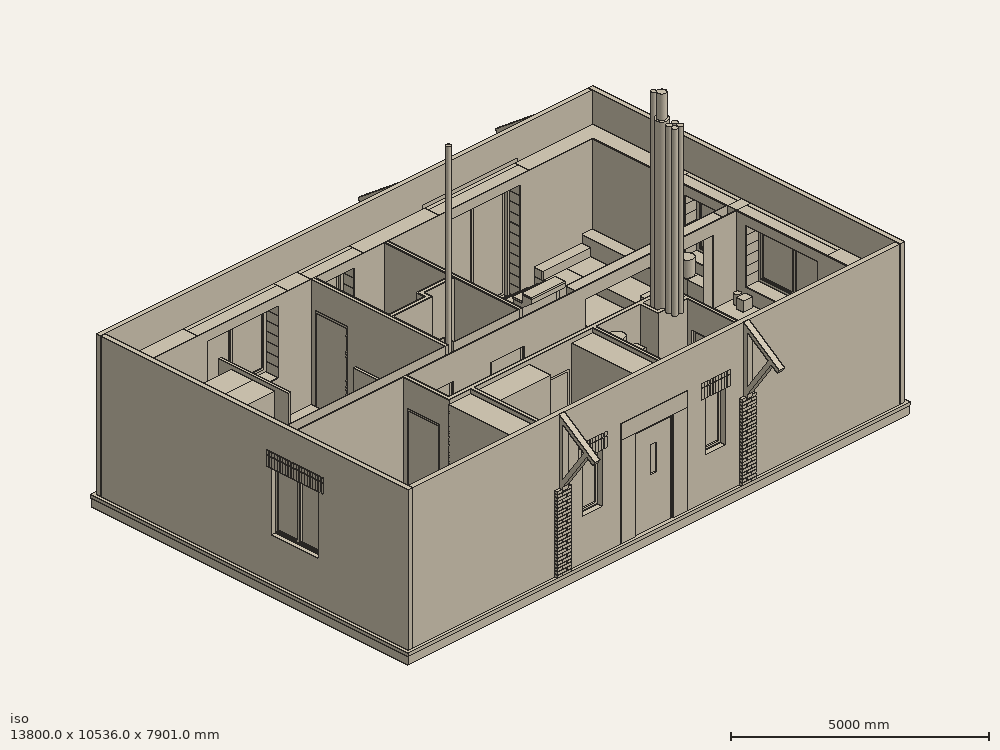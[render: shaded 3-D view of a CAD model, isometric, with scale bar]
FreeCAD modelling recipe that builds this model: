
FCSTD DOCUMENT  (FreeCAD 0.19R)
Label: 2bedr_dev_221121_BIM_mod
License: All rights reserved
LicenseURL: http://en.wikipedia.org/wiki/All_rights_reserved
objects: Part::Part2DObjectPython×664, Part::FeaturePython×646, App::FeaturePython×168, App::GeometryPython×80, App::DocumentObjectGroupPython×73, Sketcher::SketchObject×64, Part::MultiCommon×53, Part::Box×38, Part::Extrusion×36, Part::Cut×35, TechDraw::DrawViewAnnotation×32, Part::MultiFuse×26, App::MaterialObjectPython×21, TechDraw::DrawLeaderLine×17, Part::Feature×16, App::DocumentObjectGroup×11, TechDraw::DrawSVGTemplate×7, TechDraw::DrawPage×7, TechDraw::DrawViewImage×6, Part::Cylinder×5, +8 more types
note: 1669 computed .brp shape members not serialized (recipe doc carries the construction recipe); baked Part::Feature solids carry a one-line shape summary decoded from their .brp

FEATURE [Part::Part2DObjectPython] Rectangle2169  label="Д-105-254-001"  # Draft 2D object (typed FeaturePython)
  ChamferSize = 0
  Columns = 1
  FilletRadius = 0
  Height = 410
  Length = 1050
  MakeFace = true
  Placement = pos=(5670,-435,0) rot=(0,0,1;0rad)
  Rows = 1
FEATURE [Part::Part2DObjectPython] Rectangle2231  label="ОК-66-001"  # Draft 2D object (typed FeaturePython)
  ChamferSize = 0
  Columns = 1
  FilletRadius = 0
  Height = 410
  Length = 660
  MakeFace = true
  Placement = pos=(7555,-435,0) rot=(0,0,1;0rad)
  Rows = 1
FEATURE [Part::Part2DObjectPython] Rectangle2230  label="ОК-66-002"  # Draft 2D object (typed FeaturePython)
  ChamferSize = 0
  Columns = 1
  FilletRadius = 0
  Height = 410
  Length = 660
  MakeFace = true
  Placement = pos=(4175,-435,0) rot=(0,0,1;0rad)
  Rows = 1
FEATURE [App::FeaturePython] Dimension001  # Draft dimension (typed FeaturePython)
  Diameter = false
  Dimline = (13900,-300,0)
  Direction = (0,0,0)
  Distance = 7510
  End = (12550,7485,0)
  Normal = (0,0,1)
  Start = (12550,-25,0)
FEATURE [App::FeaturePython] Dimension  # Draft dimension (typed FeaturePython)
  Diameter = false
  Dimline = (13600,-1100,0)
  Direction = (0,0,0)
  Distance = 12580
  End = (12550,-10,0)
  Normal = (0,0,1)
  Start = (-30,-10,0)
FEATURE [Part::Part2DObjectPython] Rectangle2234  # Draft 2D object (typed FeaturePython)
  ChamferSize = 0
  Columns = 1
  FilletRadius = 0
  Height = 1500
  Length = 3000
  MakeFace = false
  Placement = pos=(5125,-1770,0) rot=(0,0,1;0rad)
  Rows = 1
FEATURE [Part::FeaturePython] Structure016  label="Проём-ОК-66-002"  # Arch/BIM 52 (typed FeaturePython)
  Base = -> Rectangle2230
  FaceMaker = 0
  Height = 1386
  HorizontalArea = 270600
  IfcData = complex_attributes={"OwnerHistory": {}, "IsNestedBy": {}, "IsDecomposedBy": {}, "IsDefinedBy": {}, "ObjectPlacement": {}, "Representation":... (+4 chars omitted)
  IfcType = 52
  Length = 0
  MoveBase = false
  MoveWithHost = false
  Nodes = (2) [(4618,-185,0),(4618,-185,1386)]
  NodesOffset = 0
  Normal = (0,0,0)
  PerimeterLength = 2140
  Placement = pos=(0,0,955) rot=(0,0,1;0rad)
  VerticalArea = 2966040
  Width = 100
FEATURE [Part::FeaturePython] Structure017  label="Проём-ОК-66-001"  # Arch/BIM 52 (typed FeaturePython)
  Base = -> Rectangle2231
  FaceMaker = 0
  Height = 1386
  HorizontalArea = 270600
  IfcData = complex_attributes={"OwnerHistory": {}, "IsNestedBy": {}, "IsDecomposedBy": {}, "IsDefinedBy": {}, "ObjectPlacement": {}, "Representation":... (+4 chars omitted)
  IfcType = 52
  Length = 0
  MoveBase = false
  MoveWithHost = false
  Nodes = (2) [(7885,-230,0),(7885,-230,1386)]
  NodesOffset = 0
  Normal = (0,0,0)
  PerimeterLength = 2140
  Placement = pos=(0,0,955) rot=(0,0,1;0rad)
  VerticalArea = 2966040
  Width = 100
FEATURE [Part::FeaturePython] Structure019  label="Проём-Д-105-254-001"  # Arch/BIM 52 (typed FeaturePython)
  Base = -> Rectangle2169
  FaceMaker = 0
  Height = 2541
  HorizontalArea = 430500
  IfcData = complex_attributes={"OwnerHistory": {}, "IsNestedBy": {}, "IsDecomposedBy": {}, "IsDefinedBy": {}, "ObjectPlacement": {}, "Representation":... (+4 chars omitted)
  IfcType = 52
  Length = 0
  MoveBase = false
  MoveWithHost = false
  Nodes = (2) [(6195,-230,0),(6195,-230,2541)]
  NodesOffset = 0
  Normal = (0,0,0)
  PerimeterLength = 2920
  Placement = pos=(0,0,-200) rot=(0,0,1;0rad)
  VerticalArea = 7419720
  Width = 100
FEATURE [Part::Part2DObjectPython] Line1049  # Draft 2D object (typed FeaturePython)
  ChamferSize = 0
  Closed = true
  End = (-50,3680,0)
  FilletRadius = 0
  Length = 12620
  MakeFace = false
  Placement = pos=(4290,10400,0) rot=(0,0,1;1.5708rad)
  Points = (2) [(-6720,-8280,0),(-6720,4340,0)]
  Start = (12570,3680,0)
  Subdivisions = 0
FEATURE [Part::Part2DObjectPython] Line1054  # Draft 2D object (typed FeaturePython)
  ChamferSize = 0
  Closed = true
  End = (4870,7505,0)
  FilletRadius = 0
  Length = 3700
  MakeFace = false
  Placement = pos=(9650,5690,0) rot=(0,0,1;0rad)
  Points = (2) [(-4780,-1885,0),(-4780,1815,0)]
  Start = (4870,3805,0)
  Subdivisions = 0
FEATURE [Sketcher::SketchObject] Sketch231  label="Профиль ПНО 120-8"
  FullyConstrained = false
  Placement = pos=(0,0,0) rot=(1,0,0;1.5708rad)
  sketch-geometry (19):
    g0: LineSegment StartX=0 StartY=0 StartZ=0 EndX=1190 EndY=0 EndZ=0
    g1: LineSegment StartX=1190 StartY=0 StartZ=0 EndX=1190 EndY=160 EndZ=0
    g2: LineSegment StartX=1190 StartY=160 StartZ=0 EndX=0 EndY=160 EndZ=0
    g3: LineSegment StartX=0 StartY=160 StartZ=0 EndX=0 EndY=0 EndZ=0
    g4: Circle CenterX=100 CenterY=80 CenterZ=0 NormalX=0 NormalY=0 NormalZ=1 AngleXU=0 Radius=50
    g5: Circle CenterX=240 CenterY=80 CenterZ=0 NormalX=0 NormalY=0 NormalZ=1 AngleXU=0 Radius=50
    g6: LineSegment StartX=100 StartY=80 StartZ=0 EndX=240 EndY=80 EndZ=0
    g7: Circle CenterX=380 CenterY=80 CenterZ=0 NormalX=0 NormalY=0 NormalZ=1 AngleXU=0 Radius=50
    g8: LineSegment StartX=240 StartY=80 StartZ=0 EndX=380 EndY=80 EndZ=0
    g9: Circle CenterX=520 CenterY=80 CenterZ=0 NormalX=0 NormalY=0 NormalZ=1 AngleXU=0 Radius=50
    g10: LineSegment StartX=380 StartY=80 StartZ=0 EndX=520 EndY=80 EndZ=0
    g11: Circle CenterX=660 CenterY=80 CenterZ=0 NormalX=0 NormalY=0 NormalZ=1 AngleXU=0 Radius=50
    g12: LineSegment StartX=520 StartY=80 StartZ=0 EndX=660 EndY=80 EndZ=0
    g13: Circle CenterX=800 CenterY=80 CenterZ=0 NormalX=0 NormalY=0 NormalZ=1 AngleXU=0 Radius=50
    g14: LineSegment StartX=660 StartY=80 StartZ=0 EndX=800 EndY=80 EndZ=0
    g15: Circle CenterX=940 CenterY=80 CenterZ=0 NormalX=0 NormalY=0 NormalZ=1 AngleXU=0 Radius=50
    g16: LineSegment StartX=800 StartY=80 StartZ=0 EndX=940 EndY=80 EndZ=0
    g17: Circle CenterX=1080 CenterY=80 CenterZ=0 NormalX=0 NormalY=0 NormalZ=1 AngleXU=0 Radius=50
    g18: LineSegment StartX=940 StartY=80 StartZ=0 EndX=1080 EndY=80 EndZ=0
  constraints (49):
    c: Coincident(g0,g1)
    c: Coincident(g1,g2)
    c: Coincident(g2,g3)
    c: Coincident(g3,g0)
    c: Horizontal(g0)
    c: Horizontal(g2)
    c: Vertical(g1)
    c: Vertical(g3)
    c: Coincident(g0,g-1)
    c: DistanceY(g3,g3) = 160
    c: DistanceX(g2,g2) = 1190
    c: Diameter(g4) = 100
    c: DistanceY(g4,g2) = 80
    c: Diameter(g5) = 100
    c: Coincident(g4,g6)
    c: Coincident(g5,g6)
    c: Distance(g6) = 140
    c: Angle(g6) = 0
    c: Diameter(g7) = 100
    c: Coincident(g5,g8)
    c: Coincident(g7,g8)
    c: Equal(g6,g8)
    c: Parallel(g8,g6)
    c: Diameter(g9) = 100
    c: Coincident(g7,g10)
    c: Coincident(g9,g10)
    c: Equal(g6,g10)
    c: Parallel(g10,g6)
    c: Diameter(g11) = 100
    c: Coincident(g9,g12)
    c: Coincident(g11,g12)
    c: Equal(g6,g12)
    c: Parallel(g12,g6)
    c: Diameter(g13) = 100
    c: Coincident(g11,g14)
    c: Coincident(g13,g14)
    c: Equal(g6,g14)
    c: Parallel(g14,g6)
    c: Diameter(g15) = 100
    c: Coincident(g13,g16)
    c: Coincident(g15,g16)
    c: Equal(g6,g16)
    c: Parallel(g16,g6)
    c: Diameter(g17) = 100
    c: Coincident(g15,g18)
    c: Coincident(g17,g18)
    c: Equal(g6,g18)
    c: Parallel(g18,g6)
    c: DistanceX(g2,g4) = 100
FEATURE [Part::Part2DObjectPython] Line1074  label="ось фундамента внутр.стены"  # Draft 2D object (typed FeaturePython)
  ChamferSize = 0
  Closed = true
  End = (3855,9350,0)
  FilletRadius = 0
  Length = 5200
  MakeFace = false
  Placement = pos=(2155,2900,0) rot=(0,0,1;1.5708rad)
  Points = (2) [(1250,-1700,0),(6450,-1700,0)]
  Start = (3855,4150,0)
  Subdivisions = 0
FEATURE [Part::FeaturePython] Wall037  label="фундамент внутр.стена01"  # Arch/BIM 166 (typed FeaturePython)
  Align = 2
  Area = 2.6e+06
  Base = -> Line1074
  BlockHeight = 0
  BlockLength = 0
  CountBroken = 0
  CountEntire = 0
  Face = 0
  Height = 500
  HorizontalArea = 1.3e+06
  IfcType = 166
  Joint = 0
  Length = 5200
  MakeBlocks = false
  MoveBase = false
  MoveWithHost = false
  Normal = (0,0,-1)
  OffsetFirst = 0
  OffsetSecond = 0
  PerimeterLength = 10900
  Placement = pos=(0,0,-180) rot=(0,0,1;0rad)
  PredefinedType = 0
  VerticalArea = 5.45e+06
  Width = 250
FEATURE [Part::FeaturePython] Wall046  label="утепл фунд. внешней.стены 002"  # Arch/BIM 166 (typed FeaturePython)
  Align = 1
  Area = 28488000
  BlockHeight = 600
  BlockLength = 600
  CountBroken = 1
  CountEntire = 0
  Face = 0
  Height = 600
  HorizontalArea = 3798400
  IfcType = 166
  Joint = 1
  Length = 47480
  MakeBlocks = true
  MoveBase = false
  MoveWithHost = false
  Normal = (0,0,-1)
  OffsetFirst = 0
  OffsetSecond = 0
  PerimeterLength = 95120
  Placement = pos=(0,0,-380) rot=(0,0,1;0rad)
  PredefinedType = 0
  VerticalArea = 57072000
  Width = 80
FEATURE [Part::FeaturePython] Wall047  label="утепл отмостки 001"  # Arch/BIM 166 (typed FeaturePython)
  Align = 1
  Area = 2374000
  BlockHeight = 600
  BlockLength = 1200
  CountBroken = 1
  CountEntire = 0
  Face = 0
  Height = 50
  HorizontalArea = 28488000
  IfcType = 166
  Joint = 1
  Length = 47480
  MakeBlocks = true
  MoveBase = false
  MoveWithHost = false
  Normal = (0,0,-1)
  Offset = 80
  OffsetFirst = 0
  OffsetSecond = 0
  PerimeterLength = 96160
  Placement = pos=(0,0,-930) rot=(0,0,1;0rad)
  PredefinedType = 0
  VerticalArea = 4808000
  Width = 600
FEATURE [Part::Part2DObjectPython] Circle071  # Draft 2D object (typed FeaturePython)
  FirstAngle = 0
  LastAngle = 0
  MakeFace = false
  Placement = pos=(8500,900,0) rot=(0,0,1;0rad)
  Radius = 580
FEATURE [Part::Part2DObjectPython] Circle072  # Draft 2D object (typed FeaturePython)
  FirstAngle = 0
  LastAngle = 0
  MakeFace = false
  Placement = pos=(8500,900,0) rot=(0,0,1;0rad)
  Radius = 500
FEATURE [Part::Part2DObjectPython] Circle073  label="люк_контур 001"  # Draft 2D object (typed FeaturePython)
  FirstAngle = 0
  LastAngle = 0
  MakeFace = false
  Placement = pos=(8500,1000,0) rot=(0,0,1;0rad)
  Radius = 350
FEATURE [Part::FeaturePython] Structure041  label="кольцо с днищем ДК-10.9 внутр."  # Arch/BIM 52 (typed FeaturePython)
  Base = -> Circle072
  FaceMaker = 0
  Height = 800
  HorizontalArea = 785398
  IfcData = complex_attributes={"OwnerHistory": {}, "IsNestedBy": {}, "IsDecomposedBy": {}, "IsDefinedBy": {}, "ObjectPlacement": {}, "Representation":... (+4 chars omitted)
  IfcType = 52
  Length = 0
  MoveBase = false
  MoveWithHost = false
  Nodes = (2) [(8500,900,0),(8500,900,-800)]
  NodesOffset = 0
  Normal = (0,0,-1)
  PerimeterLength = 3141.59
  Placement = pos=(0,0,-300) rot=(0,0,1;0rad)
  VerticalArea = 2.51327e+06
  Width = 100
FEATURE [Part::FeaturePython] Structure040  label="кольцо с днищем ДК-10.9 габарит"  # Arch/BIM 52 (typed FeaturePython)
  Base = -> Circle071
  FaceMaker = 0
  Height = 900
  HorizontalArea = 1.05683e+06
  IfcData = complex_attributes={"OwnerHistory": {}, "IsNestedBy": {}, "IsDecomposedBy": {}, "IsDefinedBy": {}, "ObjectPlacement": {}, "Representation":... (+4 chars omitted)
  IfcType = 52
  Length = 0
  MoveBase = false
  MoveWithHost = false
  Nodes = (2) [(8500,900,0),(8500,900,-900)]
  NodesOffset = 0
  Normal = (0,0,-1)
  PerimeterLength = 3644.25
  Placement = pos=(0,0,-300) rot=(0,0,1;0rad)
  Subtractions = -> [Structure041]
  VerticalArea = 5.7931e+06
  Width = 100
FEATURE [Part::FeaturePython] Structure044  label="люк контур Д700"  # Arch/BIM 52 (typed FeaturePython)
  Base = -> Circle073
  FaceMaker = 0
  Height = 300
  HorizontalArea = 384845
  IfcData = complex_attributes={"OwnerHistory": {}, "IsNestedBy": {}, "IsDecomposedBy": {}, "IsDefinedBy": {}, "ObjectPlacement": {}, "Representation":... (+4 chars omitted)
  IfcType = 52
  Length = 0
  MoveBase = false
  MoveWithHost = false
  Nodes = (2) [(8500,1000,0),(8500,1000,-300)]
  NodesOffset = 0
  Normal = (0,0,-1)
  PerimeterLength = 2199.11
  VerticalArea = 659734
  Width = 100
FEATURE [Part::FeaturePython] Structure043  label="крышка ПП10"  # Arch/BIM 52 (typed FeaturePython)
  Base = -> Circle071
  FaceMaker = 0
  Height = 100
  HorizontalArea = 671987
  IfcData = complex_attributes={"OwnerHistory": {}, "IsNestedBy": {}, "IsDecomposedBy": {}, "IsDefinedBy": {}, "ObjectPlacement": {}, "Representation":... (+4 chars omitted)
  IfcType = 52
  Length = 0
  MoveBase = false
  MoveWithHost = false
  Nodes = (2) [(8500,900,0),(8500,900,-100)]
  NodesOffset = 0
  Normal = (0,0,-1)
  PerimeterLength = 3644.25
  Placement = pos=(0,0,-200) rot=(0,0,1;0rad)
  Subtractions = -> [Structure044]
  VerticalArea = 584336
  Width = 100
FEATURE [App::GeometryPython] BuildingPart015  label="Колодец d1000 (ввод воды и канализации)"  # Arch/BIM 52 (typed FeaturePython)
  Area = 0
  Group = -> [Structure040,Structure043]
  Height = 0
  HeightPropagate = true
  IfcData = complex_attributes={"OwnerHistory": {}, "IsNestedBy": {}, "IsDecomposedBy": {}, "IsDefinedBy": {}, "ObjectPlacement": {}, "Representation":... (+4 chars omitted)
  IfcType = 52
  LevelOffset = 0
FEATURE [Part::Part2DObjectPython] Line1077  # Draft 2D object (typed FeaturePython)
  ChamferSize = 0
  Closed = true
  End = (-50,-45,0)
  FilletRadius = 0
  Length = 12620
  MakeFace = false
  Placement = pos=(12060,265,0) rot=(0,0,1;0rad)
  Points = (2) [(510,-310,0),(-12110,-310,0)]
  Start = (12570,-45,0)
  Subdivisions = 0
FEATURE [Part::Part2DObjectPython] Rectangle2286  # Draft 2D object (typed FeaturePython)
  ChamferSize = 0
  Columns = 1
  FilletRadius = 0
  Height = 5190
  Length = 9350
  MakeFace = false
  Placement = pos=(1950,2210,0) rot=(0,0,1;0rad)
  Rows = 1
FEATURE [Part::FeaturePython] Structure049  label="вычитаемый объём 002"  # Arch/BIM 52 (typed FeaturePython)
  FaceMaker = 0
  Height = 4000
  HorizontalArea = 3.20922e+07
  IfcData = complex_attributes={"OwnerHistory": {}, "IsNestedBy": {}, "IsDecomposedBy": {}, "IsDefinedBy": {}, "ObjectPlacement": {}, "Representation":... (+4 chars omitted)
  IfcType = 52
  Length = 0
  MoveBase = false
  MoveWithHost = false
  Nodes = (2) [(506.667,3830,0),(506.667,3830,4000)]
  NodesOffset = 0
  Normal = (0,0,1)
  PerimeterLength = 27353
  Placement = pos=(0,0,3160) rot=(0,0,1;0rad)
  VerticalArea = 1.09412e+08
  Width = 100
FEATURE [Part::FeaturePython] Structure050  label="вычитаемый объём 004"  # Arch/BIM 52 (typed FeaturePython)
  FaceMaker = 0
  Height = 4000
  HorizontalArea = 5.56586e+07
  IfcData = complex_attributes={"OwnerHistory": {}, "IsNestedBy": {}, "IsDecomposedBy": {}, "IsDefinedBy": {}, "ObjectPlacement": {}, "Representation":... (+4 chars omitted)
  IfcType = 52
  Length = 0
  MoveBase = false
  MoveWithHost = false
  Nodes = (2) [(6040,886.738,0),(6040,886.738,4000)]
  NodesOffset = 0
  Normal = (0,0,1)
  PerimeterLength = 35673
  Placement = pos=(0,0,3160) rot=(0,0,1;0rad)
  VerticalArea = 1.42692e+08
  Width = 100
FEATURE [Part::FeaturePython] Structure051  label="вычитаемый объём 003"  # Arch/BIM 52 (typed FeaturePython)
  FaceMaker = 0
  Height = 4000
  HorizontalArea = 32092225
  IfcData = complex_attributes={"OwnerHistory": {}, "IsNestedBy": {}, "IsDecomposedBy": {}, "IsDefinedBy": {}, "ObjectPlacement": {}, "Representation":... (+4 chars omitted)
  IfcType = 52
  Length = 0
  MoveBase = false
  MoveWithHost = false
  Nodes = (2) [(12481.7,4805,0),(12481.7,4805,4000)]
  NodesOffset = 0
  Normal = (0,0,1)
  PerimeterLength = 27353
  Placement = pos=(0,0,3160) rot=(0,0,1;0rad)
  VerticalArea = 1.09412e+08
  Width = 100
FEATURE [App::FeaturePython] Dimension003  # Draft dimension (typed FeaturePython)
  Diameter = false
  Dimline = (14100,-1000,0)
  Direction = (0,0,0)
  Distance = 8570
  End = (13080,8015,0)
  Normal = (0,0,1)
  Start = (13080,-555,0)
FEATURE [Sketcher::SketchObject] Sketch248
  FullyConstrained = true
  Placement = pos=(3860,3535,0) rot=(1,0,0;1.5708rad)
  sketch-geometry (8):
    g0: LineSegment StartX=0 StartY=0 StartZ=0 EndX=900 EndY=0 EndZ=0
    g1: LineSegment StartX=900 StartY=0 StartZ=0 EndX=900 EndY=2150 EndZ=0
    g2: LineSegment StartX=900 StartY=2150 StartZ=0 EndX=0 EndY=2150 EndZ=0
    g3: LineSegment StartX=0 StartY=2150 StartZ=0 EndX=0 EndY=0 EndZ=0
    g4: LineSegment StartX=50 StartY=0 StartZ=0 EndX=850 EndY=0 EndZ=0
    g5: LineSegment StartX=850 StartY=0 StartZ=0 EndX=850 EndY=2100 EndZ=0
    g6: LineSegment StartX=850 StartY=2100 StartZ=0 EndX=50 EndY=2100 EndZ=0
    g7: LineSegment StartX=50 StartY=2100 StartZ=0 EndX=50 EndY=0 EndZ=0
  constraints (23):
    c: Coincident(g0,g1)
    c: Coincident(g1,g2)
    c: Coincident(g2,g3)
    c: Coincident(g3,g0)
    c: Horizontal(g0)
    c: Horizontal(g2)
    c: Vertical(g1)
    c: Vertical(g3)
    c: Coincident(g4,g5)
    c: Coincident(g5,g6)
    c: Coincident(g6,g7)
    c: Coincident(g7,g4)
    c: Horizontal(g4)
    c: Horizontal(g6)
    c: Vertical(g5)
    c: Vertical(g7)
    c: DistanceY(g1) = 2150  'Height'
    c: DistanceX(g0) = 900  'Width'
    c: DistanceY(g6,g2) = 50  'Frame1'
    c: DistanceX(g2,g6) = 50  'Frame2'
    c: DistanceX(g4,g0) = 50  'Frame3'
    c: DistanceY(g0,g4) = 0
    c: Coincident(g0,g-1)
FEATURE [Sketcher::SketchObject] Sketch249  label="Профиль ПНО 100-6"
  FullyConstrained = false
  Placement = pos=(0,0,0) rot=(1,0,0;1.5708rad)
  sketch-geometry (15):
    g0: LineSegment StartX=0 StartY=0 StartZ=0 EndX=990 EndY=0 EndZ=0
    g1: LineSegment StartX=990 StartY=0 StartZ=0 EndX=990 EndY=160 EndZ=0
    g2: LineSegment StartX=990 StartY=160 StartZ=0 EndX=0 EndY=160 EndZ=0
    g3: LineSegment StartX=0 StartY=160 StartZ=0 EndX=0 EndY=0 EndZ=0
    g4: Circle CenterX=145 CenterY=80 CenterZ=0 NormalX=0 NormalY=0 NormalZ=1 AngleXU=0 Radius=50
    g5: Circle CenterX=285 CenterY=80 CenterZ=0 NormalX=0 NormalY=0 NormalZ=1 AngleXU=0 Radius=50
    g6: LineSegment StartX=145 StartY=80 StartZ=0 EndX=285 EndY=80 EndZ=0
    g7: Circle CenterX=425 CenterY=80 CenterZ=0 NormalX=0 NormalY=0 NormalZ=1 AngleXU=0 Radius=50
    g8: LineSegment StartX=285 StartY=80 StartZ=0 EndX=425 EndY=80 EndZ=0
    g9: Circle CenterX=565 CenterY=80 CenterZ=0 NormalX=0 NormalY=0 NormalZ=1 AngleXU=0 Radius=50
    g10: LineSegment StartX=425 StartY=80 StartZ=0 EndX=565 EndY=80 EndZ=0
    g11: Circle CenterX=705 CenterY=80 CenterZ=0 NormalX=0 NormalY=0 NormalZ=1 AngleXU=0 Radius=50
    g12: LineSegment StartX=565 StartY=80 StartZ=0 EndX=705 EndY=80 EndZ=0
    g13: Circle CenterX=845 CenterY=80 CenterZ=0 NormalX=0 NormalY=0 NormalZ=1 AngleXU=0 Radius=50
    g14: LineSegment StartX=705 StartY=80 StartZ=0 EndX=845 EndY=80 EndZ=0
  constraints (39):
    c: Coincident(g0,g1)
    c: Coincident(g1,g2)
    c: Coincident(g2,g3)
    c: Coincident(g3,g0)
    c: Horizontal(g0)
    c: Horizontal(g2)
    c: Vertical(g1)
    c: Vertical(g3)
    c: Coincident(g0,g-1)
    c: DistanceY(g3,g3) = 160
    c: DistanceX(g2,g2) = 990
    c: Diameter(g4) = 100
    c: DistanceY(g4,g2) = 80
    c: Diameter(g5) = 100
    c: Coincident(g4,g6)
    c: Coincident(g5,g6)
    c: Distance(g6) = 140
    c: Angle(g6) = 0
    c: Diameter(g7) = 100
    c: Coincident(g5,g8)
    c: Coincident(g7,g8)
    c: Equal(g6,g8)
    c: Parallel(g8,g6)
    c: Diameter(g9) = 100
    c: Coincident(g7,g10)
    c: Coincident(g9,g10)
    c: Equal(g6,g10)
    c: Parallel(g10,g6)
    c: Diameter(g11) = 100
    c: Coincident(g9,g12)
    c: Coincident(g11,g12)
    c: Equal(g6,g12)
    c: Parallel(g12,g6)
    c: Diameter(g13) = 100
    c: Coincident(g11,g14)
    c: Coincident(g13,g14)
    c: Equal(g6,g14)
    c: Parallel(g14,g6)
    c: DistanceX(g2,g4) = 145
FEATURE [Part::Part2DObjectPython] Wire460  label="границы участка"  # Draft 2D object (typed FeaturePython)
  ChamferSize = 0
  Closed = true
  End = (26167.8,29983.2,0)
  FilletRadius = 0
  Length = 156987
  MakeFace = false
  Placement = pos=(24404.1,-9481.8,0) rot=(0,0,1;0.025758rad)
  Points = (7) [(0,0,0),(-3118.22,176.296,0),(-9989.98,2199.83,0),(-22349.9,2518.26,0),(-33551.4,825.818,0),(-40981.4,39865.2,0),(2779.54,39406.5,0)]
  Start = (24404.1,-9481.8,0)
  Subdivisions = 0
FEATURE [Part::Part2DObjectPython] Rectangle2365  label="зона парковки-навес"  # Draft 2D object (typed FeaturePython)
  ChamferSize = 0
  Columns = 1
  FilletRadius = 0
  Height = 7000
  Length = 7000
  MakeFace = false
  Placement = pos=(17916.6,-6918.81,0) rot=(0,0,-1;0.068796rad)
  Rows = 1
FEATURE [Part::Part2DObjectPython] Wire463  label="граница по ограждению"  # Draft 2D object (typed FeaturePython)
  ChamferSize = 0
  Closed = true
  End = (5754.6,-6612.02,0)
  FilletRadius = 0
  Length = 153279
  MakeFace = false
  Placement = pos=(24847.4,-8209.78,0) rot=(0,0,1;0rad)
  Points = (6) [(14.0233,-1.17368,0),(2632.1,37116.3,0),(-41128.8,37575,0),(-34003,133.748,0),(-24492.8,1579.34,0),(-19092.8,1597.76,0)]
  Start = (24861.5,-8210.95,0)
  Subdivisions = 0
FEATURE [Part::FeaturePython] Structure133  label="грунт в границах участка"  # Arch/BIM 52 (typed FeaturePython)
  Base = -> Wire460
  FaceMaker = 0
  Height = 1000
  HorizontalArea = 1.47224e+09
  IfcData = complex_attributes={"OwnerHistory": {}, "IsNestedBy": {}, "IsDecomposedBy": {}, "IsDefinedBy": {}, "ObjectPlacement": {}, "Representation":... (+4 chars omitted)
  IfcType = 52
  Length = 0
  MoveBase = false
  MoveWithHost = false
  Nodes = (2) [(5892.5,11504.2,0),(5892.5,11504.2,-1000)]
  NodesOffset = 0
  Normal = (0,0,-1)
  PerimeterLength = 156987
  Placement = pos=(0,0,-320) rot=(0,0,1;0rad)
  VerticalArea = 1.56987e+08
  Width = 100
FEATURE [Part::Part2DObjectPython] Wire464  label="мауэрлат003"  # Draft 2D object (typed FeaturePython)
  ChamferSize = 0
  Closed = true
  End = (14568.5,-7412.72,0)
  FilletRadius = 0
  Length = 30000
  MakeFace = false
  Placement = pos=(20304,-1451.15,0) rot=(0,0,-1;0.229406rad)
  Points = (4) [(3770.46,-7109.62,0),(3770.46,-109.624,0),(-4229.54,-109.624,0),(-4229.54,-7109.62,0)]
  Start = (22359,-9231.91,0)
  Subdivisions = 0
FEATURE [Part::Part2DObjectPython] Rectangle2375  # Draft 2D object (typed FeaturePython)
  ChamferSize = 0
  Columns = 1
  FilletRadius = 0
  Height = 150
  Length = 800
  MakeFace = true
  Placement = pos=(-1461.06,-5083.09,0) rot=(0,0,-1;1.39508rad)
  Rows = 1
FEATURE [Part::Part2DObjectPython] Rectangle2376  # Draft 2D object (typed FeaturePython)
  ChamferSize = 0
  Columns = 1
  FilletRadius = 0
  Height = 150
  Length = 500
  MakeFace = true
  Placement = pos=(-6959.67,-6719.51,0) rot=(0,0,1;1.74651rad)
  Rows = 1
FEATURE [Part::Part2DObjectPython] Rectangle2377  # Draft 2D object (typed FeaturePython)
  ChamferSize = 0
  Columns = 1
  FilletRadius = 0
  Height = 2300
  Length = 6000
  MakeFace = false
  Placement = pos=(-1444.48,-4318.42,0) rot=(0,0,1;3.31731rad)
  Rows = 1
FEATURE [Part::FeaturePython] Roof011  label="Навес над парковкой"  # Arch/BIM 113 (typed FeaturePython)
  Angles = [90,10,90,10]
  Base = -> Wire464
  BorderLength = 0
  Face = 0
  Flip = false
  Heights = [0,617.144,0,617.144]
  HorizontalArea = 5.6e+07
  IdRel = [0,0,0,0]
  IfcType = 113
  MoveBase = false
  MoveWithHost = false
  Overhang = [0,0,0,0]
  PerimeterLength = 30000
  Placement = pos=(0,0,2500) rot=(0,0,1;0rad)
  PredefinedType = 0
  RidgeLength = 0
  Runs = [0,3500,0,3500]
  Thickness = [150,150,150,150]
  VerticalArea = 7.00644e+06
FEATURE [Part::FeaturePython] Structure135  label="Structure134"  # Arch/BIM 52 (typed FeaturePython)
  Base = -> Rectangle2375
  FaceMaker = 0
  Height = 1800
  HorizontalArea = 120000
  IfcData = complex_attributes={"OwnerHistory": {}, "IsNestedBy": {}, "IsDecomposedBy": {}, "IsDefinedBy": {}, "ObjectPlacement": {}, "Representation":... (+4 chars omitted)
  IfcType = 52
  Length = 0
  MoveBase = false
  MoveWithHost = false
  Nodes = (2) [(-35.6948,-25773.1,0),(-35.6948,-25773.1,1800)]
  NodesOffset = 0
  Normal = (0,0,0)
  PerimeterLength = 1900
  VerticalArea = 3.42e+06
  Width = 100
FEATURE [Part::FeaturePython] Structure136  label="Structure135"  # Arch/BIM 52 (typed FeaturePython)
  Base = -> Rectangle2376
  FaceMaker = 0
  Height = 600
  HorizontalArea = 75000
  IfcData = complex_attributes={"OwnerHistory": {}, "IsNestedBy": {}, "IsDecomposedBy": {}, "IsDefinedBy": {}, "ObjectPlacement": {}, "Representation":... (+4 chars omitted)
  IfcType = 52
  Length = 0
  MoveBase = false
  MoveWithHost = false
  Nodes = (2) [(1351.07,-25965.1,0),(1351.07,-25965.1,600)]
  NodesOffset = 0
  Normal = (0,0,0)
  PerimeterLength = 1300
  Placement = pos=(0,-4e-15,1240) rot=(0,0,1;0rad)
  VerticalArea = 780000
  Width = 100
FEATURE [Part::FeaturePython] Wall097  label="Wall007"  # Arch/BIM 166 (typed FeaturePython)
  Align = 1
  Area = 4.067e+07
  Base = -> Rectangle2377
  BlockHeight = 0
  BlockLength = 0
  CountBroken = 0
  CountEntire = 0
  Face = 0
  Height = 2450
  HorizontalArea = 2.595e+06
  IfcType = 166
  Joint = 0
  Length = 16600
  MakeBlocks = false
  MoveBase = false
  MoveWithHost = false
  Normal = (0,0,0)
  OffsetFirst = 0
  OffsetSecond = 0
  PerimeterLength = 12600
  Placement = pos=(0,0,-150) rot=(0,0,1;0rad)
  PredefinedType = 0
  Subtractions = -> [Structure136,Structure135]
  VerticalArea = 7.564e+07
  Width = 150
FEATURE [Sketcher::SketchObject] Sketch250  label="Габарит человека"
  FullyConstrained = false
  Placement = pos=(0,0,0) rot=(1,0,0;1.5708rad)
  sketch-geometry (21):
    g0: LineSegment StartX=-250 StartY=0 StartZ=0 EndX=250 EndY=0 EndZ=0
    g1: LineSegment StartX=250 StartY=0 StartZ=0 EndX=250 EndY=1750 EndZ=0
    g2: LineSegment StartX=250 StartY=1750 StartZ=0 EndX=-250 EndY=1750 EndZ=0
    g3: LineSegment StartX=-250 StartY=1750 StartZ=0 EndX=-250 EndY=0 EndZ=0
    g4: LineSegment StartX=85 StartY=1500 StartZ=0 EndX=85 EndY=1750 EndZ=0
    g5: LineSegment StartX=85 StartY=1750 StartZ=0 EndX=-85 EndY=1750 EndZ=0
    g6: LineSegment StartX=-85 StartY=1750 StartZ=0 EndX=-85 EndY=1500 EndZ=0
    g7: LineSegment StartX=250 StartY=750 StartZ=0 EndX=250 EndY=1500 EndZ=0
    g8: LineSegment StartX=-250 StartY=1500 StartZ=0 EndX=-250 EndY=750 EndZ=0
    g9: LineSegment StartX=-110 StartY=0 StartZ=0 EndX=110 EndY=0 EndZ=0
    g10: LineSegment StartX=110 StartY=0 StartZ=0 EndX=175 EndY=750 EndZ=0
    g11: LineSegment StartX=-175 StartY=750 StartZ=0 EndX=-110 EndY=0 EndZ=0
    g12: GeomPoint X=0 Y=750 Z=0
    g13: GeomPoint X=-110 Y=0 Z=0
    g14: GeomPoint X=110 Y=0 Z=0
    g15: GeomPoint X=175 Y=750 Z=0
    g16: GeomPoint X=-175 Y=750 Z=0
    g17: LineSegment StartX=-250 StartY=1500 StartZ=0 EndX=-85 EndY=1500 EndZ=0
    g18: LineSegment StartX=85 StartY=1500 StartZ=0 EndX=250 EndY=1500 EndZ=0
    g19: LineSegment StartX=-250 StartY=750 StartZ=0 EndX=-175 EndY=750 EndZ=0
    g20: LineSegment StartX=175 StartY=750 StartZ=0 EndX=250 EndY=750 EndZ=0
  constraints (50):
    c: Coincident(g0,g1)
    c: Coincident(g1,g2)
    c: Coincident(g2,g3)
    c: Coincident(g3,g0)
    c: Horizontal(g0)
    c: Horizontal(g2)
    c: Vertical(g1)
    c: Vertical(g3)
    c: Symmetric(g0,g0,g-1)
    c: DistanceX(g2,g2) = 500
    c: DistanceY(g1,g1) = 1750
    c: Coincident(g4,g5)
    c: Coincident(g5,g6)
    c: Horizontal(g5)
    c: Vertical(g4)
    c: Vertical(g6)
    c: Vertical(g7)
    c: Vertical(g8)
    c: Coincident(g9,g10)
    c: DistanceX(g5,g5) = 170
    c: DistanceY(g4,g4) = 250
    c: PointOnObject(g4,g2)
    c: Symmetric(g6,g4,g-2)
    c: PointOnObject(g8,g3)
    c: PointOnObject(g7,g1)
    c: Coincident(g9,g11)
    c: DistanceX(g9,g9) = 220
    c: DistanceY(g0,g7) = 750
    c: PointOnObject(g12,g-2)
    c: Coincident(g13,g9)
    c: Coincident(g14,g9)
    c: Symmetric(g13,g14,g-2)
    c: PointOnObject(g14,g0)
    c: Coincident(g15,g10)
    c: Symmetric(g15,g16,g-2)
    c: DistanceX(g16,g15) = 350
    c: Coincident(g17,g8)
    c: Coincident(g17,g6)
    c: Horizontal(g17)
    c: Coincident(g18,g4)
    c: Coincident(g18,g7)
    c: Horizontal(g18)
    c: Coincident(g19,g8)
    c: Coincident(g19,g11)
    c: Horizontal(g19)
    c: Coincident(g20,g10)
    c: Coincident(g20,g7)
    c: Horizontal(g20)
    c: Equal(g19,g20)
    c: Equal(g11,g10)
FEATURE [Part::Extrusion] Extrude007  label="Габарит человека 001"
  Base = -> Sketch250
  Dir = (0,-1,2e-16)
  DirMode = 2
  FaceMakerClass = Part::FaceMakerBullseye
  LengthFwd = 290
  LengthRev = 0
  Placement = pos=(7375,4690,0) rot=(0,0,1;0rad)
  Solid = true
  Symmetric = false
FEATURE [Part::Extrusion] Extrude008  label="Габарит человека 002"
  Base = -> Sketch250
  Dir = (0,-1,2e-16)
  DirMode = 2
  FaceMakerClass = Part::FaceMakerBullseye
  LengthFwd = 290
  LengthRev = 0
  Placement = pos=(6300,5845,0) rot=(0,0,1;0rad)
  Solid = true
  Symmetric = false
FEATURE [Part::Part2DObjectPython] Rectangle2381  # Draft 2D object (typed FeaturePython)
  ChamferSize = 0
  Columns = 1
  FilletRadius = 0
  Height = 1250
  Length = 2500
  MakeFace = false
  Placement = pos=(5375,-1520,0) rot=(0,0,1;0rad)
  Rows = 1
FEATURE [Part::FeaturePython] Structure140  label="габарит крыльца001"  # Arch/BIM 52 (typed FeaturePython)
  Base = -> Rectangle2381
  FaceMaker = 0
  Height = 180
  HorizontalArea = 3125000
  IfcData = complex_attributes={"OwnerHistory": {}, "IsNestedBy": {}, "IsDecomposedBy": {}, "IsDefinedBy": {}, "ObjectPlacement": {}, "Representation":... (+4 chars omitted)
  IfcType = 52
  Length = 0
  MoveBase = false
  MoveWithHost = false
  Nodes = (2) [(5975,-1250,0),(5975,-1250,-350)]
  NodesOffset = 0
  Normal = (0,0,-1)
  PerimeterLength = 7500
  Placement = pos=(0,0,-40) rot=(0,0,1;0rad)
  VerticalArea = 1350000
  Width = 100
FEATURE [Part::FeaturePython] Structure029  label="габарит крыльца"  # Arch/BIM 52 (typed FeaturePython)
  Additions = -> [Structure140]
  Base = -> Rectangle2234
  FaceMaker = 0
  Height = 180
  HorizontalArea = 4500000
  IfcData = complex_attributes={"OwnerHistory": {}, "IsNestedBy": {}, "IsDecomposedBy": {}, "IsDefinedBy": {}, "ObjectPlacement": {}, "Representation":... (+4 chars omitted)
  IfcType = 52
  Length = 0
  MoveBase = false
  MoveWithHost = false
  Nodes = (2) [(5975,-1250,0),(5975,-1250,-350)]
  NodesOffset = 0
  Normal = (0,0,-1)
  PerimeterLength = 9000
  Placement = pos=(0,0,-220) rot=(0,0,1;0rad)
  VerticalArea = 2970000
  Width = 100
FEATURE [Part::Part2DObjectPython] Rectangle2382  label="террасса"  # Draft 2D object (typed FeaturePython)
  ChamferSize = 0
  Columns = 1
  FilletRadius = 0
  Height = 2400
  Length = 10500
  MakeFace = false
  Placement = pos=(1255,9880,0) rot=(0,0,1;0rad)
  Rows = 1
FEATURE [Part::FeaturePython] Structure028  label="габарит терассы"  # Arch/BIM 52 (typed FeaturePython)
  Base = -> Rectangle2382
  FaceMaker = 0
  Height = 400
  HorizontalArea = 25200000
  IfcData = complex_attributes={"OwnerHistory": {}, "IsNestedBy": {}, "IsDecomposedBy": {}, "IsDefinedBy": {}, "ObjectPlacement": {}, "Representation":... (+4 chars omitted)
  IfcType = 52
  Length = 0
  MoveBase = false
  MoveWithHost = false
  Nodes = (2) [(6755,9400,0),(6755,9400,-400)]
  NodesOffset = 0
  Normal = (0,0,-1)
  PerimeterLength = 25800
  Placement = pos=(0,0,-40) rot=(0,0,1;0rad)
  VerticalArea = 10320000
  Width = 100
FEATURE [App::GeometryPython] BuildingPart035  label="Внешние элементы"  # Arch/BIM 52 (typed FeaturePython)
  Area = 0
  Group = -> [Structure028,Structure029]
  Height = 0
  HeightPropagate = true
  IfcData = complex_attributes={"OwnerHistory": {}, "IsNestedBy": {}, "IsDecomposedBy": {}, "IsDefinedBy": {}, "ObjectPlacement": {}, "Representation":... (+4 chars omitted)
  IfcType = 52
  LevelOffset = 0
FEATURE [Image::ImagePlane] ImagePlane  label="План участка"
  Placement = pos=(1568.88,19724.2,-450) rot=(0,0,1;3.16731rad)
  XSize = 103541
  YSize = 98696.8
FEATURE [Sketcher::SketchObject] Sketch251
  FullyConstrained = true
  Placement = pos=(3400,2535,0) rot=(0.57735,0.57735,0.57735;2.0944rad)
  sketch-geometry (8):
    g0: LineSegment StartX=0 StartY=0 StartZ=0 EndX=900 EndY=0 EndZ=0
    g1: LineSegment StartX=900 StartY=0 StartZ=0 EndX=900 EndY=2150 EndZ=0
    g2: LineSegment StartX=900 StartY=2150 StartZ=0 EndX=0 EndY=2150 EndZ=0
    g3: LineSegment StartX=0 StartY=2150 StartZ=0 EndX=0 EndY=0 EndZ=0
    g4: LineSegment StartX=50 StartY=0 StartZ=0 EndX=850 EndY=0 EndZ=0
    g5: LineSegment StartX=850 StartY=0 StartZ=0 EndX=850 EndY=2100 EndZ=0
    g6: LineSegment StartX=850 StartY=2100 StartZ=0 EndX=50 EndY=2100 EndZ=0
    g7: LineSegment StartX=50 StartY=2100 StartZ=0 EndX=50 EndY=0 EndZ=0
  constraints (23):
    c: Coincident(g0,g1)
    c: Coincident(g1,g2)
    c: Coincident(g2,g3)
    c: Coincident(g3,g0)
    c: Horizontal(g0)
    c: Horizontal(g2)
    c: Vertical(g1)
    c: Vertical(g3)
    c: Coincident(g4,g5)
    c: Coincident(g5,g6)
    c: Coincident(g6,g7)
    c: Coincident(g7,g4)
    c: Horizontal(g4)
    c: Horizontal(g6)
    c: Vertical(g5)
    c: Vertical(g7)
    c: DistanceY(g1) = 2150  'Height'
    c: DistanceX(g0) = 900  'Width'
    c: DistanceY(g6,g2) = 50  'Frame1'
    c: DistanceX(g2,g6) = 50  'Frame2'
    c: DistanceX(g4,g0) = 50  'Frame3'
    c: DistanceY(g0,g4) = 0
    c: Coincident(g0,g-1)
FEATURE [App::FeaturePython] Dimension004  # Draft dimension (typed FeaturePython)
  Diameter = false
  Dimline = (-1600,-1000,0)
  Direction = (0,0,0)
  Distance = 3915
  End = (-1836.7,3680,0)
  Normal = (0,0,1)
  Start = (-1836.7,-235,0)
FEATURE [App::FeaturePython] Dimension006  # Draft dimension (typed FeaturePython)
  Diameter = false
  Dimline = (-1600,3680,0)
  Direction = (0,0,0)
  Distance = 4015
  End = (-1836.7,7695,0)
  Normal = (0,0,1)
  Start = (-1836.7,3680,0)
FEATURE [App::FeaturePython] Dimension007  # Draft dimension (typed FeaturePython)
  Diameter = false
  Dimline = (-600,9000,0)
  Direction = (0,0,0)
  Distance = 5110
  End = (4870,9506.46,0)
  Normal = (0,0,1)
  Start = (-240,9506.46,0)
FEATURE [App::FeaturePython] Dimension009  # Draft dimension (typed FeaturePython)
  Diameter = false
  Dimline = (7910,9000,0)
  Direction = (0,0,0)
  Distance = 1020
  End = (7910,9506.46,0)
  Normal = (0,0,1)
  Start = (6890,9506.46,0)
FEATURE [Part::Part2DObjectPython] Rectangle2392  # Draft 2D object (typed FeaturePython)
  ChamferSize = 0
  Columns = 1
  FilletRadius = 50
  Height = 400
  Length = 400
  MakeFace = false
  Placement = pos=(12050,2061,0) rot=(0,0,1;0rad)
  Rows = 1
FEATURE [Part::Part2DObjectPython] Rectangle2573  label="четверть_530-001"  # Draft 2D object (typed FeaturePython)
  ChamferSize = 0
  Columns = 1
  FilletRadius = 0
  Height = 120
  Length = 530
  MakeFace = true
  Placement = pos=(4240,-555,0) rot=(0,0,1;0rad)
  Rows = 1
FEATURE [Part::Part2DObjectPython] Rectangle2571  label="четверть_105-001"  # Draft 2D object (typed FeaturePython)
  ChamferSize = 0
  Columns = 1
  FilletRadius = 0
  Height = 120
  Length = 1050
  MakeFace = true
  Placement = pos=(5670,-555,0) rot=(0,0,1;0rad)
  Rows = 1
FEATURE [Part::FeaturePython] Structure148  label="Проём_четв._031"  # Arch/BIM 52 (typed FeaturePython)
  Base = -> Rectangle2571
  FaceMaker = 0
  Height = 2315
  HorizontalArea = 126000
  IfcData = complex_attributes={"OwnerHistory": {}, "IsNestedBy": {}, "IsDecomposedBy": {}, "IsDefinedBy": {}, "ObjectPlacement": {}, "Representation":... (+4 chars omitted)
  IfcType = 52
  Length = 0
  MoveBase = false
  MoveWithHost = false
  Nodes = (2) [(5775,-395,0),(5775,-395,2335)]
  NodesOffset = 0
  Normal = (0,0,0)
  PerimeterLength = 2340
  Placement = pos=(0,0,-40) rot=(0,0,1;0rad)
  VerticalArea = 5417100
  Width = 100
FEATURE [Part::Part2DObjectPython] Rectangle2579  label="четверть_183-001"  # Draft 2D object (typed FeaturePython)
  ChamferSize = 0
  Columns = 1
  FilletRadius = 0
  Height = 120
  Length = 1830
  MakeFace = true
  Placement = pos=(12960,3215,0) rot=(0,0,-1;1.5708rad)
  Rows = 1
FEATURE [Part::Part2DObjectPython] Rectangle2577  label="четверть_790-001"  # Draft 2D object (typed FeaturePython)
  ChamferSize = 0
  Columns = 1
  FilletRadius = 0
  Height = 120
  Length = 790
  MakeFace = true
  Placement = pos=(12960,4905,0) rot=(0,0,-1;1.5708rad)
  Rows = 1
FEATURE [Part::Part2DObjectPython] Line1184  label="Line1179"  # Draft 2D object (typed FeaturePython)
  ChamferSize = 0
  Closed = false
  End = (8280,-555,0)
  FilletRadius = 0
  Length = 790
  MakeFace = true
  Placement = pos=(7490,-555,0) rot=(0,0,-1;0rad)
  Points = (2) [(0,0,0),(790,3.41061e-13,0)]
  Start = (7490,-555,0)
  Subdivisions = 0
FEATURE [Part::Part2DObjectPython] Line1186  # Draft 2D object (typed FeaturePython)
  ChamferSize = 0
  Closed = true
  End = (6070,8015,0)
  FilletRadius = 0
  Length = 4170
  MakeFace = true
  Placement = pos=(1900,8015,0) rot=(0,0,1;0rad)
  Points = (2) [(0,0,0),(4170,0,0)]
  Start = (1900,8015,0)
  Subdivisions = 0
FEATURE [Part::Part2DObjectPython] Line1187  # Draft 2D object (typed FeaturePython)
  ChamferSize = 0
  Closed = true
  End = (13080,5035,0)
  FilletRadius = 0
  Length = 3780
  MakeFace = true
  Placement = pos=(13080,1255,0) rot=(0,0,1;1.5708rad)
  Points = (2) [(0,0,0),(3780,9.09495e-12,0)]
  Start = (13080,1255,0)
  Subdivisions = 0
FEATURE [Part::Part2DObjectPython] Rectangle2580  label="четверть_530-002"  # Draft 2D object (typed FeaturePython)
  ChamferSize = 0
  Columns = 1
  FilletRadius = 0
  Height = 120
  Length = 530
  MakeFace = true
  Placement = pos=(7620,-555,0) rot=(0,0,1;0rad)
  Rows = 1
FEATURE [Part::Part2DObjectPython] Line1191  label="Line1184"  # Draft 2D object (typed FeaturePython)
  ChamferSize = 0
  Closed = false
  End = (4900,-555,0)
  FilletRadius = 0
  Length = 790
  MakeFace = true
  Placement = pos=(4110,-585,0) rot=(0,0,-1;0rad)
  Points = (2) [(0,30,0),(790,30,0)]
  Start = (4110,-555,0)
  Subdivisions = 0
FEATURE [Sketcher::SketchObject] Sketch260
  FullyConstrained = true
  Placement = pos=(5810,2285,-180) rot=(1,0,0;1.5708rad)
  sketch-geometry (8):
    g0: LineSegment StartX=0 StartY=0 StartZ=0 EndX=900 EndY=0 EndZ=0
    g1: LineSegment StartX=900 StartY=0 StartZ=0 EndX=900 EndY=2150 EndZ=0
    g2: LineSegment StartX=900 StartY=2150 StartZ=0 EndX=0 EndY=2150 EndZ=0
    g3: LineSegment StartX=0 StartY=2150 StartZ=0 EndX=0 EndY=0 EndZ=0
    g4: LineSegment StartX=50 StartY=0 StartZ=0 EndX=850 EndY=0 EndZ=0
    g5: LineSegment StartX=850 StartY=0 StartZ=0 EndX=850 EndY=2100 EndZ=0
    g6: LineSegment StartX=850 StartY=2100 StartZ=0 EndX=50 EndY=2100 EndZ=0
    g7: LineSegment StartX=50 StartY=2100 StartZ=0 EndX=50 EndY=0 EndZ=0
  constraints (23):
    c: Coincident(g0,g1)
    c: Coincident(g1,g2)
    c: Coincident(g2,g3)
    c: Coincident(g3,g0)
    c: Horizontal(g0)
    c: Horizontal(g2)
    c: Vertical(g1)
    c: Vertical(g3)
    c: Coincident(g4,g5)
    c: Coincident(g5,g6)
    c: Coincident(g6,g7)
    c: Coincident(g7,g4)
    c: Horizontal(g4)
    c: Horizontal(g6)
    c: Vertical(g5)
    c: Vertical(g7)
    c: DistanceY(g1) = 2150  'Height'
    c: DistanceX(g0) = 900  'Width'
    c: DistanceY(g6,g2) = 50  'Frame1'
    c: DistanceX(g2,g6) = 50  'Frame2'
    c: DistanceX(g4,g0) = 50  'Frame3'
    c: DistanceY(g0,g4) = 0
    c: Coincident(g0,g-1)
FEATURE [Part::Part2DObjectPython] Line1200  label="Line1202"  # Draft 2D object (typed FeaturePython)
  ChamferSize = 0
  Closed = true
  End = (7910,6475,0)
  FilletRadius = 0
  Length = 2670
  MakeFace = false
  Placement = pos=(5440,5450,0) rot=(0,0,-1;1.5708rad)
  Points = (2) [(1645,2470,0),(-1025,2470,0)]
  Start = (7910,3805,0)
  Subdivisions = 0
FEATURE [Part::Part2DObjectPython] Line1201  label="ось фундамента внутр.стены001"  # Draft 2D object (typed FeaturePython)
  ChamferSize = 0
  Closed = true
  End = (9525,9350,0)
  FilletRadius = 0
  Length = 9090
  MakeFace = false
  Placement = pos=(7825,2900,0) rot=(0,0,1;1.5708rad)
  Points = (2) [(-2640,-1700,0),(6450,-1700,0)]
  Start = (9525,260,0)
  Subdivisions = 0
FEATURE [Part::FeaturePython] Wall129  label="фундамент внутр.стена002"  # Arch/BIM 166 (typed FeaturePython)
  Align = 2
  Area = 4545000
  Base = -> Line1201
  BlockHeight = 0
  BlockLength = 0
  CountBroken = 0
  CountEntire = 0
  Face = 0
  Height = 500
  HorizontalArea = 2.2725e+06
  IfcType = 166
  Joint = 0
  Length = 9090
  MakeBlocks = false
  MoveBase = false
  MoveWithHost = false
  Normal = (0,0,-1)
  OffsetFirst = 0
  OffsetSecond = 0
  PerimeterLength = 18680
  Placement = pos=(0,0,-180) rot=(0,0,1;0rad)
  PredefinedType = 0
  VerticalArea = 9340000
  Width = 250
FEATURE [Part::Extrusion] Extrude012  label="Габарит человека 003"
  Base = -> Sketch250
  Dir = (0,-1,2e-16)
  DirMode = 2
  FaceMakerClass = Part::FaceMakerBullseye
  LengthFwd = 290
  LengthRev = 0
  Placement = pos=(4469.4,8795.6,0) rot=(0,0,1;0rad)
  Solid = true
  Symmetric = false
FEATURE [Part::Part2DObjectPython] Rectangle2589  label="проём в перекрытии 005"  # Draft 2D object (typed FeaturePython)
  ChamferSize = 0
  Columns = 1
  FilletRadius = 0
  Height = 1550
  Length = 380
  MakeFace = false
  Placement = pos=(-3580,8320,0) rot=(0,0,1;0rad)
  Rows = 1
FEATURE [Part::Part2DObjectPython] Rectangle2597  label="проём вентшахты"  # Draft 2D object (typed FeaturePython)
  ChamferSize = 0
  Columns = 1
  FilletRadius = 0
  Height = 800
  Length = 320
  MakeFace = false
  Placement = pos=(8785,1470,0) rot=(0,0,1;0rad)
  Rows = 1
FEATURE [Part::FeaturePython] Structure158  label="Вентстояк вычитаемы объём 002"  # Arch/BIM 52 (typed FeaturePython)
  Base = -> Rectangle2597
  FaceMaker = 0
  GlobalId = 2VgUxAGbH6UvSFD9GbSn_n
  Height = 4000
  HorizontalArea = 256000
  IfcData = IfcUID=2VgUxAGbH6UvSFD9GbSn_n,attributes={"GlobalId": {"value": "2VgUxAGbH6UvSFD9GbSn_n"}},+1 more (map truncated)
  IfcType = 52
  Length = 0
  MoveBase = false
  MoveWithHost = false
  Nodes = (2) [(8945,1870,0),(8945,1870,4000)]
  NodesOffset = 0
  Normal = (0,0,0)
  PerimeterLength = 2240
  Placement = pos=(0,0,2800) rot=(0,0,1;0rad)
  VerticalArea = 8960000
  Width = 100
FEATURE [Part::Extrusion] Extrude022  label="Габарит человека 004"
  Base = -> Sketch250
  Dir = (0,-1,2e-16)
  DirMode = 2
  FaceMakerClass = Part::FaceMakerBullseye
  LengthFwd = 290
  LengthRev = 0
  Placement = pos=(11840.4,4373.49,3130) rot=(0,0,1;1.5708rad)
  Solid = true
  Symmetric = false
FEATURE [App::GeometryPython] BuildingPart036  label="Эргономика"  # Arch/BIM 52 (typed FeaturePython)
  Area = 0
  GlobalId = 1U0bveIaj1buNClxqFBVzz
  Group = -> [Extrude007,Extrude008,Extrude012,Extrude022]
  Height = 0
  HeightPropagate = true
  IfcData = IfcUID=1U0bveIaj1buNClxqFBVzz,attributes={"GlobalId": {"value": "1U0bveIaj1buNClxqFBVzz"}},+1 more (map truncated)
  IfcType = 52
  LevelOffset = 0
FEATURE [Part::FeaturePython] Wall145  label="табуретка"  # Arch/BIM 166 (typed FeaturePython)
  Align = 2
  Area = 1992000
  BlockHeight = 0
  BlockLength = 0
  CountBroken = 0
  CountEntire = 0
  Face = 0
  Height = 150
  HorizontalArea = 1.328e+06
  IfcType = 166
  Joint = 0
  Length = 13280
  MakeBlocks = false
  MoveBase = false
  MoveWithHost = false
  Normal = (0,0,0)
  OffsetFirst = 0
  OffsetSecond = 0
  PerimeterLength = 26760
  Placement = pos=(0,0,5260) rot=(0,0,1;0rad)
  PredefinedType = 0
  VerticalArea = 4.014e+06
  Width = 100
FEATURE [Part::FeaturePython] Wall146  label="Wall010"  # Arch/BIM 166 (typed FeaturePython)
  Align = 2
  Area = 420000
  BlockHeight = 0
  BlockLength = 0
  CountBroken = 0
  CountEntire = 0
  Face = 0
  Height = 150
  HorizontalArea = 280000
  IfcType = 166
  Joint = 0
  Length = 2800
  MakeBlocks = false
  MoveBase = false
  MoveWithHost = true
  Normal = (0,0,0)
  OffsetFirst = 0
  OffsetSecond = 0
  PerimeterLength = 5800
  Placement = pos=(0,0,3210) rot=(0,0,1;0rad)
  PredefinedType = 0
  VerticalArea = 870000
  Width = 100
FEATURE [Part::Part2DObjectPython] Line1228  label="Line1229"  # Draft 2D object (typed FeaturePython)
  ChamferSize = 0
  Closed = false
  End = (903.033,1056.97,0)
  FilletRadius = 0
  Length = 150
  MakeFace = false
  Placement = pos=(796.967,1163.03,0) rot=(0,0,1;0rad)
  Points = (2) [(0,0,0),(106.066,-106.066,0)]
  Start = (796.967,1163.03,0)
  Subdivisions = 0
FEATURE [Part::Part2DObjectPython] Line1229  label="Line1230"  # Draft 2D object (typed FeaturePython)
  ChamferSize = 0
  Closed = false
  End = (12453,8446.97,0)
  FilletRadius = 0
  Length = 150
  MakeFace = false
  Placement = pos=(12347,8553.03,0) rot=(0,0,1;0rad)
  Points = (2) [(0,0,0),(106.066,-106.066,0)]
  Start = (12347,8553.03,0)
  Subdivisions = 0
FEATURE [Part::Part2DObjectPython] Line1230  label="Line1231"  # Draft 2D object (typed FeaturePython)
  ChamferSize = 0
  Closed = false
  End = (13389.9,7510.05,0)
  FilletRadius = 0
  Length = 2800
  MakeFace = false
  Placement = pos=(11410.1,9489.95,0) rot=(0,0,1;0rad)
  Points = (2) [(0,0,0),(1979.9,-1979.9,0)]
  Start = (11410.1,9489.95,0)
  Subdivisions = 0
FEATURE [Part::FeaturePython] Wall149  label="Wall012"  # Arch/BIM 166 (typed FeaturePython)
  Align = 2
  Area = 420000
  Base = -> Line1230
  BlockHeight = 0
  BlockLength = 0
  CountBroken = 0
  CountEntire = 0
  Face = 0
  Height = 150
  HorizontalArea = 280000
  IfcType = 166
  Joint = 0
  Length = 2800
  MakeBlocks = false
  MoveBase = false
  MoveWithHost = true
  Normal = (0,0,0)
  OffsetFirst = 0
  OffsetSecond = 0
  PerimeterLength = 5800
  Placement = pos=(0,0,3210) rot=(0,0,1;0rad)
  PredefinedType = 0
  VerticalArea = 870000
  Width = 100
FEATURE [Part::Part2DObjectPython] Line1231  label="Line1232"  # Draft 2D object (typed FeaturePython)
  ChamferSize = 0
  Closed = false
  End = (903.033,8553.03,0)
  FilletRadius = 0
  Length = 150
  MakeFace = false
  Placement = pos=(796.967,8446.97,0) rot=(0,0,1;1.5708rad)
  Points = (2) [(0,0,0),(106.066,-106.066,0)]
  Start = (796.967,8446.97,0)
  Subdivisions = 0
FEATURE [Part::Part2DObjectPython] Line1232  label="Line1233"  # Draft 2D object (typed FeaturePython)
  ChamferSize = 0
  Closed = false
  End = (1839.95,9489.95,0)
  FilletRadius = 0
  Length = 2800
  MakeFace = false
  Placement = pos=(-139.949,7510.05,0) rot=(0,0,1;1.5708rad)
  Points = (2) [(0,0,0),(1979.9,-1979.9,0)]
  Start = (-139.949,7510.05,0)
  Subdivisions = 0
FEATURE [Part::FeaturePython] Wall152  label="Wall014"  # Arch/BIM 166 (typed FeaturePython)
  Align = 2
  Area = 420000
  Base = -> Line1232
  BlockHeight = 0
  BlockLength = 0
  CountBroken = 0
  CountEntire = 0
  Face = 0
  Height = 150
  HorizontalArea = 280000
  IfcType = 166
  Joint = 0
  Length = 2800
  MakeBlocks = false
  MoveBase = false
  MoveWithHost = true
  Normal = (0,0,0)
  OffsetFirst = 0
  OffsetSecond = 0
  PerimeterLength = 5800
  Placement = pos=(0,0,3210) rot=(0,0,1;0rad)
  PredefinedType = 0
  VerticalArea = 870000
  Width = 100
FEATURE [Part::Part2DObjectPython] Line1233  label="Line1234"  # Draft 2D object (typed FeaturePython)
  ChamferSize = 0
  Closed = false
  End = (12453,1163.03,0)
  FilletRadius = 0
  Length = 150
  MakeFace = false
  Placement = pos=(12347,1056.97,0) rot=(0,0,1;1.5708rad)
  Points = (2) [(0,0,0),(106.066,-106.066,0)]
  Start = (12347,1056.97,0)
  Subdivisions = 0
FEATURE [Part::Part2DObjectPython] Line1234  label="Line1235"  # Draft 2D object (typed FeaturePython)
  ChamferSize = 0
  Closed = false
  End = (13389.9,2099.95,0)
  FilletRadius = 0
  Length = 2800
  MakeFace = false
  Placement = pos=(11410.1,120.051,0) rot=(0,0,1;1.5708rad)
  Points = (2) [(0,0,0),(1979.9,-1979.9,0)]
  Start = (11410.1,120.051,0)
  Subdivisions = 0
FEATURE [Part::FeaturePython] Wall155  label="Wall016"  # Arch/BIM 166 (typed FeaturePython)
  Align = 2
  Area = 420000
  Base = -> Line1234
  BlockHeight = 0
  BlockLength = 0
  CountBroken = 0
  CountEntire = 0
  Face = 0
  Height = 150
  HorizontalArea = 280000
  IfcType = 166
  Joint = 0
  Length = 2800
  MakeBlocks = false
  MoveBase = false
  MoveWithHost = true
  Normal = (0,0,0)
  OffsetFirst = 0
  OffsetSecond = 0
  PerimeterLength = 5800
  Placement = pos=(0,0,3210) rot=(0,0,1;0rad)
  PredefinedType = 0
  VerticalArea = 870000
  Width = 100
FEATURE [Part::Part2DObjectPython] Rectangle2651  label="уширение фундамента 001"  # Draft 2D object (typed FeaturePython)
  ChamferSize = 0
  Columns = 1
  FilletRadius = 0
  Height = 1030
  Length = 130
  MakeFace = false
  Placement = pos=(3600,5330,0) rot=(0,0,1;0rad)
  Rows = 1
FEATURE [Part::FeaturePython] Structure172  label="уширение фундамента001"  # Arch/BIM 52 (typed FeaturePython)
  Base = -> Rectangle2651
  FaceMaker = 0
  Height = 500
  HorizontalArea = 133900
  IfcData = complex_attributes={"OwnerHistory": {}, "IsNestedBy": {}, "IsDecomposedBy": {}, "IsDefinedBy": {}, "ObjectPlacement": {}, "Representation":... (+4 chars omitted)
  IfcType = 52
  Length = 0
  MoveBase = false
  MoveWithHost = false
  Nodes = (2) [(3665,5845,0),(3665,5845,-500)]
  NodesOffset = 0
  Normal = (0,0,-1)
  PerimeterLength = 2320
  Placement = pos=(0,0,-180) rot=(0,0,1;0rad)
  VerticalArea = 1160000
  Width = 100
FEATURE [Part::FeaturePython] Wall038  label="фундамент внутр. стена 001"  # Arch/BIM 166 (typed FeaturePython)
  Additions = -> [Wall037,Structure172]
  Align = 2
  Area = 1.56e+06
  Base = -> Line1074
  BlockHeight = 0
  BlockLength = 0
  CountBroken = 0
  CountEntire = 0
  Face = 0
  Height = 300
  HorizontalArea = 2.6e+06
  IfcType = 166
  Joint = 0
  Length = 5200
  MakeBlocks = false
  MoveBase = false
  MoveWithHost = false
  Normal = (0,0,-1)
  OffsetFirst = 0
  OffsetSecond = 0
  PerimeterLength = 28620
  Placement = pos=(-25,0,-680) rot=(0,0,1;0rad)
  PredefinedType = 0
  VerticalArea = 9e+06
  Width = 500
FEATURE [Part::Part2DObjectPython] Rectangle556  label="вытяжка осн мал"  # Draft 2D object (typed FeaturePython)
  ChamferSize = 0
  Columns = 1
  FilletRadius = 0
  Height = 400
  Length = 400
  MakeFace = false
  Placement = pos=(11300,375,1600) rot=(0,0,-1;1.5708rad)
  Rows = 1
FEATURE [Part::Box] Box3145  label="ТВ"
  AttacherType = Attacher::AttachEngine3D
  Height = 750
  Length = 1400
  Placement = pos=(8090,6200,620) rot=(0,0,-1;1.5708rad)
  Width = 100
FEATURE [Part::Box] Box3143  label="шкаф книжн. "
  AttacherType = Attacher::AttachEngine3D
  Height = 2700
  Length = 900
  Placement = pos=(320,-25,0) rot=(0,0,1;1.5708rad)
  Width = 350
FEATURE [Part::Part2DObjectPython] Rectangle555  label="вытяжка осн бол"  # Draft 2D object (typed FeaturePython)
  ChamferSize = 0
  Columns = 1
  FilletRadius = 0
  Height = 600
  Length = 500
  MakeFace = false
  Placement = pos=(11200,475,1550) rot=(0,0,-1;1.5708rad)
  Rows = 1
FEATURE [Part::Loft] Loft001  label="вытяжка"
  Closed = false
  MaxDegree = 5
  Ruled = false
  Sections = -> [Rectangle555,Rectangle556]
  Solid = true
FEATURE [Part::Feature] Fillet001  label="стол обеденный"
  Placement = pos=(10350,2890,0) rot=(0,0,1;0rad)
  shape: bbox 1500 x 750 x 750 mm, 30 faces (baked)
FEATURE [Part::Feature] Fusion013  label="стул005"
  Placement = pos=(10350,2890,0) rot=(0,0,1;0rad)
  shape: bbox 480 x 520 x 910 mm, 35 faces (baked)
FEATURE [Part::Feature] Fusion014  label="стул006"
  Placement = pos=(10350,2890,0) rot=(0,0,1;0rad)
  shape: bbox 480 x 520 x 910 mm, 35 faces (baked)
FEATURE [Part::Feature] Fusion015  label="стул007"
  Placement = pos=(10350,2890,0) rot=(0,0,1;0rad)
  shape: bbox 480 x 520 x 910 mm, 35 faces (baked)
FEATURE [Part::Feature] Fusion016  label="стул008"
  Placement = pos=(10350,2890,0) rot=(0,0,1;0rad)
  shape: bbox 480 x 520 x 910 mm, 35 faces (baked)
FEATURE [Part::Box] Box3154  label="шкаф 58 одежда 001"
  AttacherType = Attacher::AttachEngine3D
  Height = 2700
  Length = 2310
  Placement = pos=(7350,-25,0) rot=(0,0,1;1.5708rad)
  Width = 580
FEATURE [Part::Box] Box3155  label="шкаф 60 одежда 002"
  AttacherType = Attacher::AttachEngine3D
  Height = 2700
  Length = 1500
  Placement = pos=(4100,1685,0) rot=(0,0,1;0rad)
  Width = 600
FEATURE [Part::Box] Box3156  label="шкаф 60 одежда 003"
  AttacherType = Attacher::AttachEngine3D
  Height = 2700
  Length = 2310
  Placement = pos=(4000,-25,0) rot=(0,0,1;1.5708rad)
  Width = 600
FEATURE [Part::Box] Box3157  label="шкаф 60 одежда 004"
  AttacherType = Attacher::AttachEngine3D
  Height = 2700
  Length = 1400
  Placement = pos=(-30,5025,0) rot=(0,0,1;0rad)
  Width = 600
FEATURE [Part::Box] Box3159  label="ТВ001"
  AttacherType = Attacher::AttachEngine3D
  Height = 750
  Length = 1200
  Placement = pos=(4720,6225,620) rot=(0,0,-1;1.5708rad)
  Width = 75
FEATURE [Part::Box] Box3163  label="обувница"
  AttacherType = Attacher::AttachEngine3D
  Height = 500
  Length = 1500
  Placement = pos=(4100,-25,0) rot=(0,0,1;0rad)
  Width = 400
FEATURE [Part::Feature] Fusion019  label="кровать 2 спальная 210х170 002"
  Placement = pos=(6970,7925,0) rot=(0,0,-1;1.5708rad)
  shape: bbox 2100 x 1700 x 800 mm, 53 faces (baked)
FEATURE [Part::Feature] Fusion027  label="Диван кабинет"
  Placement = pos=(3475,2970,0) rot=(0,0,1;3.14159rad)
  shape: bbox 1950 x 950 x 800 mm, 23 faces (baked)
FEATURE [Part::Box] Box3175  label="Холодильник"
  AttacherType = Attacher::AttachEngine3D
  Height = 1600
  Length = 600
  Placement = pos=(10150,-10,0) rot=(0,0,1;1.5708rad)
  Width = 600
FEATURE [Part::Box] Box3178  label="шкаф 45 кухонный 002"
  AttacherType = Attacher::AttachEngine3D
  Height = 700
  Length = 1800
  Placement = pos=(10750,-10,1600) rot=(0,0,1;0rad)
  Width = 450
FEATURE [Part::Box] Box3179  label="шкаф 60 кухонный 003"
  AttacherType = Attacher::AttachEngine3D
  Height = 700
  Length = 600
  Placement = pos=(9550,-10,1600) rot=(0,0,1;0rad)
  Width = 600
FEATURE [Part::Feature] Fillet003  label="Столик журнальный"
  Placement = pos=(13600,-900,0) rot=(0,0,1;0rad)
  shape: bbox 1000 x 1000 x 530 mm, 34 faces, 5 solids (baked)
FEATURE [Part::Box] Box3183  label="морозильник 60 см"
  AttacherType = Attacher::AttachEngine3D
  Height = 1800
  Length = 600
  Placement = pos=(8250,-25,0) rot=(0,0,1;0rad)
  Width = 600
FEATURE [Part::Box] Box3184  label="СМ"
  AttacherType = Attacher::AttachEngine3D
  Height = 800
  Length = 600
  Placement = pos=(8850,-25,0) rot=(0,0,1;0rad)
  Width = 600
FEATURE [Part::Feature] Fusion041  label="унитаз с инсталляцией 002"
  Placement = pos=(10970,-6405,0) rot=(0,0,1;1.5708rad)
  shape: bbox 400 x 700 x 1150 mm, 15 faces (baked)
FEATURE [Part::Box] Box3191  label="кулер"
  AttacherType = Attacher::AttachEngine3D
  Height = 950
  Length = 310
  Placement = pos=(12240,4575,0) rot=(0,0,1;0rad)
  Width = 310
FEATURE [Part::Cylinder] Cylinder  label="бутыль воды"
  Angle = 360
  AttacherType = Attacher::AttachEngine3D
  Height = 400
  Placement = pos=(12395,4730,950) rot=(0,0,1;0rad)
  Radius = 150
FEATURE [Part::Box] Box3192  label="кофеварка"
  AttacherType = Attacher::AttachEngine3D
  Height = 250
  Length = 200
  Placement = pos=(12494,3045.99,850) rot=(0,0,1;1.5708rad)
  Width = 250
FEATURE [Part::Cylinder] Cylinder001  label="чайник"
  Angle = 360
  AttacherType = Attacher::AttachEngine3D
  Height = 250
  Placement = pos=(12393.3,3359.1,850) rot=(0,0,1;1.5708rad)
  Radius = 75
FEATURE [Part::Box] Box3195  label="шкаф 45 кухонный 003"
  AttacherType = Attacher::AttachEngine3D
  Height = 400
  Length = 3000
  Placement = pos=(9550,-10,2300) rot=(0,0,1;0rad)
  Width = 600
FEATURE [Part::Part2DObjectPython] Rectangle2663  label="уширение фундамента 002"  # Draft 2D object (typed FeaturePython)
  ChamferSize = 0
  Columns = 1
  FilletRadius = 0
  Height = 1030
  Length = 130
  MakeFace = false
  Placement = pos=(9650,4310,0) rot=(0,0,1;0rad)
  Rows = 1
FEATURE [Part::FeaturePython] Structure175  label="уширение фундамента002"  # Arch/BIM 52 (typed FeaturePython)
  Base = -> Rectangle2663
  FaceMaker = 0
  Height = 500
  HorizontalArea = 133900
  IfcData = complex_attributes={"OwnerHistory": {}, "IsNestedBy": {}, "IsDecomposedBy": {}, "IsDefinedBy": {}, "ObjectPlacement": {}, "Representation":... (+4 chars omitted)
  IfcType = 52
  Length = 0
  MoveBase = false
  MoveWithHost = false
  Nodes = (2) [(9715,4825,0),(9715,4825,-500)]
  NodesOffset = 0
  Normal = (0,0,-1)
  PerimeterLength = 2320
  Placement = pos=(0,0,-180) rot=(0,0,1;0rad)
  VerticalArea = 1160000
  Width = 100
FEATURE [Part::FeaturePython] Wall130  label="фундамент внутр. стена 002"  # Arch/BIM 166 (typed FeaturePython)
  Additions = -> [Wall129,Structure175]
  Align = 2
  Area = 2727000
  Base = -> Line1201
  BlockHeight = 0
  BlockLength = 0
  CountBroken = 0
  CountEntire = 0
  Face = 0
  Height = 300
  HorizontalArea = 4.55015e+06
  IfcType = 166
  Joint = 0
  Length = 9090
  MakeBlocks = false
  MoveBase = false
  MoveWithHost = false
  Normal = (0,0,-1)
  OffsetFirst = 0
  OffsetSecond = 0
  PerimeterLength = 28620
  Placement = pos=(0,0,-680) rot=(0,0,1;0rad)
  PredefinedType = 0
  VerticalArea = 15224000
  Width = 500
FEATURE [Part::Part2DObjectPython] Rectangle2695  label="Д90-007"  # Draft 2D object (typed FeaturePython)
  ChamferSize = 0
  Columns = 1
  FilletRadius = 0
  Height = 100
  Length = 900
  MakeFace = true
  Placement = pos=(9550,770,0) rot=(0,0,1;1.5708rad)
  Rows = 1
FEATURE [Part::FeaturePython] Structure026  label="Проём-Д90-020"  # Arch/BIM 52 (typed FeaturePython)
  Base = -> Rectangle2695
  FaceMaker = 0
  Height = 2170
  HorizontalArea = 90000
  IfcData = complex_attributes={"OwnerHistory": {}, "IsNestedBy": {}, "IsDecomposedBy": {}, "IsDefinedBy": {}, "ObjectPlacement": {}, "Representation":... (+4 chars omitted)
  IfcType = 52
  Length = 0
  MoveBase = false
  MoveWithHost = false
  Nodes = (2) [(13000,6050,0),(13000,6050,2180)]
  NodesOffset = 0
  Normal = (0,0,0)
  PerimeterLength = 2000
  Placement = pos=(0,0,-20) rot=(0,0,1;0rad)
  VerticalArea = 4340000
  Width = 100
FEATURE [Part::Part2DObjectPython] Rectangle2630  label="Rectangle2624"  # Draft 2D object (typed FeaturePython)
  ChamferSize = 0
  Columns = 1
  FilletRadius = 0
  Height = 1500
  Length = 2100
  MakeFace = false
  Placement = pos=(1150,2125,0) rot=(0,0,-1;1.5708rad)
  Rows = 1
FEATURE [Part::Part2DObjectPython] Rectangle2684  label="Rectangle2703"  # Draft 2D object (typed FeaturePython)
  ChamferSize = 0
  Columns = 1
  FilletRadius = 0
  Height = 1800
  Length = 900
  MakeFace = true
  Placement = pos=(1000,925,0) rot=(0,0,-1;1.5708rad)
  Rows = 1
FEATURE [Part::Part2DObjectPython] Rectangle2712  label="TV 54" 002"  # Draft 2D object (typed FeaturePython)
  ChamferSize = 0
  Columns = 1
  FilletRadius = 0
  Height = 1200
  Length = 75
  MakeFace = false
  Placement = pos=(4795,6225,0) rot=(0,0,1;3.14159rad)
  Rows = 1
FEATURE [Part::Part2DObjectPython] Rectangle2717  label="Д90-006"  # Draft 2D object (typed FeaturePython)
  ChamferSize = 0
  Columns = 1
  FilletRadius = 0
  Height = 100
  Length = 900
  MakeFace = true
  Placement = pos=(5810,2285,0) rot=(0,0,1;0rad)
  Rows = 1
FEATURE [Part::FeaturePython] Structure024  label="Проём-Д90-019"  # Arch/BIM 52 (typed FeaturePython)
  Base = -> Rectangle2717
  FaceMaker = 0
  Height = 2170
  HorizontalArea = 90000
  IfcData = complex_attributes={"OwnerHistory": {}, "IsNestedBy": {}, "IsDecomposedBy": {}, "IsDefinedBy": {}, "ObjectPlacement": {}, "Representation":... (+4 chars omitted)
  IfcType = 52
  Length = 0
  MoveBase = false
  MoveWithHost = false
  Nodes = (2) [(5000,3050,0),(5000,3050,2180)]
  NodesOffset = 0
  Normal = (0,0,0)
  PerimeterLength = 2000
  Placement = pos=(0,0,-20) rot=(0,0,1;0rad)
  VerticalArea = 4340000
  Width = 100
FEATURE [Part::Part2DObjectPython] Rectangle2730  label="Д70-004"  # Draft 2D object (typed FeaturePython)
  ChamferSize = 0
  Columns = 1
  FilletRadius = 0
  Height = 110
  Length = 900
  MakeFace = true
  Placement = pos=(4930,6485,0) rot=(0,0,1;1.5708rad)
  Rows = 1
FEATURE [Part::FeaturePython] Structure141  label="Проём-Д90-001"  # Arch/BIM 52 (typed FeaturePython)
  Base = -> Rectangle2730
  FaceMaker = 0
  Height = 2170
  HorizontalArea = 99000
  IfcData = complex_attributes={"OwnerHistory": {}, "IsNestedBy": {}, "IsDecomposedBy": {}, "IsDefinedBy": {}, "ObjectPlacement": {}, "Representation":... (+4 chars omitted)
  IfcType = 52
  Length = 0
  MoveBase = false
  MoveWithHost = false
  Nodes = (2) [(10750,4050,0),(10750,4050,2180)]
  NodesOffset = 0
  Normal = (0,0,0)
  PerimeterLength = 2020
  Placement = pos=(0,0,-20) rot=(0,0,1;0rad)
  VerticalArea = 4.3834e+06
  Width = 100
FEATURE [Part::Part2DObjectPython] Rectangle2788  label="вн_контур"  # Draft 2D object (typed FeaturePython)
  ChamferSize = 0
  Columns = 1
  FilletRadius = 0
  Height = 7510
  Length = 12580
  MakeFace = false
  Placement = pos=(-30,-25,0) rot=(0,0,1;0rad)
  Rows = 1
FEATURE [Part::Part2DObjectPython] Rectangle2792  # Draft 2D object (typed FeaturePython)
  ChamferSize = 0
  Columns = 1
  FilletRadius = 0
  Height = 600
  Length = 600
  MakeFace = false
  Placement = pos=(10150,-25,0) rot=(0,0,1;0rad)
  Rows = 1
FEATURE [Part::Part2DObjectPython] Rectangle2795  label="Д90-002"  # Draft 2D object (typed FeaturePython)
  ChamferSize = 0
  Columns = 1
  FilletRadius = 0
  Height = 290
  Length = 920
  MakeFace = true
  Placement = pos=(3850,3535,0) rot=(0,0,1;0rad)
  Rows = 1
FEATURE [Part::FeaturePython] Structure023  label="Проём-Д90-018"  # Arch/BIM 52 (typed FeaturePython)
  Base = -> Rectangle2795
  FaceMaker = 0
  Height = 2350
  HorizontalArea = 266800
  IfcData = complex_attributes={"OwnerHistory": {}, "IsNestedBy": {}, "IsDecomposedBy": {}, "IsDefinedBy": {}, "ObjectPlacement": {}, "Representation":... (+4 chars omitted)
  IfcType = 52
  Length = 0
  MoveBase = false
  MoveWithHost = false
  Nodes = (2) [(8900,5350,0),(8900,5350,2180)]
  NodesOffset = 0
  Normal = (0,0,0)
  PerimeterLength = 2420
  Placement = pos=(0,0,-200) rot=(0,0,1;0rad)
  VerticalArea = 5687000
  Width = 100
FEATURE [Part::Part2DObjectPython] Rectangle2798  label="Д90-005"  # Draft 2D object (typed FeaturePython)
  ChamferSize = 0
  Columns = 1
  FilletRadius = 0
  Height = 100
  Length = 900
  MakeFace = true
  Placement = pos=(3500,2535,0) rot=(0,0,1;1.5708rad)
  Rows = 1
FEATURE [Part::FeaturePython] Structure021  label="Проём-Д90-017"  # Arch/BIM 52 (typed FeaturePython)
  Base = -> Rectangle2798
  FaceMaker = 0
  Height = 2170
  HorizontalArea = 90000
  IfcData = complex_attributes={"OwnerHistory": {}, "IsNestedBy": {}, "IsDecomposedBy": {}, "IsDefinedBy": {}, "ObjectPlacement": {}, "Representation":... (+4 chars omitted)
  IfcType = 52
  Length = 0
  MoveBase = false
  MoveWithHost = false
  Nodes = (2) [(7500,3050,0),(7500,3050,2180)]
  NodesOffset = 0
  Normal = (0,0,0)
  PerimeterLength = 2000
  Placement = pos=(0,0,-20) rot=(0,0,1;0rad)
  VerticalArea = 4340000
  Width = 100
FEATURE [Part::Part2DObjectPython] Rectangle2807  label="Д90-001"  # Draft 2D object (typed FeaturePython)
  ChamferSize = 0
  Columns = 1
  FilletRadius = 0
  Height = 290
  Length = 920
  MakeFace = true
  Placement = pos=(6720,3825,0) rot=(0,0,1;3.14159rad)
  Rows = 1
FEATURE [Part::FeaturePython] Structure020  label="Проём-Д90-016"  # Arch/BIM 52 (typed FeaturePython)
  Base = -> Rectangle2807
  FaceMaker = 0
  Height = 2350
  HorizontalArea = 266800
  IfcData = complex_attributes={"OwnerHistory": {}, "IsNestedBy": {}, "IsDecomposedBy": {}, "IsDefinedBy": {}, "ObjectPlacement": {}, "Representation":... (+4 chars omitted)
  IfcType = 52
  Length = 0
  MoveBase = false
  MoveWithHost = false
  Nodes = (2) [(650,-4000,0),(650,-4000,2250)]
  NodesOffset = 0
  Normal = (0,0,0)
  PerimeterLength = 2420
  Placement = pos=(0,0,-200) rot=(0,0,1;0rad)
  VerticalArea = 5687000
  Width = 100
FEATURE [Part::Part2DObjectPython] Rectangle2808  # Draft 2D object (typed FeaturePython)
  ChamferSize = 0
  Columns = 1
  FilletRadius = 0
  Height = 600
  Length = 600
  MakeFace = true
  Placement = pos=(8850,-25,0) rot=(0,0,1;0rad)
  Rows = 1
FEATURE [Part::Part2DObjectPython] Rectangle  label="контур по облицовке"  # Draft 2D object (typed FeaturePython)
  ChamferSize = 0
  Columns = 1
  FilletRadius = 0
  Height = 8570
  Length = 13640
  MakeFace = false
  Placement = pos=(-560,-555,0) rot=(0,0,1;0rad)
  Rows = 1
FEATURE [Part::Extrusion] Extrude061  label="ПНО 40-10-6-003"
  Base = -> Sketch249
  Dir = (0,3980,0)
  DirMode = 0
  FaceMakerClass = Part::FaceMakerBullseye
  LengthFwd = 3980
  LengthRev = 0
  Placement = pos=(10,3685,2800) rot=(0,0,1;0rad)
  Solid = true
  Symmetric = false
FEATURE [Part::Extrusion] Extrude062  label="ПНО 40-12-8-003"
  Base = -> Sketch231
  Dir = (0,3980,0)
  DirMode = 0
  FaceMakerClass = Part::FaceMakerBullseye
  LengthFwd = 3980
  LengthRev = 0
  Placement = pos=(10,3685,2800) rot=(0,0,1;0rad)
  Solid = true
  Symmetric = false
FEATURE [Part::FeaturePython] Array038  label="ПНО-40-12 3шт."  # Draft array (typed FeaturePython)
  Angle = 360
  ArrayType = 0
  Axis = (0,0,1)
  Base = -> Extrude062
  Center = (0,0,0)
  Fuse = false
  IntervalAxis = (0,0,0)
  IntervalX = (1215,0,0)
  IntervalY = (0,0,0)
  IntervalZ = (0,0,1)
  NumberPolar = 1
  NumberX = 3
  NumberY = 1
  NumberZ = 1
  Placement = pos=(7920,9.09e-13,0) rot=(0,0,1;0rad)
FEATURE [Part::Part2DObjectPython] Rectangle544  # Draft 2D object (typed FeaturePython)
  ChamferSize = 0
  Columns = 1
  FilletRadius = 25
  Height = 300
  Length = 2500
  MakeFace = false
  Placement = pos=(12525,4960,0) rot=(0,0,1;1.5708rad)
  Rows = 1
FEATURE [Part::Part2DObjectPython] Rectangle545  # Draft 2D object (typed FeaturePython)
  ChamferSize = 0
  Columns = 1
  FilletRadius = 25
  Height = 950
  Length = 2500
  MakeFace = true
  Placement = pos=(12525,4960,0) rot=(0,0,1;1.5708rad)
  Rows = 1
  Support = -> [Rectangle544]
FEATURE [Part::Part2DObjectPython] Rectangle546  # Draft 2D object (typed FeaturePython)
  ChamferSize = 0
  Columns = 1
  FilletRadius = 25
  Height = 1620
  Length = 250
  MakeFace = false
  Placement = pos=(12525,7210,0) rot=(0,0,1;1.5708rad)
  Rows = 1
FEATURE [Part::Part2DObjectPython] Rectangle547  # Draft 2D object (typed FeaturePython)
  ChamferSize = 0
  Columns = 1
  FilletRadius = 25
  Height = 950
  Length = 250
  MakeFace = false
  Placement = pos=(12525,4960,0) rot=(0,0,1;1.5708rad)
  Rows = 1
FEATURE [Part::Part2DObjectPython] Rectangle2837  # Draft 2D object (typed FeaturePython)
  ChamferSize = 0
  Columns = 1
  FilletRadius = 25
  Height = 670
  Length = 900
  MakeFace = true
  Placement = pos=(11575,6560,0) rot=(0,0,1;1.5708rad)
  Rows = 1
FEATURE [Part::Part2DObjectPython] Rectangle2857  label="ОК-144-001"  # Draft 2D object (typed FeaturePython)
  ChamferSize = 0
  Columns = 1
  FilletRadius = 0
  Height = 410
  Length = 1440
  MakeFace = true
  Placement = pos=(-30,1840,0) rot=(0,0,1;1.5708rad)
  Rows = 1
FEATURE [Part::FeaturePython] Structure285  label="Проём-ОК-144-001"  # Arch/BIM 52 (typed FeaturePython)
  Base = -> Rectangle2857
  FaceMaker = 0
  Height = 1617
  HorizontalArea = 590400
  IfcData = complex_attributes={"OwnerHistory": {}, "IsNestedBy": {}, "IsDecomposedBy": {}, "IsDefinedBy": {}, "ObjectPlacement": {}, "Representation":... (+4 chars omitted)
  IfcType = 52
  Length = 0
  MoveBase = false
  MoveWithHost = false
  Nodes = (2) [(-8120,-170,0),(-8120,-170,1500)]
  NodesOffset = 0
  Normal = (0,0,0)
  PerimeterLength = 3700
  Placement = pos=(0,0,955) rot=(0,0,1;0rad)
  VerticalArea = 5982900
  Width = 100
FEATURE [Part::Part2DObjectPython] Rectangle2858  label="четверть_131-001"  # Draft 2D object (typed FeaturePython)
  ChamferSize = 0
  Columns = 1
  FilletRadius = 0
  Height = 120
  Length = 1310
  MakeFace = true
  Placement = pos=(-560,3215,0) rot=(0,0,-1;1.5708rad)
  Rows = 1
FEATURE [Part::Part2DObjectPython] Line1266  label="Line1267"  # Draft 2D object (typed FeaturePython)
  ChamferSize = 0
  Closed = false
  End = (-560,1775,0)
  FilletRadius = 0
  Length = 1570
  MakeFace = true
  Placement = pos=(-560,3345,0) rot=(0,0,-1;1.5708rad)
  Points = (2) [(0,0,0),(1570,-3.41061e-13,0)]
  Start = (-560,3345,0)
  Subdivisions = 0
FEATURE [Part::Part2DObjectPython] Line1271  label="Line1272"  # Draft 2D object (typed FeaturePython)
  ChamferSize = 0
  Closed = true
  End = (8660,1835,0)
  FilletRadius = 0
  Length = 800
  MakeFace = false
  Placement = pos=(11240,5185,0) rot=(0,0,-1;1.5708rad)
  Points = (2) [(3350,-1780,0),(3350,-2580,0)]
  Start = (9460,1835,0)
  Subdivisions = 0
FEATURE [Part::FeaturePython] Wall162  label="перегородка 042"  # Arch/BIM 166 (typed FeaturePython)
  Align = 2
  Area = 2.24e+06
  Base = -> Line1271
  BlockHeight = 250
  BlockLength = 0
  CountBroken = 0
  CountEntire = 0
  Face = 0
  Height = 2800
  HorizontalArea = 64000
  IfcType = 166
  Joint = 0
  Length = 800
  MakeBlocks = false
  MoveBase = false
  MoveWithHost = false
  Normal = (0,0,0)
  OffsetFirst = 0
  OffsetSecond = 300
  PerimeterLength = 1760
  PredefinedType = 0
  VerticalArea = 4.928e+06
  Width = 80
FEATURE [Part::Box] Box3203  label="шкаф подвесной"
  AttacherType = Attacher::AttachEngine3D
  Height = 1000
  Length = 600
  Placement = pos=(8850,-25,800) rot=(0,0,1;0rad)
  Width = 600
FEATURE [Part::Box] Box3204  label="шкаф 001"
  AttacherType = Attacher::AttachEngine3D
  Height = 2700
  Length = 1215
  Placement = pos=(370,3810,0) rot=(0,0,1;1.5708rad)
  Width = 400
FEATURE [Part::Box] Box3205  label="шкаф 60 кухонный 011"
  AttacherType = Attacher::AttachEngine3D
  Height = 850
  Length = 1800
  Placement = pos=(10750,-10,0) rot=(0,0,1;0rad)
  Width = 600
FEATURE [Part::FeaturePython] Wall163  label="отделка цоколя"  # Arch/BIM 166 (typed FeaturePython)
  Align = 1
  Area = 11870000
  BlockHeight = 600
  BlockLength = 600
  CountBroken = 1
  CountEntire = 0
  Face = 0
  Height = 250
  HorizontalArea = 474800
  IfcType = 166
  Joint = 1
  Length = 47480
  MakeBlocks = true
  MoveBase = false
  MoveWithHost = false
  Normal = (0,0,-1)
  Offset = 80
  OffsetFirst = 0
  OffsetSecond = 0
  PerimeterLength = 94980
  Placement = pos=(0,0,-380) rot=(0,0,1;0rad)
  PredefinedType = 0
  VerticalArea = 23745000
  Width = 10
FEATURE [Part::Part2DObjectPython] Rectangle2939  # Draft 2D object (typed FeaturePython)
  ChamferSize = 0
  Columns = 1
  FilletRadius = 100
  Height = 800
  Length = 1500
  MakeFace = true
  Placement = pos=(10350,3265,0) rot=(0,0,1;0rad)
  Rows = 1
FEATURE [Part::Part2DObjectPython] Rectangle2941  # Draft 2D object (typed FeaturePython)
  ChamferSize = 0
  Columns = 1
  FilletRadius = 0
  Height = 300
  Length = 500
  MakeFace = true
  Placement = pos=(10490,4065,0) rot=(0,0,1;0rad)
  Rows = 1
FEATURE [Part::Part2DObjectPython] Rectangle2944  # Draft 2D object (typed FeaturePython)
  ChamferSize = 0
  Columns = 1
  FilletRadius = 0
  Height = 300
  Length = 500
  MakeFace = true
  Placement = pos=(10490,2965,0) rot=(0,0,1;0rad)
  Rows = 1
FEATURE [Part::FeaturePython] Structure155  label="Вентстояк вычитаемы объём 001"  # Arch/BIM 52 (typed FeaturePython)
  Base = -> Rectangle2589
  FaceMaker = 0
  Height = 6000
  HorizontalArea = 589000
  IfcData = complex_attributes={"OwnerHistory": {}, "IsNestedBy": {}, "IsDecomposedBy": {}, "IsDefinedBy": {}, "ObjectPlacement": {}, "Representation":... (+4 chars omitted)
  IfcType = 52
  Length = 0
  MoveBase = false
  MoveWithHost = false
  Nodes = (2) [(-3390,9095,0),(-3390,9095,6000)]
  NodesOffset = 0
  Normal = (0,0,0)
  PerimeterLength = 3860
  Placement = pos=(0,0,-180) rot=(0,0,1;0rad)
  VerticalArea = 2.316e+07
  Width = 100
FEATURE [Part::Part2DObjectPython] ShapeString131  # Draft 2D object (typed FeaturePython)
  FontFile = <path>
  Placement = pos=(9798.37,89.5753,0) rot=(0,0,1;0rad)
  Size = 300
  String = *
  Tracking = 0
FEATURE [Part::Part2DObjectPython] ShapeString133  # Draft 2D object (typed FeaturePython)
  FontFile = <path>
  Placement = pos=(8956.86,201.345,0) rot=(0,0,1;0rad)
  Size = 200
  String = СМ
  Tracking = 0
FEATURE [Part::Part2DObjectPython] ShapeString135  # Draft 2D object (typed FeaturePython)
  FontFile = <path>
  Placement = pos=(12278.3,1358.24,0) rot=(0,0,1;1.5708rad)
  Size = 200
  String = ПМ
  Tracking = 0
FEATURE [Part::Part2DObjectPython] Rectangle2972  label="Камин"  # Draft 2D object (typed FeaturePython)
  Area = 400000
  ChamferSize = 0
  Columns = 1
  FilletRadius = 0
  Height = 500
  Length = 800
  MakeFace = true
  Placement = pos=(8750,1885,0) rot=(0,0,1;0rad)
  Rows = 1
FEATURE [Spreadsheet::Sheet] Spreadsheet
  cells = C1=N/N; D1=Помещение; E1=Площадь; C2=1); D2==<<Прихожая>>.Label; E2==<<Прихожая>>.Shape.Area; C3=2); D3==<<Тех.помещение>>.Label; E3==<<Тех.помещение>>.Shape.Area; C4=3); D4==<<Кабинет>>.Label; E4==<<Кабинет>>.Shape.Area; C5=4); D5==<<Коридор>>.Label; E5==<<Коридор>>.Shape.Area; C6=5); D6==<<СУ#1>>.Label; E6==<<СУ#1>>.Shape.Area; C7=6); D7==<<Ванная>>.Label; E7==<<Ванная>>.Shape.Area; C8=7); D8==<<Душ>>.Label; E8==<<Душ>>.Shape.Area; C9=8); D9==<<Спальня 1 этаж>>.Label; E9==<<Спальня 1 этаж>>.Shape.Area; C10=9); D10==<<Кухня-столовая>>.Label; E10==<<Кухня-столовая>>.Shape.Area; D11=Итого:; E11==sum(E2:E10); D12=Тёплый контур (Площадь этажа):; E12==<<Тёплый контур>>.Shape.Area; B29=Мансарда (к учёту по СП54.13330); D29==<<h2,5м площадь (к=1.0) 001>>.Label; E29==<<h2,5м площадь (к=1.0) 001>>.Shape.Area * 1; D30==<<h1,6м площадь (к=0.7) 001>>.Label; E30==<<h1,6м площадь (к=0.7) 001>>.Shape.Area * 0.7; D31==<<h1,6м площадь (к=0.7) 002>>.Label; E31==<<h1,6м площадь (к=0.7) 002>>.Shape.Area * 0.7; D32==<<Вычитаемая площадь проёма>>.Label; E32==<<Вычитаемая площадь проёма>>.Shape.Area; D33=Итого:; E33==sum(E29:E31) - E32; D35=Тёплый контур+Мансарда:; E35==E12 + E33; B37=Мансарда фактически (от h=1.2m); D37==<<мансарда h1.2m>>.Label; E37==<<мансарда h1.2m>>.Shape.Area; D38==<<проём в перекрытии 007>>.Label; E38==<<проём в перекрытии 007>>.Shape.Area; E39==E37 - E38; B44=Объёмы материалов (этап коробки под крышу с облицовкой, на готовый фундамент):; B45=Блок ЛСР "Тёплый" 10.7нф; D45==<<Внешняя стена ЛСР 380мм>>.Label; E45==<<Внешняя стена ЛСР 380мм>>.Shape.Volume; D46==<<Стена ЛСР 380мм ряд перекрытия 001>>.Label; E46==<<Стена ЛСР 380мм ряд перекрытия 001>>.Shape.Volume; D47==<<Стена ЛСР 380мм ряд перекрытия 002>>.Label; E47==<<Стена ЛСР 380мм ряд перекрытия 002>>.Shape.Volume; D48==<<Стена ЛСР 380мм под мауэрлат>>.Label; E48==<<Стена ЛСР 380мм под мауэрлат>>.Shape.Volume; D49=Итого:; E49==sum(E45:E48); B51=Кирпич рядовой 1нф и 2.1нф, в соотн. 1:2; D51==<<Стена 250mm 2.1нф+1нф>>.Label; E51==<<Стена 250mm 2.1нф+1нф>>.Shape.Volume; D52==<<Ряд 1нф по плитам ПНО 001>>.Label; E52==<<Ряд 1нф по плитам ПНО 001>>.Shape.Volume; D53==<<Ряд 1нф по плитам ПНО 002>>.Label; E53==<<Ряд 1нф по плитам ПНО 002>>.Shape.Volume; D54==<<Стена 3 ряда 1NF в уровне перекрытия 001>>.Label; E54==<<Стена 3 ряда 1NF в уровне перекрытия 001>>.Shape.Volume; D55==<<Стена 3 ряда 1NF в уровне перекрытия 002>>.Label; E55==<<Стена 3 ряда 1NF в уровне перекрытия 002>>.Shape.Volume; D56==<<ряд  2.1нф в уровне армпояса>>.Label; E56==<<ряд  2.1нф в уровне армпояса>>.Shape.Volume; D57=Итого:; E57==sum(E51:E56); B58=Бетон (без учёта армирования):; D59==<<Перемычки монолитные>>.Label; E59==<<Перемычки монолитные>>.Shape.Volume; D60==<<Армпояс001>>.Label; E60==<<Армпояс001>>.Shape.Volume; D61==<<Армпояс002>>.Label; E61==<<Армпояс002>>.Shape.Volume; D62==<<Армпояс003>>.Label; E62==<<Армпояс003>>.Shape.Volume; D63==<<Армпояс004>>.Label; E63==<<Армпояс004>>.Shape.Volume; D64=Итого:; E64==sum(E59:E59); B65=Утеплитель XPS 80mm и 100mm; D66==<<Утепление перемычек XPS 100mm>>.Label; E66==<<Утепление перемычек XPS 100mm>>.Shape.Volume; D67==<<Утепление торца плит XPS 80mm 001>>.Label; E67==<<Утепление торца плит XPS 80mm 001>>.Shape.Volume; D68==<<Утепление торца плит XPS 80mm 002>>.Label; E68==<<Утепление торца плит XPS 80mm 002>>.Shape.Volume; D69==<<XPS 80mm в уровне армпояса>>.Label; E69==<<XPS 80mm в уровне армпояса>>.Shape.Volume; D70=Итого:; E70==sum(E66:E69); D72=Перегородки 80mm; E72==<<Перегородки>>.Shape.Volume; D73=Утепление перемычек XPS 100mm; E73==<<Утепление перемычек XPS 100mm>>.Shape.Volume; D75=бетон Армпояс+Пол по грунту стяжка; D79=бетон (фундамент МЗЛФ); E79==<<фундамент МЗЛФ>>.Shape.Volume; D80=Утеплитель ЭППС (МЗЛФ); E80==<<утепл фунд. внешней.стены 002>>.Shape.Volume + <<утепл отмостки 001>>.Shape.Volume + <<Утеплитель полки облицовки>>.Shape.Volume; D82=Утепление перекрытия ПСБ25; E82==<<Утепление перекрытия XPS 100mm>>.Shape.Volume; D83=Пояс перекрытия+монолит.уч.; D84=стяжка перекрытия; E84==<<Стяжка пола 50мм>>.Shape.Volume; D85=опорный ряд  под мауэрлат; E85==<<Стена ЛСР 380мм под мауэрлат>>.Shape.Volume; D87=грунт в границах участка, h=1м; E87==<<грунт в границах участка>>.Shape.Volume
FEATURE [Part::Part2DObjectPython] Rectangle2973  label="Шкаф 60 014"  # Draft 2D object (typed FeaturePython)
  Area = 630000
  ChamferSize = 0
  Columns = 1
  FilletRadius = 0
  Height = 1800
  Length = 350
  MakeFace = true
  Placement = pos=(-30,-25,0) rot=(0,0,1;0rad)
  Rows = 1
FEATURE [Part::Part2DObjectPython] ShapeString138  # Draft 2D object (typed FeaturePython)
  FontFile = <path>
  Placement = pos=(5506.65,999.608,0) rot=(0,0,1;0rad)
  Size = 250
  String = 1
  Tracking = 0
FEATURE [Part::Part2DObjectPython] Circle088  # Draft 2D object (typed FeaturePython)
  Area = 0
  FirstAngle = 0
  LastAngle = 0
  MakeFace = false
  Placement = pos=(5600,1100,0) rot=(0,0,1;0rad)
  Radius = 200
FEATURE [Part::Part2DObjectPython] Circle089  label="Circle090"  # Draft 2D object (typed FeaturePython)
  Area = 0
  FirstAngle = 0
  LastAngle = 0
  MakeFace = false
  Placement = pos=(8400,1200,0) rot=(0,0,1;0rad)
  Radius = 200
FEATURE [Part::Part2DObjectPython] ShapeString139  # Draft 2D object (typed FeaturePython)
  FontFile = <path>
  Placement = pos=(8306.65,1099.61,0) rot=(0,0,1;0rad)
  Size = 250
  String = 2
  Tracking = 0
FEATURE [Part::Part2DObjectPython] Circle090  label="Circle091"  # Draft 2D object (typed FeaturePython)
  Area = 0
  FirstAngle = 0
  LastAngle = 0
  MakeFace = false
  Placement = pos=(2300,1700,0) rot=(0,0,1;0rad)
  Radius = 200
FEATURE [Part::Part2DObjectPython] ShapeString140  # Draft 2D object (typed FeaturePython)
  FontFile = <path>
  Placement = pos=(2206.65,1599.61,0) rot=(0,0,1;0rad)
  Size = 250
  String = 3
  Tracking = 0
FEATURE [Part::Part2DObjectPython] Circle091  label="Circle092"  # Draft 2D object (typed FeaturePython)
  Area = 0
  FirstAngle = 0
  LastAngle = 0
  MakeFace = false
  Placement = pos=(5400,6800,0) rot=(0,0,1;0rad)
  Radius = 200
FEATURE [Part::Part2DObjectPython] ShapeString141  # Draft 2D object (typed FeaturePython)
  FontFile = <path>
  Placement = pos=(5306.65,6699.61,0) rot=(0,0,1;0rad)
  Size = 250
  String = 6
  Tracking = 0
FEATURE [Part::Part2DObjectPython] Circle092  label="Circle093"  # Draft 2D object (typed FeaturePython)
  Area = 0
  FirstAngle = 0
  LastAngle = 0
  MakeFace = false
  Placement = pos=(5478.23,2960.97,0) rot=(0,0,1;0rad)
  Radius = 200
FEATURE [Part::Part2DObjectPython] ShapeString142  # Draft 2D object (typed FeaturePython)
  FontFile = <path>
  Placement = pos=(5384.88,2860.58,0) rot=(0,0,1;0rad)
  Size = 250
  String = 4
  Tracking = 0
FEATURE [Part::Part2DObjectPython] Circle093  label="Circle094"  # Draft 2D object (typed FeaturePython)
  Area = 0
  FirstAngle = 0
  LastAngle = 0
  MakeFace = false
  Placement = pos=(6024.68,4588.68,0) rot=(0,0,1;0rad)
  Radius = 200
FEATURE [Part::Part2DObjectPython] ShapeString143  # Draft 2D object (typed FeaturePython)
  FontFile = <path>
  Placement = pos=(5931.33,4488.29,0) rot=(0,0,1;0rad)
  Size = 250
  String = 5
  Tracking = 0
FEATURE [Part::Part2DObjectPython] Circle094  label="Circle095"  # Draft 2D object (typed FeaturePython)
  Area = 0
  FirstAngle = 0
  LastAngle = 0
  MakeFace = false
  Placement = pos=(4100,5600,0) rot=(0,0,1;0rad)
  Radius = 200
FEATURE [Part::Part2DObjectPython] ShapeString144  # Draft 2D object (typed FeaturePython)
  FontFile = <path>
  Placement = pos=(4006.65,5499.61,0) rot=(0,0,1;0rad)
  Size = 250
  String = 8
  Tracking = 0
FEATURE [Part::Part2DObjectPython] Circle095  label="Circle096"  # Draft 2D object (typed FeaturePython)
  Area = 0
  FirstAngle = 0
  LastAngle = 0
  MakeFace = false
  Placement = pos=(7423.01,4962.99,0) rot=(0,0,1;0rad)
  Radius = 200
FEATURE [Part::Part2DObjectPython] ShapeString145  # Draft 2D object (typed FeaturePython)
  FontFile = <path>
  Placement = pos=(7329.66,4862.6,0) rot=(0,0,1;0rad)
  Size = 250
  String = 7
  Tracking = 0
FEATURE [Part::Part2DObjectPython] Circle097  label="Circle098"  # Draft 2D object (typed FeaturePython)
  Area = 0
  FirstAngle = 0
  LastAngle = 0
  MakeFace = false
  Placement = pos=(9400,5300,0) rot=(0,0,1;0rad)
  Radius = 200
FEATURE [Part::Part2DObjectPython] ShapeString147  # Draft 2D object (typed FeaturePython)
  FontFile = <path>
  Placement = pos=(9306.65,5199.61,0) rot=(0,0,1;0rad)
  Size = 250
  String = 9
  Tracking = 0
FEATURE [Part::Part2DObjectPython] Wire691  label="кровля_контур_001"  # Draft 2D object (typed FeaturePython)
  Area = 0
  ChamferSize = 0
  Closed = true
  End = (-1215,8670,0)
  FilletRadius = 0
  Length = 49660
  MakeFace = false
  Placement = pos=(19000,-1120,0) rot=(0,0,1;0rad)
  Points = (4) [(-20215,-90,0),(-5265,-90,0),(-5265,9790,0),(-20215,9790,0)]
  Start = (-1215,-1210,0)
  Subdivisions = 0
FEATURE [Part::FeaturePython] Roof013  label="Крыша объём стропильной системы"  # Arch/BIM 113 (typed FeaturePython)
  Angles = [30,30,30,30]
  Base = -> Wire691
  BorderLength = 49660
  Face = 0
  Flip = false
  Heights = [2852.11,3345.74,2852.11,3345.74]
  HorizontalArea = 1.47706e+08
  IdRel = [-1,-1,-1,-1]
  IfcData = attributes={"GlobalId": {"name": "GlobalId", "type": "IfcGloballyUniqueId", "is_enum": false, "enum_values": []}, "Description": {"... (+613 chars omitted),+1 more (map truncated)
  IfcType = 113
  MoveBase = false
  MoveWithHost = false
  Overhang = [0,0,0,0]
  PerimeterLength = 0
  Placement = pos=(0,0,3180) rot=(0,0,1;0rad)
  PredefinedType = 0
  RidgeLength = 35253.9
  Runs = [5795,5795,5795,5795]
  Thickness = [190,190,190,190]
  VerticalArea = 1.08951e+07
FEATURE [Part::MultiCommon] Common022
  Shapes = -> [Roof013,Structure050]
FEATURE [Part::MultiCommon] Common024
  Shapes = -> [Roof013,Structure051]
FEATURE [Part::MultiCommon] Common026
  Shapes = -> [Roof013,Structure049]
FEATURE [Part::Part2DObjectPython] Line1297  label="Line1298"  # Draft 2D object (typed FeaturePython)
  Area = 0
  ChamferSize = 0
  Closed = true
  End = (4545,4805,0)
  FilletRadius = 0
  Length = 6957.93
  MakeFace = false
  Placement = pos=(-200,-200,0) rot=(0,0,1;0rad)
  Points = (2) [(-175,85,0),(4745,5005,0)]
  Start = (-375,-115,0)
  Subdivisions = 0
FEATURE [Part::Part2DObjectPython] Line1298  label="Line1299"  # Draft 2D object (typed FeaturePython)
  Area = 0
  ChamferSize = 0
  Closed = true
  End = (4545,4805,0)
  FilletRadius = 0
  Length = 6957.93
  MakeFace = false
  Placement = pos=(-200,9550,0) rot=(0,0,1;0rad)
  Points = (2) [(-175,175,0),(4745,-4745,0)]
  Start = (-375,9725,0)
  Subdivisions = 0
FEATURE [Part::Part2DObjectPython] Line1299  label="Line1300"  # Draft 2D object (typed FeaturePython)
  Area = 0
  ChamferSize = 0
  Closed = true
  End = (8705,4805,0)
  FilletRadius = 0
  Length = 6957.93
  MakeFace = false
  Placement = pos=(13450,9550,0) rot=(0,0,1;0rad)
  Points = (2) [(175,175,0),(-4745,-4745,0)]
  Start = (13625,9725,0)
  Subdivisions = 0
FEATURE [Part::Part2DObjectPython] Line1300  label="Line1301"  # Draft 2D object (typed FeaturePython)
  Area = 0
  ChamferSize = 0
  Closed = true
  End = (8705,4805,0)
  FilletRadius = 0
  Length = 6957.93
  MakeFace = false
  Placement = pos=(13450,-200,0) rot=(0,0,1;0rad)
  Points = (2) [(175,85,0),(-4745,5005,0)]
  Start = (13625,-115,0)
  Subdivisions = 0
FEATURE [Part::Part2DObjectPython] Line1301  label="Line1302"  # Draft 2D object (typed FeaturePython)
  Area = 0
  ChamferSize = 0
  Closed = true
  End = (8705,4805,0)
  FilletRadius = 0
  Length = 4160
  MakeFace = false
  Placement = pos=(4675,4675,0) rot=(0,0,1;0rad)
  Points = (2) [(-130,130,0),(4030,130,0)]
  Start = (4545,4805,0)
  Subdivisions = 0
FEATURE [Part::FeaturePython] Wall169  label="Стена"  # Arch/BIM 166 (typed FeaturePython)
  Align = 2
  Area = 2.43528e+07
  Base = -> Line1297
  BlockHeight = 0
  BlockLength = 0
  CountBroken = 0
  CountEntire = 0
  Face = 0
  Height = 3500
  HorizontalArea = 1.04369e+06
  IfcData = attributes={"GlobalId": {"name": "GlobalId", "type": "IfcGloballyUniqueId", "is_enum": false, "enum_values": []}, "Description": {"... (+533 chars omitted),+1 more (map truncated)
  IfcType = 166
  Joint = 0
  Length = 6957.93
  MakeBlocks = false
  MoveBase = false
  MoveWithHost = false
  Normal = (0,0,0)
  OffsetFirst = 0
  OffsetSecond = 0
  PerimeterLength = 14215.9
  Placement = pos=(0,0,3160) rot=(0,0,1;0rad)
  PredefinedType = 0
  VerticalArea = 4.97555e+07
  Width = 150
FEATURE [Part::FeaturePython] Wall170  label="Стена001"  # Arch/BIM 166 (typed FeaturePython)
  Align = 2
  Area = 2.43528e+07
  Base = -> Line1298
  BlockHeight = 0
  BlockLength = 0
  CountBroken = 0
  CountEntire = 0
  Face = 0
  Height = 3500
  HorizontalArea = 1.04369e+06
  IfcData = attributes={"GlobalId": {"name": "GlobalId", "type": "IfcGloballyUniqueId", "is_enum": false, "enum_values": []}, "Description": {"... (+533 chars omitted),+1 more (map truncated)
  IfcType = 166
  Joint = 0
  Length = 6957.93
  MakeBlocks = false
  MoveBase = false
  MoveWithHost = false
  Normal = (0,0,0)
  OffsetFirst = 0
  OffsetSecond = 0
  PerimeterLength = 14215.9
  Placement = pos=(0,0,3160) rot=(0,0,1;0rad)
  PredefinedType = 0
  VerticalArea = 4.97555e+07
  Width = 150
FEATURE [Part::FeaturePython] Wall171  label="Стена002"  # Arch/BIM 166 (typed FeaturePython)
  Align = 2
  Area = 2.43528e+07
  Base = -> Line1299
  BlockHeight = 0
  BlockLength = 0
  CountBroken = 0
  CountEntire = 0
  Face = 0
  Height = 3500
  HorizontalArea = 1.04369e+06
  IfcData = attributes={"GlobalId": {"name": "GlobalId", "type": "IfcGloballyUniqueId", "is_enum": false, "enum_values": []}, "Description": {"... (+533 chars omitted),+1 more (map truncated)
  IfcType = 166
  Joint = 0
  Length = 6957.93
  MakeBlocks = false
  MoveBase = false
  MoveWithHost = false
  Normal = (0,0,0)
  OffsetFirst = 0
  OffsetSecond = 0
  PerimeterLength = 14215.9
  Placement = pos=(0,0,3160) rot=(0,0,1;0rad)
  PredefinedType = 0
  VerticalArea = 4.97555e+07
  Width = 150
FEATURE [Part::FeaturePython] Wall172  label="Стена003"  # Arch/BIM 166 (typed FeaturePython)
  Align = 2
  Area = 2.43528e+07
  Base = -> Line1300
  BlockHeight = 0
  BlockLength = 0
  CountBroken = 0
  CountEntire = 0
  Face = 0
  Height = 3500
  HorizontalArea = 1.04369e+06
  IfcData = attributes={"GlobalId": {"name": "GlobalId", "type": "IfcGloballyUniqueId", "is_enum": false, "enum_values": []}, "Description": {"... (+533 chars omitted),+1 more (map truncated)
  IfcType = 166
  Joint = 0
  Length = 6957.93
  MakeBlocks = false
  MoveBase = false
  MoveWithHost = false
  Normal = (0,0,0)
  OffsetFirst = 0
  OffsetSecond = 0
  PerimeterLength = 14215.9
  Placement = pos=(0,0,3160) rot=(0,0,1;0rad)
  PredefinedType = 0
  VerticalArea = 4.97555e+07
  Width = 150
FEATURE [Part::FeaturePython] Wall173  label="Стена004"  # Arch/BIM 166 (typed FeaturePython)
  Align = 2
  Area = 14560000
  Base = -> Line1301
  BlockHeight = 0
  BlockLength = 0
  CountBroken = 0
  CountEntire = 0
  Face = 0
  Height = 3500
  HorizontalArea = 208000
  IfcData = attributes={"GlobalId": {"name": "GlobalId", "type": "IfcGloballyUniqueId", "is_enum": false, "enum_values": []}, "Description": {"... (+533 chars omitted),+1 more (map truncated)
  IfcType = 166
  Joint = 0
  Length = 4160
  MakeBlocks = false
  MoveBase = false
  MoveWithHost = false
  Normal = (0,0,0)
  OffsetFirst = 0
  OffsetSecond = 0
  PerimeterLength = 8420
  Placement = pos=(0,0,3160) rot=(0,0,1;0rad)
  PredefinedType = 0
  VerticalArea = 2.947e+07
  Width = 50
FEATURE [Part::MultiFuse] Fusion
  Shapes = -> [Wall169,Wall170,Wall171,Wall172,Wall173]
FEATURE [Part::MultiCommon] Common028  label="Диагональные стропила"
  Shapes = -> [Fusion,Roof013]
FEATURE [Part::Part2DObjectPython] Line1302  label="ось фундамента внутр.стены002"  # Draft 2D object (typed FeaturePython)
  ChamferSize = 0
  Closed = true
  End = (9400,4025,0)
  FilletRadius = 0
  Length = 9400
  MakeFace = false
  Placement = pos=(7825,3025,0) rot=(0,0,1;1.5708rad)
  Points = (2) [(1000,7825,0),(1000,-1575,0)]
  Start = (0,4025,0)
  Subdivisions = 0
FEATURE [Part::FeaturePython] Wall174  label="фундамент внутр.стена003"  # Arch/BIM 166 (typed FeaturePython)
  Align = 2
  Area = 4.7e+06
  Base = -> Line1302
  BlockHeight = 0
  BlockLength = 0
  CountBroken = 0
  CountEntire = 0
  Face = 0
  Height = 500
  HorizontalArea = 2.35e+06
  IfcType = 166
  Joint = 0
  Length = 9400
  MakeBlocks = false
  MoveBase = false
  MoveWithHost = false
  Normal = (0,0,-1)
  OffsetFirst = 0
  OffsetSecond = 0
  PerimeterLength = 19300
  Placement = pos=(0,0,-180) rot=(0,0,1;0rad)
  PredefinedType = 0
  VerticalArea = 9.65e+06
  Width = 250
FEATURE [Part::FeaturePython] Wall175  label="фундамент внутр. стена 003"  # Arch/BIM 166 (typed FeaturePython)
  Additions = -> [Wall174]
  Align = 2
  Area = 2.82e+06
  Base = -> Line1302
  BlockHeight = 0
  BlockLength = 0
  CountBroken = 0
  CountEntire = 0
  Face = 0
  Height = 300
  HorizontalArea = 4.7e+06
  IfcType = 166
  Joint = 0
  Length = 9400
  MakeBlocks = false
  MoveBase = false
  MoveWithHost = false
  Normal = (0,0,-1)
  OffsetFirst = 0
  OffsetSecond = 0
  PerimeterLength = 28620
  Placement = pos=(0,0,-680) rot=(0,0,1;0rad)
  PredefinedType = 0
  VerticalArea = 1.559e+07
  Width = 500
FEATURE [Part::FeaturePython] Roof014  label="Крыша объём кобылок"  # Arch/BIM 113 (typed FeaturePython)
  Angles = [28,28,28,28]
  Base = -> Wire691
  BorderLength = 92920
  Face = 0
  Flip = false
  Heights = [425.368,425.368,425.368,425.368]
  HorizontalArea = 37168000
  IdRel = [-1,-1,-1,-1]
  IfcData = attributes={"GlobalId": {"name": "GlobalId", "type": "IfcGloballyUniqueId", "is_enum": false, "enum_values": []}, "Description": {"... (+613 chars omitted),+1 more (map truncated)
  IfcType = 113
  MoveBase = false
  MoveWithHost = false
  Overhang = [0,0,0,0]
  PerimeterLength = 0
  Placement = pos=(0,0,2820) rot=(0,0,1;0rad)
  PredefinedType = 0
  RidgeLength = 4834.77
  Runs = [800,800,800,800]
  Thickness = [100,100,100,100]
  VerticalArea = 1.05238e+07
FEATURE [Part::Part2DObjectPython] Circle098  label="Circle099"  # Draft 2D object (typed FeaturePython)
  Area = 0
  FirstAngle = 0
  LastAngle = 0
  MakeFace = false
  Placement = pos=(11626.7,117.473,0) rot=(0,0,1;0rad)
  Radius = 75
FEATURE [Part::FeaturePython] Array019  # Draft array (typed FeaturePython)
  Angle = 360
  ArrayType = 0
  Axis = (0,0,1)
  Base = -> Circle098
  Center = (0,0,0)
  Fuse = false
  IntervalAxis = (0,0,0)
  IntervalX = (250,0,0)
  IntervalY = (0,250,0)
  IntervalZ = (0,0,1)
  NumberPolar = 1
  NumberX = 2
  NumberY = 2
  NumberZ = 1
  Placement = pos=(-250,0,0) rot=(0,0,1;0rad)
FEATURE [Part::Extrusion] Extrude058  label="Панель индукционная"
  Base = -> Array019
  Dir = (0,0,1)
  DirMode = 2
  FaceMakerClass = Part::FaceMakerBullseye
  LengthFwd = 50
  LengthRev = 0
  Placement = pos=(0,0,800) rot=(0,0,1;0rad)
  Solid = true
  Symmetric = false
FEATURE [Part::MultiFuse] Fusion044  label="Шкаф с плитой 001"
  Shapes = -> [Box3205,Extrude058]
FEATURE [Part::Box] Box3207  label="ПММ_45_002"
  AttacherType = Attacher::AttachEngine3D
  Height = 700
  Length = 450
  Placement = pos=(12440,1345,100) rot=(0,0,1;1.5708rad)
  Width = 500
FEATURE [Part::Box] Box3209  label="ДШ_001"
  AttacherType = Attacher::AttachEngine3D
  Height = 500
  Length = 500
  Placement = pos=(10740,90,450) rot=(0,0,1;1.5708rad)
  Width = 580
FEATURE [Part::Box] Box3211  label="камин топка 700"
  AttacherType = Attacher::AttachEngine3D
  Height = 500
  Length = 800
  Placement = pos=(8750,1885,800) rot=(0,0,1;0rad)
  Width = 500
FEATURE [Part::Box] Box3215  label="Душ 100*80"
  AttacherType = Attacher::AttachEngine3D
  Height = 5
  Length = 900
  Placement = pos=(6950,3825,0) rot=(0,0,1;0rad)
  Width = 1500
FEATURE [Part::Part2DObjectPython] Rectangle3000  # Draft 2D object (typed FeaturePython)
  Area = 0
  ChamferSize = 0
  Columns = 1
  FilletRadius = 0
  Height = 1500
  Length = 900
  MakeFace = false
  Placement = pos=(6950,3825,0) rot=(0,0,1;0rad)
  Rows = 1
FEATURE [Part::Part2DObjectPython] Rectangle3004  # Draft 2D object (typed FeaturePython)
  ChamferSize = 0
  Columns = 1
  FilletRadius = 0
  Height = 600
  Length = 600
  MakeFace = true
  Placement = pos=(8250,-25,0) rot=(0,0,1;0rad)
  Rows = 1
FEATURE [Part::Part2DObjectPython] ShapeString185  # Draft 2D object (typed FeaturePython)
  FontFile = <path>
  Placement = pos=(8472.79,91.4359,0) rot=(0,0,1;0rad)
  Size = 300
  String = *
  Tracking = 0
FEATURE [Part::Part2DObjectPython] ShapeString186  # Draft 2D object (typed FeaturePython)
  FontFile = <path>
  Placement = pos=(10206,195.637,0) rot=(0,0,1;0rad)
  Size = 200
  String = ДШ
  Tracking = 0
FEATURE [Part::FeaturePython] Wall184  label="МЗЛФ нижняя часть"  # Arch/BIM 166 (typed FeaturePython)
  Align = 0
  Area = 24108000
  Base = -> Rectangle2788
  BlockHeight = 0
  BlockLength = 0
  CountBroken = 0
  CountEntire = 0
  Face = 0
  Height = 600
  HorizontalArea = 1.4553e+07
  IfcData = attributes={"GlobalId": {"name": "GlobalId", "type": "IfcGloballyUniqueId", "is_enum": false, "enum_values": []}, "Description": {"... (+533 chars omitted),+1 more (map truncated)
  IfcType = 166
  Joint = 0
  Length = 40180
  MakeBlocks = false
  MoveBase = false
  MoveWithHost = false
  Normal = (0,0,0)
  OffsetFirst = 0
  OffsetSecond = 0
  PerimeterLength = 42980
  Placement = pos=(0,0,-980) rot=(0,0,1;0rad)
  PredefinedType = 0
  VerticalArea = 49896000
  Width = 350
FEATURE [Part::Part2DObjectPython] Rectangle3023  # Draft 2D object (typed FeaturePython)
  ChamferSize = 0
  Columns = 1
  FilletRadius = 0
  Height = 300
  Length = 500
  MakeFace = true
  Placement = pos=(11190,4065,0) rot=(0,0,1;0rad)
  Rows = 1
FEATURE [Part::Part2DObjectPython] Rectangle3024  # Draft 2D object (typed FeaturePython)
  ChamferSize = 0
  Columns = 1
  FilletRadius = 0
  Height = 300
  Length = 500
  MakeFace = true
  Placement = pos=(11190,2965,0) rot=(0,0,1;0rad)
  Rows = 1
FEATURE [Part::Part2DObjectPython] Rectangle3026  # Draft 2D object (typed FeaturePython)
  Area = 0
  ChamferSize = 0
  Columns = 1
  FilletRadius = 0
  Height = 490
  Length = 450
  MakeFace = false
  Placement = pos=(12440,1330,0) rot=(0,0,1;1.5708rad)
  Rows = 1
FEATURE [Part::Part2DObjectPython] Line1316  # Draft 2D object (typed FeaturePython)
  ChamferSize = 0
  Closed = true
  End = (3490,2335,0)
  FilletRadius = 0
  Length = 5970
  MakeFace = false
  Placement = pos=(4400,5635,0) rot=(0,0,-1;1.5708rad)
  Points = (2) [(3300,5060,0),(3300,-910,0)]
  Start = (9460,2335,0)
  Subdivisions = 0
FEATURE [Part::Part2DObjectPython] Rectangle3032  # Draft 2D object (typed FeaturePython)
  ChamferSize = 0
  Columns = 1
  FilletRadius = 75
  Height = 1000
  Length = 500
  MakeFace = true
  Placement = pos=(10350,5100,0) rot=(0,0,1;0rad)
  Rows = 1
FEATURE [Part::Part2DObjectPython] Line1317  # Draft 2D object (typed FeaturePython)
  Area = 0
  ChamferSize = 0
  Closed = false
  End = (10128.9,732.87,0)
  FilletRadius = 0
  Length = 600
  MakeFace = true
  Placement = pos=(9550,575,0) rot=(0,0,1;0rad)
  Points = (2) [(0,0,0),(578.858,157.87,0)]
  Start = (9550,575,0)
  Subdivisions = 0
FEATURE [Part::Part2DObjectPython] Rectangle3046  label="Шкаф 60 015"  # Draft 2D object (typed FeaturePython)
  Area = 498000
  ChamferSize = 0
  Columns = 1
  FilletRadius = 0
  Height = 1245
  Length = 400
  MakeFace = true
  Placement = pos=(-30,6240,0) rot=(0,0,1;0rad)
  Rows = 1
FEATURE [Part::Part2DObjectPython] Line1323  # Draft 2D object (typed FeaturePython)
  ChamferSize = 0
  Closed = true
  End = (8700,1875,0)
  FilletRadius = 0
  Length = 420
  MakeFace = false
  Placement = pos=(10280,1880,0) rot=(0,0,1;0rad)
  Points = (2) [(-1580,415,0),(-1580,-5,0)]
  Start = (8700,2295,0)
  Subdivisions = 0
FEATURE [Part::FeaturePython] Wall187  label="перегородка 044"  # Arch/BIM 166 (typed FeaturePython)
  Align = 2
  Area = 1176000
  Base = -> Line1323
  BlockHeight = 250
  BlockLength = 0
  CountBroken = 0
  CountEntire = 0
  Face = 0
  Height = 2800
  HorizontalArea = 33600
  IfcType = 166
  Joint = 0
  Length = 420
  MakeBlocks = false
  MoveBase = false
  MoveWithHost = false
  Normal = (0,0,0)
  OffsetFirst = 0
  OffsetSecond = 300
  PerimeterLength = 1000
  PredefinedType = 0
  VerticalArea = 2800000
  Width = 80
FEATURE [Part::Part2DObjectPython] Line1324  # Draft 2D object (typed FeaturePython)
  ChamferSize = 0
  Closed = true
  End = (7400,-45,0)
  FilletRadius = 0
  Length = 2340
  MakeFace = false
  Placement = pos=(9485,1900,0) rot=(0,0,1;0rad)
  Points = (2) [(-2085,395,0),(-2085,-1945,0)]
  Start = (7400,2295,0)
  Subdivisions = 0
FEATURE [Part::FeaturePython] Wall188  label="перегородка 045"  # Arch/BIM 166 (typed FeaturePython)
  Align = 2
  Area = 6552000
  Base = -> Line1324
  BlockHeight = 250
  BlockLength = 0
  CountBroken = 0
  CountEntire = 0
  Face = 0
  Height = 2800
  HorizontalArea = 187200
  IfcType = 166
  Joint = 0
  Length = 2340
  MakeBlocks = false
  MoveBase = false
  MoveWithHost = false
  Normal = (0,0,0)
  OffsetFirst = 0
  OffsetSecond = 300
  PerimeterLength = 4840
  PredefinedType = 0
  VerticalArea = 13552000
  Width = 80
FEATURE [Part::Part2DObjectPython] Line1326  # Draft 2D object (typed FeaturePython)
  Area = 0
  ChamferSize = 0
  Closed = true
  End = (14600,5100,0)
  FilletRadius = 0
  Length = 1100
  MakeFace = true
  Placement = pos=(14600,6200,0) rot=(0,0,1;0rad)
  Points = (2) [(0,0,0),(0,-1100,0)]
  Start = (14600,6200,0)
  Subdivisions = 0
FEATURE [Part::Part2DObjectPython] Line1327  # Draft 2D object (typed FeaturePython)
  Area = 0
  ChamferSize = 0
  Closed = false
  End = (14600,6200,0)
  FilletRadius = 0
  Length = 282.843
  MakeFace = true
  Placement = pos=(14400,6400,0) rot=(0,0,1;0rad)
  Points = (2) [(0,0,0),(200,-200,0)]
  Start = (14400,6400,0)
  Subdivisions = 0
FEATURE [Part::Part2DObjectPython] Line1328  # Draft 2D object (typed FeaturePython)
  Area = 0
  ChamferSize = 0
  Closed = false
  End = (14800,6400,0)
  FilletRadius = 0
  Length = 282.843
  MakeFace = true
  Placement = pos=(14600,6200,0) rot=(0,0,1;0rad)
  Points = (2) [(0,0,0),(200,200,0)]
  Start = (14600,6200,0)
  Subdivisions = 0
FEATURE [Part::Part2DObjectPython] Line1329  # Draft 2D object (typed FeaturePython)
  Area = 0
  ChamferSize = 0
  Closed = false
  End = (14400,5500,0)
  FilletRadius = 0
  Length = 447.214
  MakeFace = true
  Placement = pos=(14600,5100,0) rot=(0,0,1;0rad)
  Points = (2) [(0,0,0),(-200,400,0)]
  Start = (14600,5100,0)
  Subdivisions = 0
FEATURE [Part::Part2DObjectPython] Line1330  # Draft 2D object (typed FeaturePython)
  Area = 0
  ChamferSize = 0
  Closed = false
  End = (14800,5500,0)
  FilletRadius = 0
  Length = 447.214
  MakeFace = true
  Placement = pos=(14600,5100,0) rot=(0,0,1;0rad)
  Points = (2) [(0,0,0),(200,400,0)]
  Start = (14600,5100,0)
  Subdivisions = 0
FEATURE [Part::Part2DObjectPython] ShapeString189  # Draft 2D object (typed FeaturePython)
  FontFile = <path>
  Placement = pos=(14506.7,4699.61,0) rot=(0,0,1;0rad)
  Size = 250
  String = С
  Tracking = 0
FEATURE [Part::Part2DObjectPython] ShapeString191  # Draft 2D object (typed FeaturePython)
  FontFile = <path>
  Placement = pos=(14406.7,6499.61,0) rot=(0,0,1;0rad)
  Size = 250
  String = Юг
  Tracking = 0
FEATURE [App::FeaturePython] Dimension010  # Draft dimension (typed FeaturePython)
  Diameter = false
  Dimline = (4870,9000,0)
  Direction = (0,0,0)
  Distance = 2020
  End = (6890,9506.46,0)
  Normal = (0,0,1)
  Start = (4870,9506.46,0)
FEATURE [Part::Part2DObjectPython] Line1340  # Draft 2D object (typed FeaturePython)
  Area = 0
  ChamferSize = 0
  Closed = true
  End = (12570,-425,0)
  FilletRadius = 0
  Length = 13000
  MakeFace = false
  Placement = pos=(-400,-520,0) rot=(0,0,1;0rad)
  Points = (2) [(-30,95,0),(12970,95,0)]
  Start = (-430,-425,0)
  Subdivisions = 0
FEATURE [Part::Part2DObjectPython] Rectangle3074  label="Тёплый контур"  # Draft 2D object (typed FeaturePython)
  Area = 9.44758e+07
  ChamferSize = 0
  Columns = 1
  FilletRadius = 0
  Height = 7510
  Length = 12580
  MakeFace = true
  Placement = pos=(-30,-25,0) rot=(0,0,1;0rad)
  Rows = 1
FEATURE [Part::Part2DObjectPython] Rectangle005  label="Прихожая"  # Draft 2D object (typed FeaturePython)
  Area = 7507500
  ChamferSize = 0
  Columns = 1
  FilletRadius = 0
  Height = 2310
  Length = 3250
  MakeFace = true
  Placement = pos=(4100,-25,0) rot=(0,0,1;0rad)
  Rows = 1
FEATURE [Part::Part2DObjectPython] Rectangle006  label="Душ"  # Draft 2D object (typed FeaturePython)
  Area = 1.35e+06
  ChamferSize = 0
  Columns = 1
  FilletRadius = 0
  Height = 1500
  Length = 900
  MakeFace = true
  Placement = pos=(6950,3825,0) rot=(0,0,1;0rad)
  Rows = 1
FEATURE [Part::Part2DObjectPython] Rectangle008  label="Спальня 1 этаж"  # Draft 2D object (typed FeaturePython)
  Area = 1.7751e+07
  ChamferSize = 0
  Columns = 1
  FilletRadius = 0
  Height = 3660
  Length = 4850
  MakeFace = true
  Placement = pos=(-30,3825,0) rot=(0,0,1;0rad)
  Rows = 1
FEATURE [Part::Part2DObjectPython] Rectangle011  label="Коридор"  # Draft 2D object (typed FeaturePython)
  Area = 5.658e+06
  ChamferSize = 0
  Columns = 1
  FilletRadius = 0
  Height = 1150
  Length = 4920
  MakeFace = true
  Placement = pos=(3500,2385,0) rot=(0,0,1;0rad)
  Rows = 1
FEATURE [Part::Part2DObjectPython] Line1341  # Draft 2D object (typed FeaturePython)
  Area = 0
  ChamferSize = 0
  Closed = true
  End = (-430,-45,0)
  FilletRadius = 0
  Length = 7930
  MakeFace = false
  Placement = pos=(-345,-365,0) rot=(0,0,1;0rad)
  Points = (2) [(-85,8250,0),(-85,320,0)]
  Start = (-430,7885,0)
  Subdivisions = 0
FEATURE [Part::Part2DObjectPython] Line1342  # Draft 2D object (typed FeaturePython)
  Area = 0
  ChamferSize = 0
  Closed = true
  End = (12950,7505,0)
  FilletRadius = 0
  Length = 7930
  MakeFace = false
  Placement = pos=(-4425,-450,0) rot=(0,0,1;0rad)
  Points = (2) [(17375,25,0),(17375,7955,0)]
  Start = (12950,-425,0)
  Subdivisions = 0
FEATURE [Part::Part2DObjectPython] Line1343  # Draft 2D object (typed FeaturePython)
  Area = 0
  ChamferSize = 0
  Closed = true
  End = (12950,-45,0)
  FilletRadius = 0
  Length = 7930
  MakeFace = false
  Placement = pos=(-4425,-745,0) rot=(0,0,1;0rad)
  Points = (2) [(17375,8630,0),(17375,700,0)]
  Start = (12950,7885,0)
  Subdivisions = 0
FEATURE [Part::Part2DObjectPython] Line1347  # Draft 2D object (typed FeaturePython)
  Area = 0
  ChamferSize = 0
  Closed = true
  End = (-430,7505,0)
  FilletRadius = 0
  Length = 7930
  MakeFace = false
  Placement = pos=(-345,-875,0) rot=(0,0,1;0rad)
  Points = (2) [(-85,450,0),(-85,8380,0)]
  Start = (-430,-425,0)
  Subdivisions = 0
FEATURE [Part::Part2DObjectPython] Line1349  # Draft 2D object (typed FeaturePython)
  Area = 0
  ChamferSize = 0
  Closed = true
  End = (-50,7885,0)
  FilletRadius = 0
  Length = 13000
  MakeFace = false
  Placement = pos=(-4925,-305,0) rot=(0,0,1;0rad)
  Points = (2) [(17875,8190,0),(4875,8190,0)]
  Start = (12950,7885,0)
  Subdivisions = 0
FEATURE [Part::Part2DObjectPython] Line1350  # Draft 2D object (typed FeaturePython)
  Area = 0
  ChamferSize = 0
  Closed = true
  End = (12570,7885,0)
  FilletRadius = 0
  Length = 13000
  MakeFace = false
  Placement = pos=(-345,-305,0) rot=(0,0,1;0rad)
  Points = (2) [(-85,8190,0),(12915,8190,0)]
  Start = (-430,7885,0)
  Subdivisions = 0
FEATURE [Part::Part2DObjectPython] Line1351  # Draft 2D object (typed FeaturePython)
  Area = 0
  ChamferSize = 0
  Closed = true
  End = (-50,-425,0)
  FilletRadius = 0
  Length = 13000
  MakeFace = false
  Placement = pos=(-4925,-465,0) rot=(0,0,1;0rad)
  Points = (2) [(17875,40,0),(4875,40,0)]
  Start = (12950,-425,0)
  Subdivisions = 0
FEATURE [Part::Part2DObjectPython] Rectangle016  label="Контур_по_блоку_ЛСР_38_шаг255"  # Draft 2D object (typed FeaturePython)
  Area = 0
  ChamferSize = 0
  Columns = 1
  FilletRadius = 0
  Height = 7550
  Length = 12620
  MakeFace = false
  Placement = pos=(-50,-45,0) rot=(0,0,1;0rad)
  Rows = 1
FEATURE [Part::Part2DObjectPython] Rectangle3075  label="ОК-196-002"  # Draft 2D object (typed FeaturePython)
  ChamferSize = 0
  Columns = 1
  FilletRadius = 0
  Height = 410
  Length = 1960
  MakeFace = true
  Placement = pos=(12550,3280,0) rot=(0,0,-1;1.5708rad)
  Rows = 1
FEATURE [Part::FeaturePython] Structure304  label="Проём-ОК-196-002"  # Arch/BIM 52 (typed FeaturePython)
  Base = -> Rectangle3075
  FaceMaker = 0
  Height = 1386
  HorizontalArea = 803600
  IfcData = complex_attributes={"OwnerHistory": {}, "IsNestedBy": {}, "IsDecomposedBy": {}, "IsDefinedBy": {}, "ObjectPlacement": {}, "Representation":... (+4 chars omitted)
  IfcType = 52
  Length = 0
  MoveBase = false
  MoveWithHost = false
  Nodes = (2) [(4745,-225,0),(4745,-225,1350)]
  NodesOffset = 0
  Normal = (0,0,0)
  PerimeterLength = 4740
  Placement = pos=(0,0,1186) rot=(0,0,1;0rad)
  VerticalArea = 6569640
  Width = 100
FEATURE [Part::Part2DObjectPython] Rectangle3077  label="ОК-92-001"  # Draft 2D object (typed FeaturePython)
  ChamferSize = 0
  Columns = 1
  FilletRadius = 0
  Height = 410
  Length = 920
  MakeFace = true
  Placement = pos=(12550,4970,0) rot=(0,0,-1;1.5708rad)
  Rows = 1
FEATURE [Part::FeaturePython] Structure306  label="Проём-ОК-92-001"  # Arch/BIM 52 (typed FeaturePython)
  Base = -> Rectangle3077
  FaceMaker = 0
  Height = 1386
  HorizontalArea = 377200
  IfcData = complex_attributes={"OwnerHistory": {}, "IsNestedBy": {}, "IsDecomposedBy": {}, "IsDefinedBy": {}, "ObjectPlacement": {}, "Representation":... (+4 chars omitted)
  IfcType = 52
  Length = 0
  MoveBase = false
  MoveWithHost = false
  Nodes = (2) [(1035,250,0),(1035,250,600)]
  NodesOffset = 0
  Normal = (0,0,0)
  PerimeterLength = 2660
  Placement = pos=(0,0,1186) rot=(0,0,1;0rad)
  VerticalArea = 3.68676e+06
  Width = 100
FEATURE [Part::Part2DObjectPython] Rectangle3079  label="ОК-196-001"  # Draft 2D object (typed FeaturePython)
  ChamferSize = 0
  Columns = 1
  FilletRadius = 0
  Height = 410
  Length = 1960
  MakeFace = true
  Placement = pos=(8595,7485,0) rot=(0,0,1;0rad)
  Rows = 1
FEATURE [Part::FeaturePython] Structure308  label="Проём-ОК-196-001"  # Arch/BIM 52 (typed FeaturePython)
  Base = -> Rectangle3079
  FaceMaker = 0
  Height = 2772
  HorizontalArea = 803600
  IfcData = complex_attributes={"OwnerHistory": {}, "IsNestedBy": {}, "IsDecomposedBy": {}, "IsDefinedBy": {}, "ObjectPlacement": {}, "Representation":... (+4 chars omitted)
  IfcType = 52
  Length = 0
  MoveBase = false
  MoveWithHost = false
  Nodes = (2) [(1035,250,0),(1035,250,600)]
  NodesOffset = 0
  Normal = (0,0,0)
  PerimeterLength = 4740
  Placement = pos=(0,0,-200) rot=(0,0,1;0rad)
  VerticalArea = 13139280
  Width = 100
FEATURE [Part::Part2DObjectPython] Rectangle3084  label="ОК-92-002"  # Draft 2D object (typed FeaturePython)
  ChamferSize = 0
  Columns = 1
  FilletRadius = 0
  Height = 410
  Length = 920
  MakeFace = true
  Placement = pos=(5085,7485,0) rot=(0,0,1;0rad)
  Rows = 1
FEATURE [Part::FeaturePython] Structure313  label="Проём-ОК-92-002"  # Arch/BIM 52 (typed FeaturePython)
  Base = -> Rectangle3084
  FaceMaker = 0
  Height = 1617
  HorizontalArea = 377200
  IfcData = complex_attributes={"OwnerHistory": {}, "IsNestedBy": {}, "IsDecomposedBy": {}, "IsDefinedBy": {}, "ObjectPlacement": {}, "Representation":... (+4 chars omitted)
  IfcType = 52
  Length = 0
  MoveBase = false
  MoveWithHost = false
  Nodes = (2) [(1035,250,0),(1035,250,600)]
  NodesOffset = 0
  Normal = (0,0,0)
  PerimeterLength = 2660
  Placement = pos=(0,0,955) rot=(0,0,1;0rad)
  VerticalArea = 4301220
  Width = 100
FEATURE [Part::Part2DObjectPython] Rectangle3086  label="ОК-196-003"  # Draft 2D object (typed FeaturePython)
  ChamferSize = 0
  Columns = 1
  FilletRadius = 0
  Height = 410
  Length = 1960
  MakeFace = true
  Placement = pos=(1965,7485,0) rot=(0,0,1;0rad)
  Rows = 1
FEATURE [Part::FeaturePython] Structure315  label="Проём-ОК-196-003"  # Arch/BIM 52 (typed FeaturePython)
  Base = -> Rectangle3086
  FaceMaker = 0
  Height = 1617
  HorizontalArea = 803600
  IfcData = complex_attributes={"OwnerHistory": {}, "IsNestedBy": {}, "IsDecomposedBy": {}, "IsDefinedBy": {}, "ObjectPlacement": {}, "Representation":... (+4 chars omitted)
  IfcType = 52
  Length = 0
  MoveBase = false
  MoveWithHost = false
  Nodes = (2) [(1035,250,0),(1035,250,600)]
  NodesOffset = 0
  Normal = (0,0,0)
  PerimeterLength = 4740
  Placement = pos=(0,0,955) rot=(0,0,1;0rad)
  VerticalArea = 7664580
  Width = 100
FEATURE [Part::Part2DObjectPython] Rectangle3095  label="ПР352-001"  # Draft 2D object (typed FeaturePython)
  ChamferSize = 0
  Columns = 1
  FilletRadius = 0
  Height = 3520
  Length = 290
  MakeFace = true
  Placement = pos=(11920,3535,0) rot=(0,0,1;1.5708rad)
  Rows = 1
FEATURE [Part::FeaturePython] Structure317  label="Проём-ПР352"  # Arch/BIM 52 (typed FeaturePython)
  Base = -> Rectangle3095
  FaceMaker = 0
  Height = 2700
  HorizontalArea = 1.0208e+06
  IfcData = complex_attributes={"OwnerHistory": {}, "IsNestedBy": {}, "IsDecomposedBy": {}, "IsDefinedBy": {}, "ObjectPlacement": {}, "Representation":... (+4 chars omitted)
  IfcType = 52
  Length = 0
  MoveBase = false
  MoveWithHost = false
  Nodes = (2) [(8200,3800,0),(8200,3800,2250)]
  NodesOffset = 0
  Normal = (0,0,0)
  PerimeterLength = 7620
  Placement = pos=(0,0,-200) rot=(0,0,1;0rad)
  VerticalArea = 20574000
  Width = 100
FEATURE [Part::Part2DObjectPython] Rectangle3104  # Draft 2D object (typed FeaturePython)
  ChamferSize = 0
  Columns = 1
  FilletRadius = 0
  Height = 1060
  Length = 310
  MakeFace = true
  Placement = pos=(12240,3825,0) rot=(0,0,1;0rad)
  Rows = 1
FEATURE [App::FeaturePython] Dimension002  # Draft dimension (typed FeaturePython)
  Diameter = false
  Dimline = (6500,-1800,0)
  Direction = (0,0,0)
  Distance = 13640
  End = (13080,-555,0)
  Normal = (0,0,1)
  Start = (-560,-555,0)
FEATURE [App::FeaturePython] Dimension011  # Draft dimension (typed FeaturePython)
  Diameter = false
  Dimline = (4150,-1500,0)
  Direction = (0,0,0)
  Distance = 3350
  End = (7400,-2107.94,0)
  Normal = (0,0,1)
  Start = (4050,-2107.94,0)
FEATURE [App::FeaturePython] Dimension012  # Draft dimension (typed FeaturePython)
  Diameter = false
  Dimline = (9500,-1500,0)
  Direction = (0,0,0)
  Distance = 2100
  End = (9500,-2107.94,0)
  Normal = (0,0,1)
  Start = (7400,-2107.94,0)
FEATURE [App::FeaturePython] Dimension013  # Draft dimension (typed FeaturePython)
  Diameter = false
  Dimline = (1700,-1500,0)
  Direction = (0,0,0)
  Distance = 4290
  End = (4050,-2107.94,0)
  Normal = (0,0,1)
  Start = (-240,-2107.94,0)
FEATURE [App::FeaturePython] Dimension014  # Draft dimension (typed FeaturePython)
  Diameter = false
  Dimline = (7910,9000,0)
  Direction = (0,0,0)
  Distance = 4850
  End = (12760,9506.46,0)
  Normal = (0,0,1)
  Start = (7910,9506.46,0)
FEATURE [App::FeaturePython] Dimension015  # Draft dimension (typed FeaturePython)
  Diameter = false
  Dimline = (-1200,2335,0)
  Direction = (0,0,0)
  Distance = 2570
  End = (-1836.7,2335,0)
  Normal = (0,0,1)
  Start = (-1836.7,-235,0)
FEATURE [App::FeaturePython] Dimension016  # Draft dimension (typed FeaturePython)
  Diameter = false
  Dimline = (3550,-1350,0)
  Direction = (0,0,0)
  Distance = 600
  End = (4050,-2107.94,0)
  Normal = (0,0,1)
  Start = (3450,-2107.94,0)
FEATURE [App::FeaturePython] Dimension018  # Draft dimension (typed FeaturePython)
  Diameter = false
  Dimline = (8700,4200,0)
  Direction = (0,0,0)
  Distance = 290
  End = (8420,3825,0)
  Normal = (0,0,1)
  Start = (8420,3535,0)
FEATURE [Sketcher::SketchObject] Sketch301  label="Профиль ПНО 150-001"
  FullyConstrained = true
  Placement = pos=(0,0,0) rot=(1,0,0;1.5708rad)
  sketch-geometry (23):
    g0: LineSegment StartX=0 StartY=0 StartZ=0 EndX=1490 EndY=0 EndZ=0
    g1: LineSegment StartX=1490 StartY=0 StartZ=0 EndX=1490 EndY=160 EndZ=0
    g2: LineSegment StartX=1490 StartY=160 StartZ=0 EndX=0 EndY=160 EndZ=0
    g3: LineSegment StartX=0 StartY=160 StartZ=0 EndX=0 EndY=0 EndZ=0
    g4: Circle CenterX=115 CenterY=80 CenterZ=0 NormalX=0 NormalY=0 NormalZ=1 AngleXU=0 Radius=50
    g5: Circle CenterX=255 CenterY=80 CenterZ=0 NormalX=0 NormalY=0 NormalZ=1 AngleXU=0 Radius=50
    g6: LineSegment StartX=115 StartY=80 StartZ=0 EndX=255 EndY=80 EndZ=0
    g7: Circle CenterX=395 CenterY=80 CenterZ=0 NormalX=0 NormalY=0 NormalZ=1 AngleXU=0 Radius=50
    g8: LineSegment StartX=255 StartY=80 StartZ=0 EndX=395 EndY=80 EndZ=0
    g9: Circle CenterX=535 CenterY=80 CenterZ=0 NormalX=0 NormalY=0 NormalZ=1 AngleXU=0 Radius=50
    g10: LineSegment StartX=395 StartY=80 StartZ=0 EndX=535 EndY=80 EndZ=0
    g11: Circle CenterX=675 CenterY=80 CenterZ=0 NormalX=0 NormalY=0 NormalZ=1 AngleXU=0 Radius=50
    g12: LineSegment StartX=535 StartY=80 StartZ=0 EndX=675 EndY=80 EndZ=0
    g13: Circle CenterX=815 CenterY=80 CenterZ=0 NormalX=0 NormalY=0 NormalZ=1 AngleXU=0 Radius=50
    g14: LineSegment StartX=675 StartY=80 StartZ=0 EndX=815 EndY=80 EndZ=0
    g15: Circle CenterX=955 CenterY=80 CenterZ=0 NormalX=0 NormalY=0 NormalZ=1 AngleXU=0 Radius=50
    g16: Circle CenterX=1095 CenterY=80 CenterZ=0 NormalX=0 NormalY=0 NormalZ=1 AngleXU=0 Radius=50
    g17: Circle CenterX=1235 CenterY=80 CenterZ=0 NormalX=0 NormalY=0 NormalZ=1 AngleXU=0 Radius=50
    g18: Circle CenterX=1375 CenterY=80 CenterZ=0 NormalX=0 NormalY=0 NormalZ=1 AngleXU=0 Radius=50
    g19: LineSegment StartX=1235 StartY=80 StartZ=0 EndX=1375 EndY=80 EndZ=0
    g20: LineSegment StartX=1095 StartY=80 StartZ=0 EndX=1235 EndY=80 EndZ=0
    g21: LineSegment StartX=955 StartY=80 StartZ=0 EndX=1095 EndY=80 EndZ=0
    g22: LineSegment StartX=815 StartY=80 StartZ=0 EndX=955 EndY=80 EndZ=0
  constraints (59):
    c: Coincident(g0,g1)
    c: Coincident(g1,g2)
    c: Coincident(g2,g3)
    c: Coincident(g3,g0)
    c: Horizontal(g0)
    c: Horizontal(g2)
    c: Vertical(g1)
    c: Vertical(g3)
    c: Coincident(g0,g-1)
    c: DistanceY(g3,g3) = 160
    c: DistanceX(g2,g2) = 1490
    c: Diameter(g4) = 100
    c: DistanceY(g4,g2) = 80
    c: Diameter(g5) = 100
    c: Coincident(g4,g6)
    c: Coincident(g5,g6)
    c: Distance(g6) = 140
    c: Angle(g6) = 0
    c: Diameter(g7) = 100
    c: Coincident(g5,g8)
    c: Coincident(g7,g8)
    c: Equal(g6,g8)
    c: Parallel(g8,g6)
    c: Diameter(g9) = 100
    c: Coincident(g7,g10)
    c: Coincident(g9,g10)
    c: Equal(g6,g10)
    c: Parallel(g10,g6)
    c: Diameter(g11) = 100
    c: Coincident(g9,g12)
    c: Coincident(g11,g12)
    c: Equal(g6,g12)
    c: Parallel(g12,g6)
    c: Diameter(g13) = 100
    c: Coincident(g11,g14)
    c: Coincident(g13,g14)
    c: Equal(g6,g14)
    c: Parallel(g14,g6)
    c: Diameter(g15) = 100
    c: Coincident(g15,g22)
    c: Diameter(g16) = 100
    c: Coincident(g15,g21)
    c: Coincident(g16,g21)
    c: Diameter(g17) = 100
    c: Coincident(g16,g20)
    c: Coincident(g17,g20)
    c: Diameter(g18) = 100
    c: Coincident(g17,g19)
    c: Coincident(g18,g19)
    c: Coincident(g22,g13)
    c: Equal(g14,g22)
    c: Equal(g22,g21)
    c: Equal(g21,g20)
    c: Equal(g20,g19)
    c: Horizontal(g22)
    c: Horizontal(g21)
    c: Horizontal(g20)
    c: Horizontal(g19)
    c: DistanceX(g18,g1) = 115
FEATURE [Part::Part2DObjectPython] Wire760  label="Кабинет"  # Draft 2D object (typed FeaturePython)
  Area = 1.35968e+07
  ChamferSize = 0
  Closed = true
  End = (-30,-25,0)
  FilletRadius = 0
  Length = 15180
  MakeFace = true
  Placement = pos=(-1.819e-13,2985,0) rot=(0,0,1;0rad)
  Points = (6) [(-30,550,0),(3400,550,0),(3400,-700,0),(4000,-700,0),(4000,-3010,0),(-30,-3010,0)]
  Start = (-30,3535,0)
  Subdivisions = 0
FEATURE [Part::Extrusion] Extrude084  label="ПНО 40-15-002"
  Base = -> Sketch301
  Dir = (0,3980,0)
  DirMode = 0
  FaceMakerClass = Part::FaceMakerBullseye
  LengthFwd = 3980
  LengthRev = 0
  Placement = pos=(10,3685,2800) rot=(0,0,1;0rad)
  Solid = true
  Symmetric = false
FEATURE [Part::FeaturePython] Array054  label="ПНО-40-15 3шт."  # Draft array (typed FeaturePython)
  Angle = 360
  ArrayType = 0
  Axis = (0,0,1)
  Base = -> Extrude084
  Center = (0,0,0)
  Fuse = false
  IntervalAxis = (0,0,0)
  IntervalX = (1510,0,0)
  IntervalY = (0,0,0)
  IntervalZ = (0,0,1)
  NumberPolar = 1
  NumberX = 3
  NumberY = 1
  NumberZ = 1
  Placement = pos=(-50,-9.09e-13,0) rot=(0,0,1;0rad)
FEATURE [Part::Part2DObjectPython] Rectangle3121  label="проём в перекрытии 007"  # Draft 2D object (typed FeaturePython)
  Area = 3860700
  ChamferSize = 0
  Columns = 1
  FilletRadius = 0
  Height = 3785
  Length = 1020
  MakeFace = true
  Placement = pos=(6900,3720,0) rot=(0,0,1;0rad)
  Rows = 1
FEATURE [Part::FeaturePython] Structure037  label="проём в перекрытии 004"  # Arch/BIM 52 (typed FeaturePython)
  Base = -> Rectangle3121
  FaceMaker = 0
  Height = 4500
  HorizontalArea = 3860700
  IfcData = complex_attributes={"OwnerHistory": {}, "IsNestedBy": {}, "IsDecomposedBy": {}, "IsDefinedBy": {}, "ObjectPlacement": {}, "Representation":... (+4 chars omitted)
  IfcType = 52
  Length = 0
  MoveBase = false
  MoveWithHost = false
  Nodes = (2) [(4500,6910,0),(4500,6910,4500)]
  NodesOffset = 0
  Normal = (0,0,0)
  PerimeterLength = 9610
  VerticalArea = 43245000
  Width = 100
FEATURE [Part::FeaturePython] Wall063  label="Объем стоек стропильной системы"  # Arch/BIM 166 (typed FeaturePython)
  Align = 0
  Area = 34896000
  Base = -> Rectangle2286
  BlockHeight = 0
  BlockLength = 0
  CountBroken = 0
  CountEntire = 0
  Face = 0
  Height = 1200
  HorizontalArea = 5.5625e+06
  IfcType = 166
  Joint = 0
  Length = 29080
  MakeBlocks = false
  MoveBase = false
  MoveWithHost = false
  Normal = (0,0,0)
  OffsetFirst = 0
  OffsetSecond = 0
  PerimeterLength = 30600
  Placement = pos=(0,0,3210) rot=(0,0,1;0rad)
  PredefinedType = 0
  Subtractions = -> [Structure037]
  VerticalArea = 71868000
  Width = 190
FEATURE [Part::FeaturePython] Wall064  label="опорная доска стоек стропильной системы"  # Arch/BIM 166 (typed FeaturePython)
  Align = 0
  Area = 1454000
  Base = -> Rectangle2286
  BlockHeight = 0
  BlockLength = 0
  CountBroken = 0
  CountEntire = 0
  Face = 0
  Height = 50
  HorizontalArea = 5.5625e+06
  IfcType = 166
  Joint = 0
  Length = 29080
  MakeBlocks = false
  MoveBase = false
  MoveWithHost = false
  Normal = (0,0,0)
  OffsetFirst = 0
  OffsetSecond = 0
  PerimeterLength = 30600
  Placement = pos=(0,0,3160) rot=(0,0,1;0rad)
  PredefinedType = 0
  Subtractions = -> [Structure037]
  VerticalArea = 2994500
  Width = 190
FEATURE [Part::Cut] Cut  label="Объем стоек стропильной системы_01"
  Base = -> Wall063
  Tool = -> Roof013
FEATURE [Part::Part2DObjectPython] Line1357  # Draft 2D object (typed FeaturePython)
  ChamferSize = 0
  Closed = true
  End = (4050,-45,0)
  FilletRadius = 0
  Length = 2340
  MakeFace = false
  Placement = pos=(5330,5450,0) rot=(0,0,-1;1.5708rad)
  Points = (2) [(3155,-1280,0),(5495,-1280,0)]
  Start = (4050,2295,0)
  Subdivisions = 0
FEATURE [Part::FeaturePython] Wall222  label="перегородка 048"  # Arch/BIM 166 (typed FeaturePython)
  Align = 2
  Area = 6.552e+06
  Base = -> Line1357
  BlockHeight = 250
  BlockLength = 0
  CountBroken = 0
  CountEntire = 0
  Face = 0
  Height = 2800
  HorizontalArea = 187200
  IfcType = 166
  Joint = 0
  Length = 2340
  MakeBlocks = false
  MoveBase = false
  MoveWithHost = false
  Normal = (0,0,0)
  OffsetFirst = 300
  OffsetSecond = 50
  PerimeterLength = 4840
  PredefinedType = 0
  VerticalArea = 1.3552e+07
  Width = 80
FEATURE [Part::Part2DObjectPython] Line1358  # Draft 2D object (typed FeaturePython)
  ChamferSize = 0
  Closed = true
  End = (6890,3805,0)
  FilletRadius = 0
  Length = 3700
  MakeFace = false
  Placement = pos=(5520,5450,0) rot=(0,0,-1;1.5708rad)
  Points = (2) [(-2055,1370,0),(1645,1370,0)]
  Start = (6890,7505,0)
  Subdivisions = 0
FEATURE [Part::Part2DObjectPython] Line1359  # Draft 2D object (typed FeaturePython)
  ChamferSize = 0
  Closed = true
  End = (3450,2295,0)
  FilletRadius = 0
  Length = 1260
  MakeFace = false
  Placement = pos=(5230,5435,0) rot=(0,0,-1;1.5708rad)
  Points = (2) [(1880,-1780,0),(3140,-1780,0)]
  Start = (3450,3555,0)
  Subdivisions = 0
FEATURE [Part::FeaturePython] Wall224  label="перегородка 050"  # Arch/BIM 166 (typed FeaturePython)
  Align = 2
  Area = 3.528e+06
  Base = -> Line1359
  BlockHeight = 250
  BlockLength = 0
  CountBroken = 0
  CountEntire = 0
  Face = 0
  Height = 2800
  HorizontalArea = 100800
  IfcType = 166
  Joint = 0
  Length = 1260
  MakeBlocks = false
  MoveBase = false
  MoveWithHost = false
  Normal = (0,0,0)
  OffsetFirst = 300
  OffsetSecond = 50
  PerimeterLength = 2680
  PredefinedType = 0
  VerticalArea = 7.504e+06
  Width = 80
FEATURE [Part::Part2DObjectPython] Line1360  # Draft 2D object (typed FeaturePython)
  ChamferSize = 0
  Closed = true
  End = (9500,2375,0)
  FilletRadius = 0
  Length = 2420
  MakeFace = false
  Placement = pos=(10380,1920,0) rot=(0,0,1;0rad)
  Points = (2) [(-880,-1965,0),(-880,455,0)]
  Start = (9500,-45,0)
  Subdivisions = 0
FEATURE [Part::FeaturePython] Wall225  label="перегородка 052"  # Arch/BIM 166 (typed FeaturePython)
  Align = 2
  Area = 6776000
  Base = -> Line1360
  BlockHeight = 250
  BlockLength = 0
  CountBroken = 0
  CountEntire = 0
  Face = 0
  Height = 2800
  HorizontalArea = 193600
  IfcType = 166
  Joint = 0
  Length = 2420
  MakeBlocks = false
  MoveBase = false
  MoveWithHost = false
  Normal = (0,0,0)
  OffsetFirst = 0
  OffsetSecond = 300
  PerimeterLength = 5000
  PredefinedType = 0
  VerticalArea = 1.4e+07
  Width = 80
FEATURE [Part::Part2DObjectPython] Rectangle3159  # Draft 2D object (typed FeaturePython)
  Area = 0
  ChamferSize = 0
  Columns = 1
  FilletRadius = 0
  Height = 250
  Length = 920
  MakeFace = false
  Placement = pos=(6940,5803.61,0) rot=(0,0,1;0rad)
  Rows = 1
FEATURE [Image::ImagePlane] ImagePlane001  label="Эскиз планировки"
  Placement = pos=(7057.85,2583.46,-10) rot=(0,0,1;0rad)
  XSize = 15451.2
  YSize = 11577
FEATURE [Part::FeaturePython] Array056  label="ПНО-40-10 1шт. (2)"  # Draft array (typed FeaturePython)
  Angle = 360
  ArrayType = 0
  Axis = (0,0,1)
  Base = -> Extrude061
  Center = (0,0,0)
  Fuse = false
  IntervalAxis = (0,0,0)
  IntervalX = (-1010,0,0)
  IntervalY = (0,0,0)
  IntervalZ = (0,0,1)
  NumberPolar = 1
  NumberX = 1
  NumberY = 1
  NumberZ = 1
  Placement = pos=(11560,9.09e-13,0) rot=(0,0,1;0rad)
FEATURE [Part::FeaturePython] Array057  label="ПНО-40-12 1шт."  # Draft array (typed FeaturePython)
  Angle = 360
  ArrayType = 0
  Axis = (0,0,1)
  Base = -> Extrude062
  Center = (0,0,0)
  Fuse = false
  IntervalAxis = (0,0,0)
  IntervalX = (1210,0,0)
  IntervalY = (0,0,0)
  IntervalZ = (0,0,1)
  NumberPolar = 1
  NumberX = 2
  NumberY = 1
  NumberZ = 1
  Placement = pos=(4480,9.09e-13,0) rot=(0,0,1;0rad)
FEATURE [Part::Extrusion] Extrude087  label="ПНО 39-10-6-005"
  Base = -> Sketch249
  Dir = (0,3880,0)
  DirMode = 0
  FaceMakerClass = Part::FaceMakerBullseye
  LengthFwd = 3880
  LengthRev = 0
  Placement = pos=(10,-205,2800) rot=(0,0,1;0rad)
  Solid = true
  Symmetric = false
FEATURE [Part::FeaturePython] Array058  label="ПНО-39-10 1шт. (1)"  # Draft array (typed FeaturePython)
  Angle = 360
  ArrayType = 0
  Axis = (0,0,1)
  Base = -> Extrude087
  Center = (0,0,0)
  Fuse = false
  IntervalAxis = (0,0,0)
  IntervalX = (-1010,0,0)
  IntervalY = (0,0,0)
  IntervalZ = (0,0,1)
  NumberPolar = 1
  NumberX = 1
  NumberY = 1
  NumberZ = 1
  Placement = pos=(-50,0,0) rot=(0,0,1;0rad)
FEATURE [Part::Extrusion] Extrude088  label="ПНО 39-12-8-005"
  Base = -> Sketch231
  Dir = (0,3880,0)
  DirMode = 0
  FaceMakerClass = Part::FaceMakerBullseye
  LengthFwd = 3880
  LengthRev = 0
  Placement = pos=(10,-205,2800) rot=(0,0,1;0rad)
  Solid = true
  Symmetric = false
FEATURE [Part::FeaturePython] Array059  label="ПНО-39-12 2шт."  # Draft array (typed FeaturePython)
  Angle = 360
  ArrayType = 0
  Axis = (0,0,1)
  Base = -> Extrude088
  Center = (0,0,0)
  Fuse = false
  IntervalAxis = (0,0,0)
  IntervalX = (1210,0,0)
  IntervalY = (0,0,0)
  IntervalZ = (0,0,1)
  NumberPolar = 1
  NumberX = 2
  NumberY = 1
  NumberZ = 1
  Placement = pos=(10150,1.364e-12,0) rot=(0,0,1;0rad)
FEATURE [Part::Extrusion] Extrude089  label="ПНО 39-15-003"
  Base = -> Sketch301
  Dir = (0,3880,0)
  DirMode = 0
  FaceMakerClass = Part::FaceMakerBullseye
  LengthFwd = 3880
  LengthRev = 0
  Placement = pos=(10,-205,2800) rot=(0,0,1;0rad)
  Solid = true
  Symmetric = false
FEATURE [Part::FeaturePython] Array060  label="ПНО-39-15 2шт."  # Draft array (typed FeaturePython)
  Angle = 360
  ArrayType = 0
  Axis = (0,0,1)
  Base = -> Extrude089
  Center = (0,0,0)
  Fuse = false
  IntervalAxis = (0,0,0)
  IntervalX = (1510,0,0)
  IntervalY = (0,0,0)
  IntervalZ = (0,0,1)
  NumberPolar = 1
  NumberX = 2
  NumberY = 1
  NumberZ = 1
  Placement = pos=(960,0,0) rot=(0,0,1;0rad)
FEATURE [Part::FeaturePython] Array061  label="ПНО-39-10 1шт. (2)"  # Draft array (typed FeaturePython)
  Angle = 360
  ArrayType = 0
  Axis = (0,0,1)
  Base = -> Extrude087
  Center = (0,0,0)
  Fuse = false
  IntervalAxis = (0,0,0)
  IntervalX = (-1010,0,0)
  IntervalY = (0,0,0)
  IntervalZ = (0,0,1)
  NumberPolar = 1
  NumberX = 1
  NumberY = 1
  NumberZ = 1
  Placement = pos=(6710,4.54e-13,0) rot=(0,0,1;0rad)
FEATURE [Part::Part2DObjectPython] Rectangle3166  label="Д90-017"  # Draft 2D object (typed FeaturePython)
  ChamferSize = 0
  Columns = 1
  FilletRadius = 0
  Height = 120
  Length = 900
  MakeFace = true
  Placement = pos=(6950,3825,0) rot=(0,0,1;1.5708rad)
  Rows = 1
FEATURE [Part::FeaturePython] Structure333  label="Проём-Д90-003"  # Arch/BIM 52 (typed FeaturePython)
  Base = -> Rectangle3166
  FaceMaker = 0
  Height = 2000
  HorizontalArea = 108000
  IfcData = complex_attributes={"OwnerHistory": {}, "IsNestedBy": {}, "IsDecomposedBy": {}, "IsDefinedBy": {}, "ObjectPlacement": {}, "Representation":... (+4 chars omitted)
  IfcType = 52
  Length = 0
  MoveBase = false
  MoveWithHost = false
  Nodes = (2) [(10750,4050,0),(10750,4050,2180)]
  NodesOffset = 0
  Normal = (0,0,0)
  PerimeterLength = 2040
  VerticalArea = 4.08e+06
  Width = 100
FEATURE [Part::Part2DObjectPython] Rectangle3168  label="трап"  # Draft 2D object (typed FeaturePython)
  Area = 0
  ChamferSize = 0
  Columns = 1
  FilletRadius = 0
  Height = 900
  Length = 70
  MakeFace = false
  Placement = pos=(6950,3825,0) rot=(0,0,1;0rad)
  Rows = 1
FEATURE [Part::Box] Box3216  label="шкаф книжн. 001"
  AttacherType = Attacher::AttachEngine3D
  Height = 2700
  Length = 900
  Placement = pos=(320,875,0) rot=(0,0,1;1.5708rad)
  Width = 350
FEATURE [Part::Box] Box3217  label="шкаф 60 одежда 005"
  AttacherType = Attacher::AttachEngine3D
  Height = 2700
  Length = 1400
  Placement = pos=(-30,5625,0) rot=(0,0,1;0rad)
  Width = 600
FEATURE [Part::Box] Box3218  label="шкаф 003"
  AttacherType = Attacher::AttachEngine3D
  Height = 2700
  Length = 1245
  Placement = pos=(370,6225,0) rot=(0,0,1;1.5708rad)
  Width = 400
FEATURE [Part::Part2DObjectPython] Line1383  # Draft 2D object (typed FeaturePython)
  ChamferSize = 0
  Closed = true
  End = (1370,6575,0)
  FilletRadius = 0
  Length = 1900
  MakeFace = false
  Placement = pos=(-1100,7435,0) rot=(0,0,-1;1.5708rad)
  Points = (2) [(2760,2470,0),(860,2470,0)]
  Start = (1370,4675,0)
  Subdivisions = 0
FEATURE [Part::Feature] Fillet004  label="стол письменный"
  Placement = pos=(1140,1890,0) rot=(0,0,1;1.5708rad)
  shape: bbox 750 x 1500 x 750 mm, 30 faces (baked)
FEATURE [Part::Feature] Fusion045  label="стул009"
  Placement = pos=(-462.225,3197.19,0) rot=(0,0,-1;1.5708rad)
  shape: bbox 520 x 480 x 910 mm, 35 faces (baked)
FEATURE [Part::Part2DObjectPython] Wire784  # Draft 2D object (typed FeaturePython)
  Area = 1.11339e+06
  ChamferSize = 0
  Closed = true
  End = (8360,3825,0)
  FilletRadius = 0
  Length = 6499.55
  MakeFace = true
  Placement = pos=(7960,3835,0) rot=(0,0,1;0rad)
  Points = (10) [(1.36424e-11,-10,0),(1.36424e-11,2650,0),(-100,2650,0),(-99.9902,2715.1,0),(-65.0942,2750,0),(1.36424e-11,2750,0),(250,2750.02,0),(350,2750,0),+2 more]
  Start = (7960,3825,0)
  Subdivisions = 0
FEATURE [Part::Cylinder] Cylinder002  label="БКН 120л"
  Angle = 360
  AttacherType = Attacher::AttachEngine3D
  Height = 1010
  Placement = pos=(7730,1990,1000) rot=(0,0,1;0rad)
  Radius = 250
FEATURE [Part::Part2DObjectPython] Arc113  label="Arc114"  # Draft 2D object (typed FeaturePython)
  Area = 0
  FirstAngle = 90
  LastAngle = 180
  MakeFace = false
  Placement = pos=(6660,3635,0) rot=(0,0,1;0rad)
  Radius = 800
FEATURE [Part::Box] Box3220  label="Котёл 24кВт одноконтурн. закртытая камера"
  AttacherType = Attacher::AttachEngine3D
  Height = 700
  Length = 400
  Placement = pos=(8130,2000,1300) rot=(0,0,1;0rad)
  Width = 250
FEATURE [Part::Cylinder] Cylinder003  label="бак расширительный"
  Angle = 360
  AttacherType = Attacher::AttachEngine3D
  Height = 400
  Placement = pos=(7730,1990,2200) rot=(0,0,1;0rad)
  Radius = 175
FEATURE [Part::Box] Box3222  label="грёбенка и насосы"
  AttacherType = Attacher::AttachEngine3D
  Height = 900
  Length = 150
  Placement = pos=(7450,-10,0) rot=(0,0,1;0rad)
  Width = 1700
FEATURE [Part::Extrusion] Extrude090  label="ПНО 39-12-8-006"
  Base = -> Sketch231
  Dir = (0,3880,0)
  DirMode = 0
  FaceMakerClass = Part::FaceMakerBullseye
  LengthFwd = 3880
  LengthRev = 0
  Placement = pos=(7740,-205,2800) rot=(0,0,1;0rad)
  Solid = true
  Symmetric = false
FEATURE [Part::Extrusion] Extrude091  label="ПНО 39-12-8-007"
  Base = -> Sketch231
  Dir = (0,3880,0)
  DirMode = 0
  FaceMakerClass = Part::FaceMakerBullseye
  LengthFwd = 3880
  LengthRev = 0
  Placement = pos=(8950,-205,2800) rot=(0,0,1;0rad)
  Solid = true
  Symmetric = false
FEATURE [Part::Cut] Cut040  label="ПНО-39-12 1шт. рез. (1)"
  Base = -> Extrude090
  Tool = -> Structure158
FEATURE [Part::Cut] Cut041  label="ПНО-39-12 1шт. рез. (2)"
  Base = -> Extrude091
  Tool = -> Structure158
FEATURE [Part::Cylinder] Cylinder004  label="Гидроакк. 100л"
  Angle = 360
  AttacherType = Attacher::AttachEngine3D
  Height = 700
  Placement = pos=(8350,2020,140) rot=(0,0,1;0rad)
  Radius = 220
FEATURE [Part::Box] Box3223  label="Котёл электр. (резерв)"
  AttacherType = Attacher::AttachEngine3D
  Height = 700
  Length = 200
  Placement = pos=(7600,1490,1300) rot=(0,0,1;1.5708rad)
  Width = 150
FEATURE [Part::Extrusion] Extrude057  label="мойка_вырез"
  Base = -> Rectangle2392
  Dir = (0,0,1)
  DirMode = 0
  FaceMakerClass = Part::FaceMakerBullseye
  LengthFwd = 150
  LengthRev = 0
  Placement = pos=(0,0,700) rot=(0,0,1;0rad)
  Solid = true
  Symmetric = false
FEATURE [Part::Box] Box3224  label="шкаф 60 кухонный 012"
  AttacherType = Attacher::AttachEngine3D
  Height = 850
  Length = 2960
  Placement = pos=(12550,575,0) rot=(0,0,1;1.5708rad)
  Width = 600
FEATURE [Part::Cut] Cut043  label="Шкаф с мойкой"
  Base = -> Box3224
  Tool = -> Extrude057
FEATURE [Part::Part2DObjectPython] Wire787  label="Тех.помещение"  # Draft 2D object (typed FeaturePython)
  Area = 4.22e+06
  ChamferSize = 0
  Closed = true
  End = (9450,-25,0)
  FilletRadius = 0
  Length = 8620
  MakeFace = true
  Placement = pos=(7380,35,0) rot=(0,0,1;0rad)
  Points = (6) [(70,-60,0),(70,2250,0),(1270,2250,0),(1270,1750,0),(2070,1750,0),(2070,-60,0)]
  Start = (7450,-25,0)
  Subdivisions = 0
FEATURE [Part::Box] Box3227  label="комод"
  AttacherType = Attacher::AttachEngine3D
  Height = 950
  Length = 310
  Placement = pos=(12240,3825,0) rot=(0,0,1;0rad)
  Width = 750
FEATURE [Part::Part2DObjectPython] Line1390  # Draft 2D object (typed FeaturePython)
  ChamferSize = 0
  Closed = true
  End = (6000,5625,0)
  FilletRadius = 0
  Length = 850
  MakeFace = false
  Placement = pos=(8345,9135,0) rot=(0,0,-1;1.5708rad)
  Points = (2) [(3510,-1495,0),(3510,-2345,0)]
  Start = (6850,5625,0)
  Subdivisions = 0
FEATURE [Part::FeaturePython] Array063  # Draft array (typed FeaturePython)
  Angle = 360
  ArrayType = 0
  Axis = (0,0,1)
  Base = -> Rectangle3159
  Center = (0,0,0)
  Count = 10
  ExpandArray = false
  Fuse = false
  IntervalAxis = (0,0,0)
  IntervalX = (100,0,0)
  IntervalY = (0,-250,0)
  IntervalZ = (0,0,100)
  NumberCircles = 3
  NumberPolar = 5
  NumberX = 1
  NumberY = 10
  NumberZ = 1
  PlacementList = 10 placements: arithmetic series from (6940,5803.61,0) step (0,-250,0) to (6940,3553.61,0)
  RadialDistance = 50
  ScaleList = (10) [(1,1,1),(1,1,1),(1,1,1),(1,1,1),(1,1,1),(1,1,1),(1,1,1),(1,1,1),(1,1,1),(1,1,1)]
  Symmetry = 1
  TangentialDistance = 25
FEATURE [Part::Part2DObjectPython] Line1391  # Draft 2D object (typed FeaturePython)
  ChamferSize = 0
  Closed = true
  End = (6930,5385,0)
  FilletRadius = 0
  Length = 940
  MakeFace = false
  Placement = pos=(10350,5380,0) rot=(0,0,-1;1.5708rad)
  Points = (2) [(-5,-2480,0),(-5,-3420,0)]
  Start = (7870,5385,0)
  Subdivisions = 0
FEATURE [Part::Part2DObjectPython] Line1392  # Draft 2D object (typed FeaturePython)
  Area = 0
  ChamferSize = 0
  Closed = true
  End = (7350,-25,0)
  FilletRadius = 0
  Length = 3250
  MakeFace = true
  Placement = pos=(4210,-10,0) rot=(0,0,1;0rad)
  Points = (2) [(-110,-15,0),(3140,-15,0)]
  Start = (4100,-25,0)
  Subdivisions = 0
FEATURE [Part::Part2DObjectPython] Line1393  # Draft 2D object (typed FeaturePython)
  Area = 0
  ChamferSize = 0
  Closed = true
  End = (9450,-25,0)
  FilletRadius = 0
  Length = 2000
  MakeFace = true
  Placement = pos=(7400,-10,0) rot=(0,0,1;0rad)
  Points = (2) [(50,-15,0),(2050,-15,0)]
  Start = (7450,-25,0)
  Subdivisions = 0
FEATURE [Part::Part2DObjectPython] Wire795  # Draft 2D object (typed FeaturePython)
  Area = 0
  ChamferSize = 0
  Closed = false
  End = (3500,3535,0)
  FilletRadius = 0
  Length = 15610
  MakeFace = true
  Placement = pos=(9500,20,0) rot=(0,0,1;0rad)
  Points = (4) [(50,-45,0),(3050,-45,0),(3050,3515,0),(-6000,3515,0)]
  Start = (9550,-25,0)
  Subdivisions = 0
FEATURE [Part::Part2DObjectPython] Wire796  # Draft 2D object (typed FeaturePython)
  Area = 0
  ChamferSize = 0
  Closed = false
  End = (6940,7485,0)
  FilletRadius = 0
  Length = 13860
  MakeFace = true
  Placement = pos=(7940,3810,0) rot=(0,0,1;0rad)
  Points = (4) [(20,15,0),(4610,15,0),(4610,3675,0),(-1000,3675,0)]
  Start = (7960,3825,0)
  Subdivisions = 0
FEATURE [Part::Part2DObjectPython] Wire797  # Draft 2D object (typed FeaturePython)
  Area = 0
  ChamferSize = 0
  Closed = false
  End = (4820,3825,0)
  FilletRadius = 0
  Length = 13360
  MakeFace = true
  Placement = pos=(4820,7440,0) rot=(0,0,1;0rad)
  Points = (4) [(-9.09495e-13,45,0),(-4850,45,0),(-4850,-3615,0),(-9.09495e-13,-3615,0)]
  Start = (4820,7485,0)
  Subdivisions = 0
FEATURE [Part::Part2DObjectPython] Arc114  label="Arc115"  # Draft 2D object (typed FeaturePython)
  Area = 0
  FirstAngle = 90
  LastAngle = 180
  MakeFace = true
  Placement = pos=(4710,3635,0) rot=(0,0,1;0rad)
  Radius = 800
FEATURE [Part::Part2DObjectPython] Line1394  # Draft 2D object (typed FeaturePython)
  Area = 0
  ChamferSize = 0
  Closed = false
  End = (4710,3635,0)
  FilletRadius = 0
  Length = 800
  MakeFace = true
  Placement = pos=(4710,4435,0) rot=(0,0,1;0rad)
  Points = (2) [(0,0,0),(0,-800,0)]
  Start = (4710,4435,0)
  Subdivisions = 0
FEATURE [Part::Part2DObjectPython] Arc115  label="Arc116"  # Draft 2D object (typed FeaturePython)
  Area = 0
  FirstAngle = -180
  LastAngle = -90
  MakeFace = true
  Placement = pos=(3400,3385,0) rot=(0,0,1;0rad)
  Radius = 800
FEATURE [Part::Part2DObjectPython] Arc116  label="Arc117"  # Draft 2D object (typed FeaturePython)
  Area = 0
  FirstAngle = 180
  LastAngle = 270
  MakeFace = true
  Placement = pos=(6660,2285,0) rot=(0,0,1;0rad)
  Radius = 800
FEATURE [Part::Part2DObjectPython] Line1396  # Draft 2D object (typed FeaturePython)
  Area = 0
  ChamferSize = 0
  Closed = false
  End = (6660,2285,0)
  FilletRadius = 0
  Length = 800
  MakeFace = true
  Placement = pos=(6660,1485,0) rot=(0,0,1;0rad)
  Points = (2) [(0,0,0),(0,800,0)]
  Start = (6660,1485,0)
  Subdivisions = 0
FEATURE [Sketcher::SketchObject] Sketch305
  FullyConstrained = true
  Placement = pos=(4820,6485,0) rot=(0.57735,0.57735,0.57735;2.0944rad)
  sketch-geometry (8):
    g0: LineSegment StartX=0 StartY=0 StartZ=0 EndX=900 EndY=0 EndZ=0
    g1: LineSegment StartX=900 StartY=0 StartZ=0 EndX=900 EndY=2150 EndZ=0
    g2: LineSegment StartX=900 StartY=2150 StartZ=0 EndX=0 EndY=2150 EndZ=0
    g3: LineSegment StartX=0 StartY=2150 StartZ=0 EndX=0 EndY=0 EndZ=0
    g4: LineSegment StartX=50 StartY=0 StartZ=0 EndX=850 EndY=0 EndZ=0
    g5: LineSegment StartX=850 StartY=0 StartZ=0 EndX=850 EndY=2100 EndZ=0
    g6: LineSegment StartX=850 StartY=2100 StartZ=0 EndX=50 EndY=2100 EndZ=0
    g7: LineSegment StartX=50 StartY=2100 StartZ=0 EndX=50 EndY=0 EndZ=0
  constraints (23):
    c: Coincident(g0,g1)
    c: Coincident(g1,g2)
    c: Coincident(g2,g3)
    c: Coincident(g3,g0)
    c: Horizontal(g0)
    c: Horizontal(g2)
    c: Vertical(g1)
    c: Vertical(g3)
    c: Coincident(g4,g5)
    c: Coincident(g5,g6)
    c: Coincident(g6,g7)
    c: Coincident(g7,g4)
    c: Horizontal(g4)
    c: Horizontal(g6)
    c: Vertical(g5)
    c: Vertical(g7)
    c: DistanceY(g1) = 2150  'Height'
    c: DistanceX(g0) = 900  'Width'
    c: DistanceY(g6,g2) = 50  'Frame1'
    c: DistanceX(g2,g6) = 50  'Frame2'
    c: DistanceX(g4,g0) = 50  'Frame3'
    c: DistanceY(g0,g4) = 0
    c: Coincident(g0,g-1)
FEATURE [Sketcher::SketchObject] Sketch309
  FullyConstrained = true
  Placement = pos=(9550,770,0) rot=(0.57735,0.57735,0.57735;2.0944rad)
  sketch-geometry (8):
    g0: LineSegment StartX=0 StartY=0 StartZ=0 EndX=900 EndY=0 EndZ=0
    g1: LineSegment StartX=900 StartY=0 StartZ=0 EndX=900 EndY=2150 EndZ=0
    g2: LineSegment StartX=900 StartY=2150 StartZ=0 EndX=0 EndY=2150 EndZ=0
    g3: LineSegment StartX=0 StartY=2150 StartZ=0 EndX=0 EndY=0 EndZ=0
    g4: LineSegment StartX=50 StartY=0 StartZ=0 EndX=850 EndY=0 EndZ=0
    g5: LineSegment StartX=850 StartY=0 StartZ=0 EndX=850 EndY=2100 EndZ=0
    g6: LineSegment StartX=850 StartY=2100 StartZ=0 EndX=50 EndY=2100 EndZ=0
    g7: LineSegment StartX=50 StartY=2100 StartZ=0 EndX=50 EndY=0 EndZ=0
  constraints (23):
    c: Coincident(g0,g1)
    c: Coincident(g1,g2)
    c: Coincident(g2,g3)
    c: Coincident(g3,g0)
    c: Horizontal(g0)
    c: Horizontal(g2)
    c: Vertical(g1)
    c: Vertical(g3)
    c: Coincident(g4,g5)
    c: Coincident(g5,g6)
    c: Coincident(g6,g7)
    c: Coincident(g7,g4)
    c: Horizontal(g4)
    c: Horizontal(g6)
    c: Vertical(g5)
    c: Vertical(g7)
    c: DistanceY(g1) = 2150  'Height'
    c: DistanceX(g0) = 900  'Width'
    c: DistanceY(g6,g2) = 50  'Frame1'
    c: DistanceX(g2,g6) = 50  'Frame2'
    c: DistanceX(g4,g0) = 50  'Frame3'
    c: DistanceY(g0,g4) = 0
    c: Coincident(g0,g-1)
FEATURE [Part::Part2DObjectPython] Arc118  label="Arc119"  # Draft 2D object (typed FeaturePython)
  Area = 0
  FirstAngle = 0
  LastAngle = 90
  MakeFace = true
  Placement = pos=(9550,820,0) rot=(0,0,1;0rad)
  Radius = 800
FEATURE [Part::Part2DObjectPython] Line1398  # Draft 2D object (typed FeaturePython)
  Area = 0
  ChamferSize = 0
  Closed = false
  End = (9550,820,0)
  FilletRadius = 0
  Length = 800
  MakeFace = true
  Placement = pos=(10350,820,0) rot=(0,0,1;0rad)
  Points = (2) [(0,0,0),(-800,5.68434e-13,0)]
  Start = (10350,820,0)
  Subdivisions = 0
FEATURE [Part::Part2DObjectPython] Line1400  # Draft 2D object (typed FeaturePython)
  Area = 0
  ChamferSize = 0
  Closed = false
  End = (6660,3635,0)
  FilletRadius = 0
  Length = 800
  MakeFace = true
  Placement = pos=(6660,4580,0) rot=(0,0,1;0rad)
  Points = (2) [(0,-145,0),(0,-945,0)]
  Start = (6660,4435,0)
  Subdivisions = 0
FEATURE [Part::Part2DObjectPython] Rectangle3176  label="Контур по блоку ЛСР38 внешний"  # Draft 2D object (typed FeaturePython)
  Area = 0
  ChamferSize = 0
  Columns = 1
  FilletRadius = 0
  Height = 8310
  Length = 13380
  MakeFace = false
  Placement = pos=(-430,-425,0) rot=(0,0,1;0rad)
  Rows = 1
FEATURE [Part::Part2DObjectPython] Wire808  # Draft 2D object (typed FeaturePython)
  Area = 0
  ChamferSize = 0
  Closed = true
  End = (6830,5685,0)
  FilletRadius = 0
  Length = 5460
  MakeFace = false
  Placement = pos=(6160,4810,0) rot=(0,0,1;0rad)
  Points = (4) [(-260,875,0),(-260,2675,0),(670,2675,0),(670,875,0)]
  Start = (5900,5685,0)
  Subdivisions = 0
FEATURE [Part::Part2DObjectPython] Wire809  # Draft 2D object (typed FeaturePython)
  Area = 0
  ChamferSize = 0
  Closed = true
  End = (6675,5785,0)
  FilletRadius = 0
  Length = 4500
  MakeFace = false
  Placement = pos=(6235,4855,0) rot=(0,0,1;0rad)
  Points = (4) [(-210,930,0),(-210,2530,0),(440,2530,0),(440,930,0)]
  Start = (6025,5785,0)
  Subdivisions = 0
FEATURE [Part::FeaturePython] Structure342  label="Структура006"  # Arch/BIM 52 (typed FeaturePython)
  Base = -> Wire809
  FaceMaker = 0
  Height = 450
  HorizontalArea = 1040000
  IfcData = attributes={"GlobalId": {"name": "GlobalId", "type": "IfcGloballyUniqueId", "is_enum": false, "enum_values": []}, "Description": {"... (+484 chars omitted),+1 more (map truncated)
  IfcType = 52
  Length = 0
  MoveBase = false
  MoveWithHost = false
  Nodes = (2) [(6409.93,5722.83,0),(6409.93,5722.83,450)]
  NodesOffset = 0
  Normal = (0,0,1)
  PerimeterLength = 4500
  Placement = pos=(0,0,150) rot=(0,0,1;0rad)
  VerticalArea = 2025000
  Width = 100
FEATURE [Part::Part2DObjectPython] Circle109  label="Circle110"  # Draft 2D object (typed FeaturePython)
  Area = 0
  FirstAngle = 0
  LastAngle = 0
  MakeFace = false
  Placement = pos=(7390,4155,0) rot=(0,0,-1;1.5708rad)
  Radius = 100
FEATURE [Part::Part2DObjectPython] Line1409  # Draft 2D object (typed FeaturePython)
  Area = 0
  ChamferSize = 0
  Closed = false
  End = (7390,3825,0)
  FilletRadius = 0
  Length = 330
  MakeFace = false
  Placement = pos=(7420,4155,0) rot=(0,0,-1;1.5708rad)
  Points = (2) [(0,-30,0),(330,-30,0)]
  Start = (7390,4155,0)
  Subdivisions = 0
FEATURE [Part::Part2DObjectPython] Rectangle3193  # Draft 2D object (typed FeaturePython)
  Area = 0
  ChamferSize = 0
  Columns = 1
  FilletRadius = 75
  Height = 720
  Length = 235
  MakeFace = false
  Placement = pos=(6065,5455,0) rot=(0,0,-1;1.5708rad)
  Rows = 1
FEATURE [Part::Part2DObjectPython] Wire812  # Draft 2D object (typed FeaturePython)
  Area = 0
  ChamferSize = 0
  Closed = true
  End = (6020,5565,0)
  FilletRadius = 0
  Length = 2372.43
  MakeFace = false
  Placement = pos=(6875,5565,0) rot=(0,0,-1;1.5708rad)
  Points = (10) [(6.36646e-12,-45,0),(360,-45,0),(360,-184.29,0),(393.033,-216.967,0),(410,-275,0),(410,-625,0),(393.033,-683.033,0),(360,-715.711,0),(360,-855,0),+1 more]
  Start = (6830,5565,0)
  Subdivisions = 0
FEATURE [Part::FeaturePython] Structure346  label="Структура007"  # Arch/BIM 52 (typed FeaturePython)
  Base = -> Rectangle3193
  FaceMaker = 0
  Height = 100
  HorizontalArea = 164371
  IfcData = attributes={"GlobalId": {"name": "GlobalId", "type": "IfcGloballyUniqueId", "is_enum": false, "enum_values": []}, "Description": {"... (+484 chars omitted),+1 more (map truncated)
  IfcType = 52
  Length = 0
  MoveBase = false
  MoveWithHost = false
  Nodes = (2) [(6380,5325,0),(6380,5325,100)]
  NodesOffset = 0
  Normal = (0,0,1)
  PerimeterLength = 1781.24
  Placement = pos=(0,0,900) rot=(0,0,1;0rad)
  VerticalArea = 178124
  Width = 100
FEATURE [Part::Box] Box3228  label="Ниша-дровник"
  AttacherType = Attacher::AttachEngine3D
  Height = 400
  Length = 500
  Placement = pos=(8800,1885,200) rot=(0,0,1;0rad)
  Width = 500
FEATURE [Part::Box] Box3229  label="шкаф 60 кухонный 013"
  AttacherType = Attacher::AttachEngine3D
  Height = 700
  Length = 600
  Placement = pos=(10150,-10,1600) rot=(0,0,1;0rad)
  Width = 600
FEATURE [Part::Box] Box3230  label="шкаф 60 кухонный 001"
  AttacherType = Attacher::AttachEngine3D
  Height = 1600
  Length = 600
  Placement = pos=(10750,-10,0) rot=(0,0,1;1.5708rad)
  Width = 600
FEATURE [Part::Box] Box3231  label="МВ_001"
  AttacherType = Attacher::AttachEngine3D
  Height = 350
  Length = 500
  Placement = pos=(10740,90,1000) rot=(0,0,1;1.5708rad)
  Width = 580
FEATURE [Part::Cut] Cut044
  Base = -> Box3230
  Tool = -> Box3231
FEATURE [Part::Cut] Cut045
  Base = -> Cut044
  Tool = -> Box3209
FEATURE [Part::Box] Box3232  label="МВ_002"
  AttacherType = Attacher::AttachEngine3D
  Height = 350
  Length = 500
  Placement = pos=(10740,90,1000) rot=(0,0,1;1.5708rad)
  Width = 580
FEATURE [Part::Box] Box3233  label="ДШ_002"
  AttacherType = Attacher::AttachEngine3D
  Height = 500
  Length = 500
  Placement = pos=(10740,90,450) rot=(0,0,1;1.5708rad)
  Width = 580
FEATURE [Part::Part2DObjectPython] Rectangle3200  label="четверть_183-003"  # Draft 2D object (typed FeaturePython)
  ChamferSize = 0
  Columns = 1
  FilletRadius = 0
  Height = 120
  Length = 1830
  MakeFace = true
  Placement = pos=(2030,7895,0) rot=(0,0,1;0rad)
  Rows = 1
FEATURE [Part::Part2DObjectPython] Rectangle3201  label="четверть_790-002"  # Draft 2D object (typed FeaturePython)
  ChamferSize = 0
  Columns = 1
  FilletRadius = 0
  Height = 120
  Length = 790
  MakeFace = true
  Placement = pos=(5150,7895,0) rot=(0,0,1;0rad)
  Rows = 1
FEATURE [Part::Part2DObjectPython] Rectangle3202  label="четверть_183-002"  # Draft 2D object (typed FeaturePython)
  ChamferSize = 0
  Columns = 1
  FilletRadius = 0
  Height = 120
  Length = 1830
  MakeFace = true
  Placement = pos=(8660,7895,0) rot=(0,0,1;0rad)
  Rows = 1
FEATURE [Part::FeaturePython] Structure350  label="Проём_четв._044"  # Arch/BIM 52 (typed FeaturePython)
  Base = -> Rectangle3202
  FaceMaker = 0
  Height = 2552
  HorizontalArea = 219600
  IfcData = complex_attributes={"OwnerHistory": {}, "IsNestedBy": {}, "IsDecomposedBy": {}, "IsDefinedBy": {}, "ObjectPlacement": {}, "Representation":... (+4 chars omitted)
  IfcType = 52
  Length = 0
  MoveBase = false
  MoveWithHost = false
  Nodes = (2) [(5775,-395,0),(5775,-395,2335)]
  NodesOffset = 0
  Normal = (0,0,0)
  PerimeterLength = 3900
  Placement = pos=(0,0,-40) rot=(0,0,1;0rad)
  VerticalArea = 9.9528e+06
  Width = 100
FEATURE [Part::Part2DObjectPython] Line1426  # Draft 2D object (typed FeaturePython)
  Area = 0
  ChamferSize = 0
  Closed = true
  End = (-430,7885,0)
  FilletRadius = 0
  Length = 8310
  MakeFace = false
  Placement = pos=(-380,-318,0) rot=(0,0,1;0rad)
  Points = (2) [(-50,-107,0),(-50,8203,0)]
  Start = (-430,-425,0)
  Subdivisions = 0
FEATURE [Part::Part2DObjectPython] Line1427  # Draft 2D object (typed FeaturePython)
  Area = 0
  ChamferSize = 0
  Closed = true
  End = (12950,7885,0)
  FilletRadius = 0
  Length = 8310
  MakeFace = false
  Placement = pos=(12900,-318,0) rot=(0,0,1;0rad)
  Points = (2) [(50,-107,0),(50,8203,0)]
  Start = (12950,-425,0)
  Subdivisions = 0
FEATURE [Part::Part2DObjectPython] Line1430  # Draft 2D object (typed FeaturePython)
  Area = 0
  ChamferSize = 0
  Closed = true
  End = (-50,-425,0)
  FilletRadius = 0
  Length = 12620
  MakeFace = false
  Placement = pos=(-380,-425,0) rot=(0,0,1;0rad)
  Points = (2) [(12950,0,0),(330,0,0)]
  Start = (12570,-425,0)
  Subdivisions = 0
FEATURE [Part::Part2DObjectPython] Line1431  # Draft 2D object (typed FeaturePython)
  Area = 0
  ChamferSize = 0
  Closed = true
  End = (12570,7885,0)
  FilletRadius = 0
  Length = 12620
  MakeFace = false
  Placement = pos=(-380,-303,0) rot=(0,0,1;0rad)
  Points = (2) [(330,8188,0),(12950,8188,0)]
  Start = (-50,7885,0)
  Subdivisions = 0
FEATURE [Part::Part2DObjectPython] Wire817  label="кровля_контур_обрезки"  # Draft 2D object (typed FeaturePython)
  Area = 0
  ChamferSize = 0
  Closed = true
  End = (3195,-1155,0)
  FilletRadius = 0
  Length = 52320
  MakeFace = false
  Placement = pos=(-1210,-1210,0) rot=(0,0,1;0rad)
  Points = (12) [(50,55,0),(50,9825,0),(8285,9825,0),(8285,10600,0),(13285,10600,0),(13285,9825,0),(14890,9825,0),(14890,55,0),(10405,55,0),(10405,-720,0),+2 more]
  Start = (-1160,-1155,0)
  Subdivisions = 0
FEATURE [Part::Extrusion] Extrude
  Base = -> Wire817
  Dir = (0,0,1)
  DirMode = 2
  FaceMakerClass = Part::FaceMakerBullseye
  LengthFwd = 5000
  LengthRev = 0
  Placement = pos=(0,0,2720) rot=(0,0,1;0rad)
  Solid = true
  Symmetric = false
FEATURE [Part::Part2DObjectPython] Rectangle3216  # Draft 2D object (typed FeaturePython)
  Area = 0
  ChamferSize = 0
  Columns = 1
  FilletRadius = 0
  Height = 8540
  Length = 20900
  MakeFace = false
  Placement = pos=(-4200,-540,0) rot=(0,0,1;0rad)
  Rows = 1
FEATURE [Part::Part2DObjectPython] Wire  # Draft 2D object (typed FeaturePython)
  Area = 6.01874e+06
  ChamferSize = 0
  Closed = true
  End = (13030,6661.83,3999.83)
  FilletRadius = 0
  Length = 13021.9
  MakeFace = true
  Placement = pos=(13030,798.165,3999.83) rot=(0.57735,0.57735,0.57735;2.0944rad)
  Points = (3) [(0,0,0),(2931.83,2052.89,0),(5863.67,-9.09495e-13,0)]
  Start = (13030,798.165,3999.83)
  Subdivisions = 0
FEATURE [Part::Extrusion] Extrude092
  Base = -> Wire
  Dir = (1,0,0)
  DirMode = 2
  FaceMakerClass = Part::FaceMakerBullseye
  LengthFwd = 15000
  LengthRev = 0
  Placement = pos=(-14250,0,0) rot=(0,0,1;0rad)
  Solid = false
  Symmetric = false
FEATURE [Sketcher::SketchObject] Sketch316
  FullyConstrained = true
  Placement = pos=(-185,3635,4170) rot=(0.57735,0.57735,0.57735;2.0944rad)
  sketch-geometry (20):
    g0: LineSegment StartX=-1900 StartY=0 StartZ=0 EndX=0 EndY=0 EndZ=0
    g1: LineSegment StartX=0 StartY=0 StartZ=0 EndX=0 EndY=1200 EndZ=0
    g2: LineSegment StartX=0 StartY=1200 StartZ=0 EndX=-611.028 EndY=1200 EndZ=0
    g3: LineSegment StartX=-1900 StartY=297.452 StartZ=0 EndX=-1900 EndY=0 EndZ=0
    g4: LineSegment StartX=-1850 StartY=50 StartZ=0 EndX=-50 EndY=50 EndZ=0
    g5: LineSegment StartX=-50 StartY=50 StartZ=0 EndX=-50 EndY=1150 EndZ=0
    g6: LineSegment StartX=-50 StartY=1150 StartZ=0 EndX=-595.263 EndY=1150 EndZ=0
    g7: LineSegment StartX=-1850 StartY=271.423 StartZ=0 EndX=-1850 EndY=50 EndZ=0
    g8: LineSegment StartX=-1845 StartY=55 StartZ=0 EndX=-55 EndY=55 EndZ=0
    g9: LineSegment StartX=-55 StartY=55 StartZ=0 EndX=-55 EndY=1145 EndZ=0
    g10: LineSegment StartX=-55 StartY=1145 StartZ=0 EndX=-611.121 EndY=1145 EndZ=0
    g11: LineSegment StartX=-1845 StartY=281.028 StartZ=0 EndX=-1845 EndY=55 EndZ=0
    g12: LineSegment StartX=-1795 StartY=105 StartZ=0 EndX=-105 EndY=105 EndZ=0
    g13: LineSegment StartX=-105 StartY=105 StartZ=0 EndX=-105 EndY=1095 EndZ=0
    g14: LineSegment StartX=-105 StartY=1095 StartZ=0 EndX=-595.356 EndY=1095 EndZ=0
    g15: LineSegment StartX=-1795 StartY=255 StartZ=0 EndX=-1795 EndY=105 EndZ=0
    g16: LineSegment StartX=-1900 StartY=297.452 StartZ=0 EndX=-611.028 EndY=1200 EndZ=0
    g17: LineSegment StartX=-1850 StartY=271.423 StartZ=0 EndX=-595.263 EndY=1150 EndZ=0
    g18: LineSegment StartX=-1845 StartY=281.028 StartZ=0 EndX=-611.121 EndY=1145 EndZ=0
    g19: LineSegment StartX=-1795 StartY=255 StartZ=0 EndX=-595.356 EndY=1095 EndZ=0
  constraints (59):
    c: Coincident(g1,g2)
    c: Horizontal(g0)
    c: Horizontal(g2)
    c: Vertical(g1)
    c: Vertical(g3)
    c: Coincident(g4,g5)
    c: Coincident(g5,g6)
    c: Coincident(g7,g4)
    c: Horizontal(g4)
    c: Horizontal(g6)
    c: Vertical(g5)
    c: Vertical(g7)
    c: DistanceX(g4,g0) = 50  'Frame3'
    c: DistanceY(g0,g4) = 50  'Frame4'
    c: Coincident(g8,g9)
    c: Coincident(g9,g10)
    c: Coincident(g11,g8)
    c: Horizontal(g8)
    c: Horizontal(g10)
    c: Vertical(g9)
    c: Vertical(g11)
    c: Coincident(g12,g13)
    c: Coincident(g13,g14)
    c: Coincident(g15,g12)
    c: Horizontal(g12)
    c: Horizontal(g14)
    c: Vertical(g13)
    c: Vertical(g15)
    c: DistanceX(g8,g12) = 50  'Frame5'
    c: DistanceY(g8,g12) = 50  'Frame6'
    c: DistanceX(g14,g10) = 50  'Frame8'
    c: DistanceY(g14,g10) = 50  'Frame7'
    c: DistanceX(g4,g8) = 5
    c: DistanceY(g4,g8) = 5
    c: DistanceX(g10,g6) = 5
    c: DistanceY(g10,g6) = 5
    c: Coincident(g16,g3)
    c: Coincident(g16,g2)
    c: Coincident(g17,g7)
    c: Coincident(g17,g6)
    c: Coincident(g18,g11)
    c: Coincident(g18,g10)
    c: Coincident(g19,g15)
    c: Coincident(g19,g14)
    c: Distance(g11,g17) = 5
    c: Distance(g15,g18) = 50
    c: Distance(g7,g16) = 50
    c: DistanceY(g5,g1) = 50
    c: Parallel(g18,g17)
    c: Parallel(g16,g17)
    c: Parallel(g18,g19)
    c: DistanceX(g0,g4) = 50
    c: DistanceY(g15,g15) = 150
    c: Angle(g19) = 0.610865  'угол наклона'
    c: Coincident(g3,g0)
    c: Coincident(g0,g1)
    c: Coincident(g0,g-1)
    c: DistanceX(g0,g0) = 1900
    c: DistanceY(g1,g1) = 1200
FEATURE [Sketcher::SketchObject] Sketch318
  FullyConstrained = true
  Placement = pos=(-185,3825,4170) rot=(0.57735,-0.57735,-0.57735;2.0944rad)
  sketch-geometry (20):
    g0: LineSegment StartX=-1900 StartY=0 StartZ=0 EndX=0 EndY=0 EndZ=0
    g1: LineSegment StartX=0 StartY=0 StartZ=0 EndX=0 EndY=1200 EndZ=0
    g2: LineSegment StartX=0 StartY=1200 StartZ=0 EndX=-611.028 EndY=1200 EndZ=0
    g3: LineSegment StartX=-1900 StartY=297.452 StartZ=0 EndX=-1900 EndY=0 EndZ=0
    g4: LineSegment StartX=-1850 StartY=50 StartZ=0 EndX=-50 EndY=50 EndZ=0
    g5: LineSegment StartX=-50 StartY=50 StartZ=0 EndX=-50 EndY=1150 EndZ=0
    g6: LineSegment StartX=-50 StartY=1150 StartZ=0 EndX=-595.263 EndY=1150 EndZ=0
    g7: LineSegment StartX=-1850 StartY=271.423 StartZ=0 EndX=-1850 EndY=50 EndZ=0
    g8: LineSegment StartX=-1845 StartY=55 StartZ=0 EndX=-55 EndY=55 EndZ=0
    g9: LineSegment StartX=-55 StartY=55 StartZ=0 EndX=-55 EndY=1145 EndZ=0
    g10: LineSegment StartX=-55 StartY=1145 StartZ=0 EndX=-611.121 EndY=1145 EndZ=0
    g11: LineSegment StartX=-1845 StartY=281.028 StartZ=0 EndX=-1845 EndY=55 EndZ=0
    g12: LineSegment StartX=-1795 StartY=105 StartZ=0 EndX=-105 EndY=105 EndZ=0
    g13: LineSegment StartX=-105 StartY=105 StartZ=0 EndX=-105 EndY=1095 EndZ=0
    g14: LineSegment StartX=-105 StartY=1095 StartZ=0 EndX=-595.356 EndY=1095 EndZ=0
    g15: LineSegment StartX=-1795 StartY=255 StartZ=0 EndX=-1795 EndY=105 EndZ=0
    g16: LineSegment StartX=-1900 StartY=297.452 StartZ=0 EndX=-611.028 EndY=1200 EndZ=0
    g17: LineSegment StartX=-1850 StartY=271.423 StartZ=0 EndX=-595.263 EndY=1150 EndZ=0
    g18: LineSegment StartX=-1845 StartY=281.028 StartZ=0 EndX=-611.121 EndY=1145 EndZ=0
    g19: LineSegment StartX=-1795 StartY=255 StartZ=0 EndX=-595.356 EndY=1095 EndZ=0
  constraints (59):
    c: Coincident(g1,g2)
    c: Horizontal(g0)
    c: Horizontal(g2)
    c: Vertical(g1)
    c: Vertical(g3)
    c: Coincident(g4,g5)
    c: Coincident(g5,g6)
    c: Coincident(g7,g4)
    c: Horizontal(g4)
    c: Horizontal(g6)
    c: Vertical(g5)
    c: Vertical(g7)
    c: DistanceY(g1) = 1200  'Height'
    c: DistanceX(g4,g0) = 50  'Frame3'
    c: DistanceY(g0,g4) = 50  'Frame4'
    c: Coincident(g8,g9)
    c: Coincident(g9,g10)
    c: Coincident(g11,g8)
    c: Horizontal(g8)
    c: Horizontal(g10)
    c: Vertical(g9)
    c: Vertical(g11)
    c: Coincident(g12,g13)
    c: Coincident(g13,g14)
    c: Coincident(g15,g12)
    c: Horizontal(g12)
    c: Horizontal(g14)
    c: Vertical(g13)
    c: Vertical(g15)
    c: DistanceX(g8,g12) = 50  'Frame5'
    c: DistanceY(g8,g12) = 50  'Frame6'
    c: DistanceX(g14,g10) = 50  'Frame8'
    c: DistanceY(g14,g10) = 50  'Frame7'
    c: DistanceX(g4,g8) = 5
    c: DistanceY(g4,g8) = 5
    c: DistanceX(g10,g6) = 5
    c: DistanceY(g10,g6) = 5
    c: Coincident(g16,g3)
    c: Coincident(g16,g2)
    c: Coincident(g17,g7)
    c: Coincident(g17,g6)
    c: Coincident(g18,g11)
    c: Coincident(g18,g10)
    c: Coincident(g19,g15)
    c: Coincident(g19,g14)
    c: Distance(g11,g17) = 5
    c: Distance(g15,g18) = 50
    c: Distance(g7,g16) = 50
    c: DistanceY(g5,g1) = 50
    c: Parallel(g18,g17)
    c: Parallel(g16,g17)
    c: Parallel(g18,g19)
    c: DistanceX(g0,g4) = 50
    c: DistanceY(g15,g15) = 150
    c: Angle(g19) = 0.610865  'угол наклона'
    c: Coincident(g3,g0)
    c: Coincident(g0,g1)
    c: Coincident(g0,g-1)
    c: DistanceX(g0,g0) = 1900
FEATURE [Part::Part2DObjectPython] Rectangle3217  # Draft 2D object (typed FeaturePython)
  Area = 142500
  ChamferSize = 0
  Columns = 1
  FilletRadius = 0
  Height = 1900
  Length = 75
  MakeFace = true
  Placement = pos=(1370,4675,0) rot=(0,0,1;0rad)
  Rows = 1
FEATURE [Part::Part2DObjectPython] Wire819  label="мансарда h1.2m"  # Draft 2D object (typed FeaturePython)
  Area = 7.84576e+07
  ChamferSize = 0
  Closed = true
  End = (540,6330,0)
  FilletRadius = 0
  Length = 37840
  MakeFace = true
  Placement = pos=(20,5942.03,0) rot=(0,0,1;0rad)
  Points = (12) [(-50,387.97,0),(-50,-4812.03,0),(520,-4812.03,0),(520,-5382.03,0),(11960,-5382.03,0),(11960,-4812.03,0),(12530,-4812.03,0),(12530,387.97,0),+4 more]
  Start = (-30,6330,0)
  Subdivisions = 0
FEATURE [Part::Part2DObjectPython] Rectangle3220  # Draft 2D object (typed FeaturePython)
  Area = 0
  ChamferSize = 0
  Columns = 1
  FilletRadius = 0
  Height = 8240
  Length = 13300
  MakeFace = false
  Placement = pos=(-390,-390,0) rot=(0,0,1;0rad)
  Rows = 1
FEATURE [Part::Part2DObjectPython] Line1442  # Draft 2D object (typed FeaturePython)
  Area = 0
  ChamferSize = 0
  Closed = false
  End = (13500,3730,0)
  FilletRadius = 0
  Length = 14500
  MakeFace = false
  Placement = pos=(-390,3730,0) rot=(0,0,1;0rad)
  Points = (2) [(-610,4.54747e-13,0),(13890,0,0)]
  Start = (-1000,3730,0)
  Subdivisions = 0
FEATURE [Part::Part2DObjectPython] Rectangle3222  label="Проём ФР 001"  # Draft 2D object (typed FeaturePython)
  Area = 723419
  ChamferSize = 0
  Columns = 1
  FilletRadius = 0
  Height = 2009.5
  Length = 360
  MakeFace = true
  Placement = pos=(-390,3830,0) rot=(0,0,1;0rad)
  Rows = 1
FEATURE [Part::Part2DObjectPython] Rectangle3223  label="Проём ФР 010"  # Draft 2D object (typed FeaturePython)
  Area = 723419
  ChamferSize = 0
  Columns = 1
  FilletRadius = 0
  Height = 2009.5
  Length = 360
  MakeFace = true
  Placement = pos=(-390,1620.5,0) rot=(0,0,1;0rad)
  Rows = 1
FEATURE [Part::Part2DObjectPython] Rectangle3224  label="Проём ФР 011"  # Draft 2D object (typed FeaturePython)
  Area = 723419
  ChamferSize = 0
  Columns = 1
  FilletRadius = 0
  Height = 2009.5
  Length = 360
  MakeFace = true
  Placement = pos=(12550,3830,0) rot=(0,0,1;0rad)
  Rows = 1
FEATURE [Part::Part2DObjectPython] Rectangle3225  label="Проём ФР 012"  # Draft 2D object (typed FeaturePython)
  Area = 723419
  ChamferSize = 0
  Columns = 1
  FilletRadius = 0
  Height = 2009.5
  Length = 360
  MakeFace = true
  Placement = pos=(12550,1620.5,0) rot=(0,0,1;0rad)
  Rows = 1
FEATURE [Part::Extrusion] Extrude093  label="ПНО 39-15-004"
  Base = -> Sketch301
  Dir = (0,3880,0)
  DirMode = 0
  FaceMakerClass = Part::FaceMakerBullseye
  LengthFwd = 3880
  LengthRev = 0
  Placement = pos=(3990,-205,2800) rot=(0,0,1;0rad)
  Solid = true
  Symmetric = false
FEATURE [Part::Extrusion] Extrude094  label="ПНО 39-12-8-008"
  Base = -> Sketch231
  Dir = (0,3880,0)
  DirMode = 0
  FaceMakerClass = Part::FaceMakerBullseye
  LengthFwd = 3880
  LengthRev = 0
  Placement = pos=(5510,-205,2800) rot=(0,0,1;0rad)
  Solid = true
  Symmetric = false
FEATURE [Part::Part2DObjectPython] Rectangle3227  # Draft 2D object (typed FeaturePython)
  Area = 22500
  ChamferSize = 0
  Columns = 1
  FilletRadius = 0
  Height = 150
  Length = 150
  MakeFace = true
  Placement = pos=(3320,3655,0) rot=(0,0,1;0rad)
  Rows = 1
FEATURE [Part::Part2DObjectPython] Rectangle3228  # Draft 2D object (typed FeaturePython)
  Area = 22500
  ChamferSize = 0
  Columns = 1
  FilletRadius = 0
  Height = 150
  Length = 150
  MakeFace = true
  Placement = pos=(9050,3655,0) rot=(0,0,1;0rad)
  Rows = 1
FEATURE [Part::Part2DObjectPython] Rectangle3229  # Draft 2D object (typed FeaturePython)
  Area = 22500
  ChamferSize = 0
  Columns = 1
  FilletRadius = 0
  Height = 150
  Length = 150
  MakeFace = true
  Placement = pos=(5290,3655,0) rot=(0,0,1;0rad)
  Rows = 1
FEATURE [Part::Part2DObjectPython] Rectangle3232  # Draft 2D object (typed FeaturePython)
  Area = 169500
  ChamferSize = 0
  Columns = 1
  FilletRadius = 0
  Height = 150
  Length = 1130
  MakeFace = true
  Placement = pos=(7920,3655,0) rot=(0,0,1;0rad)
  Rows = 1
FEATURE [Part::Part2DObjectPython] Rectangle3233  # Draft 2D object (typed FeaturePython)
  Area = 464907
  ChamferSize = 0
  Columns = 1
  FilletRadius = 0
  Height = 3099.38
  Length = 150
  MakeFace = true
  Placement = pos=(7932.5,3805,0) rot=(0,0,1;0rad)
  Rows = 1
FEATURE [Part::Part2DObjectPython] Rectangle3236  # Draft 2D object (typed FeaturePython)
  Area = 464907
  ChamferSize = 0
  Columns = 1
  FilletRadius = 0
  Height = 3099.38
  Length = 150
  MakeFace = true
  Placement = pos=(6737.5,3805,0) rot=(0,0,1;0rad)
  Rows = 1
FEATURE [Part::Part2DObjectPython] Rectangle3239  # Draft 2D object (typed FeaturePython)
  Area = 0
  ChamferSize = 0
  Columns = 1
  FilletRadius = 0
  Height = 1200
  Length = 1200
  MakeFace = false
  Placement = pos=(4240,2881.47,0) rot=(0,0,1;0.785398rad)
  Rows = 1
FEATURE [Part::Part2DObjectPython] Rectangle3240  # Draft 2D object (typed FeaturePython)
  Area = 22500
  ChamferSize = 0
  Columns = 1
  FilletRadius = 0
  Height = 150
  Length = 150
  MakeFace = true
  Placement = pos=(6550,3655,0) rot=(0,0,1;0rad)
  Rows = 1
FEATURE [Part::Part2DObjectPython] Rectangle3247  # Draft 2D object (typed FeaturePython)
  Area = 0
  ChamferSize = 0
  Columns = 1
  FilletRadius = 0
  Height = 1300
  Length = 100
  MakeFace = false
  Placement = pos=(3285.41,3765.36,0) rot=(0,0,-1;0.785398rad)
  Rows = 1
FEATURE [Part::Part2DObjectPython] Rectangle3250  # Draft 2D object (typed FeaturePython)
  Area = 355835
  ChamferSize = 0
  Columns = 1
  FilletRadius = 0
  Height = 2372.23
  Length = 150
  MakeFace = true
  Placement = pos=(4190.76,4527.77,0) rot=(0,0,1;0rad)
  Rows = 1
FEATURE [Part::Part2DObjectPython] Rectangle3252  # Draft 2D object (typed FeaturePython)
  Area = 79500
  ChamferSize = 0
  Columns = 1
  FilletRadius = 0
  Height = 795
  Length = 100
  MakeFace = true
  Placement = pos=(9100,560,0) rot=(0,0,1;0rad)
  Rows = 1
FEATURE [Part::Part2DObjectPython] Rectangle3253  label="Д90-мансарда-012"  # Draft 2D object (typed FeaturePython)
  Area = 112500
  ChamferSize = 0
  Columns = 1
  FilletRadius = 0
  Height = 900
  Length = 125
  MakeFace = true
  Placement = pos=(9087.5,2500,0) rot=(0,0,1;0rad)
  Rows = 1
FEATURE [Part::Part2DObjectPython] Arc119  label="Arc120"  # Draft 2D object (typed FeaturePython)
  Area = 0
  FirstAngle = 0
  LastAngle = 90
  MakeFace = false
  Placement = pos=(9100,2550,0) rot=(0,0,1;1.5708rad)
  Radius = 800
FEATURE [Part::Part2DObjectPython] Rectangle3255  label="Д90-мансарда-011"  # Draft 2D object (typed FeaturePython)
  Area = 90000
  ChamferSize = 0
  Columns = 1
  FilletRadius = 0
  Height = 900
  Length = 100
  MakeFace = true
  Placement = pos=(4062.46,2916.83,0) rot=(0,0,1;0.785398rad)
  Rows = 1
FEATURE [Part::Part2DObjectPython] Rectangle3257  label="Д90-мансарда-010"  # Draft 2D object (typed FeaturePython)
  Area = 90000
  ChamferSize = 0
  Columns = 1
  FilletRadius = 0
  Height = 900
  Length = 100
  MakeFace = true
  Placement = pos=(4133.17,4472.46,0) rot=(0,0,1;2.35619rad)
  Rows = 1
FEATURE [Part::Part2DObjectPython] Rectangle3258  # Draft 2D object (typed FeaturePython)
  Area = 0
  ChamferSize = 0
  Columns = 1
  FilletRadius = 0
  Height = 1250
  Length = 150
  MakeFace = false
  Placement = pos=(5088.53,3730,0) rot=(0,0,1;0.785398rad)
  Rows = 1
FEATURE [Part::Part2DObjectPython] Rectangle3259  # Draft 2D object (typed FeaturePython)
  Area = 15000
  ChamferSize = 0
  Columns = 1
  FilletRadius = 0
  Height = 100
  Length = 150
  MakeFace = true
  Placement = pos=(4165.76,4527.77,0) rot=(0,0,1;0rad)
  Rows = 1
FEATURE [Part::Part2DObjectPython] Rectangle3261  # Draft 2D object (typed FeaturePython)
  Area = 330000
  ChamferSize = 0
  Columns = 1
  FilletRadius = 0
  Height = 100
  Length = 3300
  MakeFace = true
  Placement = pos=(20,3680,0) rot=(0,0,1;0rad)
  Rows = 1
FEATURE [Part::Part2DObjectPython] Rectangle3262  # Draft 2D object (typed FeaturePython)
  Area = 249000
  ChamferSize = 0
  Columns = 1
  FilletRadius = 0
  Height = 150
  Length = 1660
  MakeFace = true
  Placement = pos=(5240,3655,0) rot=(0,0,1;0rad)
  Rows = 1
FEATURE [Part::Part2DObjectPython] Line1447  # Draft 2D object (typed FeaturePython)
  Area = 0
  ChamferSize = 0
  Closed = false
  End = (4027.87,4507.82,0)
  FilletRadius = 0
  Length = 800
  MakeFace = false
  Placement = pos=(3462.18,5073.5,0) rot=(0,0,1;0rad)
  Points = (2) [(0,0,0),(565.685,-565.685,0)]
  Start = (3462.18,5073.5,0)
  Subdivisions = 0
FEATURE [Part::Part2DObjectPython] Line1448  # Draft 2D object (typed FeaturePython)
  Area = 0
  ChamferSize = 0
  Closed = false
  End = (4027.87,2952.18,0)
  FilletRadius = 0
  Length = 800
  MakeFace = false
  Placement = pos=(3462.18,2386.5,0) rot=(0,0,1;0rad)
  Points = (2) [(0,0,0),(565.685,565.685,0)]
  Start = (3462.18,2386.5,0)
  Subdivisions = 0
FEATURE [Part::Part2DObjectPython] Line1449  # Draft 2D object (typed FeaturePython)
  Area = 0
  ChamferSize = 0
  Closed = false
  End = (9100,2550,0)
  FilletRadius = 0
  Length = 800
  MakeFace = false
  Placement = pos=(8300,2550,0) rot=(0,0,1;0rad)
  Points = (2) [(0,0,0),(800,0,0)]
  Start = (8300,2550,0)
  Subdivisions = 0
FEATURE [Part::Part2DObjectPython] Rectangle3264  # Draft 2D object (typed FeaturePython)
  Area = 0
  ChamferSize = 0
  Columns = 1
  FilletRadius = 0
  Height = 600
  Length = 2525
  MakeFace = false
  Placement = pos=(570,3792.5,0) rot=(0,0,1;1.5708rad)
  Rows = 1
FEATURE [Part::Part2DObjectPython] Rectangle3265  # Draft 2D object (typed FeaturePython)
  Area = 0
  ChamferSize = 0
  Columns = 1
  FilletRadius = 0
  Height = 600
  Length = 2525
  MakeFace = false
  Placement = pos=(570,1142.5,0) rot=(0,0,1;1.5708rad)
  Rows = 1
FEATURE [Part::Part2DObjectPython] Rectangle3266  # Draft 2D object (typed FeaturePython)
  Area = 0
  ChamferSize = 0
  Columns = 1
  FilletRadius = 0
  Height = 1400
  Length = 2000
  MakeFace = false
  Placement = pos=(575.636,592.87,0) rot=(0,0,1;0rad)
  Rows = 1
FEATURE [Part::Part2DObjectPython] Rectangle3267  # Draft 2D object (typed FeaturePython)
  Area = 0
  ChamferSize = 0
  Columns = 1
  FilletRadius = 0
  Height = 1000
  Length = 400
  MakeFace = false
  Placement = pos=(2075.64,692.87,0) rot=(0,0,1;0rad)
  Rows = 1
FEATURE [Part::Part2DObjectPython] Rectangle3271  # Draft 2D object (typed FeaturePython)
  Area = 0
  ChamferSize = 0
  Columns = 1
  FilletRadius = 0
  Height = 50
  Length = 1100
  MakeFace = false
  Placement = pos=(6860,3582.5,0) rot=(0,0,1;0rad)
  Rows = 1
FEATURE [Part::Part2DObjectPython] Rectangle3272  # Draft 2D object (typed FeaturePython)
  Area = 0
  ChamferSize = 0
  Columns = 1
  FilletRadius = 0
  Height = 50
  Length = 1100
  MakeFace = false
  Placement = pos=(7920,3582.5,0) rot=(0,0,1;0rad)
  Rows = 1
FEATURE [Part::Part2DObjectPython] Rectangle3273  # Draft 2D object (typed FeaturePython)
  Area = 0
  ChamferSize = 0
  Columns = 1
  FilletRadius = 0
  Height = 2100
  Length = 1800
  MakeFace = false
  Placement = pos=(9190.68,4767.73,0) rot=(0,0,1;0rad)
  Rows = 1
FEATURE [Part::Part2DObjectPython] Rectangle3274  # Draft 2D object (typed FeaturePython)
  Area = 0
  ChamferSize = 0
  Columns = 1
  FilletRadius = 0
  Height = 400
  Length = 800
  MakeFace = false
  Placement = pos=(9290.68,6367.73,0) rot=(0,0,1;0rad)
  Rows = 1
FEATURE [Part::Part2DObjectPython] Rectangle3275  # Draft 2D object (typed FeaturePython)
  Area = 0
  ChamferSize = 0
  Columns = 1
  FilletRadius = 0
  Height = 400
  Length = 700
  MakeFace = false
  Placement = pos=(10190.7,6367.73,0) rot=(0,0,1;0rad)
  Rows = 1
FEATURE [Part::Part2DObjectPython] Arc123  label="Arc124"  # Draft 2D object (typed FeaturePython)
  Area = 0
  FirstAngle = -225
  LastAngle = -135
  MakeFace = false
  Placement = pos=(4027.87,4507.82,0) rot=(0,0,1;0rad)
  Radius = 800
FEATURE [Part::Part2DObjectPython] Line1452  # Draft 2D object (typed FeaturePython)
  Area = 0
  ChamferSize = 0
  Closed = false
  End = (3300.05,3680,0)
  FilletRadius = 0
  Length = 1300
  MakeFace = false
  Placement = pos=(4219.29,2760.76,0) rot=(0,0,1;0rad)
  Points = (2) [(0,0,0),(-919.239,919.239,0)]
  Start = (4219.29,2760.76,0)
  Subdivisions = 0
FEATURE [Part::Part2DObjectPython] Arc124  label="Arc125"  # Draft 2D object (typed FeaturePython)
  Area = 0
  FirstAngle = -225
  LastAngle = -135
  MakeFace = false
  Placement = pos=(4027.87,2952.18,0) rot=(0,0,1;0rad)
  Radius = 800
FEATURE [Part::Part2DObjectPython] Rectangle3277  # Draft 2D object (typed FeaturePython)
  Area = 0
  ChamferSize = 0
  Columns = 1
  FilletRadius = 0
  Height = 1400
  Length = 2000
  MakeFace = false
  Placement = pos=(570.894,5470.31,0) rot=(0,0,1;0rad)
  Rows = 1
FEATURE [Part::Part2DObjectPython] Rectangle3278  # Draft 2D object (typed FeaturePython)
  Area = 0
  ChamferSize = 0
  Columns = 1
  FilletRadius = 0
  Height = 1000
  Length = 400
  MakeFace = false
  Placement = pos=(2070.89,5723.96,0) rot=(0,0,1;0rad)
  Rows = 1
FEATURE [Part::Part2DObjectPython] Line1456  # Draft 2D object (typed FeaturePython)
  Area = 0
  ChamferSize = 0
  Closed = false
  End = (4820,7335,0)
  FilletRadius = 0
  Length = 800
  MakeFace = true
  Placement = pos=(4020,7335,0) rot=(0,0,1;0rad)
  Points = (2) [(0,0,0),(800,0,0)]
  Start = (4020,7335,0)
  Subdivisions = 0
FEATURE [Part::Part2DObjectPython] Arc125  label="Arc126"  # Draft 2D object (typed FeaturePython)
  Area = 0
  FirstAngle = -180
  LastAngle = -90
  MakeFace = true
  Placement = pos=(4820,7335,0) rot=(0,0,1;0rad)
  Radius = 800
FEATURE [Part::Part2DObjectPython] Wire822  # Draft 2D object (typed FeaturePython)
  Area = 3.74321e+07
  ChamferSize = 0
  Closed = true
  End = (3500,2385,0)
  FilletRadius = 0
  Length = 39480
  MakeFace = true
  Placement = pos=(3600,3535,0) rot=(0,0,1;1.5708rad)
  Points = (18) [(0,100,0),(0,-4820,0),(290,-4820,0),(290,-4360,0),(2950,-4360,0),(2950,-4260,0),(1900,-4260,0),(1900,-3340,0),(3950,-3340,0),(3950,-8950,0),+8 more]
  Start = (3500,3535,0)
  Subdivisions = 0
FEATURE [Sketcher::SketchObject] Sketch
  FullyConstrained = true
  Placement = pos=(5355,993.568,5040.23) rot=(1,0,0;0.610865rad)
  sketch-geometry (16):
    g0: LineSegment StartX=0 StartY=0 StartZ=0 EndX=550 EndY=0 EndZ=0
    g1: LineSegment StartX=550 StartY=0 StartZ=0 EndX=550 EndY=980 EndZ=0
    g2: LineSegment StartX=550 StartY=980 StartZ=0 EndX=0 EndY=980 EndZ=0
    g3: LineSegment StartX=0 StartY=980 StartZ=0 EndX=0 EndY=0 EndZ=0
    g4: LineSegment StartX=50 StartY=50 StartZ=0 EndX=500 EndY=50 EndZ=0
    g5: LineSegment StartX=500 StartY=50 StartZ=0 EndX=500 EndY=930 EndZ=0
    g6: LineSegment StartX=500 StartY=930 StartZ=0 EndX=50 EndY=930 EndZ=0
    g7: LineSegment StartX=50 StartY=930 StartZ=0 EndX=50 EndY=50 EndZ=0
    g8: LineSegment StartX=55 StartY=55 StartZ=0 EndX=495 EndY=55 EndZ=0
    g9: LineSegment StartX=495 StartY=55 StartZ=0 EndX=495 EndY=925 EndZ=0
    g10: LineSegment StartX=495 StartY=925 StartZ=0 EndX=55 EndY=925 EndZ=0
    g11: LineSegment StartX=55 StartY=925 StartZ=0 EndX=55 EndY=55 EndZ=0
    g12: LineSegment StartX=105 StartY=105 StartZ=0 EndX=445 EndY=105 EndZ=0
    g13: LineSegment StartX=445 StartY=105 StartZ=0 EndX=445 EndY=875 EndZ=0
    g14: LineSegment StartX=445 StartY=875 StartZ=0 EndX=105 EndY=875 EndZ=0
    g15: LineSegment StartX=105 StartY=875 StartZ=0 EndX=105 EndY=105 EndZ=0
  constraints (47):
    c: Coincident(g0,g1)
    c: Coincident(g1,g2)
    c: Coincident(g2,g3)
    c: Coincident(g3,g0)
    c: Horizontal(g0)
    c: Horizontal(g2)
    c: Vertical(g1)
    c: Vertical(g3)
    c: Coincident(g4,g5)
    c: Coincident(g5,g6)
    c: Coincident(g6,g7)
    c: Coincident(g7,g4)
    c: Horizontal(g4)
    c: Horizontal(g6)
    c: Vertical(g5)
    c: Vertical(g7)
    c: DistanceY(g1) = 980  'Height'
    c: DistanceX(g0) = 550  'Width'
    c: DistanceY(g6,g2) = 50  'Frame1'
    c: DistanceX(g2,g6) = 50  'Frame2'
    c: DistanceX(g4,g0) = 50  'Frame3'
    c: DistanceY(g0,g4) = 50  'Frame4'
    c: Coincident(g0,g-1)
    c: Coincident(g8,g9)
    c: Coincident(g9,g10)
    c: Coincident(g10,g11)
    c: Coincident(g11,g8)
    c: Horizontal(g8)
    c: Horizontal(g10)
    c: Vertical(g9)
    c: Vertical(g11)
    c: Coincident(g12,g13)
    c: Coincident(g13,g14)
    c: Coincident(g14,g15)
    c: Coincident(g15,g12)
    c: Horizontal(g12)
    c: Horizontal(g14)
    c: Vertical(g13)
    c: Vertical(g15)
    c: DistanceX(g8,g12) = 50  'Frame5'
    c: DistanceY(g8,g12) = 50  'Frame6'
    c: DistanceX(g14,g10) = 50  'Frame8'
    c: DistanceY(g14,g10) = 50  'Frame7'
    c: DistanceX(g4,g8) = 5
    c: DistanceY(g4,g8) = 5
    c: DistanceX(g10,g6) = 5
    c: DistanceY(g10,g6) = 5
FEATURE [Sketcher::SketchObject] Sketch321
  FullyConstrained = true
  Placement = pos=(6615,991.948,5039.09) rot=(1,0,0;0.610865rad)
  sketch-geometry (16):
    g0: LineSegment StartX=0 StartY=0 StartZ=0 EndX=550 EndY=0 EndZ=0
    g1: LineSegment StartX=550 StartY=0 StartZ=0 EndX=550 EndY=980 EndZ=0
    g2: LineSegment StartX=550 StartY=980 StartZ=0 EndX=0 EndY=980 EndZ=0
    g3: LineSegment StartX=0 StartY=980 StartZ=0 EndX=0 EndY=0 EndZ=0
    g4: LineSegment StartX=50 StartY=50 StartZ=0 EndX=500 EndY=50 EndZ=0
    g5: LineSegment StartX=500 StartY=50 StartZ=0 EndX=500 EndY=930 EndZ=0
    g6: LineSegment StartX=500 StartY=930 StartZ=0 EndX=50 EndY=930 EndZ=0
    g7: LineSegment StartX=50 StartY=930 StartZ=0 EndX=50 EndY=50 EndZ=0
    g8: LineSegment StartX=55 StartY=55 StartZ=0 EndX=495 EndY=55 EndZ=0
    g9: LineSegment StartX=495 StartY=55 StartZ=0 EndX=495 EndY=925 EndZ=0
    g10: LineSegment StartX=495 StartY=925 StartZ=0 EndX=55 EndY=925 EndZ=0
    g11: LineSegment StartX=55 StartY=925 StartZ=0 EndX=55 EndY=55 EndZ=0
    g12: LineSegment StartX=105 StartY=105 StartZ=0 EndX=445 EndY=105 EndZ=0
    g13: LineSegment StartX=445 StartY=105 StartZ=0 EndX=445 EndY=875 EndZ=0
    g14: LineSegment StartX=445 StartY=875 StartZ=0 EndX=105 EndY=875 EndZ=0
    g15: LineSegment StartX=105 StartY=875 StartZ=0 EndX=105 EndY=105 EndZ=0
  constraints (47):
    c: Coincident(g0,g1)
    c: Coincident(g1,g2)
    c: Coincident(g2,g3)
    c: Coincident(g3,g0)
    c: Horizontal(g0)
    c: Horizontal(g2)
    c: Vertical(g1)
    c: Vertical(g3)
    c: Coincident(g4,g5)
    c: Coincident(g5,g6)
    c: Coincident(g6,g7)
    c: Coincident(g7,g4)
    c: Horizontal(g4)
    c: Horizontal(g6)
    c: Vertical(g5)
    c: Vertical(g7)
    c: DistanceY(g1) = 980  'Height'
    c: DistanceX(g0) = 550  'Width'
    c: DistanceY(g6,g2) = 50  'Frame1'
    c: DistanceX(g2,g6) = 50  'Frame2'
    c: DistanceX(g4,g0) = 50  'Frame3'
    c: DistanceY(g0,g4) = 50  'Frame4'
    c: Coincident(g0,g-1)
    c: Coincident(g8,g9)
    c: Coincident(g9,g10)
    c: Coincident(g10,g11)
    c: Coincident(g11,g8)
    c: Horizontal(g8)
    c: Horizontal(g10)
    c: Vertical(g9)
    c: Vertical(g11)
    c: Coincident(g12,g13)
    c: Coincident(g13,g14)
    c: Coincident(g14,g15)
    c: Coincident(g15,g12)
    c: Horizontal(g12)
    c: Horizontal(g14)
    c: Vertical(g13)
    c: Vertical(g15)
    c: DistanceX(g8,g12) = 50  'Frame5'
    c: DistanceY(g8,g12) = 50  'Frame6'
    c: DistanceX(g14,g10) = 50  'Frame8'
    c: DistanceY(g14,g10) = 50  'Frame7'
    c: DistanceX(g4,g8) = 5
    c: DistanceY(g4,g8) = 5
    c: DistanceX(g10,g6) = 5
    c: DistanceY(g10,g6) = 5
FEATURE [Sketcher::SketchObject] Sketch322
  FullyConstrained = true
  Placement = pos=(4725,5626.01,5628.7) rot=(-1,0,0;0.610865rad)
  sketch-geometry (16):
    g0: LineSegment StartX=0 StartY=0 StartZ=0 EndX=550 EndY=0 EndZ=0
    g1: LineSegment StartX=550 StartY=0 StartZ=0 EndX=550 EndY=980 EndZ=0
    g2: LineSegment StartX=550 StartY=980 StartZ=0 EndX=0 EndY=980 EndZ=0
    g3: LineSegment StartX=0 StartY=980 StartZ=0 EndX=0 EndY=0 EndZ=0
    g4: LineSegment StartX=50 StartY=50 StartZ=0 EndX=500 EndY=50 EndZ=0
    g5: LineSegment StartX=500 StartY=50 StartZ=0 EndX=500 EndY=930 EndZ=0
    g6: LineSegment StartX=500 StartY=930 StartZ=0 EndX=50 EndY=930 EndZ=0
    g7: LineSegment StartX=50 StartY=930 StartZ=0 EndX=50 EndY=50 EndZ=0
    g8: LineSegment StartX=55 StartY=55 StartZ=0 EndX=495 EndY=55 EndZ=0
    g9: LineSegment StartX=495 StartY=55 StartZ=0 EndX=495 EndY=925 EndZ=0
    g10: LineSegment StartX=495 StartY=925 StartZ=0 EndX=55 EndY=925 EndZ=0
    g11: LineSegment StartX=55 StartY=925 StartZ=0 EndX=55 EndY=55 EndZ=0
    g12: LineSegment StartX=105 StartY=105 StartZ=0 EndX=445 EndY=105 EndZ=0
    g13: LineSegment StartX=445 StartY=105 StartZ=0 EndX=445 EndY=875 EndZ=0
    g14: LineSegment StartX=445 StartY=875 StartZ=0 EndX=105 EndY=875 EndZ=0
    g15: LineSegment StartX=105 StartY=875 StartZ=0 EndX=105 EndY=105 EndZ=0
  constraints (47):
    c: Coincident(g0,g1)
    c: Coincident(g1,g2)
    c: Coincident(g2,g3)
    c: Coincident(g3,g0)
    c: Horizontal(g0)
    c: Horizontal(g2)
    c: Vertical(g1)
    c: Vertical(g3)
    c: Coincident(g4,g5)
    c: Coincident(g5,g6)
    c: Coincident(g6,g7)
    c: Coincident(g7,g4)
    c: Horizontal(g4)
    c: Horizontal(g6)
    c: Vertical(g5)
    c: Vertical(g7)
    c: DistanceY(g1) = 980  'Height'
    c: DistanceX(g0) = 550  'Width'
    c: DistanceY(g6,g2) = 50  'Frame1'
    c: DistanceX(g2,g6) = 50  'Frame2'
    c: DistanceX(g4,g0) = 50  'Frame3'
    c: DistanceY(g0,g4) = 50  'Frame4'
    c: Coincident(g0,g-1)
    c: Coincident(g8,g9)
    c: Coincident(g9,g10)
    c: Coincident(g10,g11)
    c: Coincident(g11,g8)
    c: Horizontal(g8)
    c: Horizontal(g10)
    c: Vertical(g9)
    c: Vertical(g11)
    c: Coincident(g12,g13)
    c: Coincident(g13,g14)
    c: Coincident(g14,g15)
    c: Coincident(g15,g12)
    c: Horizontal(g12)
    c: Horizontal(g14)
    c: Vertical(g13)
    c: Vertical(g15)
    c: DistanceX(g8,g12) = 50  'Frame5'
    c: DistanceY(g8,g12) = 50  'Frame6'
    c: DistanceX(g14,g10) = 50  'Frame8'
    c: DistanceY(g14,g10) = 50  'Frame7'
    c: DistanceX(g4,g8) = 5
    c: DistanceY(g4,g8) = 5
    c: DistanceX(g10,g6) = 5
    c: DistanceY(g10,g6) = 5
FEATURE [Part::Part2DObjectPython] Line1465  # Draft 2D object (typed FeaturePython)
  Area = 0
  ChamferSize = 0
  Closed = true
  End = (5000,3900,7200)
  FilletRadius = 0
  Length = 7200
  MakeFace = true
  Placement = pos=(4655,3900,0) rot=(0,0,1;0rad)
  Points = (2) [(345,1.81899e-12,0),(345,9.09495e-13,7200)]
  Start = (5000,3900,0)
  Subdivisions = 0
FEATURE [Part::Part2DObjectPython] Rectangle3284  # Draft 2D object (typed FeaturePython)
  Area = 0
  ChamferSize = 0
  Columns = 1
  FilletRadius = 0
  Height = 8240
  Length = 14000
  MakeFace = false
  Placement = pos=(-740,-390,0) rot=(0,0,1;0rad)
  Rows = 1
FEATURE [Part::Extrusion] Extrude108
  Base = -> Rectangle3284
  Dir = (0,0,1)
  DirMode = 2
  FaceMakerClass = Part::FaceMakerBullseye
  LengthFwd = 5000
  LengthRev = 0
  Placement = pos=(0,0,2000) rot=(0,0,1;0rad)
  Solid = true
  Symmetric = false
FEATURE [Part::Part2DObjectPython] Wire825  # Draft 2D object (typed FeaturePython)
  Area = 0
  ChamferSize = 0
  Closed = true
  End = (9225,2390,0)
  FilletRadius = 0
  Length = 3200
  MakeFace = false
  Placement = pos=(8665,2390,0) rot=(0,0,1;0rad)
  Points = (4) [(0,0,0),(0,-1040,0),(560,-1040,0),(560,0,0)]
  Start = (8665,2390,0)
  Subdivisions = 0
FEATURE [Part::Part2DObjectPython] Line1468  label="облицовка ВШ_линия_005"  # Draft 2D object (typed FeaturePython)
  ChamferSize = 0
  Closed = true
  End = (8690,1355,0)
  FilletRadius = 0
  Length = 380
  MakeFace = false
  Placement = pos=(8900,1355,0) rot=(0,0,1;0rad)
  Points = (2) [(170,-9.09495e-13,0),(-210,9.09495e-13,0)]
  Start = (9070,1355,0)
  Subdivisions = 0
FEATURE [Part::Part2DObjectPython] Line1469  label="облицовка ВШ_линия_006"  # Draft 2D object (typed FeaturePython)
  ChamferSize = 0
  Closed = true
  End = (9200,2385,0)
  FilletRadius = 0
  Length = 380
  MakeFace = false
  Placement = pos=(8990,2385,0) rot=(0,0,1;3.14159rad)
  Points = (2) [(170,-9.09495e-13,0),(-210,9.09495e-13,0)]
  Start = (8820,2385,0)
  Subdivisions = 0
FEATURE [Part::Part2DObjectPython] Line1470  label="облицовка ВШ_линия_007"  # Draft 2D object (typed FeaturePython)
  ChamferSize = 0
  Closed = true
  End = (8690,2385,0)
  FilletRadius = 0
  Length = 900
  MakeFace = false
  Placement = pos=(8990,2385,0) rot=(0,0,1;3.14159rad)
  Points = (2) [(300,900,0),(300,2.72848e-12,0)]
  Start = (8690,1485,0)
  Subdivisions = 0
FEATURE [Part::Part2DObjectPython] Line1471  label="облицовка ВШ_линия_008"  # Draft 2D object (typed FeaturePython)
  ChamferSize = 0
  Closed = true
  End = (9200,1355,0)
  FilletRadius = 0
  Length = 900
  MakeFace = false
  Placement = pos=(8900,1355,0) rot=(0,0,1;0rad)
  Points = (2) [(300,900,0),(300,2.72848e-12,0)]
  Start = (9200,2255,0)
  Subdivisions = 0
FEATURE [Part::Part2DObjectPython] Rectangle3286  # Draft 2D object (typed FeaturePython)
  Area = 0
  ChamferSize = 0
  Columns = 1
  FilletRadius = 0
  Height = 1003.52
  Length = 550
  MakeFace = false
  Placement = pos=(5355,993.568,0) rot=(0,0,1;0rad)
  Rows = 1
FEATURE [Part::Part2DObjectPython] Rectangle3287  # Draft 2D object (typed FeaturePython)
  Area = 0
  ChamferSize = 0
  Columns = 1
  FilletRadius = 0
  Height = 1003.52
  Length = 550
  MakeFace = false
  Placement = pos=(6615,991.948,0) rot=(0,0,1;0rad)
  Rows = 1
FEATURE [Part::Part2DObjectPython] Rectangle3288  # Draft 2D object (typed FeaturePython)
  Area = 0
  ChamferSize = 0
  Columns = 1
  FilletRadius = 0
  Height = 1003.52
  Length = 550
  MakeFace = false
  Placement = pos=(4725,5425.25,0) rot=(0,0,1;0rad)
  Rows = 1
FEATURE [Part::Part2DObjectPython] Circle111  label="Circle112"  # Draft 2D object (typed FeaturePython)
  Area = 0
  FirstAngle = 0
  LastAngle = 0
  MakeFace = false
  Placement = pos=(8945,1979.8,0) rot=(0,0,1;0rad)
  Radius = 100
FEATURE [Part::Part2DObjectPython] Circle112  label="Circle113"  # Draft 2D object (typed FeaturePython)
  Area = 0
  FirstAngle = 0
  LastAngle = 0
  MakeFace = false
  Placement = pos=(8945,1979.8,0) rot=(0,0,1;0rad)
  Radius = 150
FEATURE [Part::Part2DObjectPython] Circle115  label="Circle116"  # Draft 2D object (typed FeaturePython)
  Area = 0
  FirstAngle = 0
  LastAngle = 0
  MakeFace = false
  Placement = pos=(8867.89,1548.23,0) rot=(0,0,1;0rad)
  Radius = 55
FEATURE [Part::Part2DObjectPython] Circle116  label="Circle117"  # Draft 2D object (typed FeaturePython)
  Area = 0
  FirstAngle = 0
  LastAngle = 0
  MakeFace = false
  Placement = pos=(8945,2200.27,0) rot=(0,0,1;0rad)
  Radius = 30
FEATURE [Part::FeaturePython] Array064  # Draft array (typed FeaturePython)
  Angle = 360
  ArrayType = 0
  Axis = (0,0,1)
  Base = -> Circle115
  Center = (0,0,0)
  Count = 4
  ExpandArray = false
  Fuse = false
  IntervalAxis = (0,0,0)
  IntervalX = (150,0,0)
  IntervalY = (0,150,0)
  IntervalZ = (0,0,100)
  NumberCircles = 3
  NumberPolar = 5
  NumberX = 2
  NumberY = 2
  NumberZ = 1
  PlacementList = 4 placements: [(8867.89,1548.23,0),(8867.89,1698.23,0),(9017.89,1548.23,0),(9017.89,1698.23,0)]
  RadialDistance = 50
  ScaleList = (4) [(1,1,1),(1,1,1),(1,1,1),(1,1,1)]
  Symmetry = 1
  TangentialDistance = 25
FEATURE [Part::Part2DObjectPython] Circle117  label="Circle118"  # Draft 2D object (typed FeaturePython)
  Area = 0
  FirstAngle = 0
  LastAngle = 0
  MakeFace = false
  Placement = pos=(8945,2200.27,0) rot=(0,0,1;0rad)
  Radius = 55
FEATURE [Part::Part2DObjectPython] Line1478  # Draft 2D object (typed FeaturePython)
  Area = 0
  ChamferSize = 0
  Closed = true
  End = (8915,2029.8,6981)
  FilletRadius = 0
  Length = 0
  MakeFace = false
  Placement = pos=(8915,2029.8,6981) rot=(0,0,1;0rad)
  Points = (2) [(0,0,0),(0,0,0)]
  Start = (8915,2029.8,6981)
  Subdivisions = 0
FEATURE [Part::Part2DObjectPython] Line1479  # Draft 2D object (typed FeaturePython)
  Area = 0
  ChamferSize = 0
  Closed = true
  End = (8945,1979.8,7581)
  FilletRadius = 0
  Length = 5600
  MakeFace = false
  Placement = pos=(8945,1979.8,6981) rot=(0,0,1;0rad)
  Points = (2) [(0,2.50111e-12,-5000),(0,0,600)]
  Start = (8945,1979.8,1981)
  Subdivisions = 0
FEATURE [Part::Part2DObjectPython] Wire828  # Draft 2D object (typed FeaturePython)
  Area = 0
  ChamferSize = 0
  Closed = false
  End = (8945,1979.8,6981)
  FilletRadius = 0
  Length = 5777.48
  MakeFace = false
  Placement = pos=(9130,2120,1300) rot=(0,0,1;0rad)
  Points = (4) [(0,0,0),(0,0,500),(-185,-140.202,731),(-185,-140.202,5681)]
  Start = (9130,2120,1300)
  Subdivisions = 0
FEATURE [Part::Part2DObjectPython] Line1480  # Draft 2D object (typed FeaturePython)
  Area = 0
  ChamferSize = 0
  Closed = false
  End = (8867.89,1698.23,6980)
  FilletRadius = 0
  Length = 4200
  MakeFace = false
  Placement = pos=(8867.89,1698.23,2780) rot=(0,0,1;0rad)
  Points = (2) [(0,0,0),(0,0,4200)]
  Start = (8867.89,1698.23,2780)
  Subdivisions = 0
FEATURE [Part::Part2DObjectPython] Line1481  # Draft 2D object (typed FeaturePython)
  Area = 0
  ChamferSize = 0
  Closed = false
  End = (8948,-1570,3275.2)
  FilletRadius = 0
  Length = 5500
  MakeFace = false
  Placement = pos=(3448,-1570,3275.2) rot=(1,0,0;0.610865rad)
  Points = (2) [(0,0,0),(5500,2.27374e-13,9.09495e-13)]
  Start = (3448,-1570,3275.2)
  Subdivisions = 0
FEATURE [Part::Part2DObjectPython] Line1482  # Draft 2D object (typed FeaturePython)
  Area = 0
  ChamferSize = 0
  Closed = false
  End = (8948,-1447.13,3361.23)
  FilletRadius = 0
  Length = 5500
  MakeFace = false
  Placement = pos=(3448,-1447.13,3361.23) rot=(1,0,0;0.610865rad)
  Points = (2) [(0,0,0),(5500,2.27374e-13,-9.09495e-13)]
  Start = (3448,-1447.13,3361.23)
  Subdivisions = 0
FEATURE [Part::Part2DObjectPython] Line1483  # Draft 2D object (typed FeaturePython)
  Area = 0
  ChamferSize = 0
  Closed = false
  End = (8948,-1447.13,3461.23)
  FilletRadius = 0
  Length = 5500
  MakeFace = false
  Placement = pos=(3448,-1447.13,3461.23) rot=(1,0,0;0.610865rad)
  Points = (2) [(0,0,0),(5500,2.27374e-13,-9.09495e-13)]
  Start = (3448,-1447.13,3461.23)
  Subdivisions = 0
FEATURE [Part::Part2DObjectPython] Line1484  # Draft 2D object (typed FeaturePython)
  Area = 0
  ChamferSize = 0
  Closed = false
  End = (8948,-1570,3375.2)
  FilletRadius = 0
  Length = 5500
  MakeFace = false
  Placement = pos=(3448,-1570,3375.2) rot=(1,0,0;0.610865rad)
  Points = (2) [(0,0,0),(5500,0,0)]
  Start = (3448,-1570,3375.2)
  Subdivisions = 0
FEATURE [Part::FeaturePython] Pipe014  label="Снегозадержатели 010"  # Arch/BIM 98 (typed FeaturePython)
  Base = -> Line1481
  Diameter = 25
  GlobalId = 3FGB4W65b7$RelxxBEC_I3
  HorizontalArea = 0
  IfcData = IfcUID=3FGB4W65b7$RelxxBEC_I3,+2 more (map truncated)
  IfcType = 98
  Length = 5500
  MoveBase = false
  MoveWithHost = false
  OffsetEnd = 0
  OffsetStart = 0
  PerimeterLength = 0
  Placement = pos=(0,0,50) rot=(0,0,1;0rad)
  PredefinedType = 0
  VerticalArea = 0
  WallThickness = 0
FEATURE [Part::FeaturePython] Pipe015  label="Снегозадержатели 011"  # Arch/BIM 98 (typed FeaturePython)
  Base = -> Line1482
  Diameter = 25
  GlobalId = 0m162zSxL9MvR8JxGsHhMh
  HorizontalArea = 0
  IfcData = IfcUID=0m162zSxL9MvR8JxGsHhMh,+2 more (map truncated)
  IfcType = 98
  Length = 5500
  MoveBase = false
  MoveWithHost = false
  OffsetEnd = 0
  OffsetStart = 0
  PerimeterLength = 0
  Placement = pos=(0,0,50) rot=(0,0,1;0rad)
  PredefinedType = 0
  VerticalArea = 0
  WallThickness = 0
FEATURE [Part::FeaturePython] Pipe016  label="Снегозадержатели 012"  # Arch/BIM 98 (typed FeaturePython)
  Base = -> Line1483
  Diameter = 25
  GlobalId = 1BHvc1NuD0qQo1xGtb2qrX
  HorizontalArea = 0
  IfcData = IfcUID=1BHvc1NuD0qQo1xGtb2qrX,+2 more (map truncated)
  IfcType = 98
  Length = 5500
  MoveBase = false
  MoveWithHost = false
  OffsetEnd = 0
  OffsetStart = 0
  PerimeterLength = 0
  Placement = pos=(0,0,50) rot=(0,0,1;0rad)
  PredefinedType = 0
  VerticalArea = 0
  WallThickness = 0
FEATURE [Part::FeaturePython] Pipe017  label="Снегозадержатели 001"  # Arch/BIM 98 (typed FeaturePython)
  Base = -> Line1484
  Diameter = 25
  GlobalId = 3Gvi8SLif8WfTz7jjSrXL2
  HorizontalArea = 0
  IfcData = IfcUID=3Gvi8SLif8WfTz7jjSrXL2,+2 more (map truncated)
  IfcType = 98
  Length = 5500
  MoveBase = false
  MoveWithHost = false
  OffsetEnd = 0
  OffsetStart = 0
  PerimeterLength = 0
  Placement = pos=(0,0,50) rot=(0,0,1;0rad)
  PredefinedType = 0
  VerticalArea = 0
  WallThickness = 0
FEATURE [Part::Part2DObjectPython] Line1486  # Draft 2D object (typed FeaturePython)
  Area = 0
  ChamferSize = 0
  Closed = true
  End = (7257,9030,3275.2)
  FilletRadius = 0
  Length = 4460
  MakeFace = false
  Placement = pos=(11717,9030,3275.2) rot=(0,0.300706,0.953717;3.14159rad)
  Points = (2) [(0,0,0),(4460,-5.92209e-05,-8.45762e-05)]
  Start = (11717,9030,3275.2)
  Subdivisions = 0
FEATURE [Part::Part2DObjectPython] Line1487  # Draft 2D object (typed FeaturePython)
  Area = 0
  ChamferSize = 0
  Closed = false
  End = (7257,8907.13,3361.23)
  FilletRadius = 0
  Length = 4460
  MakeFace = false
  Placement = pos=(11717,8907.13,3361.23) rot=(0,0.300706,0.953717;3.14159rad)
  Points = (2) [(0,0,0),(4460,-9.09495e-13,-1.81899e-12)]
  Start = (11717,8907.13,3361.23)
  Subdivisions = 0
FEATURE [Part::Part2DObjectPython] Line1488  # Draft 2D object (typed FeaturePython)
  Area = 0
  ChamferSize = 0
  Closed = false
  End = (7345,8907.13,3461.23)
  FilletRadius = 0
  Length = 4460
  MakeFace = false
  Placement = pos=(11805,8907.13,3461.23) rot=(0,0.300706,0.953717;3.14159rad)
  Points = (2) [(0,0,0),(4460,0,-9.09495e-13)]
  Start = (11805,8907.13,3461.23)
  Subdivisions = 0
FEATURE [Part::Part2DObjectPython] Line1489  # Draft 2D object (typed FeaturePython)
  Area = 0
  ChamferSize = 0
  Closed = false
  End = (7345,9030,3375.2)
  FilletRadius = 0
  Length = 4460
  MakeFace = false
  Placement = pos=(11805,9030,3375.2) rot=(0,0.300706,0.953717;3.14159rad)
  Points = (2) [(0,0,0),(4460,0,0)]
  Start = (11805,9030,3375.2)
  Subdivisions = 0
FEATURE [Part::FeaturePython] Pipe018  label="Снегозадержатели 013"  # Arch/BIM 98 (typed FeaturePython)
  Base = -> Line1486
  Diameter = 25
  GlobalId = 0psA13S1r3kfjsLgw5ftBB
  HorizontalArea = 0
  IfcData = IfcUID=0psA13S1r3kfjsLgw5ftBB,+2 more (map truncated)
  IfcType = 98
  Length = 4460
  MoveBase = false
  MoveWithHost = false
  OffsetEnd = 0
  OffsetStart = 0
  PerimeterLength = 0
  Placement = pos=(0,0,50) rot=(0,0,1;0rad)
  PredefinedType = 0
  VerticalArea = 0
  WallThickness = 0
FEATURE [Part::FeaturePython] Pipe019  label="Снегозадержатели 014"  # Arch/BIM 98 (typed FeaturePython)
  Base = -> Line1487
  Diameter = 25
  GlobalId = 1ajV3GjIH90PewpSEaAIL9
  HorizontalArea = 0
  IfcData = IfcUID=1ajV3GjIH90PewpSEaAIL9,+2 more (map truncated)
  IfcType = 98
  Length = 4460
  MoveBase = false
  MoveWithHost = false
  OffsetEnd = 0
  OffsetStart = 0
  PerimeterLength = 0
  Placement = pos=(0,0,50) rot=(0,0,1;0rad)
  PredefinedType = 0
  VerticalArea = 0
  WallThickness = 0
FEATURE [Part::FeaturePython] Pipe020  label="Снегозадержатели 015"  # Arch/BIM 98 (typed FeaturePython)
  Base = -> Line1488
  Diameter = 25
  GlobalId = 3F76V0rxL2cvmgn6TVRcv1
  HorizontalArea = 0
  IfcData = IfcUID=3F76V0rxL2cvmgn6TVRcv1,+2 more (map truncated)
  IfcType = 98
  Length = 4460
  MoveBase = false
  MoveWithHost = false
  OffsetEnd = 0
  OffsetStart = 0
  PerimeterLength = 0
  Placement = pos=(0,0,50) rot=(0,0,1;0rad)
  PredefinedType = 0
  VerticalArea = 0
  WallThickness = 0
FEATURE [Part::FeaturePython] Pipe021  label="Снегозадержатели 016"  # Arch/BIM 98 (typed FeaturePython)
  Base = -> Line1489
  Diameter = 25
  GlobalId = 2T$R0KaZDBcBfa4GgFt7Wm
  HorizontalArea = 0
  IfcData = IfcUID=2T$R0KaZDBcBfa4GgFt7Wm,+2 more (map truncated)
  IfcType = 98
  Length = 4460
  MoveBase = false
  MoveWithHost = false
  OffsetEnd = 0
  OffsetStart = 0
  PerimeterLength = 0
  Placement = pos=(0,0,50) rot=(0,0,1;0rad)
  PredefinedType = 0
  VerticalArea = 0
  WallThickness = 0
FEATURE [Part::Part2DObjectPython] Wire829  # Draft 2D object (typed FeaturePython)
  Area = 0
  ChamferSize = 0
  Closed = false
  End = (4000,-25,0)
  FilletRadius = 0
  Length = 11020
  MakeFace = false
  Placement = pos=(3510,3520,0) rot=(0,0,1;0rad)
  Points = (4) [(-110,15,0),(-3540,15,0),(-3540,-3545,0),(490,-3545,0)]
  Start = (3400,3535,0)
  Subdivisions = 0
FEATURE [Part::Part2DObjectPython] Wire830  # Draft 2D object (typed FeaturePython)
  Area = 0
  ChamferSize = 0
  Closed = false
  End = (8945,2200.27,7500)
  FilletRadius = 0
  Length = 6119.59
  MakeFace = false
  Placement = pos=(8330,2125,2000) rot=(0,0,1;0rad)
  Points = (4) [(0,0,0),(0,0,200),(615,75.27,200),(615,75.27,5500)]
  Start = (8330,2125,2000)
  Subdivisions = 0
FEATURE [Part::Part2DObjectPython] Rectangle3296  # Draft 2D object (typed FeaturePython)
  Area = 0
  ChamferSize = 0
  Columns = 1
  FilletRadius = 0
  Height = 1030
  Length = 510
  MakeFace = false
  Placement = pos=(8690,1355,0) rot=(0,0,1;0rad)
  Rows = 1
FEATURE [Part::Part2DObjectPython] Rectangle3297  label="проём вентшахты001"  # Draft 2D object (typed FeaturePython)
  ChamferSize = 0
  Columns = 1
  FilletRadius = 0
  Height = 800
  Length = 320
  MakeFace = false
  Placement = pos=(8785,1470,0) rot=(0,0,1;0rad)
  Rows = 1
FEATURE [Part::Part2DObjectPython] Line1497  # Draft 2D object (typed FeaturePython)
  Area = 0
  ChamferSize = 0
  Closed = true
  End = (3725,3730,0)
  FilletRadius = 0
  Length = 6908.43
  MakeFace = true
  Placement = pos=(-1230,8670,0) rot=(0,0,1;0rad)
  Points = (2) [(70,-55,0),(4955,-4940,0)]
  Start = (-1160,8615,0)
  Subdivisions = 0
FEATURE [Part::Part2DObjectPython] Line1498  # Draft 2D object (typed FeaturePython)
  Area = 0
  ChamferSize = 0
  Closed = true
  End = (-1160,-1155,0)
  FilletRadius = 0
  Length = 6908.43
  MakeFace = true
  Placement = pos=(3710,3730,0) rot=(0,0,1;0rad)
  Points = (2) [(15,0,0),(-4870,-4885,0)]
  Start = (3725,3730,0)
  Subdivisions = 0
FEATURE [Part::Part2DObjectPython] Line1499  # Draft 2D object (typed FeaturePython)
  Area = 0
  ChamferSize = 0
  Closed = true
  End = (8795,3730,0)
  FilletRadius = 0
  Length = 5070
  MakeFace = true
  Placement = pos=(3710,3730,0) rot=(0,0,1;0rad)
  Points = (2) [(15,0,0),(5085,0,0)]
  Start = (3725,3730,0)
  Subdivisions = 0
FEATURE [Part::Part2DObjectPython] Line1500  # Draft 2D object (typed FeaturePython)
  Area = 0
  ChamferSize = 0
  Closed = true
  End = (13680,8615,0)
  FilletRadius = 0
  Length = 6908.43
  MakeFace = true
  Placement = pos=(8810,3730,0) rot=(0,0,1;0rad)
  Points = (2) [(-15,-4.54747e-13,0),(4870,4885,0)]
  Start = (8795,3730,0)
  Subdivisions = 0
FEATURE [Part::Part2DObjectPython] Line1501  # Draft 2D object (typed FeaturePython)
  Area = 0
  ChamferSize = 0
  Closed = true
  End = (13680,-1155,0)
  FilletRadius = 0
  Length = 6908.43
  MakeFace = true
  Placement = pos=(8810,3730,0) rot=(0,0,1;0rad)
  Points = (2) [(-15,-4.54747e-13,0),(4870,-4885,0)]
  Start = (8795,3730,0)
  Subdivisions = 0
FEATURE [Part::Part2DObjectPython] Line1502  # Draft 2D object (typed FeaturePython)
  Area = 0
  ChamferSize = 0
  Closed = true
  End = (13260,7465.93,0)
  FilletRadius = 0
  Length = 5283.4
  MakeFace = true
  Placement = pos=(9480,3730,0) rot=(0,0,1;0rad)
  Points = (2) [(44.0742,-4.54747e-13,0),(3780,3735.93,0)]
  Start = (9524.07,3730,0)
  Subdivisions = 0
FEATURE [Part::Part2DObjectPython] Line1503  # Draft 2D object (typed FeaturePython)
  Area = 0
  ChamferSize = 0
  Closed = true
  End = (13260,-5.92599,0)
  FilletRadius = 0
  Length = 5283.4
  MakeFace = true
  Placement = pos=(9480,3730,0) rot=(0,0,1;0rad)
  Points = (2) [(44.0742,-4.54747e-13,0),(3780,-3735.93,0)]
  Start = (9524.07,3730,0)
  Subdivisions = 0
FEATURE [Part::Part2DObjectPython] Line1504  # Draft 2D object (typed FeaturePython)
  Area = 0
  ChamferSize = 0
  Closed = true
  End = (13260,-5.92599,0)
  FilletRadius = 0
  Length = 7471.85
  MakeFace = true
  Placement = pos=(13310,7560,0) rot=(0,0,1;0rad)
  Points = (2) [(-50,-94.0742,0),(-50,-7565.93,0)]
  Start = (13260,7465.93,0)
  Subdivisions = 0
FEATURE [Part::Part2DObjectPython] Line1505  # Draft 2D object (typed FeaturePython)
  Area = 0
  ChamferSize = 0
  Closed = true
  End = (-740,-5.926,0)
  FilletRadius = 0
  Length = 7471.85
  MakeFace = true
  Placement = pos=(-810,7580,0) rot=(0,0,1;0rad)
  Points = (2) [(70,-114.074,0),(70,-7585.93,0)]
  Start = (-740,7465.93,0)
  Subdivisions = 0
FEATURE [Part::Part2DObjectPython] Line1506  # Draft 2D object (typed FeaturePython)
  Area = 0
  ChamferSize = 0
  Closed = true
  End = (2995.93,3730,0)
  FilletRadius = 0
  Length = 5283.4
  MakeFace = true
  Placement = pos=(-810,-120,0) rot=(0,0,1;0rad)
  Points = (2) [(70,114.074,0),(3805.93,3850,0)]
  Start = (-740,-5.926,0)
  Subdivisions = 0
FEATURE [Part::Part2DObjectPython] Line1507  # Draft 2D object (typed FeaturePython)
  Area = 0
  ChamferSize = 0
  Closed = true
  End = (-740,7465.93,0)
  FilletRadius = 0
  Length = 5283.4
  MakeFace = true
  Placement = pos=(3040,3730,0) rot=(0,0,1;0rad)
  Points = (2) [(-44.074,0,0),(-3780,3735.93,0)]
  Start = (2995.93,3730,0)
  Subdivisions = 0
FEATURE [Part::Part2DObjectPython] Wire831  # Draft 2D object (typed FeaturePython)
  Area = 3.576e+06
  ChamferSize = 0
  Closed = true
  End = (11950,575,0)
  FilletRadius = 0
  Length = 13120
  MakeFace = true
  Placement = pos=(9550,575,0) rot=(0,0,1;0rad)
  Points = (6) [(0,0,0),(0,-600,0),(3000,-600,0),(3000,2960,0),(2400,2960,0),(2400,4.54747e-13,0)]
  Start = (9550,575,0)
  Subdivisions = 0
FEATURE [Part::Part2DObjectPython] Rectangle3298  label="Шкаф 60 017"  # Draft 2D object (typed FeaturePython)
  Area = 486000
  ChamferSize = 0
  Columns = 1
  FilletRadius = 0
  Height = 1215
  Length = 400
  MakeFace = true
  Placement = pos=(-30,3825,0) rot=(0,0,1;0rad)
  Rows = 1
FEATURE [Part::Part2DObjectPython] Rectangle3299  label="Шкаф 60 018"  # Draft 2D object (typed FeaturePython)
  Area = 840000
  ChamferSize = 0
  Columns = 1
  FilletRadius = 0
  Height = 600
  Length = 1400
  MakeFace = true
  Placement = pos=(-30,5040,0) rot=(0,0,1;0rad)
  Rows = 1
FEATURE [Part::Part2DObjectPython] Rectangle3300  label="Шкаф 60 019"  # Draft 2D object (typed FeaturePython)
  Area = 840000
  ChamferSize = 0
  Columns = 1
  FilletRadius = 0
  Height = 600
  Length = 1400
  MakeFace = true
  Placement = pos=(-30,5640,0) rot=(0,0,1;0rad)
  Rows = 1
FEATURE [Part::Part2DObjectPython] Rectangle3302  # Draft 2D object (typed FeaturePython)
  ChamferSize = 0
  Columns = 1
  FilletRadius = 100
  Height = 1500
  Length = 750
  MakeFace = true
  Placement = pos=(-10,1890,0) rot=(0,0,1;0rad)
  Rows = 1
FEATURE [Sketcher::SketchObject] Sketch323  label="кресло 45'014"
  FullyConstrained = false
  Placement = pos=(850,2620,0) rot=(0,0,-1;1.5708rad)
  sketch-geometry (11):
    g0: LineSegment StartX=-280 StartY=-350 StartZ=0 EndX=280 EndY=-350 EndZ=0
    g1: LineSegment StartX=330 StartY=-300 StartZ=0 EndX=330 EndY=300 EndZ=0
    g2: LineSegment StartX=280 StartY=350 StartZ=0 EndX=-280 EndY=350 EndZ=0
    g3: LineSegment StartX=-330 StartY=300 StartZ=0 EndX=-330 EndY=-300 EndZ=0
    g4: ArcOfCircle CenterX=-280 CenterY=300 CenterZ=0 NormalX=0 NormalY=0 NormalZ=1 AngleXU=0 Radius=50 StartAngle=1.5708 EndAngle=3.14159
    g5: ArcOfCircle CenterX=280 CenterY=300 CenterZ=0 NormalX=0 NormalY=0 NormalZ=1 AngleXU=0 Radius=50 StartAngle=-9e-16 EndAngle=1.5708
    g6: ArcOfCircle CenterX=280 CenterY=-300 CenterZ=0 NormalX=0 NormalY=0 NormalZ=1 AngleXU=0 Radius=50 StartAngle=4.71239 EndAngle=6.28319
    g7: ArcOfCircle CenterX=-280 CenterY=-300 CenterZ=0 NormalX=0 NormalY=0 NormalZ=1 AngleXU=0 Radius=50 StartAngle=3.14159 EndAngle=4.71239
    g8: LineSegment StartX=-330 StartY=200 StartZ=0 EndX=330 EndY=200 EndZ=0
    g9: LineSegment StartX=-230 StartY=200 StartZ=0 EndX=-230 EndY=-350 EndZ=0
    g10: LineSegment StartX=230 StartY=200 StartZ=0 EndX=230 EndY=-350 EndZ=0
  constraints (29):
    c: Horizontal(g0)
    c: Vertical(g1)
    c: Vertical(g3)
    c: Tangent(g2,g4) = -1.5708
    c: Tangent(g3,g4) = -1.5708
    c: Tangent(g2,g5) = -1.5708
    c: Tangent(g1,g5) = -1.5708
    c: Tangent(g0,g6) = -1.5708
    c: Tangent(g1,g6) = -1.5708
    c: Tangent(g3,g7) = -1.5708
    c: Tangent(g0,g7) = -1.5708
    c: DistanceY(g0,g2) = 700
    c: DistanceX(g3,g1) = 660
    c: Equal(g4,g5)
    c: Equal(g7,g6)
    c: Radius(g5) = 50
    c: Symmetric(g2,g2,g-2)
    c: Symmetric(g2,g0,g-1)
    c: PointOnObject(g8,g3)
    c: PointOnObject(g8,g1)
    c: Horizontal(g8)
    c: DistanceY(g8,g2) = 150
    c: PointOnObject(g9,g8)
    c: PointOnObject(g9,g0)
    c: Vertical(g9)
    c: PointOnObject(g10,g0)
    c: Vertical(g10)
    c: DistanceX(g10,g8) = 100
    c: Symmetric(g10,g9,g-2)
FEATURE [Part::Part2DObjectPython] Rectangle3303  label="Шкаф 60 020"  # Draft 2D object (typed FeaturePython)
  Area = 1386000
  ChamferSize = 0
  Columns = 1
  FilletRadius = 0
  Height = 2310
  Length = 600
  MakeFace = true
  Placement = pos=(3400,-25,0) rot=(0,0,1;0rad)
  Rows = 1
FEATURE [Part::Part2DObjectPython] Rectangle3304  # Draft 2D object (typed FeaturePython)
  ChamferSize = 0
  Columns = 1
  FilletRadius = 0
  Height = 1800
  Length = 2100
  MakeFace = true
  Placement = pos=(3570,6525,0) rot=(0,0,1;3.14159rad)
  Rows = 1
FEATURE [Part::Part2DObjectPython] Rectangle3305  # Draft 2D object (typed FeaturePython)
  Area = 0
  ChamferSize = 0
  Columns = 1
  FilletRadius = 0
  Height = 600
  Length = 350
  MakeFace = false
  Placement = pos=(1570,5725,0) rot=(0,0,1;0rad)
  Rows = 1
FEATURE [Part::Part2DObjectPython] Rectangle3306  # Draft 2D object (typed FeaturePython)
  Area = 0
  ChamferSize = 0
  Columns = 1
  FilletRadius = 0
  Height = 600
  Length = 350
  MakeFace = false
  Placement = pos=(1570,4945,0) rot=(0,0,1;0rad)
  Rows = 1
FEATURE [Part::Part2DObjectPython] Rectangle3307  label="Шкаф 60 021"  # Draft 2D object (typed FeaturePython)
  Area = 600000
  ChamferSize = 0
  Columns = 1
  FilletRadius = 0
  Height = 400
  Length = 1500
  MakeFace = true
  Placement = pos=(4100,-25,0) rot=(0,0,1;0rad)
  Rows = 1
FEATURE [Part::Part2DObjectPython] Rectangle3308  label="Шкаф 60 022"  # Draft 2D object (typed FeaturePython)
  Area = 900000
  ChamferSize = 0
  Columns = 1
  FilletRadius = 0
  Height = 600
  Length = 1500
  MakeFace = true
  Placement = pos=(4100,1685,0) rot=(0,0,1;0rad)
  Rows = 1
FEATURE [Part::Part2DObjectPython] Rectangle3309  label="Шкаф 60 023"  # Draft 2D object (typed FeaturePython)
  Area = 1.3398e+06
  ChamferSize = 0
  Columns = 1
  FilletRadius = 0
  Height = 2310
  Length = 580
  MakeFace = true
  Placement = pos=(6770,-25,0) rot=(0,0,1;0rad)
  Rows = 1
FEATURE [Part::Part2DObjectPython] Rectangle3310  label="TV 54" 001"  # Draft 2D object (typed FeaturePython)
  ChamferSize = 0
  Columns = 1
  FilletRadius = 0
  Height = 1200
  Length = 75
  MakeFace = false
  Placement = pos=(8190,6215,0) rot=(0,0,1;3.14159rad)
  Rows = 1
FEATURE [Part::Part2DObjectPython] Circle119  label="Circle120"  # Draft 2D object (typed FeaturePython)
  Area = 196350
  FirstAngle = 0
  LastAngle = 0
  MakeFace = true
  Placement = pos=(7730,1990,0) rot=(0,0,1;0rad)
  Radius = 250
FEATURE [Part::Part2DObjectPython] Circle120  label="Circle121"  # Draft 2D object (typed FeaturePython)
  Area = 0
  FirstAngle = 0
  LastAngle = 0
  MakeFace = false
  Placement = pos=(7730,1990,0) rot=(0,0,1;0rad)
  Radius = 175
FEATURE [Part::Part2DObjectPython] Rectangle3311  # Draft 2D object (typed FeaturePython)
  Area = 259500
  ChamferSize = 0
  Columns = 1
  FilletRadius = 0
  Height = 1730
  Length = 150
  MakeFace = true
  Placement = pos=(7450,-25,0) rot=(0,0,1;0rad)
  Rows = 1
FEATURE [Part::Part2DObjectPython] Rectangle3312  # Draft 2D object (typed FeaturePython)
  Area = 100000
  ChamferSize = 0
  Columns = 1
  FilletRadius = 0
  Height = 250
  Length = 400
  MakeFace = true
  Placement = pos=(8130,2000,0) rot=(0,0,1;0rad)
  Rows = 1
FEATURE [Part::Part2DObjectPython] Wire833  # Draft 2D object (typed FeaturePython)
  Area = 0
  ChamferSize = 0
  Closed = false
  End = (7390,5600,0)
  FilletRadius = 0
  Length = 2341.58
  MakeFace = true
  Placement = pos=(8310,7021.58,0) rot=(0,0,1;0rad)
  Points = (3) [(0,0,0),(-920,0,0),(-920,-1421.58,0)]
  Start = (8310,7021.58,0)
  Subdivisions = 0
FEATURE [Part::Part2DObjectPython] Wire835  # Draft 2D object (typed FeaturePython)
  Area = 0
  ChamferSize = 0
  Closed = true
  End = (7490,5800,0)
  FilletRadius = 0
  Length = 647.214
  MakeFace = false
  Placement = pos=(7390,5600,0) rot=(0,0,1;0rad)
  Points = (3) [(0,0,0),(-100,200,0),(100,200,0)]
  Start = (7390,5600,0)
  Subdivisions = 0
FEATURE [Part::Part2DObjectPython] Rectangle3316  label="проём в перекрытии под фан.стояк002"  # Draft 2D object (typed FeaturePython)
  ChamferSize = 0
  Columns = 1
  FilletRadius = 0
  Height = 250
  Length = 150
  MakeFace = false
  Placement = pos=(4910,3805,0) rot=(0,0,1;0rad)
  Rows = 1
FEATURE [Part::FeaturePython] Structure360  label="Вентстояк вычитаемы объём 003"  # Arch/BIM 52 (typed FeaturePython)
  Base = -> Rectangle3316
  FaceMaker = 0
  GlobalId = 0eTNl8duH9Xv7LHx2JWCfz
  Height = 6000
  HorizontalArea = 37500
  IfcData = IfcUID=0eTNl8duH9Xv7LHx2JWCfz,attributes={"GlobalId": {"value": "0eTNl8duH9Xv7LHx2JWCfz"}},+1 more (map truncated)
  IfcType = 52
  Length = 0
  MoveBase = false
  MoveWithHost = false
  Nodes = (2) [(4985,3930,0),(4985,3930,6000)]
  NodesOffset = 0
  Normal = (0,0,0)
  PerimeterLength = 800
  Placement = pos=(0,0,-200) rot=(0,0,1;0rad)
  VerticalArea = 4800000
  Width = 100
FEATURE [Part::Cut] Cut048  label="ПНО-39-15 1шт. рез. (1)"
  Base = -> Extrude093
  Tool = -> Structure360
FEATURE [Part::Cut] Cut049  label="ПНО-39-12 1шт. рез. (3)"
  Base = -> Extrude094
  Tool = -> Structure360
FEATURE [App::FeaturePython] Dimension024  # Draft dimension (typed FeaturePython)
  Diameter = false
  Dimline = (9500,-1500,0)
  Direction = (0,0,0)
  Distance = 3260
  End = (12760,-2107.94,0)
  Normal = (0,0,1)
  Start = (9500,-2107.94,0)
FEATURE [Part::Part2DObjectPython] Circle121  label="Circle122"  # Draft 2D object (typed FeaturePython)
  Area = 0
  FirstAngle = 0
  LastAngle = 0
  MakeFace = false
  Placement = pos=(4985,3900,0) rot=(0,0,1;0rad)
  Radius = 55
FEATURE [TechDraw::DrawSVGTemplate] Template001
  EditableTexts = Лист=6; Номер=ИЖС-2021.0001
  Height = 297
  Orientation = 1
  Width = 420
FEATURE [App::MaterialObjectPython] Material  label="Wood"  # material (typed FeaturePython)
  Description = A standard construction wood
  Material = AuthorAndLicense=Wood-Generic,CardName=Wood-Generic,Color=(1.0, 0.8196078431372549, 0.0, 1.0),Density=700 kg/m^3,+10 more (map truncated)
  ProductURL = https://en.wikipedia.org/wiki/Wood
  Transparency = 0
FEATURE [Part::FeaturePython] Wall057  label="мауэрлат"  # Arch/BIM 166 (typed FeaturePython)
  Align = 0
  Area = 6027000
  Base = -> Rectangle2788
  BlockHeight = 0
  BlockLength = 0
  CountBroken = 0
  CountEntire = 0
  Face = 0
  GlobalId = 1B71KP0Y9AOfuyJlUXW0eC
  Height = 150
  HorizontalArea = 6.303e+06
  IfcData = IfcUID=1B71KP0Y9AOfuyJlUXW0eC; attributes={"GlobalId": {"value": "1B71KP0Y9AOfuyJlUXW0eC"}}
  IfcType = 166
  Joint = 0
  Length = 40180
  MakeBlocks = false
  Material = -> Material
  MoveBase = false
  MoveWithHost = false
  Normal = (0,0,0)
  Offset = 155
  OffsetFirst = 0
  OffsetSecond = 0
  PerimeterLength = 42620
  Placement = pos=(0,0,3633) rot=(0,0,1;0rad)
  PredefinedType = 0
  VerticalArea = 12606000
  Width = 150
FEATURE [Part::FeaturePython] Wall147  label="шпренгель 001"  # Arch/BIM 166 (typed FeaturePython)
  Additions = -> [Wall146]
  Align = 2
  Area = 75000
  Base = -> Line1228
  BlockHeight = 0
  BlockLength = 0
  CountBroken = 0
  CountEntire = 0
  Face = 0
  Height = 500
  HorizontalArea = 295000
  IfcType = 166
  Joint = 0
  Length = 150
  MakeBlocks = false
  MoveBase = false
  MoveWithHost = false
  Normal = (0,0,0)
  OffsetFirst = 0
  OffsetSecond = 0
  PerimeterLength = 500
  Placement = pos=(0,0,3260) rot=(0,0,1;0rad)
  PredefinedType = 0
  Subtractions = -> [Wall057]
  VerticalArea = 1120000
  Width = 100
FEATURE [Part::FeaturePython] Wall150  label="шпренгель 010"  # Arch/BIM 166 (typed FeaturePython)
  Additions = -> [Wall149]
  Align = 2
  Area = 75000
  Base = -> Line1229
  BlockHeight = 0
  BlockLength = 0
  CountBroken = 0
  CountEntire = 0
  Face = 0
  Height = 500
  HorizontalArea = 280000
  IfcType = 166
  Joint = 0
  Length = 150
  MakeBlocks = false
  MoveBase = false
  MoveWithHost = false
  Normal = (0,0,0)
  OffsetFirst = 0
  OffsetSecond = 0
  PerimeterLength = 500
  Placement = pos=(0,0,3260) rot=(0,0,1;0rad)
  PredefinedType = 0
  Subtractions = -> [Wall057]
  VerticalArea = 1.07e+06
  Width = 100
FEATURE [Part::FeaturePython] Wall153  label="шпренгель 011"  # Arch/BIM 166 (typed FeaturePython)
  Additions = -> [Wall152]
  Align = 2
  Area = 75000
  Base = -> Line1231
  BlockHeight = 0
  BlockLength = 0
  CountBroken = 0
  CountEntire = 0
  Face = 0
  Height = 500
  HorizontalArea = 280000
  IfcType = 166
  Joint = 0
  Length = 150
  MakeBlocks = false
  MoveBase = false
  MoveWithHost = false
  Normal = (0,0,0)
  OffsetFirst = 0
  OffsetSecond = 0
  PerimeterLength = 500
  Placement = pos=(0,0,3260) rot=(0,0,1;0rad)
  PredefinedType = 0
  Subtractions = -> [Wall057]
  VerticalArea = 1070000
  Width = 100
FEATURE [Part::FeaturePython] Wall156  label="шпренгель 012"  # Arch/BIM 166 (typed FeaturePython)
  Additions = -> [Wall155]
  Align = 2
  Area = 75000
  Base = -> Line1233
  BlockHeight = 0
  BlockLength = 0
  CountBroken = 0
  CountEntire = 0
  Face = 0
  Height = 500
  HorizontalArea = 280000
  IfcType = 166
  Joint = 0
  Length = 150
  MakeBlocks = false
  MoveBase = false
  MoveWithHost = false
  Normal = (0,0,0)
  OffsetFirst = 0
  OffsetSecond = 0
  PerimeterLength = 500
  Placement = pos=(0,0,3260) rot=(0,0,1;0rad)
  PredefinedType = 0
  Subtractions = -> [Wall057]
  VerticalArea = 1.07e+06
  Width = 100
FEATURE [App::GeometryPython] BuildingPart044  label="Шпренгельные стойки"  # Arch/BIM 52 (typed FeaturePython)
  Area = 300000
  Group = -> [Wall147,Wall153,Wall156,Wall150]
  Height = 0
  HeightPropagate = true
  IfcData = complex_attributes={"OwnerHistory": {}, "IsNestedBy": {}, "IsDecomposedBy": {}, "IsDefinedBy": {}, "ObjectPlacement": {}, "Representation":... (+4 chars omitted)
  IfcType = 52
  LevelOffset = 0
FEATURE [App::MaterialObjectPython] Material001  label="Concrete"  # material (typed FeaturePython)
  Description = A standard C-25 construction concrete
  Material = AuthorAndLicense=Concrete-Generic,CardName=Concrete-Generic,Color=(0.47058823529411764, 0.4627450980392157, 0.4627450980392157, 1.0),+13 more (map truncated)
  ProductURL = https://en.wikipedia.org/wiki/Concrete
  StandardCode = Masterformat 03 33 13
  Transparency = 50
FEATURE [Part::FeaturePython] Structure030  label="блок утеплителя 60*10*20 001"  # Arch/BIM 7 (typed FeaturePython)
  FaceMaker = 0
  Height = 200
  HorizontalArea = 60000
  IfcType = 7
  Length = 600
  Material = -> Material001
  MoveBase = false
  MoveWithHost = false
  Nodes = (2) [(0,0,-3.88578e-16),(0,0,600)]
  NodesOffset = 0
  Normal = (0,0,0)
  PerimeterLength = 1400
  Placement = pos=(-175,9700,-280) rot=(0,0,1;0rad)
  PredefinedType = 0
  VerticalArea = 280000
  Width = 100
FEATURE [Part::FeaturePython] Array  label="массив утепления 001"  # Draft array (typed FeaturePython)
  Angle = 360
  ArrayType = 0
  Axis = (0,0,1)
  Base = -> Structure030
  Center = (0,0,0)
  Fuse = false
  IntervalAxis = (0,0,0)
  IntervalX = (765,0,0)
  IntervalY = (0,1,0)
  IntervalZ = (0,0,1)
  NumberPolar = 1
  NumberX = 18
  NumberY = 1
  NumberZ = 1
FEATURE [Part::FeaturePython] Structure031  label="блок утеплителя 60*10*20 002"  # Arch/BIM 7 (typed FeaturePython)
  FaceMaker = 0
  Height = 200
  HorizontalArea = 60000
  IfcType = 7
  Length = 600
  Material = -> Material001
  MoveBase = false
  MoveWithHost = false
  Nodes = (2) [(0,0,-3.88578e-16),(0,0,600)]
  NodesOffset = 0
  Normal = (0,0,0)
  PerimeterLength = 1400
  Placement = pos=(-180,-90,-280) rot=(0,0,1;0rad)
  PredefinedType = 0
  VerticalArea = 280000
  Width = 100
FEATURE [Part::FeaturePython] Array010  label="массив утепления 010"  # Draft array (typed FeaturePython)
  Angle = 360
  ArrayType = 0
  Axis = (0,0,1)
  Base = -> Structure031
  Center = (0,0,0)
  Fuse = false
  IntervalAxis = (0,0,0)
  IntervalX = (765,0,0)
  IntervalY = (0,1,0)
  IntervalZ = (0,0,1)
  NumberPolar = 1
  NumberX = 18
  NumberY = 1
  NumberZ = 1
FEATURE [Part::FeaturePython] Structure032  label="блок утеплителя 60*10*20 003"  # Arch/BIM 7 (typed FeaturePython)
  FaceMaker = 0
  Height = 200
  HorizontalArea = 60000
  IfcType = 7
  Length = 100
  Material = -> Material001
  MoveBase = false
  MoveWithHost = false
  Nodes = (2) [(-1.94289e-16,5.68434e-15,0),(-1.94289e-16,5.68434e-15,200)]
  NodesOffset = 0
  Normal = (0,0,0)
  PerimeterLength = 1400
  Placement = pos=(-350,375,-380) rot=(0,0,1;0rad)
  PredefinedType = 0
  VerticalArea = 280000
  Width = 600
FEATURE [Part::FeaturePython] Array011  label="массив утепления 011"  # Draft array (typed FeaturePython)
  Angle = 360
  ArrayType = 0
  Axis = (0,0,1)
  Base = -> Structure032
  Center = (0,0,0)
  Fuse = false
  IntervalAxis = (0,0,0)
  IntervalX = (0,0,0)
  IntervalY = (0,740,0)
  IntervalZ = (0,0,1)
  NumberPolar = 1
  NumberX = 1
  NumberY = 13
  NumberZ = 1
FEATURE [Part::FeaturePython] Structure033  label="блок утеплителя 60*10*20 004"  # Arch/BIM 7 (typed FeaturePython)
  FaceMaker = 0
  Height = 200
  HorizontalArea = 60000
  IfcType = 7
  Length = 100
  Material = -> Material001
  MoveBase = false
  MoveWithHost = false
  Nodes = (2) [(-1.94289e-16,5.68434e-15,0),(-1.94289e-16,5.68434e-15,200)]
  NodesOffset = 0
  Normal = (0,0,0)
  PerimeterLength = 1400
  Placement = pos=(13600,375,-380) rot=(0,0,1;0rad)
  PredefinedType = 0
  VerticalArea = 280000
  Width = 600
FEATURE [Part::FeaturePython] Array012  label="массив утепления 012"  # Draft array (typed FeaturePython)
  Angle = 360
  ArrayType = 0
  Axis = (0,0,1)
  Base = -> Structure033
  Center = (0,0,0)
  Fuse = false
  IntervalAxis = (0,0,0)
  IntervalX = (0,0,0)
  IntervalY = (0,740,0)
  IntervalZ = (0,0,1)
  NumberPolar = 1
  NumberX = 1
  NumberY = 13
  NumberZ = 1
FEATURE [App::GeometryPython] BuildingPart013  label="Утеплитель полки облицовки"  # Arch/BIM 52 (typed FeaturePython)
  Area = 0
  Group = -> [Array,Array010,Array011,Array012]
  Height = 0
  HeightPropagate = true
  IfcData = complex_attributes={"OwnerHistory": {}, "IsNestedBy": {}, "IsDecomposedBy": {}, "IsDefinedBy": {}, "ObjectPlacement": {}, "Representation":... (+4 chars omitted)
  IfcType = 52
  LevelOffset = 0
FEATURE [Part::FeaturePython] Structure047  label="Плоскость стропила"  # Arch/BIM 7 (typed FeaturePython)
  FaceMaker = 0
  Height = 5000
  HorizontalArea = 600000
  IfcType = 7
  Length = 12000
  Material = -> Material001
  MoveBase = false
  MoveWithHost = false
  Nodes = (2) [(0,1.81899e-16,-8.88178e-15),(0,1.81899e-16,14000)]
  NodesOffset = 0
  Normal = (0,0,0)
  PerimeterLength = 24100
  Placement = pos=(25,-2493.54,4500) rot=(0,0,1;1.5708rad)
  PredefinedType = 0
  VerticalArea = 120500000
  Width = 50
FEATURE [Part::FeaturePython] Structure052  label="Плоскость стропила001"  # Arch/BIM 7 (typed FeaturePython)
  FaceMaker = 0
  Height = 5000
  HorizontalArea = 850000
  IfcType = 7
  Length = 17000
  Material = -> Material001
  MoveBase = false
  MoveWithHost = false
  Nodes = (2) [(0,1.81899e-16,-8.88178e-15),(0,1.81899e-16,17000)]
  NodesOffset = 0
  Normal = (0,0,0)
  PerimeterLength = 34100
  Placement = pos=(-2000,25,4500) rot=(0,0,1;0rad)
  PredefinedType = 0
  VerticalArea = 170500000
  Width = 50
FEATURE [Part::FeaturePython] Array013  # Draft array (typed FeaturePython)
  Angle = 360
  ArrayType = 0
  Axis = (0,0,1)
  Base = -> Structure047
  Center = (0,0,0)
  Fuse = false
  IntervalAxis = (0,0,0)
  IntervalX = (630,0,0)
  IntervalY = (0,1,0)
  IntervalZ = (0,0,1)
  NumberPolar = 1
  NumberX = 22
  NumberY = 1
  NumberZ = 1
  Placement = pos=(-380,-5.457e-12,0) rot=(0,0,1;0rad)
FEATURE [Part::FeaturePython] Array014  # Draft array (typed FeaturePython)
  Angle = 360
  ArrayType = 0
  Axis = (0,0,1)
  Base = -> Structure052
  Center = (0,0,0)
  Fuse = false
  IntervalAxis = (0,0,0)
  IntervalX = (1,0,0)
  IntervalY = (0,625,0)
  IntervalZ = (0,0,1)
  NumberPolar = 1
  NumberX = 1
  NumberY = 14
  NumberZ = 1
  Placement = pos=(0,-360,0) rot=(0,0,1;0rad)
FEATURE [Part::MultiCommon] Common023  label="Стропилка_002"
  Shapes = -> [Array013,Common022]
FEATURE [Part::MultiCommon] Common025  label="Стропилка_003"
  Shapes = -> [Common024,Array014]
FEATURE [Part::MultiCommon] Common027  label="Стропилка_004"
  Shapes = -> [Common026,Array014]
FEATURE [Part::MultiCommon] Common029  label="Стойки 001"
  Shapes = -> [Cut,Array013]
FEATURE [Part::MultiCommon] Common030  label="Стойки 002"
  Shapes = -> [Cut,Array014]
FEATURE [Part::Cut] Cut024
  Base = -> Common023
  Tool = -> Wall145
FEATURE [Part::Cut] Cut025  label="Стропила 002"
  Base = -> Cut024
  Tool = -> Wall057
FEATURE [Part::Cut] Cut026
  Base = -> Common025
  Tool = -> Wall145
FEATURE [Part::Cut] Cut027  label="Стропила 003"
  Base = -> Cut026
  Tool = -> Wall057
FEATURE [Part::Cut] Cut028
  Base = -> Common027
  Tool = -> Wall145
FEATURE [Part::Cut] Cut029  label="Стропила 004"
  Base = -> Cut028
  Tool = -> Wall057
FEATURE [Part::FeaturePython] Wall176  label="фундамент МЗЛФ"  # Arch/BIM 166 (typed FeaturePython)
  Additions = -> [Wall130,Wall175,Wall038,Wall184]
  Align = 0
  Area = 8884000
  Base = -> Rectangle
  BlockHeight = 0
  BlockLength = 0
  CountBroken = 0
  CountEntire = 0
  Face = 0
  Height = 200
  HorizontalArea = 0
  IfcType = 166
  Joint = 0
  Length = 44420
  MakeBlocks = false
  MoveBase = false
  MoveWithHost = false
  Normal = (0,0,-1)
  OffsetFirst = 0
  OffsetSecond = 0
  PerimeterLength = 0
  Placement = pos=(0,0,-180) rot=(0,0,1;0rad)
  PredefinedType = 0
  Subtractions = -> [Array,Array010,Array011,Array012]
  VerticalArea = 0
  Width = 520
FEATURE [App::GeometryPython] BuildingPart012  label="Фундамент МЗЛФ в сборе"  # Arch/BIM 52 (typed FeaturePython)
  Area = 51616000
  Group = -> [Wall046,Wall047,BuildingPart013,Wall163,Wall176]
  Height = 0
  HeightPropagate = true
  IfcData = complex_attributes={"OwnerHistory": {}, "IsNestedBy": {}, "IsDecomposedBy": {}, "IsDefinedBy": {}, "ObjectPlacement": {}, "Representation":... (+4 chars omitted)
  IfcType = 52
  LevelOffset = 0
FEATURE [App::GeometryPython] BuildingPart010  label="Фундамент и основание"  # Arch/BIM 14 (typed FeaturePython)
  Area = 51616000
  CompositionType = 0
  Elevation = 0
  Group = -> [BuildingPart012]
  Height = 0
  HeightPropagate = true
  IfcData = attributes={"Elevation": {"value": 0.0}}
  IfcType = 14
  LevelOffset = 0
  LongName = Фундамент и основание
  expr: Elevation = .Placement.Base.z
FEATURE [Part::MultiCommon] Common031  label="Кобылки 001"
  Placement = pos=(50,0,0) rot=(0,0,1;0rad)
  Shapes = -> [Roof014,Array013]
FEATURE [Part::MultiCommon] Common032  label="Кобылки 002"
  Placement = pos=(0,50,0) rot=(0,0,1;0rad)
  Shapes = -> [Roof014,Array014]
FEATURE [Part::Cut] Cut035  label="Стропила 003_001"
  Base = -> Cut027
  Tool = -> Structure155
FEATURE [App::GeometryPython] BuildingPart018  label="Стропильная система"  # Arch/BIM 52 (typed FeaturePython)
  Area = 3.746e+06
  Group = -> [BuildingPart044,Common028,Wall064,Common029,Common030,Cut025,Cut029,Wall145,Common031,Common032,Cut035]
  Height = 0
  HeightPropagate = true
  IfcData = complex_attributes={"OwnerHistory": {}, "IsNestedBy": {}, "IsDecomposedBy": {}, "IsDefinedBy": {}, "ObjectPlacement": {}, "Representation":... (+4 chars omitted)
  IfcType = 52
  LevelOffset = 0
FEATURE [Part::FeaturePython] Structure368  label="Стяжка тёплого пола  80 мм 001"  # Arch/BIM 52 (typed FeaturePython)
  Base = -> Rectangle2169
  FaceMaker = 0
  GlobalId = 22FHYXjNfD0ge3TUS_JU1i
  Height = 80
  HorizontalArea = 430500
  IfcData = IfcUID=22FHYXjNfD0ge3TUS_JU1i,attributes={"GlobalId": {"value": "22FHYXjNfD0ge3TUS_JU1i"}},+1 more (map truncated)
  IfcType = 52
  Length = 0
  Material = -> Material001
  MoveBase = false
  MoveWithHost = false
  Nodes = (2) [(6195,-230,0),(6195,-230,80)]
  NodesOffset = 0
  Normal = (0,0,1)
  PerimeterLength = 2920
  Placement = pos=(0,0,-100) rot=(0,0,1;0rad)
  VerticalArea = 233600
  Width = 100
FEATURE [Part::FeaturePython] Structure371  label="Стяжка тёплого пола  80 мм 008"  # Arch/BIM 52 (typed FeaturePython)
  Base = -> Rectangle3079
  FaceMaker = 0
  GlobalId = 1aGZ9vCCD9wP_BshGDICol
  Height = 80
  HorizontalArea = 803600
  IfcData = IfcUID=1aGZ9vCCD9wP_BshGDICol,attributes={"GlobalId": {"value": "1aGZ9vCCD9wP_BshGDICol"}},+1 more (map truncated)
  IfcType = 52
  Length = 0
  Material = -> Material001
  MoveBase = false
  MoveWithHost = false
  Nodes = (2) [(4000,4250,0),(4000,4250,100)]
  NodesOffset = 0
  Normal = (0,0,1)
  PerimeterLength = 4740
  Placement = pos=(0,0,-100) rot=(0,0,1;0rad)
  VerticalArea = 379200
  Width = 100
FEATURE [Part::FeaturePython] Structure374  label="покрытие пола 20мм 001"  # Arch/BIM 52 (typed FeaturePython)
  Base = -> Rectangle2169
  FaceMaker = 0
  GlobalId = 2zjFlxA7P7zeUfdNFV2euI
  Height = 20
  HorizontalArea = 430500
  IfcData = IfcUID=2zjFlxA7P7zeUfdNFV2euI,attributes={"GlobalId": {"value": "2zjFlxA7P7zeUfdNFV2euI"}},+1 more (map truncated)
  IfcType = 52
  Length = 0
  Material = -> Material001
  MoveBase = false
  MoveWithHost = false
  Nodes = (2) [(6195,-230,0),(6195,-230,20)]
  NodesOffset = 0
  Normal = (0,0,1)
  PerimeterLength = 2920
  Placement = pos=(0,0,-20) rot=(0,0,1;0rad)
  VerticalArea = 58400
  Width = 20
FEATURE [Part::FeaturePython] Structure377  label="покрытие пола 20мм 003"  # Arch/BIM 52 (typed FeaturePython)
  Base = -> Rectangle3079
  FaceMaker = 0
  GlobalId = 2T3KnpypPEbv6OyL_zSjC5
  Height = 20
  HorizontalArea = 803600
  IfcData = IfcUID=2T3KnpypPEbv6OyL_zSjC5,attributes={"GlobalId": {"value": "2T3KnpypPEbv6OyL_zSjC5"}},+1 more (map truncated)
  IfcType = 52
  Length = 0
  Material = -> Material001
  MoveBase = false
  MoveWithHost = false
  Nodes = (2) [(4000,4250,0),(4000,4250,100)]
  NodesOffset = 0
  Normal = (0,0,1)
  PerimeterLength = 4740
  Placement = pos=(0,0,-20) rot=(0,0,1;0rad)
  VerticalArea = 94800
  Width = 20
FEATURE [App::MaterialObjectPython] Material002  label="XPS"  # material (typed FeaturePython)
  Description = XPS
  Material = AuthorAndLicense=ABS-Generic,CardName=ABS-Generic,Color=(0.9411764705882353, 0.5450980392156862, 0.5686274509803921, 1.0),Density=1060 kg/m^3,+15 more (map truncated)
  Transparency = 0
FEATURE [Part::FeaturePython] Structure066  label="утепление пола в проёмах XPS 100mm 001"  # Arch/BIM 52 (typed FeaturePython)
  Base = -> Rectangle3079
  FaceMaker = 0
  GlobalId = 3EKnpUeW1ADw6RKJbe9Fmo
  Height = 100
  HorizontalArea = 803600
  IfcData = IfcUID=3EKnpUeW1ADw6RKJbe9Fmo,attributes={"GlobalId": {"value": "3EKnpUeW1ADw6RKJbe9Fmo"}},+1 more (map truncated)
  IfcType = 52
  Length = 0
  Material = -> Material002
  MoveBase = false
  MoveWithHost = false
  Nodes = (2) [(4000,4250,0),(4000,4250,100)]
  NodesOffset = 0
  Normal = (0,0,1)
  PerimeterLength = 4740
  Placement = pos=(0,0,-200) rot=(0,0,1;0rad)
  VerticalArea = 474000
  Width = 100
FEATURE [Part::FeaturePython] Structure069  label="утепление пола в проёмах XPS 100mm 002"  # Arch/BIM 52 (typed FeaturePython)
  Base = -> Rectangle2169
  FaceMaker = 0
  GlobalId = 3Shc3AjDz99AkEi1PjraMs
  Height = 100
  HorizontalArea = 430500
  IfcData = IfcUID=3Shc3AjDz99AkEi1PjraMs,attributes={"GlobalId": {"value": "3Shc3AjDz99AkEi1PjraMs"}},+1 more (map truncated)
  IfcType = 52
  Length = 0
  Material = -> Material002
  MoveBase = false
  MoveWithHost = false
  Nodes = (2) [(6195,-230,0),(6195,-230,100)]
  NodesOffset = 0
  Normal = (0,0,1)
  PerimeterLength = 2920
  Placement = pos=(0,0,-200) rot=(0,0,1;0rad)
  VerticalArea = 292000
  Width = 100
FEATURE [Part::FeaturePython] Wall249  label="XPS 80mm в уровне армпояса"  # Arch/BIM 166 (typed FeaturePython)
  Align = 0
  Area = 5647600
  Base = -> Rectangle016
  BlockHeight = 231
  BlockLength = 1200
  CountBroken = 33
  CountEntire = 0
  Face = 0
  GlobalId = 0S$ta$Atf7kQfUAIRZ7neI
  Height = 140
  HorizontalArea = 0
  IfcData = IfcUID=0S$ta$Atf7kQfUAIRZ7neI; attributes={"GlobalId": {"value": "0S$ta$Atf7kQfUAIRZ7neI"}}
  IfcType = 166
  Joint = 0
  Length = 40340
  MakeBlocks = true
  Material = -> Material002
  MoveBase = false
  MoveWithHost = false
  Normal = (0,0,1)
  Offset = 300
  OffsetFirst = 0
  OffsetSecond = 0
  PerimeterLength = 0
  Placement = pos=(0,0,3493) rot=(0,0,1;0rad)
  PredefinedType = 0
  VerticalArea = 0
  Width = 80
FEATURE [Part::FeaturePython] Wall259  label="Утепление торца плит XPS 80mm 002"  # Arch/BIM 166 (typed FeaturePython)
  Align = 0
  Area = 2915220
  Base = -> Line1430
  BlockHeight = 231
  BlockLength = 1200
  CountBroken = 1
  CountEntire = 10
  Face = 0
  GlobalId = 1ibByTMrr7TuIBXHnohxoK
  Height = 231
  HorizontalArea = 0
  IfcData = IfcUID=1ibByTMrr7TuIBXHnohxoK,+2 more (map truncated)
  IfcType = 166
  Joint = 0
  Length = 12620
  MakeBlocks = true
  Material = -> Material002
  MoveBase = false
  MoveWithHost = false
  Normal = (0,0,0)
  OffsetFirst = 0
  OffsetSecond = 0
  PerimeterLength = 0
  Placement = pos=(5.68e-14,0,2800) rot=(0,0,1;0rad)
  PredefinedType = 0
  VerticalArea = 0
  Width = 80
FEATURE [Part::FeaturePython] Wall260  label="Утепление торца плит XPS 80mm 001"  # Arch/BIM 166 (typed FeaturePython)
  Align = 0
  Area = 2915220
  Base = -> Line1431
  BlockHeight = 231
  BlockLength = 1200
  CountBroken = 1
  CountEntire = 10
  Face = 0
  GlobalId = 1LI82ViEn62R_6CNpLHhhT
  Height = 231
  HorizontalArea = 0
  IfcData = IfcUID=1LI82ViEn62R_6CNpLHhhT,+2 more (map truncated)
  IfcType = 166
  Joint = 0
  Length = 12620
  MakeBlocks = true
  Material = -> Material002
  MoveBase = false
  MoveWithHost = false
  Normal = (0,0,0)
  OffsetFirst = 0
  OffsetSecond = 0
  PerimeterLength = 0
  Placement = pos=(5.68e-14,0,2800) rot=(0,0,1;0rad)
  PredefinedType = 0
  VerticalArea = 0
  Width = 80
FEATURE [App::MaterialObjectPython] Material003  label="Red brick"  # material (typed FeaturePython)
  Description = A standard red brick
  Material = AuthorAndLicense=Concrete-Generic,CardName=Concrete-Generic,Color=(0.788235294117647, 0.2980392156862745, 0.18823529411764706, 1.0),+11 more (map truncated)
  Transparency = 0
FEATURE [Part::FeaturePython] Wall120  label="Перемычка облицовки 014"  # Arch/BIM 166 (typed FeaturePython)
  Align = 2
  Area = 1379700
  Base = -> Line1187
  BlockHeight = 250
  BlockLength = 64.2
  CountBroken = 53
  CountEntire = 49
  Face = 0
  GlobalId = 2CDkG$u1H6yg879o_wXiaT
  Height = 365
  HorizontalArea = 0
  IfcData = IfcUID=2CDkG$u1H6yg879o_wXiaT; attributes={"GlobalId": {"value": "2CDkG$u1H6yg879o_wXiaT"}}
  IfcType = 166
  Joint = 10
  Length = 3780
  MakeBlocks = true
  Material = -> Material003
  MoveBase = false
  MoveWithHost = false
  Normal = (0,0,1)
  OffsetFirst = 0
  OffsetSecond = 0
  PerimeterLength = 0
  Placement = pos=(0,0,2510) rot=(0,0,1;0rad)
  PredefinedType = 0
  VerticalArea = 0
  Width = 10
FEATURE [Part::FeaturePython] Wall121  label="Перемычка облицовки 015"  # Arch/BIM 166 (typed FeaturePython)
  Align = 2
  Area = 1522050
  Base = -> Line1186
  BlockHeight = 250
  BlockLength = 65.8
  CountBroken = 57
  CountEntire = 53
  Face = 0
  GlobalId = 3Y7MnwAmX628ZvBXKl4dyB
  Height = 365
  HorizontalArea = 0
  IfcData = IfcUID=3Y7MnwAmX628ZvBXKl4dyB; attributes={"GlobalId": {"value": "3Y7MnwAmX628ZvBXKl4dyB"}}
  IfcType = 166
  Joint = 10
  Length = 4170
  MakeBlocks = true
  Material = -> Material003
  MoveBase = false
  MoveWithHost = false
  Normal = (0,0,1)
  OffsetFirst = 0
  OffsetSecond = 0
  PerimeterLength = 0
  Placement = pos=(0,0,2510) rot=(0,0,1;0rad)
  PredefinedType = 0
  VerticalArea = 0
  Width = 10
FEATURE [Part::FeaturePython] Wall123  label="Перемычка облицовки 017"  # Arch/BIM 166 (typed FeaturePython)
  Align = 2
  Area = 288350
  Base = -> Line1184
  BlockHeight = 250
  BlockLength = 68
  CountBroken = 12
  CountEntire = 8
  Face = 0
  GlobalId = 3lCsDqyJL5KvboFIYAEUQo
  Height = 365
  HorizontalArea = 0
  IfcData = IfcUID=3lCsDqyJL5KvboFIYAEUQo; attributes={"GlobalId": {"value": "3lCsDqyJL5KvboFIYAEUQo"}}
  IfcType = 166
  Joint = 10
  Length = 790
  MakeBlocks = true
  Material = -> Material003
  MoveBase = false
  MoveWithHost = false
  Normal = (0,0,1)
  OffsetFirst = 0
  OffsetSecond = 0
  PerimeterLength = 0
  Placement = pos=(0,0,2285) rot=(0,0,1;0rad)
  PredefinedType = 0
  VerticalArea = 0
  Width = 10
FEATURE [Part::FeaturePython] Wall124  label="Перемычка облицовки 018"  # Arch/BIM 166 (typed FeaturePython)
  Align = 2
  Area = 288350
  Base = -> Line1191
  BlockHeight = 250
  BlockLength = 68
  CountBroken = 12
  CountEntire = 8
  Face = 0
  GlobalId = 07ToIk0b17KwOPIvB7CAEx
  Height = 365
  HorizontalArea = 0
  IfcData = IfcUID=07ToIk0b17KwOPIvB7CAEx; attributes={"GlobalId": {"value": "07ToIk0b17KwOPIvB7CAEx"}}
  IfcType = 166
  Joint = 10
  Length = 790
  MakeBlocks = true
  Material = -> Material003
  MoveBase = false
  MoveWithHost = false
  Normal = (0,0,1)
  OffsetFirst = 0
  OffsetSecond = 0
  PerimeterLength = 0
  Placement = pos=(0,0,2285) rot=(0,0,1;0rad)
  PredefinedType = 0
  VerticalArea = 0
  Width = 10
FEATURE [Part::FeaturePython] Wall159  label="Перемычка облицовки 019"  # Arch/BIM 166 (typed FeaturePython)
  Align = 2
  Area = 573050
  Base = -> Line1266
  BlockHeight = 250
  BlockLength = 65
  CountBroken = 23
  CountEntire = 19
  Face = 0
  GlobalId = 0T7dyAI05B38PZhXyjg8rR
  Height = 365
  HorizontalArea = 0
  IfcData = IfcUID=0T7dyAI05B38PZhXyjg8rR; attributes={"GlobalId": {"value": "0T7dyAI05B38PZhXyjg8rR"}}
  IfcType = 166
  Joint = 10
  Length = 1570
  MakeBlocks = true
  Material = -> Material003
  MoveBase = false
  MoveWithHost = false
  Normal = (0,0,1)
  OffsetFirst = 0
  OffsetSecond = 0
  PerimeterLength = 0
  Placement = pos=(0,0,2510) rot=(0,0,1;0rad)
  PredefinedType = 0
  VerticalArea = 0
  Width = 10
FEATURE [App::GeometryPython] BuildingPart038  label="Перемычки облицовки 1nf"  # Arch/BIM 52 (typed FeaturePython)
  Area = 4.0515e+06
  GlobalId = 0KtQz4WtXFJO7H9uDU_qkV
  Group = -> [Wall120,Wall121,Wall123,Wall124,Wall159]
  Height = 0
  HeightPropagate = true
  IfcData = IfcUID=0KtQz4WtXFJO7H9uDU_qkV,attributes={"GlobalId": {"value": "0KtQz4WtXFJO7H9uDU_qkV"}},+1 more (map truncated)
  IfcType = 52
  LevelOffset = 0
FEATURE [Part::FeaturePython] Wall215  label="Ряд 1нф по плитам ПНО 001"  # Arch/BIM 166 (typed FeaturePython)
  Align = 0
  Area = 820300
  Base = -> Line1430
  BlockHeight = 65
  BlockLength = 260
  CountBroken = 2
  CountEntire = 48
  Face = 0
  GlobalId = 0Kxc8b9mX0hhA4A11jgaug
  Height = 65
  HorizontalArea = 0
  IfcData = IfcUID=0Kxc8b9mX0hhA4A11jgaug,+2 more (map truncated)
  IfcType = 166
  Joint = 0
  Length = 12620
  MakeBlocks = true
  Material = -> Material003
  MoveBase = false
  MoveWithHost = false
  Normal = (0,0,0)
  Offset = 210
  OffsetFirst = 120
  OffsetSecond = 0
  PerimeterLength = 0
  Placement = pos=(0,0,2963) rot=(0,0,1;0rad)
  PredefinedType = 0
  VerticalArea = 0
  Width = 170
FEATURE [Part::FeaturePython] Wall245  label="Стена 3 ряда 1NF в уровне перекрытия 001"  # Arch/BIM 166 (typed FeaturePython)
  Align = 0
  Area = 2915220
  Base = -> Line1430
  BlockHeight = 65
  BlockLength = 250
  CountBroken = 6
  CountEntire = 141
  Face = 0
  GlobalId = 3KlxKDIJjA7Q82FRbrh_9n
  Height = 231
  HorizontalArea = 0
  IfcData = IfcUID=3KlxKDIJjA7Q82FRbrh_9n,+2 more (map truncated)
  IfcType = 166
  Joint = 12
  Length = 12620
  MakeBlocks = true
  Material = -> Material003
  MoveBase = false
  MoveWithHost = false
  Normal = (0,0,0)
  Offset = 85
  OffsetFirst = 65
  OffsetSecond = 200
  PerimeterLength = 0
  Placement = pos=(5.68e-14,0,2805) rot=(0,0,1;0rad)
  PredefinedType = 0
  VerticalArea = 0
  Width = 120
FEATURE [Part::FeaturePython] Wall246  label="Стена 3 ряда 1NF в уровне перекрытия 002"  # Arch/BIM 166 (typed FeaturePython)
  Align = 0
  Area = 2915220
  Base = -> Line1431
  BlockHeight = 65
  BlockLength = 250
  CountBroken = 6
  CountEntire = 141
  Face = 0
  GlobalId = 2jFZMiwejFCvBCF1MAHti2
  Height = 231
  HorizontalArea = 0
  IfcData = IfcUID=2jFZMiwejFCvBCF1MAHti2,+2 more (map truncated)
  IfcType = 166
  Joint = 12
  Length = 12620
  MakeBlocks = true
  Material = -> Material003
  MoveBase = false
  MoveWithHost = false
  Normal = (0,0,0)
  Offset = 85
  OffsetFirst = 65
  OffsetSecond = 200
  PerimeterLength = 0
  Placement = pos=(5.68e-14,0,2805) rot=(0,0,1;0rad)
  PredefinedType = 0
  VerticalArea = 0
  Width = 120
FEATURE [Part::FeaturePython] Wall247  label="Ряд 1нф по плитам ПНО 002"  # Arch/BIM 166 (typed FeaturePython)
  Align = 0
  Area = 820300
  Base = -> Line1431
  BlockHeight = 65
  BlockLength = 260
  CountBroken = 2
  CountEntire = 48
  Face = 0
  GlobalId = 33o6NID0r8NOJAPg0rbzr4
  Height = 65
  HorizontalArea = 0
  IfcData = IfcUID=33o6NID0r8NOJAPg0rbzr4,+2 more (map truncated)
  IfcType = 166
  Joint = 0
  Length = 12620
  MakeBlocks = true
  Material = -> Material003
  MoveBase = false
  MoveWithHost = false
  Normal = (0,0,0)
  Offset = 210
  OffsetFirst = 120
  OffsetSecond = 0
  PerimeterLength = 0
  Placement = pos=(0,0,2963) rot=(0,0,1;0rad)
  PredefinedType = 0
  VerticalArea = 0
  Width = 170
FEATURE [Part::FeaturePython] Wall248  label="ряд  2.1нф в уровне армпояса"  # Arch/BIM 166 (typed FeaturePython)
  Align = 0
  Area = 5647600
  Base = -> Rectangle016
  BlockHeight = 140
  BlockLength = 260
  CountBroken = 4
  CountEntire = 149
  Face = 0
  GlobalId = 3OBRES97PB8f6_bWU2_YT7
  Height = 140
  HorizontalArea = 4898400
  IfcData = IfcUID=3OBRES97PB8f6_bWU2_YT7; attributes={"GlobalId": {"value": "3OBRES97PB8f6_bWU2_YT7"}}
  IfcType = 166
  Joint = 0
  Length = 40340
  MakeBlocks = false
  Material = -> Material003
  MoveBase = false
  MoveWithHost = false
  Normal = (0,0,1)
  OffsetFirst = 0
  OffsetSecond = 0
  PerimeterLength = 41300
  Placement = pos=(0,0,3493) rot=(0,0,1;0rad)
  PredefinedType = 0
  VerticalArea = 11429600
  Width = 120
FEATURE [Part::FeaturePython] Wall255  label="облицовка ВШ  001"  # Arch/BIM 166 (typed FeaturePython)
  Align = 0
  Area = 1520000
  Base = -> Line1468
  BlockHeight = 65
  BlockLength = 250
  CountBroken = 55
  CountEntire = 53
  Face = 0
  GlobalId = 0NV5Z8QsLE8RP4h00TMdTp
  Height = 4000
  HorizontalArea = 45600
  IfcData = IfcUID=0NV5Z8QsLE8RP4h00TMdTp; attributes={"GlobalId": {"value": "0NV5Z8QsLE8RP4h00TMdTp"}}
  IfcType = 166
  Joint = 10
  Length = 380
  MakeBlocks = false
  Material = -> Material003
  MoveBase = false
  MoveWithHost = false
  Normal = (0,0,0)
  OffsetFirst = 120
  OffsetSecond = 250
  PerimeterLength = 1000
  Placement = pos=(0,0,2960) rot=(0,0,1;0rad)
  PredefinedType = 0
  VerticalArea = 4000000
  Width = 120
FEATURE [Part::FeaturePython] Wall256  label="облицовка ВШ  002"  # Arch/BIM 166 (typed FeaturePython)
  Align = 0
  Area = 1520000
  Base = -> Line1469
  BlockHeight = 65
  BlockLength = 250
  CountBroken = 55
  CountEntire = 53
  Face = 0
  GlobalId = 2TkovYGMD8r9zraP45mHkR
  Height = 4000
  HorizontalArea = 45600
  IfcData = IfcUID=2TkovYGMD8r9zraP45mHkR; attributes={"GlobalId": {"value": "2TkovYGMD8r9zraP45mHkR"}}
  IfcType = 166
  Joint = 10
  Length = 380
  MakeBlocks = false
  Material = -> Material003
  MoveBase = false
  MoveWithHost = false
  Normal = (0,0,0)
  OffsetFirst = 120
  OffsetSecond = 250
  PerimeterLength = 1000
  Placement = pos=(0,0,2960) rot=(0,0,1;0rad)
  PredefinedType = 0
  VerticalArea = 4000000
  Width = 120
FEATURE [Part::FeaturePython] Wall257  label="облицовка ВШ  003"  # Arch/BIM 166 (typed FeaturePython)
  Align = 0
  Area = 3600000
  Base = -> Line1470
  BlockHeight = 65
  BlockLength = 250
  CountBroken = 57
  CountEntire = 159
  Face = 0
  GlobalId = 0woF2TLZD1r929WxYa3eSK
  Height = 4000
  HorizontalArea = 108000
  IfcData = IfcUID=0woF2TLZD1r929WxYa3eSK; attributes={"GlobalId": {"value": "0woF2TLZD1r929WxYa3eSK"}}
  IfcType = 166
  Joint = 10
  Length = 900
  MakeBlocks = false
  Material = -> Material003
  MoveBase = false
  MoveWithHost = false
  Normal = (0,0,0)
  OffsetFirst = 250
  OffsetSecond = 120
  PerimeterLength = 2040
  Placement = pos=(0,0,2960) rot=(0,0,1;0rad)
  PredefinedType = 0
  VerticalArea = 8.16e+06
  Width = 120
FEATURE [Part::FeaturePython] Wall258  label="облицовка ВШ  004"  # Arch/BIM 166 (typed FeaturePython)
  Align = 0
  Area = 3600000
  Base = -> Line1471
  BlockHeight = 65
  BlockLength = 250
  CountBroken = 57
  CountEntire = 159
  Face = 0
  GlobalId = 0uV1Y0I5TBPurrni9deYxv
  Height = 4000
  HorizontalArea = 108000
  IfcData = IfcUID=0uV1Y0I5TBPurrni9deYxv; attributes={"GlobalId": {"value": "0uV1Y0I5TBPurrni9deYxv"}}
  IfcType = 166
  Joint = 10
  Length = 900
  MakeBlocks = false
  Material = -> Material003
  MoveBase = false
  MoveWithHost = false
  Normal = (0,0,0)
  OffsetFirst = 250
  OffsetSecond = 120
  PerimeterLength = 2040
  Placement = pos=(0,0,2960) rot=(0,0,1;0rad)
  PredefinedType = 0
  VerticalArea = 8.16e+06
  Width = 120
FEATURE [App::MaterialObjectPython] Material004  label="Ceramic block"  # material (typed FeaturePython)
  Description = A standard Ceramic block LSR TK380
  Material = AuthorAndLicense=Concrete-Generic,CardName=Concrete-Generic,Color=(0.8627450980392157, 0.5803921568627451, 0.13725490196078433, 1.0),+11 more (map truncated)
  Transparency = 0
FEATURE [Part::FeaturePython] Wall164  label="Стена ЛСР 380мм под мауэрлат"  # Arch/BIM 166 (typed FeaturePython)
  Align = 0
  Area = 18637080
  Base = -> Rectangle016
  BlockHeight = 231
  BlockLength = 0
  CountBroken = 0
  CountEntire = 0
  Face = 0
  GlobalId = 3z2ptnFFLDUOlhnj0g0DYP
  Height = 462
  HorizontalArea = 31813600
  IfcData = IfcUID=3z2ptnFFLDUOlhnj0g0DYP; attributes={"GlobalId": {"value": "3z2ptnFFLDUOlhnj0g0DYP"}}
  IfcType = 166
  Joint = 0
  Length = 40340
  MakeBlocks = true
  Material = -> Material004
  MoveBase = false
  MoveWithHost = false
  Normal = (0,0,1)
  OffsetFirst = 0
  OffsetSecond = 0
  PerimeterLength = 0
  Placement = pos=(0,0,3031) rot=(0,0,1;0rad)
  PredefinedType = 0
  VerticalArea = 38678640
  Width = 380
FEATURE [Part::FeaturePython] Wall206  label="Стена021"  # Arch/BIM 166 (typed FeaturePython)
  Align = 0
  Area = 1831830
  Base = -> Line1343
  BlockHeight = 231
  BlockLength = 256
  CountBroken = 1
  CountEntire = 30
  Face = 0
  Height = 231
  HorizontalArea = 0
  IfcData = attributes={"GlobalId": {"name": "GlobalId", "type": "IfcGloballyUniqueId", "is_enum": false, "enum_values": []}, "Description": {"... (+533 chars omitted),+1 more (map truncated)
  IfcType = 166
  Joint = 0
  Length = 7930
  MakeBlocks = true
  Material = -> Material004
  MoveBase = false
  MoveWithHost = false
  Normal = (0,0,0)
  OffsetFirst = 0
  OffsetSecond = 0
  PerimeterLength = 0
  Placement = pos=(0,0,31) rot=(0,0,1;0rad)
  PredefinedType = 0
  VerticalArea = 0
  Width = 380
FEATURE [Part::FeaturePython] Wall207  label="Стена022"  # Arch/BIM 166 (typed FeaturePython)
  Align = 1
  Area = 1831830
  Base = -> Line1342
  BlockHeight = 231
  BlockLength = 256
  CountBroken = 1
  CountEntire = 30
  Face = 0
  Height = 231
  HorizontalArea = 0
  IfcData = attributes={"GlobalId": {"name": "GlobalId", "type": "IfcGloballyUniqueId", "is_enum": false, "enum_values": []}, "Description": {"... (+533 chars omitted),+1 more (map truncated)
  IfcType = 166
  Joint = 0
  Length = 7930
  MakeBlocks = true
  Material = -> Material004
  MoveBase = false
  MoveWithHost = false
  Normal = (0,0,0)
  OffsetFirst = 0
  OffsetSecond = 0
  PerimeterLength = 0
  Placement = pos=(0,0,-200) rot=(0,0,1;0rad)
  PredefinedType = 0
  VerticalArea = 0
  Width = 380
FEATURE [Part::FeaturePython] Wall208  label="Стена023"  # Arch/BIM 166 (typed FeaturePython)
  Align = 1
  Area = 3003000
  Base = -> Line1349
  BlockHeight = 231
  BlockLength = 255
  CountBroken = 3
  CountEntire = 41
  Face = 0
  Height = 231
  HorizontalArea = 0
  IfcData = attributes={"GlobalId": {"name": "GlobalId", "type": "IfcGloballyUniqueId", "is_enum": false, "enum_values": []}, "Description": {"... (+533 chars omitted),+1 more (map truncated)
  IfcType = 166
  Joint = 0
  Length = 13000
  MakeBlocks = true
  Material = -> Material004
  MoveBase = false
  MoveWithHost = false
  Normal = (0,0,0)
  OffsetFirst = 0
  OffsetSecond = 0
  PerimeterLength = 0
  Placement = pos=(0,0,-200) rot=(0,0,1;0rad)
  PredefinedType = 0
  Subtractions = -> [Structure308]
  VerticalArea = 0
  Width = 380
FEATURE [Part::FeaturePython] Wall209  label="Стена024"  # Arch/BIM 166 (typed FeaturePython)
  Align = 1
  Area = 3003000
  Base = -> Line1340
  BlockHeight = 231
  BlockLength = 255
  CountBroken = 3
  CountEntire = 44
  Face = 0
  Height = 231
  HorizontalArea = 0
  IfcData = attributes={"GlobalId": {"name": "GlobalId", "type": "IfcGloballyUniqueId", "is_enum": false, "enum_values": []}, "Description": {"... (+533 chars omitted),+1 more (map truncated)
  IfcType = 166
  Joint = 0
  Length = 13000
  MakeBlocks = true
  Material = -> Material004
  MoveBase = false
  MoveWithHost = false
  Normal = (0,0,0)
  OffsetFirst = 0
  OffsetSecond = 0
  PerimeterLength = 0
  Placement = pos=(0,0,-200) rot=(0,0,1;0rad)
  PredefinedType = 0
  Subtractions = -> [Structure019]
  VerticalArea = 0
  Width = 380
FEATURE [Part::FeaturePython] Wall210  label="Стена025"  # Arch/BIM 166 (typed FeaturePython)
  Align = 0
  Area = 3003000
  Base = -> Line1350
  BlockHeight = 231
  BlockLength = 255
  CountBroken = 3
  CountEntire = 41
  Face = 0
  Height = 231
  HorizontalArea = 0
  IfcData = attributes={"GlobalId": {"name": "GlobalId", "type": "IfcGloballyUniqueId", "is_enum": false, "enum_values": []}, "Description": {"... (+533 chars omitted),+1 more (map truncated)
  IfcType = 166
  Joint = 0
  Length = 13000
  MakeBlocks = true
  Material = -> Material004
  MoveBase = false
  MoveWithHost = false
  Normal = (0,0,0)
  OffsetFirst = 0
  OffsetSecond = 0
  PerimeterLength = 0
  Placement = pos=(0,0,31) rot=(0,0,1;0rad)
  PredefinedType = 0
  Subtractions = -> [Structure308]
  VerticalArea = 0
  Width = 380
FEATURE [Part::FeaturePython] Wall211  label="Стена026"  # Arch/BIM 166 (typed FeaturePython)
  Align = 0
  Area = 1.83183e+06
  Base = -> Line1347
  BlockHeight = 231
  BlockLength = 256
  CountBroken = 1
  CountEntire = 30
  Face = 0
  Height = 231
  HorizontalArea = 0
  IfcData = attributes={"GlobalId": {"name": "GlobalId", "type": "IfcGloballyUniqueId", "is_enum": false, "enum_values": []}, "Description": {"... (+533 chars omitted),+1 more (map truncated)
  IfcType = 166
  Joint = 0
  Length = 7930
  MakeBlocks = true
  Material = -> Material004
  MoveBase = false
  MoveWithHost = false
  Normal = (0,0,0)
  OffsetFirst = 0
  OffsetSecond = 0
  PerimeterLength = 0
  Placement = pos=(0,0,31) rot=(0,0,1;0rad)
  PredefinedType = 0
  VerticalArea = 0
  Width = 380
FEATURE [Part::FeaturePython] Wall212  label="Стена027"  # Arch/BIM 166 (typed FeaturePython)
  Align = 0
  Area = 3003000
  Base = -> Line1351
  BlockHeight = 231
  BlockLength = 255
  CountBroken = 3
  CountEntire = 45
  Face = 0
  Height = 231
  HorizontalArea = 0
  IfcData = attributes={"GlobalId": {"name": "GlobalId", "type": "IfcGloballyUniqueId", "is_enum": false, "enum_values": []}, "Description": {"... (+533 chars omitted),+1 more (map truncated)
  IfcType = 166
  Joint = 0
  Length = 13000
  MakeBlocks = true
  Material = -> Material004
  MoveBase = false
  MoveWithHost = false
  Normal = (0,0,0)
  OffsetFirst = 0
  OffsetSecond = 0
  PerimeterLength = 0
  Placement = pos=(0,0,31) rot=(0,0,1;0rad)
  PredefinedType = 0
  Subtractions = -> [Structure019]
  VerticalArea = 0
  Width = 380
FEATURE [App::GeometryPython] BuildingPart072  label="ряд 2"  # Arch/BIM 52 (typed FeaturePython)
  Area = 9669660
  Group = -> [Wall212,Wall210,Wall211,Wall206]
  Height = 0
  HeightPropagate = true
  IfcData = attributes={"GlobalId": {"name": "GlobalId", "type": "IfcGloballyUniqueId", "is_enum": false, "enum_values": []}, "Description": {"... (+484 chars omitted),+1 more (map truncated)
  IfcType = 52
  LevelOffset = 0
FEATURE [Part::FeaturePython] Wall213  label="Стена028"  # Arch/BIM 166 (typed FeaturePython)
  Align = 1
  Area = 1831830
  Base = -> Line1341
  BlockHeight = 231
  BlockLength = 256
  CountBroken = 1
  CountEntire = 30
  Face = 0
  Height = 231
  HorizontalArea = 0
  IfcData = attributes={"GlobalId": {"name": "GlobalId", "type": "IfcGloballyUniqueId", "is_enum": false, "enum_values": []}, "Description": {"... (+533 chars omitted),+1 more (map truncated)
  IfcType = 166
  Joint = 0
  Length = 7930
  MakeBlocks = true
  Material = -> Material004
  MoveBase = false
  MoveWithHost = false
  Normal = (0,0,0)
  OffsetFirst = 0
  OffsetSecond = 0
  PerimeterLength = 0
  Placement = pos=(0,0,-200) rot=(0,0,1;0rad)
  PredefinedType = 0
  VerticalArea = 0
  Width = 380
FEATURE [App::GeometryPython] BuildingPart077  label="ряд 1"  # Arch/BIM 52 (typed FeaturePython)
  Area = 9669660
  Group = -> [Wall209,Wall208,Wall213,Wall207]
  Height = 0
  HeightPropagate = true
  IfcData = attributes={"GlobalId": {"name": "GlobalId", "type": "IfcGloballyUniqueId", "is_enum": false, "enum_values": []}, "Description": {"... (+484 chars omitted),+1 more (map truncated)
  IfcType = 52
  LevelOffset = 0
FEATURE [Part::FeaturePython] Wall242  label="Стена ЛСР 380мм ряд перекрытия 001"  # Arch/BIM 166 (typed FeaturePython)
  Align = 0
  Area = 1919610
  Base = -> Line1426
  BlockHeight = 231
  BlockLength = 255
  CountBroken = 1
  CountEntire = 32
  Face = 0
  GlobalId = 0JF6Mj3WnAXwUaXoCorPV_
  Height = 231
  HorizontalArea = 3157800
  IfcData = IfcUID=0JF6Mj3WnAXwUaXoCorPV_,+2 more (map truncated)
  IfcType = 166
  Joint = 0
  Length = 8310
  MakeBlocks = false
  Material = -> Material004
  MoveBase = false
  MoveWithHost = false
  Normal = (0,0,0)
  OffsetFirst = 0
  OffsetSecond = 0
  PerimeterLength = 17380
  Placement = pos=(5.68e-14,0,2800) rot=(0,0,1;0rad)
  PredefinedType = 0
  VerticalArea = 4014780
  Width = 380
FEATURE [Part::FeaturePython] Wall243  label="Стена ЛСР 380мм ряд перекрытия 002"  # Arch/BIM 166 (typed FeaturePython)
  Align = 1
  Area = 1919610
  Base = -> Line1427
  BlockHeight = 231
  BlockLength = 255
  CountBroken = 1
  CountEntire = 32
  Face = 0
  GlobalId = 25wehzmoL6BRnSZJd_gcHH
  Height = 231
  HorizontalArea = 3157800
  IfcData = IfcUID=25wehzmoL6BRnSZJd_gcHH,+2 more (map truncated)
  IfcType = 166
  Joint = 0
  Length = 8310
  MakeBlocks = false
  Material = -> Material004
  MoveBase = false
  MoveWithHost = false
  Normal = (0,0,0)
  OffsetFirst = 120
  OffsetSecond = 0
  PerimeterLength = 17380
  Placement = pos=(5.68e-14,0,2800) rot=(0,0,1;0rad)
  PredefinedType = 0
  VerticalArea = 4014780
  Width = 380
FEATURE [App::GeometryPython] BuildingPart082  label="Кладка в уровне перекрытия"  # Arch/BIM 52 (typed FeaturePython)
  Area = 17140700
  GlobalId = 1YWPLHYQvChhSjPeXmlyje
  Group = -> [Wall247,Wall242,Wall243,Wall245,Wall246,Wall215,Wall259,Wall260]
  Height = 0
  HeightPropagate = true
  IfcData = IfcUID=1YWPLHYQvChhSjPeXmlyje,+2 more (map truncated)
  IfcType = 52
  LevelOffset = 0
FEATURE [App::MaterialObjectPython] Material005  label="Wall ceramic plates"  # material (typed FeaturePython)
  Description = Wall ceramic plates
  Material = AuthorAndLicense=Concrete-Generic,CardName=Concrete-Generic,Color=(0.1450980392156863, 0.4745098039215686, 0.6980392156862745, 1.0),+11 more (map truncated)
  Transparency = 0
FEATURE [Part::FeaturePython] Wall240  label="Облицовка ванны плиткой 30мм"  # Arch/BIM 166 (typed FeaturePython)
  Align = 0
  Area = 3112200
  Base = -> Wire808
  BlockHeight = 0
  BlockLength = 0
  CountBroken = 0
  CountEntire = 0
  Face = 0
  GlobalId = 36KkLHJl1D_AUwy3AkMKZ7
  Height = 570
  HorizontalArea = 263000
  IfcData = IfcUID=36KkLHJl1D_AUwy3AkMKZ7,+2 more (map truncated)
  IfcType = 166
  Joint = 0
  Length = 5460
  MakeBlocks = false
  Material = -> Material005
  MoveBase = false
  MoveWithHost = false
  Normal = (0,0,0)
  OffsetFirst = 0
  OffsetSecond = 0
  PerimeterLength = 5460
  PredefinedType = 0
  VerticalArea = 5.9964e+06
  Width = 50
FEATURE [App::MaterialObjectPython] Material006  label="Glass mate"  # material (typed FeaturePython)
  Description = Generic soda-lime glass
  Material = AuthorAndLicense=Glass-Generic,CardName=Glass-Generic,Color=(0.8, 0.8, 0.8, 1.0),Density=2520 kg/m^3,Description=Generic soda-lime glass,+12 more (map truncated)
  ProductURL = https://en.wikipedia.org/wiki/Soda-lime_glass
  Transparency = 80
FEATURE [App::MaterialObjectPython] Material007  label="Stone wild"  # material (typed FeaturePython)
  Description = Stone wild
  Material = AuthorAndLicense=Concrete-Generic,CardName=Concrete-Generic,Color=(0.49019607843137253, 0.49019607843137253, 0.49019607843137253, 1.0),+11 more (map truncated)
  Transparency = 0
FEATURE [Part::FeaturePython] Roof012  label="roof_4_side"  # Arch/BIM 113 (typed FeaturePython)
  Angles = [35,35,35,35]
  Base = -> Wire691
  BorderLength = 68940
  Face = 0
  Flip = false
  Heights = [3459.03,3851.14,3459.03,3851.14]
  HorizontalArea = 0
  IdRel = [-1,-1,-1,-1]
  IfcData = attributes={"GlobalId": {"name": "GlobalId", "type": "IfcGloballyUniqueId", "is_enum": false, "enum_values": []}, "Description": {"... (+613 chars omitted),+1 more (map truncated)
  IfcType = 113
  Material = -> Material007
  MoveBase = false
  MoveWithHost = false
  Overhang = [1000,1000,1000,1000]
  PerimeterLength = 0
  Placement = pos=(0,0,3093.7) rot=(0,0,1;0rad)
  PredefinedType = 0
  RidgeLength = 44214.8
  Runs = [5500,5500,5500,5500]
  Thickness = [350,350,350,350]
  VerticalArea = 0
FEATURE [Part::MultiCommon] Common033  label="Кровля с выступами"
  Shapes = -> [Extrude,Roof012]
FEATURE [Part::FeaturePython] Roof  label="Кровля 2скатн001"  # Arch/BIM 113 (typed FeaturePython)
  Angles = [35,35,35,35]
  Base = -> Rectangle3216
  BorderLength = 58880
  Face = 0
  Flip = false
  Heights = [2989.89,3150.93,2989.89,3150.93]
  HorizontalArea = 1.78486e+08
  IdRel = [-1,-1,-1,-1]
  IfcData = attributes={"GlobalId": {"name": "GlobalId", "type": "IfcGloballyUniqueId", "is_enum": false, "enum_values": []}, "Description": {"... (+613 chars omitted),+1 more (map truncated)
  IfcType = 113
  Material = -> Material007
  MoveBase = false
  MoveWithHost = false
  Overhang = [0,0,0,0]
  PerimeterLength = 0
  Placement = pos=(0,4.55e-13,3062.84) rot=(0,0,1;0rad)
  PredefinedType = 0
  RidgeLength = 39313.4
  Runs = [4500,4500,4500,4500]
  Thickness = [350,350,350,350]
  VerticalArea = 2.51577e+07
FEATURE [Part::Cut] Cut046
  Base = -> Common033
  Tool = -> Extrude092
FEATURE [Part::FeaturePython] Roof015  label="Кровля 4скатн.001"  # Arch/BIM 113 (typed FeaturePython)
  Angles = [35,35,35,35]
  Base = -> Wire691
  BorderLength = 49660
  Face = 0
  Flip = false
  Heights = [3459.03,3851.14,3459.03,3851.14]
  HorizontalArea = 147706000
  IdRel = [-1,-1,-1,-1]
  IfcData = attributes={"GlobalId": {"name": "GlobalId", "type": "IfcGloballyUniqueId", "is_enum": false, "enum_values": []}, "Description": {"... (+613 chars omitted),+1 more (map truncated)
  IfcType = 113
  Material = -> Material007
  MoveBase = false
  MoveWithHost = false
  Overhang = [0,0,0,0]
  PerimeterLength = 0
  Placement = pos=(0,0,-324.469) rot=(0,0,1;0rad)
  PredefinedType = 0
  RidgeLength = 36252.6
  Runs = [5500,5500,5500,5500]
  Thickness = [2800,2800,2800,2800]
  VerticalArea = 1.69746e+08
FEATURE [Part::MultiCommon] Common034
  Shapes = -> [Roof,Extrude108]
FEATURE [Part::MultiFuse] Fusion046
  Shapes = -> [Common034,Cut046]
FEATURE [Part::Cut] Cut050  label="Roof001"
  Base = -> Fusion046
  Tool = -> Roof015
FEATURE [Part::FeaturePython] Roof017  label="Крышка вентшахты"  # Arch/BIM 113 (typed FeaturePython)
  Angles = [35,35,35,35]
  Base = -> Wire825
  BorderLength = 3840
  Face = 0
  Flip = false
  GlobalId = 36hdyCWSLF5w0SQ7_aWhlx
  Heights = [196.058,210.062,196.058,210.062]
  HorizontalArea = 864000
  IdRel = [-1,-1,-1,-1]
  IfcData = IfcUID=36hdyCWSLF5w0SQ7_aWhlx,+2 more (map truncated)
  IfcType = 113
  Material = -> Material007
  MoveBase = false
  MoveWithHost = false
  Overhang = [80,80,80,80]
  PerimeterLength = 0
  Placement = pos=(0,0,7150) rot=(0,0,1;0rad)
  PredefinedType = 0
  RidgeLength = 2752.41
  Runs = [300,300,300,300]
  Thickness = [10,10,10,10]
  VerticalArea = 46877.7
FEATURE [App::GeometryPython] BuildingPart040  label="Вентстояки верх.часть"  # Arch/BIM 52 (typed FeaturePython)
  Area = 10240000
  GlobalId = 0S7MvrNQ9E$RFzm_BzyI1l
  Group = -> [Wall256,Wall257,Wall258,Wall255,Roof017]
  Height = 0
  HeightPropagate = true
  IfcData = IfcUID=0S7MvrNQ9E$RFzm_BzyI1l,attributes={"GlobalId": {"value": "0S7MvrNQ9E$RFzm_BzyI1l"}},+1 more (map truncated)
  IfcType = 52
  LevelOffset = 0
FEATURE [App::MaterialObjectPython] Material008  label="Wall cement"  # material (typed FeaturePython)
  Description = Wall cement
  Material = AuthorAndLicense=Concrete-Generic,CardName=Concrete-Generic,Color=(0.8, 0.8, 0.8, 1.0),CompressiveStrength=25 MPa,Density=2400 kg/m^3,+9 more (map truncated)
  Transparency = 0
FEATURE [Part::FeaturePython] Wall229  label="перегородка ГП 75мм"  # Arch/BIM 166 (typed FeaturePython)
  Align = 0
  Area = 5.32e+06
  Base = -> Line1383
  BlockHeight = 250
  BlockLength = 625
  CountBroken = 22
  CountEntire = 16
  Face = 0
  GlobalId = 2WVLl1wd99i9KCUxxwLupd
  Height = 2800
  HorizontalArea = 142500
  IfcData = IfcUID=2WVLl1wd99i9KCUxxwLupd; attributes={"GlobalId": {"value": "2WVLl1wd99i9KCUxxwLupd"}}
  IfcType = 166
  Joint = 0
  Length = 1900
  MakeBlocks = false
  Material = -> Material008
  MoveBase = false
  MoveWithHost = false
  Normal = (0,0,0)
  OffsetFirst = 300
  OffsetSecond = 50
  PerimeterLength = 3950
  PredefinedType = 0
  VerticalArea = 1.106e+07
  Width = 75
FEATURE [Part::FeaturePython] Wall233  label="Штукатурка 20мм 001"  # Arch/BIM 166 (typed FeaturePython)
  Align = 0
  Area = 30856000
  Base = -> Wire829
  BlockHeight = 0
  BlockLength = 0
  CountBroken = 0
  CountEntire = 0
  Face = 0
  GlobalId = 1_tpg5Ww11ef5dsryiIvTa
  Height = 2800
  HorizontalArea = 250000
  IfcData = IfcUID=1_tpg5Ww11ef5dsryiIvTa,+2 more (map truncated)
  IfcType = 166
  Joint = 0
  Length = 11020
  MakeBlocks = false
  Material = -> Material008
  MoveBase = false
  MoveWithHost = false
  Normal = (0,0,0)
  OffsetFirst = 0
  OffsetSecond = 0
  PerimeterLength = 14792.2
  PredefinedType = 0
  Subtractions = -> [Structure285]
  VerticalArea = 57455720
  Width = 20
FEATURE [Part::FeaturePython] Wall234  label="Штукатурка 20мм 002"  # Arch/BIM 166 (typed FeaturePython)
  Align = 0
  Area = 9100000
  Base = -> Line1392
  BlockHeight = 0
  BlockLength = 0
  CountBroken = 0
  CountEntire = 0
  Face = 0
  GlobalId = 3UxVpvSNzClhJFqsCgM8Mc
  Height = 2800
  HorizontalArea = 78200
  IfcData = IfcUID=3UxVpvSNzClhJFqsCgM8Mc,+2 more (map truncated)
  IfcType = 166
  Joint = 0
  Length = 3250
  MakeBlocks = false
  Material = -> Material008
  MoveBase = false
  MoveWithHost = false
  Normal = (0,0,0)
  OffsetFirst = 0
  OffsetSecond = 0
  PerimeterLength = 6280
  PredefinedType = 0
  Subtractions = -> [Structure019,Structure016]
  VerticalArea = 1.17155e+07
  Width = 20
FEATURE [Part::FeaturePython] Wall235  label="Штукатурка 20мм 003"  # Arch/BIM 166 (typed FeaturePython)
  Align = 0
  Area = 5600000
  Base = -> Line1393
  BlockHeight = 0
  BlockLength = 0
  CountBroken = 0
  CountEntire = 0
  Face = 0
  GlobalId = 0Elsg4vQ59AghdVdDj5fjs
  Height = 2800
  HorizontalArea = 53200
  IfcData = IfcUID=0Elsg4vQ59AghdVdDj5fjs,+2 more (map truncated)
  IfcType = 166
  Joint = 0
  Length = 2000
  MakeBlocks = false
  Material = -> Material008
  MoveBase = false
  MoveWithHost = false
  Normal = (0,0,0)
  OffsetFirst = 0
  OffsetSecond = 0
  PerimeterLength = 4080
  PredefinedType = 0
  Subtractions = -> [Structure017]
  VerticalArea = 9.53792e+06
  Width = 20
FEATURE [Part::FeaturePython] Wall236  label="Штукатурка 20мм 004"  # Arch/BIM 166 (typed FeaturePython)
  Align = 0
  Area = 43708000
  Base = -> Wire795
  BlockHeight = 0
  BlockLength = 0
  CountBroken = 0
  CountEntire = 0
  Face = 0
  GlobalId = 1rvNhjPI97_QqIjlSx0NrH
  Height = 2800
  HorizontalArea = 0
  IfcData = IfcUID=1rvNhjPI97_QqIjlSx0NrH,+2 more (map truncated)
  IfcType = 166
  Joint = 0
  Length = 15610
  MakeBlocks = false
  Material = -> Material008
  MoveBase = false
  MoveWithHost = false
  Normal = (0,0,0)
  OffsetFirst = 0
  OffsetSecond = 0
  PerimeterLength = 0
  PredefinedType = 0
  Subtractions = -> [Structure304,Structure317,Structure020,Structure023]
  VerticalArea = 0
  Width = 20
FEATURE [Part::FeaturePython] Wall237  label="Штукатурка 20мм 005"  # Arch/BIM 166 (typed FeaturePython)
  Align = 0
  Area = 38808000
  Base = -> Wire796
  BlockHeight = 0
  BlockLength = 0
  CountBroken = 0
  CountEntire = 0
  Face = 0
  GlobalId = 0ZsALDo$1EKg5Etd528_ZF
  Height = 2800
  HorizontalArea = 0
  IfcData = IfcUID=0ZsALDo$1EKg5Etd528_ZF,+2 more (map truncated)
  IfcType = 166
  Joint = 0
  Length = 13860
  MakeBlocks = false
  Material = -> Material008
  MoveBase = false
  MoveWithHost = false
  Normal = (0,0,0)
  OffsetFirst = 0
  OffsetSecond = 0
  PerimeterLength = 0
  PredefinedType = 0
  Subtractions = -> [Structure308,Structure317,Structure306]
  VerticalArea = 0
  Width = 20
FEATURE [Part::FeaturePython] Wall238  label="Штукатурка 20мм 006"  # Arch/BIM 166 (typed FeaturePython)
  Align = 0
  Area = 37408000
  Base = -> Wire797
  BlockHeight = 0
  BlockLength = 0
  CountBroken = 0
  CountEntire = 0
  Face = 0
  GlobalId = 2HzDQoGZ5FsODk6SDIgE_Y
  Height = 2800
  HorizontalArea = 307200
  IfcData = IfcUID=2HzDQoGZ5FsODk6SDIgE_Y,+2 more (map truncated)
  IfcType = 166
  Joint = 0
  Length = 13360
  MakeBlocks = false
  Material = -> Material008
  MoveBase = false
  MoveWithHost = false
  Normal = (0,0,0)
  OffsetFirst = 0
  OffsetSecond = 0
  PerimeterLength = 26620
  PredefinedType = 0
  Subtractions = -> [Structure315,Structure023]
  VerticalArea = 6.5008e+07
  Width = 20
FEATURE [App::MaterialObjectPython] Material009  label="Silicate blocks"  # material (typed FeaturePython)
  Description = Silicate blocks
  Material = AuthorAndLicense=Concrete-Generic,CardName=Concrete-Generic,Color=(0.8313725490196079, 0.7647058823529411, 0.7647058823529411, 1.0),+11 more (map truncated)
  Transparency = 0
FEATURE [Part::FeaturePython] Wall015  label="перегородка (сил.блок 500х250х80) 001"  # Arch/BIM 166 (typed FeaturePython)
  Align = 2
  Area = 10360000
  Base = -> Line1054
  BlockHeight = 250
  BlockLength = 0
  CountBroken = 0
  CountEntire = 0
  Face = 0
  GlobalId = 0Pb3kWXLL62hdiT4yMFPnD
  Height = 2800
  HorizontalArea = 296000
  IfcData = IfcUID=0Pb3kWXLL62hdiT4yMFPnD; attributes={"GlobalId": {"value": "0Pb3kWXLL62hdiT4yMFPnD"}}
  IfcType = 166
  Joint = 0
  Length = 3700
  MakeBlocks = false
  Material = -> Material009
  MoveBase = false
  MoveWithHost = false
  Normal = (0,0,0)
  OffsetFirst = 0
  OffsetSecond = 300
  PerimeterLength = 7560
  PredefinedType = 0
  Subtractions = -> [Structure141]
  VerticalArea = 1.7642e+07
  Width = 80
FEATURE [Part::FeaturePython] Wall186  label="перегородка (сил.блок 500х250х80) 002"  # Arch/BIM 166 (typed FeaturePython)
  Additions = -> [Wall162,Wall187,Wall225,Wall188,Wall224,Wall222]
  Align = 2
  Area = 16716000
  Base = -> Line1316
  BlockHeight = 250
  BlockLength = 0
  CountBroken = 0
  CountEntire = 0
  Face = 0
  GlobalId = 1Rj7XWwfD1TACQSKytQJ$J
  Height = 2800
  HorizontalArea = 0
  IfcData = IfcUID=1Rj7XWwfD1TACQSKytQJ$J; attributes={"GlobalId": {"value": "1Rj7XWwfD1TACQSKytQJ$J"}}
  IfcType = 166
  Joint = 0
  Length = 5970
  MakeBlocks = false
  Material = -> Material009
  MoveBase = false
  MoveWithHost = false
  Normal = (0,0,0)
  OffsetFirst = 300
  OffsetSecond = 0
  PerimeterLength = 0
  PredefinedType = 0
  Subtractions = -> [Structure024,Structure026,Structure021,Box3211,Box3228]
  VerticalArea = 0
  Width = 80
FEATURE [Part::FeaturePython] Wall223  label="перегородка (сил.блок 500х250х80) 004"  # Arch/BIM 166 (typed FeaturePython)
  Align = 2
  Area = 1.036e+07
  Base = -> Line1358
  BlockHeight = 250
  BlockLength = 0
  CountBroken = 0
  CountEntire = 0
  Face = 0
  GlobalId = 1OB118XG9DJPL5jtZdDHzR
  Height = 2800
  HorizontalArea = 296000
  IfcData = IfcUID=1OB118XG9DJPL5jtZdDHzR; attributes={"GlobalId": {"value": "1OB118XG9DJPL5jtZdDHzR"}}
  IfcType = 166
  Joint = 0
  Length = 3700
  MakeBlocks = false
  Material = -> Material009
  MoveBase = false
  MoveWithHost = false
  Normal = (0,0,0)
  OffsetFirst = 300
  OffsetSecond = 50
  PerimeterLength = 7560
  PredefinedType = 0
  Subtractions = -> [Structure333]
  VerticalArea = 1.7888e+07
  Width = 80
FEATURE [App::MaterialObjectPython] Material010  label="Steel-Generic"  # material (typed FeaturePython)
  Description = This is a blend Steel material card. The values are at the low end of the spectrum. If you need a more precise material definition use the more specialised steel cards.
  Material = AuthorAndLicense=Steel-Generic,CardName=Steel-Generic,Color=(0.3803921568627451, 0.3803921568627451, 0.3803921568627451, 1.0),Density=7900 kg/m^3,+13 more (map truncated)
  ProductURL = https://en.wikipedia.org/wiki/Steel
  Transparency = 0
FEATURE [Part::FeaturePython] Pipe004  label="коакс. дымоход 120"  # Arch/BIM 98 (typed FeaturePython)
  Base = -> Wire830
  Diameter = 120
  GlobalId = 3_rhopNO93fB54w5AHh6mI
  HorizontalArea = 0
  IfcData = IfcUID=3_rhopNO93fB54w5AHh6mI,+2 more (map truncated)
  IfcType = 98
  Length = 6119.59
  Material = -> Material010
  MoveBase = false
  MoveWithHost = false
  OffsetEnd = 0
  OffsetStart = 0
  PerimeterLength = 0
  PredefinedType = 0
  VerticalArea = 0
  WallThickness = 0
FEATURE [Part::FeaturePython] Pipe007  label="Дымоход 200/300"  # Arch/BIM 98 (typed FeaturePython)
  Base = -> Wire828
  Diameter = 300
  GlobalId = 2NNTD1t9nFeu6xjn5rmLg2
  HorizontalArea = 0
  IfcData = IfcUID=2NNTD1t9nFeu6xjn5rmLg2,+2 more (map truncated)
  IfcType = 98
  Length = 5777.48
  Material = -> Material010
  MoveBase = false
  MoveWithHost = false
  OffsetEnd = 0
  OffsetStart = 0
  PerimeterLength = 0
  PredefinedType = 0
  VerticalArea = 0
  WallThickness = 0
FEATURE [Part::FeaturePython] Pipe008  label="Дымоход 200"  # Arch/BIM 98 (typed FeaturePython)
  Base = -> Line1479
  Diameter = 200
  GlobalId = 11JHR0lR55LRzzbgV05jpw
  HorizontalArea = 0
  IfcData = IfcUID=11JHR0lR55LRzzbgV05jpw,+2 more (map truncated)
  IfcType = 98
  Length = 5600
  Material = -> Material010
  MoveBase = false
  MoveWithHost = false
  OffsetEnd = 0
  OffsetStart = 0
  PerimeterLength = 0
  PredefinedType = 0
  VerticalArea = 0
  WallThickness = 0
FEATURE [Part::FeaturePython] Pipe009  label="Вентканал 140мм 001"  # Arch/BIM 98 (typed FeaturePython)
  Base = -> Line1480
  Diameter = 140
  GlobalId = 3HmMp4Xfr8TAmJ5ODVlau7
  HorizontalArea = 0
  IfcData = IfcUID=3HmMp4Xfr8TAmJ5ODVlau7,+2 more (map truncated)
  IfcType = 98
  Length = 4200
  Material = -> Material010
  MoveBase = false
  MoveWithHost = false
  OffsetEnd = 0
  OffsetStart = 0
  PerimeterLength = 0
  PredefinedType = 0
  VerticalArea = 0
  WallThickness = 0
FEATURE [Part::FeaturePython] Pipe010  label="Вентканал 140мм 002"  # Arch/BIM 98 (typed FeaturePython)
  Base = -> Line1480
  Diameter = 140
  GlobalId = 3OBLLStZzDnRK0fH7jX7AD
  HorizontalArea = 0
  IfcData = IfcUID=3OBLLStZzDnRK0fH7jX7AD,+2 more (map truncated)
  IfcType = 98
  Length = 4200
  Material = -> Material010
  MoveBase = false
  MoveWithHost = false
  OffsetEnd = 0
  OffsetStart = 0
  PerimeterLength = 0
  Placement = pos=(150,-150,0) rot=(0,0,1;0rad)
  PredefinedType = 0
  VerticalArea = 0
  WallThickness = 0
FEATURE [Part::FeaturePython] Pipe011  label="Вентканал 140мм 003"  # Arch/BIM 98 (typed FeaturePython)
  Base = -> Line1480
  Diameter = 140
  GlobalId = 2bpWL1Qcr8UxhAynMgY7T5
  HorizontalArea = 0
  IfcData = IfcUID=2bpWL1Qcr8UxhAynMgY7T5,+2 more (map truncated)
  IfcType = 98
  Length = 4200
  Material = -> Material010
  MoveBase = false
  MoveWithHost = false
  OffsetEnd = 0
  OffsetStart = 0
  PerimeterLength = 0
  Placement = pos=(0,-150,0) rot=(0,0,1;0rad)
  PredefinedType = 0
  VerticalArea = 0
  WallThickness = 0
FEATURE [Part::FeaturePython] Pipe013  label="Вентканал 140мм 004"  # Arch/BIM 98 (typed FeaturePython)
  Base = -> Line1480
  Diameter = 140
  GlobalId = 22CnrufE59UfX6ZQo80id_
  HorizontalArea = 0
  IfcData = IfcUID=22CnrufE59UfX6ZQo80id_,+2 more (map truncated)
  IfcType = 98
  Length = 4200
  Material = -> Material010
  MoveBase = false
  MoveWithHost = false
  OffsetEnd = 0
  OffsetStart = 0
  PerimeterLength = 0
  Placement = pos=(150,0,0) rot=(0,0,1;0rad)
  PredefinedType = 0
  VerticalArea = 0
  WallThickness = 0
FEATURE [App::MaterialObjectPython] Material011  label="Polypropylene"  # material (typed FeaturePython)
  Material = AuthorAndLicense=PP-Generic,CardName=PP-Generic,Color=(0.38823529411764707, 0.38823529411764707, 0.38823529411764707, 1.0),CompressiveStrength=10 MPa,+15 more (map truncated)
  ProductURL = https://en.wikipedia.org/wiki/Polypropylene
  Transparency = 0
FEATURE [Part::FeaturePython] Window020  label="Д-90-004"  # Arch/BIM 41 (typed FeaturePython)
  Area = 1935000
  Base = -> Sketch248
  Frame = 50
  GlobalId = 00iW5F1Zz0_RepVZ61wedb
  Height = 2150
  HoleDepth = 0
  HoleWire = 0
  HorizontalArea = 0
  IfcData = IfcUID=00iW5F1Zz0_RepVZ61wedb; attributes={"OverallHeight": {"value": 2150.0}, "OverallWidth": {"value": 900.0}, "GlobalId": {"value": "00iW5F1Zz0_RepVZ61wedb"}}
  IfcType = 41
  LouvreSpacing = 0
  LouvreWidth = 0
  Material = -> Material011
  MoveBase = false
  MoveWithHost = true
  Normal = (0,1,0)
  Opening = 0
  OperationType = 0
  OverallHeight = 2150
  OverallWidth = 900
  PerimeterLength = 0
  Placement = pos=(0,50,0) rot=(0,0,1;0rad)
  PredefinedType = 0
  Preset = 6
  SymbolElevation = false
  SymbolPlan = false
  VerticalArea = 0
  Width = 900
  WindowParts = OuterFrame | Frame | Wire0,Wire1 | 0.0+V | 0.00+V | Door | Solid panel | Wire1 | 50.0 | 0.0+V
  expr: OverallWidth = .Width.Value
  expr: OverallHeight = .Height.Value
FEATURE [Part::FeaturePython] Window021  label="Д-90-003"  # Arch/BIM 41 (typed FeaturePython)
  Area = 1935000
  Base = -> Sketch251
  Frame = 50
  GlobalId = 29QgZPyov5qAVey2RViV7P
  Height = 2150
  HoleDepth = 0
  HoleWire = 0
  HorizontalArea = 0
  IfcData = IfcUID=29QgZPyov5qAVey2RViV7P; attributes={"OverallHeight": {"value": 2150.0}, "OverallWidth": {"value": 900.0}, "GlobalId": {"value": "29QgZPyov5qAVey2RViV7P"}}
  IfcType = 41
  LouvreSpacing = 0
  LouvreWidth = 0
  Material = -> Material011
  MoveBase = false
  MoveWithHost = true
  Normal = (1,0,0)
  Opening = 0
  OperationType = 0
  OverallHeight = 2150
  OverallWidth = 900
  PerimeterLength = 0
  PredefinedType = 0
  Preset = 6
  SymbolElevation = false
  SymbolPlan = false
  VerticalArea = 0
  Width = 900
  WindowParts = OuterFrame | Frame | Wire0,Wire1 | 0.0+V | 0.00+V | Door | Solid panel | Wire1 | 50.0 | 0.0+V
  expr: OverallWidth = .Width.Value
  expr: OverallHeight = .Height.Value
FEATURE [Part::FeaturePython] Window026  label="Д-90-002"  # Arch/BIM 41 (typed FeaturePython)
  Area = 1935000
  Base = -> Sketch260
  Frame = 50
  GlobalId = 3IW9J8Pfn69QiBWvx91KEB
  Height = 2150
  HoleDepth = 0
  HoleWire = 0
  HorizontalArea = 0
  IfcData = IfcUID=3IW9J8Pfn69QiBWvx91KEB; attributes={"OverallHeight": {"value": 2150.0}, "OverallWidth": {"value": 900.0}, "GlobalId": {"value": "3IW9J8Pfn69QiBWvx91KEB"}}
  IfcType = 41
  LouvreSpacing = 0
  LouvreWidth = 0
  Material = -> Material011
  MoveBase = false
  MoveWithHost = true
  Normal = (0,1,0)
  Opening = 0
  OperationType = 0
  OverallHeight = 2150
  OverallWidth = 900
  PerimeterLength = 0
  Placement = pos=(0,0,180) rot=(0,0,1;0rad)
  PredefinedType = 0
  Preset = 6
  SymbolElevation = false
  SymbolPlan = false
  VerticalArea = 0
  Width = 900
  WindowParts = OuterFrame | Frame | Wire0,Wire1 | 0.0+V | 0.00+V | Door | Solid panel | Wire1 | 50.0 | 0.0+V
  expr: OverallWidth = .Width.Value
  expr: OverallHeight = .Height.Value
FEATURE [Part::FeaturePython] Window048  label="Д-90-001"  # Arch/BIM 41 (typed FeaturePython)
  Area = 1935000
  Base = -> Sketch305
  Frame = 50
  GlobalId = 3YJH8Y7brE3BZDEOWbTYIP
  Height = 2150
  HoleDepth = 0
  HoleWire = 0
  HorizontalArea = 0
  IfcData = IfcUID=3YJH8Y7brE3BZDEOWbTYIP; attributes={"OverallHeight": {"value": 2150.0}, "OverallWidth": {"value": 900.0}, "GlobalId": {"value": "3YJH8Y7brE3BZDEOWbTYIP"}}
  IfcType = 41
  LouvreSpacing = 0
  LouvreWidth = 0
  Material = -> Material011
  MoveBase = false
  MoveWithHost = true
  Normal = (1,0,0)
  Opening = 0
  OperationType = 0
  OverallHeight = 2150
  OverallWidth = 900
  PerimeterLength = 0
  PredefinedType = 0
  Preset = 6
  SymbolElevation = false
  SymbolPlan = false
  VerticalArea = 0
  Width = 900
  WindowParts = OuterFrame | Frame | Wire0,Wire1 | 0.0+V | 0.00+V | Door | Solid panel | Wire1 | 50.0 | 0.0+V
  expr: OverallHeight = .Height.Value
  expr: OverallWidth = .Width.Value
FEATURE [Part::FeaturePython] Window052  label="Д-90-005"  # Arch/BIM 41 (typed FeaturePython)
  Area = 1935000
  Base = -> Sketch309
  Frame = 50
  GlobalId = 1cijn4gZv3rAlY7HDrqfh6
  Height = 2150
  HoleDepth = 0
  HoleWire = 0
  HorizontalArea = 0
  IfcData = IfcUID=1cijn4gZv3rAlY7HDrqfh6; attributes={"OverallHeight": {"value": 2150.0}, "OverallWidth": {"value": 900.0}, "GlobalId": {"value": "1cijn4gZv3rAlY7HDrqfh6"}}
  IfcType = 41
  LouvreSpacing = 0
  LouvreWidth = 0
  Material = -> Material011
  MoveBase = false
  MoveWithHost = true
  Normal = (-1,0,0)
  Opening = 0
  OperationType = 0
  OverallHeight = 2150
  OverallWidth = 900
  PerimeterLength = 0
  PredefinedType = 0
  Preset = 6
  SymbolElevation = false
  SymbolPlan = false
  VerticalArea = 0
  Width = 900
  WindowParts = OuterFrame | Frame | Wire0,Wire1 | 0.0+V | 0.00+V | Door | Solid panel | Wire1 | 50.0 | 0.0+V
  expr: OverallHeight = .Height.Value
  expr: OverallWidth = .Width.Value
FEATURE [Part::FeaturePython] Window061  label="Окно Velox 55x98 001"  # Arch/BIM 170 (typed FeaturePython)
  Area = 539000
  Base = -> Sketch
  Frame = 50
  GlobalId = 0OgXawITjBROe3cBxnSt2i
  Height = 980
  HoleDepth = 0
  HoleWire = 0
  HorizontalArea = 0
  Hosts = -> [Roof012]
  IfcData = IfcUID=0OgXawITjBROe3cBxnSt2i,+2 more (map truncated)
  IfcType = 170
  LouvreSpacing = 0
  LouvreWidth = 0
  Material = -> Material011
  MoveBase = false
  MoveWithHost = true
  Normal = (0,0.573576,-0.819152)
  Opening = 0
  OverallHeight = 980
  OverallWidth = 550
  PartitioningType = 0
  PerimeterLength = 0
  Placement = pos=(0,0,23.7) rot=(0,0,1;0rad)
  PredefinedType = 0
  Preset = 2
  SymbolElevation = false
  SymbolPlan = false
  VerticalArea = 0
  Width = 550
  WindowParts = OuterFrame | Frame | Wire0,Wire1 | 300.0+V | 0.00+V | InnerFrame | Frame | Wire2,Wire3,Edge8,Mode1 | 50.0 | 50.0+V | InnerGlass | Glass panel | Wire3 | 5.0 | 75.0+V
  expr: OverallHeight = .Height.Value
  expr: OverallWidth = .Width.Value
FEATURE [Part::FeaturePython] Window062  label="Окно Velox 55x98 002"  # Arch/BIM 170 (typed FeaturePython)
  Area = 539000
  Base = -> Sketch321
  Frame = 50
  GlobalId = 1t8PRcMxPE3hYzY8q_2YfV
  Height = 980
  HoleDepth = 0
  HoleWire = 0
  HorizontalArea = 0
  Hosts = -> [Roof012]
  IfcData = IfcUID=1t8PRcMxPE3hYzY8q_2YfV,+2 more (map truncated)
  IfcType = 170
  LouvreSpacing = 0
  LouvreWidth = 0
  Material = -> Material011
  MoveBase = false
  MoveWithHost = true
  Normal = (0,0.573576,-0.819152)
  Opening = 0
  OverallHeight = 980
  OverallWidth = 550
  PartitioningType = 0
  PerimeterLength = 0
  Placement = pos=(0,0,23.7) rot=(0,0,1;0rad)
  PredefinedType = 0
  Preset = 2
  SymbolElevation = false
  SymbolPlan = false
  VerticalArea = 0
  Width = 550
  WindowParts = OuterFrame | Frame | Wire0,Wire1 | 300.0+V | 0.00+V | InnerFrame | Frame | Wire2,Wire3,Edge8,Mode1 | 50.0 | 50.0+V | InnerGlass | Glass panel | Wire3 | 5.0 | 75.0+V
  expr: OverallHeight = .Height.Value
  expr: OverallWidth = .Width.Value
FEATURE [Part::FeaturePython] Window063  label="Окно Velox 55x98 003"  # Arch/BIM 170 (typed FeaturePython)
  Area = 539000
  Base = -> Sketch322
  Frame = 50
  GlobalId = 1OK8u$9hHB99HRKu0QW2Gw
  Height = 980
  HoleDepth = 0
  HoleWire = 0
  HorizontalArea = 0
  Hosts = -> [Roof012]
  IfcData = IfcUID=1OK8u$9hHB99HRKu0QW2Gw,+2 more (map truncated)
  IfcType = 170
  LouvreSpacing = 0
  LouvreWidth = 0
  Material = -> Material011
  MoveBase = false
  MoveWithHost = true
  Normal = (0,-0.573576,-0.819152)
  Opening = 0
  OverallHeight = 980
  OverallWidth = 550
  PartitioningType = 0
  PerimeterLength = 0
  Placement = pos=(0,0,23.7) rot=(0,0,1;0rad)
  PredefinedType = 0
  Preset = 2
  SymbolElevation = false
  SymbolPlan = false
  VerticalArea = 0
  Width = 550
  WindowParts = OuterFrame | Frame | Wire0,Wire1 | 300.0+V | 0.00+V | InnerFrame | Frame | Wire2,Wire3,Edge8,Mode1 | 50.0 | 50.0+V | InnerGlass | Glass panel | Wire3 | 5.0 | 75.0+V
  expr: OverallHeight = .Height.Value
  expr: OverallWidth = .Width.Value
FEATURE [Part::FeaturePython] Pipe006  label="Фановый стояк 001"  # Arch/BIM 98 (typed FeaturePython)
  Base = -> Line1465
  Diameter = 110
  GlobalId = 0tHcO5Qt903xGrElAHG3sm
  HorizontalArea = 0
  IfcData = IfcUID=0tHcO5Qt903xGrElAHG3sm,+2 more (map truncated)
  IfcType = 98
  Length = 7200
  Material = -> Material011
  MoveBase = false
  MoveWithHost = false
  OffsetEnd = 0
  OffsetStart = 0
  PerimeterLength = 0
  PredefinedType = 0
  VerticalArea = 0
  WallThickness = 0
FEATURE [Part::Cut] Cut051  label="Roof002"
  Base = -> Cut050
  Tool = -> Wall057
FEATURE [Part::Part2DObjectPython] Wire836  # Draft 2D object (typed FeaturePython)
  Area = 0
  ChamferSize = 0
  Closed = true
  End = (0,7042.91,3733)
  FilletRadius = 0
  Length = 14626.9
  MakeFace = false
  Placement = pos=(0,436.862,3746.85) rot=(0.57735,0.57735,0.57735;2.0944rad)
  Points = (4) [(-19.7731,-13.8453,0),(3094.8,2167,0),(3491.48,2167,0),(6606.05,-13.8453,0)]
  Start = (0,417.089,3733)
  Subdivisions = 0
FEATURE [Part::FeaturePython] Structure357  label="Фронтон каркасн. 001"  # Arch/BIM 52 (typed FeaturePython)
  Base = -> Wire836
  FaceMaker = 0
  GlobalId = 3jxAwhryLARBy7FrCZDeex
  Height = 400
  HorizontalArea = 0
  IfcData = IfcUID=3jxAwhryLARBy7FrCZDeex,+2 more (map truncated)
  IfcType = 52
  Length = 0
  Material = -> Material003
  MoveBase = false
  MoveWithHost = false
  Nodes = (2) [(0,3730,4501.01),(-380,3730,4501.01)]
  NodesOffset = 0
  Normal = (0,0,0)
  PerimeterLength = 14935.2
  Placement = pos=(12950,3.637e-12,0) rot=(0,0,1;0rad)
  VerticalArea = 9.71968e+06
  Width = 100
FEATURE [Part::FeaturePython] Window057  label="ОК-Фронтон-1-1"  # Arch/BIM 170 (typed FeaturePython)
  Area = 1500000
  Base = -> Sketch316
  Frame = 50
  GlobalId = 0$_XcsZN1ByAmbTwc2WkwE
  Height = 1500
  HoleDepth = 0
  HoleWire = 0
  HorizontalArea = 0
  Hosts = -> [Structure357]
  IfcData = IfcUID=0$_XcsZN1ByAmbTwc2WkwE; attributes={"OverallHeight": {"value": 1500.0}, "OverallWidth": {"value": 1000.0}, "GlobalId": {"value": "0$_XcsZN1ByAmbTwc2WkwE"}}
  IfcType = 170
  LouvreSpacing = 0
  LouvreWidth = 0
  Material = -> Material011
  MoveBase = false
  MoveWithHost = true
  Normal = (-1,0,0)
  Opening = 0
  OverallHeight = 1500
  OverallWidth = 1000
  PartitioningType = 0
  PerimeterLength = 0
  Placement = pos=(12990,4.546e-12,0) rot=(0,0,1;0rad)
  PredefinedType = 0
  Preset = 2
  SymbolElevation = false
  SymbolPlan = false
  VerticalArea = 0
  Width = 1000
  WindowParts = OuterFrame | Frame | Wire0,Wire1 | 0.0+V | 0.00+V | InnerFrame | Frame | Wire2,Wire3 | 0.00+V | 0.0+V | InnerGlass | Glass panel | Wire3 | 10.0 | 50.0+V
  expr: OverallHeight = .Height.Value
  expr: OverallWidth = .Width.Value
FEATURE [Part::FeaturePython] Window059  label="ОК-Фронтон-1-2"  # Arch/BIM 170 (typed FeaturePython)
  Area = 1500000
  Base = -> Sketch318
  Frame = 50
  GlobalId = 0nJFhS2Ib74ffg7zBAHN8z
  Height = 1500
  HoleDepth = 0
  HoleWire = 0
  HorizontalArea = 0
  Hosts = -> [Structure357]
  IfcData = IfcUID=0nJFhS2Ib74ffg7zBAHN8z; attributes={"OverallHeight": {"value": 1500.0}, "OverallWidth": {"value": 1000.0}, "GlobalId": {"value": "0nJFhS2Ib74ffg7zBAHN8z"}}
  IfcType = 170
  LouvreSpacing = 0
  LouvreWidth = 0
  Material = -> Material011
  MoveBase = false
  MoveWithHost = true
  Normal = (-1,0,0)
  Opening = 0
  OverallHeight = 1500
  OverallWidth = 1000
  PartitioningType = 0
  PerimeterLength = 0
  Placement = pos=(12990,4.546e-12,0) rot=(0,0,1;0rad)
  PredefinedType = 0
  Preset = 2
  SymbolElevation = false
  SymbolPlan = false
  VerticalArea = 0
  Width = 1000
  WindowParts = OuterFrame | Frame | Wire0,Wire1 | 0.0+V | 0.00+V | InnerFrame | Frame | Wire2,Wire3 | 0.00+V | 0.0+V | InnerGlass | Glass panel | Wire3 | 10.0 | 50.0+V
  expr: OverallHeight = .Height.Value
  expr: OverallWidth = .Width.Value
FEATURE [Part::FeaturePython] Structure367  label="Фронтон каркасн. 002"  # Arch/BIM 52 (typed FeaturePython)
  Base = -> Wire836
  FaceMaker = 0
  GlobalId = 2MSSJcqfT2sha54GOqmBwm
  Height = 400
  HorizontalArea = 0
  IfcData = IfcUID=2MSSJcqfT2sha54GOqmBwm,+2 more (map truncated)
  IfcType = 52
  Length = 0
  Material = -> Material003
  MoveBase = false
  MoveWithHost = false
  Nodes = (2) [(0,3730,4501.01),(-380,3730,4501.01)]
  NodesOffset = 0
  Normal = (0,0,0)
  PerimeterLength = 0
  Placement = pos=(-30,0,0) rot=(0,0,1;0rad)
  VerticalArea = 9.71968e+06
  Width = 100
FEATURE [App::GeometryPython] BuildingPart083  label="Фронтоны"  # Arch/BIM 52 (typed FeaturePython)
  Area = 0
  GlobalId = 0vaHPODnn9yvkLUa9L_ZFm
  Group = -> [Structure357,Structure367]
  Height = 0
  HeightPropagate = true
  IfcData = IfcUID=0vaHPODnn9yvkLUa9L_ZFm,+2 more (map truncated)
  IfcType = 52
  LevelOffset = 0
FEATURE [Part::FeaturePython] Window066  label="ОК-Фронтон-1-005"  # Arch/BIM 170 (typed FeaturePython)
  Area = 1500000
  Base = -> Sketch316
  Frame = 50
  GlobalId = 2UO6SkOn1FXAzPeAHbjv7O
  Height = 1500
  HoleDepth = 0
  HoleWire = 0
  HorizontalArea = 0
  Hosts = -> [Structure367]
  IfcData = IfcUID=2UO6SkOn1FXAzPeAHbjv7O; attributes={"OverallHeight": {"value": 1500.0}, "OverallWidth": {"value": 1000.0}, "GlobalId": {"value": "2UO6SkOn1FXAzPeAHbjv7O"}}
  IfcType = 170
  LouvreSpacing = 0
  LouvreWidth = 0
  Material = -> Material011
  MoveBase = false
  MoveWithHost = true
  Normal = (1,0,0)
  Opening = 0
  OverallHeight = 1500
  OverallWidth = 1000
  PartitioningType = 0
  PerimeterLength = 0
  Placement = pos=(-80,0,0) rot=(0,0,1;0rad)
  PredefinedType = 0
  Preset = 2
  SymbolElevation = false
  SymbolPlan = false
  VerticalArea = 0
  Width = 1000
  WindowParts = OuterFrame | Frame | Wire0,Wire1 | 0.0+V | 0.00+V | InnerFrame | Frame | Wire2,Wire3 | 0.00+V | 0.0+V | InnerGlass | Glass panel | Wire3 | 10.0 | 50.0+V
  expr: OverallWidth = .Width.Value
  expr: OverallHeight = .Height.Value
FEATURE [Part::FeaturePython] Window067  label="ОК-Фронтон-1-006"  # Arch/BIM 170 (typed FeaturePython)
  Area = 1500000
  Base = -> Sketch318
  Frame = 50
  GlobalId = 1cBa_Vux91PRzEq6I7BfM7
  Height = 1500
  HoleDepth = 0
  HoleWire = 0
  HorizontalArea = 0
  Hosts = -> [Structure367]
  IfcData = IfcUID=1cBa_Vux91PRzEq6I7BfM7; attributes={"OverallHeight": {"value": 1500.0}, "OverallWidth": {"value": 1000.0}, "GlobalId": {"value": "1cBa_Vux91PRzEq6I7BfM7"}}
  IfcType = 170
  LouvreSpacing = 0
  LouvreWidth = 0
  Material = -> Material011
  MoveBase = false
  MoveWithHost = true
  Normal = (1,0,0)
  Opening = 0
  OverallHeight = 1500
  OverallWidth = 1000
  PartitioningType = 0
  PerimeterLength = 0
  Placement = pos=(-80,0,0) rot=(0,0,1;0rad)
  PredefinedType = 0
  Preset = 2
  SymbolElevation = false
  SymbolPlan = false
  VerticalArea = 0
  Width = 1000
  WindowParts = OuterFrame | Frame | Wire0,Wire1 | 0.0+V | 0.00+V | InnerFrame | Frame | Wire2,Wire3 | 0.00+V | 0.0+V | InnerGlass | Glass panel | Wire3 | 10.0 | 50.0+V
  expr: OverallWidth = .Width.Value
  expr: OverallHeight = .Height.Value
FEATURE [Part::Part2DObjectPython] Wire837  # Draft 2D object (typed FeaturePython)
  Area = 0
  ChamferSize = 0
  Closed = false
  End = (3400,3555,0)
  FilletRadius = 0
  Length = 4200
  MakeFace = false
  Placement = pos=(4110,-10,0) rot=(0,0,1;0rad)
  Points = (4) [(-110,-35,0),(-110,2295,0),(-710,2295,0),(-710,3565,0)]
  Start = (4000,-45,0)
  Subdivisions = 0
FEATURE [Part::Part2DObjectPython] Wire838  # Draft 2D object (typed FeaturePython)
  Area = 0
  ChamferSize = 0
  Closed = false
  End = (3500,3555,0)
  FilletRadius = 0
  Length = 9650
  MakeFace = false
  Placement = pos=(9540,-10,0) rot=(0,0,1;0rad)
  Points = (4) [(10,-35,0),(10,2395,0),(-6040,2395,0),(-6040,3565,0)]
  Start = (9550,-45,0)
  Subdivisions = 0
FEATURE [Part::Part2DObjectPython] Wire839  # Draft 2D object (typed FeaturePython)
  Area = 0
  ChamferSize = 0
  Closed = false
  End = (7450,-45,0)
  FilletRadius = 0
  Length = 6660
  MakeFace = false
  Placement = pos=(9460,-10,0) rot=(0,0,1;0rad)
  Points = (6) [(-10,-35,0),(-10,1795,0),(-810,1795,0),(-810,2295,0),(-2010,2295,0),(-2010,-35,0)]
  Start = (9450,-45,0)
  Subdivisions = 0
FEATURE [Part::Part2DObjectPython] Wire840  # Draft 2D object (typed FeaturePython)
  Area = 0
  ChamferSize = 0
  Closed = false
  End = (4100,-45,0)
  FilletRadius = 0
  Length = 7910
  MakeFace = false
  Placement = pos=(7310,-10,0) rot=(0,0,1;0rad)
  Points = (4) [(40,-35,0),(40,2295,0),(-3210,2295,0),(-3210,-35,0)]
  Start = (7350,-45,0)
  Subdivisions = 0
FEATURE [Part::FeaturePython] Wall  label="Штукатурка 10мм 001"  # Arch/BIM 166 (typed FeaturePython)
  Align = 0
  Area = 11760000
  Base = -> Wire837
  BlockHeight = 0
  BlockLength = 0
  CountBroken = 0
  CountEntire = 0
  Face = 0
  GlobalId = 0h0Qmcrjb7bRq5SNTtGOK3
  Height = 2800
  HorizontalArea = 42000
  IfcData = IfcUID=0h0Qmcrjb7bRq5SNTtGOK3,+2 more (map truncated)
  IfcType = 166
  Joint = 0
  Length = 4200
  MakeBlocks = false
  Material = -> Material008
  MoveBase = false
  MoveWithHost = false
  Normal = (0,0,0)
  OffsetFirst = 0
  OffsetSecond = 0
  PerimeterLength = 8420
  PredefinedType = 0
  Subtractions = -> [Structure021]
  VerticalArea = 19749000
  Width = 10
FEATURE [Part::FeaturePython] Wall267  label="Штукатурка 10мм 002"  # Arch/BIM 166 (typed FeaturePython)
  Align = 1
  Area = 27020000
  Base = -> Wire838
  BlockHeight = 0
  BlockLength = 0
  CountBroken = 0
  CountEntire = 0
  Face = 0
  GlobalId = 2wC2Vrh6fADPaqtRoWs2md
  Height = 2800
  HorizontalArea = 0
  IfcData = IfcUID=2wC2Vrh6fADPaqtRoWs2md,+2 more (map truncated)
  IfcType = 166
  Joint = 0
  Length = 9650
  MakeBlocks = false
  Material = -> Material008
  MoveBase = false
  MoveWithHost = false
  Normal = (0,0,0)
  OffsetFirst = 0
  OffsetSecond = 0
  PerimeterLength = 0
  PredefinedType = 0
  Subtractions = -> [Structure024,Structure026,Structure021,Box3211,Box3228]
  VerticalArea = 0
  Width = 10
FEATURE [Part::FeaturePython] Wall268  label="Штукатурка 10мм 003"  # Arch/BIM 166 (typed FeaturePython)
  Align = 0
  Area = 18648000
  Base = -> Wire839
  BlockHeight = 0
  BlockLength = 0
  CountBroken = 0
  CountEntire = 0
  Face = 0
  GlobalId = 34dKQn9vP2GQ3oJZbW7CwE
  Height = 2800
  HorizontalArea = 66800
  IfcData = IfcUID=34dKQn9vP2GQ3oJZbW7CwE,+2 more (map truncated)
  IfcType = 166
  Joint = 0
  Length = 6660
  MakeBlocks = false
  Material = -> Material008
  MoveBase = false
  MoveWithHost = false
  Normal = (0,0,0)
  OffsetFirst = 0
  OffsetSecond = 0
  PerimeterLength = 13380
  PredefinedType = 0
  Subtractions = -> [Structure026]
  VerticalArea = 33637000
  Width = 10
FEATURE [Part::FeaturePython] Wall269  label="Штукатурка 10мм 004"  # Arch/BIM 166 (typed FeaturePython)
  Align = 0
  Area = 22148000
  Base = -> Wire840
  BlockHeight = 0
  BlockLength = 0
  CountBroken = 0
  CountEntire = 0
  Face = 0
  GlobalId = 0L504R8CfBD9vh$vQbgFy9
  Height = 2800
  HorizontalArea = 79300
  IfcData = IfcUID=0L504R8CfBD9vh$vQbgFy9,+2 more (map truncated)
  IfcType = 166
  Joint = 0
  Length = 7910
  MakeBlocks = false
  Material = -> Material008
  MoveBase = false
  MoveWithHost = false
  Normal = (0,0,0)
  OffsetFirst = 0
  OffsetSecond = 0
  PerimeterLength = 15880
  PredefinedType = 0
  Subtractions = -> [Structure024]
  VerticalArea = 4.0637e+07
  Width = 10
FEATURE [Part::Part2DObjectPython] Rectangle3317  label="проём вентшахты внешний 001"  # Draft 2D object (typed FeaturePython)
  ChamferSize = 0
  Columns = 1
  FilletRadius = 0
  Height = 1030
  Length = 510
  MakeFace = false
  Placement = pos=(8690,1355,0) rot=(0,0,1;0rad)
  Rows = 1
FEATURE [Part::FeaturePython] Structure384  label="Вентстояк вычитаемы объём 007"  # Arch/BIM 52 (typed FeaturePython)
  Base = -> Rectangle3317
  FaceMaker = 0
  Height = 4000
  HorizontalArea = 525300
  IfcData = complex_attributes={"OwnerHistory": {}, "IsNestedBy": {}, "IsDecomposedBy": {}, "IsDefinedBy": {}, "ObjectPlacement": {}, "Representation":... (+4 chars omitted)
  IfcType = 52
  Length = 0
  MoveBase = false
  MoveWithHost = false
  Nodes = (2) [(8945,1870,0),(8945,1870,4000)]
  NodesOffset = 0
  Normal = (0,0,0)
  PerimeterLength = 3080
  Placement = pos=(0,0,2800) rot=(0,0,1;0rad)
  VerticalArea = 12320000
  Width = 100
FEATURE [Part::Cut] Cut052  label="Кровля габарит_001"
  Base = -> Cut051
  Tool = -> Structure384
FEATURE [Part::Part2DObjectPython] Line1523  label="Перемычки_034"  # Draft 2D object (typed FeaturePython)
  Area = 0
  ChamferSize = 0
  Closed = true
  End = (4185,7505,0)
  FilletRadius = 0
  Length = 2480
  MakeFace = true
  Placement = pos=(1622,7505,0) rot=(0,0,1;0rad)
  Points = (2) [(83,0,0),(2563,0,0)]
  Start = (1705,7505,0)
  Subdivisions = 0
FEATURE [Part::Part2DObjectPython] Line1524  label="Перемычки_035"  # Draft 2D object (typed FeaturePython)
  Area = 0
  ChamferSize = 0
  Closed = true
  End = (6265,7505,0)
  FilletRadius = 0
  Length = 1440
  MakeFace = true
  Placement = pos=(4174,7505,0) rot=(0,0,1;0rad)
  Points = (2) [(651,0,0),(2091,0,0)]
  Start = (4825,7505,0)
  Subdivisions = 0
FEATURE [Part::Part2DObjectPython] Line1526  label="Перемычки_037"  # Draft 2D object (typed FeaturePython)
  Area = 0
  ChamferSize = 0
  Closed = true
  End = (6980,-45,0)
  FilletRadius = 0
  Length = 1570
  MakeFace = true
  Placement = pos=(4825,-45,0) rot=(0,0,1;0rad)
  Points = (2) [(585,0,0),(2155,0,0)]
  Start = (5410,-45,0)
  Subdivisions = 0
FEATURE [Part::Part2DObjectPython] Line1527  label="Перемычки_038"  # Draft 2D object (typed FeaturePython)
  Area = 0
  ChamferSize = 0
  Closed = true
  End = (8475,-45,0)
  FilletRadius = 0
  Length = 1180
  MakeFace = true
  Placement = pos=(6515,-45,0) rot=(0,0,1;0rad)
  Points = (2) [(780,1.13687e-12,0),(1960,1.13687e-12,0)]
  Start = (7295,-45,0)
  Subdivisions = 0
FEATURE [Part::Part2DObjectPython] Line1529  label="Перемычки_039"  # Draft 2D object (typed FeaturePython)
  Area = 0
  ChamferSize = 0
  Closed = true
  End = (12570,1060,0)
  FilletRadius = 0
  Length = 2480
  MakeFace = true
  Placement = pos=(9260,845,0) rot=(0,0,1;0rad)
  Points = (2) [(3310,2695,0),(3310,215,0)]
  Start = (12570,3540,0)
  Subdivisions = 0
FEATURE [Part::Part2DObjectPython] Line1530  label="Перемычки_040"  # Draft 2D object (typed FeaturePython)
  Area = 0
  ChamferSize = 0
  Closed = true
  End = (-50,1580,0)
  FilletRadius = 0
  Length = 1960
  MakeFace = true
  Placement = pos=(-3360,1090,0) rot=(0,0,1;0rad)
  Points = (2) [(3310,2450,0),(3310,490,0)]
  Start = (-50,3540,0)
  Subdivisions = 0
FEATURE [Part::Part2DObjectPython] Line1531  label="Перемычки_041"  # Draft 2D object (typed FeaturePython)
  Area = 0
  ChamferSize = 0
  Closed = true
  End = (12570,3790,0)
  FilletRadius = 0
  Length = 1440
  MakeFace = true
  Placement = pos=(9260,3089,0) rot=(0,0,1;0rad)
  Points = (2) [(3310,2141,0),(3310,701,0)]
  Start = (12570,5230,0)
  Subdivisions = 0
FEATURE [Part::Part2DObjectPython] Line1532  label="Перемычки_042"  # Draft 2D object (typed FeaturePython)
  Area = 0
  ChamferSize = 0
  Closed = true
  End = (5030,3680,0)
  FilletRadius = 0
  Length = 1440
  MakeFace = true
  Placement = pos=(2939,3680,0) rot=(0,0,1;0rad)
  Points = (2) [(651,0,0),(2091,0,0)]
  Start = (3590,3680,0)
  Subdivisions = 0
FEATURE [Part::Part2DObjectPython] Line1533  label="Перемычки_043"  # Draft 2D object (typed FeaturePython)
  Area = 0
  ChamferSize = 0
  Closed = true
  End = (6980,3680,0)
  FilletRadius = 0
  Length = 1440
  MakeFace = true
  Placement = pos=(4889,3680,0) rot=(0,0,1;0rad)
  Points = (2) [(651,0,0),(2091,0,0)]
  Start = (5540,3680,0)
  Subdivisions = 0
FEATURE [Part::Part2DObjectPython] Line1537  label="Перемычки_045"  # Draft 2D object (typed FeaturePython)
  Area = 0
  ChamferSize = 0
  Closed = true
  End = (5095,-45,0)
  FilletRadius = 0
  Length = 1180
  MakeFace = true
  Placement = pos=(3135,-45,0) rot=(0,0,1;0rad)
  Points = (2) [(780,1.13687e-12,0),(1960,1.13687e-12,0)]
  Start = (3915,-45,0)
  Subdivisions = 0
FEATURE [Part::Part2DObjectPython] Line1538  label="Перемычки_046"  # Draft 2D object (typed FeaturePython)
  Area = 0
  ChamferSize = 0
  Closed = true
  End = (10815,7505,0)
  FilletRadius = 0
  Length = 2480
  MakeFace = true
  Placement = pos=(8252,7505,0) rot=(0,0,1;0rad)
  Points = (2) [(83,0,0),(2563,0,0)]
  Start = (8335,7505,0)
  Subdivisions = 0
FEATURE [Part::Part2DObjectPython] Line1540  label="Перемычки_048"  # Draft 2D object (typed FeaturePython)
  Area = 0
  ChamferSize = 0
  Closed = true
  End = (12180,3680,0)
  FilletRadius = 0
  Length = 4040
  MakeFace = true
  Placement = pos=(8057,3680,0) rot=(0,0,1;0rad)
  Points = (2) [(83,0,0),(4123,0,0)]
  Start = (8140,3680,0)
  Subdivisions = 0
FEATURE [Part::FeaturePython] Wall270  label="Перемычка монолитн. 001"  # Arch/BIM 166 (typed FeaturePython)
  Align = 1
  Area = 565440
  Base = -> Line1523
  BlockHeight = 0
  BlockLength = 0
  CountBroken = 0
  CountEntire = 0
  Face = 0
  GlobalId = 2_OOPfC1L9nOo2BwNBJ59E
  Height = 228
  HorizontalArea = 694400
  IfcData = IfcUID=2_OOPfC1L9nOo2BwNBJ59E,+2 more (map truncated)
  IfcType = 166
  Joint = 0
  Length = 2480
  MakeBlocks = false
  Material = -> Material001
  MoveBase = false
  MoveWithHost = false
  Normal = (0,0,0)
  OffsetFirst = 0
  OffsetSecond = 0
  PerimeterLength = 5520
  Placement = pos=(0,0,2572) rot=(0,0,1;0rad)
  PredefinedType = 0
  VerticalArea = 1.25856e+06
  Width = 280
FEATURE [Part::FeaturePython] Wall271  label="Перемычка монолитн. 002"  # Arch/BIM 166 (typed FeaturePython)
  Align = 1
  Area = 328320
  Base = -> Line1524
  BlockHeight = 0
  BlockLength = 0
  CountBroken = 0
  CountEntire = 0
  Face = 0
  GlobalId = 02zZ5o_1DBJf0p5Hr4GWva
  Height = 228
  HorizontalArea = 403200
  IfcData = IfcUID=02zZ5o_1DBJf0p5Hr4GWva,+2 more (map truncated)
  IfcType = 166
  Joint = 0
  Length = 1440
  MakeBlocks = false
  Material = -> Material001
  MoveBase = false
  MoveWithHost = false
  Normal = (0,0,0)
  OffsetFirst = 0
  OffsetSecond = 0
  PerimeterLength = 3440
  Placement = pos=(0,0,2572) rot=(0,0,1;0rad)
  PredefinedType = 0
  VerticalArea = 784320
  Width = 280
FEATURE [Part::FeaturePython] Wall272  label="Перемычка монолитн. 003"  # Arch/BIM 166 (typed FeaturePython)
  Align = 0
  Area = 362670
  Base = -> Line1526
  BlockHeight = 0
  BlockLength = 0
  CountBroken = 0
  CountEntire = 0
  Face = 0
  GlobalId = 2Km2nGMYj6_hkYj1EJr8Pd
  Height = 231
  HorizontalArea = 439600
  IfcData = IfcUID=2Km2nGMYj6_hkYj1EJr8Pd,+2 more (map truncated)
  IfcType = 166
  Joint = 0
  Length = 1570
  MakeBlocks = false
  Material = -> Material001
  MoveBase = false
  MoveWithHost = false
  Normal = (0,0,0)
  OffsetFirst = 0
  OffsetSecond = 0
  PerimeterLength = 3700
  Placement = pos=(0,0,2341) rot=(0,0,1;0rad)
  PredefinedType = 0
  VerticalArea = 854700
  Width = 280
FEATURE [Part::FeaturePython] Wall273  label="Перемычка монолитн. 004"  # Arch/BIM 166 (typed FeaturePython)
  Align = 0
  Area = 272580
  Base = -> Line1527
  BlockHeight = 0
  BlockLength = 0
  CountBroken = 0
  CountEntire = 0
  Face = 0
  GlobalId = 16$DxRw$TB6BfQSNqz60Qz
  Height = 231
  HorizontalArea = 330400
  IfcData = IfcUID=16$DxRw$TB6BfQSNqz60Qz,+2 more (map truncated)
  IfcType = 166
  Joint = 0
  Length = 1180
  MakeBlocks = false
  Material = -> Material001
  MoveBase = false
  MoveWithHost = false
  Normal = (0,0,0)
  OffsetFirst = 0
  OffsetSecond = 0
  PerimeterLength = 2920
  Placement = pos=(0,0,2341) rot=(0,0,1;0rad)
  PredefinedType = 0
  VerticalArea = 674520
  Width = 280
FEATURE [Part::FeaturePython] Wall274  label="Перемычка монолитн. 005"  # Arch/BIM 166 (typed FeaturePython)
  Align = 1
  Area = 565440
  Base = -> Line1529
  BlockHeight = 0
  BlockLength = 0
  CountBroken = 0
  CountEntire = 0
  Face = 0
  GlobalId = 0AqGC86W9B8PvMAPbhOTte
  Height = 228
  HorizontalArea = 694400
  IfcData = IfcUID=0AqGC86W9B8PvMAPbhOTte,+2 more (map truncated)
  IfcType = 166
  Joint = 0
  Length = 2480
  MakeBlocks = false
  Material = -> Material001
  MoveBase = false
  MoveWithHost = false
  Normal = (0,0,0)
  OffsetFirst = 0
  OffsetSecond = 0
  PerimeterLength = 5520
  Placement = pos=(0,0,2572) rot=(0,0,1;0rad)
  PredefinedType = 0
  VerticalArea = 1258560
  Width = 280
FEATURE [Part::FeaturePython] Wall275  label="Перемычка монолитн. 006"  # Arch/BIM 166 (typed FeaturePython)
  Align = 0
  Area = 446880
  Base = -> Line1530
  BlockHeight = 0
  BlockLength = 0
  CountBroken = 0
  CountEntire = 0
  Face = 0
  GlobalId = 23sFNS3FX7B9N2mOSbHlu1
  Height = 228
  HorizontalArea = 548800
  IfcData = IfcUID=23sFNS3FX7B9N2mOSbHlu1,+2 more (map truncated)
  IfcType = 166
  Joint = 0
  Length = 1960
  MakeBlocks = false
  Material = -> Material001
  MoveBase = false
  MoveWithHost = false
  Normal = (0,0,0)
  OffsetFirst = 0
  OffsetSecond = 0
  PerimeterLength = 4480
  Placement = pos=(0,0,2572) rot=(0,0,1;0rad)
  PredefinedType = 0
  VerticalArea = 1021440
  Width = 280
FEATURE [Part::FeaturePython] Wall276  label="Перемычка монолитн. 007"  # Arch/BIM 166 (typed FeaturePython)
  Align = 1
  Area = 328320
  Base = -> Line1531
  BlockHeight = 0
  BlockLength = 0
  CountBroken = 0
  CountEntire = 0
  Face = 0
  GlobalId = 2TdxzIhfb2oA4zfHjvmbo2
  Height = 228
  HorizontalArea = 403200
  IfcData = IfcUID=2TdxzIhfb2oA4zfHjvmbo2,+2 more (map truncated)
  IfcType = 166
  Joint = 0
  Length = 1440
  MakeBlocks = false
  Material = -> Material001
  MoveBase = false
  MoveWithHost = false
  Normal = (0,0,0)
  OffsetFirst = 0
  OffsetSecond = 0
  PerimeterLength = 3440
  Placement = pos=(0,0,2572) rot=(0,0,1;0rad)
  PredefinedType = 0
  VerticalArea = 784320
  Width = 280
FEATURE [Part::FeaturePython] Wall277  label="Перемычка монолитн. 008"  # Arch/BIM 166 (typed FeaturePython)
  Align = 2
  Area = 275040
  Base = -> Line1532
  BlockHeight = 0
  BlockLength = 0
  CountBroken = 0
  CountEntire = 0
  Face = 0
  GlobalId = 0sYYehG3D7NAgPHO$7$lOP
  Height = 191
  HorizontalArea = 360000
  IfcData = IfcUID=0sYYehG3D7NAgPHO$7$lOP,+2 more (map truncated)
  IfcType = 166
  Joint = 0
  Length = 1440
  MakeBlocks = false
  Material = -> Material001
  MoveBase = false
  MoveWithHost = false
  Normal = (0,0,0)
  OffsetFirst = 0
  OffsetSecond = 0
  PerimeterLength = 3380
  Placement = pos=(0,-1.819e-12,2150) rot=(0,0,1;0rad)
  PredefinedType = 0
  VerticalArea = 645580
  Width = 250
FEATURE [Part::FeaturePython] Wall278  label="Перемычка монолитн. 009"  # Arch/BIM 166 (typed FeaturePython)
  Align = 2
  Area = 275040
  Base = -> Line1533
  BlockHeight = 0
  BlockLength = 0
  CountBroken = 0
  CountEntire = 0
  Face = 0
  GlobalId = 0U$bER0DTA2wM7MkZ_5muC
  Height = 191
  HorizontalArea = 360000
  IfcData = IfcUID=0U$bER0DTA2wM7MkZ_5muC,+2 more (map truncated)
  IfcType = 166
  Joint = 0
  Length = 1440
  MakeBlocks = false
  Material = -> Material001
  MoveBase = false
  MoveWithHost = false
  Normal = (0,0,0)
  OffsetFirst = 0
  OffsetSecond = 0
  PerimeterLength = 3380
  Placement = pos=(0,-1.819e-12,2150) rot=(0,0,1;0rad)
  PredefinedType = 0
  VerticalArea = 645580
  Width = 250
FEATURE [Part::FeaturePython] Wall279  label="Перемычка монолитн. 010"  # Arch/BIM 166 (typed FeaturePython)
  Align = 0
  Area = 272580
  Base = -> Line1537
  BlockHeight = 0
  BlockLength = 0
  CountBroken = 0
  CountEntire = 0
  Face = 0
  GlobalId = 2dIW8Z8qb1VQVoHMf0gHj5
  Height = 231
  HorizontalArea = 330400
  IfcData = IfcUID=2dIW8Z8qb1VQVoHMf0gHj5,+2 more (map truncated)
  IfcType = 166
  Joint = 0
  Length = 1180
  MakeBlocks = false
  Material = -> Material001
  MoveBase = false
  MoveWithHost = false
  Normal = (0,0,0)
  OffsetFirst = 0
  OffsetSecond = 0
  PerimeterLength = 2920
  Placement = pos=(0,0,2341) rot=(0,0,1;0rad)
  PredefinedType = 0
  VerticalArea = 674520
  Width = 280
FEATURE [Part::FeaturePython] Wall280  label="Перемычка монолитн. 011"  # Arch/BIM 166 (typed FeaturePython)
  Align = 1
  Area = 565440
  Base = -> Line1538
  BlockHeight = 0
  BlockLength = 0
  CountBroken = 0
  CountEntire = 0
  Face = 0
  GlobalId = 3keULZXVT8QA_IAgUQCOo2
  Height = 228
  HorizontalArea = 694400
  IfcData = IfcUID=3keULZXVT8QA_IAgUQCOo2,+2 more (map truncated)
  IfcType = 166
  Joint = 0
  Length = 2480
  MakeBlocks = false
  Material = -> Material001
  MoveBase = false
  MoveWithHost = false
  Normal = (0,0,0)
  OffsetFirst = 0
  OffsetSecond = 0
  PerimeterLength = 5520
  Placement = pos=(0,-9.09e-13,2572) rot=(0,0,1;0rad)
  PredefinedType = 0
  VerticalArea = 1258560
  Width = 280
FEATURE [Part::FeaturePython] Wall281  label="Перемычка монолитн. 012"  # Arch/BIM 166 (typed FeaturePython)
  Align = 2
  Area = 1212000
  Base = -> Line1540
  BlockHeight = 0
  BlockLength = 0
  CountBroken = 0
  CountEntire = 0
  Face = 0
  GlobalId = 0GYkMrihr4SvLL6ceY8F$x
  Height = 300
  HorizontalArea = 1010000
  IfcData = IfcUID=0GYkMrihr4SvLL6ceY8F$x,+2 more (map truncated)
  IfcType = 166
  Joint = 0
  Length = 4040
  MakeBlocks = false
  Material = -> Material001
  MoveBase = false
  MoveWithHost = false
  Normal = (0,0,0)
  OffsetFirst = 0
  OffsetSecond = 0
  PerimeterLength = 8580
  Placement = pos=(0,-1.819e-12,2500) rot=(0,0,1;0rad)
  PredefinedType = 0
  VerticalArea = 2574000
  Width = 250
FEATURE [Part::FeaturePython] Wall004  label="Стена 250mm 2.1нф+1нф"  # Arch/BIM 166 (typed FeaturePython)
  Align = 2
  Area = 3.786e+07
  Base = -> Line1049
  BlockHeight = 231
  BlockLength = 0
  CountBroken = 0
  CountEntire = 0
  Face = 0
  GlobalId = 1uw9ZyZ5vAkuN6nr$sWkBP
  Height = 3000
  HorizontalArea = 0
  IfcData = IfcUID=1uw9ZyZ5vAkuN6nr$sWkBP; attributes={"GlobalId": {"value": "1uw9ZyZ5vAkuN6nr$sWkBP"}}
  IfcType = 166
  Joint = 0
  Length = 12620
  MakeBlocks = true
  Material = -> Material003
  MoveBase = false
  MoveWithHost = false
  Normal = (0,0,0)
  OffsetFirst = 0
  OffsetSecond = 500
  PerimeterLength = 0
  Placement = pos=(0,0,-200) rot=(0,0,1;0rad)
  PredefinedType = 0
  Subtractions = -> [Structure317,Structure023,Structure020,Wall278,Wall281,Wall277]
  VerticalArea = 0
  Width = 250
FEATURE [App::GeometryPython] BuildingPart088  label="Перемычки монолитные"  # Arch/BIM 52 (typed FeaturePython)
  Area = 5469750
  GlobalId = 3$YVGVb81DNfcCDGoK7nvQ
  Group = -> [Wall270,Wall271,Wall272,Wall273,Wall274,Wall275,Wall276,Wall277,Wall278,Wall279,Wall280,Wall281]
  Height = 0
  HeightPropagate = true
  IfcData = IfcUID=3$YVGVb81DNfcCDGoK7nvQ,+2 more (map truncated)
  IfcType = 52
  LevelOffset = 0
FEATURE [Part::FeaturePython] Wall282  label="Утепление перемычки XPS 100mm 001"  # Arch/BIM 166 (typed FeaturePython)
  Align = 1
  Area = 565440
  Base = -> Line1523
  BlockHeight = 0
  BlockLength = 0
  CountBroken = 0
  CountEntire = 0
  Face = 0
  Height = 228
  HorizontalArea = 248000
  IfcData = attributes={"GlobalId": {"name": "GlobalId", "type": "IfcGloballyUniqueId", "is_enum": false, "enum_values": []}, "Description": {"... (+533 chars omitted),+1 more (map truncated)
  IfcType = 166
  Joint = 0
  Length = 2480
  MakeBlocks = false
  Material = -> Material002
  MoveBase = false
  MoveWithHost = false
  Normal = (0,0,0)
  Offset = 280
  OffsetFirst = 0
  OffsetSecond = 0
  PerimeterLength = 5160
  Placement = pos=(0,0,2572) rot=(0,0,1;0rad)
  PredefinedType = 0
  VerticalArea = 1.17648e+06
  Width = 100
FEATURE [Part::FeaturePython] Wall283  label="Утепление перемычки XPS 100mm 025"  # Arch/BIM 166 (typed FeaturePython)
  Align = 0
  Area = 269040
  Base = -> Line1537
  BlockHeight = 0
  BlockLength = 0
  CountBroken = 0
  CountEntire = 0
  Face = 0
  Height = 228
  HorizontalArea = 118000
  IfcData = attributes={"GlobalId": {"name": "GlobalId", "type": "IfcGloballyUniqueId", "is_enum": false, "enum_values": []}, "Description": {"... (+533 chars omitted),+1 more (map truncated)
  IfcType = 166
  Joint = 0
  Length = 1180
  MakeBlocks = false
  Material = -> Material002
  MoveBase = false
  MoveWithHost = false
  Normal = (0,0,0)
  Offset = 280
  OffsetFirst = 0
  OffsetSecond = 0
  PerimeterLength = 2560
  Placement = pos=(0,0,2341) rot=(0,0,1;0rad)
  PredefinedType = 0
  VerticalArea = 583680
  Width = 100
FEATURE [Part::FeaturePython] Wall284  label="Утепление перемычки XPS 100mm 026"  # Arch/BIM 166 (typed FeaturePython)
  Align = 1
  Area = 328320
  Base = -> Line1524
  BlockHeight = 0
  BlockLength = 0
  CountBroken = 0
  CountEntire = 0
  Face = 0
  Height = 228
  HorizontalArea = 144000
  IfcData = attributes={"GlobalId": {"name": "GlobalId", "type": "IfcGloballyUniqueId", "is_enum": false, "enum_values": []}, "Description": {"... (+533 chars omitted),+1 more (map truncated)
  IfcType = 166
  Joint = 0
  Length = 1440
  MakeBlocks = false
  Material = -> Material002
  MoveBase = false
  MoveWithHost = false
  Normal = (0,0,0)
  Offset = 280
  OffsetFirst = 0
  OffsetSecond = 0
  PerimeterLength = 3080
  Placement = pos=(0,0,2572) rot=(0,0,1;0rad)
  PredefinedType = 0
  VerticalArea = 702240
  Width = 100
FEATURE [Part::FeaturePython] Wall285  label="Утепление перемычки XPS 100mm 027"  # Arch/BIM 166 (typed FeaturePython)
  Align = 0
  Area = 446880
  Base = -> Line1530
  BlockHeight = 0
  BlockLength = 0
  CountBroken = 0
  CountEntire = 0
  Face = 0
  Height = 228
  HorizontalArea = 196000
  IfcData = attributes={"GlobalId": {"name": "GlobalId", "type": "IfcGloballyUniqueId", "is_enum": false, "enum_values": []}, "Description": {"... (+533 chars omitted),+1 more (map truncated)
  IfcType = 166
  Joint = 0
  Length = 1960
  MakeBlocks = false
  Material = -> Material002
  MoveBase = false
  MoveWithHost = false
  Normal = (0,0,0)
  Offset = 280
  OffsetFirst = 0
  OffsetSecond = 0
  PerimeterLength = 4120
  Placement = pos=(0,0,2572) rot=(0,0,1;0rad)
  PredefinedType = 0
  VerticalArea = 939360
  Width = 100
FEATURE [Part::FeaturePython] Wall286  label="Утепление перемычки XPS 100mm 028"  # Arch/BIM 166 (typed FeaturePython)
  Align = 0
  Area = 269040
  Base = -> Line1527
  BlockHeight = 0
  BlockLength = 0
  CountBroken = 0
  CountEntire = 0
  Face = 0
  Height = 228
  HorizontalArea = 118000
  IfcData = attributes={"GlobalId": {"name": "GlobalId", "type": "IfcGloballyUniqueId", "is_enum": false, "enum_values": []}, "Description": {"... (+533 chars omitted),+1 more (map truncated)
  IfcType = 166
  Joint = 0
  Length = 1180
  MakeBlocks = false
  Material = -> Material002
  MoveBase = false
  MoveWithHost = false
  Normal = (0,0,0)
  Offset = 280
  OffsetFirst = 0
  OffsetSecond = 0
  PerimeterLength = 2560
  Placement = pos=(0,0,2341) rot=(0,0,1;0rad)
  PredefinedType = 0
  VerticalArea = 583680
  Width = 100
FEATURE [Part::FeaturePython] Wall287  label="Утепление перемычки XPS 100mm 029"  # Arch/BIM 166 (typed FeaturePython)
  Align = 1
  Area = 565440
  Base = -> Line1538
  BlockHeight = 0
  BlockLength = 0
  CountBroken = 0
  CountEntire = 0
  Face = 0
  Height = 228
  HorizontalArea = 248000
  IfcData = attributes={"GlobalId": {"name": "GlobalId", "type": "IfcGloballyUniqueId", "is_enum": false, "enum_values": []}, "Description": {"... (+533 chars omitted),+1 more (map truncated)
  IfcType = 166
  Joint = 0
  Length = 2480
  MakeBlocks = false
  Material = -> Material002
  MoveBase = false
  MoveWithHost = false
  Normal = (0,0,0)
  Offset = 280
  OffsetFirst = 0
  OffsetSecond = 0
  PerimeterLength = 5160
  Placement = pos=(0,-9.09e-13,2572) rot=(0,0,1;0rad)
  PredefinedType = 0
  VerticalArea = 1176480
  Width = 100
FEATURE [Part::FeaturePython] Wall288  label="Утепление перемычки XPS 100mm 030"  # Arch/BIM 166 (typed FeaturePython)
  Align = 0
  Area = 357960
  Base = -> Line1526
  BlockHeight = 0
  BlockLength = 0
  CountBroken = 0
  CountEntire = 0
  Face = 0
  Height = 228
  HorizontalArea = 157000
  IfcData = attributes={"GlobalId": {"name": "GlobalId", "type": "IfcGloballyUniqueId", "is_enum": false, "enum_values": []}, "Description": {"... (+533 chars omitted),+1 more (map truncated)
  IfcType = 166
  Joint = 0
  Length = 1570
  MakeBlocks = false
  Material = -> Material002
  MoveBase = false
  MoveWithHost = false
  Normal = (0,0,0)
  Offset = 280
  OffsetFirst = 0
  OffsetSecond = 0
  PerimeterLength = 3340
  Placement = pos=(0,0,2341) rot=(0,0,1;0rad)
  PredefinedType = 0
  VerticalArea = 761520
  Width = 100
FEATURE [Part::FeaturePython] Wall289  label="Утепление перемычки XPS 100mm 031"  # Arch/BIM 166 (typed FeaturePython)
  Align = 1
  Area = 565440
  Base = -> Line1529
  BlockHeight = 0
  BlockLength = 0
  CountBroken = 0
  CountEntire = 0
  Face = 0
  Height = 228
  HorizontalArea = 248000
  IfcData = attributes={"GlobalId": {"name": "GlobalId", "type": "IfcGloballyUniqueId", "is_enum": false, "enum_values": []}, "Description": {"... (+533 chars omitted),+1 more (map truncated)
  IfcType = 166
  Joint = 0
  Length = 2480
  MakeBlocks = false
  Material = -> Material002
  MoveBase = false
  MoveWithHost = false
  Normal = (0,0,0)
  Offset = 280
  OffsetFirst = 0
  OffsetSecond = 0
  PerimeterLength = 5160
  Placement = pos=(0,0,2572) rot=(0,0,1;0rad)
  PredefinedType = 0
  VerticalArea = 1176480
  Width = 100
FEATURE [Part::FeaturePython] Wall290  label="Утепление перемычки XPS 100mm 032"  # Arch/BIM 166 (typed FeaturePython)
  Align = 1
  Area = 328320
  Base = -> Line1531
  BlockHeight = 0
  BlockLength = 0
  CountBroken = 0
  CountEntire = 0
  Face = 0
  Height = 228
  HorizontalArea = 144000
  IfcData = attributes={"GlobalId": {"name": "GlobalId", "type": "IfcGloballyUniqueId", "is_enum": false, "enum_values": []}, "Description": {"... (+533 chars omitted),+1 more (map truncated)
  IfcType = 166
  Joint = 0
  Length = 1440
  MakeBlocks = false
  Material = -> Material002
  MoveBase = false
  MoveWithHost = false
  Normal = (0,0,0)
  Offset = 280
  OffsetFirst = 0
  OffsetSecond = 0
  PerimeterLength = 3080
  Placement = pos=(0,0,2572) rot=(0,0,1;0rad)
  PredefinedType = 0
  VerticalArea = 702240
  Width = 100
FEATURE [App::GeometryPython] BuildingPart089  label="Утепление перемычек XPS 100mm"  # Arch/BIM 52 (typed FeaturePython)
  Area = 3695880
  GlobalId = 1IqJZ7MUv7eQPyUTFsu7$l
  Group = -> [Wall282,Wall283,Wall284,Wall285,Wall286,Wall287,Wall288,Wall289,Wall290]
  Height = 0
  HeightPropagate = true
  IfcData = IfcUID=1IqJZ7MUv7eQPyUTFsu7$l,+2 more (map truncated)
  IfcType = 52
  LevelOffset = 0
FEATURE [TechDraw::DrawSVGTemplate] Template002
  EditableTexts = Лист=4; Номер=ИЖС-2021.0001
  Height = 297
  Orientation = 1
  Width = 420
FEATURE [App::FeaturePython] Dimension026  # Draft dimension (typed FeaturePython)
  Diameter = false
  Dimline = (5200,6300,0)
  Direction = (0,0,0)
  Distance = 110
  End = (4930,7485,0)
  Normal = (0,0,1)
  Start = (4820,7485,0)
FEATURE [App::FeaturePython] Dimension027  # Draft dimension (typed FeaturePython)
  Diameter = false
  Dimline = (8300,3000,0)
  Direction = (0,0,0)
  Distance = 1150
  End = (7910,3535,0)
  Normal = (0,0,1)
  Start = (7910,2385,0)
FEATURE [Part::Part2DObjectPython] Rectangle3323  # Draft 2D object (typed FeaturePython)
  Area = 0
  ChamferSize = 0
  Columns = 1
  FilletRadius = 0
  Height = 250
  Length = 920
  MakeFace = false
  Placement = pos=(6940,6068.61,0) rot=(0,0,1;0rad)
  Rows = 1
FEATURE [Part::Part2DObjectPython] Rectangle3324  # Draft 2D object (typed FeaturePython)
  Area = 0
  ChamferSize = 0
  Columns = 1
  FilletRadius = 0
  Height = 250
  Length = 920
  MakeFace = false
  Placement = pos=(6940,5818.61,0) rot=(0,0,1;0rad)
  Rows = 1
FEATURE [Part::Part2DObjectPython] Rectangle3325  # Draft 2D object (typed FeaturePython)
  Area = 0
  ChamferSize = 0
  Columns = 1
  FilletRadius = 0
  Height = 250
  Length = 920
  MakeFace = false
  Placement = pos=(6940,5568.61,0) rot=(0,0,1;0rad)
  Rows = 1
FEATURE [Part::FeaturePython] Stairs003  # Arch/BIM 128 (typed FeaturePython)
  AbsTop = (0,0,2208)
  Align = 0
  BlondelRatio = 0
  Flight = 0
  GlobalId = 3uneSe57LCqfWUoFMYeGFv
  Height = 3000
  HorizontalArea = 0
  IfcData = IfcUID=3uneSe57LCqfWUoFMYeGFv,+2 more (map truncated)
  IfcType = 128
  LandingDepth = 0
  Landings = 0
  Length = 4500
  Material = -> Material001
  MoveBase = false
  MoveWithHost = false
  Nosing = 20
  NumberOfSteps = 12
  OutlineLeft = (2) [(0,-60,1044),(2750,-60,3068)]
  OutlineLeftAll = (2) [(0,-60,1044),(2750,-60,3068)]
  OutlineRight = (2) [(2750,-860,3068),(0,-860,1044)]
  OutlineRightAll = (2) [(2750,-860,3068),(0,-860,1044)]
  PerimeterLength = 0
  Placement = pos=(7860,6298.61,1104) rot=(0,0,-1;1.5708rad)
  PredefinedType = 0
  RailingHeightLeft = 900
  RailingHeightRight = 900
  RailingLeft = Rail
  RailingOffsetLeft = 60
  RailingOffsetRight = 60
  RailingRight = Rail001
  RiserHeight = 184
  RiserHeightEnforce = 184
  RiserThickness = 0
  StringerOverlap = 0
  StringerWidth = 100
  Structure = 1
  StructureOffset = 0
  StructureThickness = 80
  TreadDepth = 250
  TreadDepthEnforce = 250
  TreadThickness = 40
  VerticalArea = 0
  Width = 920
  Winders = 0
FEATURE [Part::Part2DObjectPython] Line1552  # Draft 2D object (typed FeaturePython)
  Area = 0
  ChamferSize = 0
  Closed = true
  End = (7390,7020,0)
  FilletRadius = 0
  Length = 1010
  MakeFace = false
  Placement = pos=(8400,7020,0) rot=(1,0,0;3.14159rad)
  Points = (2) [(0,0,0),(-1010,0,0)]
  Start = (8400,7020,0)
  Subdivisions = 0
FEATURE [Part::Part2DObjectPython] Line1553  # Draft 2D object (typed FeaturePython)
  Area = 0
  ChamferSize = 0
  Closed = false
  End = (7390,7020,0)
  FilletRadius = 0
  Length = 3210
  MakeFace = false
  Placement = pos=(7390,3810,0) rot=(0,0,1;0rad)
  Points = (2) [(0,0,0),(0,3210,0)]
  Start = (7390,3810,0)
  Subdivisions = 0
FEATURE [Part::Part2DObjectPython] Arc  # Draft 2D object (typed FeaturePython)
  Area = 0
  FirstAngle = 90
  LastAngle = 180
  MakeFace = false
  Placement = pos=(7840,6570,0) rot=(0,0,1;0rad)
  Radius = 450
FEATURE [Part::Part2DObjectPython] Rectangle3331  # Draft 2D object (typed FeaturePython)
  Area = 0
  ChamferSize = 0
  Columns = 1
  FilletRadius = 0
  Height = 50
  Length = 50
  MakeFace = false
  Placement = pos=(7840,6520,0) rot=(0,0,1;0rad)
  Rows = 1
FEATURE [Part::Part2DObjectPython] Line1554  # Draft 2D object (typed FeaturePython)
  Area = 0
  ChamferSize = 0
  Closed = false
  End = (6940,7470,0)
  FilletRadius = 0
  Length = 1272.79
  MakeFace = false
  Placement = pos=(7840,6570,0) rot=(0,0,1;0rad)
  Points = (2) [(0,0,0),(-900,900,0)]
  Start = (7840,6570,0)
  Subdivisions = 0
FEATURE [Part::Part2DObjectPython] Circle  # Draft 2D object (typed FeaturePython)
  Area = 0
  FirstAngle = 0
  LastAngle = 0
  MakeFace = false
  Placement = pos=(7521.8,6888.2,0) rot=(0,0,1;0rad)
  Radius = 125
FEATURE [Part::Part2DObjectPython] Line1556  # Draft 2D object (typed FeaturePython)
  Area = 0
  ChamferSize = 0
  Closed = false
  End = (7610.19,6976.59,0)
  FilletRadius = 0
  Length = 250
  MakeFace = false
  Placement = pos=(7433.41,6799.81,0) rot=(0,0,1;0rad)
  Points = (2) [(0,0,0),(176.777,176.777,0)]
  Start = (7433.41,6799.81,0)
  Subdivisions = 0
FEATURE [Part::Part2DObjectPython] Arc126  label="Arc127"  # Draft 2D object (typed FeaturePython)
  Area = 0
  FirstAngle = -1.84921
  LastAngle = 26.749
  MakeFace = false
  Placement = pos=(7610.19,6976.59,0) rot=(0,0,1;0rad)
  Radius = 250
FEATURE [Part::Part2DObjectPython] Line1557  # Draft 2D object (typed FeaturePython)
  Area = 0
  ChamferSize = 0
  Closed = false
  End = (7856.39,7020,0)
  FilletRadius = 0
  Length = 250
  MakeFace = false
  Placement = pos=(7610.19,6976.59,0) rot=(0,0,1;0rad)
  Points = (2) [(0,0,0),(246.202,43.4136,0)]
  Start = (7610.19,6976.59,0)
  Subdivisions = 0
FEATURE [Part::Part2DObjectPython] Arc127  label="Arc128"  # Draft 2D object (typed FeaturePython)
  Area = 0
  FirstAngle = -123.355
  LastAngle = -87.0616
  MakeFace = false
  Placement = pos=(7433.41,6799.81,0) rot=(0,0,1;0rad)
  Radius = 250
FEATURE [Part::Part2DObjectPython] Line1558  # Draft 2D object (typed FeaturePython)
  Area = 0
  ChamferSize = 0
  Closed = false
  End = (7433.41,6799.81,0)
  FilletRadius = 0
  Length = 250
  MakeFace = false
  Placement = pos=(7390,6553.61,0) rot=(0,0,1;0rad)
  Points = (2) [(0,0,0),(43.4136,246.202,0)]
  Start = (7390,6553.61,0)
  Subdivisions = 0
FEATURE [Part::Part2DObjectPython] Rectangle3332  # Draft 2D object (typed FeaturePython)
  Area = 0
  ChamferSize = 0
  Columns = 1
  FilletRadius = 0
  Height = 100
  Length = 100
  MakeFace = false
  Placement = pos=(7840,6470,0) rot=(0,0,1;0rad)
  Rows = 1
FEATURE [Part::Part2DObjectPython] Line1564  # Draft 2D object (typed FeaturePython)
  Area = 0
  ChamferSize = 0
  Closed = false
  End = (7714.57,7952.96,0)
  FilletRadius = 0
  Length = 1500
  MakeFace = false
  Placement = pos=(7940,6470,0) rot=(0,0,1;0rad)
  Points = (2) [(0,0,0),(-225.432,1482.96,0)]
  Start = (7940,6470,0)
  Subdivisions = 0
FEATURE [Part::Part2DObjectPython] Line1565  # Draft 2D object (typed FeaturePython)
  Area = 0
  ChamferSize = 0
  Closed = false
  End = (7121.6,7727.07,0)
  FilletRadius = 0
  Length = 1500
  MakeFace = false
  Placement = pos=(7940,6470,0) rot=(0,0,1;0rad)
  Points = (2) [(0,0,0),(-818.404,1257.07,0)]
  Start = (7940,6470,0)
  Subdivisions = 0
FEATURE [Part::Part2DObjectPython] Line1566  # Draft 2D object (typed FeaturePython)
  Area = 0
  ChamferSize = 0
  Closed = false
  End = (6682.93,7288.4,0)
  FilletRadius = 0
  Length = 1500
  MakeFace = false
  Placement = pos=(7940,6470,0) rot=(0,0,1;0rad)
  Points = (2) [(0,0,0),(-1257.07,818.404,0)]
  Start = (7940,6470,0)
  Subdivisions = 0
FEATURE [Part::Part2DObjectPython] Line1567  # Draft 2D object (typed FeaturePython)
  Area = 0
  ChamferSize = 0
  Closed = false
  End = (6457.04,6695.43,0)
  FilletRadius = 0
  Length = 1500
  MakeFace = false
  Placement = pos=(7940,6470,0) rot=(0,0,1;0rad)
  Points = (2) [(0,0,0),(-1482.96,225.432,0)]
  Start = (7940,6470,0)
  Subdivisions = 0
FEATURE [Part::Part2DObjectPython] Rectangle3333  # Draft 2D object (typed FeaturePython)
  Area = 0
  ChamferSize = 0
  Columns = 1
  FilletRadius = 0
  Height = 900
  Length = 250
  MakeFace = false
  Placement = pos=(7856.39,6570,0) rot=(0,0,1;0rad)
  Rows = 1
FEATURE [Part::Part2DObjectPython] Rectangle3334  # Draft 2D object (typed FeaturePython)
  Area = 0
  ChamferSize = 0
  Columns = 1
  FilletRadius = 0
  Height = 250
  Length = 900
  MakeFace = false
  Placement = pos=(6940,6303.61,0) rot=(0,0,1;0rad)
  Rows = 1
FEATURE [Part::Part2DObjectPython] Rectangle3335  # Draft 2D object (typed FeaturePython)
  Area = 0
  ChamferSize = 0
  Columns = 1
  FilletRadius = 0
  Height = 900
  Length = 250
  MakeFace = false
  Placement = pos=(8106.39,6570,0) rot=(0,0,1;0rad)
  Rows = 1
FEATURE [Part::Part2DObjectPython] Rectangle3336  # Draft 2D object (typed FeaturePython)
  Area = 0
  ChamferSize = 0
  Columns = 1
  FilletRadius = 0
  Height = 250
  Length = 900
  MakeFace = false
  Placement = pos=(6940,6053.61,0) rot=(0,0,1;0rad)
  Rows = 1
FEATURE [Part::Part2DObjectPython] Line1568  # Draft 2D object (typed FeaturePython)
  Area = 0
  ChamferSize = 0
  Closed = false
  End = (6940,7470,0)
  FilletRadius = 0
  Length = 1416.39
  MakeFace = false
  Placement = pos=(8356.39,7470,0) rot=(0,0,1;0rad)
  Points = (2) [(0,0,0),(-1416.39,0,0)]
  Start = (8356.39,7470,0)
  Subdivisions = 0
FEATURE [Part::Part2DObjectPython] Line1569  # Draft 2D object (typed FeaturePython)
  Area = 0
  ChamferSize = 0
  Closed = false
  End = (6940,7470,0)
  FilletRadius = 0
  Length = 1416.39
  MakeFace = false
  Placement = pos=(6940,6053.61,0) rot=(0,0,1;0rad)
  Points = (2) [(0,0,0),(0,1416.39,0)]
  Start = (6940,6053.61,0)
  Subdivisions = 0
FEATURE [Part::Part2DObjectPython] Line1570  # Draft 2D object (typed FeaturePython)
  Area = 0
  ChamferSize = 0
  Closed = false
  End = (7874.9,6570,0)
  FilletRadius = 0
  Length = 49.3499
  MakeFace = false
  Placement = pos=(7840,6535.1,0) rot=(0,0,1;0rad)
  Points = (2) [(0,0,0),(34.8957,34.8957,0)]
  Start = (7840,6535.1,0)
  Subdivisions = 0
FEATURE [Part::Part2DObjectPython] Wire856  # Draft 2D object (typed FeaturePython)
  Area = 0
  ChamferSize = 0
  Closed = false
  End = (7840,6303.61,0)
  FilletRadius = 0
  Length = 1410.34
  MakeFace = false
  Placement = pos=(6940,6303.61,0) rot=(0,0,1;0rad)
  Points = (4) [(0,0,0),(0,318.407,0),(900,181.593,0),(900,0,0)]
  Start = (6940,6303.61,0)
  Subdivisions = 0
FEATURE [Part::Part2DObjectPython] Rectangle3337  # Draft 2D object (typed FeaturePython)
  Area = 0
  ChamferSize = 0
  Columns = 1
  FilletRadius = 0
  Height = 20
  Length = 899.99
  MakeFace = false
  Placement = pos=(6940,6283.61,0) rot=(0,0,1;0rad)
  Rows = 1
FEATURE [Part::Part2DObjectPython] Rectangle3338  # Draft 2D object (typed FeaturePython)
  Area = 0
  ChamferSize = 0
  Columns = 1
  FilletRadius = 0
  Height = 900
  Length = 250
  MakeFace = false
  Placement = pos=(8106.4,6585,0) rot=(0,0,1;0rad)
  Rows = 1
FEATURE [Part::Part2DObjectPython] Rectangle3339  # Draft 2D object (typed FeaturePython)
  Area = 0
  ChamferSize = 0
  Columns = 1
  FilletRadius = 0
  Height = 900
  Length = 20
  MakeFace = false
  Placement = pos=(8086.39,6570,0) rot=(0,0,1;0rad)
  Rows = 1
FEATURE [Part::Part2DObjectPython] Line1571  # Draft 2D object (typed FeaturePython)
  Area = 0
  ChamferSize = 0
  Closed = false
  End = (7824.35,7230.77,0)
  FilletRadius = 0
  Length = 20
  MakeFace = false
  Placement = pos=(7804.58,7227.77,0) rot=(0,0,1;0rad)
  Points = (2) [(0,0,0),(19.7728,3.00576,0)]
  Start = (7804.58,7227.77,0)
  Subdivisions = 0
FEATURE [Part::Part2DObjectPython] Line1572  # Draft 2D object (typed FeaturePython)
  Area = 0
  ChamferSize = 0
  Closed = false
  End = (7469.57,7192.58,0)
  FilletRadius = 0
  Length = 20
  MakeFace = false
  Placement = pos=(7452.81,7181.67,0) rot=(0,0,1;0rad)
  Points = (2) [(0,0,0),(16.7609,10.9121,0)]
  Start = (7452.81,7181.67,0)
  Subdivisions = 0
FEATURE [Part::Part2DObjectPython] Line1573  # Draft 2D object (typed FeaturePython)
  Area = 0
  ChamferSize = 0
  Closed = false
  End = (7191.99,6956.99,0)
  FilletRadius = 0
  Length = 20
  MakeFace = false
  Placement = pos=(7181.07,6940.23,0) rot=(0,0,1;0rad)
  Points = (2) [(0,0,0),(10.9121,16.7609,0)]
  Start = (7181.07,6940.23,0)
  Subdivisions = 0
FEATURE [Part::Part2DObjectPython] Line1574  # Draft 2D object (typed FeaturePython)
  Area = 0
  ChamferSize = 0
  Closed = false
  End = (7110.88,6596.04,0)
  FilletRadius = 0
  Length = 20
  MakeFace = false
  Placement = pos=(7107.87,6576.27,0) rot=(0,0,1;0rad)
  Points = (2) [(0,0,0),(3.00576,19.7728,0)]
  Start = (7107.87,6576.27,0)
  Subdivisions = 0
FEATURE [Part::Part2DObjectPython] Line1575  # Draft 2D object (typed FeaturePython)
  Area = 0
  ChamferSize = 0
  Closed = false
  End = (6454.03,6675.66,0)
  FilletRadius = 0
  Length = 1500
  MakeFace = false
  Placement = pos=(7936.99,6450.23,0) rot=(0,0,1;0rad)
  Points = (2) [(0,0,0),(-1482.96,225.432,0)]
  Start = (7936.99,6450.23,0)
  Subdivisions = 0
FEATURE [Part::Part2DObjectPython] Line1576  # Draft 2D object (typed FeaturePython)
  Area = 0
  ChamferSize = 0
  Closed = false
  End = (6672.02,7271.64,0)
  FilletRadius = 0
  Length = 1500
  MakeFace = false
  Placement = pos=(7929.09,6453.24,0) rot=(0,0,1;0rad)
  Points = (2) [(0,0,0),(-1257.07,818.404,0)]
  Start = (7929.09,6453.24,0)
  Subdivisions = 0
FEATURE [Part::Part2DObjectPython] Line1577  # Draft 2D object (typed FeaturePython)
  Area = 0
  ChamferSize = 0
  Closed = false
  End = (7104.83,7716.15,0)
  FilletRadius = 0
  Length = 1500
  MakeFace = false
  Placement = pos=(7923.24,6459.09,0) rot=(0,0,1;0rad)
  Points = (2) [(0,0,0),(-818.404,1257.07,0)]
  Start = (7923.24,6459.09,0)
  Subdivisions = 0
FEATURE [Part::Part2DObjectPython] Line1578  # Draft 2D object (typed FeaturePython)
  Area = 0
  ChamferSize = 0
  Closed = false
  End = (7694.8,7949.96,0)
  FilletRadius = 0
  Length = 1500
  MakeFace = false
  Placement = pos=(7920.23,6466.99,0) rot=(0,0,1;0rad)
  Points = (2) [(0,0,0),(-225.432,1482.96,0)]
  Start = (7920.23,6466.99,0)
  Subdivisions = 0
FEATURE [App::DocumentObjectGroup] Group  label="Лестница построение"
  Group = -> [Line1578,Line1577,Line1576,Line1575,Rectangle3339,Rectangle3335,Rectangle3336,Line1566,Line1569,Line1554,Line1568,Line1565,Line1564,Rectangle3333,Rectangle3334,Rectangle3337,Line1553,Line1552,Circle,Arc127,Line1574,Line1573,Line1572,Line1571,Arc,Arc126,Line1557,Line1556,Line1558,Rectangle3332,Line1567,Rectangle3331,Line1570,Rectangle3338,Wire856]
FEATURE [Part::Part2DObjectPython] Wire857  # Draft 2D object (typed FeaturePython)
  Area = 231189
  ChamferSize = 0
  Closed = true
  End = (7860,6298.61,0)
  FilletRadius = 0
  Length = 2353.16
  MakeFace = true
  Placement = pos=(6960.01,6298.61,0) rot=(0,0,1;0rad)
  Points = (4) [(-20.01,-0.000129917,0),(-20.01,321.217,0),(900,181.364,0),(899.99,0,0)]
  Start = (6940,6298.61,0)
  Subdivisions = 0
FEATURE [Part::Part2DObjectPython] Wire858  # Draft 2D object (typed FeaturePython)
  Area = 253761
  ChamferSize = 0
  Closed = true
  End = (7860.01,6479.97,0)
  FilletRadius = 0
  Length = 2580.03
  MakeFace = true
  Placement = pos=(6960.01,6616.78,0) rot=(0,0,1;0rad)
  Points = (4) [(-20.01,3.04034,0),(-20.01,508.421,0),(900,-90.5456,0),(900,-136.813,0)]
  Start = (6940,6619.83,0)
  Subdivisions = 0
FEATURE [Part::Part2DObjectPython] Wire859  # Draft 2D object (typed FeaturePython)
  Area = 353236
  ChamferSize = 0
  Closed = true
  End = (7860.01,6550.1,0)
  FilletRadius = 0
  Length = 2946.66
  MakeFace = true
  Placement = pos=(7860.01,6526.24,0) rot=(0,0,1;0rad)
  Points = (6) [(0,0,0),(-920.01,598.96,0),(-920.01,958.761,0),(-574.908,958.761,0),(20.4411,44.3062,0),(0,23.8651,0)]
  Start = (7860.01,6526.24,0)
  Subdivisions = 0
FEATURE [Part::Part2DObjectPython] Wire860  # Draft 2D object (typed FeaturePython)
  Area = 250464
  ChamferSize = 0
  Closed = true
  End = (7894.91,6585,0)
  FilletRadius = 0
  Length = 2554.3
  MakeFace = true
  Placement = pos=(7880.45,6570.55,0) rot=(0,0,1;0rad)
  Points = (5) [(0,0,0),(-595.35,914.455,0),(-92.6855,914.455,0),(44.1277,14.4546,0),(14.4546,14.4546,0)]
  Start = (7880.45,6570.55,0)
  Subdivisions = 0
FEATURE [Part::Part2DObjectPython] Wire861  # Draft 2D object (typed FeaturePython)
  Area = 225207
  ChamferSize = 0
  Closed = true
  End = (8106.4,6585,0)
  FilletRadius = 0
  Length = 2310.8
  MakeFace = true
  Placement = pos=(7924.58,6585,0) rot=(0,0,1;0rad)
  Points = (4) [(0,0,0),(-136.813,900,0),(181.823,900,0),(181.823,0,0)]
  Start = (7924.58,6585,0)
  Subdivisions = 0
FEATURE [Part::Part2DObjectPython] Wire862  # Draft 2D object (typed FeaturePython)
  Area = 0
  ChamferSize = 0
  Closed = true
  End = (7859.99,6298.61,0)
  FilletRadius = 0
  Length = 2393.6
  MakeFace = false
  Placement = pos=(6960,6298.61,0) rot=(0,0,1;0rad)
  Points = (4) [(-20,-0.000129917,0),(-20,341.447,0),(900,201.593,0),(899.99,0,0)]
  Start = (6940,6298.61,0)
  Subdivisions = 0
FEATURE [Part::Part2DObjectPython] Wire863  # Draft 2D object (typed FeaturePython)
  Area = 0
  ChamferSize = 0
  Closed = true
  End = (7860,6479.97,0)
  FilletRadius = 0
  Length = 2627.74
  MakeFace = false
  Placement = pos=(6960,6616.78,0) rot=(0,0,1;0rad)
  Points = (4) [(-20,3.04034,0),(-20,532.28,0),(900,-66.6805,0),(900,-136.813,0)]
  Start = (6940,6619.83,0)
  Subdivisions = 0
FEATURE [Part::Part2DObjectPython] Wire864  # Draft 2D object (typed FeaturePython)
  Area = 0
  ChamferSize = 0
  Closed = true
  End = (7860,6526.24,0)
  FilletRadius = 0
  Length = 2973.7
  MakeFace = false
  Placement = pos=(6960,7112.18,0) rot=(0,0,1;0rad)
  Points = (6) [(-20,13.021,0),(-20,372.822,0),(348.957,372.822,0),(934.896,-527.178,0),(900,-562.074,0),(900,-585.939,0)]
  Start = (6940,7125.2,0)
  Subdivisions = 0
FEATURE [Part::Part2DObjectPython] Wire865  # Draft 2D object (typed FeaturePython)
  Area = 0
  ChamferSize = 0
  Closed = true
  End = (7880.44,6570.55,0)
  FilletRadius = 0
  Length = 2594.76
  MakeFace = false
  Placement = pos=(7285.09,7485,0) rot=(0,0,1;0rad)
  Points = (5) [(0,0,0),(522.894,0,0),(659.707,-900,0),(609.804,-900,0),(595.35,-914.455,0)]
  Start = (7285.09,7485,0)
  Subdivisions = 0
FEATURE [Part::Part2DObjectPython] Wire866  # Draft 2D object (typed FeaturePython)
  Area = 0
  ChamferSize = 0
  Closed = true
  End = (7924.57,6585,0)
  FilletRadius = 0
  Length = 2350.8
  MakeFace = false
  Placement = pos=(7787.76,7485,0) rot=(0,0,1;0rad)
  Points = (4) [(0,0,0),(338.636,0,0),(338.636,-900,0),(136.813,-900,0)]
  Start = (7787.76,7485,0)
  Subdivisions = 0
FEATURE [Part::Part2DObjectPython] Rectangle3340  # Draft 2D object (typed FeaturePython)
  Area = 0
  ChamferSize = 0
  Columns = 1
  FilletRadius = 0
  Height = 900
  Length = 270
  MakeFace = false
  Placement = pos=(8106.39,6585,0) rot=(0,0,1;0rad)
  Rows = 1
FEATURE [Part::Part2DObjectPython] Rectangle3341  # Draft 2D object (typed FeaturePython)
  Area = 0
  ChamferSize = 0
  Columns = 1
  FilletRadius = 0
  Height = 189.696
  Length = 920
  MakeFace = false
  Placement = pos=(6940,6108.91,0) rot=(0,0,1;0rad)
  Rows = 1
FEATURE [Part::Part2DObjectPython] Wire869  # Draft 2D object (typed FeaturePython)
  Area = 0
  ChamferSize = 0
  Closed = false
  End = (12159,3610.73,2729.47)
  FilletRadius = 0
  Length = 1079.31
  MakeFace = true
  Placement = pos=(0,20,0) rot=(0,0,1;0rad)
  Points = (7) [(12172.2,3610.53,2749.27),(12170,3564,2795.8),(12167.8,3564,2524),(12165.6,3766,2524),(12163.4,3766,2776),(12161.2,3544.2,2776),+1 more]
  Start = (12172.2,3630.53,2749.27)
  Subdivisions = 0
  Support = -> [Wall281]
FEATURE [Part::FeaturePython] Rebar  label="Stirrup"  # Arch/BIM 110 (typed FeaturePython)
  Amount = 15
  AmountCheck = false
  Base = -> Wire869
  BentAngle = 135
  BentFactor = 4
  BottomCover = 20
  Diameter = 8
  Direction = (-1,0,0)
  Distance = 0
  FrontCover = 100
  HorizontalArea = 0
  Host = -> Wall281
  IfcData = IfcUID=0N2vvO0MT7Dvpb7EyTCBhJ
  IfcType = 110
  LeftCover = 20
  Length = 1079.31
  Mark = Stirrup
  Material = -> Material010
  MoveBase = false
  MoveWithHost = false
  OffsetEnd = 104
  OffsetStart = 104
  PerimeterLength = 0
  PlacementList = 15 placements: arithmetic series from (-104,0,0) step (-273.143,0,0) to (-3928,0,0)
  RebarShape = 3
  RightCover = 20
  Rounding = 1.75
  Spacing = 273.143
  TopCover = 20
  TotalLength = 16189.7
  TrueSpacing = 300
  VerticalArea = 0
FEATURE [App::DocumentObjectGroupPython] Stirrups  # scripted group (container) (typed FeaturePython)
  Group = -> [Rebar]
  Stirrups = -> [Rebar]
  StirrupsConfiguration = Two Legged Stirrups
FEATURE [Sketcher::SketchObject] Sketch326
  FullyConstrained = false
  MapMode = 5
  Placement = pos=(0,3555,2500) rot=(1,0,0;1.5708rad)
  Support = -> [Wall281]
  sketch-geometry (1):
    g0: LineSegment StartX=8230 StartY=263 StartZ=0 EndX=12110 EndY=263 EndZ=0
FEATURE [Part::FeaturePython] Rebar001  label="StraightRebar"  # Arch/BIM 110 (typed FeaturePython)
  Amount = 3
  AmountCheck = true
  Base = -> Sketch326
  Cover = 28
  CoverAlong = Top Side
  Diameter = 18
  Direction = (0,0,0)
  Distance = 0
  FrontCover = 28
  HorizontalArea = 0
  Host = -> Wall281
  IfcData = IfcUID=1dcUT_FHHF_B5oInSCm5hB
  IfcType = 110
  LeftBottomCover = 60
  Length = 3880
  Mark = StraightRebar
  Material = -> Material010
  MoveBase = false
  MoveWithHost = false
  OffsetEnd = 37
  OffsetStart = 37
  Orientation = Horizontal
  PerimeterLength = 0
  PlacementList = 3 placements: arithmetic series from (0,37,-8.21565e-15) step (0,88,-1.95399e-14) to (0,213,-4.72955e-14)
  RebarShape = 0
  RightTopCover = 60
  Rounding = 0
  Spacing = 88
  TotalLength = 11640
  TrueSpacing = 3
  VerticalArea = 0
FEATURE [App::DocumentObjectGroupPython] TopReinforcement  # scripted group (container) (typed FeaturePython)
  Group = -> [Rebar001]
  LayerSpacing = [30]
  NumberDiameterOffset = 3#18.0@60.0
  TopRebars = -> [Rebar001]
FEATURE [Sketcher::SketchObject] Sketch327
  FullyConstrained = false
  MapMode = 5
  Placement = pos=(0,3555,2500) rot=(1,0,0;1.5708rad)
  Support = -> [Wall281]
  sketch-geometry (1):
    g0: LineSegment StartX=8230 StartY=38 StartZ=0 EndX=12110 EndY=38 EndZ=0
FEATURE [Part::FeaturePython] Rebar002  label="StraightRebar001"  # Arch/BIM 110 (typed FeaturePython)
  Amount = 4
  AmountCheck = true
  Base = -> Sketch327
  Cover = 28
  CoverAlong = Bottom Side
  Diameter = 20
  Direction = (0,0,0)
  Distance = 0
  FrontCover = 28
  HorizontalArea = 0
  Host = -> Wall281
  IfcData = IfcUID=1EQ$82SIHAhRdy_3AtFEgy
  IfcType = 110
  LeftBottomCover = 60
  Length = 3880
  Mark = StraightRebar001
  Material = -> Material010
  MoveBase = false
  MoveWithHost = false
  OffsetEnd = 38
  OffsetStart = 38
  Orientation = Horizontal
  PerimeterLength = 0
  PlacementList = 4 placements: arithmetic series from (0,38,-8.43769e-15) step (0,58,-1.28786e-14) to (0,212,-4.70735e-14)
  RebarShape = 0
  RightTopCover = 60
  Rounding = 0
  Spacing = 58
  TotalLength = 15520
  TrueSpacing = 4
  VerticalArea = 0
FEATURE [App::DocumentObjectGroupPython] BottomReinforcement  # scripted group (container) (typed FeaturePython)
  BottomRebars = -> [Rebar002]
  Group = -> [Rebar002]
  LayerSpacing = [30]
  NumberDiameterOffset = 4#20.0@60.0
FEATURE [App::DocumentObjectGroupPython] BeamReinforcement  label="BeamReinforcement012"  # scripted group (container) (typed FeaturePython)
  Group = -> [Stirrups,TopReinforcement,BottomReinforcement]
  ReinforcementGroups = -> [Stirrups,TopReinforcement,BottomReinforcement]
FEATURE [Part::Part2DObjectPython] Wire871  # Draft 2D object (typed FeaturePython)
  Area = 0
  ChamferSize = 0
  Closed = false
  End = (10787.3,7564.85,2727.59)
  FilletRadius = 0
  Length = 898.352
  MakeFace = true
  Placement = pos=(0,15,0) rot=(0,0,1;0rad)
  Points = (7) [(10800.1,7565.41,2743.15),(10798,7524,2784.56),(10795.9,7524,2606),(10793.7,7736,2606),(10791.6,7736,2769),(10789.4,7508.44,2769),+1 more]
  Start = (10800.1,7580.41,2743.15)
  Subdivisions = 0
  Support = -> [Wall280]
FEATURE [Part::FeaturePython] Rebar003  label="Stirrup001"  # Arch/BIM 110 (typed FeaturePython)
  Amount = 10
  AmountCheck = false
  Base = -> Wire871
  BentAngle = 135
  BentFactor = 4
  BottomCover = 30
  Diameter = 8
  Direction = (-1,0,0)
  Distance = 0
  FrontCover = 100
  HorizontalArea = 0
  Host = -> Wall280
  IfcData = IfcUID=03$MgHS6j9GAjpO8e5wY8i
  IfcType = 110
  LeftCover = 30
  Length = 898.352
  Mark = Stirrup001
  Material = -> Material010
  MoveBase = false
  MoveWithHost = false
  OffsetEnd = 104
  OffsetStart = 104
  PerimeterLength = 0
  PlacementList = 10 placements: arithmetic series from (-104,0,0) step (-251.556,0,0) to (-2368,0,0)
  RebarShape = 3
  RightCover = 30
  Rounding = 1.375
  Spacing = 251.556
  TopCover = 30
  TotalLength = 8983.52
  TrueSpacing = 300
  VerticalArea = 0
FEATURE [App::DocumentObjectGroupPython] Stirrups001  # scripted group (container) (typed FeaturePython)
  Group = -> [Rebar003]
  Stirrups = -> [Rebar003]
  StirrupsConfiguration = Two Legged Stirrups
FEATURE [Sketcher::SketchObject] Sketch328
  FullyConstrained = false
  MapMode = 5
  Placement = pos=(0,7505,2572) rot=(1,0,0;1.5708rad)
  Support = -> [Wall280]
  sketch-geometry (1):
    g0: LineSegment StartX=8308 StartY=187 StartZ=0 EndX=10738 EndY=187 EndZ=0
FEATURE [Part::FeaturePython] Rebar004  label="StraightRebar002"  # Arch/BIM 110 (typed FeaturePython)
  Amount = 2
  AmountCheck = true
  Base = -> Sketch328
  Cover = 38
  CoverAlong = Top Side
  Diameter = 12
  Direction = (0,0,0)
  Distance = 0
  FrontCover = 38
  HorizontalArea = 0
  Host = -> Wall280
  IfcData = IfcUID=3CS4Ce6bv4LRFzsmwW8q2U
  IfcType = 110
  LeftBottomCover = 60
  Length = 2430
  Mark = StraightRebar002
  Material = -> Material010
  MoveBase = false
  MoveWithHost = false
  OffsetEnd = 44
  OffsetStart = 44
  Orientation = Horizontal
  PerimeterLength = 0
  Placement = pos=(57,0,0) rot=(0,0,1;0rad)
  PlacementList = 2 placements: [(0,44,-9.76996e-15),(0,236,-5.24025e-14)]
  RebarShape = 0
  RightTopCover = 60
  Rounding = 0
  Spacing = 192
  TotalLength = 4860
  TrueSpacing = 2
  VerticalArea = 0
FEATURE [App::DocumentObjectGroupPython] TopReinforcement001  # scripted group (container) (typed FeaturePython)
  Group = -> [Rebar004]
  LayerSpacing = [30]
  NumberDiameterOffset = 2#12.0@60.0
  TopRebars = -> [Rebar004]
FEATURE [Sketcher::SketchObject] Sketch329
  FullyConstrained = false
  MapMode = 5
  Placement = pos=(0,7505,2572) rot=(1,0,0;1.5708rad)
  Support = -> [Wall280]
  sketch-geometry (1):
    g0: LineSegment StartX=8308 StartY=45 StartZ=0 EndX=10738 EndY=45 EndZ=0
FEATURE [Part::FeaturePython] Rebar005  label="StraightRebar003"  # Arch/BIM 110 (typed FeaturePython)
  Amount = 2
  AmountCheck = true
  Base = -> Sketch329
  Cover = 38
  CoverAlong = Bottom Side
  Diameter = 14
  Direction = (0,0,0)
  Distance = 0
  FrontCover = 38
  HorizontalArea = 0
  Host = -> Wall280
  IfcData = IfcUID=12Y1T$1uv20RkT81nP3$Z0
  IfcType = 110
  LeftBottomCover = 60
  Length = 2430
  Mark = StraightRebar003
  Material = -> Material010
  MoveBase = false
  MoveWithHost = false
  OffsetEnd = 45
  OffsetStart = 45
  Orientation = Horizontal
  PerimeterLength = 0
  Placement = pos=(57,0,0) rot=(0,0,1;0rad)
  PlacementList = 2 placements: [(0,45,-9.99201e-15),(0,235,-5.21805e-14)]
  RebarShape = 0
  RightTopCover = 60
  Rounding = 0
  Spacing = 190
  TotalLength = 4860
  TrueSpacing = 2
  VerticalArea = 0
FEATURE [App::DocumentObjectGroupPython] BottomReinforcement001  # scripted group (container) (typed FeaturePython)
  BottomRebars = -> [Rebar005]
  Group = -> [Rebar005]
  LayerSpacing = [30]
  NumberDiameterOffset = 2#14.0@60.0
FEATURE [App::DocumentObjectGroupPython] BeamReinforcement001  # scripted group (container) (typed FeaturePython)
  Group = -> [Stirrups001,TopReinforcement001,BottomReinforcement001]
  ReinforcementGroups = -> [Stirrups001,TopReinforcement001,BottomReinforcement001]
FEATURE [Part::Part2DObjectPython] Wire872  # Draft 2D object (typed FeaturePython)
  Area = 0
  ChamferSize = 0
  Closed = false
  End = (6264.33,7564.56,2729.3)
  FilletRadius = 0
  Length = 890.697
  MakeFace = true
  Placement = pos=(75,15,0) rot=(0,0,1;0rad)
  Points = (7) [(6202.13,7563.7,2743.44),(6200,7524,2783.14),(6197.87,7524,2606),(6195.73,7736,2606),(6193.6,7736,2769),(6191.47,7509.86,2769),+1 more]
  Start = (6277.13,7578.7,2743.44)
  Subdivisions = 0
  Support = -> [Wall271]
FEATURE [Part::FeaturePython] Rebar006  label="Stirrup002"  # Arch/BIM 110 (typed FeaturePython)
  Amount = 6
  AmountCheck = false
  Base = -> Wire872
  BentAngle = 135
  BentFactor = 4
  BottomCover = 30
  Diameter = 8
  Direction = (-1,0,0)
  Distance = 0
  FrontCover = 100
  HorizontalArea = 0
  Host = -> Wall271
  IfcData = IfcUID=0wbSWuBvbEnPgC0wfqdX_b
  IfcType = 110
  LeftCover = 30
  Length = 890.697
  Mark = Stirrup002
  Material = -> Material010
  MoveBase = false
  MoveWithHost = false
  OffsetEnd = 104
  OffsetStart = 104
  PerimeterLength = 0
  PlacementList = 6 placements: arithmetic series from (-104,0,0) step (-244.8,0,0) to (-1328,0,0)
  RebarShape = 3
  RightCover = 30
  Rounding = 1.25
  Spacing = 244.8
  TopCover = 30
  TotalLength = 5344.18
  TrueSpacing = 300
  VerticalArea = 0
FEATURE [App::DocumentObjectGroupPython] Stirrups002  # scripted group (container) (typed FeaturePython)
  Group = -> [Rebar006]
  Stirrups = -> [Rebar006]
  StirrupsConfiguration = Two Legged Stirrups
FEATURE [Sketcher::SketchObject] Sketch330
  FullyConstrained = false
  MapMode = 5
  Placement = pos=(0,7505,2572) rot=(1,0,0;1.5708rad)
  Support = -> [Wall271]
  sketch-geometry (1):
    g0: LineSegment StartX=4850 StartY=187 StartZ=0 EndX=6140 EndY=187 EndZ=0
FEATURE [Part::FeaturePython] Rebar007  label="StraightRebar004"  # Arch/BIM 110 (typed FeaturePython)
  Amount = 2
  AmountCheck = true
  Base = -> Sketch330
  Cover = 38
  CoverAlong = Top Side
  Diameter = 12
  Direction = (0,0,0)
  Distance = 0
  FrontCover = 38
  HorizontalArea = 0
  Host = -> Wall271
  IfcData = IfcUID=02n1lHqdL8NwZlQltGu_h7
  IfcType = 110
  LeftBottomCover = 60
  Length = 1290
  Mark = StraightRebar004
  Material = -> Material010
  MoveBase = false
  MoveWithHost = false
  OffsetEnd = 44
  OffsetStart = 44
  Orientation = Horizontal
  PerimeterLength = 0
  Placement = pos=(60,0,0) rot=(0,0,1;0rad)
  PlacementList = 2 placements: [(0,44,-9.76996e-15),(0,236,-5.24025e-14)]
  RebarShape = 0
  RightTopCover = 60
  Rounding = 0
  Spacing = 192
  TotalLength = 2580
  TrueSpacing = 2
  VerticalArea = 0
FEATURE [App::DocumentObjectGroupPython] TopReinforcement002  # scripted group (container) (typed FeaturePython)
  Group = -> [Rebar007]
  LayerSpacing = [30]
  NumberDiameterOffset = 2#12.0@60.0
  TopRebars = -> [Rebar007]
FEATURE [Sketcher::SketchObject] Sketch331
  FullyConstrained = false
  MapMode = 5
  Placement = pos=(0,7505,2572) rot=(1,0,0;1.5708rad)
  Support = -> [Wall271]
  sketch-geometry (1):
    g0: LineSegment StartX=4850 StartY=44 StartZ=0 EndX=6140 EndY=44 EndZ=0
FEATURE [Part::FeaturePython] Rebar008  label="StraightRebar005"  # Arch/BIM 110 (typed FeaturePython)
  Amount = 2
  AmountCheck = true
  Base = -> Sketch331
  Cover = 38
  CoverAlong = Bottom Side
  Diameter = 12
  Direction = (0,0,0)
  Distance = 0
  FrontCover = 38
  HorizontalArea = 0
  Host = -> Wall271
  IfcData = IfcUID=10xIFfkxLCGw0mpryRN3cI
  IfcType = 110
  LeftBottomCover = 60
  Length = 1290
  Mark = StraightRebar005
  Material = -> Material010
  MoveBase = false
  MoveWithHost = false
  OffsetEnd = 44
  OffsetStart = 44
  Orientation = Horizontal
  PerimeterLength = 0
  Placement = pos=(60,0,0) rot=(0,0,1;0rad)
  PlacementList = 2 placements: [(0,44,-9.76996e-15),(0,236,-5.24025e-14)]
  RebarShape = 0
  RightTopCover = 60
  Rounding = 0
  Spacing = 192
  TotalLength = 2580
  TrueSpacing = 2
  VerticalArea = 0
FEATURE [App::DocumentObjectGroupPython] BottomReinforcement002  # scripted group (container) (typed FeaturePython)
  BottomRebars = -> [Rebar008]
  Group = -> [Rebar008]
  LayerSpacing = [30]
  NumberDiameterOffset = 2#12.0@60.0
FEATURE [App::DocumentObjectGroupPython] BeamReinforcement002  # scripted group (container) (typed FeaturePython)
  Group = -> [Stirrups002,TopReinforcement002,BottomReinforcement002]
  ReinforcementGroups = -> [Stirrups002,TopReinforcement002,BottomReinforcement002]
FEATURE [Part::Part2DObjectPython] Wire873  # Draft 2D object (typed FeaturePython)
  Area = 0
  ChamferSize = 0
  Closed = false
  End = (12629.6,5219.33,2729.3)
  FilletRadius = 0
  Length = 890.697
  MakeFace = true
  Placement = pos=(0,30,0) rot=(0,0,1;0rad)
  Points = (7) [(12643.7,5202.13,2743.44),(12604,5200,2783.14),(12604,5197.87,2606),(12816,5195.73,2606),(12816,5193.6,2769),(12589.9,5191.47,2769),+1 more]
  Start = (12643.7,5232.13,2743.44)
  Subdivisions = 0
  Support = -> [Wall276]
FEATURE [Part::FeaturePython] Rebar009  label="Stirrup003"  # Arch/BIM 110 (typed FeaturePython)
  Amount = 6
  AmountCheck = false
  Base = -> Wire873
  BentAngle = 135
  BentFactor = 4
  BottomCover = 30
  Diameter = 8
  Direction = (0,-1,0)
  Distance = 0
  FrontCover = 100
  HorizontalArea = 0
  Host = -> Wall276
  IfcData = IfcUID=0yypPYtsPCuBCevCtN2Olt
  IfcType = 110
  LeftCover = 30
  Length = 890.697
  Mark = Stirrup003
  Material = -> Material010
  MoveBase = false
  MoveWithHost = false
  OffsetEnd = 104
  OffsetStart = 104
  PerimeterLength = 0
  PlacementList = 6 placements: arithmetic series from (0,-104,0) step (0,-244.8,0) to (0,-1328,0)
  RebarShape = 3
  RightCover = 30
  Rounding = 1.25
  Spacing = 244.8
  TopCover = 30
  TotalLength = 5344.18
  TrueSpacing = 300
  VerticalArea = 0
FEATURE [App::DocumentObjectGroupPython] Stirrups003  # scripted group (container) (typed FeaturePython)
  Group = -> [Rebar009]
  Stirrups = -> [Rebar009]
  StirrupsConfiguration = Two Legged Stirrups
FEATURE [Sketcher::SketchObject] Sketch332
  FullyConstrained = false
  MapMode = 5
  Placement = pos=(12850,0,2572) rot=(0.57735,0.57735,0.57735;2.0944rad)
  Support = -> [Wall276]
  sketch-geometry (1):
    g0: LineSegment StartX=3850 StartY=187 StartZ=0 EndX=5140 EndY=187 EndZ=0
FEATURE [Part::FeaturePython] Rebar010  label="StraightRebar006"  # Arch/BIM 110 (typed FeaturePython)
  Amount = 2
  AmountCheck = true
  Base = -> Sketch332
  Cover = 38
  CoverAlong = Top Side
  Diameter = 12
  Direction = (0,0,0)
  Distance = 0
  FrontCover = 38
  HorizontalArea = 0
  Host = -> Wall276
  IfcData = IfcUID=3sX30Bu914T9jBbQKNrnT9
  IfcType = 110
  LeftBottomCover = 60
  Length = 1290
  Mark = StraightRebar006
  Material = -> Material010
  MoveBase = false
  MoveWithHost = false
  OffsetEnd = 44
  OffsetStart = 44
  Orientation = Horizontal
  PerimeterLength = 0
  Placement = pos=(0,30,0) rot=(0,0,1;0rad)
  PlacementList = 2 placements: [(-44,0,0),(-236,0,0)]
  RebarShape = 0
  RightTopCover = 60
  Rounding = 0
  Spacing = 192
  TotalLength = 2580
  TrueSpacing = 2
  VerticalArea = 0
FEATURE [App::DocumentObjectGroupPython] TopReinforcement003  # scripted group (container) (typed FeaturePython)
  Group = -> [Rebar010]
  LayerSpacing = [30]
  NumberDiameterOffset = 2#12.0@60.0
  TopRebars = -> [Rebar010]
FEATURE [Sketcher::SketchObject] Sketch333
  FullyConstrained = false
  MapMode = 5
  Placement = pos=(12850,0,2572) rot=(0.57735,0.57735,0.57735;2.0944rad)
  Support = -> [Wall276]
  sketch-geometry (1):
    g0: LineSegment StartX=3850 StartY=44 StartZ=0 EndX=5140 EndY=44 EndZ=0
FEATURE [Part::FeaturePython] Rebar011  label="StraightRebar007"  # Arch/BIM 110 (typed FeaturePython)
  Amount = 2
  AmountCheck = true
  Base = -> Sketch333
  Cover = 38
  CoverAlong = Bottom Side
  Diameter = 12
  Direction = (0,0,0)
  Distance = 0
  FrontCover = 38
  HorizontalArea = 0
  Host = -> Wall276
  IfcData = IfcUID=0U2drE4$P7kvGv3bbH5Yg2
  IfcType = 110
  LeftBottomCover = 60
  Length = 1290
  Mark = StraightRebar007
  Material = -> Material010
  MoveBase = false
  MoveWithHost = false
  OffsetEnd = 44
  OffsetStart = 44
  Orientation = Horizontal
  PerimeterLength = 0
  Placement = pos=(0,30,0) rot=(0,0,1;0rad)
  PlacementList = 2 placements: [(-44,0,0),(-236,0,0)]
  RebarShape = 0
  RightTopCover = 60
  Rounding = 0
  Spacing = 192
  TotalLength = 2580
  TrueSpacing = 2
  VerticalArea = 0
FEATURE [App::DocumentObjectGroupPython] BottomReinforcement003  # scripted group (container) (typed FeaturePython)
  BottomRebars = -> [Rebar011]
  Group = -> [Rebar011]
  LayerSpacing = [30]
  NumberDiameterOffset = 2#12.0@60.0
FEATURE [App::DocumentObjectGroupPython] BeamReinforcement003  # scripted group (container) (typed FeaturePython)
  Group = -> [Stirrups003,TopReinforcement003,BottomReinforcement003]
  ReinforcementGroups = -> [Stirrups003,TopReinforcement003,BottomReinforcement003]
FEATURE [Part::Part2DObjectPython] Wire874  # Draft 2D object (typed FeaturePython)
  Area = 0
  ChamferSize = 0
  Closed = false
  End = (12629.8,1049.27,2727.59)
  FilletRadius = 0
  Length = 898.352
  MakeFace = true
  Placement = pos=(0,75,0) rot=(0,0,1;0rad)
  Points = (7) [(12645.4,987.147,2743.15),(12604,985,2784.56),(12604,982.853,2606),(12816,980.706,2606),(12816,978.56,2769),(12588.4,976.413,2769),+1 more]
  Start = (12645.4,1062.15,2743.15)
  Subdivisions = 0
  Support = -> [Wall274]
FEATURE [Part::FeaturePython] Rebar012  label="Stirrup004"  # Arch/BIM 110 (typed FeaturePython)
  Amount = 10
  AmountCheck = false
  Base = -> Wire874
  BentAngle = 135
  BentFactor = 4
  BottomCover = 30
  Diameter = 8
  Direction = (0,1,0)
  Distance = 0
  FrontCover = 100
  HorizontalArea = 0
  Host = -> Wall274
  IfcData = IfcUID=3XbnhF0cz6mArcGNZbmhw$
  IfcType = 110
  LeftCover = 30
  Length = 898.352
  Mark = Stirrup004
  Material = -> Material010
  MoveBase = false
  MoveWithHost = false
  OffsetEnd = 104
  OffsetStart = 104
  PerimeterLength = 0
  PlacementList = 10 placements: arithmetic series from (0,104,0) step (0,251.556,0) to (0,2368,0)
  RebarShape = 3
  RightCover = 30
  Rounding = 1.375
  Spacing = 251.556
  TopCover = 30
  TotalLength = 8983.52
  TrueSpacing = 300
  VerticalArea = 0
FEATURE [App::DocumentObjectGroupPython] Stirrups004  # scripted group (container) (typed FeaturePython)
  Group = -> [Rebar012]
  Stirrups = -> [Rebar012]
  StirrupsConfiguration = Two Legged Stirrups
FEATURE [Sketcher::SketchObject] Sketch334
  FullyConstrained = false
  MapMode = 5
  Placement = pos=(12570,0,2572) rot=(0.57735,-0.57735,-0.57735;2.0944rad)
  Support = -> [Wall274]
  sketch-geometry (1):
    g0: LineSegment StartX=-3475 StartY=187 StartZ=0 EndX=-1045 EndY=187 EndZ=0
FEATURE [Part::FeaturePython] Rebar013  label="StraightRebar008"  # Arch/BIM 110 (typed FeaturePython)
  Amount = 2
  AmountCheck = true
  Base = -> Sketch334
  Cover = 38
  CoverAlong = Top Side
  Diameter = 12
  Direction = (0,0,0)
  Distance = 0
  FrontCover = 38
  HorizontalArea = 0
  Host = -> Wall274
  IfcData = IfcUID=0IhfJ24H12sPMtpoimhsX_
  IfcType = 110
  LeftBottomCover = 60
  Length = 2430
  Mark = StraightRebar008
  Material = -> Material010
  MoveBase = false
  MoveWithHost = false
  OffsetEnd = 44
  OffsetStart = 44
  Orientation = Horizontal
  PerimeterLength = 0
  Placement = pos=(0,35,0) rot=(0,0,1;0rad)
  PlacementList = 2 placements: [(44,0,0),(236,0,0)]
  RebarShape = 0
  RightTopCover = 60
  Rounding = 0
  Spacing = 192
  TotalLength = 4860
  TrueSpacing = 2
  VerticalArea = 0
FEATURE [App::DocumentObjectGroupPython] TopReinforcement004  # scripted group (container) (typed FeaturePython)
  Group = -> [Rebar013]
  LayerSpacing = [30]
  NumberDiameterOffset = 2#12.0@60.0
  TopRebars = -> [Rebar013]
FEATURE [Sketcher::SketchObject] Sketch335
  FullyConstrained = false
  MapMode = 5
  Placement = pos=(12570,0,2572) rot=(0.57735,-0.57735,-0.57735;2.0944rad)
  Support = -> [Wall274]
  sketch-geometry (1):
    g0: LineSegment StartX=-3475 StartY=45 StartZ=0 EndX=-1045 EndY=45 EndZ=0
FEATURE [Part::FeaturePython] Rebar014  label="StraightRebar009"  # Arch/BIM 110 (typed FeaturePython)
  Amount = 2
  AmountCheck = true
  Base = -> Sketch335
  Cover = 38
  CoverAlong = Bottom Side
  Diameter = 14
  Direction = (0,0,0)
  Distance = 0
  FrontCover = 38
  HorizontalArea = 0
  Host = -> Wall274
  IfcData = IfcUID=38s843Wp98lgFtcANgZxJN
  IfcType = 110
  LeftBottomCover = 60
  Length = 2430
  Mark = StraightRebar009
  Material = -> Material010
  MoveBase = false
  MoveWithHost = false
  OffsetEnd = 45
  OffsetStart = 45
  Orientation = Horizontal
  PerimeterLength = 0
  Placement = pos=(0,35,0) rot=(0,0,1;0rad)
  PlacementList = 2 placements: [(45,0,0),(235,0,0)]
  RebarShape = 0
  RightTopCover = 60
  Rounding = 0
  Spacing = 190
  TotalLength = 4860
  TrueSpacing = 2
  VerticalArea = 0
FEATURE [App::DocumentObjectGroupPython] BottomReinforcement004  # scripted group (container) (typed FeaturePython)
  BottomRebars = -> [Rebar014]
  Group = -> [Rebar014]
  LayerSpacing = [30]
  NumberDiameterOffset = 2#14.0@60.0
FEATURE [App::DocumentObjectGroupPython] BeamReinforcement004  # scripted group (container) (typed FeaturePython)
  Group = -> [Stirrups004,TopReinforcement004,BottomReinforcement004]
  ReinforcementGroups = -> [Stirrups004,TopReinforcement004,BottomReinforcement004]
FEATURE [Part::Part2DObjectPython] Wire875  # Draft 2D object (typed FeaturePython)
  Area = 0
  ChamferSize = 0
  Closed = false
  End = (4194.27,7564.85,2727.59)
  FilletRadius = 0
  Length = 898.352
  MakeFace = true
  Placement = pos=(-75,15,0) rot=(0,0,1;0rad)
  Points = (7) [(4282.15,7565.41,2743.15),(4280,7524,2784.56),(4277.85,7524,2606),(4275.71,7736,2606),(4273.56,7736,2769),(4271.41,7508.44,2769),+1 more]
  Start = (4207.15,7580.41,2743.15)
  Subdivisions = 0
  Support = -> [Wall270]
FEATURE [Part::FeaturePython] Rebar015  label="Stirrup005"  # Arch/BIM 110 (typed FeaturePython)
  Amount = 10
  AmountCheck = false
  Base = -> Wire875
  BentAngle = 135
  BentFactor = 4
  BottomCover = 30
  Diameter = 8
  Direction = (-1,0,0)
  Distance = 0
  FrontCover = 100
  HorizontalArea = 0
  Host = -> Wall270
  IfcData = IfcUID=2RF9jp$wz08A9VdwpHTXzZ
  IfcType = 110
  LeftCover = 30
  Length = 898.352
  Mark = Stirrup005
  Material = -> Material010
  MoveBase = false
  MoveWithHost = false
  OffsetEnd = 104
  OffsetStart = 104
  PerimeterLength = 0
  PlacementList = 10 placements: arithmetic series from (-104,0,0) step (-251.556,0,0) to (-2368,0,0)
  RebarShape = 3
  RightCover = 30
  Rounding = 1.375
  Spacing = 251.556
  TopCover = 30
  TotalLength = 8983.52
  TrueSpacing = 300
  VerticalArea = 0
FEATURE [App::DocumentObjectGroupPython] Stirrups005  # scripted group (container) (typed FeaturePython)
  Group = -> [Rebar015]
  Stirrups = -> [Rebar015]
  StirrupsConfiguration = Two Legged Stirrups
FEATURE [Sketcher::SketchObject] Sketch336
  FullyConstrained = false
  MapMode = 5
  Placement = pos=(0,7505,2572) rot=(1,0,0;1.5708rad)
  Support = -> [Wall270]
  sketch-geometry (1):
    g0: LineSegment StartX=1790 StartY=187 StartZ=0 EndX=4220 EndY=187 EndZ=0
FEATURE [Part::FeaturePython] Rebar016  label="StraightRebar010"  # Arch/BIM 110 (typed FeaturePython)
  Amount = 2
  AmountCheck = true
  Base = -> Sketch336
  Cover = 38
  CoverAlong = Top Side
  Diameter = 12
  Direction = (0,0,0)
  Distance = 0
  FrontCover = 38
  HorizontalArea = 0
  Host = -> Wall270
  IfcData = IfcUID=1nXP$0rpbACR1K2SbosHQt
  IfcType = 110
  LeftBottomCover = 60
  Length = 2430
  Mark = StraightRebar010
  Material = -> Material010
  MoveBase = false
  MoveWithHost = false
  OffsetEnd = 44
  OffsetStart = 44
  Orientation = Horizontal
  PerimeterLength = 0
  Placement = pos=(-50,0,0) rot=(0,0,1;0rad)
  PlacementList = 2 placements: [(0,44,-9.76996e-15),(0,236,-5.24025e-14)]
  RebarShape = 0
  RightTopCover = 60
  Rounding = 0
  Spacing = 192
  TotalLength = 4860
  TrueSpacing = 2
  VerticalArea = 0
FEATURE [App::DocumentObjectGroupPython] TopReinforcement005  # scripted group (container) (typed FeaturePython)
  Group = -> [Rebar016]
  LayerSpacing = [30]
  NumberDiameterOffset = 2#12.0@60.0
  TopRebars = -> [Rebar016]
FEATURE [Sketcher::SketchObject] Sketch337
  FullyConstrained = false
  MapMode = 5
  Placement = pos=(0,7505,2572) rot=(1,0,0;1.5708rad)
  Support = -> [Wall270]
  sketch-geometry (1):
    g0: LineSegment StartX=1790 StartY=45 StartZ=0 EndX=4220 EndY=45 EndZ=0
FEATURE [Part::FeaturePython] Rebar017  label="StraightRebar011"  # Arch/BIM 110 (typed FeaturePython)
  Amount = 2
  AmountCheck = true
  Base = -> Sketch337
  Cover = 38
  CoverAlong = Bottom Side
  Diameter = 14
  Direction = (0,0,0)
  Distance = 0
  FrontCover = 38
  HorizontalArea = 0
  Host = -> Wall270
  IfcData = IfcUID=3zK0LNm4n3mO5pKUyneaxe
  IfcType = 110
  LeftBottomCover = 60
  Length = 2430
  Mark = StraightRebar011
  Material = -> Material010
  MoveBase = false
  MoveWithHost = false
  OffsetEnd = 45
  OffsetStart = 45
  Orientation = Horizontal
  PerimeterLength = 0
  Placement = pos=(-50,0,0) rot=(0,0,1;0rad)
  PlacementList = 2 placements: [(0,45,-9.99201e-15),(0,235,-5.21805e-14)]
  RebarShape = 0
  RightTopCover = 60
  Rounding = 0
  Spacing = 190
  TotalLength = 4860
  TrueSpacing = 2
  VerticalArea = 0
FEATURE [App::DocumentObjectGroupPython] BottomReinforcement005  # scripted group (container) (typed FeaturePython)
  BottomRebars = -> [Rebar017]
  Group = -> [Rebar017]
  LayerSpacing = [30]
  NumberDiameterOffset = 2#14.0@60.0
FEATURE [App::DocumentObjectGroupPython] BeamReinforcement005  # scripted group (container) (typed FeaturePython)
  Group = -> [Stirrups005,TopReinforcement005,BottomReinforcement005]
  ReinforcementGroups = -> [Stirrups005,TopReinforcement005,BottomReinforcement005]
FEATURE [Part::Part2DObjectPython] Wire876  # Draft 2D object (typed FeaturePython)
  Area = 0
  ChamferSize = 0
  Closed = false
  End = (-270.444,3559.33,2729.3)
  FilletRadius = 0
  Length = 890.697
  MakeFace = true
  Placement = pos=(0,-100,0) rot=(0,0,1;0rad)
  Points = (7) [(-256.302,3672.13,2743.44),(-296,3670,2783.14),(-296,3667.87,2606),(-84,3665.73,2606),(-84,3663.6,2769),(-310.142,3661.47,2769),+1 more]
  Start = (-256.302,3572.13,2743.44)
  Subdivisions = 0
  Support = -> [Wall275]
FEATURE [Part::FeaturePython] Rebar018  label="Stirrup006"  # Arch/BIM 110 (typed FeaturePython)
  Amount = 8
  AmountCheck = false
  Base = -> Wire876
  BentAngle = 135
  BentFactor = 4
  BottomCover = 30
  Diameter = 8
  Direction = (0,-1,0)
  Distance = 0
  FrontCover = 100
  HorizontalArea = 0
  Host = -> Wall275
  IfcData = IfcUID=0GO4wNkB97lOlqTACpJZwt
  IfcType = 110
  LeftCover = 30
  Length = 890.697
  Mark = Stirrup006
  Material = -> Material010
  MoveBase = false
  MoveWithHost = false
  OffsetEnd = 104
  OffsetStart = 104
  PerimeterLength = 0
  PlacementList = 8 placements: arithmetic series from (0,-104,0) step (0,-249.143,0) to (0,-1848,0)
  RebarShape = 3
  RightCover = 30
  Rounding = 1.25
  Spacing = 249.143
  TopCover = 30
  TotalLength = 7125.58
  TrueSpacing = 300
  VerticalArea = 0
FEATURE [App::DocumentObjectGroupPython] Stirrups006  # scripted group (container) (typed FeaturePython)
  Group = -> [Rebar018]
  Stirrups = -> [Rebar018]
  StirrupsConfiguration = Two Legged Stirrups
FEATURE [Sketcher::SketchObject] Sketch338
  FullyConstrained = false
  MapMode = 5
  Placement = pos=(-50,0,2572) rot=(0.57735,0.57735,0.57735;2.0944rad)
  Support = -> [Wall275]
  sketch-geometry (1):
    g0: LineSegment StartX=1690 StartY=187 StartZ=0 EndX=3610 EndY=187 EndZ=0
FEATURE [Part::FeaturePython] Rebar019  label="StraightRebar012"  # Arch/BIM 110 (typed FeaturePython)
  Amount = 2
  AmountCheck = true
  Base = -> Sketch338
  Cover = 38
  CoverAlong = Top Side
  Diameter = 12
  Direction = (0,0,0)
  Distance = 0
  FrontCover = 38
  HorizontalArea = 0
  Host = -> Wall275
  IfcData = IfcUID=3m1D0xJN5Ey8da60xgpDpj
  IfcType = 110
  LeftBottomCover = 60
  Length = 1920
  Mark = StraightRebar012
  Material = -> Material010
  MoveBase = false
  MoveWithHost = false
  OffsetEnd = 44
  OffsetStart = 44
  Orientation = Horizontal
  PerimeterLength = 0
  Placement = pos=(0,-80,0) rot=(0,0,1;0rad)
  PlacementList = 2 placements: [(-44,0,0),(-236,0,0)]
  RebarShape = 0
  RightTopCover = 60
  Rounding = 0
  Spacing = 192
  TotalLength = 3840
  TrueSpacing = 2
  VerticalArea = 0
FEATURE [App::DocumentObjectGroupPython] TopReinforcement006  # scripted group (container) (typed FeaturePython)
  Group = -> [Rebar019]
  LayerSpacing = [30]
  NumberDiameterOffset = 2#12.0@60.0
  TopRebars = -> [Rebar019]
FEATURE [Sketcher::SketchObject] Sketch339
  FullyConstrained = false
  MapMode = 5
  Placement = pos=(-50,0,2572) rot=(0.57735,0.57735,0.57735;2.0944rad)
  Support = -> [Wall275]
  sketch-geometry (1):
    g0: LineSegment StartX=1690 StartY=44 StartZ=0 EndX=3610 EndY=44 EndZ=0
FEATURE [Part::FeaturePython] Rebar020  label="StraightRebar013"  # Arch/BIM 110 (typed FeaturePython)
  Amount = 2
  AmountCheck = true
  Base = -> Sketch339
  Cover = 38
  CoverAlong = Bottom Side
  Diameter = 12
  Direction = (0,0,0)
  Distance = 0
  FrontCover = 38
  HorizontalArea = 0
  Host = -> Wall275
  IfcData = IfcUID=1s9A5d1rn8SeYaByjManJ6
  IfcType = 110
  LeftBottomCover = 60
  Length = 1920
  Mark = StraightRebar013
  Material = -> Material010
  MoveBase = false
  MoveWithHost = false
  OffsetEnd = 44
  OffsetStart = 44
  Orientation = Horizontal
  PerimeterLength = 0
  Placement = pos=(0,-80,0) rot=(0,0,1;0rad)
  PlacementList = 2 placements: [(-44,0,0),(-236,0,0)]
  RebarShape = 0
  RightTopCover = 60
  Rounding = 0
  Spacing = 192
  TotalLength = 3840
  TrueSpacing = 2
  VerticalArea = 0
FEATURE [App::DocumentObjectGroupPython] BottomReinforcement006  # scripted group (container) (typed FeaturePython)
  BottomRebars = -> [Rebar020]
  Group = -> [Rebar020]
  LayerSpacing = [30]
  NumberDiameterOffset = 2#12.0@60.0
FEATURE [App::DocumentObjectGroupPython] BeamReinforcement006  # scripted group (container) (typed FeaturePython)
  Group = -> [Stirrups006,TopReinforcement006,BottomReinforcement006]
  ReinforcementGroups = -> [Stirrups006,TopReinforcement006,BottomReinforcement006]
FEATURE [Part::Part2DObjectPython] Wire877  # Draft 2D object (typed FeaturePython)
  Area = 0
  ChamferSize = 0
  Closed = false
  End = (8454.33,-265.444,2498.3)
  FilletRadius = 0
  Length = 890.697
  MakeFace = true
  Placement = pos=(105,-15,0) rot=(0,0,1;0rad)
  Points = (7) [(8362.13,-236.302,2512.44),(8360,-276,2552.14),(8357.87,-276,2375),(8355.73,-64,2375),(8353.6,-64,2538),(8351.47,-290.142,2538),+1 more]
  Start = (8467.13,-251.302,2512.44)
  Subdivisions = 0
  Support = -> [Wall273]
FEATURE [Part::FeaturePython] Rebar021  label="Stirrup007"  # Arch/BIM 110 (typed FeaturePython)
  Amount = 5
  AmountCheck = false
  Base = -> Wire877
  BentAngle = 135
  BentFactor = 4
  BottomCover = 30
  Diameter = 8
  Direction = (-1,0,0)
  Distance = 0
  FrontCover = 100
  HorizontalArea = 0
  Host = -> Wall273
  IfcData = IfcUID=2sOpwtOeP6d93qeK3TWBYN
  IfcType = 110
  LeftCover = 30
  Length = 890.697
  Mark = Stirrup007
  Material = -> Material010
  MoveBase = false
  MoveWithHost = false
  OffsetEnd = 104
  OffsetStart = 104
  PerimeterLength = 0
  PlacementList = 5 placements: arithmetic series from (-104,0,0) step (-241,0,0) to (-1068,0,0)
  RebarShape = 3
  RightCover = 30
  Rounding = 1.25
  Spacing = 241
  TopCover = 30
  TotalLength = 4453.49
  TrueSpacing = 300
  VerticalArea = 0
FEATURE [App::DocumentObjectGroupPython] Stirrups007  # scripted group (container) (typed FeaturePython)
  Group = -> [Rebar021]
  Stirrups = -> [Rebar021]
  StirrupsConfiguration = Two Legged Stirrups
FEATURE [Sketcher::SketchObject] Sketch340
  FullyConstrained = false
  MapMode = 5
  Placement = pos=(0,-325,2341) rot=(1,0,0;1.5708rad)
  Support = -> [Wall273]
  sketch-geometry (1):
    g0: LineSegment StartX=7280 StartY=187 StartZ=0 EndX=8300 EndY=187 EndZ=0
FEATURE [Part::FeaturePython] Rebar022  label="StraightRebar014"  # Arch/BIM 110 (typed FeaturePython)
  Amount = 2
  AmountCheck = true
  Base = -> Sketch340
  Cover = 38
  CoverAlong = Top Side
  Diameter = 12
  Direction = (0,0,0)
  Distance = 0
  FrontCover = 38
  HorizontalArea = 0
  Host = -> Wall273
  IfcData = IfcUID=1vMcNoj0HEmRp1d9MJzP$J
  IfcType = 110
  LeftBottomCover = 60
  Length = 1020
  Mark = StraightRebar014
  Material = -> Material010
  MoveBase = false
  MoveWithHost = false
  OffsetEnd = 44
  OffsetStart = 44
  Orientation = Horizontal
  PerimeterLength = 0
  Placement = pos=(75,7.1e-15,0) rot=(0,0,1;0rad)
  PlacementList = 2 placements: [(0,44,-9.76996e-15),(0,236,-5.24025e-14)]
  RebarShape = 0
  RightTopCover = 60
  Rounding = 0
  Spacing = 192
  TotalLength = 2040
  TrueSpacing = 2
  VerticalArea = 0
FEATURE [App::DocumentObjectGroupPython] TopReinforcement007  # scripted group (container) (typed FeaturePython)
  Group = -> [Rebar022]
  LayerSpacing = [30]
  NumberDiameterOffset = 2#12.0@60.0
  TopRebars = -> [Rebar022]
FEATURE [Sketcher::SketchObject] Sketch341
  FullyConstrained = false
  MapMode = 5
  Placement = pos=(0,-325,2341) rot=(1,0,0;1.5708rad)
  Support = -> [Wall273]
  sketch-geometry (1):
    g0: LineSegment StartX=7280 StartY=44 StartZ=0 EndX=8300 EndY=44 EndZ=0
FEATURE [Part::FeaturePython] Rebar023  label="StraightRebar015"  # Arch/BIM 110 (typed FeaturePython)
  Amount = 2
  AmountCheck = true
  Base = -> Sketch341
  Cover = 38
  CoverAlong = Bottom Side
  Diameter = 12
  Direction = (0,0,0)
  Distance = 0
  FrontCover = 38
  HorizontalArea = 0
  Host = -> Wall273
  IfcData = IfcUID=3uc1wwna11_hIpa5m3v9lF
  IfcType = 110
  LeftBottomCover = 60
  Length = 1020
  Mark = StraightRebar015
  Material = -> Material010
  MoveBase = false
  MoveWithHost = false
  OffsetEnd = 44
  OffsetStart = 44
  Orientation = Horizontal
  PerimeterLength = 0
  Placement = pos=(75,7.1e-15,0) rot=(0,0,1;0rad)
  PlacementList = 2 placements: [(0,44,-9.76996e-15),(0,236,-5.24025e-14)]
  RebarShape = 0
  RightTopCover = 60
  Rounding = 0
  Spacing = 192
  TotalLength = 2040
  TrueSpacing = 2
  VerticalArea = 0
FEATURE [App::DocumentObjectGroupPython] BottomReinforcement007  # scripted group (container) (typed FeaturePython)
  BottomRebars = -> [Rebar023]
  Group = -> [Rebar023]
  LayerSpacing = [30]
  NumberDiameterOffset = 2#12.0@60.0
FEATURE [App::DocumentObjectGroupPython] BeamReinforcement007  # scripted group (container) (typed FeaturePython)
  Group = -> [Stirrups007,TopReinforcement007,BottomReinforcement007]
  ReinforcementGroups = -> [Stirrups007,TopReinforcement007,BottomReinforcement007]
FEATURE [Part::Part2DObjectPython] Wire878  # Draft 2D object (typed FeaturePython)
  Area = 0
  ChamferSize = 0
  Closed = false
  End = (6969.33,-265.444,2498.3)
  FilletRadius = 0
  Length = 890.697
  MakeFace = true
  Placement = pos=(15,-15,0) rot=(0,0,1;0rad)
  Points = (7) [(6967.13,-236.302,2512.44),(6965,-276,2552.14),(6962.87,-276,2375),(6960.73,-64,2375),(6958.6,-64,2538),(6956.47,-290.142,2538),+1 more]
  Start = (6982.13,-251.302,2512.44)
  Subdivisions = 0
  Support = -> [Wall272]
FEATURE [Part::FeaturePython] Rebar024  label="Stirrup008"  # Arch/BIM 110 (typed FeaturePython)
  Amount = 7
  AmountCheck = false
  Base = -> Wire878
  BentAngle = 135
  BentFactor = 4
  BottomCover = 30
  Diameter = 8
  Direction = (-1,0,0)
  Distance = 0
  FrontCover = 100
  HorizontalArea = 0
  Host = -> Wall272
  IfcData = IfcUID=0LnHNELLX3fuNNWSVyCMGl
  IfcType = 110
  LeftCover = 30
  Length = 890.697
  Mark = Stirrup008
  Material = -> Material010
  MoveBase = false
  MoveWithHost = false
  OffsetEnd = 104
  OffsetStart = 104
  PerimeterLength = 0
  PlacementList = 7 placements: arithmetic series from (-104,0,0) step (-225.667,0,0) to (-1458,0,0)
  RebarShape = 3
  RightCover = 30
  Rounding = 1.25
  Spacing = 225.667
  TopCover = 30
  TotalLength = 6234.88
  TrueSpacing = 300
  VerticalArea = 0
FEATURE [App::DocumentObjectGroupPython] Stirrups008  # scripted group (container) (typed FeaturePython)
  Group = -> [Rebar024]
  Stirrups = -> [Rebar024]
  StirrupsConfiguration = Two Legged Stirrups
FEATURE [Sketcher::SketchObject] Sketch342
  FullyConstrained = false
  MapMode = 5
  Placement = pos=(0,-325,2341) rot=(1,0,0;1.5708rad)
  Support = -> [Wall272]
  sketch-geometry (1):
    g0: LineSegment StartX=5495 StartY=187 StartZ=0 EndX=6905 EndY=187 EndZ=0
FEATURE [Part::FeaturePython] Rebar025  label="StraightRebar016"  # Arch/BIM 110 (typed FeaturePython)
  Amount = 2
  AmountCheck = true
  Base = -> Sketch342
  Cover = 38
  CoverAlong = Top Side
  Diameter = 12
  Direction = (0,0,0)
  Distance = 0
  FrontCover = 38
  HorizontalArea = 0
  Host = -> Wall272
  IfcData = IfcUID=1KTuHzywvETe2xYfKlmI5q
  IfcType = 110
  LeftBottomCover = 60
  Length = 1410
  Mark = StraightRebar016
  Material = -> Material010
  MoveBase = false
  MoveWithHost = false
  OffsetEnd = 44
  OffsetStart = 44
  Orientation = Horizontal
  PerimeterLength = 0
  Placement = pos=(-5,0,0) rot=(0,0,1;0rad)
  PlacementList = 2 placements: [(0,44,-9.76996e-15),(0,236,-5.24025e-14)]
  RebarShape = 0
  RightTopCover = 60
  Rounding = 0
  Spacing = 192
  TotalLength = 2820
  TrueSpacing = 2
  VerticalArea = 0
FEATURE [App::DocumentObjectGroupPython] TopReinforcement008  # scripted group (container) (typed FeaturePython)
  Group = -> [Rebar025]
  LayerSpacing = [30]
  NumberDiameterOffset = 2#12.0@60.0
  TopRebars = -> [Rebar025]
FEATURE [Sketcher::SketchObject] Sketch343
  FullyConstrained = false
  MapMode = 5
  Placement = pos=(0,-325,2341) rot=(1,0,0;1.5708rad)
  Support = -> [Wall272]
  sketch-geometry (1):
    g0: LineSegment StartX=5495 StartY=44 StartZ=0 EndX=6905 EndY=44 EndZ=0
FEATURE [Part::FeaturePython] Rebar026  label="StraightRebar017"  # Arch/BIM 110 (typed FeaturePython)
  Amount = 2
  AmountCheck = true
  Base = -> Sketch343
  Cover = 38
  CoverAlong = Bottom Side
  Diameter = 12
  Direction = (0,0,0)
  Distance = 0
  FrontCover = 38
  HorizontalArea = 0
  Host = -> Wall272
  IfcData = IfcUID=12i$N8lpL6MOoc$XX$mBTR
  IfcType = 110
  LeftBottomCover = 60
  Length = 1410
  Mark = StraightRebar017
  Material = -> Material010
  MoveBase = false
  MoveWithHost = false
  OffsetEnd = 44
  OffsetStart = 44
  Orientation = Horizontal
  PerimeterLength = 0
  Placement = pos=(-5,0,0) rot=(0,0,1;0rad)
  PlacementList = 2 placements: [(0,44,-9.76996e-15),(0,236,-5.24025e-14)]
  RebarShape = 0
  RightTopCover = 60
  Rounding = 0
  Spacing = 192
  TotalLength = 2820
  TrueSpacing = 2
  VerticalArea = 0
FEATURE [App::DocumentObjectGroupPython] BottomReinforcement008  # scripted group (container) (typed FeaturePython)
  BottomRebars = -> [Rebar026]
  Group = -> [Rebar026]
  LayerSpacing = [30]
  NumberDiameterOffset = 2#12.0@60.0
FEATURE [App::DocumentObjectGroupPython] BeamReinforcement008  # scripted group (container) (typed FeaturePython)
  Group = -> [Stirrups008,TopReinforcement008,BottomReinforcement008]
  ReinforcementGroups = -> [Stirrups008,TopReinforcement008,BottomReinforcement008]
FEATURE [Part::Part2DObjectPython] Wire879  # Draft 2D object (typed FeaturePython)
  Area = 0
  ChamferSize = 0
  Closed = false
  End = (5069.33,-265.444,2498.3)
  FilletRadius = 0
  Length = 890.697
  MakeFace = true
  Placement = pos=(-100,-15,0) rot=(0,0,1;0rad)
  Points = (7) [(5182.13,-236.302,2512.44),(5180,-276,2552.14),(5177.87,-276,2375),(5175.73,-64,2375),(5173.6,-64,2538),(5171.47,-290.142,2538),+1 more]
  Start = (5082.13,-251.302,2512.44)
  Subdivisions = 0
  Support = -> [Wall279]
FEATURE [Part::FeaturePython] Rebar027  label="Stirrup009"  # Arch/BIM 110 (typed FeaturePython)
  Amount = 5
  AmountCheck = false
  Base = -> Wire879
  BentAngle = 135
  BentFactor = 4
  BottomCover = 30
  Diameter = 8
  Direction = (-1,0,0)
  Distance = 0
  FrontCover = 100
  HorizontalArea = 0
  Host = -> Wall279
  IfcData = IfcUID=31rsnq52n3DxwBSiGvx1jF
  IfcType = 110
  LeftCover = 30
  Length = 890.697
  Mark = Stirrup009
  Material = -> Material010
  MoveBase = false
  MoveWithHost = false
  OffsetEnd = 104
  OffsetStart = 104
  PerimeterLength = 0
  PlacementList = 5 placements: arithmetic series from (-104,0,0) step (-241,0,0) to (-1068,0,0)
  RebarShape = 3
  RightCover = 30
  Rounding = 1.25
  Spacing = 241
  TopCover = 30
  TotalLength = 4453.49
  TrueSpacing = 300
  VerticalArea = 0
FEATURE [App::DocumentObjectGroupPython] Stirrups009  # scripted group (container) (typed FeaturePython)
  Group = -> [Rebar027]
  Stirrups = -> [Rebar027]
  StirrupsConfiguration = Two Legged Stirrups
FEATURE [Sketcher::SketchObject] Sketch344
  FullyConstrained = false
  MapMode = 5
  Placement = pos=(0,-325,2341) rot=(1,0,0;1.5708rad)
  Support = -> [Wall279]
  sketch-geometry (1):
    g0: LineSegment StartX=4100 StartY=187 StartZ=0 EndX=5120 EndY=187 EndZ=0
FEATURE [Part::FeaturePython] Rebar028  label="StraightRebar018"  # Arch/BIM 110 (typed FeaturePython)
  Amount = 2
  AmountCheck = true
  Base = -> Sketch344
  Cover = 38
  CoverAlong = Top Side
  Diameter = 12
  Direction = (0,0,0)
  Distance = 0
  FrontCover = 38
  HorizontalArea = 0
  Host = -> Wall279
  IfcData = IfcUID=3AflJxepXCVOa0re2f_fXP
  IfcType = 110
  LeftBottomCover = 60
  Length = 1020
  Mark = StraightRebar018
  Material = -> Material010
  MoveBase = false
  MoveWithHost = false
  OffsetEnd = 44
  OffsetStart = 44
  Orientation = Horizontal
  PerimeterLength = 0
  Placement = pos=(-125,-7.1e-15,0) rot=(0,0,1;0rad)
  PlacementList = 2 placements: [(0,44,-9.76996e-15),(0,236,-5.24025e-14)]
  RebarShape = 0
  RightTopCover = 60
  Rounding = 0
  Spacing = 192
  TotalLength = 2040
  TrueSpacing = 2
  VerticalArea = 0
FEATURE [App::DocumentObjectGroupPython] TopReinforcement009  # scripted group (container) (typed FeaturePython)
  Group = -> [Rebar028]
  LayerSpacing = [30]
  NumberDiameterOffset = 2#12.0@60.0
  TopRebars = -> [Rebar028]
FEATURE [Sketcher::SketchObject] Sketch345
  FullyConstrained = false
  MapMode = 5
  Placement = pos=(0,-325,2341) rot=(1,0,0;1.5708rad)
  Support = -> [Wall279]
  sketch-geometry (1):
    g0: LineSegment StartX=4100 StartY=44 StartZ=0 EndX=5120 EndY=44 EndZ=0
FEATURE [Part::FeaturePython] Rebar029  label="StraightRebar019"  # Arch/BIM 110 (typed FeaturePython)
  Amount = 2
  AmountCheck = true
  Base = -> Sketch345
  Cover = 38
  CoverAlong = Bottom Side
  Diameter = 12
  Direction = (0,0,0)
  Distance = 0
  FrontCover = 38
  HorizontalArea = 0
  Host = -> Wall279
  IfcData = IfcUID=2gFM5ezKfE0viRuku9MTTs
  IfcType = 110
  LeftBottomCover = 60
  Length = 1020
  Mark = StraightRebar019
  Material = -> Material010
  MoveBase = false
  MoveWithHost = false
  OffsetEnd = 44
  OffsetStart = 44
  Orientation = Horizontal
  PerimeterLength = 0
  Placement = pos=(-125,-7.1e-15,0) rot=(0,0,1;0rad)
  PlacementList = 2 placements: [(0,44,-9.76996e-15),(0,236,-5.24025e-14)]
  RebarShape = 0
  RightTopCover = 60
  Rounding = 0
  Spacing = 192
  TotalLength = 2040
  TrueSpacing = 2
  VerticalArea = 0
FEATURE [App::DocumentObjectGroupPython] BottomReinforcement009  # scripted group (container) (typed FeaturePython)
  BottomRebars = -> [Rebar029]
  Group = -> [Rebar029]
  LayerSpacing = [30]
  NumberDiameterOffset = 2#12.0@60.0
FEATURE [App::DocumentObjectGroupPython] BeamReinforcement009  # scripted group (container) (typed FeaturePython)
  Group = -> [Stirrups009,TopReinforcement009,BottomReinforcement009]
  ReinforcementGroups = -> [Stirrups009,TopReinforcement009,BottomReinforcement009]
FEATURE [App::DocumentObjectGroupPython] Stirrups010  # scripted group (container) (typed FeaturePython)
  StirrupsConfiguration = Two Legged Stirrups
FEATURE [App::DocumentObjectGroupPython] TopReinforcement010  # scripted group (container) (typed FeaturePython)
  LayerSpacing = [30]
  NumberDiameterOffset = 2#12.0@100.0
FEATURE [App::DocumentObjectGroupPython] BottomReinforcement010  # scripted group (container) (typed FeaturePython)
  LayerSpacing = [30]
  NumberDiameterOffset = 2#12.0@100.0
FEATURE [App::DocumentObjectGroupPython] BeamReinforcement010  # scripted group (container) (typed FeaturePython)
  Group = -> [Stirrups010,TopReinforcement010,BottomReinforcement010]
  ReinforcementGroups = -> [Stirrups010,TopReinforcement010,BottomReinforcement010]
FEATURE [App::DocumentObjectGroupPython] Stirrups011  # scripted group (container) (typed FeaturePython)
  StirrupsConfiguration = Two Legged Stirrups
FEATURE [App::DocumentObjectGroupPython] TopReinforcement011  # scripted group (container) (typed FeaturePython)
  LayerSpacing = [30]
  NumberDiameterOffset = 2#12.0@60.0
FEATURE [App::DocumentObjectGroupPython] BottomReinforcement011  # scripted group (container) (typed FeaturePython)
  LayerSpacing = [30]
  NumberDiameterOffset = 2#12.0@60.0
FEATURE [App::DocumentObjectGroupPython] BeamReinforcement011  # scripted group (container) (typed FeaturePython)
  Group = -> [Stirrups011,TopReinforcement011,BottomReinforcement011]
  ReinforcementGroups = -> [Stirrups011,TopReinforcement011,BottomReinforcement011]
FEATURE [Part::Part2DObjectPython] Line1579  # Draft 2D object (typed FeaturePython)
  Area = 0
  ChamferSize = 0
  Closed = false
  End = (12870,-345,0)
  FilletRadius = 0
  Length = 13220
  MakeFace = true
  Placement = pos=(-350,-345,0) rot=(0,0,1;0rad)
  Points = (2) [(0,0,0),(13220,3.97904e-13,0)]
  Start = (-350,-345,0)
  Subdivisions = 0
FEATURE [Part::FeaturePython] Wall291  label="Армпояс001"  # Arch/BIM 166 (typed FeaturePython)
  Align = 1
  Area = 1850800
  Base = -> Line1579
  BlockHeight = 0
  BlockLength = 0
  CountBroken = 0
  CountEntire = 0
  Face = 0
  GlobalId = 16TJfFXcP3X9E$rkeb5rWP
  Height = 140
  HorizontalArea = 2.3796e+06
  IfcData = IfcUID=16TJfFXcP3X9E$rkeb5rWP,+2 more (map truncated)
  IfcType = 166
  Joint = 0
  Length = 13220
  MakeBlocks = false
  Material = -> Material001
  MoveBase = false
  MoveWithHost = false
  Normal = (0,0,0)
  OffsetFirst = 0
  OffsetSecond = 0
  PerimeterLength = 26800
  Placement = pos=(0,0,3493) rot=(0,0,1;0rad)
  PredefinedType = 0
  VerticalArea = 3.752e+06
  Width = 180
FEATURE [Part::Part2DObjectPython] Line1580  # Draft 2D object (typed FeaturePython)
  Area = 0
  ChamferSize = 0
  Closed = true
  End = (-350,7805,0)
  FilletRadius = 0
  Length = 13220
  MakeFace = true
  Placement = pos=(-350,-315,0) rot=(0,0,1;0rad)
  Points = (2) [(13220,8120,0),(0,8120,0)]
  Start = (12870,7805,0)
  Subdivisions = 0
FEATURE [Part::FeaturePython] Wall292  label="Армпояс002"  # Arch/BIM 166 (typed FeaturePython)
  Align = 1
  Area = 1850800
  Base = -> Line1580
  BlockHeight = 0
  BlockLength = 0
  CountBroken = 0
  CountEntire = 0
  Face = 0
  GlobalId = 0QynjLo$PD1uHQZI1aWnKI
  Height = 140
  HorizontalArea = 2.3796e+06
  IfcData = IfcUID=0QynjLo$PD1uHQZI1aWnKI,+2 more (map truncated)
  IfcType = 166
  Joint = 0
  Length = 13220
  MakeBlocks = false
  Material = -> Material001
  MoveBase = false
  MoveWithHost = false
  Normal = (0,0,0)
  OffsetFirst = 0
  OffsetSecond = 0
  PerimeterLength = 26800
  Placement = pos=(0,0,3493) rot=(0,0,1;0rad)
  PredefinedType = 0
  VerticalArea = 3.752e+06
  Width = 180
FEATURE [Part::Part2DObjectPython] Line1581  # Draft 2D object (typed FeaturePython)
  Area = 0
  ChamferSize = 0
  Closed = true
  End = (-350,-165,0)
  FilletRadius = 0
  Length = 7790
  MakeFace = true
  Placement = pos=(-350,-330,0) rot=(0,0,1;0rad)
  Points = (2) [(0,7955,0),(0,165,0)]
  Start = (-350,7625,0)
  Subdivisions = 0
FEATURE [Part::FeaturePython] Wall293  label="Армпояс003"  # Arch/BIM 166 (typed FeaturePython)
  Align = 1
  Area = 1090600
  Base = -> Line1581
  BlockHeight = 0
  BlockLength = 0
  CountBroken = 0
  CountEntire = 0
  Face = 0
  GlobalId = 3eSRug_un8VgtGtFI5hYOD
  Height = 140
  HorizontalArea = 1402200
  IfcData = IfcUID=3eSRug_un8VgtGtFI5hYOD,+2 more (map truncated)
  IfcType = 166
  Joint = 0
  Length = 7790
  MakeBlocks = false
  Material = -> Material001
  MoveBase = false
  MoveWithHost = false
  Normal = (0,0,0)
  OffsetFirst = 0
  OffsetSecond = 0
  PerimeterLength = 15940
  Placement = pos=(0,0,3493) rot=(0,0,1;0rad)
  PredefinedType = 0
  VerticalArea = 2231600
  Width = 180
FEATURE [Part::Part2DObjectPython] Line1582  # Draft 2D object (typed FeaturePython)
  Area = 0
  ChamferSize = 0
  Closed = true
  End = (12870,7625,0)
  FilletRadius = 0
  Length = 7790
  MakeFace = true
  Placement = pos=(-350,-330,0) rot=(0,0,1;0rad)
  Points = (2) [(13220,165,0),(13220,7955,0)]
  Start = (12870,-165,0)
  Subdivisions = 0
FEATURE [Part::FeaturePython] Wall294  label="Армпояс004"  # Arch/BIM 166 (typed FeaturePython)
  Align = 1
  Area = 1090600
  Base = -> Line1582
  BlockHeight = 0
  BlockLength = 0
  CountBroken = 0
  CountEntire = 0
  Face = 0
  GlobalId = 1hI4wR2SfDawL0z1dNH$cq
  Height = 140
  HorizontalArea = 1402200
  IfcData = IfcUID=1hI4wR2SfDawL0z1dNH$cq,+2 more (map truncated)
  IfcType = 166
  Joint = 0
  Length = 7790
  MakeBlocks = false
  Material = -> Material001
  MoveBase = false
  MoveWithHost = false
  Normal = (0,0,0)
  OffsetFirst = 0
  OffsetSecond = 0
  PerimeterLength = 15940
  Placement = pos=(0,0,3493) rot=(0,0,1;0rad)
  PredefinedType = 0
  VerticalArea = 2231600
  Width = 180
FEATURE [Part::Part2DObjectPython] Wire883  # Draft 2D object (typed FeaturePython)
  Area = 0
  ChamferSize = 0
  Closed = false
  End = (12859.1,7673.97,3572.72)
  FilletRadius = 0
  Length = 573.429
  MakeFace = true
  Placement = pos=(0,15,0) rot=(0,0,1;0rad)
  Points = (7) [(12872.2,7670.28,3584.03),(12870,7634,3620.31),(12867.8,7634,3517),(12865.7,7766,3517),(12863.5,7766,3609),(12861.3,7622.69,3609),+1 more]
  Start = (12872.2,7685.28,3584.03)
  Subdivisions = 0
  Support = -> [Wall292]
FEATURE [Part::FeaturePython] Rebar036  label="Stirrup012"  # Arch/BIM 110 (typed FeaturePython)
  Amount = 28
  AmountCheck = false
  Base = -> Wire883
  BentAngle = 135
  BentFactor = 4
  BottomCover = 20
  Diameter = 8
  Direction = (-1,0,0)
  Distance = 0
  FrontCover = 100
  HorizontalArea = 0
  Host = -> Wall292
  IfcData = IfcUID=3K6Qvq_$X52hEgXW4rU6QA
  IfcType = 110
  LeftCover = 20
  Length = 573.429
  Mark = Stirrup012
  Material = -> Material010
  MoveBase = false
  MoveWithHost = false
  OffsetEnd = 104
  OffsetStart = 104
  PerimeterLength = 0
  PlacementList = 28 placements: arithmetic series from (-104,0,0) step (-481.63,0,0) to (-13108,0,0)
  RebarShape = 3
  RightCover = 20
  Rounding = 1
  Spacing = 481.63
  TopCover = 20
  TotalLength = 16056
  TrueSpacing = 500
  VerticalArea = 0
FEATURE [App::DocumentObjectGroupPython] Stirrups012  # scripted group (container) (typed FeaturePython)
  Group = -> [Rebar036]
  Stirrups = -> [Rebar036]
  StirrupsConfiguration = Two Legged Stirrups
FEATURE [Sketcher::SketchObject] Sketch350
  FullyConstrained = false
  MapMode = 5
  Placement = pos=(0,7625,3493) rot=(1,0,0;1.5708rad)
  Support = -> [Wall292]
  sketch-geometry (1):
    g0: LineSegment StartX=-290 StartY=108 StartZ=0 EndX=12810 EndY=108 EndZ=0
FEATURE [Part::FeaturePython] Rebar037  label="StraightRebar024"  # Arch/BIM 110 (typed FeaturePython)
  Amount = 2
  AmountCheck = true
  Base = -> Sketch350
  Cover = 28
  CoverAlong = Top Side
  Diameter = 8
  Direction = (0,0,0)
  Distance = 0
  FrontCover = 28
  HorizontalArea = 0
  Host = -> Wall292
  IfcData = IfcUID=140U$9PZ1AHwJYsE$SOkWK
  IfcType = 110
  LeftBottomCover = 60
  Length = 13100
  Mark = StraightRebar024
  Material = -> Material010
  MoveBase = false
  MoveWithHost = false
  OffsetEnd = 32
  OffsetStart = 32
  Orientation = Horizontal
  PerimeterLength = 0
  PlacementList = 2 placements: [(0,32,-7.10543e-15),(0,148,-3.28626e-14)]
  RebarShape = 0
  RightTopCover = 60
  Rounding = 0
  Spacing = 116
  TotalLength = 26200
  TrueSpacing = 2
  VerticalArea = 0
FEATURE [App::DocumentObjectGroupPython] TopReinforcement012  # scripted group (container) (typed FeaturePython)
  Group = -> [Rebar037]
  LayerSpacing = [30]
  NumberDiameterOffset = 2#8.0@60.0
  TopRebars = -> [Rebar037]
FEATURE [Sketcher::SketchObject] Sketch351
  FullyConstrained = false
  MapMode = 5
  Placement = pos=(0,7625,3493) rot=(1,0,0;1.5708rad)
  Support = -> [Wall292]
  sketch-geometry (1):
    g0: LineSegment StartX=-290 StartY=32 StartZ=0 EndX=12810 EndY=32 EndZ=0
FEATURE [Part::FeaturePython] Rebar038  label="StraightRebar025"  # Arch/BIM 110 (typed FeaturePython)
  Amount = 2
  AmountCheck = true
  Base = -> Sketch351
  Cover = 28
  CoverAlong = Bottom Side
  Diameter = 8
  Direction = (0,0,0)
  Distance = 0
  FrontCover = 28
  HorizontalArea = 0
  Host = -> Wall292
  IfcData = IfcUID=2fxrXb7T52vBDIZ$F2twXk
  IfcType = 110
  LeftBottomCover = 60
  Length = 13100
  Mark = StraightRebar025
  Material = -> Material010
  MoveBase = false
  MoveWithHost = false
  OffsetEnd = 32
  OffsetStart = 32
  Orientation = Horizontal
  PerimeterLength = 0
  PlacementList = 2 placements: [(0,32,-7.10543e-15),(0,148,-3.28626e-14)]
  RebarShape = 0
  RightTopCover = 60
  Rounding = 0
  Spacing = 116
  TotalLength = 26200
  TrueSpacing = 2
  VerticalArea = 0
FEATURE [App::DocumentObjectGroupPython] BottomReinforcement012  # scripted group (container) (typed FeaturePython)
  BottomRebars = -> [Rebar038]
  Group = -> [Rebar038]
  LayerSpacing = [30]
  NumberDiameterOffset = 2#8.0@60.0
FEATURE [App::DocumentObjectGroupPython] BeamReinforcement012  label="BeamReinforcement013"  # scripted group (container) (typed FeaturePython)
  Group = -> [Stirrups012,TopReinforcement012,BottomReinforcement012]
  ReinforcementGroups = -> [Stirrups012,TopReinforcement012,BottomReinforcement012]
FEATURE [Part::Part2DObjectPython] Wire884  # Draft 2D object (typed FeaturePython)
  Area = 0
  ChamferSize = 0
  Closed = false
  End = (12859.1,-296.029,3572.72)
  FilletRadius = 0
  Length = 573.429
  MakeFace = true
  Placement = pos=(0,-15,0) rot=(0,0,1;0rad)
  Points = (7) [(12872.2,-269.716,3584.03),(12870,-306,3620.31),(12867.8,-306,3517),(12865.7,-174,3517),(12863.5,-174,3609),(12861.3,-317.314,3609),+1 more]
  Start = (12872.2,-284.716,3584.03)
  Subdivisions = 0
  Support = -> [Wall291]
FEATURE [Part::FeaturePython] Rebar039  label="Stirrup013"  # Arch/BIM 110 (typed FeaturePython)
  Amount = 28
  AmountCheck = false
  Base = -> Wire884
  BentAngle = 135
  BentFactor = 4
  BottomCover = 20
  Diameter = 8
  Direction = (-1,0,0)
  Distance = 0
  FrontCover = 100
  HorizontalArea = 0
  Host = -> Wall291
  IfcData = IfcUID=3qYUM6LlvEqR380m34$EFs
  IfcType = 110
  LeftCover = 20
  Length = 573.429
  Mark = Stirrup013
  Material = -> Material010
  MoveBase = false
  MoveWithHost = false
  OffsetEnd = 104
  OffsetStart = 104
  PerimeterLength = 0
  PlacementList = 28 placements: arithmetic series from (-104,0,0) step (-481.63,0,0) to (-13108,0,0)
  RebarShape = 3
  RightCover = 20
  Rounding = 1
  Spacing = 481.63
  TopCover = 20
  TotalLength = 16056
  TrueSpacing = 500
  VerticalArea = 0
FEATURE [App::DocumentObjectGroupPython] Stirrups013  # scripted group (container) (typed FeaturePython)
  Group = -> [Rebar039]
  Stirrups = -> [Rebar039]
  StirrupsConfiguration = Two Legged Stirrups
FEATURE [Sketcher::SketchObject] Sketch352
  FullyConstrained = false
  MapMode = 5
  Placement = pos=(1.03e-14,-345,3493) rot=(1,0,0;1.5708rad)
  Support = -> [Wall291]
  sketch-geometry (1):
    g0: LineSegment StartX=-290 StartY=108 StartZ=0 EndX=12810 EndY=108 EndZ=0
FEATURE [Part::FeaturePython] Rebar040  label="StraightRebar026"  # Arch/BIM 110 (typed FeaturePython)
  Amount = 2
  AmountCheck = true
  Base = -> Sketch352
  Cover = 28
  CoverAlong = Top Side
  Diameter = 8
  Direction = (0,0,0)
  Distance = 0
  FrontCover = 28
  HorizontalArea = 0
  Host = -> Wall291
  IfcData = IfcUID=0p007rg9H619hFCHvEy_jd
  IfcType = 110
  LeftBottomCover = 60
  Length = 13100
  Mark = StraightRebar026
  Material = -> Material010
  MoveBase = false
  MoveWithHost = false
  OffsetEnd = 32
  OffsetStart = 32
  Orientation = Horizontal
  PerimeterLength = 0
  PlacementList = 2 placements: [(-9.63156e-16,32,-7.10543e-15),(-4.4546e-15,148,-3.28626e-14)]
  RebarShape = 0
  RightTopCover = 60
  Rounding = 0
  Spacing = 116
  TotalLength = 26200
  TrueSpacing = 2
  VerticalArea = 0
FEATURE [App::DocumentObjectGroupPython] TopReinforcement013  # scripted group (container) (typed FeaturePython)
  Group = -> [Rebar040]
  LayerSpacing = [30]
  NumberDiameterOffset = 2#8.0@60.0
  TopRebars = -> [Rebar040]
FEATURE [Sketcher::SketchObject] Sketch353
  FullyConstrained = false
  MapMode = 5
  Placement = pos=(1.03e-14,-345,3493) rot=(1,0,0;1.5708rad)
  Support = -> [Wall291]
  sketch-geometry (1):
    g0: LineSegment StartX=-290 StartY=32 StartZ=0 EndX=12810 EndY=32 EndZ=0
FEATURE [Part::FeaturePython] Rebar041  label="StraightRebar027"  # Arch/BIM 110 (typed FeaturePython)
  Amount = 2
  AmountCheck = true
  Base = -> Sketch353
  Cover = 28
  CoverAlong = Bottom Side
  Diameter = 8
  Direction = (0,0,0)
  Distance = 0
  FrontCover = 28
  HorizontalArea = 0
  Host = -> Wall291
  IfcData = IfcUID=3WhL2Y$11658LLbofuE694
  IfcType = 110
  LeftBottomCover = 60
  Length = 13100
  Mark = StraightRebar027
  Material = -> Material010
  MoveBase = false
  MoveWithHost = false
  OffsetEnd = 32
  OffsetStart = 32
  Orientation = Horizontal
  PerimeterLength = 0
  PlacementList = 2 placements: [(-9.63156e-16,32,-7.10543e-15),(-4.4546e-15,148,-3.28626e-14)]
  RebarShape = 0
  RightTopCover = 60
  Rounding = 0
  Spacing = 116
  TotalLength = 26200
  TrueSpacing = 2
  VerticalArea = 0
FEATURE [App::DocumentObjectGroupPython] BottomReinforcement013  # scripted group (container) (typed FeaturePython)
  BottomRebars = -> [Rebar041]
  Group = -> [Rebar041]
  LayerSpacing = [30]
  NumberDiameterOffset = 2#8.0@60.0
FEATURE [App::DocumentObjectGroupPython] BeamReinforcement013  label="BeamReinforcement014"  # scripted group (container) (typed FeaturePython)
  Group = -> [Stirrups013,TopReinforcement013,BottomReinforcement013]
  ReinforcementGroups = -> [Stirrups013,TopReinforcement013,BottomReinforcement013]
FEATURE [Part::Part2DObjectPython] Wire886  # Draft 2D object (typed FeaturePython)
  Area = 0
  ChamferSize = 0
  Closed = false
  End = (12739,7599.14,3572.72)
  FilletRadius = 0
  Length = 573.429
  MakeFace = true
  Points = (7) [(12750.3,7612.17,3584.03),(12714,7610,3620.31),(12714,7607.83,3517),(12846,7605.66,3517),(12846,7603.49,3609),(12702.7,7601.31,3609),+1 more]
  Start = (12750.3,7612.17,3584.03)
  Subdivisions = 0
  Support = -> [Wall294]
FEATURE [Part::FeaturePython] Rebar042  label="Stirrup014"  # Arch/BIM 110 (typed FeaturePython)
  Amount = 17
  AmountCheck = false
  Base = -> Wire886
  BentAngle = 135
  BentFactor = 4
  BottomCover = 20
  Diameter = 8
  Direction = (0,-1,0)
  Distance = 0
  FrontCover = 100
  HorizontalArea = 0
  Host = -> Wall294
  IfcData = IfcUID=2hh8STxOfCgxszMIN_Kbtk
  IfcType = 110
  LeftCover = 20
  Length = 573.429
  Mark = Stirrup014
  Material = -> Material010
  MoveBase = false
  MoveWithHost = false
  OffsetEnd = 104
  OffsetStart = 104
  PerimeterLength = 0
  PlacementList = 17 placements: arithmetic series from (0,-104,0) step (0,-473.375,0) to (0,-7678,0)
  RebarShape = 3
  RightCover = 20
  Rounding = 1
  Spacing = 473.375
  TopCover = 20
  TotalLength = 9748.3
  TrueSpacing = 500
  VerticalArea = 0
FEATURE [App::DocumentObjectGroupPython] Stirrups014  # scripted group (container) (typed FeaturePython)
  Group = -> [Rebar042]
  Stirrups = -> [Rebar042]
  StirrupsConfiguration = Two Legged Stirrups
FEATURE [Sketcher::SketchObject] Sketch360
  FullyConstrained = false
  MapMode = 5
  Placement = pos=(12870,0,3493) rot=(0.57735,0.57735,0.57735;2.0944rad)
  Support = -> [Wall294]
  sketch-geometry (1):
    g0: LineSegment StartX=-300 StartY=108 StartZ=0 EndX=7760 EndY=108 EndZ=0
FEATURE [Part::FeaturePython] Rebar045  label="StraightRebar030"  # Arch/BIM 110 (typed FeaturePython)
  Amount = 2
  AmountCheck = true
  Base = -> Sketch360
  Cover = 28
  CoverAlong = Top Side
  Diameter = 8
  Direction = (0,0,0)
  Distance = 0
  FrontCover = 28
  HorizontalArea = 0
  Host = -> Wall294
  IfcData = IfcUID=0$9Ki$QzP9MxF8QuB$I3Ex
  IfcType = 110
  LeftBottomCover = -150
  Length = 8060
  Mark = StraightRebar030
  Material = -> Material010
  MoveBase = false
  MoveWithHost = false
  OffsetEnd = 32
  OffsetStart = 32
  Orientation = Horizontal
  PerimeterLength = 0
  PlacementList = 2 placements: [(-32,0,0),(-148,0,0)]
  RebarShape = 0
  RightTopCover = -150
  Rounding = 0
  Spacing = 116
  TotalLength = 16120
  TrueSpacing = 2
  VerticalArea = 0
FEATURE [App::DocumentObjectGroupPython] TopReinforcement014  # scripted group (container) (typed FeaturePython)
  Group = -> [Rebar045]
  LayerSpacing = [30]
  NumberDiameterOffset = 2#8.0@-150.0
  TopRebars = -> [Rebar045]
FEATURE [Sketcher::SketchObject] Sketch361
  FullyConstrained = false
  MapMode = 5
  Placement = pos=(12870,0,3493) rot=(0.57735,0.57735,0.57735;2.0944rad)
  Support = -> [Wall294]
  sketch-geometry (1):
    g0: LineSegment StartX=-300 StartY=32 StartZ=0 EndX=7760 EndY=32 EndZ=0
FEATURE [Part::FeaturePython] Rebar046  label="StraightRebar031"  # Arch/BIM 110 (typed FeaturePython)
  Amount = 2
  AmountCheck = true
  Base = -> Sketch361
  Cover = 28
  CoverAlong = Bottom Side
  Diameter = 8
  Direction = (0,0,0)
  Distance = 0
  FrontCover = 28
  HorizontalArea = 0
  Host = -> Wall294
  IfcData = IfcUID=3LTvHi1MTDgRMXNthAh_XG
  IfcType = 110
  LeftBottomCover = -150
  Length = 8060
  Mark = StraightRebar031
  Material = -> Material010
  MoveBase = false
  MoveWithHost = false
  OffsetEnd = 32
  OffsetStart = 32
  Orientation = Horizontal
  PerimeterLength = 0
  PlacementList = 2 placements: [(-32,0,0),(-148,0,0)]
  RebarShape = 0
  RightTopCover = -150
  Rounding = 0
  Spacing = 116
  TotalLength = 16120
  TrueSpacing = 2
  VerticalArea = 0
FEATURE [App::DocumentObjectGroupPython] BottomReinforcement014  # scripted group (container) (typed FeaturePython)
  BottomRebars = -> [Rebar046]
  Group = -> [Rebar046]
  LayerSpacing = [30]
  NumberDiameterOffset = 2#8.0@-150.0
FEATURE [App::DocumentObjectGroupPython] BeamReinforcement014  label="BeamReinforcement015"  # scripted group (container) (typed FeaturePython)
  Group = -> [Stirrups014,TopReinforcement014,BottomReinforcement014]
  ReinforcementGroups = -> [Stirrups014,TopReinforcement014,BottomReinforcement014]
FEATURE [Part::Part2DObjectPython] Wire887  # Draft 2D object (typed FeaturePython)
  Area = 0
  ChamferSize = 0
  Closed = false
  End = (-301.029,7599.14,3572.72)
  FilletRadius = 0
  Length = 573.429
  MakeFace = true
  Points = (7) [(-289.716,7612.17,3584.03),(-326,7610,3620.31),(-326,7607.83,3517),(-194,7605.66,3517),(-194,7603.49,3609),(-337.314,7601.31,3609),+1 more]
  Start = (-289.716,7612.17,3584.03)
  Subdivisions = 0
  Support = -> [Wall293]
FEATURE [Part::FeaturePython] Rebar047  label="Stirrup015"  # Arch/BIM 110 (typed FeaturePython)
  Amount = 17
  AmountCheck = false
  Base = -> Wire887
  BentAngle = 135
  BentFactor = 4
  BottomCover = 20
  Diameter = 8
  Direction = (0,-1,0)
  Distance = 0
  FrontCover = 100
  HorizontalArea = 0
  Host = -> Wall293
  IfcData = IfcUID=3cNbPT2cr1VeJ7E6rFKLiC
  IfcType = 110
  LeftCover = 20
  Length = 573.429
  Mark = Stirrup015
  Material = -> Material010
  MoveBase = false
  MoveWithHost = false
  OffsetEnd = 104
  OffsetStart = 104
  PerimeterLength = 0
  PlacementList = 17 placements: arithmetic series from (0,-104,0) step (0,-473.375,0) to (0,-7678,0)
  RebarShape = 3
  RightCover = 20
  Rounding = 1
  Spacing = 473.375
  TopCover = 20
  TotalLength = 9748.3
  TrueSpacing = 500
  VerticalArea = 0
FEATURE [App::DocumentObjectGroupPython] Stirrups015  # scripted group (container) (typed FeaturePython)
  Group = -> [Rebar047]
  Stirrups = -> [Rebar047]
  StirrupsConfiguration = Two Legged Stirrups
FEATURE [Sketcher::SketchObject] Sketch362
  FullyConstrained = false
  MapMode = 5
  Placement = pos=(-170,0,3493) rot=(0.57735,0.57735,0.57735;2.0944rad)
  Support = -> [Wall293]
  sketch-geometry (1):
    g0: LineSegment StartX=-300 StartY=108 StartZ=0 EndX=7760 EndY=108 EndZ=0
FEATURE [Part::FeaturePython] Rebar048  label="StraightRebar032"  # Arch/BIM 110 (typed FeaturePython)
  Amount = 2
  AmountCheck = true
  Base = -> Sketch362
  Cover = 28
  CoverAlong = Top Side
  Diameter = 8
  Direction = (0,0,0)
  Distance = 0
  FrontCover = 28
  HorizontalArea = 0
  Host = -> Wall293
  IfcData = IfcUID=3g7bd8dkj1MPydz_teGZJR
  IfcType = 110
  LeftBottomCover = -150
  Length = 8060
  Mark = StraightRebar032
  Material = -> Material010
  MoveBase = false
  MoveWithHost = false
  OffsetEnd = 32
  OffsetStart = 32
  Orientation = Horizontal
  PerimeterLength = 0
  PlacementList = 2 placements: [(-32,0,0),(-148,0,0)]
  RebarShape = 0
  RightTopCover = -150
  Rounding = 0
  Spacing = 116
  TotalLength = 16120
  TrueSpacing = 2
  VerticalArea = 0
FEATURE [App::DocumentObjectGroupPython] TopReinforcement015  # scripted group (container) (typed FeaturePython)
  Group = -> [Rebar048]
  LayerSpacing = [30]
  NumberDiameterOffset = 2#8.0@-150.0
  TopRebars = -> [Rebar048]
FEATURE [Sketcher::SketchObject] Sketch363
  FullyConstrained = false
  MapMode = 5
  Placement = pos=(-170,0,3493) rot=(0.57735,0.57735,0.57735;2.0944rad)
  Support = -> [Wall293]
  sketch-geometry (1):
    g0: LineSegment StartX=-300 StartY=32 StartZ=0 EndX=7760 EndY=32 EndZ=0
FEATURE [Part::FeaturePython] Rebar049  label="StraightRebar033"  # Arch/BIM 110 (typed FeaturePython)
  Amount = 2
  AmountCheck = true
  Base = -> Sketch363
  Cover = 28
  CoverAlong = Bottom Side
  Diameter = 8
  Direction = (0,0,0)
  Distance = 0
  FrontCover = 28
  HorizontalArea = 0
  Host = -> Wall293
  IfcData = IfcUID=0PUrgqHLj2fuIB$J8Xlgq8
  IfcType = 110
  LeftBottomCover = -150
  Length = 8060
  Mark = StraightRebar033
  Material = -> Material010
  MoveBase = false
  MoveWithHost = false
  OffsetEnd = 32
  OffsetStart = 32
  Orientation = Horizontal
  PerimeterLength = 0
  PlacementList = 2 placements: [(-32,0,0),(-148,0,0)]
  RebarShape = 0
  RightTopCover = -150
  Rounding = 0
  Spacing = 116
  TotalLength = 16120
  TrueSpacing = 2
  VerticalArea = 0
FEATURE [App::DocumentObjectGroupPython] BottomReinforcement015  # scripted group (container) (typed FeaturePython)
  BottomRebars = -> [Rebar049]
  Group = -> [Rebar049]
  LayerSpacing = [30]
  NumberDiameterOffset = 2#8.0@-150.0
FEATURE [App::DocumentObjectGroupPython] BeamReinforcement015  label="BeamReinforcement016"  # scripted group (container) (typed FeaturePython)
  Group = -> [Stirrups015,TopReinforcement015,BottomReinforcement015]
  ReinforcementGroups = -> [Stirrups015,TopReinforcement015,BottomReinforcement015]
FEATURE [App::GeometryPython] BuildingPart098  label="Армирование пояса"  # Arch/BIM 111 (typed FeaturePython)
  Area = 0
  GlobalId = 2PxC9szOX0IvFjy5VtbcaU
  Group = -> [BeamReinforcement012,BeamReinforcement013,BeamReinforcement014,BeamReinforcement015]
  Height = 0
  HeightPropagate = true
  IfcData = IfcUID=2PxC9szOX0IvFjy5VtbcaU,+2 more (map truncated)
  IfcType = 111
  LevelOffset = 0
FEATURE [App::GeometryPython] BuildingPart097  label="Армпояс"  # Arch/BIM 52 (typed FeaturePython)
  Area = 5882800
  GlobalId = 2GdC2J3IrBqAFOXYdeO3oM
  Group = -> [Wall291,Wall292,Wall293,Wall294,BuildingPart098]
  Height = 0
  HeightPropagate = true
  IfcData = IfcUID=2GdC2J3IrBqAFOXYdeO3oM,+2 more (map truncated)
  IfcType = 52
  LevelOffset = 0
FEATURE [App::FeaturePython] Dimension028  # Draft dimension (typed FeaturePython)
  Diameter = false
  Dimline = (-1200,2335,0)
  Direction = (0,0,0)
  Distance = 1345
  End = (-1836.7,3680,0)
  Normal = (0,0,1)
  Start = (-1836.7,2335,0)
FEATURE [Part::Part2DObjectPython] Circle122  label="Circle123"  # Draft 2D object (typed FeaturePython)
  Area = 0
  FirstAngle = 0
  LastAngle = 0
  MakeFace = false
  Placement = pos=(-2036.7,7695,0) rot=(0,0,1;0rad)
  Radius = 200
FEATURE [Part::Part2DObjectPython] ShapeString192  # Draft 2D object (typed FeaturePython)
  FontFile = <path>
  Placement = pos=(-2130.05,7594.61,0) rot=(0,0,1;0rad)
  Size = 200
  String = D
  Tracking = 0
FEATURE [Part::Part2DObjectPython] Circle123  label="Circle124"  # Draft 2D object (typed FeaturePython)
  Area = 0
  FirstAngle = 0
  LastAngle = 0
  MakeFace = false
  Placement = pos=(-2036.7,3680,0) rot=(0,0,1;0rad)
  Radius = 200
FEATURE [Part::Part2DObjectPython] ShapeString193  # Draft 2D object (typed FeaturePython)
  FontFile = <path>
  Placement = pos=(-2133.13,3586.85,0) rot=(0,0,1;0rad)
  Size = 200
  String = C
  Tracking = 0
FEATURE [Part::Part2DObjectPython] Circle124  label="Circle125"  # Draft 2D object (typed FeaturePython)
  Area = 0
  FirstAngle = 0
  LastAngle = 0
  MakeFace = false
  Placement = pos=(-2036.7,2335,0) rot=(0,0,1;0rad)
  Radius = 200
FEATURE [Part::Part2DObjectPython] ShapeString194  # Draft 2D object (typed FeaturePython)
  FontFile = <path>
  Placement = pos=(-2116.38,2246.01,0) rot=(0,0,1;0rad)
  Size = 200
  String = B
  Tracking = 0
FEATURE [Part::Part2DObjectPython] Circle125  label="Circle126"  # Draft 2D object (typed FeaturePython)
  Area = 0
  FirstAngle = 0
  LastAngle = 0
  MakeFace = false
  Placement = pos=(-2036.7,-235,0) rot=(0,0,1;0rad)
  Radius = 200
FEATURE [Part::Part2DObjectPython] ShapeString195  # Draft 2D object (typed FeaturePython)
  FontFile = <path>
  Placement = pos=(-2124.02,-327.945,0) rot=(0,0,1;0rad)
  Size = 200
  String = A
  Tracking = 0
FEATURE [Part::Part2DObjectPython] Circle126  label="Circle127"  # Draft 2D object (typed FeaturePython)
  Area = 0
  FirstAngle = 0
  LastAngle = 0
  MakeFace = false
  Placement = pos=(-240,9706.46,0) rot=(0,0,1;0rad)
  Radius = 200
FEATURE [Part::Part2DObjectPython] ShapeString196  # Draft 2D object (typed FeaturePython)
  FontFile = <path>
  Placement = pos=(-319.076,9614.22,0) rot=(0,0,1;0rad)
  Size = 200
  String = 1
  Tracking = 0
FEATURE [Part::Part2DObjectPython] Circle127  label="Circle128"  # Draft 2D object (typed FeaturePython)
  Area = 0
  FirstAngle = 0
  LastAngle = 0
  MakeFace = false
  Placement = pos=(3450,9706.46,0) rot=(0,0,1;0rad)
  Radius = 200
FEATURE [Part::Part2DObjectPython] ShapeString197  # Draft 2D object (typed FeaturePython)
  FontFile = <path>
  Placement = pos=(3367.38,9622.97,0) rot=(0,0,1;0rad)
  Size = 200
  String = 2
  Tracking = 0
FEATURE [Part::Part2DObjectPython] Circle128  label="Circle129"  # Draft 2D object (typed FeaturePython)
  Area = 0
  FirstAngle = 0
  LastAngle = 0
  MakeFace = false
  Placement = pos=(4050,9706.46,0) rot=(0,0,1;0rad)
  Radius = 200
FEATURE [Part::Part2DObjectPython] ShapeString198  # Draft 2D object (typed FeaturePython)
  FontFile = <path>
  Placement = pos=(3978.07,9610.28,0) rot=(0,0,1;0rad)
  Size = 200
  String = 3
  Tracking = 0
FEATURE [Part::Part2DObjectPython] Circle129  label="Circle130"  # Draft 2D object (typed FeaturePython)
  Area = 0
  FirstAngle = 0
  LastAngle = 0
  MakeFace = false
  Placement = pos=(4870,9706.46,0) rot=(0,0,1;0rad)
  Radius = 200
FEATURE [Part::Part2DObjectPython] ShapeString199  # Draft 2D object (typed FeaturePython)
  FontFile = <path>
  Placement = pos=(4784.17,9612.89,0) rot=(0,0,1;0rad)
  Size = 200
  String = 4
  Tracking = 0
FEATURE [Part::Part2DObjectPython] Circle130  label="Circle131"  # Draft 2D object (typed FeaturePython)
  Area = 0
  FirstAngle = 0
  LastAngle = 0
  MakeFace = false
  Placement = pos=(6890,9706.46,0) rot=(0,0,1;0rad)
  Radius = 200
FEATURE [Part::Part2DObjectPython] ShapeString200  # Draft 2D object (typed FeaturePython)
  FontFile = <path>
  Placement = pos=(6820.3,9606.58,0) rot=(0,0,1;0rad)
  Size = 200
  String = 5
  Tracking = 0
FEATURE [Part::Part2DObjectPython] Circle131  label="Circle132"  # Draft 2D object (typed FeaturePython)
  Area = 0
  FirstAngle = 0
  LastAngle = 0
  MakeFace = false
  Placement = pos=(7400,9706.46,0) rot=(0,0,1;0rad)
  Radius = 200
FEATURE [Part::Part2DObjectPython] ShapeString201  # Draft 2D object (typed FeaturePython)
  FontFile = <path>
  Placement = pos=(7325.5,9616.19,0) rot=(0,0,1;0rad)
  Size = 200
  String = 6
  Tracking = 0
FEATURE [Part::Part2DObjectPython] Circle132  label="Circle133"  # Draft 2D object (typed FeaturePython)
  Area = 0
  FirstAngle = 0
  LastAngle = 0
  MakeFace = false
  Placement = pos=(7910,9706.46,0) rot=(0,0,1;0rad)
  Radius = 200
FEATURE [Part::Part2DObjectPython] ShapeString202  # Draft 2D object (typed FeaturePython)
  FontFile = <path>
  Placement = pos=(7839.18,9604.4,0) rot=(0,0,1;0rad)
  Size = 200
  String = 7
  Tracking = 0
FEATURE [Part::Part2DObjectPython] Circle133  label="Circle134"  # Draft 2D object (typed FeaturePython)
  Area = 0
  FirstAngle = 0
  LastAngle = 0
  MakeFace = false
  Placement = pos=(9500,9706.46,0) rot=(0,0,1;0rad)
  Radius = 200
FEATURE [Part::Part2DObjectPython] ShapeString203  # Draft 2D object (typed FeaturePython)
  FontFile = <path>
  Placement = pos=(9427.59,9608.74,0) rot=(0,0,1;0rad)
  Size = 200
  String = 8
  Tracking = 0
FEATURE [Part::Part2DObjectPython] Circle134  label="Circle135"  # Draft 2D object (typed FeaturePython)
  Area = 0
  FirstAngle = 0
  LastAngle = 0
  MakeFace = false
  Placement = pos=(12760,9706.46,0) rot=(0,0,1;0rad)
  Radius = 200
FEATURE [Part::Part2DObjectPython] ShapeString204  # Draft 2D object (typed FeaturePython)
  FontFile = <path>
  Placement = pos=(12685.6,9616.32,0) rot=(0,0,1;0rad)
  Size = 200
  String = 9
  Tracking = 0
FEATURE [TechDraw::DrawViewAnnotation] Annotation007
  Font = DejaVu Sans
  LineSpace = 80
  LockPosition = false
  MaxWidth = -1
  Rotation = 0
  ScaleType = 0
  Text = \u041f\u043b\u0430\u043d \u043f\u0435\u0440\u0432\u043e\u0433\u043e \u044d\u0442\u0430\u0436\u0430  \u043d\u0430 \u043e\u0442\u043c\u0435\u0442\u043a\u0435 +0.0
  TextSize = 6
  TextStyle = 0
  X = 211.887
  Y = 279.654
FEATURE [TechDraw::DrawViewAnnotation] Annotation008  label="a_085"
  Font = DejaVu Sans
  LineSpace = 80
  LockPosition = true
  MaxWidth = -1
  Rotation = 0
  ScaleType = 0
  Text = \u0420\u0430\u0437\u0440\u0435\u0437 \u043f\u043e \u0410-\u0410
  TextSize = 6
  TextStyle = 0
  X = 203.183
  Y = 279.058
FEATURE [App::FeaturePython] Dimension029  # Draft dimension (typed FeaturePython)
  Diameter = false
  Dimline = (0,5100,-400)
  Direction = (0,0,0)
  Distance = 200
  End = (0,8000,0)
  Normal = (1,0,0)
  Start = (0,8000,-200)
FEATURE [Part::Part2DObjectPython] Wire462  label="мауэрлат002"  # Draft 2D object (typed FeaturePython)
  ChamferSize = 0
  Closed = true
  End = (21584.8,5827.56,0)
  FilletRadius = 0
  Length = 12600
  MakeFace = false
  Placement = pos=(21406.2,1831.55,0) rot=(0,0,-1;1.61546rad)
  Points = (4) [(0,0,0),(0,2300,0),(-4000,2300,0),(-4000,-2.18279e-11,0)]
  Start = (21406.2,1831.55,0)
  Subdivisions = 0
FEATURE [Part::FeaturePython] Roof010  label="Крыша001"  # Arch/BIM 113 (typed FeaturePython)
  Angles = [90,14.6,90,14.6]
  Base = -> Wire462
  BorderLength = 15096.9
  Face = 0
  Flip = false
  Heights = [0,299.553,0,299.553]
  HorizontalArea = 1.26e+07
  IdRel = [0,0,0,0]
  IfcType = 113
  MoveBase = false
  MoveWithHost = false
  Overhang = [250,250,250,250]
  PerimeterLength = 14600
  Placement = pos=(0,0,2200) rot=(0,0,1;0rad)
  PredefinedType = 0
  RidgeLength = 7393.43
  Runs = [250,1150,250,1150]
  Thickness = [150,150,150,150]
  VerticalArea = 2.26308e+06
FEATURE [Part::Part2DObjectPython] Rectangle2373  # Draft 2D object (typed FeaturePython)
  ChamferSize = 0
  Columns = 1
  FilletRadius = 0
  Height = 150
  Length = 800
  MakeFace = true
  Placement = pos=(21464.3,3130.25,0) rot=(0,0,-1;1.61546rad)
  Rows = 1
FEATURE [Part::FeaturePython] Structure131  label="Structure130"  # Arch/BIM 52 (typed FeaturePython)
  Base = -> Rectangle2373
  FaceMaker = 0
  Height = 1800
  HorizontalArea = 120000
  IfcData = complex_attributes={"OwnerHistory": {}, "IsNestedBy": {}, "IsDecomposedBy": {}, "IsDefinedBy": {}, "ObjectPlacement": {}, "Representation":... (+4 chars omitted)
  IfcType = 52
  Length = 0
  MoveBase = false
  MoveWithHost = false
  Nodes = (2) [(-35.6948,-25773.1,0),(-35.6948,-25773.1,1800)]
  NodesOffset = 0
  Normal = (0,0,0)
  PerimeterLength = 1900
  VerticalArea = 3.42e+06
  Width = 100
FEATURE [Part::Part2DObjectPython] Rectangle2370  # Draft 2D object (typed FeaturePython)
  ChamferSize = 0
  Columns = 1
  FilletRadius = 0
  Height = 500
  Length = 150
  MakeFace = true
  Placement = pos=(21862.5,1961.31,0) rot=(0,0,-1;1.61546rad)
  Rows = 1
FEATURE [Part::FeaturePython] Structure130  label="Structure129"  # Arch/BIM 52 (typed FeaturePython)
  Base = -> Rectangle2370
  FaceMaker = 0
  Height = 600
  HorizontalArea = 75000
  IfcData = complex_attributes={"OwnerHistory": {}, "IsNestedBy": {}, "IsDecomposedBy": {}, "IsDefinedBy": {}, "ObjectPlacement": {}, "Representation":... (+4 chars omitted)
  IfcType = 52
  Length = 0
  MoveBase = false
  MoveWithHost = false
  Nodes = (2) [(-938.622,-26279,0),(-938.622,-26279,600)]
  NodesOffset = 0
  Normal = (0,0,0)
  PerimeterLength = 1300
  Placement = pos=(0,-4e-15,1240) rot=(0,0,1;0rad)
  VerticalArea = 780000
  Width = 100
FEATURE [Part::Part2DObjectPython] Rectangle2372  # Draft 2D object (typed FeaturePython)
  ChamferSize = 0
  Columns = 1
  FilletRadius = 0
  Height = 150
  Length = 500
  MakeFace = true
  Placement = pos=(21520.1,4379.01,0) rot=(0,0,-1;1.61546rad)
  Rows = 1
FEATURE [Part::FeaturePython] Structure128  label="Structure"  # Arch/BIM 52 (typed FeaturePython)
  Base = -> Rectangle2372
  FaceMaker = 0
  Height = 600
  HorizontalArea = 75000
  IfcData = complex_attributes={"OwnerHistory": {}, "IsNestedBy": {}, "IsDecomposedBy": {}, "IsDefinedBy": {}, "ObjectPlacement": {}, "Representation":... (+4 chars omitted)
  IfcType = 52
  Length = 0
  MoveBase = false
  MoveWithHost = false
  Nodes = (2) [(1351.07,-25965.1,0),(1351.07,-25965.1,600)]
  NodesOffset = 0
  Normal = (0,0,0)
  PerimeterLength = 1300
  Placement = pos=(0,-4e-15,1240) rot=(0,0,1;0rad)
  VerticalArea = 780000
  Width = 100
FEATURE [Part::Part2DObjectPython] Rectangle2368  # Draft 2D object (typed FeaturePython)
  ChamferSize = 0
  Columns = 1
  FilletRadius = 0
  Height = 2300
  Length = 4000
  MakeFace = false
  Placement = pos=(21584.8,5827.56,0) rot=(0,0,-1;1.61546rad)
  Rows = 1
FEATURE [Part::FeaturePython] Wall094  label="Wall005"  # Arch/BIM 166 (typed FeaturePython)
  Align = 1
  Area = 3.087e+07
  Base = -> Rectangle2368
  BlockHeight = 0
  BlockLength = 0
  CountBroken = 0
  CountEntire = 0
  Face = 0
  Height = 2450
  HorizontalArea = 0
  IfcType = 166
  Joint = 0
  Length = 12600
  MakeBlocks = false
  MoveBase = false
  MoveWithHost = false
  Normal = (0,0,0)
  OffsetFirst = 0
  OffsetSecond = 0
  PerimeterLength = 0
  Placement = pos=(0,0,-150) rot=(0,0,1;0rad)
  PredefinedType = 0
  Subtractions = -> [Structure128,Structure130,Structure131]
  VerticalArea = 0
  Width = 150
FEATURE [Part::FeaturePython] Wall096  label="Wall006"  # Arch/BIM 166 (typed FeaturePython)
  Align = 0
  Area = 6.3e+06
  Base = -> Rectangle2368
  BlockHeight = 0
  BlockLength = 0
  CountBroken = 0
  CountEntire = 0
  Face = 0
  Height = 500
  HorizontalArea = 1.18e+06
  IfcType = 166
  Joint = 0
  Length = 12600
  MakeBlocks = false
  MoveBase = false
  MoveWithHost = false
  Normal = (0,0,-1)
  Offset = 50
  OffsetFirst = 0
  OffsetSecond = 0
  PerimeterLength = 12200
  Placement = pos=(0,0,-150) rot=(0,0,1;0rad)
  PredefinedType = 0
  VerticalArea = 1.18e+07
  Width = 100
FEATURE [App::GeometryPython] BuildingPart032  label="Баня (перевозная)"  # Arch/BIM 10 (typed FeaturePython)
  Area = 3.717e+07
  BuildingType = 0
  CompositionType = 0
  ElevationOfRefHeight = 0
  ElevationOfTerrain = 0
  Group = -> [Wall094,Roof010,Wall096]
  Height = 0
  HeightPropagate = true
  IfcType = 10
  LevelOffset = 0
  LongName = Баня (перевозная)
FEATURE [Part::Part2DObjectPython] Rectangle3343  label="Контур Строения001"  # Draft 2D object (typed FeaturePython)
  Area = 0
  ChamferSize = 0
  Columns = 1
  FilletRadius = 0
  Height = 8540
  Length = 13640
  MakeFace = false
  Placement = pos=(-560,-540,0) rot=(0,0,1;0rad)
  Rows = 1
FEATURE [App::FeaturePython] Text  label="Название Строения"  # WARN: FeaturePython — macro-defined, semantics opaque (R4)
  Placement = pos=(60,-286,0) rot=(0,0,1;0rad)
FEATURE [Part::Feature] Human
  Placement = pos=(2300,-1000,-200) rot=(0,0,1;0rad)
  shape: bbox 490.6 x 1.43e-06 x 1712 mm, 1 faces, 0 solids (baked)
FEATURE [Part::FeaturePython] Axis001006  label="Горизонтальные оси"  # WARN: FeaturePython — macro-defined, semantics opaque (R4)
  Angles = [0,0,0,0]
  Distances = [305,2570,1345,4015]
  Length = 15958.8
  Placement = pos=(14122.1,-540,0) rot=(0,0,1;1.5708rad)
  expr: Length = Rectangle3343.Length * 1.17
  expr: .Placement.Base.x = Rectangle3343.Placement.Base.x + Length * 0.92
  expr: .Placement.Base.y = Rectangle3343.Placement.Base.y
FEATURE [Part::FeaturePython] Axis001007  label="Вертикальные Оси"  # WARN: FeaturePython — macro-defined, semantics opaque (R4)
  Angles = [0,0,0,0,0,0,0,0,0]
  Distances = [320,3690,600,820,2020,510,510,1590,3260]
  Length = 11614.4
  Placement = pos=(-560,-2107.94,0) rot=(0,0,1;0rad)
  expr: Length = Rectangle3343.Height * 1.36
  expr: .Placement.Base.y = Rectangle3343.Placement.Base.y - Length * 0.135
  expr: .Placement.Base.x = Rectangle3343.Placement.Base.x
FEATURE [App::FeaturePython] AxisSystem002  label="Оси 1й этаж"  # WARN: FeaturePython — macro-defined, semantics opaque (R4)
  Axes = -> [Axis001006,Axis001007]
FEATURE [Part::FeaturePython] Axis001008  label="Оси уровня"  # WARN: FeaturePython — macro-defined, semantics opaque (R4)
  Angles = [0,0]
  Distances = [0,3130]
  Labels = 1st floor | mansard
  Length = 15004
  Placement = pos=(13618.8,-540,0) rot=(0.57735,-0.57735,0.57735;2.0944rad)
  expr: Length = Rectangle3343.Length * 1.1
  expr: .Placement.Base.x = Rectangle3343.Placement.Base.x + Length * 0.945
  expr: .Placement.Base.y = Rectangle3343.Placement.Base.y
FEATURE [App::DocumentObjectGroup] App__DocumentObjectGroup  label="Разметка Строения"
  Group = -> [Rectangle3343,Text,AxisSystem002,Axis001008]
FEATURE [App::FeaturePython] WPProxy  # WARN: FeaturePython — macro-defined, semantics opaque (R4)
  Placement = pos=(-560,-540,0) rot=(0,0,1;0rad)
FEATURE [Part::Part2DObjectPython] Rectangle3344  label="Фальшколонна 016"  # Draft 2D object (typed FeaturePython)
  Area = 54600
  ChamferSize = 0
  Columns = 1
  FilletRadius = 0
  Height = 140
  Length = 390
  MakeFace = true
  Placement = pos=(5280,-565,0) rot=(0,0,1;0rad)
  Rows = 1
FEATURE [Part::FeaturePython] Structure413  label="Облицовка камнем 029"  # Arch/BIM 52 (typed FeaturePython)
  Base = -> Rectangle3344
  FaceMaker = 0
  GlobalId = 2ZAbdpbyTAehtFhwD_xQoN
  Height = 2320
  HorizontalArea = 54600
  IfcData = IfcUID=2ZAbdpbyTAehtFhwD_xQoN,+2 more (map truncated)
  IfcType = 52
  Length = 0
  Material = -> Material007
  MoveBase = false
  MoveWithHost = false
  Nodes = (2) [(3798,-460,0),(3798,-460,3600)]
  NodesOffset = 0
  Normal = (0,0,0)
  PerimeterLength = 1060
  Placement = pos=(0,-2.558e-13,-40) rot=(0,0,1;0rad)
  VerticalArea = 2459200
  Width = 100
FEATURE [Part::Part2DObjectPython] Rectangle3345  label="Фальшколонна 017"  # Draft 2D object (typed FeaturePython)
  Area = 256200
  ChamferSize = 0
  Columns = 1
  FilletRadius = 0
  Height = 140
  Length = 1830
  MakeFace = true
  Placement = pos=(5280,-565,0) rot=(0,0,1;0rad)
  Rows = 1
FEATURE [Part::FeaturePython] Structure414  label="Облицовка камнем 030"  # Arch/BIM 52 (typed FeaturePython)
  Base = -> Rectangle3345
  FaceMaker = 0
  GlobalId = 1KN_bE7FH3jPyxIPmeDa18
  Height = 380
  HorizontalArea = 256200
  IfcData = IfcUID=1KN_bE7FH3jPyxIPmeDa18,+2 more (map truncated)
  IfcType = 52
  Length = 0
  Material = -> Material007
  MoveBase = false
  MoveWithHost = false
  Nodes = (2) [(3798,-460,0),(3798,-460,3600)]
  NodesOffset = 0
  Normal = (0,0,0)
  PerimeterLength = 3940
  Placement = pos=(0,1.14e-13,2280) rot=(0,0,1;0rad)
  VerticalArea = 1.4972e+06
  Width = 100
FEATURE [Part::Part2DObjectPython] Rectangle3346  label="Фальшколонна 018"  # Draft 2D object (typed FeaturePython)
  Area = 365400
  ChamferSize = 0
  Columns = 1
  FilletRadius = 0
  Height = 140
  Length = 2610
  MakeFace = true
  Placement = pos=(8270,7895,0) rot=(0,0,1;0rad)
  Rows = 1
FEATURE [Part::FeaturePython] Structure415  label="Облицовка камнем 031"  # Arch/BIM 52 (typed FeaturePython)
  Base = -> Rectangle3346
  FaceMaker = 0
  GlobalId = 0o5mp13GDD3PgfU32fU4jr
  Height = 380
  HorizontalArea = 365400
  IfcData = IfcUID=0o5mp13GDD3PgfU32fU4jr,+2 more (map truncated)
  IfcType = 52
  Length = 0
  Material = -> Material007
  MoveBase = false
  MoveWithHost = false
  Nodes = (2) [(3798,-460,0),(3798,-460,3600)]
  NodesOffset = 0
  Normal = (0,0,0)
  PerimeterLength = 5500
  Placement = pos=(0,1.14e-13,2500) rot=(0,0,1;0rad)
  VerticalArea = 2.09e+06
  Width = 100
FEATURE [Part::Part2DObjectPython] Rectangle3347  label="Фальшколонна 019"  # Draft 2D object (typed FeaturePython)
  Area = 54600
  ChamferSize = 0
  Columns = 1
  FilletRadius = 0
  Height = 140
  Length = 390
  MakeFace = true
  Placement = pos=(8270,7895,0) rot=(0,0,1;0rad)
  Rows = 1
FEATURE [Part::FeaturePython] Structure416  label="Облицовка камнем 032"  # Arch/BIM 52 (typed FeaturePython)
  Base = -> Rectangle3347
  FaceMaker = 0
  GlobalId = 0mLPfwKGf0vhV5LN6Arb3I
  Height = 2540
  HorizontalArea = 54600
  IfcData = IfcUID=0mLPfwKGf0vhV5LN6Arb3I,+2 more (map truncated)
  IfcType = 52
  Length = 0
  Material = -> Material007
  MoveBase = false
  MoveWithHost = false
  Nodes = (2) [(3798,-460,0),(3798,-460,3600)]
  NodesOffset = 0
  Normal = (0,0,0)
  PerimeterLength = 1060
  Placement = pos=(0,4.55e-13,-40) rot=(0,0,1;0rad)
  VerticalArea = 2692400
  Width = 100
FEATURE [Part::Part2DObjectPython] Rectangle3348  label="Фальшколонна 020"  # Draft 2D object (typed FeaturePython)
  Area = 54600
  ChamferSize = 0
  Columns = 1
  FilletRadius = 0
  Height = 140
  Length = 390
  MakeFace = true
  Placement = pos=(6720,-565,0) rot=(0,0,1;0rad)
  Rows = 1
FEATURE [Part::FeaturePython] Structure417  label="Облицовка камнем 033"  # Arch/BIM 52 (typed FeaturePython)
  Base = -> Rectangle3348
  FaceMaker = 0
  GlobalId = 3gi2vzadv7rvN$3wEIiMLm
  Height = 2320
  HorizontalArea = 54600
  IfcData = IfcUID=3gi2vzadv7rvN$3wEIiMLm,+2 more (map truncated)
  IfcType = 52
  Length = 0
  Material = -> Material007
  MoveBase = false
  MoveWithHost = false
  Nodes = (2) [(3798,-460,0),(3798,-460,3600)]
  NodesOffset = 0
  Normal = (0,0,0)
  PerimeterLength = 1060
  Placement = pos=(0,-2.558e-13,-40) rot=(0,0,1;0rad)
  VerticalArea = 2459200
  Width = 100
FEATURE [Part::Part2DObjectPython] Rectangle3349  label="Фальшколонна 021"  # Draft 2D object (typed FeaturePython)
  Area = 54600
  ChamferSize = 0
  Columns = 1
  FilletRadius = 0
  Height = 140
  Length = 390
  MakeFace = true
  Placement = pos=(10490,7895,0) rot=(0,0,1;0rad)
  Rows = 1
FEATURE [Part::FeaturePython] Structure420  label="Облицовка камнем 036"  # Arch/BIM 52 (typed FeaturePython)
  Base = -> Rectangle3349
  FaceMaker = 0
  GlobalId = 0xXC9cy$jFShfp8t3IltaA
  Height = 2540
  HorizontalArea = 54600
  IfcData = IfcUID=0xXC9cy$jFShfp8t3IltaA,+2 more (map truncated)
  IfcType = 52
  Length = 0
  Material = -> Material007
  MoveBase = false
  MoveWithHost = false
  Nodes = (2) [(3798,-460,0),(3798,-460,3600)]
  NodesOffset = 0
  Normal = (0,0,0)
  PerimeterLength = 1060
  Placement = pos=(0,4.55e-13,-40) rot=(0,0,1;0rad)
  VerticalArea = 2692400
  Width = 100
FEATURE [Part::Feature] Extrude098001  label="Подкосы крыльца 015"
  Placement = pos=(19738,7460,0) rot=(0,0,1;3.14159rad)
  shape: bbox 150 x 983 x 1690 mm, 12 faces (baked)
FEATURE [Part::FeaturePython] Component002  label="Подкос011"  # Arch/BIM 52 (typed FeaturePython)
  Base = -> Extrude098001
  GlobalId = 305owz_yPFe8XEoQwHyy9O
  HorizontalArea = 0
  IfcData = IfcUID=305owz_yPFe8XEoQwHyy9O,+2 more (map truncated)
  IfcType = 52
  Material = -> Material
  MoveBase = false
  MoveWithHost = false
  PerimeterLength = 0
  Placement = pos=(19734,7445,0) rot=(0,0,1;3.14159rad)
  VerticalArea = 0
FEATURE [Part::Feature] Extrude095001  label="Подкосы крыльца 013"
  Placement = pos=(476,-7.69351e-07,0) rot=(0,0,1;0rad)
  shape: bbox 150 x 983 x 1690 mm, 12 faces (baked)
FEATURE [Part::FeaturePython] Component  label="Подкос001"  # Arch/BIM 52 (typed FeaturePython)
  Base = -> Extrude095001
  GlobalId = 0BS$y7q7z1ufWzhc1qzE8g
  HorizontalArea = 0
  IfcData = IfcUID=0BS$y7q7z1ufWzhc1qzE8g,+2 more (map truncated)
  IfcType = 52
  Material = -> Material
  MoveBase = false
  MoveWithHost = false
  PerimeterLength = 0
  Placement = pos=(456,15,0) rot=(0,0,1;0rad)
  VerticalArea = 0
FEATURE [Part::Feature] Extrude099001  label="Подкосы крыльца 014"
  Placement = pos=(14668,7460,0) rot=(0,0,1;3.14159rad)
  shape: bbox 150 x 983 x 1690 mm, 12 faces (baked)
FEATURE [Part::FeaturePython] Component001  label="Подкос010"  # Arch/BIM 52 (typed FeaturePython)
  Base = -> Extrude099001
  GlobalId = 3F3uK2ozfBRxSV0PWqxsz5
  HorizontalArea = 0
  IfcData = IfcUID=3F3uK2ozfBRxSV0PWqxsz5,+2 more (map truncated)
  IfcType = 52
  Material = -> Material
  MoveBase = false
  MoveWithHost = false
  PerimeterLength = 0
  Placement = pos=(14664,7445,0) rot=(0,0,1;3.14159rad)
  VerticalArea = 0
FEATURE [Part::Feature] Extrude096001  label="Подкосы крыльца 016"
  Placement = pos=(-3422,-7.69351e-07,0) rot=(0,0,1;0rad)
  shape: bbox 150 x 983 x 1690 mm, 12 faces (baked)
FEATURE [Part::FeaturePython] Component003  label="Подкос012"  # Arch/BIM 52 (typed FeaturePython)
  Base = -> Extrude096001
  GlobalId = 0rQ8hKrWb1kuTVB9ZxaTxQ
  HorizontalArea = 0
  IfcData = IfcUID=0rQ8hKrWb1kuTVB9ZxaTxQ,+2 more (map truncated)
  IfcType = 52
  Material = -> Material
  MoveBase = false
  MoveWithHost = false
  PerimeterLength = 0
  Placement = pos=(-3314,15,0) rot=(0,0,1;0rad)
  VerticalArea = 0
FEATURE [Part::Part2DObjectPython] Line1583  label="облицовка_стены_032"  # Draft 2D object (typed FeaturePython)
  ChamferSize = 0
  Closed = true
  End = (12950,8015,0)
  FilletRadius = 0
  Length = 13510
  MakeFace = false
  Placement = pos=(-450,8535,0) rot=(0,0,1;0rad)
  Points = (2) [(-110,-520,0),(13400,-520,0)]
  Start = (-560,8015,0)
  Subdivisions = 0
FEATURE [Part::FeaturePython] Structure421  label="Проём_четв._045"  # Arch/BIM 52 (typed FeaturePython)
  Base = -> Rectangle3200
  FaceMaker = 0
  Height = 1500
  HorizontalArea = 219600
  IfcData = complex_attributes={"OwnerHistory": {}, "IsNestedBy": {}, "IsDecomposedBy": {}, "IsDefinedBy": {}, "ObjectPlacement": {}, "Representation":... (+4 chars omitted)
  IfcType = 52
  Length = 0
  MoveBase = false
  MoveWithHost = false
  Nodes = (2) [(5775,-395,0),(5775,-395,2335)]
  NodesOffset = 0
  Normal = (0,0,0)
  PerimeterLength = 3900
  Placement = pos=(0,0,1010) rot=(0,0,1;0rad)
  VerticalArea = 5.85e+06
  Width = 100
FEATURE [Part::FeaturePython] Structure422  label="Проём_четв._046"  # Arch/BIM 52 (typed FeaturePython)
  Base = -> Rectangle3201
  FaceMaker = 0
  Height = 1500
  HorizontalArea = 94800
  IfcData = complex_attributes={"OwnerHistory": {}, "IsNestedBy": {}, "IsDecomposedBy": {}, "IsDefinedBy": {}, "ObjectPlacement": {}, "Representation":... (+4 chars omitted)
  IfcType = 52
  Length = 0
  MoveBase = false
  MoveWithHost = false
  Nodes = (2) [(5775,-395,0),(5775,-395,2335)]
  NodesOffset = 0
  Normal = (0,0,0)
  PerimeterLength = 1820
  Placement = pos=(0,0,1010) rot=(0,0,1;0rad)
  VerticalArea = 2.73e+06
  Width = 100
FEATURE [Part::FeaturePython] Structure424  label="Облицовка камнем 037"  # Arch/BIM 52 (typed FeaturePython)
  FaceMaker = 0
  Height = 1500
  HorizontalArea = 154800
  IfcData = attributes={"GlobalId": {"name": "GlobalId", "type": "IfcGloballyUniqueId", "is_enum": false, "enum_values": []}, "Description": {"... (+484 chars omitted),+1 more (map truncated)
  IfcType = 52
  Length = 0
  Material = -> Material007
  MoveBase = false
  MoveWithHost = false
  Nodes = (2) [(4505,7955,0),(4505,7955,1500)]
  NodesOffset = 0
  Normal = (0,0,1)
  PerimeterLength = 2820
  Placement = pos=(0,0,1010) rot=(0,0,1;0rad)
  VerticalArea = 4.23e+06
  Width = 100
FEATURE [Part::FeaturePython] Structure425  label="Облицовка камнем 038"  # Arch/BIM 52 (typed FeaturePython)
  Base = -> Rectangle3346
  FaceMaker = 0
  Height = 2925
  HorizontalArea = 365400
  IfcData = attributes={"GlobalId": {"name": "GlobalId", "type": "IfcGloballyUniqueId", "is_enum": false, "enum_values": []}, "Description": {"... (+484 chars omitted),+1 more (map truncated)
  IfcType = 52
  Length = 0
  Material = -> Material007
  MoveBase = false
  MoveWithHost = false
  Nodes = (2) [(3798,-460,0),(3798,-460,3600)]
  NodesOffset = 0
  Normal = (0,0,0)
  PerimeterLength = 5500
  Placement = pos=(0,1.14e-13,-46) rot=(0,0,1;0rad)
  VerticalArea = 1.60875e+07
  Width = 100
FEATURE [Part::FeaturePython] Wall298  label="облицовка 017"  # Arch/BIM 166 (typed FeaturePython)
  Align = 0
  Area = 48636000
  Base = -> Line1583
  BlockHeight = 65
  BlockLength = 250
  CountBroken = 108
  CountEntire = 1737
  Face = 0
  GlobalId = 2NuME8GJTD0RJft756pcFm
  Height = 3600
  HorizontalArea = 2.0904e+06
  IfcData = IfcUID=2NuME8GJTD0RJft756pcFm; attributes={"GlobalId": {"value": "2NuME8GJTD0RJft756pcFm"}}
  IfcType = 166
  Joint = 10
  Length = 13510
  MakeBlocks = false
  Material = -> Material003
  MoveBase = false
  MoveWithHost = false
  Normal = (0,0,0)
  OffsetFirst = 120
  OffsetSecond = 250
  PerimeterLength = 0
  Placement = pos=(0,0,-40) rot=(0,0,1;0rad)
  PredefinedType = 0
  Subtractions = -> [Structure421,Structure422,Structure424,Structure425]
  VerticalArea = 72229380
  Width = 120
FEATURE [Part::Part2DObjectPython] Line1584  label="облицовка_стены_033"  # Draft 2D object (typed FeaturePython)
  ChamferSize = 0
  Closed = true
  End = (-430,-555,0)
  FilletRadius = 0
  Length = 13380
  MakeFace = false
  Placement = pos=(12780,-555,0) rot=(0,0,1;0rad)
  Points = (2) [(170,2.84217e-12,0),(-13210,2.84217e-12,0)]
  Start = (12950,-555,0)
  Subdivisions = 0
FEATURE [Part::FeaturePython] Structure426  label="Проём_четв._048"  # Arch/BIM 52 (typed FeaturePython)
  Base = -> Rectangle2573
  FaceMaker = 0
  Height = 1275
  HorizontalArea = 63600
  IfcData = complex_attributes={"OwnerHistory": {}, "IsNestedBy": {}, "IsDecomposedBy": {}, "IsDefinedBy": {}, "ObjectPlacement": {}, "Representation":... (+4 chars omitted)
  IfcType = 52
  Length = 0
  MoveBase = false
  MoveWithHost = false
  Nodes = (2) [(4618,-450,0),(4618,-450,1320)]
  NodesOffset = 0
  Normal = (0,0,0)
  PerimeterLength = 1300
  Placement = pos=(0,0,1010) rot=(0,0,1;0rad)
  VerticalArea = 1657500
  Width = 100
FEATURE [Part::FeaturePython] Structure427  label="Проём_четв._049"  # Arch/BIM 52 (typed FeaturePython)
  Base = -> Rectangle2571
  FaceMaker = 0
  Height = 2315
  HorizontalArea = 252000
  IfcData = complex_attributes={"OwnerHistory": {}, "IsNestedBy": {}, "IsDecomposedBy": {}, "IsDefinedBy": {}, "ObjectPlacement": {}, "Representation":... (+4 chars omitted)
  IfcType = 52
  Length = 0
  MoveBase = false
  MoveWithHost = false
  Nodes = (2) [(5775,-395,0),(5775,-395,2335)]
  NodesOffset = 0
  Normal = (0,0,0)
  PerimeterLength = 2340
  Placement = pos=(0,0,-40) rot=(0,0,1;0rad)
  VerticalArea = 503100
  Width = 100
FEATURE [Part::FeaturePython] Structure428  label="Проём_четв._050"  # Arch/BIM 52 (typed FeaturePython)
  Base = -> Rectangle2580
  FaceMaker = 0
  Height = 1275
  HorizontalArea = 63600
  IfcData = complex_attributes={"OwnerHistory": {}, "IsNestedBy": {}, "IsDecomposedBy": {}, "IsDefinedBy": {}, "ObjectPlacement": {}, "Representation":... (+4 chars omitted)
  IfcType = 52
  Length = 0
  MoveBase = false
  MoveWithHost = false
  Nodes = (2) [(5775,-395,0),(5775,-395,2335)]
  NodesOffset = 0
  Normal = (0,0,0)
  PerimeterLength = 1300
  Placement = pos=(0,0,1010) rot=(0,0,1;0rad)
  VerticalArea = 1657500
  Width = 100
FEATURE [Part::FeaturePython] Structure429  label="Облицовка камнем 039"  # Arch/BIM 52 (typed FeaturePython)
  Base = -> Rectangle3345
  FaceMaker = 0
  Height = 2700
  HorizontalArea = 256200
  IfcData = attributes={"GlobalId": {"name": "GlobalId", "type": "IfcGloballyUniqueId", "is_enum": false, "enum_values": []}, "Description": {"... (+484 chars omitted),+1 more (map truncated)
  IfcType = 52
  Length = 0
  Material = -> Material007
  MoveBase = false
  MoveWithHost = false
  Nodes = (2) [(3798,-460,0),(3798,-460,3600)]
  NodesOffset = 0
  Normal = (0,0,0)
  PerimeterLength = 3940
  Placement = pos=(0,1.14e-13,-40) rot=(0,0,1;0rad)
  VerticalArea = 1.0638e+07
  Width = 100
FEATURE [Part::FeaturePython] Wall299  label="облицовка 018"  # Arch/BIM 166 (typed FeaturePython)
  Align = 0
  Area = 48168000
  Base = -> Line1584
  BlockHeight = 65
  BlockLength = 250
  CountBroken = 120
  CountEntire = 2088
  Face = 0
  GlobalId = 3SgCB7ImHBKRjTRpndNtdS
  Height = 3600
  HorizontalArea = 1732800
  IfcData = IfcUID=3SgCB7ImHBKRjTRpndNtdS; attributes={"GlobalId": {"value": "3SgCB7ImHBKRjTRpndNtdS"}}
  IfcType = 166
  Joint = 10
  Length = 13380
  MakeBlocks = false
  Material = -> Material003
  MoveBase = false
  MoveWithHost = false
  Normal = (0,0,0)
  OffsetFirst = 120
  OffsetSecond = 250
  PerimeterLength = 0
  Placement = pos=(0,0,-40) rot=(0,0,1;0rad)
  PredefinedType = 0
  Subtractions = -> [Structure426,Structure427,Structure428,Structure429]
  VerticalArea = 85875000
  Width = 120
FEATURE [Part::Part2DObjectPython] Line1585  label="облицовка_стены_034"  # Draft 2D object (typed FeaturePython)
  ChamferSize = 0
  Closed = true
  End = (-560,-555,0)
  FilletRadius = 0
  Length = 8440
  MakeFace = false
  Placement = pos=(-515,-735,0) rot=(0,0,1;0rad)
  Points = (2) [(-45,8620,0),(-45,180,0)]
  Start = (-560,7885,0)
  Subdivisions = 0
FEATURE [Part::FeaturePython] Structure430  label="Проём_четв._051"  # Arch/BIM 52 (typed FeaturePython)
  Base = -> Rectangle2858
  FaceMaker = 0
  Height = 1500
  HorizontalArea = 157200
  IfcData = complex_attributes={"OwnerHistory": {}, "IsNestedBy": {}, "IsDecomposedBy": {}, "IsDefinedBy": {}, "ObjectPlacement": {}, "Representation":... (+4 chars omitted)
  IfcType = 52
  Length = 0
  MoveBase = false
  MoveWithHost = false
  Nodes = (2) [(1035,460,0),(1035,460,535)]
  NodesOffset = 0
  Normal = (0,0,0)
  PerimeterLength = 2860
  Placement = pos=(0,0,1010) rot=(0,0,1;0rad)
  VerticalArea = 4290000
  Width = 100
FEATURE [Part::FeaturePython] Wall300  label="облицовка 019"  # Arch/BIM 166 (typed FeaturePython)
  Align = 1
  Area = 30384000
  Base = -> Line1585
  BlockHeight = 65
  BlockLength = 250
  CountBroken = 68
  CountEntire = 1421
  Face = 0
  GlobalId = 2BxWlk8bv7HwfTqswZTI_V
  Height = 3600
  HorizontalArea = 1170000
  IfcData = IfcUID=2BxWlk8bv7HwfTqswZTI_V; attributes={"GlobalId": {"value": "2BxWlk8bv7HwfTqswZTI_V"}}
  IfcType = 166
  Joint = 10
  Length = 8440
  MakeBlocks = false
  Material = -> Material003
  MoveBase = false
  MoveWithHost = false
  Normal = (0,0,0)
  OffsetFirst = 120
  OffsetSecond = 250
  PerimeterLength = 0
  Placement = pos=(0,0,-40) rot=(0,0,1;0rad)
  PredefinedType = 0
  Subtractions = -> [Structure430]
  VerticalArea = 58062000
  Width = 120
FEATURE [Part::Part2DObjectPython] Line1586  label="облицовка_стены_035"  # Draft 2D object (typed FeaturePython)
  ChamferSize = 0
  Closed = true
  End = (13080,8015,0)
  FilletRadius = 0
  Length = 8570
  MakeFace = false
  Placement = pos=(14815,4225,0) rot=(0,0,1;0rad)
  Points = (2) [(-1735,-4780,0),(-1735,3790,0)]
  Start = (13080,-555,0)
  Subdivisions = 0
FEATURE [Part::FeaturePython] Structure431  label="Проём_четв._052"  # Arch/BIM 52 (typed FeaturePython)
  Base = -> Rectangle2579
  FaceMaker = 0
  Height = 1275
  HorizontalArea = 219600
  IfcData = complex_attributes={"OwnerHistory": {}, "IsNestedBy": {}, "IsDecomposedBy": {}, "IsDefinedBy": {}, "ObjectPlacement": {}, "Representation":... (+4 chars omitted)
  IfcType = 52
  Length = 0
  MoveBase = false
  MoveWithHost = false
  Nodes = (2) [(1035,460,0),(1035,460,535)]
  NodesOffset = 0
  Normal = (0,0,0)
  PerimeterLength = 3900
  Placement = pos=(0,0,1235) rot=(0,0,1;0rad)
  VerticalArea = 4.9725e+06
  Width = 100
FEATURE [Part::FeaturePython] Structure432  label="Проём_четв._053"  # Arch/BIM 52 (typed FeaturePython)
  Base = -> Rectangle2577
  FaceMaker = 0
  Height = 1275
  HorizontalArea = 94800
  IfcData = complex_attributes={"OwnerHistory": {}, "IsNestedBy": {}, "IsDecomposedBy": {}, "IsDefinedBy": {}, "ObjectPlacement": {}, "Representation":... (+4 chars omitted)
  IfcType = 52
  Length = 0
  MoveBase = false
  MoveWithHost = false
  Nodes = (2) [(1035,460,0),(1035,460,535)]
  NodesOffset = 0
  Normal = (0,0,0)
  PerimeterLength = 1820
  Placement = pos=(0,0,1235) rot=(0,0,1;0rad)
  VerticalArea = 2320500
  Width = 100
FEATURE [Part::FeaturePython] Structure433  label="Облицовка камнем 040"  # Arch/BIM 52 (typed FeaturePython)
  FaceMaker = 0
  Height = 1275
  HorizontalArea = 108000
  IfcData = attributes={"GlobalId": {"name": "GlobalId", "type": "IfcGloballyUniqueId", "is_enum": false, "enum_values": []}, "Description": {"... (+484 chars omitted),+1 more (map truncated)
  IfcType = 52
  Length = 0
  Material = -> Material007
  MoveBase = false
  MoveWithHost = false
  Nodes = (2) [(13020,3665,0),(13020,3665,1275)]
  NodesOffset = 0
  Normal = (0,0,1)
  PerimeterLength = 2040
  Placement = pos=(0,0,1235) rot=(0,0,1;0rad)
  VerticalArea = 2.601e+06
  Width = 100
FEATURE [Part::FeaturePython] Wall305  label="облицовка 020"  # Arch/BIM 166 (typed FeaturePython)
  Align = 1
  Area = 30852000
  Base = -> Line1586
  BlockHeight = 65
  BlockLength = 250
  CountBroken = 66
  CountEntire = 1299
  Face = 0
  GlobalId = 0ylFaZ_Q11vgSu8iyeHdyc
  Height = 3600
  HorizontalArea = 1450800
  IfcData = IfcUID=0ylFaZ_Q11vgSu8iyeHdyc; attributes={"GlobalId": {"value": "0ylFaZ_Q11vgSu8iyeHdyc"}}
  IfcType = 166
  Joint = 10
  Length = 8570
  MakeBlocks = false
  Material = -> Material003
  MoveBase = false
  MoveWithHost = false
  Normal = (0,0,0)
  OffsetFirst = 120
  OffsetSecond = 250
  PerimeterLength = 0
  Placement = pos=(0,0,-40) rot=(0,0,1;0rad)
  PredefinedType = 0
  Subtractions = -> [Structure431,Structure432,Structure433]
  VerticalArea = 53898000
  Width = 120
FEATURE [Part::Part2DObjectPython] Line1587  label="контрфорс_линия_005"  # Draft 2D object (typed FeaturePython)
  ChamferSize = 0
  Closed = true
  End = (3470,-635,0)
  FilletRadius = 0
  Length = 380
  MakeFace = false
  Placement = pos=(3680,-635,0) rot=(0,0,1;0rad)
  Points = (2) [(170,1.02318e-12,0),(-210,9.09495e-13,0)]
  Start = (3850,-635,0)
  Subdivisions = 0
FEATURE [Part::FeaturePython] Wall306  label="Контрфорс 005"  # Arch/BIM 166 (typed FeaturePython)
  Align = 0
  Area = 741000
  Base = -> Line1587
  BlockHeight = 65
  BlockLength = 250
  CountBroken = 26
  CountEntire = 26
  Face = 0
  GlobalId = 342k6QohT2QOnSo3Rt4Yr5
  Height = 1950
  HorizontalArea = 0
  IfcData = IfcUID=342k6QohT2QOnSo3Rt4Yr5; attributes={"GlobalId": {"value": "342k6QohT2QOnSo3Rt4Yr5"}}
  IfcType = 166
  Joint = 10
  Length = 380
  MakeBlocks = true
  Material = -> Material003
  MoveBase = false
  MoveWithHost = false
  Normal = (0,0,0)
  OffsetFirst = 250
  OffsetSecond = 120
  PerimeterLength = 0
  Placement = pos=(0,0,-40) rot=(0,0,1;0rad)
  PredefinedType = 0
  VerticalArea = 0
  Width = 120
FEATURE [Part::Part2DObjectPython] Line1588  label="контрфорс_линия_006"  # Draft 2D object (typed FeaturePython)
  ChamferSize = 0
  Closed = true
  End = (8540,-635,0)
  FilletRadius = 0
  Length = 380
  MakeFace = false
  Placement = pos=(8750,-635,0) rot=(0,0,1;0rad)
  Points = (2) [(170,1.02318e-12,0),(-210,9.09495e-13,0)]
  Start = (8920,-635,0)
  Subdivisions = 0
FEATURE [Part::FeaturePython] Wall307  label="Контрфорс 006"  # Arch/BIM 166 (typed FeaturePython)
  Align = 0
  Area = 741000
  Base = -> Line1588
  BlockHeight = 65
  BlockLength = 250
  CountBroken = 26
  CountEntire = 26
  Face = 0
  GlobalId = 2QQuq56G56SBKvMoDbUykg
  Height = 1950
  HorizontalArea = 0
  IfcData = IfcUID=2QQuq56G56SBKvMoDbUykg; attributes={"GlobalId": {"value": "2QQuq56G56SBKvMoDbUykg"}}
  IfcType = 166
  Joint = 10
  Length = 380
  MakeBlocks = true
  Material = -> Material003
  MoveBase = false
  MoveWithHost = false
  Normal = (0,0,0)
  OffsetFirst = 120
  OffsetSecond = 250
  PerimeterLength = 0
  Placement = pos=(0,0,-40) rot=(0,0,1;0rad)
  PredefinedType = 0
  VerticalArea = 0
  Width = 120
FEATURE [Part::Part2DObjectPython] Line1589  label="контрфорс_линия_007"  # Draft 2D object (typed FeaturePython)
  ChamferSize = 0
  Closed = true
  End = (7500,8095,0)
  FilletRadius = 0
  Length = 380
  MakeFace = false
  Placement = pos=(7710,8095,0) rot=(0,0,1;0rad)
  Points = (2) [(170,9.09495e-13,0),(-210,9.09495e-13,0)]
  Start = (7880,8095,0)
  Subdivisions = 0
FEATURE [Part::FeaturePython] Wall308  label="Контрфорс 007"  # Arch/BIM 166 (typed FeaturePython)
  Align = 1
  Area = 741000
  Base = -> Line1589
  BlockHeight = 65
  BlockLength = 250
  CountBroken = 26
  CountEntire = 26
  Face = 0
  GlobalId = 3waotNP91F$e4vFRfeMs10
  Height = 1950
  HorizontalArea = 0
  IfcData = IfcUID=3waotNP91F$e4vFRfeMs10; attributes={"GlobalId": {"value": "3waotNP91F$e4vFRfeMs10"}}
  IfcType = 166
  Joint = 10
  Length = 380
  MakeBlocks = true
  Material = -> Material003
  MoveBase = false
  MoveWithHost = false
  Normal = (0,0,0)
  OffsetFirst = 120
  OffsetSecond = 250
  PerimeterLength = 0
  Placement = pos=(0,0,-40) rot=(0,0,1;0rad)
  PredefinedType = 0
  VerticalArea = 0
  Width = 120
FEATURE [Part::Part2DObjectPython] Line1590  label="контрфорс_линия_008"  # Draft 2D object (typed FeaturePython)
  ChamferSize = 0
  Closed = true
  End = (11270,8095,0)
  FilletRadius = 0
  Length = 380
  MakeFace = false
  Placement = pos=(11480,8095,0) rot=(0,0,1;0rad)
  Points = (2) [(170,9.09495e-13,0),(-210,9.09495e-13,0)]
  Start = (11650,8095,0)
  Subdivisions = 0
FEATURE [Part::FeaturePython] Wall309  label="Контрфорс 008"  # Arch/BIM 166 (typed FeaturePython)
  Align = 1
  Area = 741000
  Base = -> Line1590
  BlockHeight = 65
  BlockLength = 250
  CountBroken = 26
  CountEntire = 26
  Face = 0
  GlobalId = 0Yg83kwN5EPeGAKGfacmqk
  Height = 1950
  HorizontalArea = 0
  IfcData = IfcUID=0Yg83kwN5EPeGAKGfacmqk; attributes={"GlobalId": {"value": "0Yg83kwN5EPeGAKGfacmqk"}}
  IfcType = 166
  Joint = 10
  Length = 380
  MakeBlocks = true
  Material = -> Material003
  MoveBase = false
  MoveWithHost = false
  Normal = (0,0,0)
  OffsetFirst = 250
  OffsetSecond = 120
  PerimeterLength = 0
  Placement = pos=(0,0,-40) rot=(0,0,1;0rad)
  PredefinedType = 0
  VerticalArea = 0
  Width = 120
FEATURE [App::FeaturePython] WPProxy001  # WARN: FeaturePython — macro-defined, semantics opaque (R4)
  Placement = pos=(-560,-540,3130) rot=(0,0,1;0rad)
FEATURE [Sketcher::SketchObject] Sketch364
  FullyConstrained = false
  MapMode = 5
  Placement = pos=(10929,-710.046,-122.202) rot=(0.57735,0.57735,0.57735;2.0944rad)
  sketch-geometry (10):
    g0: LineSegment StartX=8710.05 StartY=1993.19 StartZ=0 EndX=8710.05 EndY=3683.19 EndZ=0
    g1: LineSegment StartX=8710.05 StartY=3683.19 StartZ=0 EndX=9693.03 EndY=2994.9 EndZ=0
    g2: LineSegment StartX=9693.03 StartY=2994.9 StartZ=0 EndX=9635.67 EndY=2912.98 EndZ=0
    g3: LineSegment StartX=9635.67 StartY=2912.98 StartZ=0 EndX=9471.84 EndY=3027.7 EndZ=0
    g4: LineSegment StartX=9471.84 StartY=3027.7 StartZ=0 EndX=8810.05 EndY=2082.56 EndZ=0
    g5: LineSegment StartX=8810.05 StartY=2082.56 StartZ=0 EndX=8810.05 EndY=1993.19 EndZ=0
    g6: LineSegment StartX=8810.05 StartY=1993.19 StartZ=0 EndX=8710.05 EndY=1993.19 EndZ=0
    g7: LineSegment StartX=8810.05 StartY=2256.9 StartZ=0 EndX=8810.05 EndY=3491.09 EndZ=0
    g8: LineSegment StartX=8810.05 StartY=3491.09 StartZ=0 EndX=9389.93 EndY=3085.06 EndZ=0
    g9: LineSegment StartX=9389.93 StartY=3085.06 StartZ=0 EndX=8810.05 EndY=2256.9 EndZ=0
  constraints (28):
    c: Vertical(g0)
    c: Coincident(g1,g2)
    c: Coincident(g2,g3)
    c: Coincident(g3,g4)
    c: Coincident(g4,g5)
    c: Vertical(g5)
    c: Coincident(g5,g6)
    c: Coincident(g6,g0)
    c: Vertical(g7)
    c: Coincident(g7,g8)
    c: Coincident(g8,g9)
    c: Coincident(g9,g7)
    c: Parallel(g4,g9)
    c: Horizontal(g6)
    c: Parallel(g3,g1)
    c: Parallel(g9,g2)
    c: Parallel(g8,g3)
    c: Distance(g8,g4) = 100
    c: Distance(g8,g1) = 100
    c: Distance(g3,g1) = 100
    c: Distance(g7,g0) = 100
    c: DistanceX(g6,g6) = 100
    c: Angle(g1) = -0.610865
    c: Coincident(g0,g1)
    c: Distance(g1) = 1200
    c: DistanceY(g0,g0) = 1690
    c: Angle(g4,g3) = 1.5708
    c: Distance(g3) = 200
FEATURE [Part::Extrusion] Extrude099002  label="Подкосы крыльца 017"
  Base = -> Sketch364
  Dir = (1,0,0)
  DirMode = 2
  FaceMakerClass = Part::FaceMakerBullseye
  LengthFwd = 150
  LengthRev = 0
  Placement = pos=(19738,7460,0) rot=(0,0,1;3.14159rad)
  Solid = true
  Symmetric = false
FEATURE [Part::Extrusion] Extrude099003  label="Подкосы крыльца 018"
  Base = -> Sketch364
  Dir = (1,0,0)
  DirMode = 2
  FaceMakerClass = Part::FaceMakerBullseye
  LengthFwd = 150
  LengthRev = 0
  Placement = pos=(476,-7.69351e-07,0) rot=(0,0,1;0rad)
  Solid = true
  Symmetric = false
FEATURE [Part::Extrusion] Extrude099004  label="Подкосы крыльца 019"
  Base = -> Sketch364
  Dir = (1,0,0)
  DirMode = 2
  FaceMakerClass = Part::FaceMakerBullseye
  LengthFwd = 150
  LengthRev = 0
  Placement = pos=(-3422,-7.69351e-07,0) rot=(0,0,1;0rad)
  Solid = true
  Symmetric = false
FEATURE [Part::Extrusion] Extrude099005  label="Подкосы крыльца 020"
  Base = -> Sketch364
  Dir = (1,0,0)
  DirMode = 2
  FaceMakerClass = Part::FaceMakerBullseye
  LengthFwd = 150
  LengthRev = 0
  Placement = pos=(14668,7460,0) rot=(0,0,1;3.14159rad)
  Solid = true
  Symmetric = false
FEATURE [App::DocumentObjectGroup] Group128  label="NotSupportedForExport_to_IFC"
  Group = -> [Extrude099002,Extrude099003,Extrude099004,Extrude099005,Pipe004,Pipe007]
FEATURE [Part::FeaturePython] Component004  label="Топка L700"  # Arch/BIM 15 (typed FeaturePython)
  Base = -> Box3211
  GlobalId = 1gtXDcR713zhxl2yKk2Izx
  HorizontalArea = 0
  IfcData = IfcUID=1gtXDcR713zhxl2yKk2Izx,+2 more (map truncated)
  IfcType = 15
  Material = -> Material006
  MoveBase = false
  MoveWithHost = false
  PerimeterLength = 0
  Placement = pos=(8750,1885,800) rot=(0,0,1;0rad)
  PredefinedType = 0
  VerticalArea = 0
FEATURE [Part::FeaturePython] Component005  label="Дымоход 200 001"  # Arch/BIM 52 (typed FeaturePython)
  Base = -> Pipe008
  GlobalId = 1RYiQBgpbBTAR3hS4pyNB_
  HorizontalArea = 0
  IfcData = IfcUID=1RYiQBgpbBTAR3hS4pyNB_,+2 more (map truncated)
  IfcType = 52
  Material = -> Material010
  MoveBase = false
  MoveWithHost = false
  PerimeterLength = 0
  VerticalArea = 0
FEATURE [Part::FeaturePython] Component007  label="Вентканал 140мм 008"  # Arch/BIM 52 (typed FeaturePython)
  Base = -> Pipe009
  GlobalId = 1bznvW3p57su9hI7viqv$n
  HorizontalArea = 0
  IfcData = IfcUID=1bznvW3p57su9hI7viqv$n,+2 more (map truncated)
  IfcType = 52
  Material = -> Material010
  MoveBase = false
  MoveWithHost = false
  PerimeterLength = 0
  VerticalArea = 0
FEATURE [Part::FeaturePython] Component008  label="Вентканал 140мм 007"  # Arch/BIM 52 (typed FeaturePython)
  Base = -> Pipe010
  GlobalId = 30PUGUtgf8w9a6SsQSC606
  HorizontalArea = 0
  IfcData = IfcUID=30PUGUtgf8w9a6SsQSC606,+2 more (map truncated)
  IfcType = 52
  Material = -> Material010
  MoveBase = false
  MoveWithHost = false
  PerimeterLength = 0
  Placement = pos=(150,-150,0) rot=(0,0,1;0rad)
  VerticalArea = 0
FEATURE [Part::FeaturePython] Component009  label="Вентканал 140мм 006"  # Arch/BIM 52 (typed FeaturePython)
  Base = -> Pipe011
  GlobalId = 2DPp5cUajCNBraILIYWVwM
  HorizontalArea = 0
  IfcData = IfcUID=2DPp5cUajCNBraILIYWVwM,+2 more (map truncated)
  IfcType = 52
  Material = -> Material010
  MoveBase = false
  MoveWithHost = false
  PerimeterLength = 0
  Placement = pos=(0,-150,0) rot=(0,0,1;0rad)
  VerticalArea = 0
FEATURE [Part::FeaturePython] Component010  label="Вентканал 140мм 005"  # Arch/BIM 52 (typed FeaturePython)
  Base = -> Pipe013
  GlobalId = 2ewKzaCcr5eA7xHkmfw3LN
  HorizontalArea = 0
  IfcData = IfcUID=2ewKzaCcr5eA7xHkmfw3LN,+2 more (map truncated)
  IfcType = 52
  Material = -> Material010
  MoveBase = false
  MoveWithHost = false
  PerimeterLength = 0
  Placement = pos=(150,0,0) rot=(0,0,1;0rad)
  VerticalArea = 0
FEATURE [Part::FeaturePython] Component011  label="Фановый стояк 002"  # Arch/BIM 52 (typed FeaturePython)
  Base = -> Pipe006
  GlobalId = 0fM_EzyLfDH9wwlzWxKcxT
  HorizontalArea = 0
  IfcData = IfcUID=0fM_EzyLfDH9wwlzWxKcxT,+2 more (map truncated)
  IfcType = 52
  Material = -> Material010
  MoveBase = false
  MoveWithHost = false
  PerimeterLength = 0
  VerticalArea = 0
FEATURE [Part::FeaturePython] Component013  label="бак расширительный001"  # Arch/BIM 52 (typed FeaturePython)
  Base = -> Cylinder003
  GlobalId = 1M0Pc_1oL1dAVej87m7tiQ
  HorizontalArea = 0
  IfcData = IfcUID=1M0Pc_1oL1dAVej87m7tiQ,+2 more (map truncated)
  IfcType = 52
  Material = -> Material010
  MoveBase = false
  MoveWithHost = false
  PerimeterLength = 0
  Placement = pos=(7730,1990,2200) rot=(0,0,1;0rad)
  VerticalArea = 0
FEATURE [Part::FeaturePython] Component014  label="Котёл 24кВт одноконтурн. закртытая камера001"  # Arch/BIM 52 (typed FeaturePython)
  Base = -> Box3220
  GlobalId = 3xYIuffef0591nSqu_zTts
  HorizontalArea = 0
  IfcData = IfcUID=3xYIuffef0591nSqu_zTts,+2 more (map truncated)
  IfcType = 52
  Material = -> Material010
  MoveBase = false
  MoveWithHost = false
  PerimeterLength = 0
  Placement = pos=(8130,2000,1300) rot=(0,0,1;0rad)
  VerticalArea = 0
FEATURE [Part::FeaturePython] Component015  label="БКН 120л001"  # Arch/BIM 52 (typed FeaturePython)
  Base = -> Cylinder002
  GlobalId = 1rGDNCqJr9TfpJcmQRNPPi
  HorizontalArea = 0
  IfcData = IfcUID=1rGDNCqJr9TfpJcmQRNPPi,+2 more (map truncated)
  IfcType = 52
  Material = -> Material010
  MoveBase = false
  MoveWithHost = false
  PerimeterLength = 0
  Placement = pos=(7730,1990,1000) rot=(0,0,1;0rad)
  VerticalArea = 0
FEATURE [Part::FeaturePython] Component016  label="грёбенка и насосы001"  # Arch/BIM 52 (typed FeaturePython)
  Base = -> Box3222
  GlobalId = 2B4UVsrmbF4xKMeEbnOrEi
  HorizontalArea = 0
  IfcData = IfcUID=2B4UVsrmbF4xKMeEbnOrEi,+2 more (map truncated)
  IfcType = 52
  Material = -> Material010
  MoveBase = false
  MoveWithHost = false
  PerimeterLength = 0
  Placement = pos=(7450,-10,0) rot=(0,0,1;0rad)
  VerticalArea = 0
FEATURE [Part::FeaturePython] Component017  label="Гидроакк. 100л001"  # Arch/BIM 52 (typed FeaturePython)
  Base = -> Cylinder004
  GlobalId = 3jeFyR0bH2F9QaToboQra_
  HorizontalArea = 0
  IfcData = IfcUID=3jeFyR0bH2F9QaToboQra_,+2 more (map truncated)
  IfcType = 52
  Material = -> Material010
  MoveBase = false
  MoveWithHost = false
  PerimeterLength = 0
  Placement = pos=(8350,2020,140) rot=(0,0,1;0rad)
  VerticalArea = 0
FEATURE [Part::FeaturePython] Component018  label="Котёл электр. (резерв)001"  # Arch/BIM 52 (typed FeaturePython)
  Base = -> Box3223
  GlobalId = 3fLs6$YNDCqPUF9yh_StuK
  HorizontalArea = 0
  IfcData = IfcUID=3fLs6$YNDCqPUF9yh_StuK,+2 more (map truncated)
  IfcType = 52
  Material = -> Material010
  MoveBase = false
  MoveWithHost = false
  PerimeterLength = 0
  Placement = pos=(7600,1490,1300) rot=(0,0,1;1.5708rad)
  VerticalArea = 0
FEATURE [App::MaterialObjectPython] Material012  label="Wood_mebel"  # material (typed FeaturePython)
  Description = A standard construction wood
  Material = AuthorAndLicense=Wood-Generic,CardName=Wood-Generic,Color=(0.34509803921568627, 0.6627450980392157, 0.5058823529411764, 1.0),Density=700 kg/m^3,+10 more (map truncated)
  ProductURL = https://en.wikipedia.org/wiki/Wood
  Transparency = 0
FEATURE [Part::FeaturePython] Component019  label="Мебель_001"  # Arch/BIM 52 (typed FeaturePython)
  Base = -> Box3143
  GlobalId = 3nI$K5MXnFSf1FSLhknV3E
  HorizontalArea = 0
  IfcData = IfcUID=3nI$K5MXnFSf1FSLhknV3E,+2 more (map truncated)
  IfcType = 52
  Material = -> Material012
  MoveBase = false
  MoveWithHost = false
  PerimeterLength = 0
  Placement = pos=(320,-25,0) rot=(0,0,1;1.5708rad)
  VerticalArea = 0
FEATURE [Part::FeaturePython] Component020  label="Мебель_031"  # Arch/BIM 52 (typed FeaturePython)
  Base = -> Box3216
  GlobalId = 0sMfDnDfXDKQPzl59nSg3w
  HorizontalArea = 0
  IfcData = IfcUID=0sMfDnDfXDKQPzl59nSg3w,+2 more (map truncated)
  IfcType = 52
  Material = -> Material012
  MoveBase = false
  MoveWithHost = false
  PerimeterLength = 0
  Placement = pos=(320,875,0) rot=(0,0,1;1.5708rad)
  VerticalArea = 0
FEATURE [Part::FeaturePython] Component021  label="Мебель_032"  # Arch/BIM 52 (typed FeaturePython)
  Base = -> Box3204
  GlobalId = 3v4KZ3erzAjxwqMZOEXsgs
  HorizontalArea = 0
  IfcData = IfcUID=3v4KZ3erzAjxwqMZOEXsgs,+2 more (map truncated)
  IfcType = 52
  Material = -> Material012
  MoveBase = false
  MoveWithHost = false
  PerimeterLength = 0
  Placement = pos=(370,3825,0) rot=(0,0,1;1.5708rad)
  VerticalArea = 0
FEATURE [Part::FeaturePython] Component022  label="Мебель_033"  # Arch/BIM 52 (typed FeaturePython)
  Base = -> Box3157
  GlobalId = 1irmjboHHBgQGOddX9HYrQ
  HorizontalArea = 0
  IfcData = IfcUID=1irmjboHHBgQGOddX9HYrQ,+2 more (map truncated)
  IfcType = 52
  Material = -> Material012
  MoveBase = false
  MoveWithHost = false
  PerimeterLength = 0
  Placement = pos=(-30,5040,0) rot=(0,0,1;0rad)
  VerticalArea = 0
FEATURE [Part::FeaturePython] Component023  label="Мебель_034"  # Arch/BIM 52 (typed FeaturePython)
  Base = -> Box3217
  GlobalId = 3xnzb49$n4OeOTx2O8OBOQ
  HorizontalArea = 0
  IfcData = IfcUID=3xnzb49$n4OeOTx2O8OBOQ,+2 more (map truncated)
  IfcType = 52
  Material = -> Material012
  MoveBase = false
  MoveWithHost = false
  PerimeterLength = 0
  Placement = pos=(-30,5640,0) rot=(0,0,1;0rad)
  VerticalArea = 0
FEATURE [Part::FeaturePython] Component024  label="Мебель_035"  # Arch/BIM 52 (typed FeaturePython)
  Base = -> Box3218
  GlobalId = 3zlhB5eMrASwK$nF_B$17d
  HorizontalArea = 0
  IfcData = IfcUID=3zlhB5eMrASwK$nF_B$17d,+2 more (map truncated)
  IfcType = 52
  Material = -> Material012
  MoveBase = false
  MoveWithHost = false
  PerimeterLength = 0
  Placement = pos=(370,6240,0) rot=(0,0,1;1.5708rad)
  VerticalArea = 0
FEATURE [Part::FeaturePython] Component025  label="Мебель_036"  # Arch/BIM 52 (typed FeaturePython)
  Base = -> Box3156
  GlobalId = 2LlK29D3D0RBA6mNzylxS_
  HorizontalArea = 0
  IfcData = IfcUID=2LlK29D3D0RBA6mNzylxS_,+2 more (map truncated)
  IfcType = 52
  Material = -> Material012
  MoveBase = false
  MoveWithHost = false
  PerimeterLength = 0
  Placement = pos=(4000,-25,0) rot=(0,0,1;1.5708rad)
  VerticalArea = 0
FEATURE [Part::FeaturePython] Component026  label="Мебель_037"  # Arch/BIM 52 (typed FeaturePython)
  Base = -> Box3155
  GlobalId = 2akPkUu2HEGPHq0U02EI1f
  HorizontalArea = 0
  IfcData = IfcUID=2akPkUu2HEGPHq0U02EI1f,+2 more (map truncated)
  IfcType = 52
  Material = -> Material012
  MoveBase = false
  MoveWithHost = false
  PerimeterLength = 0
  Placement = pos=(4100,1685,0) rot=(0,0,1;0rad)
  VerticalArea = 0
FEATURE [Part::FeaturePython] Component027  label="Мебель_038"  # Arch/BIM 52 (typed FeaturePython)
  Base = -> Box3154
  GlobalId = 01rWHBvXv688jV3_Ss2xzX
  HorizontalArea = 0
  IfcData = IfcUID=01rWHBvXv688jV3_Ss2xzX,+2 more (map truncated)
  IfcType = 52
  Material = -> Material012
  MoveBase = false
  MoveWithHost = false
  PerimeterLength = 0
  Placement = pos=(7350,-25,0) rot=(0,0,1;1.5708rad)
  VerticalArea = 0
FEATURE [Part::FeaturePython] Component028  label="Мебель_039"  # Arch/BIM 52 (typed FeaturePython)
  Base = -> Box3203
  GlobalId = 0TELnS7a95EADyr_UuBryd
  HorizontalArea = 0
  IfcData = IfcUID=0TELnS7a95EADyr_UuBryd,+2 more (map truncated)
  IfcType = 52
  Material = -> Material012
  MoveBase = false
  MoveWithHost = false
  PerimeterLength = 0
  Placement = pos=(8850,-25,800) rot=(0,0,1;0rad)
  VerticalArea = 0
FEATURE [Part::FeaturePython] Component029  label="Мебель_040"  # Arch/BIM 52 (typed FeaturePython)
  Base = -> Box3163
  GlobalId = 3x$ZLcTwH4lOi2HV3kkIS2
  HorizontalArea = 0
  IfcData = IfcUID=3x$ZLcTwH4lOi2HV3kkIS2,+2 more (map truncated)
  IfcType = 52
  Material = -> Material012
  MoveBase = false
  MoveWithHost = false
  PerimeterLength = 0
  Placement = pos=(4100,-25,0) rot=(0,0,1;0rad)
  VerticalArea = 0
FEATURE [App::MaterialObjectPython] Material013  label="ceramic other"  # material (typed FeaturePython)
  Description = ceramic other
  Material = AuthorAndLicense=Concrete-Generic,CardName=Concrete-Generic,Color=(0.8117647058823529, 0.8117647058823529, 0.8117647058823529, 1.0),+11 more (map truncated)
  Transparency = 0
FEATURE [Part::FeaturePython] Structure343  label="Ванна 180х90"  # Arch/BIM 52 (typed FeaturePython)
  Base = -> Wire808
  FaceMaker = 0
  GlobalId = 2VbcwV0QPCqROXcrzT3$_s
  Height = 600
  HorizontalArea = 1.674e+06
  IfcData = IfcUID=2VbcwV0QPCqROXcrzT3$_s,+2 more (map truncated)
  IfcType = 52
  Length = 0
  Material = -> Material013
  MoveBase = false
  MoveWithHost = false
  Nodes = (2) [(-2856.79,7112.64,0),(-2856.79,7112.64,600)]
  NodesOffset = 0
  Normal = (0,0,1)
  PerimeterLength = 4240.95
  Subtractions = -> [Structure342,Wall240]
  VerticalArea = 5073000
  Width = 100
FEATURE [Part::FeaturePython] Structure347  label="Раковина 81х45 Hatria Area"  # Arch/BIM 52 (typed FeaturePython)
  Base = -> Wire812
  FaceMaker = 0
  GlobalId = 2d5W_OQQf2Fxkoe6wMEOb9
  Height = 150
  HorizontalArea = 0
  IfcData = IfcUID=2d5W_OQQf2Fxkoe6wMEOb9,+2 more (map truncated)
  IfcType = 52
  Length = 0
  Material = -> Material013
  MoveBase = false
  MoveWithHost = false
  Nodes = (2) [(-2856.79,7112.64,0),(-2856.79,7112.64,600)]
  NodesOffset = 0
  Normal = (0,0,1)
  PerimeterLength = 0
  Placement = pos=(0,0,850) rot=(0,0,1;0rad)
  Subtractions = -> [Structure346]
  VerticalArea = 0
  Width = 100
FEATURE [Part::FeaturePython] Component030  label="унитаз с инсталляцией 003"  # Arch/BIM 52 (typed FeaturePython)
  Base = -> Fusion041
  GlobalId = 1DHlQrIaXCZ9oXu4naqRMg
  HorizontalArea = 0
  IfcData = IfcUID=1DHlQrIaXCZ9oXu4naqRMg,+2 more (map truncated)
  IfcType = 52
  Material = -> Material013
  MoveBase = false
  MoveWithHost = false
  PerimeterLength = 0
  Placement = pos=(10970,-6405,0) rot=(0,0,1;1.5708rad)
  VerticalArea = 0
FEATURE [Part::FeaturePython] Component031  label="Душ 100*081"  # Arch/BIM 52 (typed FeaturePython)
  Base = -> Box3215
  GlobalId = 2$9kHs27rDI8YZvC992Gc0
  HorizontalArea = 0
  IfcData = IfcUID=2$9kHs27rDI8YZvC992Gc0,+2 more (map truncated)
  IfcType = 52
  Material = -> Material013
  MoveBase = false
  MoveWithHost = false
  PerimeterLength = 0
  Placement = pos=(6950,3825,-10) rot=(0,0,1;0rad)
  VerticalArea = 0
FEATURE [App::MaterialObjectPython] Material014  label="Wood (laminate)"  # material (typed FeaturePython)
  Description = A standard construction wood
  Material = AuthorAndLicense=Wood-Generic,CardName=Wood-Generic,Color=(0.8196078431372549, 0.8196078431372549, 0.8196078431372549, 1.0),Density=700 kg/m^3,+10 more (map truncated)
  ProductURL = https://en.wikipedia.org/wiki/Wood
  Transparency = 0
FEATURE [App::MaterialObjectPython] Material015  label="Other mebel"  # material (typed FeaturePython)
  Description = Other mebel
  Material = AuthorAndLicense=Wood-Generic,CardName=Wood-Generic,Color=(0.6196078431372549, 0.6941176470588235, 0.7568627450980392, 1.0),Density=700 kg/m^3,+9 more (map truncated)
  Transparency = 0
FEATURE [Part::FeaturePython] Structure277  label="Structure020"  # Arch/BIM 52 (typed FeaturePython)
  Base = -> Rectangle546
  FaceMaker = 0
  GlobalId = 2DDa$j80P5hvQ3LPUQNes4
  Height = 200
  HorizontalArea = 404463
  IfcData = IfcUID=2DDa$j80P5hvQ3LPUQNes4,attributes={"GlobalId": {"value": "2DDa$j80P5hvQ3LPUQNes4"}},+1 more (map truncated)
  IfcType = 52
  Length = 0
  Material = -> Material015
  MoveBase = false
  MoveWithHost = false
  Nodes = (2) [(1656.58,7240.7,0),(1656.58,7240.7,200)]
  NodesOffset = 0
  Normal = (0,0,0)
  PerimeterLength = 3697.08
  Placement = pos=(0,0,400) rot=(0,0,1;0rad)
  VerticalArea = 739416
  Width = 100
FEATURE [Part::FeaturePython] Structure278  label="Structure021"  # Arch/BIM 52 (typed FeaturePython)
  Base = -> Rectangle547
  FaceMaker = 0
  GlobalId = 3Z9IWRZuT13weCYbg7_Khd
  Height = 200
  HorizontalArea = 236963
  IfcData = IfcUID=3Z9IWRZuT13weCYbg7_Khd,attributes={"GlobalId": {"value": "3Z9IWRZuT13weCYbg7_Khd"}},+1 more (map truncated)
  IfcType = 52
  Length = 0
  Material = -> Material015
  MoveBase = false
  MoveWithHost = false
  Nodes = (2) [(156.577,7240.7,0),(156.577,7240.7,200)]
  NodesOffset = 0
  Normal = (0,0,0)
  PerimeterLength = 2357.08
  Placement = pos=(0,0,400) rot=(0,0,1;0rad)
  VerticalArea = 471416
  Width = 100
FEATURE [Part::FeaturePython] Structure275  label="Structure018"  # Arch/BIM 52 (typed FeaturePython)
  Base = -> Rectangle544
  FaceMaker = 0
  GlobalId = 1sWNXrsjP3FQ$2jjEvDesy
  Height = 400
  HorizontalArea = 749463
  IfcData = IfcUID=1sWNXrsjP3FQ$2jjEvDesy,attributes={"GlobalId": {"value": "1sWNXrsjP3FQ$2jjEvDesy"}},+1 more (map truncated)
  IfcType = 52
  Length = 0
  Material = -> Material015
  MoveBase = false
  MoveWithHost = false
  Nodes = (2) [(182.895,-1383.89,0),(182.895,-1383.89,400)]
  NodesOffset = 0
  Normal = (0,0,0)
  PerimeterLength = 5557.08
  Placement = pos=(0,0,400) rot=(0,0,1;0rad)
  VerticalArea = 2.22283e+06
  Width = 100
FEATURE [Part::FeaturePython] Structure276  label="Structure019"  # Arch/BIM 52 (typed FeaturePython)
  Base = -> Rectangle545
  FaceMaker = 0
  GlobalId = 3fmvKSc5DEWOPxKz6nUpvm
  Height = 400
  HorizontalArea = 2.37446e+06
  IfcData = IfcUID=3fmvKSc5DEWOPxKz6nUpvm,attributes={"GlobalId": {"value": "3fmvKSc5DEWOPxKz6nUpvm"}},+1 more (map truncated)
  IfcType = 52
  Length = 0
  Material = -> Material015
  MoveBase = false
  MoveWithHost = false
  Nodes = (2) [(906.577,7240.7,0),(906.577,7240.7,400)]
  NodesOffset = 0
  Normal = (0,0,0)
  PerimeterLength = 6857.08
  VerticalArea = 2.74283e+06
  Width = 100
FEATURE [Part::FeaturePython] Structure279  label="Structure143"  # Arch/BIM 52 (typed FeaturePython)
  Base = -> Rectangle2837
  FaceMaker = 0
  GlobalId = 3TZavIZkH49B1D2AaSuAzL
  Height = 400
  HorizontalArea = 602463
  IfcData = IfcUID=3TZavIZkH49B1D2AaSuAzL,attributes={"GlobalId": {"value": "3TZavIZkH49B1D2AaSuAzL"}},+1 more (map truncated)
  IfcType = 52
  Length = 0
  Material = -> Material015
  MoveBase = false
  MoveWithHost = false
  Nodes = (2) [(906.577,7240.7,0),(906.577,7240.7,400)]
  NodesOffset = 0
  Normal = (0,0,0)
  PerimeterLength = 3097.08
  VerticalArea = 1.23883e+06
  Width = 100
FEATURE [App::GeometryPython] BuildingPart065  label="Диван 250x162L"  # Arch/BIM 52 (typed FeaturePython)
  Area = 0
  GlobalId = 1oZyr4jbn08vwhGg8DOzPQ
  Group = -> [Structure275,Structure278,Structure276,Structure277,Structure279]
  Height = 0
  HeightPropagate = true
  IfcData = IfcUID=1oZyr4jbn08vwhGg8DOzPQ,attributes={"GlobalId": {"value": "1oZyr4jbn08vwhGg8DOzPQ"}},+1 more (map truncated)
  IfcType = 52
  LevelOffset = 0
FEATURE [Part::FeaturePython] Structure339  label="Тумба под ТВ"  # Arch/BIM 52 (typed FeaturePython)
  Base = -> Wire784
  FaceMaker = 0
  GlobalId = 02q3nx$AH4fB0PqHacSjsk
  Height = 550
  HorizontalArea = 1.11339e+06
  IfcData = IfcUID=02q3nx$AH4fB0PqHacSjsk,+2 more (map truncated)
  IfcType = 52
  Length = 0
  Material = -> Material015
  MoveBase = false
  MoveWithHost = false
  Nodes = (2) [(8157.91,5216.2,0),(8157.91,5216.2,550)]
  NodesOffset = 0
  Normal = (0,0,1)
  PerimeterLength = 6499.55
  VerticalArea = 3.57475e+06
  Width = 100
FEATURE [Part::FeaturePython] Component032  label="стол обеденный001"  # Arch/BIM 52 (typed FeaturePython)
  Base = -> Fillet001
  GlobalId = 30KhDQuLT9PRlsli0ojqYH
  HorizontalArea = 0
  IfcData = IfcUID=30KhDQuLT9PRlsli0ojqYH,+2 more (map truncated)
  IfcType = 52
  Material = -> Material014
  MoveBase = false
  MoveWithHost = false
  PerimeterLength = 0
  Placement = pos=(10350,2890,0) rot=(0,0,1;0rad)
  VerticalArea = 0
FEATURE [Part::FeaturePython] Component033  label="стул013"  # Arch/BIM 52 (typed FeaturePython)
  Base = -> Fusion015
  GlobalId = 1jDmJlQDDCvfAqy4Wlc4hX
  HorizontalArea = 0
  IfcData = IfcUID=1jDmJlQDDCvfAqy4Wlc4hX,+2 more (map truncated)
  IfcType = 52
  Material = -> Material014
  MoveBase = false
  MoveWithHost = false
  PerimeterLength = 0
  Placement = pos=(10350,2890,0) rot=(0,0,1;0rad)
  VerticalArea = 0
FEATURE [Part::FeaturePython] Component034  label="стул012"  # Arch/BIM 52 (typed FeaturePython)
  Base = -> Fusion014
  GlobalId = 2fjpVYF01FEf1CPxL3Q2Wu
  HorizontalArea = 0
  IfcData = IfcUID=2fjpVYF01FEf1CPxL3Q2Wu,+2 more (map truncated)
  IfcType = 52
  Material = -> Material014
  MoveBase = false
  MoveWithHost = false
  PerimeterLength = 0
  Placement = pos=(10350,2890,0) rot=(0,0,1;0rad)
  VerticalArea = 0
FEATURE [Part::FeaturePython] Component035  label="стул011"  # Arch/BIM 52 (typed FeaturePython)
  Base = -> Fusion016
  GlobalId = 2rbIXYhRj4JgNPKMNl$8l7
  HorizontalArea = 0
  IfcData = IfcUID=2rbIXYhRj4JgNPKMNl$8l7,+2 more (map truncated)
  IfcType = 52
  Material = -> Material014
  MoveBase = false
  MoveWithHost = false
  PerimeterLength = 0
  Placement = pos=(10350,2890,0) rot=(0,0,1;0rad)
  VerticalArea = 0
FEATURE [Part::FeaturePython] Component036  label="стул010"  # Arch/BIM 52 (typed FeaturePython)
  Base = -> Fusion013
  GlobalId = 1ih4cOnfvDqPPYXDMeM0vw
  HorizontalArea = 0
  IfcData = IfcUID=1ih4cOnfvDqPPYXDMeM0vw,+2 more (map truncated)
  IfcType = 52
  Material = -> Material014
  MoveBase = false
  MoveWithHost = false
  PerimeterLength = 0
  Placement = pos=(10350,2890,0) rot=(0,0,1;0rad)
  VerticalArea = 0
FEATURE [Part::FeaturePython] Component037  label="Столик журнальный001"  # Arch/BIM 52 (typed FeaturePython)
  Base = -> Fillet003
  GlobalId = 2_br9eASD3lOnwEF_KCKKD
  HorizontalArea = 0
  IfcData = IfcUID=2_br9eASD3lOnwEF_KCKKD,+2 more (map truncated)
  IfcType = 52
  Material = -> Material014
  MoveBase = false
  MoveWithHost = false
  PerimeterLength = 0
  Placement = pos=(13600,-900,0) rot=(0,0,1;0rad)
  VerticalArea = 0
FEATURE [App::MaterialObjectPython] Material016  label="PVC"  # material (typed FeaturePython)
  Material = AuthorAndLicense=PVC-Generic,CardName=PVC-Generic,Color=(0.10980392156862745, 0.050980392156862744, 0.050980392156862744, 1.0),Density=1380 kg/m^3,+13 more (map truncated)
  ProductURL = https://en.wikipedia.org/wiki/Polyvinyl_chloride
  Transparency = 0
FEATURE [Part::FeaturePython] Component038  label="TV 001"  # Arch/BIM 52 (typed FeaturePython)
  Base = -> Box3145
  GlobalId = 2JRZAdYer2vvHxwrBL$6Tl
  HorizontalArea = 0
  IfcData = IfcUID=2JRZAdYer2vvHxwrBL$6Tl,+2 more (map truncated)
  IfcType = 52
  Material = -> Material016
  MoveBase = false
  MoveWithHost = false
  PerimeterLength = 0
  Placement = pos=(8090,6200,620) rot=(0,0,-1;1.5708rad)
  VerticalArea = 0
FEATURE [Part::FeaturePython] Component039  label="TV 002"  # Arch/BIM 52 (typed FeaturePython)
  Base = -> Box3159
  GlobalId = 1KbL9tWEn0_9owhEd3OMOe
  HorizontalArea = 0
  IfcData = IfcUID=1KbL9tWEn0_9owhEd3OMOe,+2 more (map truncated)
  IfcType = 52
  Material = -> Material016
  MoveBase = false
  MoveWithHost = false
  PerimeterLength = 0
  Placement = pos=(4720,6225,620) rot=(0,0,-1;1.5708rad)
  VerticalArea = 0
FEATURE [Part::FeaturePython] Component040  label="кровать 2 спальная 210х170 003"  # Arch/BIM 52 (typed FeaturePython)
  Base = -> Fusion019
  GlobalId = 178W44cHTAbgFocl2NGJXF
  HorizontalArea = 0
  IfcData = IfcUID=178W44cHTAbgFocl2NGJXF,+2 more (map truncated)
  IfcType = 52
  Material = -> Material015
  MoveBase = false
  MoveWithHost = false
  PerimeterLength = 0
  Placement = pos=(6970,7925,0) rot=(0,0,-1;1.5708rad)
  VerticalArea = 0
FEATURE [Part::FeaturePython] Component041  label="Диван кабинет001"  # Arch/BIM 52 (typed FeaturePython)
  Base = -> Fusion027
  GlobalId = 03vX7Qg392WAqcZgndFghb
  HorizontalArea = 0
  IfcData = IfcUID=03vX7Qg392WAqcZgndFghb,+2 more (map truncated)
  IfcType = 52
  Material = -> Material015
  MoveBase = false
  MoveWithHost = false
  PerimeterLength = 0
  Placement = pos=(3475,2970,0) rot=(0,0,1;3.14159rad)
  VerticalArea = 0
FEATURE [Part::FeaturePython] Component042  label="стол письменный001"  # Arch/BIM 52 (typed FeaturePython)
  Base = -> Fillet004
  GlobalId = 1qvzd8t693bQPX5BZwJPZ7
  HorizontalArea = 0
  IfcData = IfcUID=1qvzd8t693bQPX5BZwJPZ7,+2 more (map truncated)
  IfcType = 52
  Material = -> Material014
  MoveBase = false
  MoveWithHost = false
  PerimeterLength = 0
  Placement = pos=(1140,1890,0) rot=(0,0,1;1.5708rad)
  VerticalArea = 0
FEATURE [Part::FeaturePython] Component043  label="стул014"  # Arch/BIM 52 (typed FeaturePython)
  Base = -> Fusion045
  GlobalId = 1cZkVUkvD10h41bCcuxnEs
  HorizontalArea = 0
  IfcData = IfcUID=1cZkVUkvD10h41bCcuxnEs,+2 more (map truncated)
  IfcType = 52
  Material = -> Material014
  MoveBase = false
  MoveWithHost = false
  PerimeterLength = 0
  Placement = pos=(-462.225,3197.19,0) rot=(0,0,-1;1.5708rad)
  VerticalArea = 0
FEATURE [Part::FeaturePython] Component044  label="бутыль воды001"  # Arch/BIM 52 (typed FeaturePython)
  Base = -> Cylinder
  GlobalId = 0nuTQ1H4vFqAFkLsCfzz$Y
  HorizontalArea = 0
  IfcData = IfcUID=0nuTQ1H4vFqAFkLsCfzz$Y,+2 more (map truncated)
  IfcType = 52
  Material = -> Material006
  MoveBase = false
  MoveWithHost = false
  PerimeterLength = 0
  Placement = pos=(12395,4730,950) rot=(0,0,1;0rad)
  VerticalArea = 0
FEATURE [Part::FeaturePython] Component047  label="кулер001"  # Arch/BIM 52 (typed FeaturePython)
  Base = -> Box3191
  GlobalId = 1NUnbntaH5wfvllth3pArq
  HorizontalArea = 0
  IfcData = IfcUID=1NUnbntaH5wfvllth3pArq,+2 more (map truncated)
  IfcType = 52
  Material = -> Material015
  MoveBase = false
  MoveWithHost = false
  PerimeterLength = 0
  Placement = pos=(12240,4575,0) rot=(0,0,1;0rad)
  VerticalArea = 0
FEATURE [Part::FeaturePython] Component048  label="комод001"  # Arch/BIM 52 (typed FeaturePython)
  Base = -> Box3227
  GlobalId = 3x1u_ovjXEMwAlsSbA8GHf
  HorizontalArea = 0
  IfcData = IfcUID=3x1u_ovjXEMwAlsSbA8GHf,+2 more (map truncated)
  IfcType = 52
  Material = -> Material015
  MoveBase = false
  MoveWithHost = false
  PerimeterLength = 0
  Placement = pos=(12240,3825,0) rot=(0,0,1;0rad)
  VerticalArea = 0
FEATURE [App::GeometryPython] BuildingPart047  label="Мебель другая"  # Arch/BIM 52 (typed FeaturePython)
  Area = 0
  GlobalId = 1Dl8CuxJnEPxKEPVOok4FA
  Group = -> [BuildingPart065,Structure339,Component019,Component020,Component021,Component022,Component023,Component024,Component025,Component026,Component027,Component028,Component029,Component032,Component033,Component034,Component035,Component036,Component037,Component038,Component039,Component040,Component041,Component042,Component043,Component047,Component048,Component044]
  Height = 0
  HeightPropagate = true
  IfcData = IfcUID=1Dl8CuxJnEPxKEPVOok4FA,attributes={"GlobalId": {"value": "1Dl8CuxJnEPxKEPVOok4FA"}},+1 more (map truncated)
  IfcType = 52
  LevelOffset = 0
FEATURE [App::MaterialObjectPython] Material017  label="Steel (white)"  # material (typed FeaturePython)
  Material = AuthorAndLicense=Steel-Generic,CardName=Steel-Generic,Color=(0.6549019607843137, 0.8823529411764706, 0.9058823529411765, 1.0),Density=7900 kg/m^3,+12 more (map truncated)
  ProductURL = https://en.wikipedia.org/wiki/Steel
  Transparency = 0
FEATURE [Part::FeaturePython] Component045  label="морозильник 60 см001"  # Arch/BIM 52 (typed FeaturePython)
  Base = -> Box3183
  GlobalId = 1vDB6tGTv9rA3TFt87TZXl
  HorizontalArea = 0
  IfcData = IfcUID=1vDB6tGTv9rA3TFt87TZXl,+2 more (map truncated)
  IfcType = 52
  Material = -> Material017
  MoveBase = false
  MoveWithHost = false
  PerimeterLength = 0
  Placement = pos=(8250,-25,0) rot=(0,0,1;0rad)
  VerticalArea = 0
FEATURE [Part::FeaturePython] Component046  label="СМ001"  # Arch/BIM 52 (typed FeaturePython)
  Base = -> Box3184
  GlobalId = 3p89ErDe9E9Opxcq8_zvGg
  HorizontalArea = 0
  IfcData = IfcUID=3p89ErDe9E9Opxcq8_zvGg,+2 more (map truncated)
  IfcType = 52
  Material = -> Material017
  MoveBase = false
  MoveWithHost = false
  PerimeterLength = 0
  Placement = pos=(8850,-25,0) rot=(0,0,1;0rad)
  VerticalArea = 0
FEATURE [Part::FeaturePython] Component049  label="Кухонная мебель 001"  # Arch/BIM 52 (typed FeaturePython)
  Base = -> Fusion044
  GlobalId = 1ieDP$cJrBk8JUU$BNtJAd
  HorizontalArea = 0
  IfcData = IfcUID=1ieDP$cJrBk8JUU$BNtJAd,+2 more (map truncated)
  IfcType = 52
  Material = -> Material015
  MoveBase = false
  MoveWithHost = false
  PerimeterLength = 0
  Placement = pos=(0,-15,0) rot=(0,0,1;0rad)
  VerticalArea = 0
FEATURE [Part::FeaturePython] Component050  label="Кухонная мебель 040"  # Arch/BIM 52 (typed FeaturePython)
  Base = -> Box3175
  GlobalId = 1ED_GkK7LDUfuRWPN8I4HD
  HorizontalArea = 0
  IfcData = IfcUID=1ED_GkK7LDUfuRWPN8I4HD,+2 more (map truncated)
  IfcType = 52
  Material = -> Material015
  MoveBase = false
  MoveWithHost = false
  PerimeterLength = 0
  Placement = pos=(10150,-25,0) rot=(0,0,1;1.5708rad)
  VerticalArea = 0
FEATURE [Part::FeaturePython] Component051  label="Кухонная мебель 041"  # Arch/BIM 52 (typed FeaturePython)
  Base = -> Box3178
  GlobalId = 2Zjfoa06D7BB00eGawwvIP
  HorizontalArea = 0
  IfcData = IfcUID=2Zjfoa06D7BB00eGawwvIP,+2 more (map truncated)
  IfcType = 52
  Material = -> Material014
  MoveBase = false
  MoveWithHost = false
  PerimeterLength = 0
  Placement = pos=(10750,-25,1600) rot=(0,0,1;0rad)
  VerticalArea = 0
FEATURE [Part::FeaturePython] Component052  label="Кухонная мебель 042"  # Arch/BIM 52 (typed FeaturePython)
  Base = -> Box3179
  GlobalId = 2zXaDShtTEIwaqsWia$bJe
  HorizontalArea = 0
  IfcData = IfcUID=2zXaDShtTEIwaqsWia$bJe,+2 more (map truncated)
  IfcType = 52
  Material = -> Material015
  MoveBase = false
  MoveWithHost = false
  PerimeterLength = 0
  Placement = pos=(9550,-25,1600) rot=(0,0,1;0rad)
  VerticalArea = 0
FEATURE [Part::FeaturePython] Component053  label="Кухонная мебель 043"  # Arch/BIM 52 (typed FeaturePython)
  Base = -> Loft001
  GlobalId = 2NbjGyofnF4Q_5s1mmRZID
  HorizontalArea = 0
  IfcData = IfcUID=2NbjGyofnF4Q_5s1mmRZID,+2 more (map truncated)
  IfcType = 52
  Material = -> Material010
  MoveBase = false
  MoveWithHost = false
  PerimeterLength = 0
  Placement = pos=(0,-15,0) rot=(0,0,1;0rad)
  VerticalArea = 0
FEATURE [Part::FeaturePython] Component054  label="Кухонная мебель 044"  # Arch/BIM 52 (typed FeaturePython)
  Base = -> Box3192
  GlobalId = 37d12NPs5EAOYglb_81CGc
  HorizontalArea = 0
  IfcData = IfcUID=37d12NPs5EAOYglb_81CGc,+2 more (map truncated)
  IfcType = 52
  Material = -> Material011
  MoveBase = false
  MoveWithHost = false
  PerimeterLength = 0
  Placement = pos=(12494,3030.99,850) rot=(0,0,1;1.5708rad)
  VerticalArea = 0
FEATURE [Part::FeaturePython] Component055  label="Кухонная мебель 045"  # Arch/BIM 52 (typed FeaturePython)
  Base = -> Cylinder001
  GlobalId = 1nrzgZxzDATfvzL8VMDaoZ
  HorizontalArea = 0
  IfcData = IfcUID=1nrzgZxzDATfvzL8VMDaoZ,+2 more (map truncated)
  IfcType = 52
  Material = -> Material006
  MoveBase = false
  MoveWithHost = false
  PerimeterLength = 0
  Placement = pos=(12393.3,3344.1,850) rot=(0,0,1;1.5708rad)
  VerticalArea = 0
FEATURE [Part::FeaturePython] Component056  label="Кухонная мебель 046"  # Arch/BIM 52 (typed FeaturePython)
  Base = -> Box3195
  GlobalId = 0jonv5hkP7hB1P2BRJZFtA
  HorizontalArea = 0
  IfcData = IfcUID=0jonv5hkP7hB1P2BRJZFtA,+2 more (map truncated)
  IfcType = 52
  Material = -> Material015
  MoveBase = false
  MoveWithHost = false
  PerimeterLength = 0
  Placement = pos=(9550,-25,2300) rot=(0,0,1;0rad)
  VerticalArea = 0
FEATURE [Part::FeaturePython] Component057  label="Кухонная мебель 047"  # Arch/BIM 52 (typed FeaturePython)
  Base = -> Box3207
  GlobalId = 3unBum7Wr2XxUiA4dm2BNM
  HorizontalArea = 0
  IfcData = IfcUID=3unBum7Wr2XxUiA4dm2BNM,+2 more (map truncated)
  IfcType = 52
  Material = -> Material010
  MoveBase = false
  MoveWithHost = false
  PerimeterLength = 0
  Placement = pos=(12440,1330,100) rot=(0,0,1;1.5708rad)
  VerticalArea = 0
FEATURE [Part::FeaturePython] Component058  label="Кухонная мебель 048"  # Arch/BIM 52 (typed FeaturePython)
  Base = -> Cut043
  GlobalId = 0D9H_B8SfDFO$LhgA4khjg
  HorizontalArea = 0
  IfcData = IfcUID=0D9H_B8SfDFO$LhgA4khjg,+2 more (map truncated)
  IfcType = 52
  Material = -> Material015
  MoveBase = false
  MoveWithHost = false
  PerimeterLength = 0
  Placement = pos=(0,9.01e-13,0) rot=(0,0,1;0rad)
  VerticalArea = 0
FEATURE [Part::FeaturePython] Component059  label="Кухонная мебель 049"  # Arch/BIM 52 (typed FeaturePython)
  Base = -> Box3229
  GlobalId = 0wxRoUoAL2SRTsV_v4CUOt
  HorizontalArea = 0
  IfcData = IfcUID=0wxRoUoAL2SRTsV_v4CUOt,+2 more (map truncated)
  IfcType = 52
  Material = -> Material015
  MoveBase = false
  MoveWithHost = false
  PerimeterLength = 0
  Placement = pos=(10150,-25,1600) rot=(0,0,1;0rad)
  VerticalArea = 0
FEATURE [Part::FeaturePython] Component060  label="Кухонная мебель 050"  # Arch/BIM 52 (typed FeaturePython)
  Base = -> Cut045
  GlobalId = 2AztVf12z2KvLRx4YAzmc8
  HorizontalArea = 0
  IfcData = IfcUID=2AztVf12z2KvLRx4YAzmc8,+2 more (map truncated)
  IfcType = 52
  Material = -> Material015
  MoveBase = false
  MoveWithHost = false
  PerimeterLength = 0
  Placement = pos=(0,-15,0) rot=(0,0,1;0rad)
  VerticalArea = 0
FEATURE [Part::FeaturePython] Component061  label="Кухонная мебель 051"  # Arch/BIM 52 (typed FeaturePython)
  Base = -> Box3232
  GlobalId = 3Ik2mwhEnASuyGStdn9Hym
  HorizontalArea = 0
  IfcData = IfcUID=3Ik2mwhEnASuyGStdn9Hym,+2 more (map truncated)
  IfcType = 52
  Material = -> Material010
  MoveBase = false
  MoveWithHost = false
  PerimeterLength = 0
  Placement = pos=(10740,75,1000) rot=(0,0,1;1.5708rad)
  VerticalArea = 0
FEATURE [Part::FeaturePython] Component062  label="Кухонная мебель 052"  # Arch/BIM 52 (typed FeaturePython)
  Base = -> Box3233
  GlobalId = 0Wjbmkijf2hfmVL70WrgpJ
  HorizontalArea = 0
  IfcData = IfcUID=0Wjbmkijf2hfmVL70WrgpJ,+2 more (map truncated)
  IfcType = 52
  Material = -> Material010
  MoveBase = false
  MoveWithHost = false
  PerimeterLength = 0
  Placement = pos=(10740,75,450) rot=(0,0,1;1.5708rad)
  VerticalArea = 0
FEATURE [App::GeometryPython] BuildingPart045  label="Мебель кухонная"  # Arch/BIM 52 (typed FeaturePython)
  Area = 0
  GlobalId = 32uBXoaMr36Ak6fKsSPIPb
  Group = -> [Component046,Component045,Component049,Component050,Component051,Component052,Component053,Component054,Component055,Component056,Component057,Component058,Component059,Component060,Component061,Component062]
  Height = 0
  HeightPropagate = true
  IfcData = IfcUID=32uBXoaMr36Ak6fKsSPIPb,attributes={"GlobalId": {"value": "32uBXoaMr36Ak6fKsSPIPb"}},+1 more (map truncated)
  IfcType = 52
  LevelOffset = 0
FEATURE [Part::FeaturePython] Component075  label="Снегозадержание 001"  # Arch/BIM 52 (typed FeaturePython)
  Base = -> Pipe017
  GlobalId = 3fLgtWsyD8IOEn8l3TiBLL
  HorizontalArea = 0
  IfcData = IfcUID=3fLgtWsyD8IOEn8l3TiBLL,+2 more (map truncated)
  IfcType = 52
  Material = -> Material010
  MoveBase = false
  MoveWithHost = false
  PerimeterLength = 0
  Placement = pos=(0,0,50) rot=(0,0,1;0rad)
  VerticalArea = 0
FEATURE [Part::FeaturePython] Component076  label="Снегозадержание 022"  # Arch/BIM 52 (typed FeaturePython)
  Base = -> Pipe014
  GlobalId = 0fZFyhZkD7zPOVUYzK7U8n
  HorizontalArea = 0
  IfcData = IfcUID=0fZFyhZkD7zPOVUYzK7U8n,+2 more (map truncated)
  IfcType = 52
  Material = -> Material010
  MoveBase = false
  MoveWithHost = false
  PerimeterLength = 0
  Placement = pos=(0,0,50) rot=(0,0,1;0rad)
  VerticalArea = 0
FEATURE [Part::FeaturePython] Component077  label="Снегозадержание 023"  # Arch/BIM 52 (typed FeaturePython)
  Base = -> Pipe015
  GlobalId = 1LTO2PMRz6CfNW9W9wpak_
  HorizontalArea = 0
  IfcData = IfcUID=1LTO2PMRz6CfNW9W9wpak_,+2 more (map truncated)
  IfcType = 52
  Material = -> Material010
  MoveBase = false
  MoveWithHost = false
  PerimeterLength = 0
  Placement = pos=(0,0,50) rot=(0,0,1;0rad)
  VerticalArea = 0
FEATURE [Part::FeaturePython] Component078  label="Снегозадержание 024"  # Arch/BIM 52 (typed FeaturePython)
  Base = -> Pipe016
  GlobalId = 3fQfcs9tzCD9Q9FqWmmUZh
  HorizontalArea = 0
  IfcData = IfcUID=3fQfcs9tzCD9Q9FqWmmUZh,+2 more (map truncated)
  IfcType = 52
  Material = -> Material010
  MoveBase = false
  MoveWithHost = false
  PerimeterLength = 0
  Placement = pos=(0,0,50) rot=(0,0,1;0rad)
  VerticalArea = 0
FEATURE [Part::FeaturePython] Component079  label="Снегозадержание 025"  # Arch/BIM 52 (typed FeaturePython)
  Base = -> Pipe018
  GlobalId = 0JHLrOnyP7EehrYvml2qRo
  HorizontalArea = 0
  IfcData = IfcUID=0JHLrOnyP7EehrYvml2qRo,+2 more (map truncated)
  IfcType = 52
  Material = -> Material010
  MoveBase = false
  MoveWithHost = false
  PerimeterLength = 0
  Placement = pos=(0,0,50) rot=(0,0,1;0rad)
  VerticalArea = 0
FEATURE [Part::FeaturePython] Component080  label="Снегозадержание 026"  # Arch/BIM 52 (typed FeaturePython)
  Base = -> Pipe019
  GlobalId = 2smBLn7S1BvPhRI76FeC6b
  HorizontalArea = 0
  IfcData = IfcUID=2smBLn7S1BvPhRI76FeC6b,+2 more (map truncated)
  IfcType = 52
  Material = -> Material010
  MoveBase = false
  MoveWithHost = false
  PerimeterLength = 0
  Placement = pos=(0,0,50) rot=(0,0,1;0rad)
  VerticalArea = 0
FEATURE [Part::FeaturePython] Component081  label="Снегозадержание 027"  # Arch/BIM 52 (typed FeaturePython)
  Base = -> Pipe020
  GlobalId = 0$KWaMNPf21x_ja3hWF9hF
  HorizontalArea = 0
  IfcData = IfcUID=0$KWaMNPf21x_ja3hWF9hF,+2 more (map truncated)
  IfcType = 52
  Material = -> Material010
  MoveBase = false
  MoveWithHost = false
  PerimeterLength = 0
  Placement = pos=(0,0,50) rot=(0,0,1;0rad)
  VerticalArea = 0
FEATURE [Part::FeaturePython] Component082  label="Снегозадержание 028"  # Arch/BIM 52 (typed FeaturePython)
  Base = -> Pipe021
  GlobalId = 3Kb$CT3C16afQlV9OLZMZP
  HorizontalArea = 0
  IfcData = IfcUID=3Kb$CT3C16afQlV9OLZMZP,+2 more (map truncated)
  IfcType = 52
  Material = -> Material010
  MoveBase = false
  MoveWithHost = false
  PerimeterLength = 0
  Placement = pos=(0,0,50) rot=(0,0,1;0rad)
  VerticalArea = 0
FEATURE [App::GeometryPython] BuildingPart084  label="Снегозадержатели"  # Arch/BIM 52 (typed FeaturePython)
  Area = 0
  GlobalId = 10iOlZVPHFee_$fCiLahbp
  Group = -> [Component081,Component079,Component077,Component075,Component082,Component078,Component080,Component076]
  Height = 0
  HeightPropagate = true
  IfcData = IfcUID=10iOlZVPHFee_$fCiLahbp,+2 more (map truncated)
  IfcType = 52
  LevelOffset = 0
FEATURE [Part::Part2DObjectPython] Line1591  # Draft 2D object (typed FeaturePython)
  Area = 0
  ChamferSize = 0
  Closed = true
  End = (8945,2200.27,7500)
  FilletRadius = 0
  Length = 5600
  MakeFace = false
  Placement = pos=(8945,2200.27,6900) rot=(0,0,1;0rad)
  Points = (2) [(0,-6.91216e-10,-5000),(0,0,600)]
  Start = (8945,2200.27,1900)
  Subdivisions = 0
FEATURE [Part::FeaturePython] Pipe007002  label="Дымоход 201"  # Arch/BIM 98 (typed FeaturePython)
  Base = -> Line1591
  Diameter = 120
  GlobalId = 11JHR0lR55LRzzbgV05jpw
  HorizontalArea = 0
  IfcData = IfcUID=11JHR0lR55LRzzbgV05jpw,+2 more (map truncated)
  IfcType = 98
  Length = 5600
  Material = -> Material010
  MoveBase = false
  MoveWithHost = false
  OffsetEnd = 0
  OffsetStart = 0
  PerimeterLength = 0
  PredefinedType = 0
  VerticalArea = 0
  WallThickness = 0
FEATURE [Part::FeaturePython] Component084  label="Дымоход 120 002"  # Arch/BIM 52 (typed FeaturePython)
  Base = -> Pipe007002
  GlobalId = 1BRcTpsETD4PFK9C3ntAng
  HorizontalArea = 0
  IfcData = IfcUID=1BRcTpsETD4PFK9C3ntAng,+2 more (map truncated)
  IfcType = 52
  Material = -> Material010
  MoveBase = false
  MoveWithHost = false
  PerimeterLength = 0
  VerticalArea = 0
FEATURE [Part::Part2DObjectPython] Line1592  # Draft 2D object (typed FeaturePython)
  Area = 0
  ChamferSize = 0
  Closed = true
  End = (8945,1979.8,6981)
  FilletRadius = 0
  Length = 5000
  MakeFace = false
  Placement = pos=(8945,1979.8,6981) rot=(0,0,1;0rad)
  Points = (2) [(0,2.50111e-12,-5000),(0,2.50111e-12,0)]
  Start = (8945,1979.8,1981)
  Subdivisions = 0
FEATURE [Part::FeaturePython] Pipe007003  label="Дымоход 202"  # Arch/BIM 98 (typed FeaturePython)
  Base = -> Line1592
  Diameter = 300
  GlobalId = 11JHR0lR55LRzzbgV05jpw
  HorizontalArea = 0
  IfcData = IfcUID=11JHR0lR55LRzzbgV05jpw,+2 more (map truncated)
  IfcType = 98
  Length = 5000
  Material = -> Material010
  MoveBase = false
  MoveWithHost = false
  OffsetEnd = 0
  OffsetStart = 0
  PerimeterLength = 0
  PredefinedType = 0
  VerticalArea = 0
  WallThickness = 0
FEATURE [Part::FeaturePython] Component085  label="Дымоход 300 002"  # Arch/BIM 52 (typed FeaturePython)
  Base = -> Pipe007003
  GlobalId = 1RYiQBgpbBTAR3hS4pyNB_
  HorizontalArea = 0
  IfcData = IfcUID=1RYiQBgpbBTAR3hS4pyNB_,+2 more (map truncated)
  IfcType = 52
  Material = -> Material010
  MoveBase = false
  MoveWithHost = false
  PerimeterLength = 0
  VerticalArea = 0
FEATURE [App::GeometryPython] BuildingPart087  label="Инженерные системы"  # Arch/BIM 52 (typed FeaturePython)
  Area = 0
  GlobalId = 0dgo77$PP7IAddqr4C3YZS
  Group = -> [Component004,Component011,Component009,Component008,Component005,Component010,Component007,Component013,Component014,Component015,Component016,Component017,Component018,Component084,Component085]
  Height = 0
  HeightPropagate = true
  IfcData = IfcUID=0dgo77$PP7IAddqr4C3YZS,+2 more (map truncated)
  IfcType = 52
  LevelOffset = 0
FEATURE [Part::FeaturePython] Component086  label="Вычет стены 001"  # Arch/BIM 0 (typed FeaturePython)
  Base = -> Wall004
  HorizontalArea = 0
  IfcData = attributes={"GlobalId": {"name": "GlobalId", "type": "IfcGloballyUniqueId", "is_enum": false, "enum_values": []}, "Description": {"... (+538 chars omitted),+1 more (map truncated)
  IfcType = 0
  MoveBase = false
  MoveWithHost = false
  PerimeterLength = 0
  Placement = pos=(0,0,-200) rot=(0,0,1;0rad)
  PredefinedType = 0
  VerticalArea = 0
FEATURE [Part::FeaturePython] Structure  label="Утепление пола XPS 100mm"  # Arch/BIM 118 (typed FeaturePython)
  Additions = -> [Structure066,Structure069]
  Base = -> Rectangle016
  FaceMaker = 0
  GlobalId = 12HaZCeTXDOvnd1ysX9j$x
  Height = 100
  HorizontalArea = 0
  IfcData = IfcUID=12HaZCeTXDOvnd1ysX9j$x,+2 more (map truncated)
  IfcType = 118
  Length = 7520
  Material = -> Material002
  MoveBase = false
  MoveWithHost = false
  Nodes = (4) [(-50,-45,0),(12570,-45,0),(12570,7505,0),(-50,7505,0)]
  NodesOffset = 0
  Normal = (0,0,0)
  PerimeterLength = 0
  Placement = pos=(0,0,-200) rot=(0,0,1;0rad)
  PredefinedType = 0
  Subtractions = -> [Component086]
  VerticalArea = 0
  Width = 12620
FEATURE [App::GeometryPython] BuildingPart020  label="Утепление пола по грунту"  # Arch/BIM 52 (typed FeaturePython)
  Area = 0
  GlobalId = 3yH_rZ_TXC4Rf1NqFztroU
  Group = -> [Structure]
  Height = 0
  HeightPropagate = true
  IfcData = IfcUID=3yH_rZ_TXC4Rf1NqFztroU,attributes={"GlobalId": {"value": "3yH_rZ_TXC4Rf1NqFztroU"}},+1 more (map truncated)
  IfcType = 52
  LevelOffset = 0
FEATURE [App::MaterialObjectPython] Material018  label="Concrete (not transparent)"  # material (typed FeaturePython)
  Description = A standard C-25 construction concrete
  Material = AuthorAndLicense=Concrete-Generic,CardName=Concrete-Generic,Color=(0.47058823529411764, 0.4627450980392157, 0.4627450980392157, 1.0),+13 more (map truncated)
  ProductURL = https://en.wikipedia.org/wiki/Concrete
  StandardCode = Masterformat 03 33 13
  Transparency = 0
FEATURE [Part::FeaturePython] Structure399  label="Забежные низ 001"  # Arch/BIM 52 (typed FeaturePython)
  Base = -> Wire857
  FaceMaker = 0
  GlobalId = 3xRowyKFv2DhSfk5E$qgY5
  Height = 1064
  HorizontalArea = 231189
  IfcData = IfcUID=3xRowyKFv2DhSfk5E$qgY5,+2 more (map truncated)
  IfcType = 52
  Length = 0
  Material = -> Material018
  MoveBase = false
  MoveWithHost = false
  Nodes = (2) [(7357.33,6427.5,0),(7357.33,6427.5,1064)]
  NodesOffset = 0
  Normal = (0,0,1)
  PerimeterLength = 2353.16
  VerticalArea = 2.50376e+06
  Width = 100
FEATURE [Part::FeaturePython] Structure400  label="Забежные низ 013"  # Arch/BIM 52 (typed FeaturePython)
  Base = -> Wire858
  FaceMaker = 0
  GlobalId = 3$gmb_2qX9N8uPM2$7_dmQ
  Height = 880
  HorizontalArea = 253761
  IfcData = IfcUID=3$gmb_2qX9N8uPM2$7_dmQ,+2 more (map truncated)
  IfcType = 52
  Length = 0
  Material = -> Material018
  MoveBase = false
  MoveWithHost = false
  Nodes = (2) [(7272.39,6739.05,0),(7272.39,6739.05,880)]
  NodesOffset = 0
  Normal = (0,0,1)
  PerimeterLength = 2580.03
  VerticalArea = 2.27043e+06
  Width = 100
FEATURE [Part::FeaturePython] Structure401  label="Забежные низ 014"  # Arch/BIM 52 (typed FeaturePython)
  Base = -> Wire859
  FaceMaker = 0
  GlobalId = 01ecilRVH53xz1ioP6bHrT
  Height = 696
  HorizontalArea = 353236
  IfcData = IfcUID=01ecilRVH53xz1ioP6bHrT,+2 more (map truncated)
  IfcType = 52
  Length = 0
  Material = -> Material018
  MoveBase = false
  MoveWithHost = false
  Nodes = (2) [(7327.45,7090.2,0),(7327.45,7090.2,696)]
  NodesOffset = 0
  Normal = (0,0,1)
  PerimeterLength = 2946.66
  VerticalArea = 2.05087e+06
  Width = 100
FEATURE [Part::FeaturePython] Structure402  label="Забежные низ 015"  # Arch/BIM 52 (typed FeaturePython)
  Base = -> Wire860
  FaceMaker = 0
  GlobalId = 2Qxt6SlRz2T8lyMYD6o2tP
  Height = 512
  HorizontalArea = 250464
  IfcData = IfcUID=2Qxt6SlRz2T8lyMYD6o2tP,+2 more (map truncated)
  IfcType = 52
  Length = 0
  Material = -> Material018
  MoveBase = false
  MoveWithHost = false
  Nodes = (2) [(7668.63,7155.73,0),(7668.63,7155.73,512)]
  NodesOffset = 0
  Normal = (0,0,1)
  PerimeterLength = 2554.3
  VerticalArea = 1.3078e+06
  Width = 100
FEATURE [Part::FeaturePython] Structure403  label="Забежные низ 016"  # Arch/BIM 52 (typed FeaturePython)
  Base = -> Wire861
  FaceMaker = 0
  GlobalId = 22WKr65a12qwGJ$_8YzaFf
  Height = 328
  HorizontalArea = 225207
  IfcData = IfcUID=22WKr65a12qwGJ$_8YzaFf,+2 more (map truncated)
  IfcType = 52
  Length = 0
  Material = -> Material018
  MoveBase = false
  MoveWithHost = false
  Nodes = (2) [(7978.17,7076.01,0),(7978.17,7076.01,328)]
  NodesOffset = 0
  Normal = (0,0,1)
  PerimeterLength = 2310.8
  VerticalArea = 757942
  Width = 100
FEATURE [Part::FeaturePython] Structure404  label="Забежные низ 017"  # Arch/BIM 52 (typed FeaturePython)
  Base = -> Rectangle3338
  FaceMaker = 0
  GlobalId = 1VsCdZ7iTEn9tPuMJaDspx
  Height = 144
  HorizontalArea = 225000
  IfcData = IfcUID=1VsCdZ7iTEn9tPuMJaDspx,+2 more (map truncated)
  IfcType = 52
  Length = 0
  Material = -> Material018
  MoveBase = false
  MoveWithHost = false
  Nodes = (2) [(8231.4,7035,0),(8231.4,7035,144)]
  NodesOffset = 0
  Normal = (0,0,0)
  PerimeterLength = 2300
  VerticalArea = 331200
  Width = 100
FEATURE [Part::FeaturePython] Structure405  label="Структура015"  # Arch/BIM 52 (typed FeaturePython)
  Base = -> Wire862
  FaceMaker = 0
  GlobalId = 17tEtNUWvARhORHH3OyyHE
  Height = 40
  HorizontalArea = 249797
  IfcData = IfcUID=17tEtNUWvARhORHH3OyyHE,+2 more (map truncated)
  IfcType = 52
  Length = 0
  Material = -> Material018
  MoveBase = false
  MoveWithHost = false
  Nodes = (2) [(7360.51,6437.37,0),(7360.51,6437.37,-40)]
  NodesOffset = 0
  Normal = (0,0,0)
  PerimeterLength = 2393.6
  Placement = pos=(0,0,1104) rot=(0,0,1;0rad)
  VerticalArea = 95744
  Width = 100
FEATURE [Part::FeaturePython] Structure406  label="Структура016"  # Arch/BIM 52 (typed FeaturePython)
  Base = -> Wire863
  FaceMaker = 0
  GlobalId = 0bs21bqPT2gQetmdzIKKcU
  Height = 40
  HorizontalArea = 275711
  IfcData = IfcUID=0bs21bqPT2gQetmdzIKKcU,+2 more (map truncated)
  IfcType = 52
  Length = 0
  Material = -> Material018
  MoveBase = false
  MoveWithHost = false
  Nodes = (2) [(7275.7,6726.62,0),(7275.7,6726.62,-40)]
  NodesOffset = 0
  Normal = (0,0,0)
  PerimeterLength = 2627.74
  Placement = pos=(0,0,920) rot=(0,0,1;0rad)
  VerticalArea = 105109
  Width = 100
FEATURE [Part::FeaturePython] Structure407  label="Структура017"  # Arch/BIM 52 (typed FeaturePython)
  Base = -> Wire864
  FaceMaker = 0
  GlobalId = 2j64CQRQHAcRK4sU5nK_W7
  Height = 40
  HorizontalArea = 374881
  IfcData = IfcUID=2j64CQRQHAcRK4sU5nK_W7,+2 more (map truncated)
  IfcType = 52
  Length = 0
  Material = -> Material018
  MoveBase = false
  MoveWithHost = false
  Nodes = (2) [(7342.75,7086.8,0),(7342.75,7086.8,-40)]
  NodesOffset = 0
  Normal = (0,0,0)
  PerimeterLength = 2973.7
  Placement = pos=(0,0,736) rot=(0,0,1;0rad)
  VerticalArea = 118948
  Width = 100
FEATURE [Part::FeaturePython] Structure408  label="Структура018"  # Arch/BIM 52 (typed FeaturePython)
  Base = -> Wire865
  FaceMaker = 0
  GlobalId = 1QIDzeYIT3m8mUX9Kkwym4
  Height = 40
  HorizontalArea = 268670
  IfcData = IfcUID=1QIDzeYIT3m8mUX9Kkwym4,+2 more (map truncated)
  IfcType = 52
  Length = 0
  Material = -> Material018
  MoveBase = false
  MoveWithHost = false
  Nodes = (2) [(7682.02,7147.55,0),(7682.02,7147.55,-40)]
  NodesOffset = 0
  Normal = (0,0,0)
  PerimeterLength = 2594.76
  Placement = pos=(0,0,552) rot=(0,0,1;0rad)
  VerticalArea = 103790
  Width = 100
FEATURE [Part::FeaturePython] Structure409  label="Структура019"  # Arch/BIM 52 (typed FeaturePython)
  Base = -> Wire866
  FaceMaker = 0
  GlobalId = 25WTBURZvCHuciqcaKOkV_
  Height = 40
  HorizontalArea = 243207
  IfcData = IfcUID=25WTBURZvCHuciqcaKOkV_,+2 more (map truncated)
  IfcType = 52
  Length = 0
  Material = -> Material018
  MoveBase = false
  MoveWithHost = false
  Nodes = (2) [(7988.39,7072.97,0),(7988.39,7072.97,-40)]
  NodesOffset = 0
  Normal = (0,0,0)
  PerimeterLength = 2350.8
  Placement = pos=(0,0,369) rot=(0,0,1;0rad)
  VerticalArea = 94032
  Width = 100
FEATURE [Part::FeaturePython] Structure410  label="Структура020"  # Arch/BIM 52 (typed FeaturePython)
  Base = -> Rectangle3340
  FaceMaker = 0
  GlobalId = 3fuuXTC0L9FOhhGPsIqq2n
  Height = 40
  HorizontalArea = 243000
  IfcData = IfcUID=3fuuXTC0L9FOhhGPsIqq2n,+2 more (map truncated)
  IfcType = 52
  Length = 0
  Material = -> Material018
  MoveBase = false
  MoveWithHost = false
  Nodes = (2) [(8241.39,7035,0),(8241.39,7035,-40)]
  NodesOffset = 0
  Normal = (0,0,-1)
  PerimeterLength = 2340
  Placement = pos=(0,0,184) rot=(0,0,1;0rad)
  VerticalArea = 93600
  Width = 100
FEATURE [App::GeometryPython] BuildingPart095  label="Забежные верх"  # Arch/BIM 52 (typed FeaturePython)
  Area = 0
  GlobalId = 1ZYgrdkID2NPN3ZGn3KHqO
  Group = -> [Structure405,Structure406,Structure407,Structure408,Structure409,Structure410]
  Height = 0
  HeightPropagate = true
  IfcData = IfcUID=1ZYgrdkID2NPN3ZGn3KHqO,+2 more (map truncated)
  IfcType = 52
  LevelOffset = 0
FEATURE [Part::FeaturePython] Structure411  label="Забежные низ 018"  # Arch/BIM 52 (typed FeaturePython)
  Base = -> Rectangle3341
  FaceMaker = 0
  GlobalId = 23ZLurxYD1YfxSwC6KIQzz
  Height = 1104
  HorizontalArea = 174521
  IfcData = IfcUID=23ZLurxYD1YfxSwC6KIQzz,+2 more (map truncated)
  IfcType = 52
  Length = 0
  Material = -> Material018
  MoveBase = false
  MoveWithHost = false
  Nodes = (2) [(8211.39,7020,0),(8211.39,7020,143.5)]
  NodesOffset = 0
  Normal = (0,0,0)
  PerimeterLength = 2219.39
  VerticalArea = 2.45021e+06
  Width = 100
FEATURE [App::GeometryPython] BuildingPart094  label="Забежные низ"  # Arch/BIM 52 (typed FeaturePython)
  Area = 0
  GlobalId = 1IKz8gq_D40uVuKk2CcJxb
  Group = -> [Structure399,Structure400,Structure401,Structure402,Structure403,Structure404,Structure411]
  Height = 0
  HeightPropagate = true
  IfcData = IfcUID=1IKz8gq_D40uVuKk2CcJxb,+2 more (map truncated)
  IfcType = 52
  LevelOffset = 0
FEATURE [App::GeometryPython] BuildingPart093  label="Лестница 184/250 17 подъёмов обновл."  # Arch/BIM 52 (typed FeaturePython)
  Area = 0
  GlobalId = 1mPKq_o39C3gXvH55GxGJR
  Group = -> [Stairs003,BuildingPart094,BuildingPart095]
  Height = 0
  HeightPropagate = true
  IfcData = IfcUID=1mPKq_o39C3gXvH55GxGJR,+2 more (map truncated)
  IfcType = 52
  LevelOffset = 0
FEATURE [Part::FeaturePython] Component063  label="ПНО-39-001"  # Arch/BIM 52 (typed FeaturePython)
  Base = -> Array060
  GlobalId = 3XdGCKpWL71eu_U9riFilZ
  HorizontalArea = 0
  IfcData = IfcUID=3XdGCKpWL71eu_U9riFilZ,+2 more (map truncated)
  IfcType = 52
  Material = -> Material018
  MoveBase = false
  MoveWithHost = false
  PerimeterLength = 0
  Placement = pos=(960,0,0) rot=(0,0,1;0rad)
  VerticalArea = 0
FEATURE [Part::FeaturePython] Component064  label="ПНО-39-022"  # Arch/BIM 52 (typed FeaturePython)
  Base = -> Array059
  GlobalId = 0bmcIJyB97$9xeF$u53D6V
  HorizontalArea = 0
  IfcData = IfcUID=0bmcIJyB97$9xeF$u53D6V,+2 more (map truncated)
  IfcType = 52
  Material = -> Material018
  MoveBase = false
  MoveWithHost = false
  PerimeterLength = 0
  Placement = pos=(10150,1.364e-12,0) rot=(0,0,1;0rad)
  VerticalArea = 0
FEATURE [Part::FeaturePython] Component065  label="ПНО-39-023"  # Arch/BIM 52 (typed FeaturePython)
  Base = -> Array058
  GlobalId = 3J7wnUa6v2rfQwTZ0ixKlx
  HorizontalArea = 0
  IfcData = IfcUID=3J7wnUa6v2rfQwTZ0ixKlx,+2 more (map truncated)
  IfcType = 52
  Material = -> Material018
  MoveBase = false
  MoveWithHost = false
  PerimeterLength = 0
  Placement = pos=(-50,0,0) rot=(0,0,1;0rad)
  VerticalArea = 0
FEATURE [Part::FeaturePython] Component066  label="ПНО-39-024"  # Arch/BIM 52 (typed FeaturePython)
  Base = -> Array061
  GlobalId = 04BNWqgZL2Ov5OlXQ9URhu
  HorizontalArea = 0
  IfcData = IfcUID=04BNWqgZL2Ov5OlXQ9URhu,+2 more (map truncated)
  IfcType = 52
  Material = -> Material018
  MoveBase = false
  MoveWithHost = false
  PerimeterLength = 0
  Placement = pos=(6710,4.54e-13,0) rot=(0,0,1;0rad)
  VerticalArea = 0
FEATURE [Part::FeaturePython] Component067  label="ПНО-39-025"  # Arch/BIM 52 (typed FeaturePython)
  Base = -> Cut040
  GlobalId = 3oxNR3o2f3ThkHi0MWyoUk
  HorizontalArea = 0
  IfcData = IfcUID=3oxNR3o2f3ThkHi0MWyoUk,+2 more (map truncated)
  IfcType = 52
  Material = -> Material018
  MoveBase = false
  MoveWithHost = false
  PerimeterLength = 0
  VerticalArea = 0
FEATURE [Part::FeaturePython] Component068  label="ПНО-39-026"  # Arch/BIM 52 (typed FeaturePython)
  Base = -> Cut041
  GlobalId = 248Twkwhj2Cw3m_5Ovog43
  HorizontalArea = 0
  IfcData = IfcUID=248Twkwhj2Cw3m_5Ovog43,+2 more (map truncated)
  IfcType = 52
  Material = -> Material018
  MoveBase = false
  MoveWithHost = false
  PerimeterLength = 0
  VerticalArea = 0
FEATURE [Part::FeaturePython] Component069  label="ПНО-39-027"  # Arch/BIM 52 (typed FeaturePython)
  Base = -> Cut048
  GlobalId = 1Khcr$NwzCrA2G11iVvVb8
  HorizontalArea = 0
  IfcData = IfcUID=1Khcr$NwzCrA2G11iVvVb8,+2 more (map truncated)
  IfcType = 52
  Material = -> Material018
  MoveBase = false
  MoveWithHost = false
  PerimeterLength = 0
  VerticalArea = 0
FEATURE [Part::FeaturePython] Component070  label="ПНО-39-028"  # Arch/BIM 52 (typed FeaturePython)
  Base = -> Cut049
  GlobalId = 0yPrT9kDj0g9Se6444B6w3
  HorizontalArea = 0
  IfcData = IfcUID=0yPrT9kDj0g9Se6444B6w3,+2 more (map truncated)
  IfcType = 52
  Material = -> Material018
  MoveBase = false
  MoveWithHost = false
  PerimeterLength = 0
  VerticalArea = 0
FEATURE [App::GeometryPython] BuildingPart080  label="Перекрытие 2-4"  # Arch/BIM 52 (typed FeaturePython)
  Area = 0
  GlobalId = 0anh3cmIz34vhOpNdTvs5l
  Group = -> [Component063,Component064,Component065,Component066,Component067,Component068,Component069,Component070]
  Height = 0
  HeightPropagate = true
  IfcData = IfcUID=0anh3cmIz34vhOpNdTvs5l,+2 more (map truncated)
  IfcType = 52
  LevelOffset = 0
FEATURE [Part::FeaturePython] Component071  label="ПНО-40-001"  # Arch/BIM 52 (typed FeaturePython)
  Base = -> Array054
  GlobalId = 0wpf9Q8IzA_f4m02htJFBb
  HorizontalArea = 0
  IfcData = IfcUID=0wpf9Q8IzA_f4m02htJFBb,+2 more (map truncated)
  IfcType = 52
  Material = -> Material018
  MoveBase = false
  MoveWithHost = false
  PerimeterLength = 0
  Placement = pos=(-50,-9.09e-13,0) rot=(0,0,1;0rad)
  VerticalArea = 0
FEATURE [Part::FeaturePython] Component072  label="ПНО-40-010"  # Arch/BIM 52 (typed FeaturePython)
  Base = -> Array038
  GlobalId = 0oBCy39Wb7fhN7XKOpfxSu
  HorizontalArea = 0
  IfcData = IfcUID=0oBCy39Wb7fhN7XKOpfxSu,+2 more (map truncated)
  IfcType = 52
  Material = -> Material018
  MoveBase = false
  MoveWithHost = false
  PerimeterLength = 0
  Placement = pos=(7920,9.09e-13,0) rot=(0,0,1;0rad)
  VerticalArea = 0
FEATURE [Part::FeaturePython] Component073  label="ПНО-40-011"  # Arch/BIM 52 (typed FeaturePython)
  Base = -> Array056
  GlobalId = 28AQdtbYrBIx61Ll5jYMHO
  HorizontalArea = 0
  IfcData = IfcUID=28AQdtbYrBIx61Ll5jYMHO,+2 more (map truncated)
  IfcType = 52
  Material = -> Material018
  MoveBase = false
  MoveWithHost = false
  PerimeterLength = 0
  Placement = pos=(11560,9.09e-13,0) rot=(0,0,1;0rad)
  VerticalArea = 0
FEATURE [Part::FeaturePython] Component074  label="ПНО-40-012"  # Arch/BIM 52 (typed FeaturePython)
  Base = -> Array057
  GlobalId = 0ZSNQygeL5b9x0j4AY$sC6
  HorizontalArea = 0
  IfcData = IfcUID=0ZSNQygeL5b9x0j4AY$sC6,+2 more (map truncated)
  IfcType = 52
  Material = -> Material018
  MoveBase = false
  MoveWithHost = false
  PerimeterLength = 0
  Placement = pos=(4480,9.09e-13,0) rot=(0,0,1;0rad)
  VerticalArea = 0
FEATURE [App::GeometryPython] BuildingPart074  label="Перекрытие 1-2"  # Arch/BIM 52 (typed FeaturePython)
  Area = 0
  GlobalId = 2Lvd2Pu4D2h9CzOOmQVni3
  Group = -> [Component074,Component073,Component071,Component072]
  Height = 0
  HeightPropagate = true
  IfcData = IfcUID=2Lvd2Pu4D2h9CzOOmQVni3,+2 more (map truncated)
  IfcType = 52
  LevelOffset = 0
FEATURE [App::GeometryPython] BuildingPart006  label="Перекрытие плитами ПНО"  # Arch/BIM 52 (typed FeaturePython)
  Area = 0
  GlobalId = 29arHl4sD0PxQq1DVpDEyo
  Group = -> [BuildingPart074,BuildingPart080]
  Height = 0
  HeightPropagate = true
  IfcData = IfcUID=29arHl4sD0PxQq1DVpDEyo,attributes={"GlobalId": {"value": "29arHl4sD0PxQq1DVpDEyo"}},+1 more (map truncated)
  IfcType = 52
  LevelOffset = 0
FEATURE [Part::FeaturePython] Structure434  label="Стяжка тёплого пола 80mm"  # Arch/BIM 118 (typed FeaturePython)
  Additions = -> [Structure368,Structure371]
  Base = -> Rectangle016
  FaceMaker = 0
  GlobalId = 3i06NLwF5739lSL_IHGmf1
  Height = 80
  HorizontalArea = 0
  IfcData = IfcUID=3i06NLwF5739lSL_IHGmf1,+2 more (map truncated)
  IfcType = 118
  Length = 7520
  Material = -> Material018
  MoveBase = false
  MoveWithHost = false
  Nodes = (4) [(-50,-45,0),(12570,-45,0),(12570,7505,0),(-50,7505,0)]
  NodesOffset = 0
  Normal = (0,0,0)
  PerimeterLength = 0
  Placement = pos=(0,0,-100) rot=(0,0,1;0rad)
  PredefinedType = 0
  Subtractions = -> [Component086]
  VerticalArea = 0
  Width = 12620
FEATURE [App::GeometryPython] BuildingPart085  label="Стяжка тёплого пола 80мм"  # Arch/BIM 52 (typed FeaturePython)
  Area = 0
  GlobalId = 0paGEjjH988O$uNBI5I7u1
  Group = -> [Structure434]
  Height = 0
  HeightPropagate = true
  IfcData = IfcUID=0paGEjjH988O$uNBI5I7u1,+2 more (map truncated)
  IfcType = 52
  LevelOffset = 0
FEATURE [Part::FeaturePython] Structure435  label="Покрытие пола 20мм001"  # Arch/BIM 118 (typed FeaturePython)
  Additions = -> [Structure374,Structure377]
  Base = -> Rectangle016
  FaceMaker = 0
  GlobalId = 069jleHXv70OyIjGnnOFdt
  Height = 20
  HorizontalArea = 0
  IfcData = IfcUID=069jleHXv70OyIjGnnOFdt,+2 more (map truncated)
  IfcType = 118
  Length = 7520
  Material = -> Material018
  MoveBase = false
  MoveWithHost = false
  Nodes = (4) [(-50,-45,0),(12570,-45,0),(12570,7505,0),(-50,7505,0)]
  NodesOffset = 0
  Normal = (0,0,0)
  PerimeterLength = 0
  Placement = pos=(0,0,-20) rot=(0,0,1;0rad)
  PredefinedType = 0
  Subtractions = -> [Component086]
  VerticalArea = 0
  Width = 12620
FEATURE [App::GeometryPython] BuildingPart086  label="Покрытие пола 20мм"  # Arch/BIM 52 (typed FeaturePython)
  Area = 0
  GlobalId = 1v2dx_MFP8whu6FdM2ihDU
  Group = -> [Structure435]
  Height = 0
  HeightPropagate = true
  IfcData = IfcUID=1v2dx_MFP8whu6FdM2ihDU,+2 more (map truncated)
  IfcType = 52
  LevelOffset = 0
FEATURE [App::GeometryPython] BuildingPart014  label="Полы по грунту"  # Arch/BIM 52 (typed FeaturePython)
  Area = 0
  GlobalId = 1N3QY958b6OO8VUwpY7Wbc
  Group = -> [BuildingPart020,BuildingPart085,BuildingPart086]
  Height = 0
  HeightPropagate = true
  IfcData = IfcUID=1N3QY958b6OO8VUwpY7Wbc,attributes={"GlobalId": {"value": "1N3QY958b6OO8VUwpY7Wbc"}},+1 more (map truncated)
  IfcType = 52
  LevelOffset = 0
FEATURE [App::FeaturePython] Dimension032  # Draft dimension (typed FeaturePython)
  Diameter = false
  Dimline = (3700,2600,0)
  Direction = (0,0,0)
  Distance = 900
  End = (3500,3435,0)
  Normal = (0,0,1)
  Start = (3500,2535,0)
FEATURE [App::FeaturePython] Dimension034  # Draft dimension (typed FeaturePython)
  Diameter = false
  Dimline = (4770,3300,0)
  Direction = (0,0,0)
  Distance = 920
  End = (4770,3825,0)
  Normal = (0,0,1)
  Start = (3850,3825,0)
FEATURE [App::FeaturePython] Dimension035  # Draft dimension (typed FeaturePython)
  Diameter = false
  Dimline = (5800,3300,0)
  Direction = (0,0,0)
  Distance = 920
  End = (6720,3825,0)
  Normal = (0,0,1)
  Start = (5800,3825,0)
FEATURE [App::FeaturePython] Dimension036  # Draft dimension (typed FeaturePython)
  Diameter = false
  Dimline = (5800,2600,0)
  Direction = (0,0,0)
  Distance = 900
  End = (6710,2385,0)
  Normal = (0,0,1)
  Start = (5810,2385,0)
FEATURE [App::FeaturePython] Dimension037  # Draft dimension (typed FeaturePython)
  Diameter = false
  Dimline = (7200,4426.21,0)
  Direction = (0,0,0)
  Distance = 900
  End = (6950,4725,0)
  Normal = (0,0,1)
  Start = (6950,3825,0)
FEATURE [App::FeaturePython] Dimension038  # Draft dimension (typed FeaturePython)
  Diameter = false
  Dimline = (5670,-235,0)
  Direction = (0,0,0)
  Distance = 1050
  End = (6720,-25,0)
  Normal = (0,0,1)
  Start = (5670,-25,0)
FEATURE [App::FeaturePython] Dimension039  # Draft dimension (typed FeaturePython)
  Diameter = false
  Dimline = (4835,-235,0)
  Direction = (0,0,0)
  Distance = 660
  End = (4835,-25,0)
  Normal = (0,0,1)
  Start = (4175,-25,0)
FEATURE [App::FeaturePython] Dimension040  # Draft dimension (typed FeaturePython)
  Diameter = false
  Dimline = (7555,-235,0)
  Direction = (0,0,0)
  Distance = 660
  End = (8215,-25,0)
  Normal = (0,0,1)
  Start = (7555,-25,0)
FEATURE [App::FeaturePython] Dimension041  # Draft dimension (typed FeaturePython)
  Diameter = false
  Dimline = (-240,1840,0)
  Direction = (0,0,0)
  Distance = 1440
  End = (-30,3280,0)
  Normal = (0,0,1)
  Start = (-30,1840,0)
FEATURE [App::FeaturePython] Dimension042  # Draft dimension (typed FeaturePython)
  Diameter = false
  Dimline = (12760,1320,0)
  Direction = (0,0,0)
  Distance = 1960
  End = (12550,3280,0)
  Normal = (0,0,1)
  Start = (12550,1320,0)
FEATURE [App::FeaturePython] Dimension043  # Draft dimension (typed FeaturePython)
  Diameter = false
  Dimline = (12760,4000,0)
  Direction = (0,0,0)
  Distance = 920
  End = (12550,4970,0)
  Normal = (0,0,1)
  Start = (12550,4050,0)
FEATURE [App::FeaturePython] Dimension044  # Draft dimension (typed FeaturePython)
  Diameter = false
  Dimline = (8595,7695,0)
  Direction = (0,0,0)
  Distance = 1960
  End = (10555,7485,0)
  Normal = (0,0,1)
  Start = (8595,7485,0)
FEATURE [App::FeaturePython] Dimension045  # Draft dimension (typed FeaturePython)
  Diameter = false
  Dimline = (6005,7695,0)
  Direction = (0,0,0)
  Distance = 920
  End = (6005,7485,0)
  Normal = (0,0,1)
  Start = (5085,7485,0)
FEATURE [App::FeaturePython] Dimension046  # Draft dimension (typed FeaturePython)
  Diameter = false
  Dimline = (3925,7695,0)
  Direction = (0,0,0)
  Distance = 1960
  End = (3925,7485,0)
  Normal = (0,0,1)
  Start = (1965,7485,0)
FEATURE [App::FeaturePython] Dimension047  # Draft dimension (typed FeaturePython)
  Diameter = false
  Dimline = (5690,200,0)
  Direction = (0,0,0)
  Distance = 3250
  End = (7350,-25,0)
  Normal = (0,0,1)
  Start = (4100,-25,0)
FEATURE [App::FeaturePython] Dimension048  # Draft dimension (typed FeaturePython)
  Diameter = false
  Dimline = (5200,1052.26,0)
  Direction = (0,0,0)
  Distance = 2310
  End = (7300,2285,0)
  Normal = (0,0,1)
  Start = (7300,-25,0)
FEATURE [App::FeaturePython] Dimension049  # Draft dimension (typed FeaturePython)
  Diameter = false
  Dimline = (3200,1600,0)
  Direction = (0,0,0)
  Distance = 3560
  End = (-30,3535,0)
  Normal = (0,0,1)
  Start = (-30,-25,0)
FEATURE [App::FeaturePython] Dimension050  # Draft dimension (typed FeaturePython)
  Diameter = false
  Dimline = (2900,1200,0)
  Direction = (0,0,0)
  Distance = 4030
  End = (4000,-25,0)
  Normal = (0,0,1)
  Start = (-30,-25,0)
FEATURE [App::FeaturePython] Dimension052  # Draft dimension (typed FeaturePython)
  Diameter = false
  Dimline = (11900,1600,0)
  Direction = (0,0,0)
  Distance = 3560
  End = (12550,3535,0)
  Normal = (0,0,1)
  Start = (12550,-25,0)
FEATURE [App::FeaturePython] Dimension053  # Draft dimension (typed FeaturePython)
  Diameter = false
  Dimline = (3700,8200,0)
  Direction = (0,0,0)
  Distance = 1830
  End = (3860,8015,0)
  Normal = (0,0,1)
  Start = (2030,8015,0)
FEATURE [App::FeaturePython] Dimension054  # Draft dimension (typed FeaturePython)
  Diameter = false
  Dimline = (2500,4300,0)
  Direction = (0,0,0)
  Distance = 4850
  End = (4820,7485,0)
  Normal = (0,0,1)
  Start = (-30,7485,0)
FEATURE [App::FeaturePython] Dimension055  # Draft dimension (typed FeaturePython)
  Diameter = false
  Dimline = (8800,6200,0)
  Direction = (0,0,0)
  Distance = 4590
  End = (12550,3825,0)
  Normal = (0,0,1)
  Start = (7960,3825,0)
FEATURE [App::FeaturePython] Dimension056  # Draft dimension (typed FeaturePython)
  Diameter = false
  Dimline = (10943.1,642.693,0)
  Direction = (0,0,0)
  Distance = 3000
  End = (12550,-25,0)
  Normal = (0,0,1)
  Start = (9550,-25,0)
FEATURE [App::FeaturePython] Dimension057  # Draft dimension (typed FeaturePython)
  Diameter = false
  Dimline = (800,4600,0)
  Direction = (0,0,0)
  Distance = 3660
  End = (-30,7485,0)
  Normal = (0,0,1)
  Start = (-30,3825,0)
FEATURE [App::FeaturePython] Dimension058  # Draft dimension (typed FeaturePython)
  Diameter = false
  Dimline = (10700,200,0)
  Direction = (0,0,0)
  Distance = 2000
  End = (9450,-25,0)
  Normal = (0,0,1)
  Start = (7450,-25,0)
FEATURE [App::FeaturePython] Dimension059  # Draft dimension (typed FeaturePython)
  Diameter = false
  Dimline = (12100,4500,0)
  Direction = (0,0,0)
  Distance = 3660
  End = (12550,7485,0)
  Normal = (0,0,1)
  Start = (12550,3825,0)
FEATURE [App::FeaturePython] Dimension060  # Draft dimension (typed FeaturePython)
  Diameter = false
  Dimline = (8800,3300,0)
  Direction = (0,0,0)
  Distance = 3520
  End = (11920,3680,0)
  Normal = (0,0,1)
  Start = (8400,3680,0)
FEATURE [App::FeaturePython] Dimension061  # Draft dimension (typed FeaturePython)
  Diameter = false
  Dimline = (11920,3300,0)
  Direction = (0,0,0)
  Distance = 650
  End = (12570,3665,0)
  Normal = (0,0,1)
  Start = (11920,3665,0)
FEATURE [App::FeaturePython] Dimension062  # Draft dimension (typed FeaturePython)
  Diameter = false
  Dimline = (6720,3300,0)
  Direction = (0,0,0)
  Distance = 1680
  End = (8400,3680,0)
  Normal = (0,0,1)
  Start = (6720,3680,0)
FEATURE [App::FeaturePython] Dimension063  # Draft dimension (typed FeaturePython)
  Diameter = false
  Dimline = (5800,3300,0)
  Direction = (0,0,0)
  Distance = 1030
  End = (5800,3680,0)
  Normal = (0,0,1)
  Start = (4770,3680,0)
FEATURE [App::FeaturePython] Dimension064  # Draft dimension (typed FeaturePython)
  Diameter = false
  Dimline = (3850,4000,0)
  Direction = (0,0,0)
  Distance = 3900
  End = (3850,3680,0)
  Normal = (0,0,1)
  Start = (-50,3680,0)
FEATURE [TechDraw::DrawViewAnnotation] Annotation009  label="a_077"
  Font = osifont
  LineSpace = 80
  LockPosition = true
  MaxWidth = -1
  Rotation = 0
  ScaleType = 0
  Text = \u0410\u0440\u043c\u043f\u043e\u044f\u0441 180x140mm
  TextSize = 4
  TextStyle = 0
  X = 256.728
  Y = 224.794
FEATURE [TechDraw::DrawViewAnnotation] Annotation010  label="a_078"
  Font = osifont
  LineSpace = 80
  LockPosition = true
  MaxWidth = -1
  Rotation = 0
  ScaleType = 0
  Text = XPS 80mm
  TextSize = 4
  TextStyle = 0
  X = 265.062
  Y = 229.944
FEATURE [TechDraw::DrawViewAnnotation] Annotation011  label="a_079"
  Font = osifont
  LineSpace = 80
  LockPosition = true
  MaxWidth = -1
  Rotation = 0
  ScaleType = 0
  Text = \u041a\u0438\u0440\u043f\u0438\u0447 2.1 \u043d\u0444
  TextSize = 4
  TextStyle = 0
  X = 260.909
  Y = 212.329
FEATURE [TechDraw::DrawViewAnnotation] Annotation012  label="a_080"
  Font = osifont
  LineSpace = 80
  LockPosition = true
  MaxWidth = -1
  Rotation = 0
  ScaleType = 0
  Text = \u041c\u0430\u0443\u044d\u0440\u043b\u0430\u0442 150\u0445150mm
  TextSize = 4
  TextStyle = 0
  X = 256.196
  Y = 218.755
FEATURE [TechDraw::DrawLeaderLine] LeaderLine
  AutoHorizontal = true
  EndSymbol = 7
  LeaderParent = -> Annotation010
  LockPosition = true
  Rotation = 0
  Scalable = false
  ScaleType = 0
  StartSymbol = 7
  WayPoints = (3) [(0,0,0),(9.82636,-670.069,0),(-263.143,-670.069,0)]
  X = 17.2239
  Y = -68.3719
FEATURE [TechDraw::DrawLeaderLine] LeaderLine001
  AutoHorizontal = true
  EndSymbol = 7
  LeaderParent = -> Annotation012
  LockPosition = true
  Rotation = 0
  Scalable = false
  ScaleType = 0
  StartSymbol = 7
  WayPoints = (3) [(0,0,0),(10.0885,-535.699,0),(-399.504,-535.699,0)]
  X = 22.6678
  Y = -54.1973
FEATURE [TechDraw::DrawLeaderLine] LeaderLine002
  AutoHorizontal = true
  EndSymbol = 7
  LeaderParent = -> Annotation009
  LockPosition = true
  Rotation = 0
  Scalable = false
  ScaleType = 0
  StartSymbol = 7
  WayPoints = (3) [(0,0,0),(10.0885,-626.495,0),(-400.513,-626.495,0)]
  X = 23.346
  Y = -63.2619
FEATURE [TechDraw::DrawLeaderLine] LeaderLine003
  AutoHorizontal = true
  EndSymbol = 7
  LeaderParent = -> Annotation011
  LockPosition = true
  Rotation = 0
  Scalable = false
  ScaleType = 0
  StartSymbol = 7
  WayPoints = (3) [(0,0,0),(11.2011,-497.917,0),(-281.712,-497.917,0)]
  X = 15.6278
  Y = -50.7269
FEATURE [TechDraw::DrawViewAnnotation] Annotation013  label="a_082"
  Font = osifont
  LineSpace = 80
  LockPosition = true
  MaxWidth = -1
  Rotation = 0
  ScaleType = 0
  Text = XPS 100mm
  TextSize = 4
  TextStyle = 0
  X = 118.3
  Y = 198.428
FEATURE [TechDraw::DrawViewAnnotation] Annotation014  label="a_083"
  Font = osifont
  LineSpace = 80
  LockPosition = true
  MaxWidth = -1
  Rotation = 0
  ScaleType = 0
  Text = \u041f\u043e\u043a\u0440\u044b\u0442\u0438\u0435 \u043f\u043e\u043b\u0430 20mm
  TextSize = 4
  TextStyle = 0
  X = 109.298
  Y = 208.784
FEATURE [TechDraw::DrawViewAnnotation] Annotation015  label="a_084"
  Font = osifont
  LineSpace = 80
  LockPosition = true
  MaxWidth = -1
  Rotation = 0
  ScaleType = 0
  Text = \u0421\u0442\u044f\u0436\u043a\u0430 \u043f\u043e\u043b\u0430 50mm
  TextSize = 4
  TextStyle = 0
  X = 111.999
  Y = 203.648
FEATURE [TechDraw::DrawViewAnnotation] Annotation016  label="a_076"
  Font = osifont
  LineSpace = 80
  LockPosition = true
  MaxWidth = -1
  Rotation = 0
  ScaleType = 0
  Text = \u041e\u0431\u043b\u0438\u0446\u043e\u0432\u043e\u0447\u043d\u044b\u0439 \u043a\u0438\u0440\u043f\u0438\u0447 1\u043d\u0444
  TextSize = 4
  TextStyle = 0
  X = 250.884
  Y = 234.906
FEATURE [TechDraw::DrawLeaderLine] LeaderLine004
  AutoHorizontal = true
  EndSymbol = 7
  LeaderParent = -> Annotation016
  LockPosition = true
  Rotation = 0
  Scalable = false
  ScaleType = 0
  StartSymbol = 7
  WayPoints = (3) [(0,0,0),(17.4485,-744.208,0),(-570.424,-744.208,0)]
  X = 33.3756
  Y = -74.7769
FEATURE [TechDraw::DrawViewAnnotation] Annotation017  label="a_001"
  Font = osifont
  LineSpace = 80
  LockPosition = true
  MaxWidth = -1
  Rotation = 0
  ScaleType = 0
  Text = XPS 100mm
  TextSize = 4
  TextStyle = 0
  X = 301.631
  Y = 118.628
FEATURE [TechDraw::DrawViewAnnotation] Annotation018  label="a_028"
  Font = osifont
  LineSpace = 80
  LockPosition = true
  MaxWidth = -1
  Rotation = 0
  ScaleType = 0
  Text = XPS 80mm
  TextSize = 4
  TextStyle = 0
  X = 313.482
  Y = 140.167
FEATURE [TechDraw::DrawViewAnnotation] Annotation019  label="a_029"
  Font = osifont
  LineSpace = 80
  LockPosition = true
  MaxWidth = -1
  Rotation = 0
  ScaleType = 0
  Text = \u041f\u0435\u0440\u0435\u043c\u044b\u0447\u043a\u0430 \u043c\u043e\u043d\u043e\u043b\u0438\u0442\u043d\u0430\u044f
  TextSize = 4
  TextStyle = 0
  X = 311.808
  Y = 112.937
FEATURE [TechDraw::DrawViewAnnotation] Annotation020  label="a_030"
  Font = osifont
  LineSpace = 80
  LockPosition = true
  MaxWidth = -1
  Rotation = 0
  ScaleType = 0
  Text = \u041a\u0430\u043c\u0435\u043d\u044c \u043e\u0431\u043b\u0438\u0446\u043e\u0432\u043e\u0447\u043d\u044b\u0439
  TextSize = 4
  TextStyle = 0
  X = 311.983
  Y = 123.571
FEATURE [TechDraw::DrawViewAnnotation] Annotation021  label="a_031"
  Font = osifont
  LineSpace = 80
  LockPosition = true
  MaxWidth = -1
  Rotation = 0
  ScaleType = 0
  Text = \u041a\u0438\u0440\u043f\u0438\u0447 1\u043d\u0444
  TextSize = 4
  TextStyle = 0
  X = 320.081
  Y = 135.139
FEATURE [TechDraw::DrawViewAnnotation] Annotation022  label="a_032"
  Font = osifont
  LineSpace = 80
  LockPosition = true
  MaxWidth = -1
  Rotation = 0
  ScaleType = 0
  Text = \u0411\u043b\u043e\u043a 380\u043c\u043c \u041b\u0421\u0420 10.7\u043d\u0444 "\u0422\u0451\u043f\u043b\u044b\u0439"
  TextSize = 4
  TextStyle = 0
  X = 68.8072
  Y = 136.929
FEATURE [TechDraw::DrawViewAnnotation] Annotation023  label="a_033"
  Font = osifont
  LineSpace = 80
  LockPosition = true
  MaxWidth = -1
  Rotation = 0
  ScaleType = 0
  Text = XPS 100mm
  TextSize = 4
  TextStyle = 0
  X = 97.5568
  Y = 118.043
FEATURE [TechDraw::DrawViewAnnotation] Annotation024  label="a_034"
  Font = osifont
  LineSpace = 80
  LockPosition = true
  MaxWidth = -1
  Rotation = 0
  ScaleType = 0
  Text = \u0421\u0442\u044f\u0436\u043a\u0430 \u0442\u0451\u043f\u043b\u043e\u0433\u043e \u043f\u043e\u043b\u0430 80mm
  TextSize = 4
  TextStyle = 0
  X = 83.3647
  Y = 122.395
FEATURE [TechDraw::DrawViewAnnotation] Annotation025  label="a_035"
  Font = osifont
  LineSpace = 80
  LockPosition = true
  MaxWidth = -1
  Rotation = 0
  ScaleType = 0
  Text = \u041f\u043e\u043a\u0440\u044b\u0442\u0438\u0435 \u043f\u043e\u043b\u0430 20mm
  TextSize = 4
  TextStyle = 0
  X = 88.1001
  Y = 127.174
FEATURE [TechDraw::DrawViewAnnotation] Annotation026  label="a_036"
  Font = osifont
  LineSpace = 80
  LockPosition = true
  MaxWidth = -1
  Rotation = 0
  ScaleType = 0
  Text = \u041f\u043b\u0438\u0442\u044b \u043e\u0431\u043b\u0435\u0433\u0447\u0451\u043d\u043d\u044b\u0435 160mm
  TextSize = 4
  TextStyle = 0
  X = 104.49
  Y = 193.218
FEATURE [TechDraw::DrawLeaderLine] LeaderLine005
  AutoHorizontal = true
  EndSymbol = 7
  LeaderParent = -> Annotation026
  LockPosition = true
  Rotation = 0
  Scalable = false
  ScaleType = 0
  StartSymbol = 7
  WayPoints = (3) [(0,0,0),(-2.30237,-441.288,0),(-511.894,-441.288,0)]
  X = 27.6874
  Y = -45.469
FEATURE [TechDraw::DrawLeaderLine] LeaderLine006
  AutoHorizontal = true
  EndSymbol = 7
  LeaderParent = -> Annotation023
  LockPosition = true
  Rotation = 0
  Scalable = false
  ScaleType = 0
  StartSymbol = 7
  WayPoints = (4) [(0,0,0),(0,-112.671,0),(-241.304,-298.052,0),(-700.128,-298.052,0)]
  X = 33.001
  Y = -31.105
FEATURE [TechDraw::DrawLeaderLine] LeaderLine007
  AutoHorizontal = true
  EndSymbol = 7
  LeaderParent = -> Annotation022
  LockPosition = true
  Rotation = 0
  Scalable = false
  ScaleType = 0
  StartSymbol = 7
  WayPoints = (3) [(0,0,0),(-234.053,-148.301,0),(-811.115,-148.301,0)]
  X = 52.2554
  Y = -15.2644
FEATURE [TechDraw::DrawLeaderLine] LeaderLine008
  AutoHorizontal = true
  EndSymbol = 7
  LeaderParent = -> Annotation019
  LockPosition = true
  Rotation = 0
  Scalable = false
  ScaleType = 0
  StartSymbol = 7
  WayPoints = (3) [(0,0,0),(123.191,316.527,0),(538.433,316.527,0)]
  X = -33.8955
  Y = 30.8346
FEATURE [TechDraw::DrawLeaderLine] LeaderLine009
  AutoHorizontal = true
  EndSymbol = 7
  LeaderParent = -> Annotation017
  LockPosition = true
  Rotation = 0
  Scalable = false
  ScaleType = 0
  StartSymbol = 7
  WayPoints = (3) [(0,0,0),(99.3175,258.506,0),(299.176,258.506,0)]
  X = -19.5842
  Y = 24.9219
FEATURE [TechDraw::DrawLeaderLine] LeaderLine010
  AutoHorizontal = true
  EndSymbol = 7
  LeaderParent = -> Annotation020
  LockPosition = true
  Rotation = 0
  Scalable = false
  ScaleType = 0
  StartSymbol = 7
  WayPoints = (3) [(0,0,0),(77.3527,184.314,0),(465.976,184.314,0)]
  X = -27.3933
  Y = 17.9304
FEATURE [TechDraw::DrawLeaderLine] LeaderLine011
  AutoHorizontal = true
  EndSymbol = 7
  LeaderParent = -> Annotation021
  LockPosition = true
  Rotation = 0
  Scalable = false
  ScaleType = 0
  StartSymbol = 7
  WayPoints = (3) [(0,0,0),(246.354,145.817,0),(563.314,145.817,0)]
  X = -40.3095
  Y = 13.3285
FEATURE [TechDraw::DrawLeaderLine] LeaderLine012
  AutoHorizontal = true
  EndSymbol = 7
  LeaderParent = -> Annotation018
  LockPosition = true
  Rotation = 0
  Scalable = false
  ScaleType = 0
  StartSymbol = 7
  WayPoints = (3) [(0,0,0),(226.991,110.973,0),(407.743,110.973,0)]
  X = -31.4229
  Y = 10.0706
FEATURE [App::FeaturePython] Dimension065  # Draft dimension (typed FeaturePython)
  Diameter = false
  Dimline = (0,5100,1600)
  Direction = (0,0,0)
  Distance = 2800
  End = (0,3665,2800)
  Normal = (1,0,0)
  Start = (0,3665,0)
FEATURE [App::FeaturePython] Dimension066  # Draft dimension (typed FeaturePython)
  Diameter = false
  Dimline = (0,5100,2700)
  Direction = (0,0,0)
  Distance = 330
  End = (0,3665,3130)
  Normal = (1,0,0)
  Start = (0,3665,2800)
FEATURE [App::FeaturePython] Dimension067  # Draft dimension (typed FeaturePython)
  Diameter = false
  Dimline = (0,5100,4100)
  Direction = (0,0,0)
  Distance = 503
  End = (0,3665,3633)
  Normal = (1,0,0)
  Start = (0,3665,3130)
FEATURE [App::FeaturePython] Dimension069  # Draft dimension (typed FeaturePython)
  Diameter = false
  Dimline = (0,3400,1900)
  Direction = (0,0,0)
  Distance = 300
  End = (0,3790,2800)
  Normal = (1,0,0)
  Start = (0,3790,2500)
FEATURE [App::FeaturePython] Dimension071  # Draft dimension (typed FeaturePython)
  Diameter = false
  Dimline = (0,11400,-400)
  Direction = (0,0,0)
  Distance = 7180
  End = (0,3730,6980)
  Normal = (1,0,0)
  Start = (0,3730,-200)
FEATURE [App::GeometryPython] BuildingPart100  label="Размеры (side)"  # Arch/BIM 52 (typed FeaturePython)
  Area = 0
  GlobalId = 27k3ICoRP4zxJkZ2CvXEQH
  Group = -> [Dimension029,Dimension065,Dimension066,Dimension067,Dimension069,Dimension071]
  Height = 0
  HeightPropagate = true
  IfcData = IfcUID=27k3ICoRP4zxJkZ2CvXEQH,+2 more (map truncated)
  IfcType = 52
  LevelOffset = 0
  Placement = pos=(0,0,0) rot=(0.57735,0.57735,0.57735;2.0944rad)
FEATURE [App::MaterialObjectPython] Material019  label="Red brick (solid)"  # material (typed FeaturePython)
  Description = A standard red brick
  Material = AuthorAndLicense=Concrete-Generic,CardName=Concrete-Generic,Color=(0.6666666666666666, 0.0, 0.0, 1.0),CompressiveStrength=25 MPa,Density=2400 kg/m^3,+9 more (map truncated)
  Transparency = 0
FEATURE [Part::FeaturePython] Wall301  label="Облицовка цоколя (полнотел.1нф) 001"  # Arch/BIM 166 (typed FeaturePython)
  Align = 1
  Area = 633000
  Base = -> Line1585
  BlockHeight = 65
  BlockLength = 250
  CountBroken = 1
  CountEntire = 32
  Face = 0
  GlobalId = 1E5ZyhmSr7guLYcvr8Y9qj
  Height = 75
  HorizontalArea = 1012800
  IfcData = IfcUID=1E5ZyhmSr7guLYcvr8Y9qj; attributes={"GlobalId": {"value": "1E5ZyhmSr7guLYcvr8Y9qj"}}
  IfcType = 166
  Joint = 10
  Length = 8440
  MakeBlocks = false
  Material = -> Material019
  MoveBase = false
  MoveWithHost = false
  Normal = (0,0,0)
  OffsetFirst = 250
  OffsetSecond = 120
  PerimeterLength = 17120
  Placement = pos=(0,0,-200) rot=(0,0,1;0rad)
  PredefinedType = 0
  VerticalArea = 1284000
  Width = 120
FEATURE [Part::FeaturePython] Wall302  label="Облицовка цоколя (полнотел.1нф) 010"  # Arch/BIM 166 (typed FeaturePython)
  Align = 0
  Area = 1003500
  Base = -> Line1584
  BlockHeight = 65
  BlockLength = 250
  CountBroken = 1
  CountEntire = 51
  Face = 0
  GlobalId = 1TP$vjbOv5ffUx0fDKfugP
  Height = 75
  HorizontalArea = 1605600
  IfcData = IfcUID=1TP$vjbOv5ffUx0fDKfugP; attributes={"GlobalId": {"value": "1TP$vjbOv5ffUx0fDKfugP"}}
  IfcType = 166
  Joint = 10
  Length = 13380
  MakeBlocks = false
  Material = -> Material019
  MoveBase = false
  MoveWithHost = false
  Normal = (0,0,0)
  OffsetFirst = 250
  OffsetSecond = 120
  PerimeterLength = 27000
  Placement = pos=(0,0,-200) rot=(0,0,1;0rad)
  PredefinedType = 0
  VerticalArea = 2025000
  Width = 120
FEATURE [Part::FeaturePython] Wall303  label="Облицовка цоколя (полнотел.1нф) 011"  # Arch/BIM 166 (typed FeaturePython)
  Align = 1
  Area = 642750
  Base = -> Line1586
  BlockHeight = 65
  BlockLength = 250
  CountBroken = 0
  CountEntire = 33
  Face = 0
  GlobalId = 0Qqq80WcDAy9cO4W0cQ$pL
  Height = 75
  HorizontalArea = 1028400
  IfcData = IfcUID=0Qqq80WcDAy9cO4W0cQ$pL; attributes={"GlobalId": {"value": "0Qqq80WcDAy9cO4W0cQ$pL"}}
  IfcType = 166
  Joint = 10
  Length = 8570
  MakeBlocks = false
  Material = -> Material019
  MoveBase = false
  MoveWithHost = false
  Normal = (0,0,0)
  OffsetFirst = 250
  OffsetSecond = 120
  PerimeterLength = 17380
  Placement = pos=(0,0,-200) rot=(0,0,1;0rad)
  PredefinedType = 0
  VerticalArea = 1303500
  Width = 120
FEATURE [Part::FeaturePython] Wall304  label="Облицовка цоколя (полнотел.1нф) 012"  # Arch/BIM 166 (typed FeaturePython)
  Align = 0
  Area = 1013250
  Base = -> Line1583
  BlockHeight = 65
  BlockLength = 250
  CountBroken = 0
  CountEntire = 52
  Face = 0
  GlobalId = 0a9Ful3VXDtwee5LreBW$T
  Height = 75
  HorizontalArea = 1621200
  IfcData = IfcUID=0a9Ful3VXDtwee5LreBW$T; attributes={"GlobalId": {"value": "0a9Ful3VXDtwee5LreBW$T"}}
  IfcType = 166
  Joint = 10
  Length = 13510
  MakeBlocks = false
  Material = -> Material019
  MoveBase = false
  MoveWithHost = false
  Normal = (0,0,0)
  OffsetFirst = 250
  OffsetSecond = 120
  PerimeterLength = 27260
  Placement = pos=(0,0,-200) rot=(0,0,1;0rad)
  PredefinedType = 0
  VerticalArea = 2044500
  Width = 120
FEATURE [Part::Part2DObjectPython] Wire890  # Draft 2D object (typed FeaturePython)
  Area = 0
  ChamferSize = 0
  Closed = true
  End = (12950,-425,0)
  FilletRadius = 0
  Length = 43380
  MakeFace = false
  Placement = pos=(-430,-410,0) rot=(0,0,1;0rad)
  Points = (4) [(0,-15,0),(0,8295,0),(13380,8295,0),(13380,-15,0)]
  Start = (-430,-425,0)
  Subdivisions = 0
FEATURE [Part::FeaturePython] Wall310  label="Отлив (вибропресс. бордюрный камень 1000х200х80мм)"  # Arch/BIM 166 (typed FeaturePython)
  Align = 1
  Area = 3470400
  Base = -> Wire890
  BlockHeight = 80
  BlockLength = 1000
  CountBroken = 4
  CountEntire = 39
  Face = 0
  Height = 80
  HorizontalArea = 8852000
  IfcData = attributes={"GlobalId": {"name": "GlobalId", "type": "IfcGloballyUniqueId", "is_enum": false, "enum_values": []}, "Description": {"... (+533 chars omitted),+1 more (map truncated)
  IfcType = 166
  Joint = 0
  Length = 43380
  MakeBlocks = false
  Material = -> Material018
  MoveBase = false
  MoveWithHost = false
  Normal = (0,0,0)
  Offset = 10
  OffsetFirst = 0
  OffsetSecond = 0
  PerimeterLength = 45060
  Placement = pos=(0,0,-120) rot=(0,0,1;0rad)
  PredefinedType = 0
  VerticalArea = 7081600
  Width = 200
FEATURE [Part::FeaturePython] Wall311  label="Утепление цоколя XPS 50mm"  # Arch/BIM 166 (typed FeaturePython)
  Align = 1
  Area = 8676000
  Base = -> Wire890
  BlockHeight = 80
  BlockLength = 1000
  CountBroken = 4
  CountEntire = 39
  Face = 0
  Height = 200
  HorizontalArea = 2.231e+06
  IfcData = attributes={"GlobalId": {"name": "GlobalId", "type": "IfcGloballyUniqueId", "is_enum": false, "enum_values": []}, "Description": {"... (+533 chars omitted),+1 more (map truncated)
  IfcType = 166
  Joint = 0
  Length = 43380
  MakeBlocks = false
  Material = -> Material002
  MoveBase = false
  MoveWithHost = false
  Normal = (0,0,0)
  Offset = 130
  OffsetFirst = 0
  OffsetSecond = 0
  PerimeterLength = 44820
  Placement = pos=(0,0,-320) rot=(0,0,1;0rad)
  PredefinedType = 0
  VerticalArea = 17848000
  Width = 50
FEATURE [Part::FeaturePython] Wall312  label="Отделка цоколя 15mm"  # Arch/BIM 166 (typed FeaturePython)
  Align = 1
  Area = 8676000
  Base = -> Wire890
  BlockHeight = 80
  BlockLength = 1000
  CountBroken = 4
  CountEntire = 39
  Face = 0
  Height = 200
  HorizontalArea = 673200
  IfcData = attributes={"GlobalId": {"name": "GlobalId", "type": "IfcGloballyUniqueId", "is_enum": false, "enum_values": []}, "Description": {"... (+533 chars omitted),+1 more (map truncated)
  IfcType = 166
  Joint = 0
  Length = 43380
  MakeBlocks = false
  Material = -> Material018
  MoveBase = false
  MoveWithHost = false
  Normal = (0,0,0)
  Offset = 180
  OffsetFirst = 0
  OffsetSecond = 0
  PerimeterLength = 44940
  Placement = pos=(0,0,-320) rot=(0,0,1;0rad)
  PredefinedType = 0
  VerticalArea = 17952000
  Width = 15
FEATURE [App::GeometryPython] BuildingPart102  label="Облицовка 1nf кирпич001"  # Arch/BIM 52 (typed FeaturePython)
  Area = 185118900
  GlobalId = 28tVz6in97ivETWCX3RcDU
  Group = -> [Wall298,Wall299,Wall300,Wall301,Wall302,Wall303,Wall304,Wall305,Wall306,Wall307,Wall308,Wall309,Wall310,Wall311,Wall312]
  Height = 0
  HeightPropagate = true
  IfcData = IfcUID=28tVz6in97ivETWCX3RcDU,attributes={"GlobalId": {"value": "28tVz6in97ivETWCX3RcDU"}},+1 more (map truncated)
  IfcType = 52
  LevelOffset = 0
FEATURE [TechDraw::DrawViewAnnotation] Annotation  label="a_092"
  Font = osifont
  LineSpace = 80
  LockPosition = true
  MaxWidth = -1
  Rotation = 0
  Scale = 0.02
  ScaleType = 0
  Text = \u041e\u0442\u0434\u0435\u043b\u043a\u0430 \u0446\u043e\u043a\u043e\u043b\u044f 15mm
  TextSize = 4
  TextStyle = 0
  X = 85.2969
  Y = 88.0815
FEATURE [TechDraw::DrawViewAnnotation] Annotation027  label="a_093"
  Font = osifont
  LineSpace = 80
  LockPosition = true
  MaxWidth = -1
  Rotation = 0
  Scale = 0.02
  ScaleType = 0
  Text = XPS 50mm
  TextSize = 4
  TextStyle = 0
  X = 95.3409
  Y = 93.1161
FEATURE [TechDraw::DrawViewAnnotation] Annotation028  label="a_094"
  Font = osifont
  LineSpace = 80
  LockPosition = true
  MaxWidth = -1
  Rotation = 0
  Scale = 0.02
  ScaleType = 0
  Text = \u041a\u0430\u043c\u0435\u043d\u044c \u0431\u043e\u0440\u0434\u044e\u0440\u043d\u044b\u0439 1000\u044580\u0445200mm
  TextSize = 4
  TextStyle = 0
  X = 74.5727
  Y = 97.7244
FEATURE [TechDraw::DrawLeaderLine] LeaderLine013
  AutoHorizontal = true
  EndSymbol = 7
  LeaderParent = -> Annotation
  LockPosition = true
  Rotation = 0
  Scalable = false
  ScaleType = 0
  StartSymbol = 7
  WayPoints = (3) [(0,0,0),(-95.8036,-29.0684,0),(-464.748,-29.0684,0)]
  X = 1397.61
  Y = -181.771
FEATURE [TechDraw::DrawLeaderLine] LeaderLine014
  AutoHorizontal = true
  EndSymbol = 7
  LeaderParent = -> Annotation027
  LockPosition = true
  Rotation = 0
  Scalable = false
  ScaleType = 0
  StartSymbol = 7
  WayPoints = (3) [(0,0,0),(-103.814,-76.5886,0),(-277.347,-76.5886,0)]
  X = 939.794
  Y = -403.983
FEATURE [TechDraw::DrawLeaderLine] LeaderLine015
  AutoHorizontal = true
  EndSymbol = 7
  LeaderParent = -> Annotation028
  LockPosition = true
  Rotation = 0
  Scalable = false
  ScaleType = 0
  StartSymbol = 7
  WayPoints = (3) [(0,0,0),(-108.706,-86.9646,0),(-695.382,-86.9646,0)]
  X = 2006.85
  Y = -452.409
FEATURE [TechDraw::DrawViewAnnotation] Annotation029  label="a_095"
  Font = osifont
  LineSpace = 80
  LockPosition = true
  MaxWidth = -1
  Rotation = 0
  Scale = 0.02
  ScaleType = 0
  Text = \u041a\u0438\u0440\u043f\u0438\u0447 \u043f\u043e\u043b\u043d\u043e\u0442\u0435\u043b\u044b\u0439 1\u043d\u0444
  TextSize = 4
  TextStyle = 0
  X = 313.34
  Y = 91.6882
FEATURE [TechDraw::DrawLeaderLine] LeaderLine016
  AutoHorizontal = true
  EndSymbol = 7
  LeaderParent = -> Annotation029
  LockPosition = true
  Rotation = 0
  Scalable = false
  ScaleType = 0
  StartSymbol = 7
  WayPoints = (3) [(0,0,0),(77.064,-40.1375,0),(501.188,-40.1375,0)]
  X = -1439.22
  Y = -222.205
FEATURE [App::DocumentObjectGroup] Group127  label="Выноски"
  Group = -> [LeaderLine,LeaderLine001,LeaderLine002,LeaderLine003,LeaderLine004,LeaderLine005,LeaderLine006,LeaderLine007,LeaderLine008,LeaderLine009,LeaderLine010,LeaderLine011,LeaderLine012,LeaderLine013,LeaderLine014,LeaderLine015,LeaderLine016]
FEATURE [TechDraw::DrawSVGTemplate] Template
  EditableTexts = Лист=3; Номер=ИЖС-2021.0001
  Height = 297
  Orientation = 1
  Width = 420
FEATURE [TechDraw::DrawViewSpreadsheet] Sheet
  CellEnd = E12
  CellStart = C1
  Font = osifont
  LineWidth = 0.35
  LockPosition = false
  Rotation = 0
  Scale = 1.2
  ScaleType = 2
  Source = -> Spreadsheet
  Symbol = <blob: 8016 chars omitted>
  TextSize = 12
  X = 107.319
  Y = 207.308
FEATURE [TechDraw::DrawViewAnnotation] Annotation030
  Font = osifont
  LineSpace = 80
  LockPosition = false
  MaxWidth = -1
  Rotation = 0
  ScaleType = 0
  Text = \u042d\u043a\u0441\u043f\u043b\u0438\u043a\u0430\u0446\u0438\u044f \u043f\u043e\u043c\u0435\u0449\u0435\u043d\u0438\u0439 1-\u0433\u043e \u044d\u0442\u0430\u0436\u0430
  TextSize = 8
  TextStyle = 0
  X = 107.631
  Y = 267.351
FEATURE [TechDraw::DrawPage] Page  label="Экспликация"
  KeepUpdated = false
  NextBalloonIndex = 1
  ProjectionType = 0
  Template = -> Template
  Views = -> [Sheet,Annotation030]
FEATURE [Part::Part2DObjectPython] Line1602  # Draft 2D object (typed FeaturePython)
  Area = 0
  ChamferSize = 0
  Closed = true
  End = (22842.7,-9031.64,0)
  FilletRadius = 0
  Length = 380
  MakeFace = true
  Placement = pos=(17078.5,-7861.73,0) rot=(0,0,1;1.37981rad)
  Points = (2) [(-109.84,-5505.54,0),(-54.4343,-5881.48,0)]
  Start = (22463.1,-9014.68,0)
  Subdivisions = 0
FEATURE [Part::FeaturePython] Wall316  label="Столб 001"  # Arch/BIM 166 (typed FeaturePython)
  Align = 0
  Area = 836000
  Base = -> Line1602
  BlockHeight = 0
  BlockLength = 0
  CountBroken = 0
  CountEntire = 0
  Face = 0
  Height = 2200
  HorizontalArea = 144400
  IfcData = attributes={"GlobalId": {"name": "GlobalId", "type": "IfcGloballyUniqueId", "is_enum": false, "enum_values": []}, "Description": {"... (+533 chars omitted),+1 more (map truncated)
  IfcType = 166
  Joint = 0
  Length = 380
  MakeBlocks = false
  Material = -> Material003
  MoveBase = false
  MoveWithHost = false
  Normal = (0,0,0)
  OffsetFirst = 0
  OffsetSecond = 0
  PerimeterLength = 1520
  Placement = pos=(0,0,-320) rot=(0,0,1;0rad)
  PredefinedType = 0
  VerticalArea = 3.344e+06
  Width = 380
FEATURE [Part::FeaturePython] Wall317  label="Столб 002"  # Arch/BIM 166 (typed FeaturePython)
  Align = 2
  Area = 836000
  BlockHeight = 0
  BlockLength = 0
  CloneOf = -> Wall316
  CountBroken = 0
  CountEntire = 0
  Face = 0
  Height = 2200
  HorizontalArea = 144400
  IfcData = attributes={"GlobalId": {"name": "GlobalId", "type": "IfcGloballyUniqueId", "is_enum": false, "enum_values": []}, "Description": {"... (+533 chars omitted),+1 more (map truncated)
  IfcType = 166
  Joint = 0
  Length = 380
  MakeBlocks = false
  Material = -> Material003
  MoveBase = false
  MoveWithHost = false
  Normal = (0,0,0)
  OffsetFirst = 0
  OffsetSecond = 0
  PerimeterLength = 1520
  Placement = pos=(1578.42,-70.54,-320) rot=(0,0,1;0rad)
  PredefinedType = 0
  VerticalArea = 3.344e+06
  Width = 380
FEATURE [Part::FeaturePython] Wall318  label="Столб 003"  # Arch/BIM 166 (typed FeaturePython)
  Align = 2
  Area = 836000
  BlockHeight = 0
  BlockLength = 0
  CloneOf = -> Wall316
  CountBroken = 0
  CountEntire = 0
  Face = 0
  Height = 2200
  HorizontalArea = 144400
  IfcData = attributes={"GlobalId": {"name": "GlobalId", "type": "IfcGloballyUniqueId", "is_enum": false, "enum_values": []}, "Description": {"... (+533 chars omitted),+1 more (map truncated)
  IfcType = 166
  Joint = 0
  Length = 380
  MakeBlocks = false
  Material = -> Material003
  MoveBase = false
  MoveWithHost = false
  Normal = (0,0,0)
  OffsetFirst = 0
  OffsetSecond = 0
  PerimeterLength = 1520
  Placement = pos=(1818.62,5304.1,-320) rot=(0,0,1;0rad)
  PredefinedType = 0
  VerticalArea = 3.344e+06
  Width = 380
FEATURE [Part::Part2DObjectPython] Line1604  label="Калитка 001"  # Draft 2D object (typed FeaturePython)
  Area = 0
  ChamferSize = 0
  Closed = true
  End = (22834.2,-9221.45,0)
  FilletRadius = 0
  Length = 1200
  MakeFace = true
  Placement = pos=(12251.1,-7121.93,0) rot=(0,0,1;0.025758rad)
  Points = (2) [(11722.5,-2455.82,0),(10525.5,-2371.39,0)]
  Start = (24033,-9275.03,0)
  Subdivisions = 0
FEATURE [Part::FeaturePython] Wall319  label="Калитка 002"  # Arch/BIM 166 (typed FeaturePython)
  Align = 1
  Area = 2.16e+06
  Base = -> Line1604
  BlockHeight = 2000
  BlockLength = 150
  CountBroken = 8
  CountEntire = 0
  Face = 0
  Height = 1800
  HorizontalArea = 0
  IfcData = attributes={"GlobalId": {"name": "GlobalId", "type": "IfcGloballyUniqueId", "is_enum": false, "enum_values": []}, "Description": {"... (+533 chars omitted),+1 more (map truncated)
  IfcType = 166
  Joint = 10
  Length = 1200
  MakeBlocks = true
  Material = -> Material010
  MoveBase = false
  MoveWithHost = false
  Normal = (0,0,0)
  Offset = 50
  OffsetFirst = 90
  OffsetSecond = 0
  PerimeterLength = 0
  Placement = pos=(0,0,-120) rot=(0,0,1;0rad)
  PredefinedType = 0
  VerticalArea = 0
  Width = 50
FEATURE [Part::Part2DObjectPython] Wire892  # Draft 2D object (typed FeaturePython)
  Area = 0
  ChamferSize = 0
  Closed = true
  End = (22842.7,-9031.64,1880)
  FilletRadius = 0
  Length = 1520
  MakeFace = false
  Placement = pos=(22463.1,-9014.68,1880) rot=(0,0,-1;1.61546rad)
  Points = (4) [(0,0,0),(380,0,0),(380,380,0),(-1.72804e-11,380,0)]
  Start = (22463.1,-9014.68,1880)
  Subdivisions = 0
FEATURE [Part::FeaturePython] Roof018  label="Крышка столба 001"  # Arch/BIM 113 (typed FeaturePython)
  Angles = [15,15,15,15]
  Base = -> Wire892
  BorderLength = 1920
  Face = 0
  Flip = false
  Heights = [50.9103,53.5898,50.9103,53.5898]
  HorizontalArea = 230400
  IdRel = [-1,-1,-1,-1]
  IfcData = attributes={"GlobalId": {"name": "GlobalId", "type": "IfcGloballyUniqueId", "is_enum": false, "enum_values": []}, "Description": {"... (+613 chars omitted),+1 more (map truncated)
  IfcType = 113
  Material = -> Material018
  MoveBase = false
  MoveWithHost = false
  Overhang = [50,50,50,50]
  PerimeterLength = 0
  PredefinedType = 0
  RidgeLength = 1381.8
  Runs = [200,200,200,200]
  Thickness = [50,50,50,50]
  VerticalArea = 99386.5
FEATURE [Part::FeaturePython] Roof019  label="Крышка столба 002"  # Arch/BIM 113 (typed FeaturePython)
  BorderLength = 0
  CloneOf = -> Roof018
  Face = 0
  Flip = false
  HorizontalArea = 230400
  IfcData = attributes={"GlobalId": {"name": "GlobalId", "type": "IfcGloballyUniqueId", "is_enum": false, "enum_values": []}, "Description": {"... (+613 chars omitted),+1 more (map truncated)
  IfcType = 113
  Material = -> Material018
  MoveBase = false
  MoveWithHost = false
  PerimeterLength = 0
  Placement = pos=(1578.42,-70.54,0) rot=(0,0,1;0rad)
  PredefinedType = 0
  RidgeLength = 0
  Thickness = [50,50,50,50]
  VerticalArea = 99386.5
FEATURE [Part::FeaturePython] Roof020  label="Крышка столба 003"  # Arch/BIM 113 (typed FeaturePython)
  BorderLength = 0
  CloneOf = -> Roof018
  Face = 0
  Flip = false
  HorizontalArea = 230400
  IfcData = attributes={"GlobalId": {"name": "GlobalId", "type": "IfcGloballyUniqueId", "is_enum": false, "enum_values": []}, "Description": {"... (+613 chars omitted),+1 more (map truncated)
  IfcType = 113
  Material = -> Material018
  MoveBase = false
  MoveWithHost = false
  PerimeterLength = 0
  Placement = pos=(1818.62,5304.1,0) rot=(0,0,1;0rad)
  PredefinedType = 0
  RidgeLength = 0
  Thickness = [50,50,50,50]
  VerticalArea = 99386.5
FEATURE [Part::Part2DObjectPython] Rectangle3361  # Draft 2D object (typed FeaturePython)
  Area = 0
  ChamferSize = 0
  Columns = 1
  FilletRadius = 0
  Height = 8540
  Length = 20900
  MakeFace = false
  Placement = pos=(-4200,-540,0) rot=(0,0,1;0rad)
  Rows = 1
FEATURE [Part::FeaturePython] Roof021  label="Кровля 2скатн002"  # Arch/BIM 113 (typed FeaturePython)
  Angles = [35,35,35,35]
  Base = -> Rectangle3361
  BorderLength = 58880
  Face = 0
  Flip = false
  Heights = [2989.89,3150.93,2989.89,3150.93]
  HorizontalArea = 178486000
  IdRel = [-1,-1,-1,-1]
  IfcData = attributes={"GlobalId": {"name": "GlobalId", "type": "IfcGloballyUniqueId", "is_enum": false, "enum_values": []}, "Description": {"... (+613 chars omitted),+1 more (map truncated)
  IfcType = 113
  Material = -> Material007
  MoveBase = false
  MoveWithHost = false
  Overhang = [0,0,0,0]
  PerimeterLength = 0
  Placement = pos=(0,4.55e-13,3062.84) rot=(0,0,1;0rad)
  PredefinedType = 0
  RidgeLength = 39313.4
  Runs = [4500,4500,4500,4500]
  Thickness = [200,200,200,200]
  VerticalArea = 1.43758e+07
FEATURE [Part::FeaturePython] Roof022  label="roof_4_side001"  # Arch/BIM 113 (typed FeaturePython)
  Angles = [35,35,35,35]
  Base = -> Wire691
  BorderLength = 57660
  Face = 0
  Flip = false
  Heights = [3459.03,3851.14,3459.03,3851.14]
  HorizontalArea = 201366000
  IdRel = [-1,-1,-1,-1]
  IfcData = attributes={"GlobalId": {"name": "GlobalId", "type": "IfcGloballyUniqueId", "is_enum": false, "enum_values": []}, "Description": {"... (+613 chars omitted),+1 more (map truncated)
  IfcType = 113
  Material = -> Material007
  MoveBase = false
  MoveWithHost = false
  Overhang = [1000,1000,1000,1000]
  PerimeterLength = 0
  Placement = pos=(0,0,3093.7) rot=(0,0,1;0rad)
  PredefinedType = 0
  RidgeLength = 42564.8
  Runs = [5500,5500,5500,5500]
  Thickness = [200,200,200,200]
  VerticalArea = 1.4078e+07
FEATURE [Part::MultiCommon] Common035
  Shapes = -> [Roof021,Extrude108]
FEATURE [Part::MultiCommon] Common036
  Shapes = -> [Extrude,Roof022]
FEATURE [Part::Cut] Cut053  label="Объём стропилки вальмы"
  Base = -> Common036
  Tool = -> Extrude092
FEATURE [Part::Cut] Cut054  label="Объём стропилки кукушек001"
  Base = -> Common035
  Tool = -> Roof015
FEATURE [Part::Part2DObjectPython] Wire896  # Draft 2D object (typed FeaturePython)
  Area = 1.07086e+08
  ChamferSize = 0
  Closed = true
  End = (3198,-1210,0)
  FilletRadius = 0
  Length = 60784.9
  MakeFace = true
  Placement = pos=(-1230,-1210,0) rot=(0,0,1;0rad)
  Points = (14) [(0,0,0),(4940,4940,0),(3.63798e-12,9880,0),(8237,9880,0),(8237,10600,0),(13197,10600,0),(13197,9880,0),(14980,9880,0),(10040,4940,0),+5 more]
  Start = (-1230,-1210,0)
  Subdivisions = 0
FEATURE [Part::FeaturePython] Structure048  label="вычитаемый объём 001"  # Arch/BIM 52 (typed FeaturePython)
  Base = -> Wire896
  FaceMaker = 0
  Height = 5000
  HorizontalArea = 1.07086e+08
  IfcData = complex_attributes={"OwnerHistory": {}, "IsNestedBy": {}, "IsDecomposedBy": {}, "IsDefinedBy": {}, "ObjectPlacement": {}, "Representation":... (+4 chars omitted)
  IfcType = 52
  Length = 0
  MoveBase = false
  MoveWithHost = false
  Nodes = (2) [(6625,8181.9,0),(6625,8181.9,4000)]
  NodesOffset = 0
  Normal = (0,0,1)
  PerimeterLength = 60784.9
  Placement = pos=(0,0,2500) rot=(0,0,1;0rad)
  VerticalArea = 3.03924e+08
  Width = 100
FEATURE [Part::MultiCommon] Common
  Shapes = -> [Array013,Structure048]
FEATURE [Part::MultiCommon] Common037  label="Стропилка вальмы боковые скаты 001"
  Shapes = -> [Cut053,Common]
FEATURE [Part::MultiCommon] Common038  label="Стропилка кукушек004"
  Shapes = -> [Array013,Cut054]
FEATURE [Part::FeaturePython] Wall322  label="Стена029"  # Arch/BIM 166 (typed FeaturePython)
  Align = 2
  Area = 3.45422e+07
  Base = -> Line1497
  BlockHeight = 0
  BlockLength = 0
  CountBroken = 0
  CountEntire = 0
  Face = 0
  Height = 5000
  HorizontalArea = 1.03626e+06
  IfcData = attributes={"GlobalId": {"name": "GlobalId", "type": "IfcGloballyUniqueId", "is_enum": false, "enum_values": []}, "Description": {"... (+533 chars omitted),+1 more (map truncated)
  IfcType = 166
  Joint = 0
  Length = 6908.43
  MakeBlocks = false
  MoveBase = false
  MoveWithHost = false
  Normal = (0,0,0)
  OffsetFirst = 0
  OffsetSecond = 0
  PerimeterLength = 14116.9
  Placement = pos=(35.3553,-35.3553,2500) rot=(0,0,1;0rad)
  PredefinedType = 0
  VerticalArea = 7.05843e+07
  Width = 150
FEATURE [Part::FeaturePython] Wall323  label="Стена030"  # Arch/BIM 166 (typed FeaturePython)
  Align = 2
  Area = 3.45422e+07
  Base = -> Line1498
  BlockHeight = 0
  BlockLength = 0
  CountBroken = 0
  CountEntire = 0
  Face = 0
  Height = 5000
  HorizontalArea = 1.03626e+06
  IfcData = attributes={"GlobalId": {"name": "GlobalId", "type": "IfcGloballyUniqueId", "is_enum": false, "enum_values": []}, "Description": {"... (+533 chars omitted),+1 more (map truncated)
  IfcType = 166
  Joint = 0
  Length = 6908.43
  MakeBlocks = false
  MoveBase = false
  MoveWithHost = false
  Normal = (0,0,0)
  OffsetFirst = 0
  OffsetSecond = 0
  PerimeterLength = 14116.9
  Placement = pos=(35.3553,35.3553,2500) rot=(0,0,1;0rad)
  PredefinedType = 0
  VerticalArea = 7.05843e+07
  Width = 150
FEATURE [Part::FeaturePython] Wall324  label="Стена031"  # Arch/BIM 166 (typed FeaturePython)
  Align = 2
  Area = 3.45422e+07
  Base = -> Line1500
  BlockHeight = 0
  BlockLength = 0
  CountBroken = 0
  CountEntire = 0
  Face = 0
  Height = 5000
  HorizontalArea = 1.03626e+06
  IfcData = attributes={"GlobalId": {"name": "GlobalId", "type": "IfcGloballyUniqueId", "is_enum": false, "enum_values": []}, "Description": {"... (+533 chars omitted),+1 more (map truncated)
  IfcType = 166
  Joint = 0
  Length = 6908.43
  MakeBlocks = false
  MoveBase = false
  MoveWithHost = false
  Normal = (0,0,0)
  OffsetFirst = 0
  OffsetSecond = 0
  PerimeterLength = 14116.9
  Placement = pos=(-35.3553,-35.3553,2500) rot=(0,0,1;0rad)
  PredefinedType = 0
  VerticalArea = 7.05843e+07
  Width = 150
FEATURE [Part::FeaturePython] Wall325  label="Стена032"  # Arch/BIM 166 (typed FeaturePython)
  Align = 2
  Area = 3.45422e+07
  Base = -> Line1501
  BlockHeight = 0
  BlockLength = 0
  CountBroken = 0
  CountEntire = 0
  Face = 0
  Height = 5000
  HorizontalArea = 1.03626e+06
  IfcData = attributes={"GlobalId": {"name": "GlobalId", "type": "IfcGloballyUniqueId", "is_enum": false, "enum_values": []}, "Description": {"... (+533 chars omitted),+1 more (map truncated)
  IfcType = 166
  Joint = 0
  Length = 6908.43
  MakeBlocks = false
  MoveBase = false
  MoveWithHost = false
  Normal = (0,0,0)
  OffsetFirst = 0
  OffsetSecond = 0
  PerimeterLength = 14116.9
  Placement = pos=(-35.3553,35.3553,2500) rot=(0,0,1;0rad)
  PredefinedType = 0
  VerticalArea = 7.05843e+07
  Width = 150
FEATURE [Part::MultiCommon] Common040  label="Накосное стропило 004"
  Shapes = -> [Wall323,Cut053]
FEATURE [Part::MultiCommon] Common041  label="Накосное стропило 001"
  Shapes = -> [Wall322,Cut053]
FEATURE [Part::MultiCommon] Common042  label="Накосное стропило 002"
  Shapes = -> [Wall324,Cut053]
FEATURE [Part::MultiCommon] Common043  label="Накосное стропило 003"
  Shapes = -> [Wall325,Cut053]
FEATURE [Part::FeaturePython] Wall327  label="Стена034"  # Arch/BIM 166 (typed FeaturePython)
  Align = 2
  Area = 2.6417e+07
  Base = -> Line1507
  BlockHeight = 0
  BlockLength = 0
  CountBroken = 0
  CountEntire = 0
  Face = 0
  Height = 5000
  HorizontalArea = 792510
  IfcData = attributes={"GlobalId": {"name": "GlobalId", "type": "IfcGloballyUniqueId", "is_enum": false, "enum_values": []}, "Description": {"... (+533 chars omitted),+1 more (map truncated)
  IfcType = 166
  Joint = 0
  Length = 5283.4
  MakeBlocks = false
  MoveBase = false
  MoveWithHost = false
  Normal = (0,0,0)
  OffsetFirst = 0
  OffsetSecond = 0
  PerimeterLength = 10866.8
  Placement = pos=(159.099,-53.033,2500) rot=(0,0,1;0rad)
  PredefinedType = 0
  VerticalArea = 5.4334e+07
  Width = 150
FEATURE [Part::FeaturePython] Wall328  label="Стена035"  # Arch/BIM 166 (typed FeaturePython)
  Align = 2
  Area = 2.6417e+07
  Base = -> Line1506
  BlockHeight = 0
  BlockLength = 0
  CountBroken = 0
  CountEntire = 0
  Face = 0
  Height = 5000
  HorizontalArea = 792510
  IfcData = attributes={"GlobalId": {"name": "GlobalId", "type": "IfcGloballyUniqueId", "is_enum": false, "enum_values": []}, "Description": {"... (+533 chars omitted),+1 more (map truncated)
  IfcType = 166
  Joint = 0
  Length = 5283.4
  MakeBlocks = false
  MoveBase = false
  MoveWithHost = false
  Normal = (0,0,0)
  OffsetFirst = 0
  OffsetSecond = 0
  PerimeterLength = 10866.8
  Placement = pos=(159.099,53.033,2500) rot=(0,0,1;0rad)
  PredefinedType = 0
  VerticalArea = 5.4334e+07
  Width = 150
FEATURE [Part::FeaturePython] Wall329  label="Стена036"  # Arch/BIM 166 (typed FeaturePython)
  Align = 2
  Area = 2.6417e+07
  Base = -> Line1502
  BlockHeight = 0
  BlockLength = 0
  CountBroken = 0
  CountEntire = 0
  Face = 0
  Height = 5000
  HorizontalArea = 792510
  IfcData = attributes={"GlobalId": {"name": "GlobalId", "type": "IfcGloballyUniqueId", "is_enum": false, "enum_values": []}, "Description": {"... (+533 chars omitted),+1 more (map truncated)
  IfcType = 166
  Joint = 0
  Length = 5283.4
  MakeBlocks = false
  MoveBase = false
  MoveWithHost = false
  Normal = (0,0,0)
  OffsetFirst = 0
  OffsetSecond = 0
  PerimeterLength = 10866.8
  Placement = pos=(-159.099,-53.033,2500) rot=(0,0,1;0rad)
  PredefinedType = 0
  VerticalArea = 5.4334e+07
  Width = 150
FEATURE [Part::FeaturePython] Wall330  label="Стена037"  # Arch/BIM 166 (typed FeaturePython)
  Align = 2
  Area = 2.6417e+07
  Base = -> Line1503
  BlockHeight = 0
  BlockLength = 0
  CountBroken = 0
  CountEntire = 0
  Face = 0
  Height = 5000
  HorizontalArea = 792510
  IfcData = attributes={"GlobalId": {"name": "GlobalId", "type": "IfcGloballyUniqueId", "is_enum": false, "enum_values": []}, "Description": {"... (+533 chars omitted),+1 more (map truncated)
  IfcType = 166
  Joint = 0
  Length = 5283.4
  MakeBlocks = false
  MoveBase = false
  MoveWithHost = false
  Normal = (0,0,0)
  OffsetFirst = 0
  OffsetSecond = 0
  PerimeterLength = 10866.8
  Placement = pos=(-159.099,53.033,2500) rot=(0,0,1;0rad)
  PredefinedType = 0
  VerticalArea = 5.4334e+07
  Width = 150
FEATURE [Part::MultiCommon] Common046  label="Накосное стропило кукушки 001"
  Shapes = -> [Wall329,Cut053]
FEATURE [Part::MultiCommon] Common047  label="Накосное стропило кукушки 010"
  Shapes = -> [Wall330,Cut053]
FEATURE [Part::MultiCommon] Common048  label="Накосное стропило кукушки 011"
  Shapes = -> [Wall327,Cut053]
FEATURE [Part::MultiCommon] Common049  label="Накосное стропило кукушки 012"
  Shapes = -> [Wall328,Cut053]
FEATURE [Part::Part2DObjectPython] Wire897  # Draft 2D object (typed FeaturePython)
  Area = 1.44851e+07
  ChamferSize = 0
  Closed = true
  End = (2995.93,3730,0)
  FilletRadius = 0
  Length = 18376.6
  MakeFace = true
  Placement = pos=(-810,-75.926,0) rot=(0,0,1;0rad)
  Points = (3) [(0,0,0),(0,7611.85,0),(3805.93,3805.93,0)]
  Start = (-810,-75.926,0)
  Subdivisions = 0
FEATURE [Part::FeaturePython] Structure438  label="Структура"  # Arch/BIM 172 (typed FeaturePython)
  Base = -> Wire897
  FaceMaker = 0
  Height = 5000
  HorizontalArea = 1.44851e+07
  IfcData = attributes={"GlobalId": {"name": "GlobalId", "type": "IfcGloballyUniqueId", "is_enum": false, "enum_values": []}, "Description": {"... (+484 chars omitted),+1 more (map truncated)
  IfcType = 172
  Length = 0
  MoveBase = false
  MoveWithHost = false
  Nodes = (2) [(458.642,3730,0),(458.642,3730,5000)]
  NodesOffset = 0
  Normal = (0,0,1)
  PerimeterLength = 18376.6
  Placement = pos=(0,0,2500) rot=(0,0,1;0rad)
  PredefinedType = 0
  VerticalArea = 9.18832e+07
  Width = 100
FEATURE [Part::FeaturePython] Structure439  label="Структура021"  # Arch/BIM 172 (typed FeaturePython)
  CloneOf = -> Structure438
  FaceMaker = 0
  Height = 5000
  HorizontalArea = 1.44851e+07
  IfcData = attributes={"GlobalId": {"name": "GlobalId", "type": "IfcGloballyUniqueId", "is_enum": false, "enum_values": []}, "Description": {"... (+484 chars omitted),+1 more (map truncated)
  IfcType = 172
  Length = 0
  MoveBase = false
  MoveWithHost = false
  Nodes = (2) [(458.642,3730,0),(458.642,3730,5000)]
  NodesOffset = 0
  Normal = (0,0,0)
  PerimeterLength = 18376.6
  Placement = pos=(12520,7460,2500) rot=(0,0,1;3.14159rad)
  PredefinedType = 0
  VerticalArea = 9.18832e+07
  Width = 100
FEATURE [Part::MultiFuse] Fusion047
  Shapes = -> [Structure438,Structure439]
FEATURE [Part::MultiCommon] Common050  label="Стропилка кукушек001"
  Shapes = -> [Fusion047,Common038]
FEATURE [Part::Part2DObjectPython] Wire898  # Draft 2D object (typed FeaturePython)
  Area = 2.44036e+07
  ChamferSize = 0
  Closed = true
  End = (3725,3730,0)
  FilletRadius = 0
  Length = 23852.4
  MakeFace = true
  Placement = pos=(-1215,-1210,0) rot=(0,0,1;0rad)
  Points = (3) [(0,0,0),(6.82121e-13,9880,0),(4940,4940,0)]
  Start = (-1215,-1210,0)
  Subdivisions = 0
FEATURE [Part::Extrusion] Extrude099006
  Base = -> Wire898
  Dir = (0,0,1)
  DirMode = 2
  FaceMakerClass = Part::FaceMakerBullseye
  LengthFwd = 5000
  LengthRev = 0
  Placement = pos=(0,0,2500) rot=(0,0,1;0rad)
  Solid = false
  Symmetric = false
FEATURE [Part::FeaturePython] Clone  label="Extrude099007"  # Draft clone (typed FeaturePython)
  AttacherType = Attacher::AttachEngine3D
  Fuse = false
  Objects = -> [Extrude099006]
  Placement = pos=(12520,7460,2500) rot=(0,0,1;3.14159rad)
  Scale = (1,1,1)
FEATURE [Part::MultiFuse] Fusion048
  Shapes = -> [Extrude099006,Clone]
FEATURE [Part::MultiCommon] Common051
  Shapes = -> [Fusion048,Array014]
FEATURE [Part::MultiCommon] Common052
  Shapes = -> [Roof022,Common051]
FEATURE [Part::FeaturePython] Structure440  label="Стойка под конёк 001"  # Arch/BIM 172 (typed FeaturePython)
  Base = -> Rectangle3228
  FaceMaker = 0
  Height = 3220
  HorizontalArea = 22500
  IfcData = attributes={"GlobalId": {"name": "GlobalId", "type": "IfcGloballyUniqueId", "is_enum": false, "enum_values": []}, "Description": {"... (+484 chars omitted),+1 more (map truncated)
  IfcType = 172
  Length = 0
  Material = -> Material
  MoveBase = false
  MoveWithHost = false
  Nodes = (2) [(9125,3730,0),(9125,3730,3220)]
  NodesOffset = 0
  Normal = (0,0,0)
  PerimeterLength = 600
  Placement = pos=(0,0,3130) rot=(0,0,1;0rad)
  PredefinedType = 0
  VerticalArea = 1932000
  Width = 100
FEATURE [Part::FeaturePython] Structure441  label="Стойка под конёк 010"  # Arch/BIM 172 (typed FeaturePython)
  Base = -> Rectangle3227
  FaceMaker = 0
  Height = 3220
  HorizontalArea = 22500
  IfcData = attributes={"GlobalId": {"name": "GlobalId", "type": "IfcGloballyUniqueId", "is_enum": false, "enum_values": []}, "Description": {"... (+484 chars omitted),+1 more (map truncated)
  IfcType = 172
  Length = 0
  Material = -> Material
  MoveBase = false
  MoveWithHost = false
  Nodes = (2) [(3395,3730,0),(3395,3730,3220)]
  NodesOffset = 0
  Normal = (0,0,0)
  PerimeterLength = 600
  Placement = pos=(0,0,3130) rot=(0,0,1;0rad)
  PredefinedType = 0
  VerticalArea = 1932000
  Width = 100
FEATURE [Part::FeaturePython] Structure442  label="Стойка под конёк 011"  # Arch/BIM 172 (typed FeaturePython)
  Base = -> Rectangle3229
  FaceMaker = 0
  Height = 3220
  HorizontalArea = 22500
  IfcData = attributes={"GlobalId": {"name": "GlobalId", "type": "IfcGloballyUniqueId", "is_enum": false, "enum_values": []}, "Description": {"... (+484 chars omitted),+1 more (map truncated)
  IfcType = 172
  Length = 0
  Material = -> Material
  MoveBase = false
  MoveWithHost = false
  Nodes = (2) [(5365,3730,0),(5365,3730,3220)]
  NodesOffset = 0
  Normal = (0,0,0)
  PerimeterLength = 600
  Placement = pos=(0,0,3130) rot=(0,0,1;0rad)
  PredefinedType = 0
  VerticalArea = 1932000
  Width = 100
FEATURE [Part::FeaturePython] Structure443  label="Стойка под конёк 012"  # Arch/BIM 172 (typed FeaturePython)
  Base = -> Rectangle3240
  FaceMaker = 0
  Height = 3220
  HorizontalArea = 22500
  IfcData = attributes={"GlobalId": {"name": "GlobalId", "type": "IfcGloballyUniqueId", "is_enum": false, "enum_values": []}, "Description": {"... (+484 chars omitted),+1 more (map truncated)
  IfcType = 172
  Length = 0
  Material = -> Material
  MoveBase = false
  MoveWithHost = false
  Nodes = (2) [(6625,3730,0),(6625,3730,3220)]
  NodesOffset = 0
  Normal = (0,0,0)
  PerimeterLength = 600
  Placement = pos=(0,0,3130) rot=(0,0,1;0rad)
  PredefinedType = 0
  VerticalArea = 1932000
  Width = 100
FEATURE [Part::Part2DObjectPython] Rectangle3362  # Draft 2D object (typed FeaturePython)
  Area = 22500
  ChamferSize = 0
  Columns = 1
  FilletRadius = 0
  Height = 150
  Length = 150
  MakeFace = true
  Placement = pos=(-335,3655,0) rot=(0,0,1;0rad)
  Rows = 1
FEATURE [Part::Part2DObjectPython] Rectangle3363  # Draft 2D object (typed FeaturePython)
  Area = 22500
  ChamferSize = 0
  Columns = 1
  FilletRadius = 0
  Height = 150
  Length = 150
  MakeFace = true
  Placement = pos=(12705,3655,0) rot=(0,0,1;0rad)
  Rows = 1
FEATURE [Part::FeaturePython] Structure444  label="Стойка фронтона 002"  # Arch/BIM 172 (typed FeaturePython)
  Base = -> Rectangle3363
  FaceMaker = 0
  Height = 2070
  HorizontalArea = 22500
  IfcData = attributes={"GlobalId": {"name": "GlobalId", "type": "IfcGloballyUniqueId", "is_enum": false, "enum_values": []}, "Description": {"... (+484 chars omitted),+1 more (map truncated)
  IfcType = 172
  Length = 0
  Material = -> Material
  MoveBase = false
  MoveWithHost = false
  Nodes = (2) [(12780,3730,0),(12780,3730,2070)]
  NodesOffset = 0
  Normal = (0,0,0)
  PerimeterLength = 600
  Placement = pos=(0,0,3780) rot=(0,0,1;0rad)
  PredefinedType = 0
  VerticalArea = 1242000
  Width = 100
FEATURE [Part::FeaturePython] Structure445  label="Стойка фронтона 001"  # Arch/BIM 172 (typed FeaturePython)
  Base = -> Rectangle3362
  FaceMaker = 0
  Height = 2070
  HorizontalArea = 22500
  IfcData = attributes={"GlobalId": {"name": "GlobalId", "type": "IfcGloballyUniqueId", "is_enum": false, "enum_values": []}, "Description": {"... (+484 chars omitted),+1 more (map truncated)
  IfcType = 172
  Length = 0
  Material = -> Material
  MoveBase = false
  MoveWithHost = false
  Nodes = (2) [(-260,3730,0),(-260,3730,2070)]
  NodesOffset = 0
  Normal = (0,0,0)
  PerimeterLength = 600
  Placement = pos=(0,0,3780) rot=(0,0,1;0rad)
  PredefinedType = 0
  VerticalArea = 1242000
  Width = 100
FEATURE [Part::Part2DObjectPython] Line1606  # Draft 2D object (typed FeaturePython)
  Area = 0
  ChamferSize = 0
  Closed = false
  End = (12850,3730,0)
  FilletRadius = 0
  Length = 3650
  MakeFace = true
  Placement = pos=(9200,3730,0) rot=(0,0,1;0rad)
  Points = (2) [(0,0,0),(3650,0,0)]
  Start = (9200,3730,0)
  Subdivisions = 0
FEATURE [Part::FeaturePython] Wall331  label="Конёк кукушки 002"  # Arch/BIM 166 (typed FeaturePython)
  Align = 2
  Area = 730000
  Base = -> Line1606
  BlockHeight = 0
  BlockLength = 0
  CountBroken = 0
  CountEntire = 0
  Face = 0
  Height = 200
  HorizontalArea = 547500
  IfcData = attributes={"GlobalId": {"name": "GlobalId", "type": "IfcGloballyUniqueId", "is_enum": false, "enum_values": []}, "Description": {"... (+533 chars omitted),+1 more (map truncated)
  IfcType = 166
  Joint = 0
  Length = 3650
  MakeBlocks = false
  MoveBase = false
  MoveWithHost = false
  Normal = (0,0,0)
  OffsetFirst = 0
  OffsetSecond = 0
  PerimeterLength = 7600
  Placement = pos=(0,0,5850) rot=(0,0,1;0rad)
  PredefinedType = 0
  VerticalArea = 1.52e+06
  Width = 150
FEATURE [Part::FeaturePython] Wall333  label="Конёк кукушки 001"  # Arch/BIM 166 (typed FeaturePython)
  Align = 2
  Area = 730000
  BlockHeight = 0
  BlockLength = 0
  CloneOf = -> Wall331
  CountBroken = 0
  CountEntire = 0
  Face = 0
  Height = 200
  HorizontalArea = 547500
  IfcData = attributes={"GlobalId": {"name": "GlobalId", "type": "IfcGloballyUniqueId", "is_enum": false, "enum_values": []}, "Description": {"... (+533 chars omitted),+1 more (map truncated)
  IfcType = 166
  Joint = 0
  Length = 3650
  MakeBlocks = false
  MoveBase = false
  MoveWithHost = false
  Normal = (0,0,0)
  OffsetFirst = 0
  OffsetSecond = 0
  PerimeterLength = 7600
  Placement = pos=(-9530,-4.55e-13,5850) rot=(0,0,1;0rad)
  PredefinedType = 0
  VerticalArea = 1.52e+06
  Width = 150
FEATURE [Part::Part2DObjectPython] Line1607  # Draft 2D object (typed FeaturePython)
  Area = 0
  ChamferSize = 0
  Closed = true
  End = (9200,3730,0)
  FilletRadius = 0
  Length = 5880
  MakeFace = true
  Placement = pos=(9200,3730,0) rot=(0,0,1;0rad)
  Points = (2) [(-5880,0,0),(0,0,0)]
  Start = (3320,3730,0)
  Subdivisions = 0
FEATURE [Part::FeaturePython] Wall334  label="Конёк вальмы"  # Arch/BIM 166 (typed FeaturePython)
  Align = 2
  Area = 1176000
  Base = -> Line1607
  BlockHeight = 0
  BlockLength = 0
  CountBroken = 0
  CountEntire = 0
  Face = 0
  Height = 200
  HorizontalArea = 882000
  IfcData = attributes={"GlobalId": {"name": "GlobalId", "type": "IfcGloballyUniqueId", "is_enum": false, "enum_values": []}, "Description": {"... (+533 chars omitted),+1 more (map truncated)
  IfcType = 166
  Joint = 0
  Length = 5880
  MakeBlocks = false
  Material = -> Material
  MoveBase = false
  MoveWithHost = false
  Normal = (0,0,0)
  OffsetFirst = 0
  OffsetSecond = 0
  PerimeterLength = 12060
  Placement = pos=(0,0,6350) rot=(0,0,1;0rad)
  PredefinedType = 0
  VerticalArea = 2412000
  Width = 150
FEATURE [Part::Part2DObjectPython] Line1611  # Draft 2D object (typed FeaturePython)
  Area = 0
  ChamferSize = 0
  Closed = true
  End = (-335,1400,0)
  FilletRadius = 0
  Length = 4700
  MakeFace = true
  Placement = pos=(-335,7060.93,0) rot=(0,0,1;0rad)
  Points = (2) [(-9.09495e-13,-960.926,0),(-9.09495e-13,-5660.93,0)]
  Start = (-335,6100,0)
  Subdivisions = 0
FEATURE [Part::FeaturePython] Wall335  label="Стена038"  # Arch/BIM 166 (typed FeaturePython)
  Align = 1
  Area = 705000
  Base = -> Line1611
  BlockHeight = 0
  BlockLength = 0
  CountBroken = 0
  CountEntire = 0
  Face = 0
  Height = 150
  HorizontalArea = 705000
  IfcData = attributes={"GlobalId": {"name": "GlobalId", "type": "IfcGloballyUniqueId", "is_enum": false, "enum_values": []}, "Description": {"... (+533 chars omitted),+1 more (map truncated)
  IfcType = 166
  Joint = 0
  Length = 4700
  MakeBlocks = false
  MoveBase = false
  MoveWithHost = false
  Normal = (0,0,0)
  Offset = 50
  OffsetFirst = 0
  OffsetSecond = 0
  PerimeterLength = 9700
  Placement = pos=(0,0,4000) rot=(0,0,1;0rad)
  PredefinedType = 0
  VerticalArea = 1455000
  Width = 150
FEATURE [Part::Part2DObjectPython] Wire900  # Draft 2D object (typed FeaturePython)
  Area = 1.27668e+07
  ChamferSize = 0
  Closed = true
  End = (0,8000,3306.99)
  FilletRadius = 0
  Length = 18965.4
  MakeFace = true
  Placement = pos=(0,-540,3306.99) rot=(0.57735,0.57735,0.57735;2.0944rad)
  Points = (3) [(0,0,0),(4270,2989.89,0),(8540,0,0)]
  Start = (0,-540,3306.99)
  Subdivisions = 0
FEATURE [Part::Extrusion] Extrude099008  label="Extrude099010"
  Base = -> Wire900
  Dir = (1,0,0)
  DirMode = 2
  FaceMakerClass = Part::FaceMakerBullseye
  LengthFwd = 5000
  LengthRev = 0
  Placement = pos=(-2000,0,0) rot=(0,0,1;0rad)
  Solid = false
  Symmetric = false
FEATURE [Part::MultiCommon] Common053  label="Балка фронтона 002"
  Shapes = -> [Wall335,Extrude099008]
FEATURE [Part::FeaturePython] Clone002  label="Балка фронтона 001"  # Draft clone (typed FeaturePython)
  AttacherType = Attacher::AttachEngine3D
  Fuse = false
  Objects = -> [Common053]
  Placement = pos=(12520,7460,0) rot=(0,0,1;3.14159rad)
  Scale = (1,1,1)
FEATURE [Part::MultiFuse] Fusion051  label="Брус подоконный001"
  Shapes = -> [Common053,Clone002]
FEATURE [Part::Cut] Cut058  label="Стропилка вальмы боковые скаты 002"
  Base = -> Common037
  Tool = -> Wall057
FEATURE [Part::Part2DObjectPython] Line1613  # Draft 2D object (typed FeaturePython)
  Area = 0
  ChamferSize = 0
  Closed = false
  End = (3520,3730,0)
  FilletRadius = 0
  Length = 250
  MakeFace = true
  Placement = pos=(3270,3730,0) rot=(0,0,1;0rad)
  Points = (2) [(0,0,0),(250,0,0)]
  Start = (3270,3730,0)
  Subdivisions = 0
FEATURE [Part::FeaturePython] Wall336  label="Кладка под стойки 001"  # Arch/BIM 166 (typed FeaturePython)
  Align = 2
  Area = 42500
  Base = -> Line1613
  BlockHeight = 65
  BlockLength = 250
  CountBroken = 1
  CountEntire = 0
  Face = 0
  Height = 170
  HorizontalArea = 62500
  IfcData = attributes={"GlobalId": {"name": "GlobalId", "type": "IfcGloballyUniqueId", "is_enum": false, "enum_values": []}, "Description": {"... (+533 chars omitted),+1 more (map truncated)
  IfcType = 166
  Joint = 12000
  Length = 250
  MakeBlocks = false
  Material = -> Material019
  MoveBase = false
  MoveWithHost = false
  Normal = (0,0,0)
  OffsetFirst = 120
  OffsetSecond = 200
  PerimeterLength = 1000
  Placement = pos=(0,0,2960) rot=(0,0,1;0rad)
  PredefinedType = 0
  VerticalArea = 170000
  Width = 250
FEATURE [Part::Part2DObjectPython] Line1614  # Draft 2D object (typed FeaturePython)
  Area = 0
  ChamferSize = 0
  Closed = false
  End = (6750,3730,0)
  FilletRadius = 0
  Length = 250
  MakeFace = true
  Placement = pos=(6500,3730,0) rot=(0,0,1;0rad)
  Points = (2) [(0,0,0),(250,0,0)]
  Start = (6500,3730,0)
  Subdivisions = 0
FEATURE [Part::FeaturePython] Wall337  label="Кладка под стойки 002"  # Arch/BIM 166 (typed FeaturePython)
  Align = 2
  Area = 42500
  Base = -> Line1614
  BlockHeight = 65
  BlockLength = 250
  CountBroken = 1
  CountEntire = 0
  Face = 0
  Height = 170
  HorizontalArea = 62500
  IfcData = attributes={"GlobalId": {"name": "GlobalId", "type": "IfcGloballyUniqueId", "is_enum": false, "enum_values": []}, "Description": {"... (+533 chars omitted),+1 more (map truncated)
  IfcType = 166
  Joint = 12000
  Length = 250
  MakeBlocks = false
  Material = -> Material019
  MoveBase = false
  MoveWithHost = false
  Normal = (0,0,0)
  OffsetFirst = 120
  OffsetSecond = 200
  PerimeterLength = 1000
  Placement = pos=(0,0,2960) rot=(0,0,1;0rad)
  PredefinedType = 0
  VerticalArea = 170000
  Width = 250
FEATURE [Part::Part2DObjectPython] Line1615  # Draft 2D object (typed FeaturePython)
  Area = 0
  ChamferSize = 0
  Closed = false
  End = (5490,3730,0)
  FilletRadius = 0
  Length = 250
  MakeFace = true
  Placement = pos=(5240,3730,0) rot=(0,0,1;0rad)
  Points = (2) [(0,0,0),(250,0,0)]
  Start = (5240,3730,0)
  Subdivisions = 0
FEATURE [Part::FeaturePython] Wall338  label="Кладка под стойки 003"  # Arch/BIM 166 (typed FeaturePython)
  Align = 2
  Area = 42500
  Base = -> Line1615
  BlockHeight = 65
  BlockLength = 250
  CountBroken = 1
  CountEntire = 0
  Face = 0
  Height = 170
  HorizontalArea = 62500
  IfcData = attributes={"GlobalId": {"name": "GlobalId", "type": "IfcGloballyUniqueId", "is_enum": false, "enum_values": []}, "Description": {"... (+533 chars omitted),+1 more (map truncated)
  IfcType = 166
  Joint = 12000
  Length = 250
  MakeBlocks = false
  Material = -> Material019
  MoveBase = false
  MoveWithHost = false
  Normal = (0,0,0)
  OffsetFirst = 120
  OffsetSecond = 200
  PerimeterLength = 1000
  Placement = pos=(0,0,2960) rot=(0,0,1;0rad)
  PredefinedType = 0
  VerticalArea = 170000
  Width = 250
FEATURE [Part::Part2DObjectPython] Line1616  # Draft 2D object (typed FeaturePython)
  Area = 0
  ChamferSize = 0
  Closed = false
  End = (9250,3730,0)
  FilletRadius = 0
  Length = 250
  MakeFace = true
  Placement = pos=(9000,3730,0) rot=(0,0,1;0rad)
  Points = (2) [(0,0,0),(250,0,0)]
  Start = (9000,3730,0)
  Subdivisions = 0
FEATURE [Part::FeaturePython] Wall339  label="Кладка под стойки 004"  # Arch/BIM 166 (typed FeaturePython)
  Align = 2
  Area = 42500
  Base = -> Line1616
  BlockHeight = 65
  BlockLength = 250
  CountBroken = 1
  CountEntire = 0
  Face = 0
  Height = 170
  HorizontalArea = 62500
  IfcData = attributes={"GlobalId": {"name": "GlobalId", "type": "IfcGloballyUniqueId", "is_enum": false, "enum_values": []}, "Description": {"... (+533 chars omitted),+1 more (map truncated)
  IfcType = 166
  Joint = 12000
  Length = 250
  MakeBlocks = false
  Material = -> Material019
  MoveBase = false
  MoveWithHost = false
  Normal = (0,0,0)
  OffsetFirst = 120
  OffsetSecond = 200
  PerimeterLength = 1000
  Placement = pos=(0,0,2960) rot=(0,0,1;0rad)
  PredefinedType = 0
  VerticalArea = 170000
  Width = 250
FEATURE [Part::Part2DObjectPython] Wire901  label="Стропильная нога 200х50х6000 001"  # Draft 2D object (typed FeaturePython)
  Area = 1.17137e+06
  ChamferSize = 0
  Closed = true
  End = (0,3730,6552.73)
  FilletRadius = 0
  Length = 12171.8
  MakeFace = true
  Placement = pos=(0,3730,6796.88) rot=(0.57735,0.57735,0.57735;2.0944rad)
  Points = (5) [(0,0,0),(4870,-3410.01,0),(4870,-3496.88,0),(4645.37,-3496.88,0),(0,-244.155,0)]
  Start = (0,3730,6796.88)
  Subdivisions = 0
FEATURE [Part::Extrusion] Extrude099009  label="Extrude099011"
  Base = -> Wire901
  Dir = (1,0,0)
  DirMode = 2
  FaceMakerClass = Part::FaceMakerBullseye
  LengthFwd = 15000
  LengthRev = 0
  Placement = pos=(-1300,0,0) rot=(0,0,1;0rad)
  Solid = false
  Symmetric = false
FEATURE [Part::Mirroring] mirror  label="Extrude099011 (mirrored)"
  Base = (-1300,3730,0)
  Normal = (1e-16,-1,0)
  Source = -> Extrude099009
FEATURE [Part::MultiFuse] Fusion052  label="Объём стропильных ног 6м 001"
  Shapes = -> [Extrude099009,mirror]
FEATURE [Part::Extrusion] Extrude099010  label="Extrude099012"
  Base = -> Wire901
  Dir = (1,0,0)
  DirMode = 2
  FaceMakerClass = Part::FaceMakerBullseye
  LengthFwd = 10000
  LengthRev = 0
  Placement = pos=(7440,-1270,9.09e-13) rot=(0,0,1;1.5708rad)
  Solid = false
  Symmetric = false
FEATURE [Part::Mirroring] mirror001  label="Extrude099012 (mirrored)"
  Base = (6200,11400,0)
  Normal = (-1,1e-16,0)
  Placement = pos=(120,-2.774e-11,0) rot=(0,0,1;0rad)
  Source = -> Extrude099010
FEATURE [Part::MultiFuse] Fusion053  label="Объём стропильных ног 6м 002"
  Shapes = -> [mirror001,Extrude099010]
FEATURE [Part::MultiFuse] Fusion054  label="Накосные стропила 001"
  Shapes = -> [Common041,Common042,Common043,Common040]
FEATURE [Part::MultiCommon] Common055  label="Стропилка вальмы боковые скаты 003"
  Shapes = -> [Fusion052,Cut058]
FEATURE [Part::MultiFuse] Fusion055
  Shapes = -> [Fusion052,Fusion053]
FEATURE [Part::Part2DObjectPython] Line1626  # Draft 2D object (typed FeaturePython)
  Area = 0
  ChamferSize = 0
  Closed = false
  End = (3200,-1930,0)
  FilletRadius = 0
  Length = 2
  MakeFace = true
  Placement = pos=(3198,-1930,0) rot=(0,0,1;0rad)
  Points = (2) [(0,0,0),(2,0,0)]
  Start = (3198,-1930,0)
  Subdivisions = 0
FEATURE [Part::MultiCommon] Common056  label="Накосные стропила001"
  Shapes = -> [Fusion055,Fusion054]
FEATURE [Part::Part2DObjectPython] Rectangle3364  # Draft 2D object (typed FeaturePython)
  Area = 1.119e+07
  ChamferSize = 0
  Columns = 1
  FilletRadius = 0
  Height = 1865
  Length = 6000
  MakeFace = true
  Placement = pos=(3198,-1930,0) rot=(0,0,1;0rad)
  Rows = 1
FEATURE [Part::Part2DObjectPython] Rectangle3365  # Draft 2D object (typed FeaturePython)
  Area = 9.2504e+06
  ChamferSize = 0
  Columns = 1
  FilletRadius = 0
  Height = 1865
  Length = 4960
  MakeFace = true
  Placement = pos=(7007,7525,0) rot=(0,0,1;0rad)
  Rows = 1
FEATURE [Part::Extrusion] Extrude099011  label="Extrude099013"
  Base = -> Rectangle3364
  Dir = (0,0,1)
  DirMode = 2
  FaceMakerClass = Part::FaceMakerBullseye
  LengthFwd = 5000
  LengthRev = 0
  Placement = pos=(0,0,2000) rot=(0,0,1;0rad)
  Solid = false
  Symmetric = false
FEATURE [Part::Extrusion] Extrude099012  label="Extrude099014"
  Base = -> Rectangle3365
  Dir = (0,0,1)
  DirMode = 2
  FaceMakerClass = Part::FaceMakerBullseye
  LengthFwd = 5000
  LengthRev = 0
  Placement = pos=(0,0,2000) rot=(0,0,1;0rad)
  Solid = false
  Symmetric = false
FEATURE [Part::Part2DObjectPython] Rectangle3366  # Draft 2D object (typed FeaturePython)
  Area = 0
  ChamferSize = 0
  Columns = 1
  FilletRadius = 0
  Height = 1130
  Length = 1110
  MakeFace = false
  Placement = pos=(8540,1305,0) rot=(0,0,1;0rad)
  Rows = 1
FEATURE [Part::Extrusion] Extrude099013  label="Extrude099015"
  Base = -> Rectangle3366
  Dir = (0,0,1)
  DirMode = 2
  FaceMakerClass = Part::FaceMakerBullseye
  LengthFwd = 5000
  LengthRev = 0
  Placement = pos=(0,0,2500) rot=(0,0,1;0rad)
  Solid = true
  Symmetric = false
FEATURE [Part::FeaturePython] Wall340  label="Стена039"  # Arch/BIM 166 (typed FeaturePython)
  Align = 0
  Area = 13440000
  Base = -> Rectangle3366
  BlockHeight = 0
  BlockLength = 0
  CountBroken = 0
  CountEntire = 0
  Face = 0
  Height = 3000
  HorizontalArea = 234000
  IfcData = attributes={"GlobalId": {"name": "GlobalId", "type": "IfcGloballyUniqueId", "is_enum": false, "enum_values": []}, "Description": {"... (+533 chars omitted),+1 more (map truncated)
  IfcType = 166
  Joint = 0
  Length = 4480
  MakeBlocks = false
  MoveBase = false
  MoveWithHost = false
  Normal = (0,0,0)
  OffsetFirst = 0
  OffsetSecond = 0
  PerimeterLength = 4880
  Placement = pos=(0,0,4000) rot=(0,0,1;0rad)
  PredefinedType = 0
  VerticalArea = 28080000
  Width = 50
FEATURE [Part::Cut] Cut059  label="Стропилка вальмы боковые скаты 004"
  Base = -> Common055
  Tool = -> Extrude099013
FEATURE [Part::MultiCommon] Common060  label="Проход вентстояка001"
  Shapes = -> [Cut053,Wall340]
FEATURE [Part::Part2DObjectPython] Rectangle3367  # Draft 2D object (typed FeaturePython)
  Area = 15000
  ChamferSize = 0
  Columns = 1
  FilletRadius = 0
  Height = 100
  Length = 150
  MakeFace = true
  Placement = pos=(410.619,455.619,0) rot=(0,0,1;0rad)
  Rows = 1
FEATURE [Part::FeaturePython] Structure446  label="Стойка прогона"  # Arch/BIM 172 (typed FeaturePython)
  Base = -> Rectangle3367
  FaceMaker = 0
  Height = 1050
  HorizontalArea = 15000
  IfcData = attributes={"GlobalId": {"name": "GlobalId", "type": "IfcGloballyUniqueId", "is_enum": false, "enum_values": []}, "Description": {"... (+484 chars omitted),+1 more (map truncated)
  IfcType = 172
  Length = 0
  MoveBase = false
  MoveWithHost = false
  Nodes = (2) [(12780,3730,0),(12780,3730,2100)]
  NodesOffset = 0
  Normal = (0,0,0)
  PerimeterLength = 500
  Placement = pos=(0,0,3100) rot=(0,0,1;0rad)
  PredefinedType = 0
  VerticalArea = 525000
  Width = 100
FEATURE [Part::Part2DObjectPython] Line1646  # Draft 2D object (typed FeaturePython)
  Area = 0
  ChamferSize = 0
  Closed = false
  End = (610.619,505.619,0)
  FilletRadius = 0
  Length = 250
  MakeFace = true
  Placement = pos=(360.619,505.619,0) rot=(0,0,1;0rad)
  Points = (2) [(0,0,0),(250,0,0)]
  Start = (360.619,505.619,0)
  Subdivisions = 0
FEATURE [Part::FeaturePython] Wall341  label="Кладка под стойки 005"  # Arch/BIM 166 (typed FeaturePython)
  Align = 2
  Area = 42500
  Base = -> Line1646
  BlockHeight = 65
  BlockLength = 250
  CountBroken = 1
  CountEntire = 0
  Face = 0
  Height = 170
  HorizontalArea = 62500
  IfcData = attributes={"GlobalId": {"name": "GlobalId", "type": "IfcGloballyUniqueId", "is_enum": false, "enum_values": []}, "Description": {"... (+533 chars omitted),+1 more (map truncated)
  IfcType = 166
  Joint = 12000
  Length = 250
  MakeBlocks = false
  Material = -> Material019
  MoveBase = false
  MoveWithHost = false
  Normal = (0,0,0)
  OffsetFirst = 120
  OffsetSecond = 200
  PerimeterLength = 1000
  Placement = pos=(0,0,2960) rot=(0,0,1;0rad)
  PredefinedType = 0
  VerticalArea = 170000
  Width = 250
FEATURE [Part::FeaturePython] Array066  # Draft array (typed FeaturePython)
  Angle = 360
  ArrayType = 0
  Axis = (0,0,1)
  Base = -> Structure446
  Center = (0,0,0)
  Count = 5
  ExpandArray = false
  Fuse = false
  IntervalAxis = (0,0,0)
  IntervalX = (2880,0,0)
  IntervalY = (0,0,0)
  IntervalZ = (0,0,0)
  NumberCircles = 3
  NumberPolar = 5
  NumberX = 5
  NumberY = 1
  NumberZ = 1
  PlacementList = 5 placements: arithmetic series from (0,0,3100) step (2880,0,0) to (11520,0,3100)
  RadialDistance = 50
  ScaleList = (5) [(1,1,1),(1,1,1),(1,1,1),(1,1,1),(1,1,1)]
  Symmetry = 1
  TangentialDistance = 25
FEATURE [Part::FeaturePython] Array067  # Draft array (typed FeaturePython)
  Angle = 360
  ArrayType = 0
  Axis = (0,0,1)
  Base = -> Wall341
  Center = (0,0,0)
  Count = 5
  ExpandArray = false
  Fuse = false
  IntervalAxis = (0,0,0)
  IntervalX = (2880,0,0)
  IntervalY = (0,100,0)
  IntervalZ = (0,0,100)
  NumberCircles = 3
  NumberPolar = 5
  NumberX = 5
  NumberY = 1
  NumberZ = 1
  PlacementList = 5 placements: arithmetic series from (0,0,2960) step (2880,0,0) to (11520,0,2960)
  RadialDistance = 50
  ScaleList = (5) [(1,1,1),(1,1,1),(1,1,1),(1,1,1),(1,1,1)]
  Symmetry = 1
  TangentialDistance = 25
FEATURE [Part::Part2DObjectPython] Line1650  # Draft 2D object (typed FeaturePython)
  Area = 0
  ChamferSize = 0
  Closed = false
  End = (12080.6,505.619,0)
  FilletRadius = 0
  Length = 11670
  MakeFace = true
  Placement = pos=(410.619,505.619,0) rot=(0,0,1;0rad)
  Points = (2) [(0,0,0),(11670,1.7053e-13,0)]
  Start = (410.619,505.619,0)
  Subdivisions = 0
FEATURE [Part::FeaturePython] Wall342  label="Стена040"  # Arch/BIM 166 (typed FeaturePython)
  Align = 2
  Area = 1750500
  Base = -> Line1650
  BlockHeight = 0
  BlockLength = 0
  CountBroken = 0
  CountEntire = 0
  Face = 0
  Height = 150
  HorizontalArea = 1.167e+06
  IfcData = attributes={"GlobalId": {"name": "GlobalId", "type": "IfcGloballyUniqueId", "is_enum": false, "enum_values": []}, "Description": {"... (+533 chars omitted),+1 more (map truncated)
  IfcType = 166
  Joint = 0
  Length = 11670
  MakeBlocks = false
  Material = -> Material
  MoveBase = false
  MoveWithHost = false
  Normal = (0,0,0)
  OffsetFirst = 0
  OffsetSecond = 0
  PerimeterLength = 23540
  Placement = pos=(0,0,4150) rot=(0,0,1;0rad)
  PredefinedType = 0
  VerticalArea = 3531000
  Width = 100
FEATURE [Part::Mirroring] mirror002  label="Стена040 (mirrored)"
  Base = (3710,3730,0)
  Normal = (-1e-16,-1,0)
  Source = -> Wall342
FEATURE [Part::MultiFuse] Fusion057  label="Прогоны подстропильные002"
  Shapes = -> [Wall342,mirror002]
FEATURE [Part::FeaturePython] Array068  # Draft array (typed FeaturePython)
  Angle = 360
  ArrayType = 0
  Axis = (0,0,1)
  Base = -> Structure446
  Center = (0,0,0)
  Count = 5
  ExpandArray = false
  Fuse = false
  IntervalAxis = (0,0,0)
  IntervalX = (2880,0,0)
  IntervalY = (0,0,0)
  IntervalZ = (0,0,0)
  NumberCircles = 3
  NumberPolar = 5
  NumberX = 5
  NumberY = 1
  NumberZ = 1
  Placement = pos=(0,6448.76,0) rot=(0,0,1;0rad)
  PlacementList = 5 placements: arithmetic series from (0,0,3100) step (2880,0,0) to (11520,0,3100)
  RadialDistance = 50
  ScaleList = (5) [(1,1,1),(1,1,1),(1,1,1),(1,1,1),(1,1,1)]
  Symmetry = 1
  TangentialDistance = 25
FEATURE [Part::FeaturePython] Array069  # Draft array (typed FeaturePython)
  Angle = 360
  ArrayType = 0
  Axis = (0,0,1)
  Base = -> Wall341
  Center = (0,0,0)
  Count = 5
  ExpandArray = false
  Fuse = false
  IntervalAxis = (0,0,0)
  IntervalX = (2880,0,0)
  IntervalY = (0,100,0)
  IntervalZ = (0,0,100)
  NumberCircles = 3
  NumberPolar = 5
  NumberX = 5
  NumberY = 1
  NumberZ = 1
  Placement = pos=(0,6448.76,0) rot=(0,0,1;0rad)
  PlacementList = 5 placements: arithmetic series from (0,0,2960) step (2880,0,0) to (11520,0,2960)
  RadialDistance = 50
  ScaleList = (5) [(1,1,1),(1,1,1),(1,1,1),(1,1,1),(1,1,1)]
  Symmetry = 1
  TangentialDistance = 25
FEATURE [Part::FeaturePython] Component115  label="Кладка под стойки 006"  # Arch/BIM 0 (typed FeaturePython)
  Base = -> Array069
  HorizontalArea = 0
  IfcData = attributes={"GlobalId": {"name": "GlobalId", "type": "IfcGloballyUniqueId", "is_enum": false, "enum_values": []}, "Description": {"... (+538 chars omitted),+1 more (map truncated)
  IfcType = 0
  Material = -> Material019
  MoveBase = false
  MoveWithHost = false
  PerimeterLength = 0
  Placement = pos=(0,6448.76,0) rot=(0,0,1;0rad)
  PredefinedType = 0
  VerticalArea = 0
FEATURE [Part::FeaturePython] Component116  label="Кладка под стойки 007"  # Arch/BIM 0 (typed FeaturePython)
  Base = -> Array067
  HorizontalArea = 0
  IfcData = attributes={"GlobalId": {"name": "GlobalId", "type": "IfcGloballyUniqueId", "is_enum": false, "enum_values": []}, "Description": {"... (+538 chars omitted),+1 more (map truncated)
  IfcType = 0
  Material = -> Material019
  MoveBase = false
  MoveWithHost = false
  PerimeterLength = 0
  PredefinedType = 0
  VerticalArea = 0
FEATURE [Part::Part2DObjectPython] Rectangle3368  # Draft 2D object (typed FeaturePython)
  Area = 22500
  ChamferSize = 0
  Columns = 1
  FilletRadius = 0
  Height = 150
  Length = 150
  MakeFace = true
  Placement = pos=(-335,5740,0) rot=(0,0,1;0rad)
  Rows = 1
FEATURE [Part::FeaturePython] Structure447  label="Стойка фронтона 003"  # Arch/BIM 172 (typed FeaturePython)
  Base = -> Rectangle3368
  FaceMaker = 0
  Height = 1000
  HorizontalArea = 22500
  IfcData = attributes={"GlobalId": {"name": "GlobalId", "type": "IfcGloballyUniqueId", "is_enum": false, "enum_values": []}, "Description": {"... (+484 chars omitted),+1 more (map truncated)
  IfcType = 172
  Length = 0
  Material = -> Material
  MoveBase = false
  MoveWithHost = false
  Nodes = (2) [(-260,3730,0),(-260,3730,2100)]
  NodesOffset = 0
  Normal = (0,0,0)
  PerimeterLength = 600
  Placement = pos=(0,0,3780) rot=(0,0,1;0rad)
  PredefinedType = 0
  VerticalArea = 600000
  Width = 100
FEATURE [Part::Part2DObjectPython] Rectangle3369  # Draft 2D object (typed FeaturePython)
  Area = 22500
  ChamferSize = 0
  Columns = 1
  FilletRadius = 0
  Height = 150
  Length = 150
  MakeFace = true
  Placement = pos=(-335,1565,0) rot=(0,0,1;0rad)
  Rows = 1
FEATURE [Part::FeaturePython] Structure448  label="Стойка фронтона 004"  # Arch/BIM 172 (typed FeaturePython)
  Base = -> Rectangle3369
  FaceMaker = 0
  Height = 1000
  HorizontalArea = 22500
  IfcData = attributes={"GlobalId": {"name": "GlobalId", "type": "IfcGloballyUniqueId", "is_enum": false, "enum_values": []}, "Description": {"... (+484 chars omitted),+1 more (map truncated)
  IfcType = 172
  Length = 0
  Material = -> Material
  MoveBase = false
  MoveWithHost = false
  Nodes = (2) [(-260,3730,0),(-260,3730,2100)]
  NodesOffset = 0
  Normal = (0,0,0)
  PerimeterLength = 600
  Placement = pos=(0,0,3780) rot=(0,0,1;0rad)
  PredefinedType = 0
  VerticalArea = 600000
  Width = 100
FEATURE [Part::Part2DObjectPython] Rectangle3370  # Draft 2D object (typed FeaturePython)
  Area = 22500
  ChamferSize = 0
  Columns = 1
  FilletRadius = 0
  Height = 150
  Length = 150
  MakeFace = true
  Placement = pos=(12705,5740,0) rot=(0,0,1;0rad)
  Rows = 1
FEATURE [Part::FeaturePython] Structure449  label="Стойка фронтона 005"  # Arch/BIM 172 (typed FeaturePython)
  Base = -> Rectangle3370
  FaceMaker = 0
  Height = 1000
  HorizontalArea = 22500
  IfcData = attributes={"GlobalId": {"name": "GlobalId", "type": "IfcGloballyUniqueId", "is_enum": false, "enum_values": []}, "Description": {"... (+484 chars omitted),+1 more (map truncated)
  IfcType = 172
  Length = 0
  Material = -> Material
  MoveBase = false
  MoveWithHost = false
  Nodes = (2) [(-260,3730,0),(-260,3730,2100)]
  NodesOffset = 0
  Normal = (0,0,0)
  PerimeterLength = 600
  Placement = pos=(0,0,3780) rot=(0,0,1;0rad)
  PredefinedType = 0
  VerticalArea = 600000
  Width = 100
FEATURE [Part::Part2DObjectPython] Rectangle3371  # Draft 2D object (typed FeaturePython)
  Area = 22500
  ChamferSize = 0
  Columns = 1
  FilletRadius = 0
  Height = 150
  Length = 150
  MakeFace = true
  Placement = pos=(12705,1565,0) rot=(0,0,1;0rad)
  Rows = 1
FEATURE [Part::FeaturePython] Structure450  label="Стойка фронтона 006"  # Arch/BIM 172 (typed FeaturePython)
  Base = -> Rectangle3371
  FaceMaker = 0
  Height = 1000
  HorizontalArea = 22500
  IfcData = attributes={"GlobalId": {"name": "GlobalId", "type": "IfcGloballyUniqueId", "is_enum": false, "enum_values": []}, "Description": {"... (+484 chars omitted),+1 more (map truncated)
  IfcType = 172
  Length = 0
  Material = -> Material
  MoveBase = false
  MoveWithHost = false
  Nodes = (2) [(-260,3730,0),(-260,3730,2100)]
  NodesOffset = 0
  Normal = (0,0,0)
  PerimeterLength = 600
  Placement = pos=(0,0,3780) rot=(0,0,1;0rad)
  PredefinedType = 0
  VerticalArea = 600000
  Width = 100
FEATURE [App::GeometryPython] BuildingPart111  label="Стойки фронтонов"  # Arch/BIM 172 (typed FeaturePython)
  Area = 0
  Group = -> [Structure444,Structure445,Structure447,Structure448,Structure449,Structure450]
  Height = 0
  HeightPropagate = true
  IfcData = attributes={"GlobalId": {"name": "GlobalId", "type": "IfcGloballyUniqueId", "is_enum": false, "enum_values": []}, "Description": {"... (+484 chars omitted),+1 more (map truncated)
  IfcType = 172
  LevelOffset = 0
  Placement = pos=(0,0,3780) rot=(0,0,1;0rad)
  PredefinedType = 0
FEATURE [Part::Part2DObjectPython] Rectangle3372  # Draft 2D object (typed FeaturePython)
  Area = 28910000
  ChamferSize = 0
  Columns = 1
  FilletRadius = 0
  Height = 5900
  Length = 4900
  MakeFace = true
  Placement = pos=(3800,780,0) rot=(0,0,1;0rad)
  Rows = 1
FEATURE [Part::Extrusion] Extrude099014  label="Extrude099016"
  Base = -> Rectangle3372
  Dir = (0,0,1)
  DirMode = 2
  FaceMakerClass = Part::FaceMakerBullseye
  LengthFwd = 200
  LengthRev = 0
  Placement = pos=(0,0,5880) rot=(0,0,1;0rad)
  Solid = false
  Symmetric = false
FEATURE [Part::FeaturePython] Structure451  label="Балка крыльца 002"  # Arch/BIM 7 (typed FeaturePython)
  FaceMaker = 0
  Height = 100
  HorizontalArea = 0
  IfcData = attributes={"GlobalId": {"name": "GlobalId", "type": "IfcGloballyUniqueId", "is_enum": false, "enum_values": []}, "Description": {"... (+475 chars omitted),+1 more (map truncated)
  IfcType = 7
  Length = 5900
  Material = -> Material
  MoveBase = false
  MoveWithHost = false
  Nodes = (2) [(0,-1.42109e-15,-1.94289e-16),(5900,-1.42109e-15,1.30987e-12)]
  NodesOffset = 0
  Normal = (0,0,0)
  PerimeterLength = 0
  Placement = pos=(3264,-1456.07,2930.06) rot=(1,0,0;0.610865rad)
  PredefinedType = 0
  VerticalArea = 30000
  Width = 150
FEATURE [Part::MultiCommon] Common061
  Shapes = -> [Extrude099011,Array013]
FEATURE [Part::MultiCommon] Common062
  Shapes = -> [Extrude099012,Array013]
FEATURE [Part::MultiCommon] Common063
  Shapes = -> [Extrude099014,Array013]
FEATURE [Part::MultiCommon] Common064
  Shapes = -> [Common063,Roof015]
FEATURE [Part::MultiCommon] Common065
  Shapes = -> [Cut053,Common063]
FEATURE [Part::MultiFuse] Fusion058  label="Затяжки 001"
  Placement = pos=(-50,0,0) rot=(0,0,1;0rad)
  Shapes = -> [Common065,Common064]
FEATURE [Part::MultiCommon] Common066  label="Кобылки навеса 002"
  Placement = pos=(-50,0,0) rot=(0,0,1;0rad)
  Shapes = -> [Cut053,Common061]
FEATURE [Part::MultiCommon] Common067  label="Кобылки навеса 001"
  Placement = pos=(50,0,0) rot=(0,0,1;0rad)
  Shapes = -> [Cut053,Common062]
FEATURE [Part::FeaturePython] Structure452  label="Балка крыльца 001"  # Arch/BIM 7 (typed FeaturePython)
  FaceMaker = 0
  Height = 100
  HorizontalArea = 0
  IfcData = attributes={"GlobalId": {"name": "GlobalId", "type": "IfcGloballyUniqueId", "is_enum": false, "enum_values": []}, "Description": {"... (+475 chars omitted),+1 more (map truncated)
  IfcType = 7
  Length = 4900
  Material = -> Material
  MoveBase = false
  MoveWithHost = false
  Nodes = (2) [(0,-1.42109e-15,-1.94289e-16),(4900,-1.42109e-15,1.08782e-12)]
  NodesOffset = 0
  Normal = (0,0,0)
  PerimeterLength = 0
  Placement = pos=(12025,8916.07,2930.06) rot=(0,0.300706,0.953717;3.14159rad)
  PredefinedType = 0
  VerticalArea = 30000
  Width = 150
FEATURE [App::GeometryPython] BuildingPart101  label="Элементы арх.декора001"  # Arch/BIM 52 (typed FeaturePython)
  Area = 0
  GlobalId = 1dA3$MPA5FehwTwOMwm9Bl
  Group = -> [Structure413,Structure414,Structure415,Structure416,Structure417,Structure420,Component002,Component,Component001,Component003,Structure451,Structure452,Structure424,Structure433]
  Height = 0
  HeightPropagate = true
  IfcData = IfcUID=1dA3$MPA5FehwTwOMwm9Bl,+2 more (map truncated)
  IfcType = 52
  LevelOffset = 0
FEATURE [Part::Part2DObjectPython] Wire902  # Draft 2D object (typed FeaturePython)
  Area = 2.1695e+07
  ChamferSize = 0
  Closed = true
  End = (310,315,0)
  FilletRadius = 0
  Length = 19422
  MakeFace = true
  Placement = pos=(-1160,315,0) rot=(0,0,1;0rad)
  Points = (5) [(0,0,0),(1.59162e-12,6825,0),(1475,6825,0),(4885,3415,0),(1470,-1.36424e-12,0)]
  Start = (-1160,315,0)
  Subdivisions = 0
FEATURE [Part::Extrusion] Extrude099015  label="Extrude099017"
  Base = -> Wire902
  Dir = (0,0,1)
  DirMode = 2
  FaceMakerClass = Part::FaceMakerBullseye
  LengthFwd = 5000
  LengthRev = 0
  Placement = pos=(0,0,2500) rot=(0,0,1;0rad)
  Solid = false
  Symmetric = false
FEATURE [Part::Mirroring] mirror003  label="Extrude099017 (mirrored)"
  Base = (6260,3680,0)
  Normal = (1,0,0)
  Source = -> Extrude099015
FEATURE [Part::MultiFuse] Fusion060
  Shapes = -> [mirror003,Extrude099015]
FEATURE [Part::Part2DObjectPython] Rectangle3377  # Draft 2D object (typed FeaturePython)
  Area = 22500
  ChamferSize = 0
  Columns = 1
  FilletRadius = 0
  Height = 150
  Length = 150
  MakeFace = true
  Placement = pos=(8240,3655,0) rot=(0,0,1;0rad)
  Rows = 1
FEATURE [Part::FeaturePython] Structure457  label="Стойка под конёк 013"  # Arch/BIM 172 (typed FeaturePython)
  Base = -> Rectangle3377
  FaceMaker = 0
  Height = 3220
  HorizontalArea = 22500
  IfcData = attributes={"GlobalId": {"name": "GlobalId", "type": "IfcGloballyUniqueId", "is_enum": false, "enum_values": []}, "Description": {"... (+484 chars omitted),+1 more (map truncated)
  IfcType = 172
  Length = 0
  Material = -> Material
  MoveBase = false
  MoveWithHost = false
  Nodes = (2) [(8315,3730,0),(8315,3730,3220)]
  NodesOffset = 0
  Normal = (0,0,0)
  PerimeterLength = 600
  Placement = pos=(0,0,3130) rot=(0,0,1;0rad)
  PredefinedType = 0
  VerticalArea = 1932000
  Width = 100
FEATURE [App::GeometryPython] BuildingPart112  label="Стойки конька"  # Arch/BIM 172 (typed FeaturePython)
  Area = 0
  Group = -> [Structure440,Structure441,Structure442,Structure443,Structure457]
  Height = 0
  HeightPropagate = true
  IfcData = attributes={"GlobalId": {"name": "GlobalId", "type": "IfcGloballyUniqueId", "is_enum": false, "enum_values": []}, "Description": {"... (+484 chars omitted),+1 more (map truncated)
  IfcType = 172
  LevelOffset = 0
  Placement = pos=(0,0,3130) rot=(0,0,1;0rad)
  PredefinedType = 0
FEATURE [Part::Part2DObjectPython] Line1653  # Draft 2D object (typed FeaturePython)
  Area = 0
  ChamferSize = 0
  Closed = false
  End = (8440,3730,0)
  FilletRadius = 0
  Length = 250
  MakeFace = true
  Placement = pos=(8190,3730,0) rot=(0,0,1;0rad)
  Points = (2) [(0,0,0),(250,0,0)]
  Start = (8190,3730,0)
  Subdivisions = 0
FEATURE [Part::FeaturePython] Wall343  label="Кладка под стойки 008"  # Arch/BIM 166 (typed FeaturePython)
  Align = 2
  Area = 42500
  Base = -> Line1653
  BlockHeight = 65
  BlockLength = 250
  CountBroken = 1
  CountEntire = 0
  Face = 0
  Height = 170
  HorizontalArea = 62500
  IfcData = attributes={"GlobalId": {"name": "GlobalId", "type": "IfcGloballyUniqueId", "is_enum": false, "enum_values": []}, "Description": {"... (+533 chars omitted),+1 more (map truncated)
  IfcType = 166
  Joint = 12000
  Length = 250
  MakeBlocks = false
  Material = -> Material019
  MoveBase = false
  MoveWithHost = false
  Normal = (0,0,0)
  OffsetFirst = 120
  OffsetSecond = 200
  PerimeterLength = 1000
  Placement = pos=(0,0,2960) rot=(0,0,1;0rad)
  PredefinedType = 0
  VerticalArea = 170000
  Width = 250
FEATURE [Part::FeaturePython] Wall054  label="Утепление перекрытия XPS 100mm"  # Arch/BIM 166 (typed FeaturePython)
  Align = 0
  Area = 95281000
  Base = -> Line1077
  BlockHeight = 600
  BlockLength = 1200
  CountBroken = 113
  CountEntire = 88
  Face = 0
  GlobalId = 3kr3_7iVj0bR5GirXoWo2v
  Height = 7550
  HorizontalArea = 0
  IfcData = IfcUID=3kr3_7iVj0bR5GirXoWo2v; attributes={"GlobalId": {"value": "3kr3_7iVj0bR5GirXoWo2v"}}
  IfcType = 166
  Joint = 0
  Length = 12620
  MakeBlocks = false
  Material = -> Material002
  MoveBase = false
  MoveWithHost = false
  Normal = (0,1,0)
  OffsetFirst = 80
  OffsetSecond = 600
  PerimeterLength = 0
  Placement = pos=(0,0,3060) rot=(0,0,1;0rad)
  PredefinedType = 0
  Subtractions = -> [Structure037,Structure360,Structure384,Wall336,Wall337,Wall338,Wall339,Component116,Component115,Wall343]
  VerticalArea = 0
  Width = 100
FEATURE [Part::FeaturePython] Wall098  label="Стяжка пола 50мм"  # Arch/BIM 166 (typed FeaturePython)
  Align = 0
  Area = 95281000
  Base = -> Line1077
  BlockHeight = 0
  BlockLength = 0
  CountBroken = 53
  CountEntire = 111
  Face = 0
  GlobalId = 2jmC5X6fbFRwmp_GUsZLMp
  Height = 7550
  HorizontalArea = 0
  IfcData = IfcUID=2jmC5X6fbFRwmp_GUsZLMp; attributes={"GlobalId": {"value": "2jmC5X6fbFRwmp_GUsZLMp"}}
  IfcType = 166
  Joint = 0
  Length = 12620
  MakeBlocks = false
  Material = -> Material018
  MoveBase = false
  MoveWithHost = false
  Normal = (0,1,0)
  OffsetFirst = 0
  OffsetSecond = 0
  PerimeterLength = 0
  Placement = pos=(0,1.1e-15,3110) rot=(0,0,1;0rad)
  PredefinedType = 0
  Subtractions = -> [Structure037,Structure360,Structure384,Wall336,Wall337,Wall338,Wall339,Component116,Component115,Wall343]
  VerticalArea = 0
  Width = 50
FEATURE [Part::FeaturePython] Wall295  label="Покрытие пола 20мм 001"  # Arch/BIM 166 (typed FeaturePython)
  Align = 0
  Area = 95281000
  Base = -> Line1077
  BlockHeight = 0
  BlockLength = 0
  CountBroken = 53
  CountEntire = 111
  Face = 0
  GlobalId = 3s3if1WDv6dQOvhmOxYeJ$
  Height = 7550
  HorizontalArea = 0
  IfcData = IfcUID=3s3if1WDv6dQOvhmOxYeJ$; attributes={"GlobalId": {"value": "3s3if1WDv6dQOvhmOxYeJ$"}}
  IfcType = 166
  Joint = 0
  Length = 12620
  MakeBlocks = false
  Material = -> Material018
  MoveBase = false
  MoveWithHost = false
  Normal = (0,1,0)
  OffsetFirst = 0
  OffsetSecond = 0
  PerimeterLength = 0
  Placement = pos=(0,1.1e-15,3130) rot=(0,0,1;0rad)
  PredefinedType = 0
  Subtractions = -> [Structure037,Structure360,Structure384,Wall336,Wall337,Wall339,Wall338,Component116,Component115,Wall343]
  VerticalArea = 0
  Width = 20
FEATURE [App::GeometryPython] BuildingPart099  label="Пол мансарды"  # Arch/BIM 52 (typed FeaturePython)
  Area = 285843000
  GlobalId = 0Uv4k6v0XBk8Mx6e_8kGVf
  Group = -> [Wall098,Wall054,Wall295]
  Height = 0
  HeightPropagate = true
  IfcData = IfcUID=0Uv4k6v0XBk8Mx6e_8kGVf,+2 more (map truncated)
  IfcType = 52
  LevelOffset = 0
FEATURE [App::GeometryPython] BuildingPart110  label="Кладка под стойки"  # Arch/BIM 172 (typed FeaturePython)
  Area = 212500
  Group = -> [Wall336,Wall337,Wall338,Wall339,Component116,Component115,Wall343]
  Height = 170
  HeightPropagate = true
  IfcData = attributes={"GlobalId": {"name": "GlobalId", "type": "IfcGloballyUniqueId", "is_enum": false, "enum_values": []}, "Description": {"... (+484 chars omitted),+1 more (map truncated)
  IfcType = 172
  LevelOffset = 0
  Placement = pos=(0,0,2960) rot=(0,0,1;0rad)
  PredefinedType = 0
FEATURE [App::GeometryPython] BuildingPart016  label="Конструкции перекрытия"  # Arch/BIM 52 (typed FeaturePython)
  Area = 349251280
  GlobalId = 3lFo00xcPACR0FdWtYITp1
  Group = -> [BuildingPart006,Wall164,BuildingPart040,BuildingPart082,Wall248,Wall249,BuildingPart097,BuildingPart099,BuildingPart110]
  Height = 0
  HeightPropagate = true
  IfcData = IfcUID=3lFo00xcPACR0FdWtYITp1,attributes={"GlobalId": {"value": "3lFo00xcPACR0FdWtYITp1"}},+1 more (map truncated)
  IfcType = 52
  LevelOffset = 0
FEATURE [Part::Cut] Cut060  label="Стропилка вальмы боковые скаты 005"
  Base = -> Cut059
  Tool = -> Fusion057
FEATURE [Part::Cut] Cut061  label="Кобылки навеса 003"
  Base = -> Common066
  Tool = -> Structure451
FEATURE [Part::Cut] Cut062  label="Кобылки навеса 004"
  Base = -> Common067
  Tool = -> Structure452
FEATURE [Part::Cut] Cut065  label="Стропилка вальмы боковые скаты 006"
  Base = -> Cut060
  Tool = -> Wall334
FEATURE [Part::Cut] Cut066  label="Стропилка вальмы боковые скаты001"
  Base = -> Cut065
  Tool = -> Common056
FEATURE [Part::MultiFuse] Fusion061  label="Конёк кукушки 003"
  Shapes = -> [Wall331,Wall333]
FEATURE [Part::Cut] Cut068  label="Стропилка кукушек002"
  Base = -> Common050
  Tool = -> Fusion061
FEATURE [Part::Part2DObjectPython] Wire903  # Draft 2D object (typed FeaturePython)
  Area = 9.7405e+06
  ChamferSize = 0
  Closed = true
  End = (215.926,940,0)
  FilletRadius = 0
  Length = 14166.1
  MakeFace = true
  Placement = pos=(-135,940,0) rot=(0,0,1;0rad)
  Points = (5) [(0,0,0),(7.95808e-13,5575,0),(355.926,5575,0),(3140.93,2790,0),(350.926,-6.34373e-11,0)]
  Start = (-135,940,0)
  Subdivisions = 0
FEATURE [Part::Extrusion] Extrude099007  label="Extrude099008"
  Base = -> Wire903
  Dir = (0,0,1)
  DirMode = 2
  FaceMakerClass = Part::FaceMakerBullseye
  LengthFwd = 5000
  LengthRev = 0
  Placement = pos=(0,0,2500) rot=(0,0,1;0rad)
  Solid = false
  Symmetric = false
FEATURE [Part::FeaturePython] Clone001  label="Extrude099009"  # Draft clone (typed FeaturePython)
  AttacherType = Attacher::AttachEngine3D
  Fuse = false
  Objects = -> [Extrude099007]
  Placement = pos=(12520,7460,2500) rot=(0,0,1;3.14159rad)
  Scale = (1,1,1)
FEATURE [Part::MultiFuse] Fusion049
  Shapes = -> [Extrude099007,Clone001]
FEATURE [Part::Cut] Cut055  label="Стропилка вальмы скаты с кукушками 001"
  Base = -> Common052
  Tool = -> Fusion049
FEATURE [Part::Cut] Cut056  label="Стропилка вальмы скаты с кукушками 002"
  Base = -> Cut055
  Tool = -> Fusion051
FEATURE [Part::Cut] Cut057  label="Стропилка вальмы скаты с кукушками 003"
  Base = -> Cut056
  Tool = -> Wall057
FEATURE [Part::MultiCommon] Common054  label="Стропилка вальмы скаты с кукушками 004"
  Shapes = -> [Fusion053,Cut057]
FEATURE [Part::Cut] Cut067  label="Стропилка вальмы скаты с кукушками 006"
  Base = -> Common054
  Tool = -> Common056
FEATURE [Part::Part2DObjectPython] Rectangle3384  label="h2,5м площадь (к=1.0) 001"  # Draft 2D object (typed FeaturePython)
  Area = 3.31556e+07
  ChamferSize = 0
  Columns = 1
  FilletRadius = 0
  Height = 2635.58
  Length = 12580
  MakeFace = true
  Placement = pos=(-30,2412.21,0) rot=(0,0,1;0rad)
  Rows = 1
FEATURE [Part::Part2DObjectPython] Rectangle3385  label="h1,6м площадь (к=0.7) 002"  # Draft 2D object (typed FeaturePython)
  Area = 1.61695e+07
  ChamferSize = 0
  Columns = 1
  FilletRadius = 0
  Height = 1285.33
  Length = 12580
  MakeFace = true
  Placement = pos=(-30,1126.88,0) rot=(0,0,1;0rad)
  Rows = 1
FEATURE [Part::Part2DObjectPython] Rectangle3386  label="h1,6м площадь (к=0.7) 001"  # Draft 2D object (typed FeaturePython)
  Area = 1.61695e+07
  ChamferSize = 0
  Columns = 1
  FilletRadius = 0
  Height = 1285.33
  Length = 12580
  MakeFace = true
  Placement = pos=(-30,5047.79,0) rot=(0,0,1;0rad)
  Rows = 1
FEATURE [Part::Part2DObjectPython] Rectangle3387  label="Вычитаемая площадь проёма"  # Draft 2D object (typed FeaturePython)
  Area = 2.5801e+06
  ChamferSize = 0
  Columns = 1
  FilletRadius = 0
  Height = 2529.51
  Length = 1020
  MakeFace = true
  Placement = pos=(6900,3803.61,0) rot=(0,0,1;0rad)
  Rows = 1
FEATURE [Part::Part2DObjectPython] Wire904  # Draft 2D object (typed FeaturePython)
  Area = 123740
  ChamferSize = 0
  Closed = true
  End = (1250,0,4150)
  FilletRadius = 0
  Length = 2074.13
  MakeFace = true
  Placement = pos=(560.619,0,3460.62) rot=(1,0,0;1.5708rad)
  Points = (4) [(0,0,0),(0,212.132,4.71028e-14),(477.249,689.381,1.38462e-13),(689.381,689.381,1.31967e-13)]
  Start = (560.619,0,3460.62)
  Subdivisions = 0
FEATURE [Part::Extrusion] Extrude099016  label="Extrude099018"
  Base = -> Wire904
  Dir = (0,-1,2e-16)
  DirMode = 2
  FaceMakerClass = Part::FaceMakerBullseye
  LengthFwd = 100
  LengthRev = 0
  Placement = pos=(0,555.619,0) rot=(0,0,1;0rad)
  Solid = false
  Symmetric = false
FEATURE [Part::Mirroring] mirror007  label="Extrude099018 (mirrored)"
  Base = (410.619,555.619,0)
  Normal = (-1,0,0)
  Placement = pos=(11670,6.821e-13,0) rot=(0,0,1;0rad)
  Source = -> Extrude099016
FEATURE [Part::FeaturePython] Array070  # Draft array (typed FeaturePython)
  Angle = 360
  ArrayType = 0
  Axis = (0,0,1)
  Base = -> Extrude099016
  Center = (0,0,0)
  Count = 4
  ExpandArray = false
  Fuse = false
  IntervalAxis = (0,0,0)
  IntervalX = (2880,0,0)
  IntervalY = (0,100,0)
  IntervalZ = (0,0,100)
  NumberCircles = 3
  NumberPolar = 5
  NumberX = 4
  NumberY = 1
  NumberZ = 1
  PlacementList = 4 placements: arithmetic series from (0,555.619,0) step (2880,0,0) to (8640,555.619,0)
  RadialDistance = 50
  ScaleList = (4) [(1,1,1),(1,1,1),(1,1,1),(1,1,1)]
  Symmetry = 1
  TangentialDistance = 25
FEATURE [Part::FeaturePython] Array071  # Draft array (typed FeaturePython)
  Angle = 360
  ArrayType = 0
  Axis = (0,0,1)
  Base = -> mirror007
  Center = (0,0,0)
  Count = 4
  ExpandArray = false
  Fuse = false
  IntervalAxis = (0,0,0)
  IntervalX = (-2880,0,0)
  IntervalY = (0,100,0)
  IntervalZ = (0,0,100)
  NumberCircles = 3
  NumberPolar = 5
  NumberX = 4
  NumberY = 1
  NumberZ = 1
  PlacementList = 4 placements: arithmetic series from (11670,6.82121e-13,0) step (-2880,0,0) to (3030,6.82121e-13,0)
  RadialDistance = 50
  ScaleList = (4) [(1,1,1),(1,1,1),(1,1,1),(1,1,1)]
  Symmetry = 1
  TangentialDistance = 25
FEATURE [Part::MultiFuse] Fusion062
  Shapes = -> [Array070,Array071]
FEATURE [Part::FeaturePython] Clone003  label="Fusion063"  # Draft clone (typed FeaturePython)
  AttacherType = Attacher::AttachEngine3D
  Fuse = false
  Objects = -> [Fusion062]
  Placement = pos=(0,6448.76,0) rot=(0,0,1;0rad)
  Scale = (1,1,1)
FEATURE [Part::MultiFuse] Fusion063  label="Стойки подстропильные (подкосы)"
  Shapes = -> [Fusion062,Clone003]
FEATURE [Part::MultiFuse] Fusion064
  Shapes = -> [Array066,Array068]
FEATURE [Part::MultiFuse] Fusion065
  Shapes = -> [Fusion064,Fusion063]
FEATURE [Part::MultiFuse] Fusion066  label="Прогоны подстропильные 001"
  Shapes = -> [Fusion057,Fusion065]
FEATURE [Part::Part2DObjectPython] Rectangle3388  # Draft 2D object (typed FeaturePython)
  Area = 2640000
  ChamferSize = 0
  Columns = 1
  FilletRadius = 0
  Height = 1200
  Length = 2200
  MakeFace = true
  Placement = pos=(100,3100,0) rot=(0,0,1;0rad)
  Rows = 1
FEATURE [Part::Extrusion] Extrude099017  label="Extrude099019"
  Base = -> Rectangle3388
  Dir = (0,0,1)
  DirMode = 2
  FaceMakerClass = Part::FaceMakerBullseye
  LengthFwd = 300
  LengthRev = 0
  Placement = pos=(0,0,6050) rot=(0,0,1;0rad)
  Solid = false
  Symmetric = false
FEATURE [Part::MultiCommon] Common069
  Shapes = -> [Cut054,Extrude099017]
FEATURE [Part::MultiCommon] Common070
  Placement = pos=(-50,0,0) rot=(0,0,1;0rad)
  Shapes = -> [Array013,Common069]
FEATURE [Part::FeaturePython] Clone004  label="Common071"  # Draft clone (typed FeaturePython)
  AttacherType = Attacher::AttachEngine3D
  Fuse = false
  Objects = -> [Common070]
  Placement = pos=(10130,4.55e-13,0) rot=(0,0,1;0rad)
  Scale = (1,1,1)
FEATURE [Part::MultiFuse] Fusion067  label="Накладки стропил кукушек001"
  Shapes = -> [Common070,Clone004]
FEATURE [Part::Extrusion] Extrude099018  label="Extrude099020"
  Base = -> Rectangle3372
  Dir = (0,0,1)
  DirMode = 2
  FaceMakerClass = Part::FaceMakerBullseye
  LengthFwd = 300
  LengthRev = 0
  Placement = pos=(0,0,6550) rot=(0,0,1;0rad)
  Solid = false
  Symmetric = false
FEATURE [Part::MultiCommon] Common071  label="Common072"
  Shapes = -> [Cut053,Extrude099018]
FEATURE [Part::MultiCommon] Common072  label="Накладки стропил 001"
  Placement = pos=(-50,0,0) rot=(0,0,1;0rad)
  Shapes = -> [Array013,Common071]
FEATURE [Part::MultiFuse] Fusion068
  Shapes = -> [Common046,Common047]
FEATURE [Part::MultiFuse] Fusion069
  Shapes = -> [Common048,Common049]
FEATURE [Part::MultiFuse] Fusion070
  Shapes = -> [Fusion068,Fusion069]
FEATURE [Part::MultiCommon] Common073  label="Накосные стропила кукушки 001"
  Shapes = -> [Fusion060,Fusion070]
FEATURE [Part::Cut] Cut069  label="Стропилка вальмы скаты с кукушками 007"
  Base = -> Cut067
  Tool = -> Common073
FEATURE [Part::FeaturePython] Component117  label="Накосные стропила кукушки"  # Arch/BIM 0 (typed FeaturePython)
  Base = -> Common073
  HorizontalArea = 0
  IfcData = attributes={"GlobalId": {"name": "GlobalId", "type": "IfcGloballyUniqueId", "is_enum": false, "enum_values": []}, "Description": {"... (+538 chars omitted),+1 more (map truncated)
  IfcType = 0
  Material = -> Material
  MoveBase = false
  MoveWithHost = false
  PerimeterLength = 0
  PredefinedType = 0
  VerticalArea = 0
FEATURE [Part::FeaturePython] Component118  label="Стропилка вальмы скаты с кукушками"  # Arch/BIM 0 (typed FeaturePython)
  Base = -> Cut069
  HorizontalArea = 0
  IfcData = attributes={"GlobalId": {"name": "GlobalId", "type": "IfcGloballyUniqueId", "is_enum": false, "enum_values": []}, "Description": {"... (+538 chars omitted),+1 more (map truncated)
  IfcType = 0
  Material = -> Material
  MoveBase = false
  MoveWithHost = false
  PerimeterLength = 0
  PredefinedType = 0
  VerticalArea = 0
FEATURE [Part::FeaturePython] Component119  label="Накладки стропил"  # Arch/BIM 0 (typed FeaturePython)
  Base = -> Common072
  HorizontalArea = 0
  IfcData = attributes={"GlobalId": {"name": "GlobalId", "type": "IfcGloballyUniqueId", "is_enum": false, "enum_values": []}, "Description": {"... (+538 chars omitted),+1 more (map truncated)
  IfcType = 0
  Material = -> Material
  MoveBase = false
  MoveWithHost = false
  PerimeterLength = 0
  Placement = pos=(-50,0,0) rot=(0,0,1;0rad)
  PredefinedType = 0
  VerticalArea = 0
FEATURE [Part::FeaturePython] Component120  label="Затяжки"  # Arch/BIM 0 (typed FeaturePython)
  Base = -> Fusion058
  HorizontalArea = 0
  IfcData = attributes={"GlobalId": {"name": "GlobalId", "type": "IfcGloballyUniqueId", "is_enum": false, "enum_values": []}, "Description": {"... (+538 chars omitted),+1 more (map truncated)
  IfcType = 0
  Material = -> Material
  MoveBase = false
  MoveWithHost = false
  PerimeterLength = 0
  Placement = pos=(-50,0,0) rot=(0,0,1;0rad)
  PredefinedType = 0
  VerticalArea = 0
FEATURE [Part::FeaturePython] Component121  label="Кобылки навеса св."  # Arch/BIM 0 (typed FeaturePython)
  Base = -> Cut061
  HorizontalArea = 0
  IfcData = attributes={"GlobalId": {"name": "GlobalId", "type": "IfcGloballyUniqueId", "is_enum": false, "enum_values": []}, "Description": {"... (+538 chars omitted),+1 more (map truncated)
  IfcType = 0
  Material = -> Material
  MoveBase = false
  MoveWithHost = false
  PerimeterLength = 0
  PredefinedType = 0
  VerticalArea = 0
FEATURE [Part::FeaturePython] Component122  label="Кобылки навеса юг."  # Arch/BIM 0 (typed FeaturePython)
  Base = -> Cut062
  HorizontalArea = 0
  IfcData = attributes={"GlobalId": {"name": "GlobalId", "type": "IfcGloballyUniqueId", "is_enum": false, "enum_values": []}, "Description": {"... (+538 chars omitted),+1 more (map truncated)
  IfcType = 0
  Material = -> Material
  MoveBase = false
  MoveWithHost = false
  PerimeterLength = 0
  PredefinedType = 0
  VerticalArea = 0
FEATURE [Part::FeaturePython] Component123  label="Конёк кукушки"  # Arch/BIM 0 (typed FeaturePython)
  Base = -> Fusion061
  HorizontalArea = 0
  IfcData = attributes={"GlobalId": {"name": "GlobalId", "type": "IfcGloballyUniqueId", "is_enum": false, "enum_values": []}, "Description": {"... (+538 chars omitted),+1 more (map truncated)
  IfcType = 0
  Material = -> Material
  MoveBase = false
  MoveWithHost = false
  PerimeterLength = 0
  PredefinedType = 0
  VerticalArea = 0
FEATURE [Part::FeaturePython] Component124  label="Стропилка кукушек"  # Arch/BIM 0 (typed FeaturePython)
  Base = -> Cut068
  HorizontalArea = 0
  IfcData = attributes={"GlobalId": {"name": "GlobalId", "type": "IfcGloballyUniqueId", "is_enum": false, "enum_values": []}, "Description": {"... (+538 chars omitted),+1 more (map truncated)
  IfcType = 0
  Material = -> Material
  MoveBase = false
  MoveWithHost = false
  PerimeterLength = 0
  PredefinedType = 0
  VerticalArea = 0
FEATURE [Part::FeaturePython] Component125  label="Стропилка вальмы боковые скаты"  # Arch/BIM 0 (typed FeaturePython)
  Base = -> Cut066
  HorizontalArea = 0
  IfcData = attributes={"GlobalId": {"name": "GlobalId", "type": "IfcGloballyUniqueId", "is_enum": false, "enum_values": []}, "Description": {"... (+538 chars omitted),+1 more (map truncated)
  IfcType = 0
  Material = -> Material
  MoveBase = false
  MoveWithHost = false
  PerimeterLength = 0
  PredefinedType = 0
  VerticalArea = 0
FEATURE [Part::FeaturePython] Component126  label="Прогоны подстропильные"  # Arch/BIM 0 (typed FeaturePython)
  Base = -> Fusion066
  HorizontalArea = 0
  IfcData = attributes={"GlobalId": {"name": "GlobalId", "type": "IfcGloballyUniqueId", "is_enum": false, "enum_values": []}, "Description": {"... (+538 chars omitted),+1 more (map truncated)
  IfcType = 0
  Material = -> Material
  MoveBase = false
  MoveWithHost = false
  PerimeterLength = 0
  PredefinedType = 0
  VerticalArea = 0
FEATURE [Part::FeaturePython] Component127  label="Накладки стропил кукушек"  # Arch/BIM 0 (typed FeaturePython)
  Base = -> Fusion067
  HorizontalArea = 0
  IfcData = attributes={"GlobalId": {"name": "GlobalId", "type": "IfcGloballyUniqueId", "is_enum": false, "enum_values": []}, "Description": {"... (+538 chars omitted),+1 more (map truncated)
  IfcType = 0
  Material = -> Material
  MoveBase = false
  MoveWithHost = false
  PerimeterLength = 0
  PredefinedType = 0
  VerticalArea = 0
FEATURE [Part::FeaturePython] Component128  label="Брус подоконный"  # Arch/BIM 0 (typed FeaturePython)
  Base = -> Fusion051
  HorizontalArea = 0
  IfcData = attributes={"GlobalId": {"name": "GlobalId", "type": "IfcGloballyUniqueId", "is_enum": false, "enum_values": []}, "Description": {"... (+538 chars omitted),+1 more (map truncated)
  IfcType = 0
  Material = -> Material
  MoveBase = false
  MoveWithHost = false
  PerimeterLength = 0
  PredefinedType = 0
  VerticalArea = 0
FEATURE [Part::FeaturePython] Component129  label="Проход вентстояка"  # Arch/BIM 0 (typed FeaturePython)
  Base = -> Common060
  HorizontalArea = 0
  IfcData = attributes={"GlobalId": {"name": "GlobalId", "type": "IfcGloballyUniqueId", "is_enum": false, "enum_values": []}, "Description": {"... (+538 chars omitted),+1 more (map truncated)
  IfcType = 0
  Material = -> Material
  MoveBase = false
  MoveWithHost = false
  PerimeterLength = 0
  PredefinedType = 0
  VerticalArea = 0
FEATURE [Part::FeaturePython] Component130  label="Накосные стропила"  # Arch/BIM 0 (typed FeaturePython)
  Base = -> Common056
  HorizontalArea = 0
  IfcData = attributes={"GlobalId": {"name": "GlobalId", "type": "IfcGloballyUniqueId", "is_enum": false, "enum_values": []}, "Description": {"... (+538 chars omitted),+1 more (map truncated)
  IfcType = 0
  Material = -> Material
  MoveBase = false
  MoveWithHost = false
  PerimeterLength = 0
  PredefinedType = 0
  VerticalArea = 0
FEATURE [App::GeometryPython] BuildingPart109  label="Стропильная система кровли"  # Arch/BIM 172 (typed FeaturePython)
  Area = 0
  Group = -> [Component117,Component118,Component119,Component120,Component121,Component122,Component124,Component125,Component127,Component128,Component129,Component130]
  Height = 0
  HeightPropagate = true
  IfcData = attributes={"GlobalId": {"name": "GlobalId", "type": "IfcGloballyUniqueId", "is_enum": false, "enum_values": []}, "Description": {"... (+484 chars omitted),+1 more (map truncated)
  IfcType = 172
  LevelOffset = 0
  Placement = pos=(0,0,3630) rot=(0,0,1;0rad)
  PredefinedType = 0
FEATURE [App::GeometryPython] BuildingPart113  label="Стойки и прогоны"  # Arch/BIM 172 (typed FeaturePython)
  Area = 7203000
  Group = -> [Wall334,Wall057,BuildingPart112,BuildingPart111,Component123,Component126]
  Height = 0
  HeightPropagate = true
  IfcData = attributes={"GlobalId": {"name": "GlobalId", "type": "IfcGloballyUniqueId", "is_enum": false, "enum_values": []}, "Description": {"... (+484 chars omitted),+1 more (map truncated)
  IfcType = 172
  LevelOffset = 0
  PredefinedType = 0
FEATURE [Part::Compound] Compound  label="Оси001"
  Links = -> [Axis001006,Axis001007]
FEATURE [Part::Compound] Compound005  label="Roof003"
  Links = -> [Wire817,Line1497,Line1500,Line1502,Line1503,Line1501,Line1507,Line1506,Line1498,Line1504,Line1505,Line1499]
FEATURE [TechDraw::DrawViewDraft] DraftView001
  Direction = (0,0,1)
  FontSize = 12
  LineSpacing = 1
  LineStyle = Solid
  LineWidth = 0.1
  LockPosition = true
  OverrideStyle = false
  Rotation = 0
  Scale = 0.02
  ScaleType = 2
  Source = -> Compound005
  Symbol = <blob: 3309 chars omitted>
  X = 209.065
  Y = 144.442
FEATURE [TechDraw::DrawSVGTemplate] Template003
  EditableTexts = Лист=5; Номер=ИЖС-2021.0001
  Height = 297
  Orientation = 1
  Width = 420
FEATURE [TechDraw::DrawViewAnnotation] Annotation031
  Font = osifont
  LineSpace = 80
  LockPosition = false
  MaxWidth = -1
  Rotation = 0
  ScaleType = 0
  Text = \u041f\u043b\u0430\u043d \u043c\u0430\u043d\u0441\u0430\u0440\u0434\u043d\u043e\u0433\u043e \u044d\u0442\u0430\u0436\u0430 \u043d\u0430 \u043e\u0442\u043c\u0435\u0442\u043a\u0435 +3.13
  TextSize = 6
  TextStyle = 0
  X = 218.387
  Y = 275.093
FEATURE [Part::Part2DObjectPython] Rectangle3398  # Draft 2D object (typed FeaturePython)
  Area = 0
  ChamferSize = 0
  Columns = 1
  FilletRadius = 0
  Height = 8000
  Length = 7000
  MakeFace = false
  Placement = pos=(22359,-9231.91,0) rot=(0,0,1;1.34139rad)
  Rows = 1
FEATURE [Part::FeaturePython] Structure437  label="Парковка"  # Arch/BIM 118 (typed FeaturePython)
  Base = -> Rectangle3398
  FaceMaker = 0
  Height = 200
  HorizontalArea = 5.6e+07
  IfcData = attributes={"GlobalId": {"name": "GlobalId", "type": "IfcGloballyUniqueId", "is_enum": false, "enum_values": []}, "Description": {"... (+453 chars omitted),+1 more (map truncated)
  IfcType = 118
  Length = 7000
  MoveBase = false
  MoveWithHost = false
  Nodes = (4) [(19575,-8688.32,0),(20865.3,-2828.71,0),(14029.1,-1323.35,0),(12738.8,-7182.97,0)]
  NodesOffset = 0
  Normal = (0,0,-1)
  PerimeterLength = 30000
  Placement = pos=(0,0,-300) rot=(0,0,1;0rad)
  PredefinedType = 0
  VerticalArea = 6e+06
  Width = 6500
FEATURE [Part::Part2DObjectPython] Rectangle3402  # Draft 2D object (typed FeaturePython)
  Area = 1.38e+07
  ChamferSize = 0
  Columns = 1
  FilletRadius = 0
  Height = 2300
  Length = 6000
  MakeFace = true
  Placement = pos=(-6950.03,-7631.87,0) rot=(0,0,1;0.175714rad)
  Rows = 1
FEATURE [Part::Part2DObjectPython] Line1707  # Draft 2D object (typed FeaturePython)
  Area = 0
  ChamferSize = 0
  Closed = false
  End = (24359.1,-3994.32,0)
  FilletRadius = 0
  Length = 5200
  MakeFace = true
  Placement = pos=(24127,-9189.13,0) rot=(0,0,-1;1.61546rad)
  Points = (2) [(0,0,0),(-5200,-3.63798e-11,0)]
  Start = (24127,-9189.13,0)
  Subdivisions = 0
FEATURE [Part::FeaturePython] Wall315  label="Створка ворот 4.7м"  # Arch/BIM 166 (typed FeaturePython)
  Align = 0
  Area = 9.36e+06
  Base = -> Line1707
  BlockHeight = 2000
  BlockLength = 150
  CountBroken = 33
  CountEntire = 0
  Face = 0
  Height = 1800
  HorizontalArea = 0
  IfcData = attributes={"GlobalId": {"name": "GlobalId", "type": "IfcGloballyUniqueId", "is_enum": false, "enum_values": []}, "Description": {"... (+533 chars omitted),+1 more (map truncated)
  IfcType = 166
  Joint = 10
  Length = 5200
  MakeBlocks = true
  Material = -> Material010
  MoveBase = false
  MoveWithHost = false
  Normal = (0,0,0)
  Offset = 125
  OffsetFirst = 100
  OffsetSecond = 0
  PerimeterLength = 0
  Placement = pos=(-290,1.3642e-12,-120) rot=(0,0,1;0rad)
  PredefinedType = 0
  VerticalArea = 0
  Width = 50
FEATURE [Part::Part2DObjectPython] Line1708  # Draft 2D object (typed FeaturePython)
  Area = 0
  ChamferSize = 0
  Closed = false
  End = (24454.5,-4098.68,0)
  FilletRadius = 0
  Length = 5000
  MakeFace = true
  Placement = pos=(24231.3,-9093.7,0) rot=(0,0,-1;0.04466rad)
  Points = (2) [(0,0,0),(-1.81899e-11,5000,0)]
  Start = (24231.3,-9093.7,0)
  Subdivisions = 0
FEATURE [Part::FeaturePython] Wall314  label="Проём ворот 5м"  # Arch/BIM 166 (typed FeaturePython)
  Align = 0
  Area = 1e+07
  Base = -> Line1708
  BlockHeight = 0
  BlockLength = 0
  CountBroken = 0
  CountEntire = 0
  Face = 0
  Height = 2000
  HorizontalArea = 1e+06
  IfcData = attributes={"GlobalId": {"name": "GlobalId", "type": "IfcGloballyUniqueId", "is_enum": false, "enum_values": []}, "Description": {"... (+533 chars omitted),+1 more (map truncated)
  IfcType = 166
  Joint = 0
  Length = 5000
  MakeBlocks = false
  MoveBase = false
  MoveWithHost = false
  Normal = (0,0,0)
  Offset = 100
  OffsetFirst = 0
  OffsetSecond = 0
  PerimeterLength = 10400
  Placement = pos=(0,0,-320) rot=(0,0,1;0rad)
  PredefinedType = 0
  VerticalArea = 2.08e+07
  Width = 200
FEATURE [Part::FeaturePython] Space  label="Проём ворот"  # Arch/BIM 122 (typed FeaturePython)
  Area = 1e+06
  AutoPower = false
  Base = -> Wall314
  CompositionType = 0
  Conditioning = 0
  ElevationWithFlooring = -320
  EquipmentPower = 0
  FloorThickness = 0
  HorizontalArea = 1e+06
  IfcData = attributes={"GlobalId": {"name": "GlobalId", "type": "IfcGloballyUniqueId", "is_enum": false, "enum_values": []}, "Description": {"... (+888 chars omitted),+1 more (map truncated)
  IfcType = 122
  Internal = true
  LightingPower = 0
  LongName = Space
  MoveBase = false
  MoveWithHost = false
  NumberOfPeople = 0
  PerimeterLength = 10400
  Placement = pos=(-490,0,0) rot=(0,0,1;0rad)
  PredefinedType = 0
  SpaceType = 0
  VerticalArea = 2.08e+07
  expr: ElevationWithFlooring = .Shape.BoundBox.ZMin
FEATURE [Part::Part2DObjectPython] Line1709  # Draft 2D object (typed FeaturePython)
  Area = 0
  ChamferSize = 0
  Closed = false
  End = (24811.7,3893.34,0)
  FilletRadius = 0
  Length = 8000
  MakeFace = true
  Placement = pos=(24454.5,-4098.68,0) rot=(0,0,-1;0.04466rad)
  Points = (2) [(0,0,0),(9.82254e-11,8000,0)]
  Start = (24454.5,-4098.68,0)
  Subdivisions = 0
FEATURE [Part::FeaturePython] Wall313  label="Зона отката ворот 7.5м"  # Arch/BIM 166 (typed FeaturePython)
  Align = 0
  Area = 1.6e+07
  Base = -> Line1709
  BlockHeight = 0
  BlockLength = 0
  CountBroken = 0
  CountEntire = 0
  Face = 0
  Height = 2000
  HorizontalArea = 1.6e+06
  IfcData = attributes={"GlobalId": {"name": "GlobalId", "type": "IfcGloballyUniqueId", "is_enum": false, "enum_values": []}, "Description": {"... (+533 chars omitted),+1 more (map truncated)
  IfcType = 166
  Joint = 0
  Length = 8000
  MakeBlocks = false
  MoveBase = false
  MoveWithHost = false
  Normal = (0,0,0)
  Offset = 100
  OffsetFirst = 0
  OffsetSecond = 0
  PerimeterLength = 16400
  Placement = pos=(0,0,-320) rot=(0,0,1;0rad)
  PredefinedType = 0
  VerticalArea = 3.28e+07
  Width = 200
FEATURE [Part::FeaturePython] Space001  label="Зона отката ворот "  # Arch/BIM 122 (typed FeaturePython)
  Area = 1.6e+06
  AutoPower = false
  Base = -> Wall313
  CompositionType = 0
  Conditioning = 0
  ElevationWithFlooring = -320
  EquipmentPower = 0
  FloorThickness = 0
  HorizontalArea = 1.6e+06
  IfcData = attributes={"GlobalId": {"name": "GlobalId", "type": "IfcGloballyUniqueId", "is_enum": false, "enum_values": []}, "Description": {"... (+888 chars omitted),+1 more (map truncated)
  IfcType = 122
  Internal = true
  LightingPower = 0
  LongName = Space
  MoveBase = false
  MoveWithHost = false
  NumberOfPeople = 0
  PerimeterLength = 16400
  Placement = pos=(-490,0,0) rot=(0,0,1;0rad)
  PredefinedType = 0
  SpaceType = 0
  VerticalArea = 3.28e+07
  expr: ElevationWithFlooring = .Shape.BoundBox.ZMin
FEATURE [App::GeometryPython] BuildingPart108  label="Откатные ворота 4.5 с калиткой 1м"  # Arch/BIM 172 (typed FeaturePython)
  Area = 1.6628e+07
  Group = -> [Wall315,Wall316,Wall317,Wall318,Wall319,Space,Space001,Roof018,Roof019,Roof020]
  Height = 0
  HeightPropagate = true
  IfcData = attributes={"GlobalId": {"name": "GlobalId", "type": "IfcGloballyUniqueId", "is_enum": false, "enum_values": []}, "Description": {"... (+484 chars omitted),+1 more (map truncated)
  IfcType = 172
  LevelOffset = 0
  PredefinedType = 0
FEATURE [Part::Part2DObjectPython] Wire905  # Draft 2D object (typed FeaturePython)
  Area = 0
  ChamferSize = 0
  Closed = false
  End = (-16687.8,-6439.13,0)
  FilletRadius = 0
  Length = 42628.1
  MakeFace = true
  Placement = pos=(22450.1,-9304.39,0) rot=(0,0,-1;0.04466rad)
  Points = (6) [(0,0,0),(-11950.7,2233.07,0),(-20644.1,1844.56,0),(-31822.2,-659.433,0),(-32744.5,2829.02,0),(-39226.9,1115.07,0)]
  Start = (22450.1,-9304.39,0)
  Subdivisions = 0
FEATURE [Part::FeaturePython] Wall320  label="Забор 002"  # Arch/BIM 166 (typed FeaturePython)
  Align = 0
  Area = 8.52563e+07
  Base = -> Wire905
  BlockHeight = 2000
  BlockLength = 150
  CountBroken = 6
  CountEntire = 260
  Face = 0
  Height = 2000
  HorizontalArea = 0
  IfcData = attributes={"GlobalId": {"name": "GlobalId", "type": "IfcGloballyUniqueId", "is_enum": false, "enum_values": []}, "Description": {"... (+533 chars omitted),+1 more (map truncated)
  IfcType = 166
  Joint = 10
  Length = 42628.1
  MakeBlocks = true
  Material = -> Material010
  MoveBase = false
  MoveWithHost = false
  Normal = (0,0,0)
  OffsetFirst = 100
  OffsetSecond = 0
  PerimeterLength = 0
  Placement = pos=(0,0,-220) rot=(0,0,1;0rad)
  PredefinedType = 0
  VerticalArea = 0
  Width = 50
FEATURE [Part::Part2DObjectPython] Wire906  # Draft 2D object (typed FeaturePython)
  Area = 0
  ChamferSize = 0
  Closed = false
  End = (28701.9,-939.667,0)
  FilletRadius = 0
  Length = 8059.16
  MakeFace = true
  Placement = pos=(24661.3,-3727.55,0) rot=(0,0,-1;0.04466rad)
  Points = (3) [(0,0,0),(-8.2224e-05,4010,0),(3912.13,2965.49,0)]
  Start = (24661.3,-3727.55,0)
  Subdivisions = 0
FEATURE [Part::FeaturePython] Wall321  label="Забор 001"  # Arch/BIM 166 (typed FeaturePython)
  Align = 0
  Area = 1.61183e+07
  Base = -> Wire906
  BlockHeight = 2000
  BlockLength = 150
  CountBroken = 4
  CountEntire = 47
  Face = 0
  Height = 2000
  HorizontalArea = 0
  IfcData = attributes={"GlobalId": {"name": "GlobalId", "type": "IfcGloballyUniqueId", "is_enum": false, "enum_values": []}, "Description": {"... (+533 chars omitted),+1 more (map truncated)
  IfcType = 166
  Joint = 10
  Length = 8059.16
  MakeBlocks = true
  Material = -> Material010
  MoveBase = false
  MoveWithHost = false
  Normal = (0,0,0)
  OffsetFirst = 0
  OffsetSecond = 0
  PerimeterLength = 0
  Placement = pos=(0,0,-220) rot=(0,0,1;0rad)
  PredefinedType = 0
  VerticalArea = 0
  Width = 50
FEATURE [Part::FeaturePython] Structure458  label="Крыша бытовки"  # Arch/BIM 118 (typed FeaturePython)
  Base = -> Rectangle3402
  FaceMaker = 0
  Height = 50
  HorizontalArea = 1.38e+07
  IfcData = attributes={"GlobalId": {"name": "GlobalId", "type": "IfcGloballyUniqueId", "is_enum": false, "enum_values": []}, "Description": {"... (+453 chars omitted),+1 more (map truncated)
  IfcType = 118
  Length = 2300
  MoveBase = false
  MoveWithHost = false
  Nodes = (4) [(-5840.87,-8273.6,0),(66.7383,-7224.73,0),(-335.328,-4960.14,0),(-6242.94,-6009.01,0)]
  NodesOffset = 0
  Normal = (0,0,0)
  PerimeterLength = 16600
  Placement = pos=(0,0,2300) rot=(0,0,1;0rad)
  PredefinedType = 0
  VerticalArea = 830000
  Width = 6000
FEATURE [App::GeometryPython] BuildingPart033  label="хозблок (бытовка)"  # Arch/BIM 10 (typed FeaturePython)
  Area = 4.067e+07
  BuildingType = 0
  CompositionType = 0
  ElevationOfRefHeight = 0
  ElevationOfTerrain = 0
  Group = -> [Wall097,Structure458]
  Height = 0
  HeightPropagate = true
  IfcType = 10
  LevelOffset = 0
  LongName = хозблок (бытовка)
FEATURE [Part::FeaturePython] Roof023  label="Крышка столба 004"  # Arch/BIM 113 (typed FeaturePython)
  BorderLength = 0
  CloneOf = -> Roof018
  Face = 0
  Flip = false
  HorizontalArea = 230400
  IfcData = attributes={"GlobalId": {"name": "GlobalId", "type": "IfcGloballyUniqueId", "is_enum": false, "enum_values": []}, "Description": {"... (+613 chars omitted),+1 more (map truncated)
  IfcType = 113
  Material = -> Material018
  MoveBase = false
  MoveWithHost = false
  PerimeterLength = 0
  Placement = pos=(-20687.8,2722.97,0) rot=(0,0,1;0rad)
  PredefinedType = 0
  RidgeLength = 0
  Thickness = [50,50,50,50]
  VerticalArea = 99386.5
FEATURE [Part::FeaturePython] Wall344  label="Столб 004"  # Arch/BIM 166 (typed FeaturePython)
  Align = 2
  Area = 836000
  BlockHeight = 0
  BlockLength = 0
  CloneOf = -> Wall316
  CountBroken = 0
  CountEntire = 0
  Face = 0
  Height = 2200
  HorizontalArea = 144400
  IfcData = attributes={"GlobalId": {"name": "GlobalId", "type": "IfcGloballyUniqueId", "is_enum": false, "enum_values": []}, "Description": {"... (+533 chars omitted),+1 more (map truncated)
  IfcType = 166
  Joint = 0
  Length = 380
  MakeBlocks = false
  Material = -> Material003
  MoveBase = false
  MoveWithHost = false
  Normal = (0,0,0)
  OffsetFirst = 0
  OffsetSecond = 0
  PerimeterLength = 1520
  Placement = pos=(-20687.8,2722.97,-320) rot=(0,0,1;0rad)
  PredefinedType = 0
  VerticalArea = 3.344e+06
  Width = 380
FEATURE [Part::FeaturePython] Wall345  label="Столб 005"  # Arch/BIM 166 (typed FeaturePython)
  Align = 2
  Area = 836000
  BlockHeight = 0
  BlockLength = 0
  CloneOf = -> Wall316
  CountBroken = 0
  CountEntire = 0
  Face = 0
  Height = 2200
  HorizontalArea = 144400
  IfcData = attributes={"GlobalId": {"name": "GlobalId", "type": "IfcGloballyUniqueId", "is_enum": false, "enum_values": []}, "Description": {"... (+533 chars omitted),+1 more (map truncated)
  IfcType = 166
  Joint = 0
  Length = 380
  MakeBlocks = false
  Material = -> Material003
  MoveBase = false
  MoveWithHost = false
  Normal = (0,0,0)
  OffsetFirst = 0
  OffsetSecond = 0
  PerimeterLength = 1520
  Placement = pos=(-12035.1,2722.32,-320) rot=(0,0,1;0rad)
  PredefinedType = 0
  VerticalArea = 3.344e+06
  Width = 380
FEATURE [Part::FeaturePython] Roof024  label="Крышка столба 005"  # Arch/BIM 113 (typed FeaturePython)
  BorderLength = 0
  CloneOf = -> Roof018
  Face = 0
  Flip = false
  HorizontalArea = 230400
  IfcData = attributes={"GlobalId": {"name": "GlobalId", "type": "IfcGloballyUniqueId", "is_enum": false, "enum_values": []}, "Description": {"... (+613 chars omitted),+1 more (map truncated)
  IfcType = 113
  Material = -> Material018
  MoveBase = false
  MoveWithHost = false
  PerimeterLength = 0
  Placement = pos=(-12035.1,2722.32,0) rot=(0,0,1;0rad)
  PredefinedType = 0
  RidgeLength = 0
  Thickness = [50,50,50,50]
  VerticalArea = 99386.5
FEATURE [App::GeometryPython] BuildingPart067  label="Участок с ограждением"  # Arch/BIM 52 (typed FeaturePython)
  Area = 1.19675e+08
  Group = -> [Structure133,BuildingPart108,Wall320,Wall321,Structure437,Roof023,Wall344,Wall345,Roof024]
  Height = 0
  HeightPropagate = true
  IfcData = attributes={"GlobalId": {"name": "GlobalId", "type": "IfcGloballyUniqueId", "is_enum": false, "enum_values": []}, "Description": {"... (+484 chars omitted),+1 more (map truncated)
  IfcType = 52
  LevelOffset = 0
FEATURE [App::FeaturePython] Dimension072  # Draft dimension (typed FeaturePython)
  Diameter = false
  Dimline = (-1400,7200,0)
  Direction = (0,0,0)
  Distance = 738.353
  End = (-800,7685.58,0)
  Normal = (0,0,1)
  Start = (-800,6947.23,0)
FEATURE [App::FeaturePython] Dimension073  # Draft dimension (typed FeaturePython)
  Diameter = false
  Dimline = (-1400,7200,0)
  Direction = (0,0,0)
  Distance = 3217.23
  End = (-800,6947.23,0)
  Normal = (0,0,1)
  Start = (-800,3730,0)
FEATURE [App::FeaturePython] Dimension074  # Draft dimension (typed FeaturePython)
  Diameter = false
  Dimline = (-1400,7685.58,0)
  Direction = (0,0,0)
  Distance = 914.422
  End = (-800,8600,0)
  Normal = (0,0,1)
  Start = (-800,7685.58,0)
FEATURE [App::FeaturePython] Dimension075  # Draft dimension (typed FeaturePython)
  Diameter = false
  Dimline = (0,5100,2400)
  Direction = (0,0,0)
  Distance = 6448.76
  End = (0,6954.38,3045)
  Normal = (1,0,0)
  Start = (0,505.619,3045)
FEATURE [App::FeaturePython] Dimension076  # Draft dimension (typed FeaturePython)
  Diameter = false
  Dimline = (0,8900,4000)
  Direction = (0,0,0)
  Distance = 3013.88
  End = (0,9000,6796.88)
  Normal = (1,0,0)
  Start = (0,9000,3783)
FEATURE [App::FeaturePython] Dimension077  # Draft dimension (typed FeaturePython)
  Diameter = false
  Dimline = (0,5000,1500)
  Direction = (0,0,0)
  Distance = 9740
  End = (0,8600,3300)
  Normal = (1,0,0)
  Start = (0,-1140,3300)
FEATURE [App::FeaturePython] Dimension078  # Draft dimension (typed FeaturePython)
  Diameter = false
  Dimline = (0,5000,2000)
  Direction = (0,0,0)
  Distance = 7911.16
  End = (0,7685.58,2200)
  Normal = (1,0,0)
  Start = (0,-225.578,2200)
FEATURE [Part::Part2DObjectPython] Rectangle3389  # Draft 2D object (typed FeaturePython)
  Area = 2.45e+07
  ChamferSize = 0
  Columns = 1
  FilletRadius = 0
  Height = 7000
  Length = 3500
  MakeFace = true
  Placement = pos=(22359,-9231.91,0) rot=(0,0,1;1.34139rad)
  Rows = 1
FEATURE [Part::Part2DObjectPython] Line1687  # Draft 2D object (typed FeaturePython)
  Area = 0
  ChamferSize = 0
  Closed = false
  End = (-3580.3,-8530.19,0)
  FilletRadius = 0
  Length = 1000
  MakeFace = true
  Placement = pos=(-3755.12,-7545.59,0) rot=(0,0,1;1.52614rad)
  Points = (2) [(0,0,0),(-975.816,-218.595,0)]
  Start = (-3755.12,-7545.59,0)
  Subdivisions = 0
FEATURE [Part::Part2DObjectPython] Line1688  # Draft 2D object (typed FeaturePython)
  Area = 0
  ChamferSize = 0
  Closed = false
  End = (7519.32,-7540,0)
  FilletRadius = 0
  Length = 1000
  MakeFace = true
  Placement = pos=(7519.32,-6540,0) rot=(0,0,1;1.52614rad)
  Points = (2) [(0,0,0),(-999.003,-44.6455,0)]
  Start = (7519.32,-6540,0)
  Subdivisions = 0
FEATURE [Part::Part2DObjectPython] Line1689  # Draft 2D object (typed FeaturePython)
  Area = 0
  ChamferSize = 0
  Closed = false
  End = (9687.65,-6293.74,0)
  FilletRadius = 0
  Length = 12000
  MakeFace = true
  Placement = pos=(21282.4,-9385.88,0) rot=(0,0,1;1.52614rad)
  Points = (2) [(0,0,0),(2571.4,11721.3,0)]
  Start = (21282.4,-9385.88,0)
  Subdivisions = 0
FEATURE [Part::Part2DObjectPython] Line1690  # Draft 2D object (typed FeaturePython)
  Area = 0
  ChamferSize = 0
  Closed = false
  End = (1996.8,-7540,0)
  FilletRadius = 0
  Length = 1000
  MakeFace = true
  Placement = pos=(1996.8,-6540,0) rot=(0,0,1;1.52614rad)
  Points = (2) [(0,0,0),(-999.003,-44.6455,0)]
  Start = (1996.8,-6540,0)
  Subdivisions = 0
FEATURE [Part::Part2DObjectPython] Line1692  # Draft 2D object (typed FeaturePython)
  Area = 0
  ChamferSize = 0
  Closed = false
  End = (1996.8,-7540,0)
  FilletRadius = 0
  Length = 1000
  MakeFace = true
  Placement = pos=(1821.99,-6555.4,0) rot=(0,0,1;1.52614rad)
  Points = (2) [(0,0,0),(-975.816,-218.595,0)]
  Start = (1821.99,-6555.4,0)
  Subdivisions = 0
FEATURE [Part::Part2DObjectPython] Line1693  # Draft 2D object (typed FeaturePython)
  Area = 0
  ChamferSize = 0
  Closed = false
  End = (-9993.23,-8653.14,0)
  FilletRadius = 0
  Length = 12000
  MakeFace = true
  Placement = pos=(1821.99,-6555.4,0) rot=(0,0,1;1.52614rad)
  Points = (2) [(0,0,0),(-2623.14,11709.8,0)]
  Start = (1821.99,-6555.4,0)
  Subdivisions = 0
FEATURE [Part::Part2DObjectPython] Line1694  # Draft 2D object (typed FeaturePython)
  Area = 0
  ChamferSize = 0
  Closed = false
  End = (-9662.73,-8594.46,0)
  FilletRadius = 0
  Length = 12000
  MakeFace = true
  Placement = pos=(2152.5,-6496.72,0) rot=(0,0,1;1.52614rad)
  Points = (2) [(0,0,0),(-2623.14,11709.8,0)]
  Start = (2152.5,-6496.72,0)
  Subdivisions = 0
FEATURE [Part::Part2DObjectPython] Line1695  # Draft 2D object (typed FeaturePython)
  Area = 0
  ChamferSize = 0
  Closed = false
  End = (12611.1,-6540,0)
  FilletRadius = 0
  Length = 12000
  MakeFace = true
  Placement = pos=(611.062,-6540,0) rot=(0,0,1;1.52614rad)
  Points = (2) [(0,0,0),(535.746,-11988,0)]
  Start = (611.062,-6540,0)
  Subdivisions = 0
FEATURE [Part::Part2DObjectPython] Rectangle3390  # Draft 2D object (typed FeaturePython)
  Area = 144400
  ChamferSize = 0
  Columns = 1
  FilletRadius = 0
  Height = 380
  Length = 380
  MakeFace = true
  Placement = pos=(22825.7,-9411.26,0) rot=(0,0,1;1.52614rad)
  Rows = 1
FEATURE [Part::Part2DObjectPython] Rectangle3392  # Draft 2D object (typed FeaturePython)
  Area = 144400
  ChamferSize = 0
  Columns = 1
  FilletRadius = 0
  Height = 380
  Length = 380
  MakeFace = true
  Placement = pos=(24404.1,-9481.8,0) rot=(0,0,1;1.52614rad)
  Rows = 1
FEATURE [Part::Part2DObjectPython] Rectangle3393  # Draft 2D object (typed FeaturePython)
  Area = 144400
  ChamferSize = 0
  Columns = 1
  FilletRadius = 0
  Height = 380
  Length = 380
  MakeFace = true
  Placement = pos=(24644.3,-4107.17,0) rot=(0,0,1;1.52614rad)
  Rows = 1
FEATURE [Part::Part2DObjectPython] Rectangle3395  # Draft 2D object (typed FeaturePython)
  Area = 520000
  ChamferSize = 0
  Columns = 1
  FilletRadius = 0
  Height = 100
  Length = 5200
  MakeFace = true
  Placement = pos=(24037,-9185.12,0) rot=(0,0,1;1.52614rad)
  Rows = 1
FEATURE [Part::Part2DObjectPython] Circle135  label="Circle136"  # Draft 2D object (typed FeaturePython)
  Area = 1.05683e+06
  FirstAngle = 0
  LastAngle = 0
  MakeFace = true
  Placement = pos=(22885.9,-1376.75,0) rot=(0,0,1;1.52614rad)
  Radius = 580
FEATURE [Part::Part2DObjectPython] Line1697  # Draft 2D object (typed FeaturePython)
  Area = 0
  ChamferSize = 0
  Closed = false
  End = (24764.4,-1419.85,0)
  FilletRadius = 0
  Length = 1500
  MakeFace = false
  Placement = pos=(23265.9,-1352.88,0) rot=(0,0,1;1.52614rad)
  Points = (2) [(0,0,0),(-2.50111e-12,-1500,0)]
  Start = (23265.9,-1352.88,0)
  Subdivisions = 0
FEATURE [Part::Part2DObjectPython] Line1699  # Draft 2D object (typed FeaturePython)
  Area = 0
  ChamferSize = 0
  Closed = false
  End = (24840.3,278.455,0)
  FilletRadius = 0
  Length = 1300
  MakeFace = false
  Placement = pos=(23541.6,336.495,0) rot=(0,0,1;1.52614rad)
  Points = (2) [(0,0,0),(6.82121e-13,-1300,0)]
  Start = (23541.6,336.495,0)
  Subdivisions = 0
FEATURE [Part::Part2DObjectPython] Circle136  label="Circle137"  # Draft 2D object (typed FeaturePython)
  Area = 1.05683e+06
  FirstAngle = 0
  LastAngle = 0
  MakeFace = true
  Placement = pos=(22961.8,321.557,0) rot=(0,0,1;1.52614rad)
  Radius = 580
FEATURE [Part::Part2DObjectPython] Line1702  # Draft 2D object (typed FeaturePython)
  Area = 0
  ChamferSize = 0
  Closed = true
  End = (14388.6,662.218,0)
  FilletRadius = 0
  Length = 8000
  MakeFace = true
  Placement = pos=(22381.9,303.842,0) rot=(0,0,1;1.52614rad)
  Points = (2) [(38.1281,1.43103,0),(1.15288,8001.35,0)]
  Start = (22382.2,341.996,0)
  Subdivisions = 0
FEATURE [Part::Part2DObjectPython] Rectangle3400  # Draft 2D object (typed FeaturePython)
  Area = 2.45e+07
  ChamferSize = 0
  Columns = 1
  FilletRadius = 0
  Height = 7000
  Length = 3500
  MakeFace = true
  Placement = pos=(22181.1,-5596.2,0) rot=(0,0,1;1.34139rad)
  Rows = 1
FEATURE [Part::Part2DObjectPython] Line1704  # Draft 2D object (typed FeaturePython)
  Area = 0
  ChamferSize = 0
  Closed = false
  End = (14360.8,-420.719,0)
  FilletRadius = 0
  Length = 5100
  MakeFace = false
  Placement = pos=(19455.7,-648.412,0) rot=(0,0,1;0.025758rad)
  Points = (2) [(0,0,0),(-5087.36,358.837,0)]
  Start = (19455.7,-648.412,0)
  Subdivisions = 0
FEATURE [Part::Part2DObjectPython] Circle140  label="Circle141"  # Draft 2D object (typed FeaturePython)
  Area = 1.05683e+06
  FirstAngle = 0
  LastAngle = 0
  MakeFace = true
  Placement = pos=(21460.2,-1031.22,0) rot=(0,0,1;1.52614rad)
  Radius = 580
FEATURE [Part::Part2DObjectPython] Circle141  label="Circle142"  # Draft 2D object (typed FeaturePython)
  Area = 1.05683e+06
  FirstAngle = 0
  LastAngle = 0
  MakeFace = true
  Placement = pos=(20034.5,-685.694,0) rot=(0,0,1;1.52614rad)
  Radius = 580
FEATURE [Part::Part2DObjectPython] Line1705  # Draft 2D object (typed FeaturePython)
  Area = 0
  ChamferSize = 0
  Closed = true
  End = (22885.9,-1376.75,0)
  FilletRadius = 0
  Length = 2933.93
  MakeFace = false
  Placement = pos=(19875.5,-436.151,0) rot=(0,0,1;0.025758rad)
  Points = (2) [(152.568,-253.556,0),(2985.21,-1017.82,0)]
  Start = (20034.5,-685.694,0)
  Subdivisions = 0
FEATURE [Part::Part2DObjectPython] Circle142  label="Circle143"  # Draft 2D object (typed FeaturePython)
  Area = 1.05683e+06
  FirstAngle = 0
  LastAngle = 0
  MakeFace = true
  Placement = pos=(-7874.87,-6660.56,0) rot=(0,0,1;1.52614rad)
  Radius = 580
FEATURE [Part::Part2DObjectPython] Rectangle3401  # Draft 2D object (typed FeaturePython)
  Area = 9.2e+06
  ChamferSize = 0
  Columns = 1
  FilletRadius = 0
  Height = 2300
  Length = 4000
  MakeFace = true
  Placement = pos=(23704,1728.87,0) rot=(0,0,1;1.52614rad)
  Rows = 1
FEATURE [Part::Part2DObjectPython] Line1706  # Draft 2D object (typed FeaturePython)
  Area = 0
  ChamferSize = 0
  Closed = false
  End = (-8436.54,-6805.24,0)
  FilletRadius = 0
  Length = 1200
  MakeFace = true
  Placement = pos=(-9598.6,-7104.59,0) rot=(0,0,1;1.52614rad)
  Points = (2) [(0,0,0),(350.925,-1147.54,0)]
  Start = (-9598.6,-7104.59,0)
  Subdivisions = 0
FEATURE [Part::Part2DObjectPython] Line1710  # Draft 2D object (typed FeaturePython)
  Area = 0
  ChamferSize = 0
  Closed = false
  End = (14360.8,-7540,0)
  FilletRadius = 0
  Length = 6000
  MakeFace = true
  Placement = pos=(14360.8,-1540,0) rot=(0,0,-1;0.04466rad)
  Points = (2) [(0,0,0),(267.873,-5994.02,0)]
  Start = (14360.8,-1540,0)
  Subdivisions = 0
FEATURE [Part::Part2DObjectPython] Line1711  # Draft 2D object (typed FeaturePython)
  Area = 0
  ChamferSize = 0
  Closed = false
  End = (22185.4,-9292.56,0)
  FilletRadius = 0
  Length = 1800
  MakeFace = true
  Placement = pos=(23983.6,-9372.92,0) rot=(0,0,-1;0.04466rad)
  Points = (2) [(0,0,0),(-1800,-1.09139e-11,0)]
  Start = (23983.6,-9372.92,0)
  Subdivisions = 0
FEATURE [Part::Part2DObjectPython] Line1712  # Draft 2D object (typed FeaturePython)
  Area = 0
  ChamferSize = 0
  Closed = false
  End = (10611.1,-6540,0)
  FilletRadius = 0
  Length = 12157.5
  MakeFace = true
  Placement = pos=(22450.1,-9304.39,0) rot=(0,0,-1;0.04466rad)
  Points = (2) [(0,0,0),(-11950.7,2233.07,0)]
  Start = (22450.1,-9304.39,0)
  Subdivisions = 0
FEATURE [Part::Part2DObjectPython] Line1713  # Draft 2D object (typed FeaturePython)
  Area = 0
  ChamferSize = 0
  Closed = false
  End = (24571.4,-3723.53,0)
  FilletRadius = 0
  Length = 90
  MakeFace = true
  Placement = pos=(24661.3,-3727.55,0) rot=(0,0,-1;0.04466rad)
  Points = (2) [(0,0,0),(-90,1.36424e-12,0)]
  Start = (24661.3,-3727.55,0)
  Subdivisions = 0
FEATURE [Part::Part2DObjectPython] Rectangle3403  label="Контур Строения002"  # Draft 2D object (typed FeaturePython)
  Area = 0
  ChamferSize = 0
  Columns = 1
  FilletRadius = 0
  Height = 8540
  Length = 13640
  MakeFace = false
  Placement = pos=(-560,-540,0) rot=(0,0,1;0rad)
  Rows = 1
FEATURE [Part::Part2DObjectPython] Line1714  # Draft 2D object (typed FeaturePython)
  Area = 0
  ChamferSize = 0
  Closed = false
  End = (-34430.2,9739.91,0)
  FilletRadius = 0
  Length = 7432.67
  MakeFace = true
  Placement = pos=(-41420.8,7214.83,0) rot=(0,0,-1;0.04466rad)
  Points = (2) [(0,0,0),(6870.9,2834.66,0)]
  Start = (-41420.8,7214.83,0)
  Subdivisions = 0
FEATURE [Part::Part2DObjectPython] Line1715  # Draft 2D object (typed FeaturePython)
  Area = 0
  ChamferSize = 0
  Closed = false
  End = (-41420.8,7214.83,0)
  FilletRadius = 0
  Length = 5559.77
  MakeFace = true
  Placement = pos=(-39131,2148.46,0) rot=(0,0,-1;0.04466rad)
  Points = (2) [(0,0,0),(-2513.65,4959.09,0)]
  Start = (-39131,2148.46,0)
  Subdivisions = 0
FEATURE [Part::Part2DObjectPython] Line1716  # Draft 2D object (typed FeaturePython)
  Area = 0
  ChamferSize = 0
  Closed = false
  End = (39960.8,38650.8,0)
  FilletRadius = 0
  Length = 6490.01
  MakeFace = true
  Placement = pos=(37704.2,32565.7,0) rot=(0,0,-1;0.04466rad)
  Points = (2) [(0,0,0),(1982.64,6179.75,0)]
  Start = (37704.2,32565.7,0)
  Subdivisions = 0
FEATURE [Part::Part2DObjectPython] Line1717  # Draft 2D object (typed FeaturePython)
  Area = 0
  ChamferSize = 0
  Closed = false
  End = (39960.8,38650.8,0)
  FilletRadius = 0
  Length = 8107.57
  MakeFace = true
  Placement = pos=(32209.4,41027.5,0) rot=(0,0,-1;0.04466rad)
  Points = (2) [(0,0,0),(7849.75,-2028.32,0)]
  Start = (32209.4,41027.5,0)
  Subdivisions = 0
FEATURE [Part::Part2DObjectPython] Line1718  # Draft 2D object (typed FeaturePython)
  Area = 0
  ChamferSize = 0
  Closed = false
  End = (6260,-6540,0)
  FilletRadius = 0
  Length = 6000
  MakeFace = true
  Placement = pos=(6260,-540,0) rot=(0,0,1;1.52614rad)
  Points = (2) [(0,0,0),(-5994.02,-267.873,0)]
  Start = (6260,-540,0)
  Subdivisions = 0
FEATURE [Part::Part2DObjectPython] Line1719  # Draft 2D object (typed FeaturePython)
  Area = 0
  ChamferSize = 0
  Closed = false
  End = (6198,-7540,0)
  FilletRadius = 0
  Length = 5610
  MakeFace = true
  Placement = pos=(6198,-1930,0) rot=(0,0,1;1.52614rad)
  Points = (2) [(0,0,0),(-5604.41,-250.461,0)]
  Start = (6198,-1930,0)
  Subdivisions = 0
FEATURE [App::DocumentObjectGroup] Group132  label="разное"
  Group = -> [Dimension072,Dimension073,Dimension074,Dimension075,Dimension076,Dimension077,Dimension078,Rectangle3389,Line1687,Line1688,Line1689,Line1690,Line1692,Line1693,Line1694,Line1695,Rectangle3390,Rectangle3392,Rectangle3393,Rectangle3395,Circle135,Line1697,Line1699,Circle136,Line1702,Rectangle3400,Line1704,Circle140,Circle141,Line1705,Circle142,Rectangle3401,Line1706,Line1710,Line1711,Line1712,+8 more]
FEATURE [Part::Part2DObjectPython] Wire914  # Draft 2D object (typed FeaturePython)
  Area = 0
  ChamferSize = 0
  Closed = false
  End = (3579.3,3604.56,2277.3)
  FilletRadius = 0
  Length = 830.703
  MakeFace = true
  Points = (7) [(3592.14,3618.7,2291.44),(3590,3579,2331.14),(3587.86,3579,2174),(3585.72,3781,2174),(3583.58,3781,2317),(3581.44,3564.86,2317),+1 more]
  Start = (3592.14,3618.7,2291.44)
  Subdivisions = 0
  Support = -> [Wall277]
FEATURE [Part::FeaturePython] Rebar050  label="Stirrup016"  # Arch/BIM 110 (typed FeaturePython)
  Amount = 7
  AmountCheck = false
  Base = -> Wire914
  BentAngle = 135
  BentFactor = 4
  BottomCover = 20
  Diameter = 8
  Direction = (1,0,0)
  Distance = 0
  FrontCover = 100
  HorizontalArea = 0
  Host = -> Wall277
  IfcType = 110
  LeftCover = 20
  Length = 830.703
  Mark = Stirrup016
  Material = -> Material010
  MoveBase = false
  MoveWithHost = false
  OffsetEnd = 104
  OffsetStart = 104
  PerimeterLength = 0
  PlacementList = 7 placements: arithmetic series from (104,0,0) step (204,0,0) to (1328,0,0)
  RebarShape = 3
  RightCover = 20
  Rounding = 1.25
  Spacing = 204
  TopCover = 20
  TotalLength = 5814.92
  TrueSpacing = 250
  VerticalArea = 0
FEATURE [App::DocumentObjectGroupPython] Stirrups016  # scripted group (container) (typed FeaturePython)
  Group = -> [Rebar050]
  Stirrups = -> [Rebar050]
  StirrupsConfiguration = Two Legged Stirrups
FEATURE [Sketcher::SketchObject] Sketch365
  FullyConstrained = false
  MapMode = 5
  Placement = pos=(0,3805,2150) rot=(0,0.707107,0.707107;3.14159rad)
  Support = -> [Wall277]
  sketch-geometry (1):
    g0: LineSegment StartX=-4970 StartY=157 StartZ=0 EndX=-3650 EndY=157 EndZ=0
FEATURE [Part::FeaturePython] Rebar051  label="StraightRebar034"  # Arch/BIM 110 (typed FeaturePython)
  Amount = 2
  AmountCheck = true
  Base = -> Sketch365
  Cover = 28
  CoverAlong = Top Side
  Diameter = 12
  Direction = (0,0,0)
  Distance = 0
  FrontCover = 28
  HorizontalArea = 0
  Host = -> Wall277
  IfcType = 110
  LeftBottomCover = 60
  Length = 1320
  Mark = StraightRebar034
  Material = -> Material010
  MoveBase = false
  MoveWithHost = false
  OffsetEnd = 34
  OffsetStart = 34
  Orientation = Horizontal
  PerimeterLength = 0
  PlacementList = 2 placements: [(0,-34,7.54952e-15),(0,-216,4.79616e-14)]
  RebarShape = 0
  RightTopCover = 60
  Rounding = 0
  Spacing = 182
  TotalLength = 2640
  TrueSpacing = 2
  VerticalArea = 0
FEATURE [App::DocumentObjectGroupPython] TopReinforcement016  # scripted group (container) (typed FeaturePython)
  Group = -> [Rebar051]
  LayerSpacing = [30]
  NumberDiameterOffset = 2#12.0@60.0
  TopRebars = -> [Rebar051]
FEATURE [Sketcher::SketchObject] Sketch366
  FullyConstrained = false
  MapMode = 5
  Placement = pos=(0,3805,2150) rot=(0,0.707107,0.707107;3.14159rad)
  Support = -> [Wall277]
  sketch-geometry (1):
    g0: LineSegment StartX=-4970 StartY=34 StartZ=0 EndX=-3650 EndY=34 EndZ=0
FEATURE [Part::FeaturePython] Rebar052  label="StraightRebar035"  # Arch/BIM 110 (typed FeaturePython)
  Amount = 2
  AmountCheck = true
  Base = -> Sketch366
  Cover = 28
  CoverAlong = Bottom Side
  Diameter = 12
  Direction = (0,0,0)
  Distance = 0
  FrontCover = 28
  HorizontalArea = 0
  Host = -> Wall277
  IfcType = 110
  LeftBottomCover = 60
  Length = 1320
  Mark = StraightRebar035
  Material = -> Material010
  MoveBase = false
  MoveWithHost = false
  OffsetEnd = 34
  OffsetStart = 34
  Orientation = Horizontal
  PerimeterLength = 0
  PlacementList = 2 placements: [(0,-34,7.54952e-15),(0,-216,4.79616e-14)]
  RebarShape = 0
  RightTopCover = 60
  Rounding = 0
  Spacing = 182
  TotalLength = 2640
  TrueSpacing = 2
  VerticalArea = 0
FEATURE [App::DocumentObjectGroupPython] BottomReinforcement016  # scripted group (container) (typed FeaturePython)
  BottomRebars = -> [Rebar052]
  Group = -> [Rebar052]
  LayerSpacing = [30]
  NumberDiameterOffset = 2#12.0@60.0
FEATURE [App::DocumentObjectGroupPython] BeamReinforcement016  label="BeamReinforcement017"  # scripted group (container) (typed FeaturePython)
  Group = -> [Stirrups016,TopReinforcement016,BottomReinforcement016]
  ReinforcementGroups = -> [Stirrups016,TopReinforcement016,BottomReinforcement016]
FEATURE [Part::Part2DObjectPython] Wire915  # Draft 2D object (typed FeaturePython)
  Area = 0
  ChamferSize = 0
  Closed = false
  End = (5529.3,3604.56,2277.3)
  FilletRadius = 0
  Length = 830.703
  MakeFace = true
  Points = (7) [(5542.14,3618.7,2291.44),(5540,3579,2331.14),(5537.86,3579,2174),(5535.72,3781,2174),(5533.58,3781,2317),(5531.44,3564.86,2317),+1 more]
  Start = (5542.14,3618.7,2291.44)
  Subdivisions = 0
  Support = -> [Wall278]
FEATURE [Part::FeaturePython] Rebar053  label="Stirrup017"  # Arch/BIM 110 (typed FeaturePython)
  Amount = 7
  AmountCheck = false
  Base = -> Wire915
  BentAngle = 135
  BentFactor = 4
  BottomCover = 20
  Diameter = 8
  Direction = (1,0,0)
  Distance = 0
  FrontCover = 100
  HorizontalArea = 0
  Host = -> Wall278
  IfcType = 110
  LeftCover = 20
  Length = 830.703
  Mark = Stirrup017
  Material = -> Material010
  MoveBase = false
  MoveWithHost = false
  OffsetEnd = 104
  OffsetStart = 104
  PerimeterLength = 0
  PlacementList = 7 placements: arithmetic series from (104,0,0) step (204,0,0) to (1328,0,0)
  RebarShape = 3
  RightCover = 20
  Rounding = 1.25
  Spacing = 204
  TopCover = 20
  TotalLength = 5814.92
  TrueSpacing = 250
  VerticalArea = 0
FEATURE [App::DocumentObjectGroupPython] Stirrups017  # scripted group (container) (typed FeaturePython)
  Group = -> [Rebar053]
  Stirrups = -> [Rebar053]
  StirrupsConfiguration = Two Legged Stirrups
FEATURE [Sketcher::SketchObject] Sketch367
  FullyConstrained = false
  MapMode = 5
  Placement = pos=(0,3805,2150) rot=(0,0.707107,0.707107;3.14159rad)
  Support = -> [Wall278]
  sketch-geometry (1):
    g0: LineSegment StartX=-6920 StartY=157 StartZ=0 EndX=-5600 EndY=157 EndZ=0
FEATURE [Part::FeaturePython] Rebar054  label="StraightRebar036"  # Arch/BIM 110 (typed FeaturePython)
  Amount = 2
  AmountCheck = true
  Base = -> Sketch367
  Cover = 28
  CoverAlong = Top Side
  Diameter = 12
  Direction = (0,0,0)
  Distance = 0
  FrontCover = 28
  HorizontalArea = 0
  Host = -> Wall278
  IfcType = 110
  LeftBottomCover = 60
  Length = 1320
  Mark = StraightRebar036
  Material = -> Material010
  MoveBase = false
  MoveWithHost = false
  OffsetEnd = 34
  OffsetStart = 34
  Orientation = Horizontal
  PerimeterLength = 0
  PlacementList = 2 placements: [(0,-34,7.54952e-15),(0,-216,4.79616e-14)]
  RebarShape = 0
  RightTopCover = 60
  Rounding = 0
  Spacing = 182
  TotalLength = 2640
  TrueSpacing = 2
  VerticalArea = 0
FEATURE [App::DocumentObjectGroupPython] TopReinforcement017  # scripted group (container) (typed FeaturePython)
  Group = -> [Rebar054]
  LayerSpacing = [30]
  NumberDiameterOffset = 2#12.0@60.0
  TopRebars = -> [Rebar054]
FEATURE [Sketcher::SketchObject] Sketch368
  FullyConstrained = false
  MapMode = 5
  Placement = pos=(0,3805,2150) rot=(0,0.707107,0.707107;3.14159rad)
  Support = -> [Wall278]
  sketch-geometry (1):
    g0: LineSegment StartX=-6920 StartY=34 StartZ=0 EndX=-5600 EndY=34 EndZ=0
FEATURE [Part::FeaturePython] Rebar055  label="StraightRebar037"  # Arch/BIM 110 (typed FeaturePython)
  Amount = 2
  AmountCheck = true
  Base = -> Sketch368
  Cover = 28
  CoverAlong = Bottom Side
  Diameter = 12
  Direction = (0,0,0)
  Distance = 0
  FrontCover = 28
  HorizontalArea = 0
  Host = -> Wall278
  IfcType = 110
  LeftBottomCover = 60
  Length = 1320
  Mark = StraightRebar037
  Material = -> Material010
  MoveBase = false
  MoveWithHost = false
  OffsetEnd = 34
  OffsetStart = 34
  Orientation = Horizontal
  PerimeterLength = 0
  PlacementList = 2 placements: [(0,-34,7.54952e-15),(0,-216,4.79616e-14)]
  RebarShape = 0
  RightTopCover = 60
  Rounding = 0
  Spacing = 182
  TotalLength = 2640
  TrueSpacing = 2
  VerticalArea = 0
FEATURE [App::DocumentObjectGroupPython] BottomReinforcement017  # scripted group (container) (typed FeaturePython)
  BottomRebars = -> [Rebar055]
  Group = -> [Rebar055]
  LayerSpacing = [30]
  NumberDiameterOffset = 2#12.0@60.0
FEATURE [App::DocumentObjectGroupPython] BeamReinforcement017  label="BeamReinforcement018"  # scripted group (container) (typed FeaturePython)
  Group = -> [Stirrups017,TopReinforcement017,BottomReinforcement017]
  ReinforcementGroups = -> [Stirrups017,TopReinforcement017,BottomReinforcement017]
FEATURE [App::GeometryPython] BuildingPart096  label="Армирование перемычек"  # Arch/BIM 111 (typed FeaturePython)
  Area = 0
  GlobalId = 0M_P_ho1jD6Ar$JhrFI58w
  Group = -> [BeamReinforcement011,BeamReinforcement010,BeamReinforcement009,BeamReinforcement008,BeamReinforcement007,BeamReinforcement006,BeamReinforcement004,BeamReinforcement003,BeamReinforcement001,BeamReinforcement,BeamReinforcement002,BeamReinforcement005,BeamReinforcement016,BeamReinforcement017]
  Height = 0
  HeightPropagate = true
  IfcData = IfcUID=0M_P_ho1jD6Ar$JhrFI58w,+2 more (map truncated)
  IfcType = 111
  LevelOffset = 0
FEATURE [Sketcher::SketchObject] Sketch369
  FullyConstrained = true
  Placement = pos=(5810,3535,0) rot=(1,0,0;1.5708rad)
  sketch-geometry (8):
    g0: LineSegment StartX=0 StartY=0 StartZ=0 EndX=900 EndY=0 EndZ=0
    g1: LineSegment StartX=900 StartY=0 StartZ=0 EndX=900 EndY=2150 EndZ=0
    g2: LineSegment StartX=900 StartY=2150 StartZ=0 EndX=0 EndY=2150 EndZ=0
    g3: LineSegment StartX=0 StartY=2150 StartZ=0 EndX=0 EndY=0 EndZ=0
    g4: LineSegment StartX=50 StartY=0 StartZ=0 EndX=850 EndY=0 EndZ=0
    g5: LineSegment StartX=850 StartY=0 StartZ=0 EndX=850 EndY=2100 EndZ=0
    g6: LineSegment StartX=850 StartY=2100 StartZ=0 EndX=50 EndY=2100 EndZ=0
    g7: LineSegment StartX=50 StartY=2100 StartZ=0 EndX=50 EndY=0 EndZ=0
  constraints (23):
    c: Coincident(g0,g1)
    c: Coincident(g1,g2)
    c: Coincident(g2,g3)
    c: Coincident(g3,g0)
    c: Horizontal(g0)
    c: Horizontal(g2)
    c: Vertical(g1)
    c: Vertical(g3)
    c: Coincident(g4,g5)
    c: Coincident(g5,g6)
    c: Coincident(g6,g7)
    c: Coincident(g7,g4)
    c: Horizontal(g4)
    c: Horizontal(g6)
    c: Vertical(g5)
    c: Vertical(g7)
    c: DistanceY(g1) = 2150  'Height'
    c: DistanceX(g0) = 900  'Width'
    c: DistanceY(g6,g2) = 50  'Frame1'
    c: DistanceX(g2,g6) = 50  'Frame2'
    c: DistanceX(g4,g0) = 50  'Frame3'
    c: DistanceY(g0,g4) = 0
    c: Coincident(g0,g-1)
FEATURE [Part::FeaturePython] Window068  label="Д-90-006"  # Arch/BIM 41 (typed FeaturePython)
  Area = 1935000
  Base = -> Sketch369
  Frame = 50
  GlobalId = 00iW5F1Zz0_RepVZ61wedb
  Height = 2150
  HoleDepth = 0
  HoleWire = 0
  HorizontalArea = 0
  IfcData = IfcUID=00iW5F1Zz0_RepVZ61wedb; attributes={"OverallHeight": {"value": 2150.0}, "OverallWidth": {"value": 900.0}, "GlobalId": {"value": "00iW5F1Zz0_RepVZ61wedb"}}
  IfcType = 41
  LouvreSpacing = 0
  LouvreWidth = 0
  Material = -> Material011
  MoveBase = false
  MoveWithHost = true
  Normal = (0,1,0)
  Opening = 0
  OperationType = 0
  OverallHeight = 2150
  OverallWidth = 900
  PerimeterLength = 0
  Placement = pos=(0,50,0) rot=(0,0,1;0rad)
  PredefinedType = 0
  Preset = 6
  SymbolElevation = false
  SymbolPlan = false
  VerticalArea = 0
  Width = 900
  WindowParts = OuterFrame | Frame | Wire0,Wire1 | 0.0+V | 0.00+V | Door | Solid panel | Wire1 | 50.0 | 0.0+V
  expr: OverallHeight = .Height.Value
  expr: OverallWidth = .Width.Value
FEATURE [Sketcher::SketchObject] Sketch370
  FullyConstrained = true
  Placement = pos=(6005,7895,960) rot=(0,0.707107,0.707107;3.14159rad)
  sketch-geometry (16):
    g0: LineSegment StartX=0 StartY=0 StartZ=0 EndX=920 EndY=0 EndZ=0
    g1: LineSegment StartX=920 StartY=0 StartZ=0 EndX=920 EndY=1610 EndZ=0
    g2: LineSegment StartX=920 StartY=1610 StartZ=0 EndX=0 EndY=1610 EndZ=0
    g3: LineSegment StartX=0 StartY=1610 StartZ=0 EndX=0 EndY=0 EndZ=0
    g4: LineSegment StartX=70 StartY=70 StartZ=0 EndX=850 EndY=70 EndZ=0
    g5: LineSegment StartX=850 StartY=70 StartZ=0 EndX=850 EndY=1540 EndZ=0
    g6: LineSegment StartX=850 StartY=1540 StartZ=0 EndX=70 EndY=1540 EndZ=0
    g7: LineSegment StartX=70 StartY=1540 StartZ=0 EndX=70 EndY=70 EndZ=0
    g8: LineSegment StartX=77 StartY=77 StartZ=0 EndX=843 EndY=77 EndZ=0
    g9: LineSegment StartX=843 StartY=77 StartZ=0 EndX=843 EndY=1533 EndZ=0
    g10: LineSegment StartX=843 StartY=1533 StartZ=0 EndX=77 EndY=1533 EndZ=0
    g11: LineSegment StartX=77 StartY=1533 StartZ=0 EndX=77 EndY=77 EndZ=0
    g12: LineSegment StartX=117 StartY=117 StartZ=0 EndX=803 EndY=117 EndZ=0
    g13: LineSegment StartX=803 StartY=117 StartZ=0 EndX=803 EndY=1493 EndZ=0
    g14: LineSegment StartX=803 StartY=1493 StartZ=0 EndX=117 EndY=1493 EndZ=0
    g15: LineSegment StartX=117 StartY=1493 StartZ=0 EndX=117 EndY=117 EndZ=0
  constraints (47):
    c: Coincident(g0,g1)
    c: Coincident(g1,g2)
    c: Coincident(g2,g3)
    c: Coincident(g3,g0)
    c: Horizontal(g0)
    c: Horizontal(g2)
    c: Vertical(g1)
    c: Vertical(g3)
    c: Coincident(g4,g5)
    c: Coincident(g5,g6)
    c: Coincident(g6,g7)
    c: Coincident(g7,g4)
    c: Horizontal(g4)
    c: Horizontal(g6)
    c: Vertical(g5)
    c: Vertical(g7)
    c: DistanceY(g1) = 1610  'Height'
    c: DistanceX(g0) = 920  'Width'
    c: DistanceY(g6,g2) = 70  'Frame1'
    c: DistanceX(g2,g6) = 70  'Frame2'
    c: DistanceX(g4,g0) = 70  'Frame3'
    c: DistanceY(g0,g4) = 70  'Frame4'
    c: Coincident(g0,g-1)
    c: Coincident(g8,g9)
    c: Coincident(g9,g10)
    c: Coincident(g10,g11)
    c: Coincident(g11,g8)
    c: Horizontal(g8)
    c: Horizontal(g10)
    c: Vertical(g9)
    c: Vertical(g11)
    c: Coincident(g12,g13)
    c: Coincident(g13,g14)
    c: Coincident(g14,g15)
    c: Coincident(g15,g12)
    c: Horizontal(g12)
    c: Horizontal(g14)
    c: Vertical(g13)
    c: Vertical(g15)
    c: DistanceX(g8,g12) = 40
    c: DistanceY(g8,g12) = 40
    c: DistanceX(g14,g10) = 40
    c: DistanceY(g14,g10) = 40
    c: DistanceX(g4,g8) = 7
    c: DistanceY(g4,g8) = 7
    c: DistanceX(g10,g6) = 7
    c: DistanceY(g10,g6) = 7
FEATURE [Part::FeaturePython] Window  label="ОК-92/161-001"  # Arch/BIM 170 (typed FeaturePython)
  Area = 1481200
  Base = -> Sketch370
  Frame = 70
  Height = 1610
  HoleDepth = 0
  HoleWire = 0
  HorizontalArea = 0
  IfcData = attributes={"GlobalId": {"name": "GlobalId", "type": "IfcGloballyUniqueId", "is_enum": false, "enum_values": []}, "Description": {"... (+1230 chars omitted),+1 more (map truncated)
  IfcType = 170
  LouvreSpacing = 0
  LouvreWidth = 0
  Material = -> Material011
  MoveBase = false
  MoveWithHost = true
  Normal = (0,-1,2e-16)
  Opening = 0
  OverallHeight = 1610
  OverallWidth = 920
  PartitioningType = 0
  PerimeterLength = 0
  PredefinedType = 0
  Preset = 2
  SymbolElevation = false
  SymbolPlan = false
  VerticalArea = 0
  Width = 920
  WindowParts = OuterFrame | Frame | Wire0,Wire1 | 0.0+V | 0.00+V | InnerFrame | Frame | Wire2,Wire3,Edge8,Mode1 | 0.00+V | 0.0+V | InnerGlass | Glass panel | Wire3 | 8.0 | 40.0+V
  expr: OverallHeight = .Height.Value
  expr: OverallWidth = .Width.Value
FEATURE [Sketcher::SketchObject] Sketch371
  FullyConstrained = true
  Placement = pos=(3925,7895,960) rot=(0,0.707107,0.707107;3.14159rad)
  sketch-geometry (24):
    g0: LineSegment StartX=0 StartY=0 StartZ=0 EndX=1960 EndY=0 EndZ=0
    g1: LineSegment StartX=1960 StartY=0 StartZ=0 EndX=1960 EndY=1610 EndZ=0
    g2: LineSegment StartX=1960 StartY=1610 StartZ=0 EndX=0 EndY=1610 EndZ=0
    g3: LineSegment StartX=0 StartY=1610 StartZ=0 EndX=0 EndY=0 EndZ=0
    g4: LineSegment StartX=70 StartY=70 StartZ=0 EndX=1890 EndY=70 EndZ=0
    g5: LineSegment StartX=1890 StartY=70 StartZ=0 EndX=1890 EndY=1540 EndZ=0
    g6: LineSegment StartX=1890 StartY=1540 StartZ=0 EndX=70 EndY=1540 EndZ=0
    g7: LineSegment StartX=70 StartY=1540 StartZ=0 EndX=70 EndY=70 EndZ=0
    g8: LineSegment StartX=77 StartY=77 StartZ=0 EndX=976.5 EndY=77 EndZ=0
    g9: LineSegment StartX=976.5 StartY=77 StartZ=0 EndX=976.5 EndY=1533 EndZ=0
    g10: LineSegment StartX=976.5 StartY=1533 StartZ=0 EndX=77 EndY=1533 EndZ=0
    g11: LineSegment StartX=77 StartY=1533 StartZ=0 EndX=77 EndY=77 EndZ=0
    g12: LineSegment StartX=117 StartY=117 StartZ=0 EndX=936.5 EndY=117 EndZ=0
    g13: LineSegment StartX=936.5 StartY=117 StartZ=0 EndX=936.5 EndY=1493 EndZ=0
    g14: LineSegment StartX=936.5 StartY=1493 StartZ=0 EndX=117 EndY=1493 EndZ=0
    g15: LineSegment StartX=117 StartY=1493 StartZ=0 EndX=117 EndY=117 EndZ=0
    g16: LineSegment StartX=983.5 StartY=77 StartZ=0 EndX=1883 EndY=77 EndZ=0
    g17: LineSegment StartX=1883 StartY=77 StartZ=0 EndX=1883 EndY=1533 EndZ=0
    g18: LineSegment StartX=1883 StartY=1533 StartZ=0 EndX=983.5 EndY=1533 EndZ=0
    g19: LineSegment StartX=983.5 StartY=1533 StartZ=0 EndX=983.5 EndY=77 EndZ=0
    g20: LineSegment StartX=1023.5 StartY=117 StartZ=0 EndX=1843 EndY=117 EndZ=0
    g21: LineSegment StartX=1843 StartY=117 StartZ=0 EndX=1843 EndY=1493 EndZ=0
    g22: LineSegment StartX=1843 StartY=1493 StartZ=0 EndX=1023.5 EndY=1493 EndZ=0
    g23: LineSegment StartX=1023.5 StartY=1493 StartZ=0 EndX=1023.5 EndY=117 EndZ=0
  constraints (71):
    c: Coincident(g0,g1)
    c: Coincident(g1,g2)
    c: Coincident(g2,g3)
    c: Coincident(g3,g0)
    c: Horizontal(g0)
    c: Horizontal(g2)
    c: Vertical(g1)
    c: Vertical(g3)
    c: Coincident(g4,g5)
    c: Coincident(g5,g6)
    c: Coincident(g6,g7)
    c: Coincident(g7,g4)
    c: Horizontal(g4)
    c: Horizontal(g6)
    c: Vertical(g5)
    c: Vertical(g7)
    c: DistanceY(g1) = 1610  'Height'
    c: DistanceX(g0) = 1960  'Width'
    c: DistanceY(g6,g2) = 70  'Frame1'
    c: DistanceX(g2,g6) = 70  'Frame2'
    c: DistanceX(g4,g0) = 70  'Frame3'
    c: DistanceY(g0,g4) = 70  'Frame4'
    c: Coincident(g0,g-1)
    c: Coincident(g8,g9)
    c: Coincident(g9,g10)
    c: Coincident(g10,g11)
    c: Coincident(g11,g8)
    c: Horizontal(g8)
    c: Horizontal(g10)
    c: Vertical(g9)
    c: Vertical(g11)
    c: Coincident(g12,g13)
    c: Coincident(g13,g14)
    c: Coincident(g14,g15)
    c: Coincident(g15,g12)
    c: Horizontal(g12)
    c: Horizontal(g14)
    c: Vertical(g13)
    c: Vertical(g15)
    c: Coincident(g16,g17)
    c: Coincident(g17,g18)
    c: Coincident(g18,g19)
    c: Coincident(g19,g16)
    c: Horizontal(g16)
    c: Horizontal(g18)
    c: Vertical(g17)
    c: Vertical(g19)
    c: Coincident(g20,g21)
    c: Coincident(g21,g22)
    c: Coincident(g22,g23)
    c: Coincident(g23,g20)
    c: Horizontal(g20)
    c: Horizontal(g22)
    c: Vertical(g21)
    c: Vertical(g23)
    c: DistanceY(g8,g12) = 40
    c: DistanceX(g8,g12) = 40
    c: DistanceX(g21,g17) = 40
    c: DistanceY(g21,g17) = 40
    c: DistanceX(g16,g20) = 40
    c: DistanceX(g14,g10) = 40
    c: Equal(g22,g14)
    c: DistanceY(g8,g16) = 0
    c: DistanceY(g10,g18) = 0
    c: DistanceX(g4,g8) = 7
    c: DistanceY(g4,g8) = 7
    c: DistanceX(g6,g18) = -7
    c: DistanceY(g6,g18) = -7
    c: DistanceX(g9,g19) = 7
    c: PointOnObject(g13,g22)
    c: PointOnObject(g20,g12)
FEATURE [Part::FeaturePython] Window069  label="ОК-196/161-001"  # Arch/BIM 170 (typed FeaturePython)
  Area = 3155600
  Base = -> Sketch371
  Frame = 70
  Height = 1610
  HoleDepth = 0
  HoleWire = 0
  HorizontalArea = 0
  IfcData = attributes={"GlobalId": {"name": "GlobalId", "type": "IfcGloballyUniqueId", "is_enum": false, "enum_values": []}, "Description": {"... (+1231 chars omitted),+1 more (map truncated)
  IfcType = 170
  LouvreSpacing = 0
  LouvreWidth = 0
  Material = -> Material011
  MoveBase = false
  MoveWithHost = true
  Normal = (0,-1,2e-16)
  Opening = 0
  OverallHeight = 1610
  OverallWidth = 1960
  PartitioningType = 0
  PerimeterLength = 0
  PredefinedType = 0
  Preset = 3
  SymbolElevation = false
  SymbolPlan = false
  VerticalArea = 0
  Width = 1960
  WindowParts = OuterFrame | Frame | Wire0,Wire1 | 0.0+V | 0.00+V | LeftFrame | Frame | Wire2,Wire3,Edge8,Mode1 | 0.00+V | 0.0+V | LeftGlass | Glass panel | Wire3 | 8.0 | 40.0+V | RightFrame | Frame | Wire4,Wire5,Edge6,Mode2 | 0.00+V | 0.0+V | RightGlass | Glass panel | Wire5 | 8.0 | 40.0+V
  expr: OverallHeight = .Height.Value
  expr: OverallWidth = .Width.Value
FEATURE [Sketcher::SketchObject] Sketch372
  FullyConstrained = true
  Placement = pos=(-440,3280,960) rot=(0.57735,-0.57735,-0.57735;2.0944rad)
  sketch-geometry (24):
    g0: LineSegment StartX=0 StartY=0 StartZ=0 EndX=1440 EndY=0 EndZ=0
    g1: LineSegment StartX=1440 StartY=0 StartZ=0 EndX=1440 EndY=1610 EndZ=0
    g2: LineSegment StartX=1440 StartY=1610 StartZ=0 EndX=0 EndY=1610 EndZ=0
    g3: LineSegment StartX=0 StartY=1610 StartZ=0 EndX=0 EndY=0 EndZ=0
    g4: LineSegment StartX=70 StartY=70 StartZ=0 EndX=1370 EndY=70 EndZ=0
    g5: LineSegment StartX=1370 StartY=70 StartZ=0 EndX=1370 EndY=1540 EndZ=0
    g6: LineSegment StartX=1370 StartY=1540 StartZ=0 EndX=70 EndY=1540 EndZ=0
    g7: LineSegment StartX=70 StartY=1540 StartZ=0 EndX=70 EndY=70 EndZ=0
    g8: LineSegment StartX=77 StartY=77 StartZ=0 EndX=716.5 EndY=77 EndZ=0
    g9: LineSegment StartX=716.5 StartY=77 StartZ=0 EndX=716.5 EndY=1533 EndZ=0
    g10: LineSegment StartX=716.5 StartY=1533 StartZ=0 EndX=77 EndY=1533 EndZ=0
    g11: LineSegment StartX=77 StartY=1533 StartZ=0 EndX=77 EndY=77 EndZ=0
    g12: LineSegment StartX=117 StartY=117 StartZ=0 EndX=676.5 EndY=117 EndZ=0
    g13: LineSegment StartX=676.5 StartY=117 StartZ=0 EndX=676.5 EndY=1493 EndZ=0
    g14: LineSegment StartX=676.5 StartY=1493 StartZ=0 EndX=117 EndY=1493 EndZ=0
    g15: LineSegment StartX=117 StartY=1493 StartZ=0 EndX=117 EndY=117 EndZ=0
    g16: LineSegment StartX=723.5 StartY=77 StartZ=0 EndX=1363 EndY=77 EndZ=0
    g17: LineSegment StartX=1363 StartY=77 StartZ=0 EndX=1363 EndY=1533 EndZ=0
    g18: LineSegment StartX=1363 StartY=1533 StartZ=0 EndX=723.5 EndY=1533 EndZ=0
    g19: LineSegment StartX=723.5 StartY=1533 StartZ=0 EndX=723.5 EndY=77 EndZ=0
    g20: LineSegment StartX=763.5 StartY=117 StartZ=0 EndX=1323 EndY=117 EndZ=0
    g21: LineSegment StartX=1323 StartY=117 StartZ=0 EndX=1323 EndY=1493 EndZ=0
    g22: LineSegment StartX=1323 StartY=1493 StartZ=0 EndX=763.5 EndY=1493 EndZ=0
    g23: LineSegment StartX=763.5 StartY=1493 StartZ=0 EndX=763.5 EndY=117 EndZ=0
  constraints (71):
    c: Coincident(g0,g1)
    c: Coincident(g1,g2)
    c: Coincident(g2,g3)
    c: Coincident(g3,g0)
    c: Horizontal(g0)
    c: Horizontal(g2)
    c: Vertical(g1)
    c: Vertical(g3)
    c: Coincident(g4,g5)
    c: Coincident(g5,g6)
    c: Coincident(g6,g7)
    c: Coincident(g7,g4)
    c: Horizontal(g4)
    c: Horizontal(g6)
    c: Vertical(g5)
    c: Vertical(g7)
    c: DistanceY(g1) = 1610  'Height'
    c: DistanceX(g0) = 1440  'Width'
    c: DistanceY(g6,g2) = 70  'Frame1'
    c: DistanceX(g2,g6) = 70  'Frame2'
    c: DistanceX(g4,g0) = 70  'Frame3'
    c: DistanceY(g0,g4) = 70  'Frame4'
    c: Coincident(g0,g-1)
    c: Coincident(g8,g9)
    c: Coincident(g9,g10)
    c: Coincident(g10,g11)
    c: Coincident(g11,g8)
    c: Horizontal(g8)
    c: Horizontal(g10)
    c: Vertical(g9)
    c: Vertical(g11)
    c: Coincident(g12,g13)
    c: Coincident(g13,g14)
    c: Coincident(g14,g15)
    c: Coincident(g15,g12)
    c: Horizontal(g12)
    c: Horizontal(g14)
    c: Vertical(g13)
    c: Vertical(g15)
    c: Coincident(g16,g17)
    c: Coincident(g17,g18)
    c: Coincident(g18,g19)
    c: Coincident(g19,g16)
    c: Horizontal(g16)
    c: Horizontal(g18)
    c: Vertical(g17)
    c: Vertical(g19)
    c: Coincident(g20,g21)
    c: Coincident(g21,g22)
    c: Coincident(g22,g23)
    c: Coincident(g23,g20)
    c: Horizontal(g20)
    c: Horizontal(g22)
    c: Vertical(g21)
    c: Vertical(g23)
    c: DistanceY(g8,g12) = 40
    c: DistanceX(g8,g12) = 40
    c: DistanceX(g21,g17) = 40
    c: DistanceY(g21,g17) = 40
    c: DistanceX(g16,g20) = 40
    c: DistanceX(g14,g10) = 40
    c: Equal(g22,g14)
    c: DistanceY(g8,g16) = 0
    c: DistanceY(g10,g18) = 0
    c: DistanceX(g4,g8) = 7
    c: DistanceY(g4,g8) = 7
    c: DistanceX(g6,g18) = -7
    c: DistanceY(g6,g18) = -7
    c: DistanceX(g9,g19) = 7
    c: PointOnObject(g13,g22)
    c: PointOnObject(g20,g12)
FEATURE [Part::FeaturePython] Window070  label="ОК-144/161-001"  # Arch/BIM 170 (typed FeaturePython)
  Area = 2318400
  Base = -> Sketch372
  Frame = 70
  Height = 1610
  HoleDepth = 0
  HoleWire = 0
  HorizontalArea = 0
  IfcData = attributes={"GlobalId": {"name": "GlobalId", "type": "IfcGloballyUniqueId", "is_enum": false, "enum_values": []}, "Description": {"... (+1231 chars omitted),+1 more (map truncated)
  IfcType = 170
  LouvreSpacing = 0
  LouvreWidth = 0
  Material = -> Material011
  MoveBase = false
  MoveWithHost = true
  Normal = (1,0,0)
  Opening = 0
  OverallHeight = 1610
  OverallWidth = 1440
  PartitioningType = 0
  PerimeterLength = 0
  PredefinedType = 0
  Preset = 3
  SymbolElevation = false
  SymbolPlan = false
  VerticalArea = 0
  Width = 1440
  WindowParts = <same value as first occurrence — deduplicated (x3 in doc)>
  expr: OverallHeight = .Height.Value
  expr: OverallWidth = .Width.Value
FEATURE [Sketcher::SketchObject] Sketch373
  FullyConstrained = true
  Placement = pos=(12960,1320,1190) rot=(0.57735,0.57735,0.57735;2.0944rad)
  sketch-geometry (24):
    g0: LineSegment StartX=0 StartY=0 StartZ=0 EndX=1960 EndY=0 EndZ=0
    g1: LineSegment StartX=1960 StartY=0 StartZ=0 EndX=1960 EndY=1380 EndZ=0
    g2: LineSegment StartX=1960 StartY=1380 StartZ=0 EndX=0 EndY=1380 EndZ=0
    g3: LineSegment StartX=0 StartY=1380 StartZ=0 EndX=0 EndY=0 EndZ=0
    g4: LineSegment StartX=70 StartY=70 StartZ=0 EndX=1890 EndY=70 EndZ=0
    g5: LineSegment StartX=1890 StartY=70 StartZ=0 EndX=1890 EndY=1310 EndZ=0
    g6: LineSegment StartX=1890 StartY=1310 StartZ=0 EndX=70 EndY=1310 EndZ=0
    g7: LineSegment StartX=70 StartY=1310 StartZ=0 EndX=70 EndY=70 EndZ=0
    g8: LineSegment StartX=77 StartY=77 StartZ=0 EndX=976.5 EndY=77 EndZ=0
    g9: LineSegment StartX=976.5 StartY=77 StartZ=0 EndX=976.5 EndY=1303 EndZ=0
    g10: LineSegment StartX=976.5 StartY=1303 StartZ=0 EndX=77 EndY=1303 EndZ=0
    g11: LineSegment StartX=77 StartY=1303 StartZ=0 EndX=77 EndY=77 EndZ=0
    g12: LineSegment StartX=117 StartY=117 StartZ=0 EndX=936.5 EndY=117 EndZ=0
    g13: LineSegment StartX=936.5 StartY=117 StartZ=0 EndX=936.5 EndY=1263 EndZ=0
    g14: LineSegment StartX=936.5 StartY=1263 StartZ=0 EndX=117 EndY=1263 EndZ=0
    g15: LineSegment StartX=117 StartY=1263 StartZ=0 EndX=117 EndY=117 EndZ=0
    g16: LineSegment StartX=983.5 StartY=77 StartZ=0 EndX=1883 EndY=77 EndZ=0
    g17: LineSegment StartX=1883 StartY=77 StartZ=0 EndX=1883 EndY=1303 EndZ=0
    g18: LineSegment StartX=1883 StartY=1303 StartZ=0 EndX=983.5 EndY=1303 EndZ=0
    g19: LineSegment StartX=983.5 StartY=1303 StartZ=0 EndX=983.5 EndY=77 EndZ=0
    g20: LineSegment StartX=1023.5 StartY=117 StartZ=0 EndX=1843 EndY=117 EndZ=0
    g21: LineSegment StartX=1843 StartY=117 StartZ=0 EndX=1843 EndY=1263 EndZ=0
    g22: LineSegment StartX=1843 StartY=1263 StartZ=0 EndX=1023.5 EndY=1263 EndZ=0
    g23: LineSegment StartX=1023.5 StartY=1263 StartZ=0 EndX=1023.5 EndY=117 EndZ=0
  constraints (71):
    c: Coincident(g0,g1)
    c: Coincident(g1,g2)
    c: Coincident(g2,g3)
    c: Coincident(g3,g0)
    c: Horizontal(g0)
    c: Horizontal(g2)
    c: Vertical(g1)
    c: Vertical(g3)
    c: Coincident(g4,g5)
    c: Coincident(g5,g6)
    c: Coincident(g6,g7)
    c: Coincident(g7,g4)
    c: Horizontal(g4)
    c: Horizontal(g6)
    c: Vertical(g5)
    c: Vertical(g7)
    c: DistanceY(g1) = 1380  'Height'
    c: DistanceX(g0) = 1960  'Width'
    c: DistanceY(g6,g2) = 70  'Frame1'
    c: DistanceX(g2,g6) = 70  'Frame2'
    c: DistanceX(g4,g0) = 70  'Frame3'
    c: DistanceY(g0,g4) = 70  'Frame4'
    c: Coincident(g0,g-1)
    c: Coincident(g8,g9)
    c: Coincident(g9,g10)
    c: Coincident(g10,g11)
    c: Coincident(g11,g8)
    c: Horizontal(g8)
    c: Horizontal(g10)
    c: Vertical(g9)
    c: Vertical(g11)
    c: Coincident(g12,g13)
    c: Coincident(g13,g14)
    c: Coincident(g14,g15)
    c: Coincident(g15,g12)
    c: Horizontal(g12)
    c: Horizontal(g14)
    c: Vertical(g13)
    c: Vertical(g15)
    c: Coincident(g16,g17)
    c: Coincident(g17,g18)
    c: Coincident(g18,g19)
    c: Coincident(g19,g16)
    c: Horizontal(g16)
    c: Horizontal(g18)
    c: Vertical(g17)
    c: Vertical(g19)
    c: Coincident(g20,g21)
    c: Coincident(g21,g22)
    c: Coincident(g22,g23)
    c: Coincident(g23,g20)
    c: Horizontal(g20)
    c: Horizontal(g22)
    c: Vertical(g21)
    c: Vertical(g23)
    c: DistanceY(g8,g12) = 40
    c: DistanceX(g8,g12) = 40
    c: DistanceX(g21,g17) = 40
    c: DistanceY(g21,g17) = 40
    c: DistanceX(g16,g20) = 40
    c: DistanceX(g14,g10) = 40
    c: Equal(g22,g14)
    c: DistanceY(g8,g16) = 0
    c: DistanceY(g10,g18) = 0
    c: DistanceX(g4,g8) = 7
    c: DistanceY(g4,g8) = 7
    c: DistanceX(g6,g18) = -7
    c: DistanceY(g6,g18) = -7
    c: DistanceX(g9,g19) = 7
    c: PointOnObject(g13,g22)
    c: PointOnObject(g20,g12)
FEATURE [Part::FeaturePython] Window071  label="ОК-196/138-001"  # Arch/BIM 170 (typed FeaturePython)
  Area = 2704800
  Base = -> Sketch373
  Frame = 70
  Height = 1380
  HoleDepth = 0
  HoleWire = 0
  HorizontalArea = 0
  IfcData = attributes={"GlobalId": {"name": "GlobalId", "type": "IfcGloballyUniqueId", "is_enum": false, "enum_values": []}, "Description": {"... (+1231 chars omitted),+1 more (map truncated)
  IfcType = 170
  LouvreSpacing = 0
  LouvreWidth = 0
  Material = -> Material011
  MoveBase = false
  MoveWithHost = true
  Normal = (-1,0,0)
  Opening = 0
  OverallHeight = 1380
  OverallWidth = 1960
  PartitioningType = 0
  PerimeterLength = 0
  PredefinedType = 0
  Preset = 3
  SymbolElevation = false
  SymbolPlan = false
  VerticalArea = 0
  Width = 1960
  WindowParts = <same value as first occurrence — deduplicated (x3 in doc)>
  expr: OverallHeight = .Height.Value
  expr: OverallWidth = .Width.Value
FEATURE [Sketcher::SketchObject] Sketch374
  FullyConstrained = true
  Placement = pos=(12960,4050,0) rot=(0.57735,0.57735,0.57735;2.0944rad)
  sketch-geometry (16):
    g0: LineSegment StartX=0 StartY=0 StartZ=0 EndX=920 EndY=0 EndZ=0
    g1: LineSegment StartX=920 StartY=0 StartZ=0 EndX=920 EndY=1380 EndZ=0
    g2: LineSegment StartX=920 StartY=1380 StartZ=0 EndX=0 EndY=1380 EndZ=0
    g3: LineSegment StartX=0 StartY=1380 StartZ=0 EndX=0 EndY=0 EndZ=0
    g4: LineSegment StartX=70 StartY=70 StartZ=0 EndX=850 EndY=70 EndZ=0
    g5: LineSegment StartX=850 StartY=70 StartZ=0 EndX=850 EndY=1310 EndZ=0
    g6: LineSegment StartX=850 StartY=1310 StartZ=0 EndX=70 EndY=1310 EndZ=0
    g7: LineSegment StartX=70 StartY=1310 StartZ=0 EndX=70 EndY=70 EndZ=0
    g8: LineSegment StartX=77 StartY=77 StartZ=0 EndX=843 EndY=77 EndZ=0
    g9: LineSegment StartX=843 StartY=77 StartZ=0 EndX=843 EndY=1303 EndZ=0
    g10: LineSegment StartX=843 StartY=1303 StartZ=0 EndX=77 EndY=1303 EndZ=0
    g11: LineSegment StartX=77 StartY=1303 StartZ=0 EndX=77 EndY=77 EndZ=0
    g12: LineSegment StartX=117 StartY=117 StartZ=0 EndX=803 EndY=117 EndZ=0
    g13: LineSegment StartX=803 StartY=117 StartZ=0 EndX=803 EndY=1263 EndZ=0
    g14: LineSegment StartX=803 StartY=1263 StartZ=0 EndX=117 EndY=1263 EndZ=0
    g15: LineSegment StartX=117 StartY=1263 StartZ=0 EndX=117 EndY=117 EndZ=0
  constraints (47):
    c: Coincident(g0,g1)
    c: Coincident(g1,g2)
    c: Coincident(g2,g3)
    c: Coincident(g3,g0)
    c: Horizontal(g0)
    c: Horizontal(g2)
    c: Vertical(g1)
    c: Vertical(g3)
    c: Coincident(g4,g5)
    c: Coincident(g5,g6)
    c: Coincident(g6,g7)
    c: Coincident(g7,g4)
    c: Horizontal(g4)
    c: Horizontal(g6)
    c: Vertical(g5)
    c: Vertical(g7)
    c: DistanceY(g1) = 1380  'Height'
    c: DistanceX(g0) = 920  'Width'
    c: DistanceY(g6,g2) = 70  'Frame1'
    c: DistanceX(g2,g6) = 70  'Frame2'
    c: DistanceX(g4,g0) = 70  'Frame3'
    c: DistanceY(g0,g4) = 70  'Frame4'
    c: Coincident(g0,g-1)
    c: Coincident(g8,g9)
    c: Coincident(g9,g10)
    c: Coincident(g10,g11)
    c: Coincident(g11,g8)
    c: Horizontal(g8)
    c: Horizontal(g10)
    c: Vertical(g9)
    c: Vertical(g11)
    c: Coincident(g12,g13)
    c: Coincident(g13,g14)
    c: Coincident(g14,g15)
    c: Coincident(g15,g12)
    c: Horizontal(g12)
    c: Horizontal(g14)
    c: Vertical(g13)
    c: Vertical(g15)
    c: DistanceX(g8,g12) = 40
    c: DistanceY(g8,g12) = 40
    c: DistanceX(g14,g10) = 40
    c: DistanceY(g14,g10) = 40
    c: DistanceX(g4,g8) = 7
    c: DistanceY(g4,g8) = 7
    c: DistanceX(g10,g6) = 7
    c: DistanceY(g10,g6) = 7
FEATURE [Part::FeaturePython] Window072  label="ОК-92/138-001"  # Arch/BIM 170 (typed FeaturePython)
  Area = 1269600
  Base = -> Sketch374
  Frame = 70
  Height = 1380
  HoleDepth = 0
  HoleWire = 0
  HorizontalArea = 0
  IfcData = attributes={"GlobalId": {"name": "GlobalId", "type": "IfcGloballyUniqueId", "is_enum": false, "enum_values": []}, "Description": {"... (+1230 chars omitted),+1 more (map truncated)
  IfcType = 170
  LouvreSpacing = 0
  LouvreWidth = 0
  Material = -> Material011
  MoveBase = false
  MoveWithHost = true
  Normal = (-1,-9e-16,9e-16)
  Opening = 0
  OverallHeight = 1380
  OverallWidth = 920
  PartitioningType = 0
  PerimeterLength = 0
  Placement = pos=(0,0,1190) rot=(0,0,1;0rad)
  PredefinedType = 0
  Preset = 2
  SymbolElevation = false
  SymbolPlan = false
  VerticalArea = 0
  Width = 920
  WindowParts = OuterFrame | Frame | Wire0,Wire1 | 0.0+V | 0.00+V | InnerFrame | Frame | Wire2,Wire3,Edge8,Mode1 | 0.00+V | 0.0+V | InnerGlass | Glass panel | Wire3 | 8.0 | 40.0+V
  expr: OverallHeight = .Height.Value
  expr: OverallWidth = .Width.Value
FEATURE [Sketcher::SketchObject] Sketch375
  FullyConstrained = true
  Placement = pos=(4175,-435,960) rot=(1,0,0;1.5708rad)
  sketch-geometry (16):
    g0: LineSegment StartX=0 StartY=0 StartZ=0 EndX=660 EndY=0 EndZ=0
    g1: LineSegment StartX=660 StartY=0 StartZ=0 EndX=660 EndY=1380 EndZ=0
    g2: LineSegment StartX=660 StartY=1380 StartZ=0 EndX=0 EndY=1380 EndZ=0
    g3: LineSegment StartX=0 StartY=1380 StartZ=0 EndX=0 EndY=0 EndZ=0
    g4: LineSegment StartX=70 StartY=70 StartZ=0 EndX=590 EndY=70 EndZ=0
    g5: LineSegment StartX=590 StartY=70 StartZ=0 EndX=590 EndY=1310 EndZ=0
    g6: LineSegment StartX=590 StartY=1310 StartZ=0 EndX=70 EndY=1310 EndZ=0
    g7: LineSegment StartX=70 StartY=1310 StartZ=0 EndX=70 EndY=70 EndZ=0
    g8: LineSegment StartX=77 StartY=77 StartZ=0 EndX=583 EndY=77 EndZ=0
    g9: LineSegment StartX=583 StartY=77 StartZ=0 EndX=583 EndY=1303 EndZ=0
    g10: LineSegment StartX=583 StartY=1303 StartZ=0 EndX=77 EndY=1303 EndZ=0
    g11: LineSegment StartX=77 StartY=1303 StartZ=0 EndX=77 EndY=77 EndZ=0
    g12: LineSegment StartX=117 StartY=117 StartZ=0 EndX=543 EndY=117 EndZ=0
    g13: LineSegment StartX=543 StartY=117 StartZ=0 EndX=543 EndY=1263 EndZ=0
    g14: LineSegment StartX=543 StartY=1263 StartZ=0 EndX=117 EndY=1263 EndZ=0
    g15: LineSegment StartX=117 StartY=1263 StartZ=0 EndX=117 EndY=117 EndZ=0
  constraints (47):
    c: Coincident(g0,g1)
    c: Coincident(g1,g2)
    c: Coincident(g2,g3)
    c: Coincident(g3,g0)
    c: Horizontal(g0)
    c: Horizontal(g2)
    c: Vertical(g1)
    c: Vertical(g3)
    c: Coincident(g4,g5)
    c: Coincident(g5,g6)
    c: Coincident(g6,g7)
    c: Coincident(g7,g4)
    c: Horizontal(g4)
    c: Horizontal(g6)
    c: Vertical(g5)
    c: Vertical(g7)
    c: DistanceY(g1) = 1380  'Height'
    c: DistanceX(g0) = 660  'Width'
    c: DistanceY(g6,g2) = 70  'Frame1'
    c: DistanceX(g2,g6) = 70  'Frame2'
    c: DistanceX(g4,g0) = 70  'Frame3'
    c: DistanceY(g0,g4) = 70  'Frame4'
    c: Coincident(g0,g-1)
    c: Coincident(g8,g9)
    c: Coincident(g9,g10)
    c: Coincident(g10,g11)
    c: Coincident(g11,g8)
    c: Horizontal(g8)
    c: Horizontal(g10)
    c: Vertical(g9)
    c: Vertical(g11)
    c: Coincident(g12,g13)
    c: Coincident(g13,g14)
    c: Coincident(g14,g15)
    c: Coincident(g15,g12)
    c: Horizontal(g12)
    c: Horizontal(g14)
    c: Vertical(g13)
    c: Vertical(g15)
    c: DistanceX(g8,g12) = 40
    c: DistanceY(g8,g12) = 40
    c: DistanceX(g14,g10) = 40
    c: DistanceY(g14,g10) = 40
    c: DistanceX(g4,g8) = 7
    c: DistanceY(g4,g8) = 7
    c: DistanceX(g10,g6) = 7
    c: DistanceY(g10,g6) = 7
FEATURE [Part::FeaturePython] Window073  label="ОК-66/138-001"  # Arch/BIM 170 (typed FeaturePython)
  Area = 910800
  Base = -> Sketch375
  Frame = 70
  Height = 1380
  HoleDepth = 0
  HoleWire = 0
  HorizontalArea = 0
  IfcData = attributes={"GlobalId": {"name": "GlobalId", "type": "IfcGloballyUniqueId", "is_enum": false, "enum_values": []}, "Description": {"... (+1230 chars omitted),+1 more (map truncated)
  IfcType = 170
  LouvreSpacing = 0
  LouvreWidth = 0
  Material = -> Material011
  MoveBase = false
  MoveWithHost = true
  Normal = (0,1,-2e-16)
  Opening = 0
  OverallHeight = 1380
  OverallWidth = 660
  PartitioningType = 0
  PerimeterLength = 0
  PredefinedType = 0
  Preset = 2
  SymbolElevation = false
  SymbolPlan = false
  VerticalArea = 0
  Width = 660
  WindowParts = OuterFrame | Frame | Wire0,Wire1 | 0.0+V | 0.00+V | InnerFrame | Frame | Wire2,Wire3,Edge8,Mode1 | 0.00+V | 0.0+V | InnerGlass | Glass panel | Wire3 | 8.0 | 40.0+V
  expr: OverallHeight = .Height.Value
  expr: OverallWidth = .Width.Value
FEATURE [Sketcher::SketchObject] Sketch376
  FullyConstrained = true
  Placement = pos=(7555,-435,960) rot=(1,0,0;1.5708rad)
  sketch-geometry (16):
    g0: LineSegment StartX=0 StartY=0 StartZ=0 EndX=660 EndY=0 EndZ=0
    g1: LineSegment StartX=660 StartY=0 StartZ=0 EndX=660 EndY=1380 EndZ=0
    g2: LineSegment StartX=660 StartY=1380 StartZ=0 EndX=0 EndY=1380 EndZ=0
    g3: LineSegment StartX=0 StartY=1380 StartZ=0 EndX=0 EndY=0 EndZ=0
    g4: LineSegment StartX=70 StartY=70 StartZ=0 EndX=590 EndY=70 EndZ=0
    g5: LineSegment StartX=590 StartY=70 StartZ=0 EndX=590 EndY=1310 EndZ=0
    g6: LineSegment StartX=590 StartY=1310 StartZ=0 EndX=70 EndY=1310 EndZ=0
    g7: LineSegment StartX=70 StartY=1310 StartZ=0 EndX=70 EndY=70 EndZ=0
    g8: LineSegment StartX=77 StartY=77 StartZ=0 EndX=583 EndY=77 EndZ=0
    g9: LineSegment StartX=583 StartY=77 StartZ=0 EndX=583 EndY=1303 EndZ=0
    g10: LineSegment StartX=583 StartY=1303 StartZ=0 EndX=77 EndY=1303 EndZ=0
    g11: LineSegment StartX=77 StartY=1303 StartZ=0 EndX=77 EndY=77 EndZ=0
    g12: LineSegment StartX=117 StartY=117 StartZ=0 EndX=543 EndY=117 EndZ=0
    g13: LineSegment StartX=543 StartY=117 StartZ=0 EndX=543 EndY=1263 EndZ=0
    g14: LineSegment StartX=543 StartY=1263 StartZ=0 EndX=117 EndY=1263 EndZ=0
    g15: LineSegment StartX=117 StartY=1263 StartZ=0 EndX=117 EndY=117 EndZ=0
  constraints (47):
    c: Coincident(g0,g1)
    c: Coincident(g1,g2)
    c: Coincident(g2,g3)
    c: Coincident(g3,g0)
    c: Horizontal(g0)
    c: Horizontal(g2)
    c: Vertical(g1)
    c: Vertical(g3)
    c: Coincident(g4,g5)
    c: Coincident(g5,g6)
    c: Coincident(g6,g7)
    c: Coincident(g7,g4)
    c: Horizontal(g4)
    c: Horizontal(g6)
    c: Vertical(g5)
    c: Vertical(g7)
    c: DistanceY(g1) = 1380  'Height'
    c: DistanceX(g0) = 660  'Width'
    c: DistanceY(g6,g2) = 70  'Frame1'
    c: DistanceX(g2,g6) = 70  'Frame2'
    c: DistanceX(g4,g0) = 70  'Frame3'
    c: DistanceY(g0,g4) = 70  'Frame4'
    c: Coincident(g0,g-1)
    c: Coincident(g8,g9)
    c: Coincident(g9,g10)
    c: Coincident(g10,g11)
    c: Coincident(g11,g8)
    c: Horizontal(g8)
    c: Horizontal(g10)
    c: Vertical(g9)
    c: Vertical(g11)
    c: Coincident(g12,g13)
    c: Coincident(g13,g14)
    c: Coincident(g14,g15)
    c: Coincident(g15,g12)
    c: Horizontal(g12)
    c: Horizontal(g14)
    c: Vertical(g13)
    c: Vertical(g15)
    c: DistanceX(g8,g12) = 40
    c: DistanceY(g8,g12) = 40
    c: DistanceX(g14,g10) = 40
    c: DistanceY(g14,g10) = 40
    c: DistanceX(g4,g8) = 7
    c: DistanceY(g4,g8) = 7
    c: DistanceX(g10,g6) = 7
    c: DistanceY(g10,g6) = 7
FEATURE [Part::FeaturePython] Window074  label="ОК-66/138-002"  # Arch/BIM 170 (typed FeaturePython)
  Area = 910800
  Base = -> Sketch376
  Frame = 70
  Height = 1380
  HoleDepth = 0
  HoleWire = 0
  HorizontalArea = 0
  IfcData = attributes={"GlobalId": {"name": "GlobalId", "type": "IfcGloballyUniqueId", "is_enum": false, "enum_values": []}, "Description": {"... (+1230 chars omitted),+1 more (map truncated)
  IfcType = 170
  LouvreSpacing = 0
  LouvreWidth = 0
  Material = -> Material011
  MoveBase = false
  MoveWithHost = true
  Normal = (0,1,-2e-16)
  Opening = 0
  OverallHeight = 1380
  OverallWidth = 660
  PartitioningType = 0
  PerimeterLength = 0
  PredefinedType = 0
  Preset = 2
  SymbolElevation = false
  SymbolPlan = false
  VerticalArea = 0
  Width = 660
  WindowParts = OuterFrame | Frame | Wire0,Wire1 | 0.0+V | 0.00+V | InnerFrame | Frame | Wire2,Wire3,Edge8,Mode1 | 0.00+V | 0.0+V | InnerGlass | Glass panel | Wire3 | 8.0 | 40.0+V
  expr: OverallHeight = .Height.Value
  expr: OverallWidth = .Width.Value
FEATURE [Sketcher::SketchObject] Sketch379
  FullyConstrained = true
  Placement = pos=(10555,7895,-70) rot=(0,0.707107,0.707107;3.14159rad)
  sketch-geometry (24):
    g0: LineSegment StartX=0 StartY=0 StartZ=0 EndX=1960 EndY=0 EndZ=0
    g1: LineSegment StartX=1960 StartY=0 StartZ=0 EndX=1960 EndY=2630 EndZ=0
    g2: LineSegment StartX=1960 StartY=2630 StartZ=0 EndX=0 EndY=2630 EndZ=0
    g3: LineSegment StartX=0 StartY=2630 StartZ=0 EndX=0 EndY=0 EndZ=0
    g4: LineSegment StartX=70 StartY=70 StartZ=0 EndX=1890 EndY=70 EndZ=0
    g5: LineSegment StartX=1890 StartY=70 StartZ=0 EndX=1890 EndY=2560 EndZ=0
    g6: LineSegment StartX=1890 StartY=2560 StartZ=0 EndX=70 EndY=2560 EndZ=0
    g7: LineSegment StartX=70 StartY=2560 StartZ=0 EndX=70 EndY=70 EndZ=0
    g8: LineSegment StartX=77 StartY=77 StartZ=0 EndX=976.5 EndY=77 EndZ=0
    g9: LineSegment StartX=976.5 StartY=77 StartZ=0 EndX=976.5 EndY=2553 EndZ=0
    g10: LineSegment StartX=976.5 StartY=2553 StartZ=0 EndX=77 EndY=2553 EndZ=0
    g11: LineSegment StartX=77 StartY=2553 StartZ=0 EndX=77 EndY=77 EndZ=0
    g12: LineSegment StartX=117 StartY=117 StartZ=0 EndX=936.5 EndY=117 EndZ=0
    g13: LineSegment StartX=936.5 StartY=117 StartZ=0 EndX=936.5 EndY=2513 EndZ=0
    g14: LineSegment StartX=936.5 StartY=2513 StartZ=0 EndX=117 EndY=2513 EndZ=0
    g15: LineSegment StartX=117 StartY=2513 StartZ=0 EndX=117 EndY=117 EndZ=0
    g16: LineSegment StartX=983.5 StartY=77 StartZ=0 EndX=1883 EndY=77 EndZ=0
    g17: LineSegment StartX=1883 StartY=77 StartZ=0 EndX=1883 EndY=2553 EndZ=0
    g18: LineSegment StartX=1883 StartY=2553 StartZ=0 EndX=983.5 EndY=2553 EndZ=0
    g19: LineSegment StartX=983.5 StartY=2553 StartZ=0 EndX=983.5 EndY=77 EndZ=0
    g20: LineSegment StartX=1023.5 StartY=117 StartZ=0 EndX=1843 EndY=117 EndZ=0
    g21: LineSegment StartX=1843 StartY=117 StartZ=0 EndX=1843 EndY=2513 EndZ=0
    g22: LineSegment StartX=1843 StartY=2513 StartZ=0 EndX=1023.5 EndY=2513 EndZ=0
    g23: LineSegment StartX=1023.5 StartY=2513 StartZ=0 EndX=1023.5 EndY=117 EndZ=0
  constraints (71):
    c: Coincident(g0,g1)
    c: Coincident(g1,g2)
    c: Coincident(g2,g3)
    c: Coincident(g3,g0)
    c: Horizontal(g0)
    c: Horizontal(g2)
    c: Vertical(g1)
    c: Vertical(g3)
    c: Coincident(g4,g5)
    c: Coincident(g5,g6)
    c: Coincident(g6,g7)
    c: Coincident(g7,g4)
    c: Horizontal(g4)
    c: Horizontal(g6)
    c: Vertical(g5)
    c: Vertical(g7)
    c: DistanceY(g1) = 2630  'Height'
    c: DistanceX(g0) = 1960  'Width'
    c: DistanceY(g6,g2) = 70  'Frame1'
    c: DistanceX(g2,g6) = 70  'Frame2'
    c: DistanceX(g4,g0) = 70  'Frame3'
    c: DistanceY(g0,g4) = 70  'Frame4'
    c: Coincident(g0,g-1)
    c: Coincident(g8,g9)
    c: Coincident(g9,g10)
    c: Coincident(g10,g11)
    c: Coincident(g11,g8)
    c: Horizontal(g8)
    c: Horizontal(g10)
    c: Vertical(g9)
    c: Vertical(g11)
    c: Coincident(g12,g13)
    c: Coincident(g13,g14)
    c: Coincident(g14,g15)
    c: Coincident(g15,g12)
    c: Horizontal(g12)
    c: Horizontal(g14)
    c: Vertical(g13)
    c: Vertical(g15)
    c: Coincident(g16,g17)
    c: Coincident(g17,g18)
    c: Coincident(g18,g19)
    c: Coincident(g19,g16)
    c: Horizontal(g16)
    c: Horizontal(g18)
    c: Vertical(g17)
    c: Vertical(g19)
    c: Coincident(g20,g21)
    c: Coincident(g21,g22)
    c: Coincident(g22,g23)
    c: Coincident(g23,g20)
    c: Horizontal(g20)
    c: Horizontal(g22)
    c: Vertical(g21)
    c: Vertical(g23)
    c: DistanceY(g8,g12) = 40
    c: DistanceX(g8,g12) = 40
    c: DistanceX(g21,g17) = 40
    c: DistanceY(g21,g17) = 40
    c: DistanceX(g16,g20) = 40
    c: DistanceX(g14,g10) = 40
    c: Equal(g22,g14)
    c: DistanceY(g8,g16) = 0
    c: DistanceY(g10,g18) = 0
    c: DistanceX(g4,g8) = 7
    c: DistanceY(g4,g8) = 7
    c: DistanceX(g6,g18) = -7
    c: DistanceY(g6,g18) = -7
    c: DistanceX(g9,g19) = 7
    c: PointOnObject(g13,g22)
    c: PointOnObject(g12,g20)
FEATURE [Part::FeaturePython] Window077  label="ОК-196/263-001"  # Arch/BIM 170 (typed FeaturePython)
  Area = 5154800
  Base = -> Sketch379
  Frame = 70
  Height = 2630
  HoleDepth = 0
  HoleWire = 0
  HorizontalArea = 0
  IfcData = attributes={"GlobalId": {"name": "GlobalId", "type": "IfcGloballyUniqueId", "is_enum": false, "enum_values": []}, "Description": {"... (+1231 chars omitted),+1 more (map truncated)
  IfcType = 170
  LouvreSpacing = 0
  LouvreWidth = 0
  Material = -> Material011
  MoveBase = false
  MoveWithHost = true
  Normal = (0,-1,2e-16)
  Opening = 0
  OverallHeight = 2630
  OverallWidth = 1960
  PartitioningType = 0
  PerimeterLength = 0
  PredefinedType = 0
  Preset = 5
  SymbolElevation = false
  SymbolPlan = false
  VerticalArea = 0
  Width = 1960
  WindowParts = OuterFrame | Frame | Wire0,Wire1 | 50.0+V | 0.00+V | LeftFrame | Frame | Wire2,Wire3 | 50.0 | 0.0+V | LeftGlass | Glass panel | Wire3 | 5.0 | 25.0+V | RightFrame | Frame | Wire4,Wire5 | 50.0 | 50.0+V | RightGlass | Glass panel | Wire5 | 5.0 | 75.0+V
  expr: OverallHeight = .Height.Value
  expr: OverallWidth = .Width.Value
FEATURE [Sketcher::SketchObject] Sketch381
  FullyConstrained = true
  Placement = pos=(6720,-435,-40) rot=(0,0.707107,0.707107;3.14159rad)
  sketch-geometry (16):
    g0: LineSegment StartX=0 StartY=0 StartZ=0 EndX=1050 EndY=0 EndZ=0
    g1: LineSegment StartX=1050 StartY=0 StartZ=0 EndX=1050 EndY=2320 EndZ=0
    g2: LineSegment StartX=1050 StartY=2320 StartZ=0 EndX=0 EndY=2320 EndZ=0
    g3: LineSegment StartX=0 StartY=2320 StartZ=0 EndX=0 EndY=0 EndZ=0
    g4: LineSegment StartX=40 StartY=0 StartZ=0 EndX=1010 EndY=0 EndZ=0
    g5: LineSegment StartX=1010 StartY=0 StartZ=0 EndX=1010 EndY=2280 EndZ=0
    g6: LineSegment StartX=1010 StartY=2280 StartZ=0 EndX=40 EndY=2280 EndZ=0
    g7: LineSegment StartX=40 StartY=2280 StartZ=0 EndX=40 EndY=0 EndZ=0
    g8: LineSegment StartX=44 StartY=4 StartZ=0 EndX=1006 EndY=4 EndZ=0
    g9: LineSegment StartX=1006 StartY=4 StartZ=0 EndX=1006 EndY=2276 EndZ=0
    g10: LineSegment StartX=1006 StartY=2276 StartZ=0 EndX=44 EndY=2276 EndZ=0
    g11: LineSegment StartX=44 StartY=2276 StartZ=0 EndX=44 EndY=4 EndZ=0
    g12: LineSegment StartX=444 StartY=1204 StartZ=0 EndX=606 EndY=1204 EndZ=0
    g13: LineSegment StartX=606 StartY=1204 StartZ=0 EndX=606 EndY=1876 EndZ=0
    g14: LineSegment StartX=606 StartY=1876 StartZ=0 EndX=444 EndY=1876 EndZ=0
    g15: LineSegment StartX=444 StartY=1876 StartZ=0 EndX=444 EndY=1204 EndZ=0
  constraints (47):
    c: Coincident(g0,g1)
    c: Coincident(g1,g2)
    c: Coincident(g2,g3)
    c: Coincident(g3,g0)
    c: Horizontal(g0)
    c: Horizontal(g2)
    c: Vertical(g1)
    c: Vertical(g3)
    c: Coincident(g4,g5)
    c: Coincident(g5,g6)
    c: Coincident(g6,g7)
    c: Coincident(g7,g4)
    c: Horizontal(g4)
    c: Horizontal(g6)
    c: Vertical(g5)
    c: Vertical(g7)
    c: DistanceY(g1) = 2320  'Height'
    c: DistanceX(g0) = 1050  'Width'
    c: DistanceY(g6,g2) = 40  'Frame1'
    c: DistanceX(g2,g6) = 40  'Frame2'
    c: DistanceX(g4,g0) = 40  'Frame3'
    c: DistanceY(g0,g4) = 0
    c: Coincident(g0,g-1)
    c: Coincident(g8,g9)
    c: Coincident(g9,g10)
    c: Coincident(g10,g11)
    c: Coincident(g11,g8)
    c: Horizontal(g8)
    c: Horizontal(g10)
    c: Vertical(g9)
    c: Vertical(g11)
    c: Coincident(g12,g13)
    c: Coincident(g13,g14)
    c: Coincident(g14,g15)
    c: Coincident(g15,g12)
    c: Horizontal(g12)
    c: Horizontal(g14)
    c: Vertical(g13)
    c: Vertical(g15)
    c: DistanceX(g8,g12) = 400
    c: DistanceY(g8,g12) = 1200
    c: DistanceX(g14,g10) = 400
    c: DistanceY(g14,g10) = 400
    c: DistanceX(g4,g8) = 4
    c: DistanceY(g4,g8) = 4
    c: DistanceX(g10,g6) = 4
    c: DistanceY(g10,g6) = 4
FEATURE [Part::FeaturePython] Window078  label="Д-105/232-001"  # Arch/BIM 41 (typed FeaturePython)
  Area = 2436000
  Base = -> Sketch381
  Frame = 40
  Height = 2320
  HoleDepth = 0
  HoleWire = 0
  HorizontalArea = 0
  IfcData = attributes={"GlobalId": {"name": "GlobalId", "type": "IfcGloballyUniqueId", "is_enum": false, "enum_values": []}, "Description": {"... (+1934 chars omitted),+1 more (map truncated)
  IfcType = 41
  LouvreSpacing = 0
  LouvreWidth = 0
  Material = -> Material011
  MoveBase = false
  MoveWithHost = true
  Normal = (0,-1,2e-16)
  Offset = 20
  Opening = 0
  OperationType = 0
  OverallHeight = 2320
  OverallWidth = 1050
  PerimeterLength = 0
  PredefinedType = 0
  Preset = 7
  SymbolElevation = false
  SymbolPlan = false
  VerticalArea = 0
  Width = 1050
  WindowParts = OuterFrame | Frame | Wire0,Wire1 | 40.0+V | 0.00+V | InnerFrame | Frame | Wire2,Wire3,Edge8,Mode1 | 80.0 | 0.0+V | InnerGlass | Glass panel | Wire3 | 8.0 | 40.0+V
  expr: OverallWidth = .Width.Value
  expr: OverallHeight = .Height.Value
FEATURE [Part::Part2DObjectPython] Line1395  # Draft 2D object (typed FeaturePython)
  Area = 0
  ChamferSize = 0
  Closed = false
  End = (3400,3385,0)
  FilletRadius = 0
  Length = 800
  MakeFace = true
  Placement = pos=(2600,3385,0) rot=(0,0,1;0rad)
  Points = (2) [(0,0,0),(800,0,0)]
  Start = (2600,3385,0)
  Subdivisions = 0
FEATURE [Part::FeaturePython] Component131  label="Компонент"  # Arch/BIM 0 (typed FeaturePython)
  Base = -> Arc114
  HorizontalArea = 0
  IfcData = attributes={"GlobalId": {"name": "GlobalId", "type": "IfcGloballyUniqueId", "is_enum": false, "enum_values": []}, "Description": {"... (+538 chars omitted),+1 more (map truncated)
  IfcType = 0
  MoveBase = false
  MoveWithHost = false
  PerimeterLength = 0
  Placement = pos=(4710,3635,0) rot=(0,0,1;0rad)
  PredefinedType = 0
  VerticalArea = 0
FEATURE [Part::FeaturePython] Component132  label="Компонент001"  # Arch/BIM 0 (typed FeaturePython)
  Base = -> Line1394
  HorizontalArea = 0
  IfcData = attributes={"GlobalId": {"name": "GlobalId", "type": "IfcGloballyUniqueId", "is_enum": false, "enum_values": []}, "Description": {"... (+538 chars omitted),+1 more (map truncated)
  IfcType = 0
  MoveBase = false
  MoveWithHost = false
  PerimeterLength = 0
  Placement = pos=(4710,4435,0) rot=(0,0,1;0rad)
  PredefinedType = 0
  VerticalArea = 0
FEATURE [Part::FeaturePython] Component133  label="Компонент002"  # Arch/BIM 0 (typed FeaturePython)
  Base = -> Line1395
  HorizontalArea = 0
  IfcData = attributes={"GlobalId": {"name": "GlobalId", "type": "IfcGloballyUniqueId", "is_enum": false, "enum_values": []}, "Description": {"... (+538 chars omitted),+1 more (map truncated)
  IfcType = 0
  MoveBase = false
  MoveWithHost = false
  PerimeterLength = 0
  Placement = pos=(2600,3385,0) rot=(0,0,1;0rad)
  PredefinedType = 0
  VerticalArea = 0
FEATURE [Part::FeaturePython] Component134  label="Компонент003"  # Arch/BIM 0 (typed FeaturePython)
  Base = -> Arc115
  HorizontalArea = 0
  IfcData = attributes={"GlobalId": {"name": "GlobalId", "type": "IfcGloballyUniqueId", "is_enum": false, "enum_values": []}, "Description": {"... (+538 chars omitted),+1 more (map truncated)
  IfcType = 0
  MoveBase = false
  MoveWithHost = false
  PerimeterLength = 0
  Placement = pos=(3400,3385,0) rot=(0,0,1;0rad)
  PredefinedType = 0
  VerticalArea = 0
FEATURE [Part::FeaturePython] Component135  label="Компонент004"  # Arch/BIM 0 (typed FeaturePython)
  Base = -> Arc116
  HorizontalArea = 0
  IfcData = attributes={"GlobalId": {"name": "GlobalId", "type": "IfcGloballyUniqueId", "is_enum": false, "enum_values": []}, "Description": {"... (+538 chars omitted),+1 more (map truncated)
  IfcType = 0
  MoveBase = false
  MoveWithHost = false
  PerimeterLength = 0
  Placement = pos=(6660,2285,0) rot=(0,0,1;0rad)
  PredefinedType = 0
  VerticalArea = 0
FEATURE [Part::FeaturePython] Component136  label="Компонент005"  # Arch/BIM 0 (typed FeaturePython)
  Base = -> Line1396
  HorizontalArea = 0
  IfcData = attributes={"GlobalId": {"name": "GlobalId", "type": "IfcGloballyUniqueId", "is_enum": false, "enum_values": []}, "Description": {"... (+538 chars omitted),+1 more (map truncated)
  IfcType = 0
  MoveBase = false
  MoveWithHost = false
  PerimeterLength = 0
  Placement = pos=(6660,1485,0) rot=(0,0,1;0rad)
  PredefinedType = 0
  VerticalArea = 0
FEATURE [Part::FeaturePython] Component137  label="Компонент006"  # Arch/BIM 0 (typed FeaturePython)
  Base = -> Arc113
  HorizontalArea = 0
  IfcData = attributes={"GlobalId": {"name": "GlobalId", "type": "IfcGloballyUniqueId", "is_enum": false, "enum_values": []}, "Description": {"... (+538 chars omitted),+1 more (map truncated)
  IfcType = 0
  MoveBase = false
  MoveWithHost = false
  PerimeterLength = 0
  Placement = pos=(6660,3635,0) rot=(0,0,1;0rad)
  PredefinedType = 0
  VerticalArea = 0
FEATURE [Part::FeaturePython] Component138  label="Компонент007"  # Arch/BIM 0 (typed FeaturePython)
  Base = -> Line1400
  HorizontalArea = 0
  IfcData = attributes={"GlobalId": {"name": "GlobalId", "type": "IfcGloballyUniqueId", "is_enum": false, "enum_values": []}, "Description": {"... (+538 chars omitted),+1 more (map truncated)
  IfcType = 0
  MoveBase = false
  MoveWithHost = false
  PerimeterLength = 0
  Placement = pos=(6660,4580,0) rot=(0,0,1;0rad)
  PredefinedType = 0
  VerticalArea = 0
FEATURE [Part::FeaturePython] Component139  label="Компонент008"  # Arch/BIM 0 (typed FeaturePython)
  Base = -> Arc118
  HorizontalArea = 0
  IfcData = attributes={"GlobalId": {"name": "GlobalId", "type": "IfcGloballyUniqueId", "is_enum": false, "enum_values": []}, "Description": {"... (+538 chars omitted),+1 more (map truncated)
  IfcType = 0
  MoveBase = false
  MoveWithHost = false
  PerimeterLength = 0
  Placement = pos=(9550,820,0) rot=(0,0,1;0rad)
  PredefinedType = 0
  VerticalArea = 0
FEATURE [Part::FeaturePython] Component140  label="Компонент009"  # Arch/BIM 0 (typed FeaturePython)
  Base = -> Line1398
  HorizontalArea = 0
  IfcData = attributes={"GlobalId": {"name": "GlobalId", "type": "IfcGloballyUniqueId", "is_enum": false, "enum_values": []}, "Description": {"... (+538 chars omitted),+1 more (map truncated)
  IfcType = 0
  MoveBase = false
  MoveWithHost = false
  PerimeterLength = 0
  Placement = pos=(10350,820,0) rot=(0,0,1;0rad)
  PredefinedType = 0
  VerticalArea = 0
FEATURE [App::FeaturePython] Dimension079  # Draft dimension (typed FeaturePython)
  Diameter = false
  Dimline = (4500,1400,0)
  Direction = (0,0,0)
  Distance = 100
  End = (4100,2285,0)
  Normal = (0,0,1)
  Start = (4000,2285,0)
FEATURE [Part::FeaturePython] Component141  label="Компонент010"  # Arch/BIM 0 (typed FeaturePython)
  Base = -> Circle109
  HorizontalArea = 0
  IfcData = attributes={"GlobalId": {"name": "GlobalId", "type": "IfcGloballyUniqueId", "is_enum": false, "enum_values": []}, "Description": {"... (+538 chars omitted),+1 more (map truncated)
  IfcType = 0
  MoveBase = false
  MoveWithHost = false
  PerimeterLength = 0
  Placement = pos=(7390,4155,0) rot=(0,0,-1;1.5708rad)
  PredefinedType = 0
  VerticalArea = 0
FEATURE [Part::FeaturePython] Component142  label="Компонент011"  # Arch/BIM 0 (typed FeaturePython)
  Base = -> Line1409
  HorizontalArea = 0
  IfcData = attributes={"GlobalId": {"name": "GlobalId", "type": "IfcGloballyUniqueId", "is_enum": false, "enum_values": []}, "Description": {"... (+538 chars omitted),+1 more (map truncated)
  IfcType = 0
  MoveBase = false
  MoveWithHost = false
  PerimeterLength = 0
  Placement = pos=(7420,4155,0) rot=(0,0,-1;1.5708rad)
  PredefinedType = 0
  VerticalArea = 0
FEATURE [App::FeaturePython] Dimension080  # Draft dimension (typed FeaturePython)
  Diameter = false
  Dimline = (2030,8200,0)
  Direction = (0,0,0)
  Distance = 2590
  End = (2030,8015,0)
  Normal = (0,0,1)
  Start = (-560,8015,0)
FEATURE [App::FeaturePython] Dimension081  # Draft dimension (typed FeaturePython)
  Diameter = false
  Dimline = (3860,8200,0)
  Direction = (0,0,0)
  Distance = 1290
  End = (5150,8015,0)
  Normal = (0,0,1)
  Start = (3860,8015,0)
FEATURE [App::FeaturePython] Dimension082  # Draft dimension (typed FeaturePython)
  Diameter = false
  Dimline = (5150,8200,0)
  Direction = (0,0,0)
  Distance = 790
  End = (5940,8015,0)
  Normal = (0,0,1)
  Start = (5150,8015,0)
FEATURE [App::FeaturePython] Dimension083  # Draft dimension (typed FeaturePython)
  Diameter = false
  Dimline = (5940,8200,0)
  Direction = (0,0,0)
  Distance = 2720
  End = (8660,8015,0)
  Normal = (0,0,1)
  Start = (5940,8015,0)
FEATURE [App::FeaturePython] Dimension084  # Draft dimension (typed FeaturePython)
  Diameter = false
  Dimline = (8660,8200,0)
  Direction = (0,0,0)
  Distance = 1830
  End = (10490,8015,0)
  Normal = (0,0,1)
  Start = (8660,8015,0)
FEATURE [App::FeaturePython] Dimension085  # Draft dimension (typed FeaturePython)
  Diameter = false
  Dimline = (10490,8200,0)
  Direction = (0,0,0)
  Distance = 2590
  End = (13080,8015,0)
  Normal = (0,0,1)
  Start = (10490,8015,0)
FEATURE [App::FeaturePython] Dimension086  # Draft dimension (typed FeaturePython)
  Diameter = false
  Dimline = (5000,7200,0)
  Direction = (0,0,0)
  Distance = 1900
  End = (6830,7485,0)
  Normal = (0,0,1)
  Start = (4930,7485,0)
FEATURE [App::FeaturePython] Dimension087  # Draft dimension (typed FeaturePython)
  Diameter = false
  Dimline = (-800,3215,0)
  Direction = (0,0,0)
  Distance = 1310
  End = (-560,3215,0)
  Normal = (0,0,1)
  Start = (-560,1905,0)
FEATURE [App::FeaturePython] Dimension088  # Draft dimension (typed FeaturePython)
  Diameter = false
  Dimline = (-800,1905,0)
  Direction = (0,0,0)
  Distance = 2460
  End = (-560,1905,0)
  Normal = (0,0,1)
  Start = (-560,-555,0)
FEATURE [App::FeaturePython] Dimension089  # Draft dimension (typed FeaturePython)
  Diameter = false
  Dimline = (1700,-800,0)
  Direction = (0,0,0)
  Distance = 4800
  End = (4240,-555,0)
  Normal = (0,0,1)
  Start = (-560,-555,0)
FEATURE [App::FeaturePython] Dimension090  # Draft dimension (typed FeaturePython)
  Diameter = false
  Dimline = (4240,-800,0)
  Direction = (0,0,0)
  Distance = 530
  End = (4770,-555,0)
  Normal = (0,0,1)
  Start = (4240,-555,0)
FEATURE [App::FeaturePython] Dimension091  # Draft dimension (typed FeaturePython)
  Diameter = false
  Dimline = (4770,-800,0)
  Direction = (0,0,0)
  Distance = 900
  End = (5670,-555,0)
  Normal = (0,0,1)
  Start = (4770,-555,0)
FEATURE [App::FeaturePython] Dimension092  # Draft dimension (typed FeaturePython)
  Diameter = false
  Dimline = (7620,-800,0)
  Direction = (0,0,0)
  Distance = 530
  End = (8150,-555,0)
  Normal = (0,0,1)
  Start = (7620,-555,0)
FEATURE [App::FeaturePython] Dimension093  # Draft dimension (typed FeaturePython)
  Diameter = false
  Dimline = (6720,-800,0)
  Direction = (0,0,0)
  Distance = 900
  End = (7620,-555,0)
  Normal = (0,0,1)
  Start = (6720,-555,0)
FEATURE [App::FeaturePython] Dimension094  # Draft dimension (typed FeaturePython)
  Diameter = false
  Dimline = (8150,-800,0)
  Direction = (0,0,0)
  Distance = 4930
  End = (13080,-555,0)
  Normal = (0,0,1)
  Start = (8150,-555,0)
FEATURE [App::FeaturePython] Dimension095  # Draft dimension (typed FeaturePython)
  Diameter = false
  Dimline = (13600,1200,0)
  Direction = (0,0,0)
  Distance = 1940
  End = (13080,1385,0)
  Normal = (0,0,1)
  Start = (13080,-555,0)
FEATURE [App::FeaturePython] Dimension096  # Draft dimension (typed FeaturePython)
  Diameter = false
  Dimline = (13600,1385,0)
  Direction = (0,0,0)
  Distance = 1830
  End = (13080,3215,0)
  Normal = (0,0,1)
  Start = (13080,1385,0)
FEATURE [App::FeaturePython] Dimension097  # Draft dimension (typed FeaturePython)
  Diameter = false
  Dimline = (13600,3215,0)
  Direction = (0,0,0)
  Distance = 900
  End = (13080,4115,0)
  Normal = (0,0,1)
  Start = (13080,3215,0)
FEATURE [App::FeaturePython] Dimension098  # Draft dimension (typed FeaturePython)
  Diameter = false
  Dimline = (13600,4115,0)
  Direction = (0,0,0)
  Distance = 790
  End = (13080,4905,0)
  Normal = (0,0,1)
  Start = (13080,4115,0)
FEATURE [App::FeaturePython] Dimension099  # Draft dimension (typed FeaturePython)
  Diameter = false
  Dimline = (13600,4905,0)
  Direction = (0,0,0)
  Distance = 3110
  End = (13080,8015,0)
  Normal = (0,0,1)
  Start = (13080,4905,0)
FEATURE [App::FeaturePython] Dimension100  # Draft dimension (typed FeaturePython)
  Diameter = false
  Dimline = (-800,3215,0)
  Direction = (0,0,0)
  Distance = 4800
  End = (-560,8015,0)
  Normal = (0,0,1)
  Start = (-560,3215,0)
FEATURE [Part::Part2DObjectPython] Wire917  # Draft 2D object (typed FeaturePython)
  Area = 0
  ChamferSize = 0
  Closed = false
  End = (7860,6485,0)
  FilletRadius = 0
  Length = 2780
  MakeFace = false
  Placement = pos=(7960,3805,0) rot=(0,0,1;0rad)
  Points = (3) [(0,0,0),(0,2680,0),(-100,2680,0)]
  Start = (7960,3805,0)
  Subdivisions = 0
FEATURE [Part::Part2DObjectPython] Line1728  # Draft 2D object (typed FeaturePython)
  Area = 0
  ChamferSize = 0
  Closed = false
  End = (6940,3805,0)
  FilletRadius = 0
  Length = 3700
  MakeFace = false
  Placement = pos=(6940,7505,0) rot=(0,0,1;0rad)
  Points = (2) [(0,0,0),(0,-3700,0)]
  Start = (6940,7505,0)
  Subdivisions = 0
FEATURE [Part::FeaturePython] Wall348  label="Стена042"  # Arch/BIM 166 (typed FeaturePython)
  Align = 0
  Area = 1.036e+07
  Base = -> Line1728
  BlockHeight = 0
  BlockLength = 0
  CountBroken = 0
  CountEntire = 0
  Face = 0
  Height = 2800
  HorizontalArea = 37000
  IfcData = attributes={"GlobalId": {"name": "GlobalId", "type": "IfcGloballyUniqueId", "is_enum": false, "enum_values": []}, "Description": {"... (+533 chars omitted),+1 more (map truncated)
  IfcType = 166
  Joint = 0
  Length = 3700
  MakeBlocks = false
  MoveBase = false
  MoveWithHost = false
  Normal = (0,0,0)
  OffsetFirst = 0
  OffsetSecond = 0
  PerimeterLength = 7420
  PredefinedType = 0
  VerticalArea = 2.0776e+07
  Width = 10
FEATURE [Part::Part2DObjectPython] Wire918  # Draft 2D object (typed FeaturePython)
  Area = 0
  ChamferSize = 0
  Closed = true
  End = (7960,7600,48.08)
  FilletRadius = 0
  Length = 13696.2
  MakeFace = false
  Placement = pos=(7960,2995.41,3427.85) rot=(0.57735,0.57735,0.57735;2.0944rad)
  Points = (3) [(0,0,0),(4604.59,0,0),(4604.59,-3379.77,0)]
  Start = (7960,2995.41,3427.85)
  Subdivisions = 0
FEATURE [Part::FeaturePython] Structure337  label="Структура005"  # Arch/BIM 52 (typed FeaturePython)
  Base = -> Wire918
  FaceMaker = 0
  Height = 1030
  HorizontalArea = 4.74273e+06
  IfcData = attributes={"GlobalId": {"name": "GlobalId", "type": "IfcGloballyUniqueId", "is_enum": false, "enum_values": []}, "Description": {"... (+484 chars omitted),+1 more (map truncated)
  IfcType = 52
  Length = 0
  MoveBase = false
  MoveWithHost = false
  Nodes = (2) [(5266.67,6238.33,-4065),(5166.67,6238.33,-4065)]
  NodesOffset = 0
  Normal = (-1,0,0)
  PerimeterLength = 11269.2
  VerticalArea = 1.90436e+07
  Width = 100
FEATURE [Part::FeaturePython] Wall128  label="перегородка (сил.блок 500х250х80) 003"  # Arch/BIM 166 (typed FeaturePython)
  Align = 2
  Area = 7.476e+06
  Base = -> Line1200
  BlockHeight = 250
  BlockLength = 0
  CountBroken = 0
  CountEntire = 0
  Face = 0
  GlobalId = 239nej2f15XxZ4oxwr6VZE
  Height = 2800
  HorizontalArea = 213600
  IfcData = IfcUID=239nej2f15XxZ4oxwr6VZE; attributes={"GlobalId": {"value": "239nej2f15XxZ4oxwr6VZE"}}
  IfcType = 166
  Joint = 0
  Length = 2670
  MakeBlocks = false
  Material = -> Material009
  MoveBase = false
  MoveWithHost = false
  Normal = (0,0,0)
  OffsetFirst = 300
  OffsetSecond = 50
  PerimeterLength = 5720
  PredefinedType = 0
  Subtractions = -> [Structure337]
  VerticalArea = 1.01912e+07
  Width = 80
FEATURE [Part::FeaturePython] Structure460  label="Структура022"  # Arch/BIM 52 (typed FeaturePython)
  Base = -> Wire918
  FaceMaker = 0
  Height = 1030
  HorizontalArea = 4.74273e+06
  IfcData = attributes={"GlobalId": {"name": "GlobalId", "type": "IfcGloballyUniqueId", "is_enum": false, "enum_values": []}, "Description": {"... (+484 chars omitted),+1 more (map truncated)
  IfcType = 52
  Length = 0
  MoveBase = false
  MoveWithHost = false
  Nodes = (2) [(5266.67,6238.33,-4065),(5166.67,6238.33,-4065)]
  NodesOffset = 0
  Normal = (-1,0,0)
  PerimeterLength = 11269.2
  Placement = pos=(0,0,-30) rot=(0,0,1;0rad)
  VerticalArea = 1.90436e+07
  Width = 100
FEATURE [Part::FeaturePython] Wall231  label="перегородка (сил.блок 500х250х80) 005"  # Arch/BIM 166 (typed FeaturePython)
  Align = 2
  Area = 1.5604e+06
  Base = -> Line1391
  BlockHeight = 250
  BlockLength = 0
  CountBroken = 0
  CountEntire = 0
  Face = 0
  GlobalId = 2YMQSCXEvDBOywm4rK59sv
  Height = 1660
  HorizontalArea = 75200
  IfcData = IfcUID=2YMQSCXEvDBOywm4rK59sv; attributes={"GlobalId": {"value": "2YMQSCXEvDBOywm4rK59sv"}}
  IfcType = 166
  Joint = 0
  Length = 940
  MakeBlocks = false
  Material = -> Material009
  MoveBase = false
  MoveWithHost = false
  Normal = (0,0,0)
  OffsetFirst = 300
  OffsetSecond = 50
  PerimeterLength = 2000
  PredefinedType = 0
  Subtractions = -> [Structure460]
  VerticalArea = 3.34084e+06
  Width = 80
FEATURE [Part::FeaturePython] Wall346  label="Покрытие Душ плиткой 20мм"  # Arch/BIM 166 (typed FeaturePython)
  Align = 0
  Area = 1.344e+07
  Base = -> Rectangle3000
  BlockHeight = 0
  BlockLength = 0
  CountBroken = 0
  CountEntire = 0
  Face = 0
  Height = 2800
  HorizontalArea = 4623.16
  IfcData = attributes={"GlobalId": {"name": "GlobalId", "type": "IfcGloballyUniqueId", "is_enum": false, "enum_values": []}, "Description": {"... (+533 chars omitted),+1 more (map truncated)
  IfcType = 166
  Joint = 0
  Length = 4800
  MakeBlocks = false
  Material = -> Material005
  MoveBase = false
  MoveWithHost = false
  Normal = (0,0,0)
  OffsetFirst = 0
  OffsetSecond = 0
  PerimeterLength = 1889.84
  PredefinedType = 0
  Subtractions = -> [Structure333,Structure460]
  VerticalArea = 1.83237e+07
  Width = 20
FEATURE [Part::FeaturePython] Wall347  label="Штукатурка 10мм 006"  # Arch/BIM 166 (typed FeaturePython)
  Align = 1
  Area = 7.784e+06
  Base = -> Wire917
  BlockHeight = 0
  BlockLength = 0
  CountBroken = 0
  CountEntire = 0
  Face = 0
  Height = 2800
  HorizontalArea = 27700
  IfcData = attributes={"GlobalId": {"name": "GlobalId", "type": "IfcGloballyUniqueId", "is_enum": false, "enum_values": []}, "Description": {"... (+533 chars omitted),+1 more (map truncated)
  IfcType = 166
  Joint = 0
  Length = 2780
  MakeBlocks = false
  Material = -> Material008
  MoveBase = false
  MoveWithHost = false
  Normal = (0,0,0)
  OffsetFirst = 0
  OffsetSecond = 0
  PerimeterLength = 5560
  PredefinedType = 0
  Subtractions = -> [Structure337]
  VerticalArea = 1.0108e+07
  Width = 10
FEATURE [Part::MultiCommon] Common074  label="Штукатурка 10мм 005"
  Shapes = -> [Wall348,Structure460]
FEATURE [Part::FeaturePython] Component143  label="Компонент012"  # Arch/BIM 0 (typed FeaturePython)
  Base = -> Common074
  HorizontalArea = 0
  IfcData = attributes={"GlobalId": {"name": "GlobalId", "type": "IfcGloballyUniqueId", "is_enum": false, "enum_values": []}, "Description": {"... (+538 chars omitted),+1 more (map truncated)
  IfcType = 0
  Material = -> Material008
  MoveBase = false
  MoveWithHost = false
  PerimeterLength = 0
  PredefinedType = 0
  VerticalArea = 0
FEATURE [Part::Part2DObjectPython] Line1729  # Draft 2D object (typed FeaturePython)
  Area = 0
  ChamferSize = 0
  Closed = false
  End = (4820,3805,0)
  FilletRadius = 0
  Length = 3700
  MakeFace = false
  Placement = pos=(4820,7505,0) rot=(0,0,1;0rad)
  Points = (2) [(0,0,0),(-9.09495e-13,-3700,0)]
  Start = (4820,7505,0)
  Subdivisions = 0
FEATURE [Part::FeaturePython] Wall349  label="Штукатурка 10мм 007"  # Arch/BIM 166 (typed FeaturePython)
  Align = 1
  Area = 1.036e+07
  Base = -> Line1729
  BlockHeight = 0
  BlockLength = 0
  CountBroken = 0
  CountEntire = 0
  Face = 0
  Height = 2800
  HorizontalArea = 37000
  IfcData = attributes={"GlobalId": {"name": "GlobalId", "type": "IfcGloballyUniqueId", "is_enum": false, "enum_values": []}, "Description": {"... (+533 chars omitted),+1 more (map truncated)
  IfcType = 166
  Joint = 0
  Length = 3700
  MakeBlocks = false
  Material = -> Material008
  MoveBase = false
  MoveWithHost = false
  Normal = (0,0,0)
  OffsetFirst = 0
  OffsetSecond = 0
  PerimeterLength = 7420
  PredefinedType = 0
  Subtractions = -> [Structure141]
  VerticalArea = 16949000
  Width = 10
FEATURE [Part::FeaturePython] Component144  label="Компонент013"  # Arch/BIM 0 (typed FeaturePython)
  Base = -> Line1456
  HorizontalArea = 0
  IfcData = attributes={"GlobalId": {"name": "GlobalId", "type": "IfcGloballyUniqueId", "is_enum": false, "enum_values": []}, "Description": {"... (+538 chars omitted),+1 more (map truncated)
  IfcType = 0
  MoveBase = false
  MoveWithHost = false
  PerimeterLength = 0
  Placement = pos=(4020,7335,0) rot=(0,0,1;0rad)
  PredefinedType = 0
  VerticalArea = 0
FEATURE [Part::FeaturePython] Component145  label="Компонент014"  # Arch/BIM 0 (typed FeaturePython)
  Base = -> Arc125
  HorizontalArea = 0
  IfcData = attributes={"GlobalId": {"name": "GlobalId", "type": "IfcGloballyUniqueId", "is_enum": false, "enum_values": []}, "Description": {"... (+538 chars omitted),+1 more (map truncated)
  IfcType = 0
  MoveBase = false
  MoveWithHost = false
  PerimeterLength = 0
  Placement = pos=(4820,7335,0) rot=(0,0,1;0rad)
  PredefinedType = 0
  VerticalArea = 0
FEATURE [App::GeometryPython] BuildingPart107  label="Направление открывания дверей"  # Arch/BIM 172 (typed FeaturePython)
  Area = 0
  Group = -> [Component131,Component132,Component133,Component134,Component135,Component136,Component137,Component138,Component139,Component140,Component144,Component145]
  Height = 0
  HeightPropagate = true
  IfcData = attributes={"GlobalId": {"name": "GlobalId", "type": "IfcGloballyUniqueId", "is_enum": false, "enum_values": []}, "Description": {"... (+484 chars omitted),+1 more (map truncated)
  IfcType = 172
  LevelOffset = 0
  PredefinedType = 0
FEATURE [Part::FeaturePython] Component146  label="Компонент015"  # Arch/BIM 0 (typed FeaturePython)
  Base = -> Wire833
  HorizontalArea = 0
  IfcData = attributes={"GlobalId": {"name": "GlobalId", "type": "IfcGloballyUniqueId", "is_enum": false, "enum_values": []}, "Description": {"... (+538 chars omitted),+1 more (map truncated)
  IfcType = 0
  MoveBase = false
  MoveWithHost = false
  PerimeterLength = 0
  Placement = pos=(8310,7021.58,0) rot=(0,0,1;0rad)
  PredefinedType = 0
  VerticalArea = 0
FEATURE [Part::FeaturePython] Component147  label="Компонент016"  # Arch/BIM 0 (typed FeaturePython)
  Base = -> Wire835
  HorizontalArea = 0
  IfcData = attributes={"GlobalId": {"name": "GlobalId", "type": "IfcGloballyUniqueId", "is_enum": false, "enum_values": []}, "Description": {"... (+538 chars omitted),+1 more (map truncated)
  IfcType = 0
  MoveBase = false
  MoveWithHost = false
  PerimeterLength = 0
  Placement = pos=(7390,5600,0) rot=(0,0,1;0rad)
  PredefinedType = 0
  VerticalArea = 0
FEATURE [Part::FeaturePython] Component148  label="Оси003"  # Arch/BIM 0 (typed FeaturePython)
  Base = -> Compound
  HorizontalArea = 0
  IfcData = attributes={"GlobalId": {"name": "GlobalId", "type": "IfcGloballyUniqueId", "is_enum": false, "enum_values": []}, "Description": {"... (+538 chars omitted),+1 more (map truncated)
  IfcType = 0
  MoveBase = false
  MoveWithHost = false
  PerimeterLength = 0
  PredefinedType = 0
  VerticalArea = 0
FEATURE [Part::Part2DObjectPython] Line1730  # Draft 2D object (typed FeaturePython)
  Area = 0
  ChamferSize = 0
  Closed = false
  End = (9950,9900,0)
  FilletRadius = 0
  Length = 200
  MakeFace = true
  Placement = pos=(9950,10100,0) rot=(0,0,1;0rad)
  Points = (2) [(0,0,0),(0,-200,0)]
  Start = (9950,10100,0)
  Subdivisions = 0
FEATURE [Part::Part2DObjectPython] Line1731  # Draft 2D object (typed FeaturePython)
  Area = 0
  ChamferSize = 0
  Closed = false
  End = (7800,9900,0)
  FilletRadius = 0
  Length = 200
  MakeFace = true
  Placement = pos=(7800,10100,0) rot=(0,0,1;0rad)
  Points = (2) [(0,0,0),(0,-200,0)]
  Start = (7800,10100,0)
  Subdivisions = 0
FEATURE [Part::Part2DObjectPython] Line1732  # Draft 2D object (typed FeaturePython)
  Area = 0
  ChamferSize = 0
  Closed = false
  End = (7800,-2300,0)
  FilletRadius = 0
  Length = 200
  MakeFace = true
  Placement = pos=(7800,-2500,0) rot=(0,0,1;0rad)
  Points = (2) [(0,0,0),(0,200,0)]
  Start = (7800,-2500,0)
  Subdivisions = 0
FEATURE [Part::Part2DObjectPython] Line1733  # Draft 2D object (typed FeaturePython)
  Area = 0
  ChamferSize = 0
  Closed = false
  End = (9950,-2300,0)
  FilletRadius = 0
  Length = 200
  MakeFace = true
  Placement = pos=(9950,-2500,0) rot=(0,0,1;0rad)
  Points = (2) [(0,0,0),(0,200,0)]
  Start = (9950,-2500,0)
  Subdivisions = 0
FEATURE [Part::Part2DObjectPython] Line1734  # Draft 2D object (typed FeaturePython)
  Area = 0
  ChamferSize = 0
  Closed = false
  End = (9950,-2500,0)
  FilletRadius = 0
  Length = 250
  MakeFace = true
  Placement = pos=(10200,-2500,0) rot=(0,0,1;0rad)
  Points = (2) [(0,0,0),(-250,0,0)]
  Start = (10200,-2500,0)
  Subdivisions = 0
FEATURE [Part::Part2DObjectPython] ShapeString205  # Draft 2D object (typed FeaturePython)
  FontFile = <path>
  Placement = pos=(10259.2,-2466.26,0) rot=(0,0,1;0rad)
  Size = 150
  String = А
  Tracking = 0
FEATURE [Part::Part2DObjectPython] ShapeString206  # Draft 2D object (typed FeaturePython)
  FontFile = <path>
  Placement = pos=(10259.2,10133.7,0) rot=(0,0,1;0rad)
  Size = 150
  String = А
  Tracking = 0
FEATURE [Part::Part2DObjectPython] Line1735  # Draft 2D object (typed FeaturePython)
  Area = 0
  ChamferSize = 0
  Closed = false
  End = (9950,10100,0)
  FilletRadius = 0
  Length = 250
  MakeFace = true
  Placement = pos=(10200,10100,0) rot=(0,0,1;0rad)
  Points = (2) [(0,0,0),(-250,0,0)]
  Start = (10200,10100,0)
  Subdivisions = 0
FEATURE [Part::Part2DObjectPython] Line1736  # Draft 2D object (typed FeaturePython)
  Area = 0
  ChamferSize = 0
  Closed = false
  End = (7800,-2500,0)
  FilletRadius = 0
  Length = 250
  MakeFace = true
  Placement = pos=(8050,-2500,0) rot=(0,0,1;0rad)
  Points = (2) [(0,0,0),(-250,0,0)]
  Start = (8050,-2500,0)
  Subdivisions = 0
FEATURE [Part::Part2DObjectPython] ShapeString207  # Draft 2D object (typed FeaturePython)
  FontFile = <path>
  Placement = pos=(8109.21,-2466.26,0) rot=(0,0,1;0rad)
  Size = 150
  String = B
  Tracking = 0
FEATURE [Part::Part2DObjectPython] ShapeString208  # Draft 2D object (typed FeaturePython)
  FontFile = <path>
  Placement = pos=(8109.21,10133.7,0) rot=(0,0,1;0rad)
  Size = 150
  String = B
  Tracking = 0
FEATURE [Part::Part2DObjectPython] Line1737  # Draft 2D object (typed FeaturePython)
  Area = 0
  ChamferSize = 0
  Closed = false
  End = (7800,10100,0)
  FilletRadius = 0
  Length = 250
  MakeFace = true
  Placement = pos=(8050,10100,0) rot=(0,0,1;0rad)
  Points = (2) [(0,0,0),(-250,0,0)]
  Start = (8050,10100,0)
  Subdivisions = 0
FEATURE [App::GeometryPython] BuildingPart114  label="разрезы"  # Arch/BIM 172 (typed FeaturePython)
  Area = 0
  Group = -> [Line1730,Line1731,Line1732,Line1733,Line1734,ShapeString205,ShapeString206,Line1735,Line1736,ShapeString207,ShapeString208,Line1737]
  Height = 0
  HeightPropagate = true
  IfcData = attributes={"GlobalId": {"name": "GlobalId", "type": "IfcGloballyUniqueId", "is_enum": false, "enum_values": []}, "Description": {"... (+484 chars omitted),+1 more (map truncated)
  IfcType = 172
  LevelOffset = 0
  PredefinedType = 0
FEATURE [TechDraw::DrawSVGTemplate] Template004
  EditableTexts = Дата_разработки=16.11.21,Информация=эскизный проект,Лист=1,Листов=7,Название=Жилой дом,Номер=ИЖС-2021.0001,Организация2=г. Санкт-Петербург,+2 more (map truncated)
  Height = 297
  Orientation = 1
  Width = 420
FEATURE [TechDraw::DrawViewImage] Image001
  Height = 300
  ImageFile = <userpath>/Рабочий стол/sweet_home_3d-2.jpg
  LockPosition = true
  Rotation = 0
  Scale = 0.85
  ScaleType = 2
  Width = 300
  X = 305.698
  Y = 150.441
FEATURE [TechDraw::DrawViewImage] Image002
  Height = 300
  ImageFile = <userpath>/Рабочий стол/sweet_home_3d-1.jpg
  LockPosition = true
  Rotation = 0
  Scale = 1.15
  ScaleType = 2
  Width = 300
  X = 132.768
  Y = 149.376
FEATURE [TechDraw::DrawViewAnnotation] Annotation032
  Font = osifont
  LineSpace = 80
  LockPosition = true
  MaxWidth = -1
  Rotation = 0
  ScaleType = 0
  Text = \u0440\u0438\u0441. 1   \u0421\u0435\u0432\u0435\u0440\u043d\u044b\u0439 \u0444\u0430\u0441\u0430\u0434
  TextSize = 6
  TextStyle = 0
  X = 131.841
  Y = 97.1035
FEATURE [TechDraw::DrawViewAnnotation] Annotation033
  Font = osifont
  LineSpace = 80
  LockPosition = true
  MaxWidth = -1
  Rotation = 0
  ScaleType = 0
  Text = \u0440\u0438\u0441. 2  \u042e\u0436\u043d\u044b\u0439 \u0444\u0430\u0441\u0430\u0434
  TextSize = 6
  TextStyle = 0
  X = 305.465
  Y = 99.5459
FEATURE [TechDraw::DrawSVGTemplate] Template005
  EditableTexts = Лист=7; Номер=ИЖС-2021.0001
  Height = 297
  Orientation = 1
  Width = 420
FEATURE [Part::Part2DObjectPython] Wire920  # Draft 2D object (typed FeaturePython)
  Area = 0
  ChamferSize = 0
  Closed = false
  End = (7075,8615,3132.21)
  FilletRadius = 0
  Length = 22363
  MakeFace = false
  Placement = pos=(3198,-1155,3132.21) rot=(0,0,1;0rad)
  Points = (4) [(0,0,0),(-4358,4.54747e-13,-4.54747e-13),(-4358,9770,1.81899e-12),(3877,9770,4.54747e-13)]
  Start = (3198,-1155,3132.21)
  Subdivisions = 0
FEATURE [Part::Part2DObjectPython] Wire919  # Draft 2D object (typed FeaturePython)
  Area = 0
  ChamferSize = 0
  Closed = false
  End = (9198,-1155,3132.21)
  FilletRadius = 0
  Length = 15857
  MakeFace = false
  Placement = pos=(12075,8615,3132.21) rot=(0,0,1;0rad)
  Points = (4) [(0,0,0),(1605,0,-4.54747e-13),(1605,-9770,-4.54747e-13),(-2877,-9770,-4.54747e-13)]
  Start = (12075,8615,3132.21)
  Subdivisions = 0
FEATURE [Part::FeaturePython] Wall350  label="Стена043"  # Arch/BIM 166 (typed FeaturePython)
  Align = 0
  Area = 2616405
  Base = -> Wire919
  BlockHeight = 0
  BlockLength = 0
  CountBroken = 0
  CountEntire = 0
  Face = 0
  Height = 165
  HorizontalArea = 6022800
  IfcData = attributes={"GlobalId": {"name": "GlobalId", "type": "IfcGloballyUniqueId", "is_enum": false, "enum_values": []}, "Description": {"... (+533 chars omitted),+1 more (map truncated)
  IfcType = 166
  Joint = 0
  Length = 15857
  MakeBlocks = false
  MoveBase = false
  MoveWithHost = false
  Normal = (0,0,0)
  OffsetFirst = 0
  OffsetSecond = 0
  PerimeterLength = 30914
  PredefinedType = 0
  VerticalArea = 5100810
  Width = 400
FEATURE [Part::FeaturePython] Wall351  label="Стена044"  # Arch/BIM 166 (typed FeaturePython)
  Align = 0
  Area = 3689895
  Base = -> Wire920
  BlockHeight = 0
  BlockLength = 0
  CountBroken = 0
  CountEntire = 0
  Face = 0
  Height = 165
  HorizontalArea = 8625200
  IfcData = attributes={"GlobalId": {"name": "GlobalId", "type": "IfcGloballyUniqueId", "is_enum": false, "enum_values": []}, "Description": {"... (+533 chars omitted),+1 more (map truncated)
  IfcType = 166
  Joint = 0
  Length = 22363
  MakeBlocks = false
  MoveBase = false
  MoveWithHost = false
  Normal = (0,0,0)
  OffsetFirst = 0
  OffsetSecond = 0
  PerimeterLength = 43926
  PredefinedType = 0
  VerticalArea = 7.24779e+06
  Width = 400
FEATURE [Part::MultiFuse] Fusion071
  Shapes = -> [Wall350,Wall351]
FEATURE [Part::Cut] Cut070  label="Кровля габарит_002"
  Base = -> Cut052
  Tool = -> Fusion071
FEATURE [Part::FeaturePython] Component149  label="Кровля габарит"  # Arch/BIM 0 (typed FeaturePython)
  Base = -> Cut070
  HorizontalArea = 0
  IfcData = attributes={"GlobalId": {"name": "GlobalId", "type": "IfcGloballyUniqueId", "is_enum": false, "enum_values": []}, "Description": {"... (+538 chars omitted),+1 more (map truncated)
  IfcType = 0
  Material = -> Material007
  MoveBase = false
  MoveWithHost = false
  PerimeterLength = 0
  PredefinedType = 0
  VerticalArea = 0
FEATURE [App::GeometryPython] BuildingPart106  label="Кровля"  # Arch/BIM 52 (typed FeaturePython)
  Area = 0
  GlobalId = 3O6XTUJY1FTBF6rjo3DaEi
  Group = -> [BuildingPart084,Component149]
  Height = 0
  HeightPropagate = true
  IfcData = IfcUID=3O6XTUJY1FTBF6rjo3DaEi,+2 more (map truncated)
  IfcType = 52
  LevelOffset = 0
FEATURE [TechDraw::DrawViewAnnotation] Annotation034
  Font = osifont
  LineSpace = 80
  LockPosition = true
  MaxWidth = -1
  Rotation = 0
  ScaleType = 0
  Text = \u0416\u0438\u043b\u043e\u0439 \u0434\u043e\u043c \u0441 \u043c\u0430\u043d\u0441\u0430\u0440\u0434\u043e\u0439
  TextSize = 10
  TextStyle = 0
  X = 209.673
  Y = 248.467
FEATURE [TechDraw::DrawViewAnnotation] Annotation035
  Font = osifont
  LineSpace = 80
  LockPosition = true
  MaxWidth = -1
  Rotation = 0
  ScaleType = 0
  Text = \u044d\u0441\u043a\u0438\u0437\u043d\u044b\u0439 \u043f\u0440\u043e\u0435\u043a\u0442
  TextSize = 6
  TextStyle = 0
  X = 210.327
  Y = 238.34
FEATURE [TechDraw::DrawPage] Page004  label="Титульный лист"
  KeepUpdated = false
  NextBalloonIndex = 1
  ProjectionType = 0
  Template = -> Template004
  Views = -> [Image001,Image002,Annotation032,Annotation033,Annotation034,Annotation035]
FEATURE [TechDraw::DrawSVGTemplate] Template006
  EditableTexts = Лист=2; Номер=ИЖС-2021.0001
  Height = 297
  Orientation = 1
  Width = 420
FEATURE [TechDraw::DrawViewImage] Image
  Caption = фасад "Север"
  Height = 100
  ImageFile = <userpath>/Рабочий стол/ф1.png
  LockPosition = true
  Rotation = 0
  Scale = 0.9
  ScaleType = 2
  Width = 100
  X = 145.786
  Y = 207.21
FEATURE [TechDraw::DrawViewImage] Image003
  Caption = фасад "Юг"
  Height = 100
  ImageFile = <userpath>/Рабочий стол/ф2.png
  LockPosition = true
  Rotation = 0
  Scale = 0.9
  ScaleType = 2
  Width = 100
  X = 145.494
  Y = 89.2006
FEATURE [TechDraw::DrawViewImage] Image004
  Caption = фасад "Запад"
  Height = 100
  ImageFile = <userpath>/Рабочий стол/ф3.png
  LockPosition = true
  Rotation = 0
  ScaleType = 2
  Width = 100
  X = 317.811
  Y = 207.25
FEATURE [TechDraw::DrawViewImage] Image005
  Caption = фасад "Восток"
  Height = 100
  ImageFile = <userpath>/Рабочий стол/ф4.png
  LockPosition = true
  Rotation = 0
  ScaleType = 2
  Width = 100
  X = 318.063
  Y = 89.4698
FEATURE [TechDraw::DrawViewAnnotation] Annotation036
  Font = osifont
  LineSpace = 80
  LockPosition = true
  MaxWidth = -1
  Rotation = 0
  ScaleType = 0
  Text = \u0424\u0430\u0441\u0430\u0434\u044b
  TextSize = 8
  TextStyle = 0
  X = 222.059
  Y = 271.5
FEATURE [TechDraw::DrawPage] Page006  label="Фасады"
  KeepUpdated = false
  NextBalloonIndex = 1
  ProjectionType = 0
  Template = -> Template006
  Views = -> [Image,Image003,Image004,Image005,Annotation036]
FEATURE [TechDraw::DrawViewAnnotation] Annotation037
  Font = Ubuntu Light
  LineSpace = 80
  LockPosition = false
  MaxWidth = -1
  Rotation = 0
  ScaleType = 0
  Text = \u0420\u0430\u0437\u0440\u0435\u0437 \u043f\u043e \u0412-\u0412
  TextSize = 6
  TextStyle = 0
  X = 223.092
  Y = 272.533
FEATURE [Part::FeaturePython] Component151  label="ряд 003"  # Arch/BIM 0 (typed FeaturePython)
  CloneOf = -> BuildingPart077
  HorizontalArea = 0
  IfcData = attributes={"GlobalId": {"name": "GlobalId", "type": "IfcGloballyUniqueId", "is_enum": false, "enum_values": []}, "Description": {"... (+532 chars omitted),+1 more (map truncated)
  IfcType = 0
  Material = -> Material004
  MoveBase = false
  MoveWithHost = false
  PerimeterLength = 0
  Placement = pos=(0,0,462) rot=(0,0,1;0rad)
  PredefinedType = 6
  VerticalArea = 0
FEATURE [Part::FeaturePython] Component152  label="ряд 004"  # Arch/BIM 0 (typed FeaturePython)
  CloneOf = -> BuildingPart072
  HorizontalArea = 0
  IfcData = attributes={"GlobalId": {"name": "GlobalId", "type": "IfcGloballyUniqueId", "is_enum": false, "enum_values": []}, "Description": {"... (+532 chars omitted),+1 more (map truncated)
  IfcType = 0
  Material = -> Material004
  MoveBase = false
  MoveWithHost = false
  PerimeterLength = 0
  Placement = pos=(0,0,462) rot=(0,0,1;0rad)
  PredefinedType = 6
  VerticalArea = 0
FEATURE [Part::FeaturePython] Component153  label="ряд 005"  # Arch/BIM 0 (typed FeaturePython)
  CloneOf = -> BuildingPart077
  HorizontalArea = 0
  IfcData = attributes={"GlobalId": {"name": "GlobalId", "type": "IfcGloballyUniqueId", "is_enum": false, "enum_values": []}, "Description": {"... (+532 chars omitted),+1 more (map truncated)
  IfcType = 0
  Material = -> Material004
  MoveBase = false
  MoveWithHost = false
  PerimeterLength = 0
  Placement = pos=(0,0,924) rot=(0,0,1;0rad)
  PredefinedType = 6
  VerticalArea = 0
FEATURE [Part::FeaturePython] Wall352  label="Стена045"  # Arch/BIM 166 (typed FeaturePython)
  Align = 0
  Area = 1831830
  Base = -> Line1343
  BlockHeight = 231
  BlockLength = 256
  CountBroken = 1
  CountEntire = 30
  Face = 0
  Height = 231
  HorizontalArea = 0
  IfcData = attributes={"GlobalId": {"name": "GlobalId", "type": "IfcGloballyUniqueId", "is_enum": false, "enum_values": []}, "Description": {"... (+533 chars omitted),+1 more (map truncated)
  IfcType = 166
  Joint = 0
  Length = 7930
  MakeBlocks = true
  Material = -> Material004
  MoveBase = false
  MoveWithHost = false
  Normal = (0,0,0)
  OffsetFirst = 0
  OffsetSecond = 0
  PerimeterLength = 0
  Placement = pos=(0,0,955) rot=(0,0,1;0rad)
  PredefinedType = 0
  VerticalArea = 0
  Width = 380
FEATURE [Part::FeaturePython] Wall353  label="Стена046"  # Arch/BIM 166 (typed FeaturePython)
  Align = 0
  Area = 3003000
  Base = -> Line1350
  BlockHeight = 231
  BlockLength = 255
  CountBroken = 7
  CountEntire = 27
  Face = 0
  Height = 231
  HorizontalArea = 0
  IfcData = attributes={"GlobalId": {"name": "GlobalId", "type": "IfcGloballyUniqueId", "is_enum": false, "enum_values": []}, "Description": {"... (+533 chars omitted),+1 more (map truncated)
  IfcType = 166
  Joint = 0
  Length = 13000
  MakeBlocks = true
  Material = -> Material004
  MoveBase = false
  MoveWithHost = false
  Normal = (0,0,0)
  OffsetFirst = 0
  OffsetSecond = 0
  PerimeterLength = 0
  Placement = pos=(0,0,955) rot=(0,0,1;0rad)
  PredefinedType = 0
  Subtractions = -> [Structure308,Structure315,Structure313]
  VerticalArea = 0
  Width = 380
FEATURE [Part::FeaturePython] Wall354  label="Стена047"  # Arch/BIM 166 (typed FeaturePython)
  Align = 0
  Area = 1.83183e+06
  Base = -> Line1347
  BlockHeight = 231
  BlockLength = 256
  CountBroken = 3
  CountEntire = 23
  Face = 0
  Height = 231
  HorizontalArea = 0
  IfcData = attributes={"GlobalId": {"name": "GlobalId", "type": "IfcGloballyUniqueId", "is_enum": false, "enum_values": []}, "Description": {"... (+533 chars omitted),+1 more (map truncated)
  IfcType = 166
  Joint = 0
  Length = 7930
  MakeBlocks = true
  Material = -> Material004
  MoveBase = false
  MoveWithHost = false
  Normal = (0,0,0)
  OffsetFirst = 0
  OffsetSecond = 0
  PerimeterLength = 0
  Placement = pos=(0,0,955) rot=(0,0,1;0rad)
  PredefinedType = 0
  Subtractions = -> [Structure285]
  VerticalArea = 0
  Width = 380
FEATURE [Part::FeaturePython] Wall355  label="Стена048"  # Arch/BIM 166 (typed FeaturePython)
  Align = 0
  Area = 3003000
  Base = -> Line1351
  BlockHeight = 231
  BlockLength = 255
  CountBroken = 7
  CountEntire = 37
  Face = 0
  Height = 231
  HorizontalArea = 0
  IfcData = attributes={"GlobalId": {"name": "GlobalId", "type": "IfcGloballyUniqueId", "is_enum": false, "enum_values": []}, "Description": {"... (+533 chars omitted),+1 more (map truncated)
  IfcType = 166
  Joint = 0
  Length = 13000
  MakeBlocks = true
  Material = -> Material004
  MoveBase = false
  MoveWithHost = false
  Normal = (0,0,0)
  OffsetFirst = 0
  OffsetSecond = 0
  PerimeterLength = 0
  Placement = pos=(0,0,955) rot=(0,0,1;0rad)
  PredefinedType = 0
  Subtractions = -> [Structure019,Structure016,Structure017]
  VerticalArea = 0
  Width = 380
FEATURE [App::GeometryPython] BuildingPart115  label="ряд 006"  # Arch/BIM 52 (typed FeaturePython)
  Area = 9669660
  Group = -> [Wall355,Wall353,Wall354,Wall352]
  Height = 0
  HeightPropagate = true
  IfcData = attributes={"GlobalId": {"name": "GlobalId", "type": "IfcGloballyUniqueId", "is_enum": false, "enum_values": []}, "Description": {"... (+484 chars omitted),+1 more (map truncated)
  IfcType = 52
  LevelOffset = 0
FEATURE [Part::FeaturePython] Wall356  label="Стена049"  # Arch/BIM 166 (typed FeaturePython)
  Align = 1
  Area = 1831830
  Base = -> Line1342
  BlockHeight = 231
  BlockLength = 256
  CountBroken = 5
  CountEntire = 16
  Face = 0
  Height = 231
  HorizontalArea = 0
  IfcData = attributes={"GlobalId": {"name": "GlobalId", "type": "IfcGloballyUniqueId", "is_enum": false, "enum_values": []}, "Description": {"... (+533 chars omitted),+1 more (map truncated)
  IfcType = 166
  Joint = 0
  Length = 7930
  MakeBlocks = true
  Material = -> Material004
  MoveBase = false
  MoveWithHost = false
  Normal = (0,0,0)
  OffsetFirst = 0
  OffsetSecond = 0
  PerimeterLength = 0
  Placement = pos=(0,0,1186) rot=(0,0,1;0rad)
  PredefinedType = 0
  Subtractions = -> [Structure306,Structure304]
  VerticalArea = 0
  Width = 380
FEATURE [Part::FeaturePython] Wall357  label="Стена050"  # Arch/BIM 166 (typed FeaturePython)
  Align = 1
  Area = 3003000
  Base = -> Line1349
  BlockHeight = 231
  BlockLength = 255
  CountBroken = 7
  CountEntire = 28
  Face = 0
  Height = 231
  HorizontalArea = 0
  IfcData = attributes={"GlobalId": {"name": "GlobalId", "type": "IfcGloballyUniqueId", "is_enum": false, "enum_values": []}, "Description": {"... (+533 chars omitted),+1 more (map truncated)
  IfcType = 166
  Joint = 0
  Length = 13000
  MakeBlocks = true
  Material = -> Material004
  MoveBase = false
  MoveWithHost = false
  Normal = (0,0,0)
  OffsetFirst = 0
  OffsetSecond = 0
  PerimeterLength = 0
  Placement = pos=(0,0,1186) rot=(0,0,1;0rad)
  PredefinedType = 0
  Subtractions = -> [Structure308,Structure315,Structure313]
  VerticalArea = 0
  Width = 380
FEATURE [Part::FeaturePython] Wall358  label="Стена051"  # Arch/BIM 166 (typed FeaturePython)
  Align = 1
  Area = 3003000
  Base = -> Line1340
  BlockHeight = 231
  BlockLength = 255
  CountBroken = 7
  CountEntire = 38
  Face = 0
  Height = 231
  HorizontalArea = 0
  IfcData = attributes={"GlobalId": {"name": "GlobalId", "type": "IfcGloballyUniqueId", "is_enum": false, "enum_values": []}, "Description": {"... (+533 chars omitted),+1 more (map truncated)
  IfcType = 166
  Joint = 0
  Length = 13000
  MakeBlocks = true
  Material = -> Material004
  MoveBase = false
  MoveWithHost = false
  Normal = (0,0,0)
  OffsetFirst = 0
  OffsetSecond = 0
  PerimeterLength = 0
  Placement = pos=(0,0,1186) rot=(0,0,1;0rad)
  PredefinedType = 0
  Subtractions = -> [Structure019,Structure016,Structure017]
  VerticalArea = 0
  Width = 380
FEATURE [Part::FeaturePython] Wall359  label="Стена052"  # Arch/BIM 166 (typed FeaturePython)
  Align = 1
  Area = 1831830
  Base = -> Line1341
  BlockHeight = 231
  BlockLength = 256
  CountBroken = 3
  CountEntire = 23
  Face = 0
  Height = 231
  HorizontalArea = 0
  IfcData = attributes={"GlobalId": {"name": "GlobalId", "type": "IfcGloballyUniqueId", "is_enum": false, "enum_values": []}, "Description": {"... (+533 chars omitted),+1 more (map truncated)
  IfcType = 166
  Joint = 0
  Length = 7930
  MakeBlocks = true
  Material = -> Material004
  MoveBase = false
  MoveWithHost = false
  Normal = (0,0,0)
  OffsetFirst = 0
  OffsetSecond = 0
  PerimeterLength = 0
  Placement = pos=(0,0,1186) rot=(0,0,1;0rad)
  PredefinedType = 0
  Subtractions = -> [Structure285]
  VerticalArea = 0
  Width = 380
FEATURE [App::GeometryPython] BuildingPart116  label="ряд 007"  # Arch/BIM 52 (typed FeaturePython)
  Area = 9669660
  Group = -> [Wall358,Wall357,Wall359,Wall356]
  Height = 0
  HeightPropagate = true
  IfcData = attributes={"GlobalId": {"name": "GlobalId", "type": "IfcGloballyUniqueId", "is_enum": false, "enum_values": []}, "Description": {"... (+484 chars omitted),+1 more (map truncated)
  IfcType = 52
  LevelOffset = 0
FEATURE [Part::FeaturePython] Wall360  label="Стена053"  # Arch/BIM 166 (typed FeaturePython)
  Align = 0
  Area = 3003000
  Base = -> Line1351
  BlockHeight = 231
  BlockLength = 255
  CountBroken = 7
  CountEntire = 37
  Face = 0
  Height = 231
  HorizontalArea = 0
  IfcData = attributes={"GlobalId": {"name": "GlobalId", "type": "IfcGloballyUniqueId", "is_enum": false, "enum_values": []}, "Description": {"... (+533 chars omitted),+1 more (map truncated)
  IfcType = 166
  Joint = 0
  Length = 13000
  MakeBlocks = true
  Material = -> Material004
  MoveBase = false
  MoveWithHost = false
  Normal = (0,0,0)
  OffsetFirst = 0
  OffsetSecond = 0
  PerimeterLength = 0
  Placement = pos=(0,0,1417) rot=(0,0,1;0rad)
  PredefinedType = 0
  Subtractions = -> [Structure019,Structure016,Structure017]
  VerticalArea = 0
  Width = 380
FEATURE [Part::FeaturePython] Wall361  label="Стена054"  # Arch/BIM 166 (typed FeaturePython)
  Align = 0
  Area = 3003000
  Base = -> Line1350
  BlockHeight = 231
  BlockLength = 255
  CountBroken = 7
  CountEntire = 27
  Face = 0
  Height = 231
  HorizontalArea = 0
  IfcData = attributes={"GlobalId": {"name": "GlobalId", "type": "IfcGloballyUniqueId", "is_enum": false, "enum_values": []}, "Description": {"... (+533 chars omitted),+1 more (map truncated)
  IfcType = 166
  Joint = 0
  Length = 13000
  MakeBlocks = true
  Material = -> Material004
  MoveBase = false
  MoveWithHost = false
  Normal = (0,0,0)
  OffsetFirst = 0
  OffsetSecond = 0
  PerimeterLength = 0
  Placement = pos=(0,0,1417) rot=(0,0,1;0rad)
  PredefinedType = 0
  Subtractions = -> [Structure308,Structure315,Structure313]
  VerticalArea = 0
  Width = 380
FEATURE [Part::FeaturePython] Wall362  label="Стена055"  # Arch/BIM 166 (typed FeaturePython)
  Align = 0
  Area = 1831830
  Base = -> Line1343
  BlockHeight = 231
  BlockLength = 256
  CountBroken = 5
  CountEntire = 17
  Face = 0
  Height = 231
  HorizontalArea = 0
  IfcData = attributes={"GlobalId": {"name": "GlobalId", "type": "IfcGloballyUniqueId", "is_enum": false, "enum_values": []}, "Description": {"... (+533 chars omitted),+1 more (map truncated)
  IfcType = 166
  Joint = 0
  Length = 7930
  MakeBlocks = true
  Material = -> Material004
  MoveBase = false
  MoveWithHost = false
  Normal = (0,0,0)
  OffsetFirst = 0
  OffsetSecond = 0
  PerimeterLength = 0
  Placement = pos=(0,0,1417) rot=(0,0,1;0rad)
  PredefinedType = 0
  Subtractions = -> [Structure304,Structure306]
  VerticalArea = 0
  Width = 380
FEATURE [Part::FeaturePython] Wall363  label="Стена056"  # Arch/BIM 166 (typed FeaturePython)
  Align = 0
  Area = 1.83183e+06
  Base = -> Line1347
  BlockHeight = 231
  BlockLength = 256
  CountBroken = 3
  CountEntire = 23
  Face = 0
  Height = 231
  HorizontalArea = 0
  IfcData = attributes={"GlobalId": {"name": "GlobalId", "type": "IfcGloballyUniqueId", "is_enum": false, "enum_values": []}, "Description": {"... (+533 chars omitted),+1 more (map truncated)
  IfcType = 166
  Joint = 0
  Length = 7930
  MakeBlocks = true
  Material = -> Material004
  MoveBase = false
  MoveWithHost = false
  Normal = (0,0,0)
  OffsetFirst = 0
  OffsetSecond = 0
  PerimeterLength = 0
  Placement = pos=(0,0,1417) rot=(0,0,1;0rad)
  PredefinedType = 0
  Subtractions = -> [Structure285]
  VerticalArea = 0
  Width = 380
FEATURE [App::GeometryPython] BuildingPart117  label="ряд 008"  # Arch/BIM 52 (typed FeaturePython)
  Area = 9669660
  Group = -> [Wall360,Wall361,Wall363,Wall362]
  Height = 0
  HeightPropagate = true
  IfcData = attributes={"GlobalId": {"name": "GlobalId", "type": "IfcGloballyUniqueId", "is_enum": false, "enum_values": []}, "Description": {"... (+484 chars omitted),+1 more (map truncated)
  IfcType = 52
  LevelOffset = 0
FEATURE [Part::FeaturePython] Component154  label="ряд 009"  # Arch/BIM 0 (typed FeaturePython)
  CloneOf = -> BuildingPart116
  HorizontalArea = 0
  IfcData = attributes={"GlobalId": {"name": "GlobalId", "type": "IfcGloballyUniqueId", "is_enum": false, "enum_values": []}, "Description": {"... (+538 chars omitted),+1 more (map truncated)
  IfcType = 0
  Material = -> Material004
  MoveBase = false
  MoveWithHost = false
  PerimeterLength = 0
  Placement = pos=(0,0,462) rot=(0,0,1;0rad)
  PredefinedType = 0
  VerticalArea = 0
FEATURE [Part::FeaturePython] Component155  label="ряд 010"  # Arch/BIM 0 (typed FeaturePython)
  CloneOf = -> BuildingPart117
  HorizontalArea = 0
  IfcData = attributes={"GlobalId": {"name": "GlobalId", "type": "IfcGloballyUniqueId", "is_enum": false, "enum_values": []}, "Description": {"... (+538 chars omitted),+1 more (map truncated)
  IfcType = 0
  Material = -> Material004
  MoveBase = false
  MoveWithHost = false
  PerimeterLength = 0
  Placement = pos=(0,0,462) rot=(0,0,1;0rad)
  PredefinedType = 0
  VerticalArea = 0
FEATURE [Part::FeaturePython] Component156  label="ряд 011"  # Arch/BIM 0 (typed FeaturePython)
  CloneOf = -> BuildingPart116
  HorizontalArea = 0
  IfcData = attributes={"GlobalId": {"name": "GlobalId", "type": "IfcGloballyUniqueId", "is_enum": false, "enum_values": []}, "Description": {"... (+538 chars omitted),+1 more (map truncated)
  IfcType = 0
  Material = -> Material004
  MoveBase = false
  MoveWithHost = false
  PerimeterLength = 0
  Placement = pos=(0,0,924) rot=(0,0,1;0rad)
  PredefinedType = 0
  VerticalArea = 0
FEATURE [Part::FeaturePython] Wall364  label="Стена057"  # Arch/BIM 166 (typed FeaturePython)
  Align = 0
  Area = 1.83183e+06
  Base = -> Line1347
  BlockHeight = 231
  BlockLength = 256
  CountBroken = 3
  CountEntire = 23
  Face = 0
  Height = 231
  HorizontalArea = 0
  IfcData = attributes={"GlobalId": {"name": "GlobalId", "type": "IfcGloballyUniqueId", "is_enum": false, "enum_values": []}, "Description": {"... (+533 chars omitted),+1 more (map truncated)
  IfcType = 166
  Joint = 0
  Length = 7930
  MakeBlocks = true
  Material = -> Material004
  MoveBase = false
  MoveWithHost = false
  Normal = (0,0,0)
  OffsetFirst = 0
  OffsetSecond = 0
  PerimeterLength = 0
  Placement = pos=(0,0,2341) rot=(0,0,1;0rad)
  PredefinedType = 0
  Subtractions = -> [Structure285]
  VerticalArea = 0
  Width = 380
FEATURE [Part::FeaturePython] Wall365  label="Стена058"  # Arch/BIM 166 (typed FeaturePython)
  Align = 0
  Area = 1831830
  Base = -> Line1343
  BlockHeight = 231
  BlockLength = 256
  CountBroken = 5
  CountEntire = 17
  Face = 0
  Height = 231
  HorizontalArea = 0
  IfcData = attributes={"GlobalId": {"name": "GlobalId", "type": "IfcGloballyUniqueId", "is_enum": false, "enum_values": []}, "Description": {"... (+533 chars omitted),+1 more (map truncated)
  IfcType = 166
  Joint = 0
  Length = 7930
  MakeBlocks = true
  Material = -> Material004
  MoveBase = false
  MoveWithHost = false
  Normal = (0,0,0)
  OffsetFirst = 0
  OffsetSecond = 0
  PerimeterLength = 0
  Placement = pos=(0,0,2341) rot=(0,0,1;0rad)
  PredefinedType = 0
  Subtractions = -> [Structure304,Structure306]
  VerticalArea = 0
  Width = 380
FEATURE [Part::FeaturePython] Wall366  label="Стена059"  # Arch/BIM 166 (typed FeaturePython)
  Align = 0
  Area = 3003000
  Base = -> Line1350
  BlockHeight = 231
  BlockLength = 255
  CountBroken = 7
  CountEntire = 27
  Face = 0
  Height = 231
  HorizontalArea = 0
  IfcData = attributes={"GlobalId": {"name": "GlobalId", "type": "IfcGloballyUniqueId", "is_enum": false, "enum_values": []}, "Description": {"... (+533 chars omitted),+1 more (map truncated)
  IfcType = 166
  Joint = 0
  Length = 13000
  MakeBlocks = true
  Material = -> Material004
  MoveBase = false
  MoveWithHost = false
  Normal = (0,0,0)
  OffsetFirst = 0
  OffsetSecond = 0
  PerimeterLength = 0
  Placement = pos=(0,0,2341) rot=(0,0,1;0rad)
  PredefinedType = 0
  Subtractions = -> [Structure308,Structure315,Structure313]
  VerticalArea = 0
  Width = 380
FEATURE [Part::FeaturePython] Wall370  label="Стена063"  # Arch/BIM 166 (typed FeaturePython)
  Align = 1
  Area = 3003000
  Base = -> Line1340
  BlockHeight = 231
  BlockLength = 255
  CountBroken = 1
  CountEntire = 50
  Face = 0
  Height = 231
  HorizontalArea = 0
  IfcData = attributes={"GlobalId": {"name": "GlobalId", "type": "IfcGloballyUniqueId", "is_enum": false, "enum_values": []}, "Description": {"... (+533 chars omitted),+1 more (map truncated)
  IfcType = 166
  Joint = 0
  Length = 13000
  MakeBlocks = true
  Material = -> Material004
  MoveBase = false
  MoveWithHost = false
  Normal = (0,0,0)
  OffsetFirst = 0
  OffsetSecond = 0
  PerimeterLength = 0
  Placement = pos=(0,0,2572) rot=(0,0,1;0rad)
  PredefinedType = 0
  Subtractions = -> [Structure019]
  VerticalArea = 0
  Width = 380
FEATURE [Part::FeaturePython] Wall372  label="Перемычка монолитн. 013"  # Arch/BIM 166 (typed FeaturePython)
  Align = 1
  Area = 572880
  Base = -> Line1523
  BlockHeight = 0
  BlockLength = 0
  CountBroken = 0
  CountEntire = 0
  Face = 0
  GlobalId = 2_OOPfC1L9nOo2BwNBJ59E
  Height = 231
  HorizontalArea = 942400
  IfcData = IfcUID=2_OOPfC1L9nOo2BwNBJ59E,+2 more (map truncated)
  IfcType = 166
  Joint = 0
  Length = 2480
  MakeBlocks = false
  Material = -> Material001
  MoveBase = false
  MoveWithHost = false
  Normal = (0,0,0)
  OffsetFirst = 0
  OffsetSecond = 0
  PerimeterLength = 5720
  Placement = pos=(0,0,2572) rot=(0,0,1;0rad)
  PredefinedType = 0
  VerticalArea = 1.32132e+06
  Width = 380
FEATURE [Part::FeaturePython] Wall373  label="Перемычка монолитн. 014"  # Arch/BIM 166 (typed FeaturePython)
  Align = 1
  Area = 332640
  Base = -> Line1524
  BlockHeight = 0
  BlockLength = 0
  CountBroken = 0
  CountEntire = 0
  Face = 0
  GlobalId = 02zZ5o_1DBJf0p5Hr4GWva
  Height = 231
  HorizontalArea = 547200
  IfcData = IfcUID=02zZ5o_1DBJf0p5Hr4GWva,+2 more (map truncated)
  IfcType = 166
  Joint = 0
  Length = 1440
  MakeBlocks = false
  Material = -> Material001
  MoveBase = false
  MoveWithHost = false
  Normal = (0,0,0)
  OffsetFirst = 0
  OffsetSecond = 0
  PerimeterLength = 3640
  Placement = pos=(0,0,2572) rot=(0,0,1;0rad)
  PredefinedType = 0
  VerticalArea = 840840
  Width = 380
FEATURE [Part::FeaturePython] Wall374  label="Перемычка монолитн. 015"  # Arch/BIM 166 (typed FeaturePython)
  Align = 0
  Area = 362670
  Base = -> Line1526
  BlockHeight = 0
  BlockLength = 0
  CountBroken = 0
  CountEntire = 0
  Face = 0
  GlobalId = 2Km2nGMYj6_hkYj1EJr8Pd
  Height = 231
  HorizontalArea = 596600
  IfcData = IfcUID=2Km2nGMYj6_hkYj1EJr8Pd,+2 more (map truncated)
  IfcType = 166
  Joint = 0
  Length = 1570
  MakeBlocks = false
  Material = -> Material001
  MoveBase = false
  MoveWithHost = false
  Normal = (0,0,0)
  OffsetFirst = 0
  OffsetSecond = 0
  PerimeterLength = 3900
  Placement = pos=(0,0,2341) rot=(0,0,1;0rad)
  PredefinedType = 0
  VerticalArea = 900900
  Width = 380
FEATURE [Part::FeaturePython] Wall375  label="Перемычка монолитн. 016"  # Arch/BIM 166 (typed FeaturePython)
  Align = 0
  Area = 272580
  Base = -> Line1527
  BlockHeight = 0
  BlockLength = 0
  CountBroken = 0
  CountEntire = 0
  Face = 0
  GlobalId = 16$DxRw$TB6BfQSNqz60Qz
  Height = 231
  HorizontalArea = 448400
  IfcData = IfcUID=16$DxRw$TB6BfQSNqz60Qz,+2 more (map truncated)
  IfcType = 166
  Joint = 0
  Length = 1180
  MakeBlocks = false
  Material = -> Material001
  MoveBase = false
  MoveWithHost = false
  Normal = (0,0,0)
  OffsetFirst = 0
  OffsetSecond = 0
  PerimeterLength = 3120
  Placement = pos=(0,0,2341) rot=(0,0,1;0rad)
  PredefinedType = 0
  VerticalArea = 720720
  Width = 380
FEATURE [Part::FeaturePython] Wall376  label="Перемычка монолитн. 017"  # Arch/BIM 166 (typed FeaturePython)
  Align = 1
  Area = 572880
  Base = -> Line1529
  BlockHeight = 0
  BlockLength = 0
  CountBroken = 0
  CountEntire = 0
  Face = 0
  GlobalId = 0AqGC86W9B8PvMAPbhOTte
  Height = 231
  HorizontalArea = 942400
  IfcData = IfcUID=0AqGC86W9B8PvMAPbhOTte,+2 more (map truncated)
  IfcType = 166
  Joint = 0
  Length = 2480
  MakeBlocks = false
  Material = -> Material001
  MoveBase = false
  MoveWithHost = false
  Normal = (0,0,0)
  OffsetFirst = 0
  OffsetSecond = 0
  PerimeterLength = 5720
  Placement = pos=(0,0,2572) rot=(0,0,1;0rad)
  PredefinedType = 0
  VerticalArea = 1321320
  Width = 380
FEATURE [Part::FeaturePython] Wall377  label="Перемычка монолитн. 018"  # Arch/BIM 166 (typed FeaturePython)
  Align = 0
  Area = 452760
  Base = -> Line1530
  BlockHeight = 0
  BlockLength = 0
  CountBroken = 0
  CountEntire = 0
  Face = 0
  GlobalId = 23sFNS3FX7B9N2mOSbHlu1
  Height = 231
  HorizontalArea = 744800
  IfcData = IfcUID=23sFNS3FX7B9N2mOSbHlu1,+2 more (map truncated)
  IfcType = 166
  Joint = 0
  Length = 1960
  MakeBlocks = false
  Material = -> Material001
  MoveBase = false
  MoveWithHost = false
  Normal = (0,0,0)
  OffsetFirst = 0
  OffsetSecond = 0
  PerimeterLength = 4680
  Placement = pos=(0,0,2572) rot=(0,0,1;0rad)
  PredefinedType = 0
  VerticalArea = 1081080
  Width = 380
FEATURE [Part::FeaturePython] Wall371  label="Стена064"  # Arch/BIM 166 (typed FeaturePython)
  Align = 1
  Area = 1831830
  Base = -> Line1341
  BlockHeight = 231
  BlockLength = 256
  CountBroken = 3
  CountEntire = 21
  Face = 0
  Height = 231
  HorizontalArea = 0
  IfcData = attributes={"GlobalId": {"name": "GlobalId", "type": "IfcGloballyUniqueId", "is_enum": false, "enum_values": []}, "Description": {"... (+533 chars omitted),+1 more (map truncated)
  IfcType = 166
  Joint = 0
  Length = 7930
  MakeBlocks = true
  Material = -> Material004
  MoveBase = false
  MoveWithHost = false
  Normal = (0,0,0)
  OffsetFirst = 0
  OffsetSecond = 0
  PerimeterLength = 0
  Placement = pos=(0,0,2572) rot=(0,0,1;0rad)
  PredefinedType = 0
  Subtractions = -> [Wall377]
  VerticalArea = 0
  Width = 380
FEATURE [Part::FeaturePython] Wall378  label="Перемычка монолитн. 019"  # Arch/BIM 166 (typed FeaturePython)
  Align = 1
  Area = 332640
  Base = -> Line1531
  BlockHeight = 0
  BlockLength = 0
  CountBroken = 0
  CountEntire = 0
  Face = 0
  GlobalId = 2TdxzIhfb2oA4zfHjvmbo2
  Height = 231
  HorizontalArea = 547200
  IfcData = IfcUID=2TdxzIhfb2oA4zfHjvmbo2,+2 more (map truncated)
  IfcType = 166
  Joint = 0
  Length = 1440
  MakeBlocks = false
  Material = -> Material001
  MoveBase = false
  MoveWithHost = false
  Normal = (0,0,0)
  OffsetFirst = 0
  OffsetSecond = 0
  PerimeterLength = 3640
  Placement = pos=(0,0,2572) rot=(0,0,1;0rad)
  PredefinedType = 0
  VerticalArea = 840840
  Width = 380
FEATURE [Part::FeaturePython] Wall368  label="Стена061"  # Arch/BIM 166 (typed FeaturePython)
  Align = 1
  Area = 1831830
  Base = -> Line1342
  BlockHeight = 231
  BlockLength = 256
  CountBroken = 5
  CountEntire = 12
  Face = 0
  Height = 231
  HorizontalArea = 0
  IfcData = attributes={"GlobalId": {"name": "GlobalId", "type": "IfcGloballyUniqueId", "is_enum": false, "enum_values": []}, "Description": {"... (+533 chars omitted),+1 more (map truncated)
  IfcType = 166
  Joint = 0
  Length = 7930
  MakeBlocks = true
  Material = -> Material004
  MoveBase = false
  MoveWithHost = false
  Normal = (0,0,0)
  OffsetFirst = 0
  OffsetSecond = 0
  PerimeterLength = 0
  Placement = pos=(0,0,2572) rot=(0,0,1;0rad)
  PredefinedType = 0
  Subtractions = -> [Wall378,Wall376]
  VerticalArea = 0
  Width = 380
FEATURE [Part::FeaturePython] Wall379  label="Перемычка монолитн. 020"  # Arch/BIM 166 (typed FeaturePython)
  Align = 0
  Area = 272580
  Base = -> Line1537
  BlockHeight = 0
  BlockLength = 0
  CountBroken = 0
  CountEntire = 0
  Face = 0
  GlobalId = 2dIW8Z8qb1VQVoHMf0gHj5
  Height = 231
  HorizontalArea = 448400
  IfcData = IfcUID=2dIW8Z8qb1VQVoHMf0gHj5,+2 more (map truncated)
  IfcType = 166
  Joint = 0
  Length = 1180
  MakeBlocks = false
  Material = -> Material001
  MoveBase = false
  MoveWithHost = false
  Normal = (0,0,0)
  OffsetFirst = 0
  OffsetSecond = 0
  PerimeterLength = 3120
  Placement = pos=(0,0,2341) rot=(0,0,1;0rad)
  PredefinedType = 0
  VerticalArea = 720720
  Width = 380
FEATURE [Part::FeaturePython] Wall367  label="Стена060"  # Arch/BIM 166 (typed FeaturePython)
  Align = 0
  Area = 3003000
  Base = -> Line1351
  BlockHeight = 231
  BlockLength = 255
  CountBroken = 7
  CountEntire = 31
  Face = 0
  Height = 231
  HorizontalArea = 0
  IfcData = attributes={"GlobalId": {"name": "GlobalId", "type": "IfcGloballyUniqueId", "is_enum": false, "enum_values": []}, "Description": {"... (+533 chars omitted),+1 more (map truncated)
  IfcType = 166
  Joint = 0
  Length = 13000
  MakeBlocks = true
  Material = -> Material004
  MoveBase = false
  MoveWithHost = false
  Normal = (0,0,0)
  OffsetFirst = 0
  OffsetSecond = 0
  PerimeterLength = 0
  Placement = pos=(0,0,2341) rot=(0,0,1;0rad)
  PredefinedType = 0
  Subtractions = -> [Wall379,Wall375,Wall374]
  VerticalArea = 0
  Width = 380
FEATURE [App::GeometryPython] BuildingPart118  label="ряд 012"  # Arch/BIM 52 (typed FeaturePython)
  Area = 9669660
  Group = -> [Wall367,Wall366,Wall364,Wall365]
  Height = 0
  HeightPropagate = true
  IfcData = attributes={"GlobalId": {"name": "GlobalId", "type": "IfcGloballyUniqueId", "is_enum": false, "enum_values": []}, "Description": {"... (+484 chars omitted),+1 more (map truncated)
  IfcType = 52
  LevelOffset = 0
FEATURE [Part::FeaturePython] Wall380  label="Перемычка монолитн. 021"  # Arch/BIM 166 (typed FeaturePython)
  Align = 1
  Area = 572880
  Base = -> Line1538
  BlockHeight = 0
  BlockLength = 0
  CountBroken = 0
  CountEntire = 0
  Face = 0
  GlobalId = 3keULZXVT8QA_IAgUQCOo2
  Height = 231
  HorizontalArea = 942400
  IfcData = IfcUID=3keULZXVT8QA_IAgUQCOo2,+2 more (map truncated)
  IfcType = 166
  Joint = 0
  Length = 2480
  MakeBlocks = false
  Material = -> Material001
  MoveBase = false
  MoveWithHost = false
  Normal = (0,0,0)
  OffsetFirst = 0
  OffsetSecond = 0
  PerimeterLength = 5720
  Placement = pos=(0,-9.09e-13,2572) rot=(0,0,1;0rad)
  PredefinedType = 0
  VerticalArea = 1321320
  Width = 380
FEATURE [Part::FeaturePython] Wall369  label="Стена062"  # Arch/BIM 166 (typed FeaturePython)
  Align = 1
  Area = 3003000
  Base = -> Line1349
  BlockHeight = 231
  BlockLength = 255
  CountBroken = 7
  CountEntire = 22
  Face = 0
  Height = 231
  HorizontalArea = 0
  IfcData = attributes={"GlobalId": {"name": "GlobalId", "type": "IfcGloballyUniqueId", "is_enum": false, "enum_values": []}, "Description": {"... (+533 chars omitted),+1 more (map truncated)
  IfcType = 166
  Joint = 0
  Length = 13000
  MakeBlocks = true
  Material = -> Material004
  MoveBase = false
  MoveWithHost = false
  Normal = (0,0,0)
  OffsetFirst = 0
  OffsetSecond = 0
  PerimeterLength = 0
  Placement = pos=(0,0,2572) rot=(0,0,1;0rad)
  PredefinedType = 0
  Subtractions = -> [Structure308,Wall372,Wall373,Wall380]
  VerticalArea = 0
  Width = 380
FEATURE [App::GeometryPython] BuildingPart119  label="ряд 013"  # Arch/BIM 52 (typed FeaturePython)
  Area = 9669660
  Group = -> [Wall370,Wall369,Wall371,Wall368]
  Height = 0
  HeightPropagate = true
  IfcData = attributes={"GlobalId": {"name": "GlobalId", "type": "IfcGloballyUniqueId", "is_enum": false, "enum_values": []}, "Description": {"... (+484 chars omitted),+1 more (map truncated)
  IfcType = 52
  LevelOffset = 0
FEATURE [Part::FeaturePython] Wall381  label="Стена065"  # Arch/BIM 166 (typed FeaturePython)
  Align = 1
  Area = 1919610
  Base = -> Line1427
  BlockHeight = 231
  BlockLength = 256
  CountBroken = 2
  CountEntire = 31
  Face = 0
  Height = 231
  HorizontalArea = 0
  IfcData = attributes={"GlobalId": {"name": "GlobalId", "type": "IfcGloballyUniqueId", "is_enum": false, "enum_values": []}, "Description": {"... (+533 chars omitted),+1 more (map truncated)
  IfcType = 166
  Joint = 0
  Length = 8310
  MakeBlocks = true
  Material = -> Material004
  MoveBase = false
  MoveWithHost = false
  Normal = (0,0,0)
  OffsetFirst = 125
  OffsetSecond = 0
  PerimeterLength = 0
  Placement = pos=(0,0,2803) rot=(0,0,1;0rad)
  PredefinedType = 0
  VerticalArea = 0
  Width = 380
FEATURE [Part::FeaturePython] Wall383  label="Стена067"  # Arch/BIM 166 (typed FeaturePython)
  Align = 0
  Area = 1919610
  Base = -> Line1426
  BlockHeight = 231
  BlockLength = 256
  CountBroken = 1
  CountEntire = 32
  Face = 0
  Height = 231
  HorizontalArea = 0
  IfcData = attributes={"GlobalId": {"name": "GlobalId", "type": "IfcGloballyUniqueId", "is_enum": false, "enum_values": []}, "Description": {"... (+533 chars omitted),+1 more (map truncated)
  IfcType = 166
  Joint = 0
  Length = 8310
  MakeBlocks = true
  Material = -> Material004
  MoveBase = false
  MoveWithHost = false
  Normal = (0,0,0)
  OffsetFirst = 0
  OffsetSecond = 0
  PerimeterLength = 0
  Placement = pos=(0,0,2803) rot=(0,0,1;0rad)
  PredefinedType = 0
  VerticalArea = 0
  Width = 380
FEATURE [App::GeometryPython] BuildingPart120  label="ряд 014"  # Arch/BIM 52 (typed FeaturePython)
  Area = 3839220
  Group = -> [Wall383,Wall381]
  Height = 0
  HeightPropagate = true
  IfcData = attributes={"GlobalId": {"name": "GlobalId", "type": "IfcGloballyUniqueId", "is_enum": false, "enum_values": []}, "Description": {"... (+484 chars omitted),+1 more (map truncated)
  IfcType = 52
  LevelOffset = 0
FEATURE [Part::FeaturePython] Wall384  label="Стена068"  # Arch/BIM 166 (typed FeaturePython)
  Align = 1
  Area = 1831830
  Base = -> Line1342
  BlockHeight = 231
  BlockLength = 256
  CountBroken = 1
  CountEntire = 30
  Face = 0
  Height = 231
  HorizontalArea = 0
  IfcData = attributes={"GlobalId": {"name": "GlobalId", "type": "IfcGloballyUniqueId", "is_enum": false, "enum_values": []}, "Description": {"... (+533 chars omitted),+1 more (map truncated)
  IfcType = 166
  Joint = 0
  Length = 7930
  MakeBlocks = true
  Material = -> Material004
  MoveBase = false
  MoveWithHost = false
  Normal = (0,0,0)
  OffsetFirst = 0
  OffsetSecond = 0
  PerimeterLength = 0
  Placement = pos=(0,0,3034) rot=(0,0,1;0rad)
  PredefinedType = 0
  VerticalArea = 0
  Width = 380
FEATURE [Part::FeaturePython] Wall385  label="Стена069"  # Arch/BIM 166 (typed FeaturePython)
  Align = 1
  Area = 3003000
  Base = -> Line1349
  BlockHeight = 231
  BlockLength = 255
  CountBroken = 1
  CountEntire = 50
  Face = 0
  Height = 231
  HorizontalArea = 0
  IfcData = attributes={"GlobalId": {"name": "GlobalId", "type": "IfcGloballyUniqueId", "is_enum": false, "enum_values": []}, "Description": {"... (+533 chars omitted),+1 more (map truncated)
  IfcType = 166
  Joint = 0
  Length = 13000
  MakeBlocks = true
  Material = -> Material004
  MoveBase = false
  MoveWithHost = false
  Normal = (0,0,0)
  OffsetFirst = 0
  OffsetSecond = 0
  PerimeterLength = 0
  Placement = pos=(0,0,3034) rot=(0,0,1;0rad)
  PredefinedType = 0
  VerticalArea = 0
  Width = 380
FEATURE [Part::FeaturePython] Wall386  label="Стена070"  # Arch/BIM 166 (typed FeaturePython)
  Align = 1
  Area = 3003000
  Base = -> Line1340
  BlockHeight = 231
  BlockLength = 255
  CountBroken = 1
  CountEntire = 50
  Face = 0
  Height = 231
  HorizontalArea = 0
  IfcData = attributes={"GlobalId": {"name": "GlobalId", "type": "IfcGloballyUniqueId", "is_enum": false, "enum_values": []}, "Description": {"... (+533 chars omitted),+1 more (map truncated)
  IfcType = 166
  Joint = 0
  Length = 13000
  MakeBlocks = true
  Material = -> Material004
  MoveBase = false
  MoveWithHost = false
  Normal = (0,0,0)
  OffsetFirst = 0
  OffsetSecond = 0
  PerimeterLength = 0
  Placement = pos=(0,0,3034) rot=(0,0,1;0rad)
  PredefinedType = 0
  VerticalArea = 0
  Width = 380
FEATURE [Part::FeaturePython] Wall387  label="Стена071"  # Arch/BIM 166 (typed FeaturePython)
  Align = 1
  Area = 1831830
  Base = -> Line1341
  BlockHeight = 231
  BlockLength = 256
  CountBroken = 1
  CountEntire = 30
  Face = 0
  Height = 231
  HorizontalArea = 0
  IfcData = attributes={"GlobalId": {"name": "GlobalId", "type": "IfcGloballyUniqueId", "is_enum": false, "enum_values": []}, "Description": {"... (+533 chars omitted),+1 more (map truncated)
  IfcType = 166
  Joint = 0
  Length = 7930
  MakeBlocks = true
  Material = -> Material004
  MoveBase = false
  MoveWithHost = false
  Normal = (0,0,0)
  OffsetFirst = 0
  OffsetSecond = 0
  PerimeterLength = 0
  Placement = pos=(0,0,3034) rot=(0,0,1;0rad)
  PredefinedType = 0
  VerticalArea = 0
  Width = 380
FEATURE [App::GeometryPython] BuildingPart121  label="ряд 015"  # Arch/BIM 52 (typed FeaturePython)
  Area = 9669660
  Group = -> [Wall386,Wall385,Wall387,Wall384]
  Height = 0
  HeightPropagate = true
  IfcData = attributes={"GlobalId": {"name": "GlobalId", "type": "IfcGloballyUniqueId", "is_enum": false, "enum_values": []}, "Description": {"... (+484 chars omitted),+1 more (map truncated)
  IfcType = 52
  LevelOffset = 0
FEATURE [Part::FeaturePython] Wall388  label="Стена072"  # Arch/BIM 166 (typed FeaturePython)
  Align = 0
  Area = 1831830
  Base = -> Line1343
  BlockHeight = 231
  BlockLength = 256
  CountBroken = 1
  CountEntire = 30
  Face = 0
  Height = 231
  HorizontalArea = 0
  IfcData = attributes={"GlobalId": {"name": "GlobalId", "type": "IfcGloballyUniqueId", "is_enum": false, "enum_values": []}, "Description": {"... (+533 chars omitted),+1 more (map truncated)
  IfcType = 166
  Joint = 0
  Length = 7930
  MakeBlocks = true
  Material = -> Material004
  MoveBase = false
  MoveWithHost = false
  Normal = (0,0,0)
  OffsetFirst = 0
  OffsetSecond = 0
  PerimeterLength = 0
  Placement = pos=(0,0,3265) rot=(0,0,1;0rad)
  PredefinedType = 0
  VerticalArea = 0
  Width = 380
FEATURE [Part::FeaturePython] Wall389  label="Стена073"  # Arch/BIM 166 (typed FeaturePython)
  Align = 0
  Area = 3003000
  Base = -> Line1350
  BlockHeight = 231
  BlockLength = 255
  CountBroken = 1
  CountEntire = 50
  Face = 0
  Height = 231
  HorizontalArea = 0
  IfcData = attributes={"GlobalId": {"name": "GlobalId", "type": "IfcGloballyUniqueId", "is_enum": false, "enum_values": []}, "Description": {"... (+533 chars omitted),+1 more (map truncated)
  IfcType = 166
  Joint = 0
  Length = 13000
  MakeBlocks = true
  Material = -> Material004
  MoveBase = false
  MoveWithHost = false
  Normal = (0,0,0)
  OffsetFirst = 0
  OffsetSecond = 0
  PerimeterLength = 0
  Placement = pos=(0,0,3265) rot=(0,0,1;0rad)
  PredefinedType = 0
  VerticalArea = 0
  Width = 380
FEATURE [Part::FeaturePython] Wall390  label="Стена074"  # Arch/BIM 166 (typed FeaturePython)
  Align = 0
  Area = 1.83183e+06
  Base = -> Line1347
  BlockHeight = 231
  BlockLength = 256
  CountBroken = 1
  CountEntire = 30
  Face = 0
  Height = 231
  HorizontalArea = 0
  IfcData = attributes={"GlobalId": {"name": "GlobalId", "type": "IfcGloballyUniqueId", "is_enum": false, "enum_values": []}, "Description": {"... (+533 chars omitted),+1 more (map truncated)
  IfcType = 166
  Joint = 0
  Length = 7930
  MakeBlocks = true
  Material = -> Material004
  MoveBase = false
  MoveWithHost = false
  Normal = (0,0,0)
  OffsetFirst = 0
  OffsetSecond = 0
  PerimeterLength = 0
  Placement = pos=(0,0,3265) rot=(0,0,1;0rad)
  PredefinedType = 0
  VerticalArea = 0
  Width = 380
FEATURE [Part::FeaturePython] Wall391  label="Стена075"  # Arch/BIM 166 (typed FeaturePython)
  Align = 0
  Area = 3003000
  Base = -> Line1351
  BlockHeight = 231
  BlockLength = 255
  CountBroken = 1
  CountEntire = 50
  Face = 0
  Height = 231
  HorizontalArea = 0
  IfcData = attributes={"GlobalId": {"name": "GlobalId", "type": "IfcGloballyUniqueId", "is_enum": false, "enum_values": []}, "Description": {"... (+533 chars omitted),+1 more (map truncated)
  IfcType = 166
  Joint = 0
  Length = 13000
  MakeBlocks = true
  Material = -> Material004
  MoveBase = false
  MoveWithHost = false
  Normal = (0,0,0)
  OffsetFirst = 0
  OffsetSecond = 0
  PerimeterLength = 0
  Placement = pos=(0,0,3265) rot=(0,0,1;0rad)
  PredefinedType = 0
  VerticalArea = 0
  Width = 380
FEATURE [App::GeometryPython] BuildingPart122  label="ряд 016"  # Arch/BIM 52 (typed FeaturePython)
  Area = 9669660
  Group = -> [Wall391,Wall389,Wall390,Wall388]
  Height = 0
  HeightPropagate = true
  IfcData = attributes={"GlobalId": {"name": "GlobalId", "type": "IfcGloballyUniqueId", "is_enum": false, "enum_values": []}, "Description": {"... (+484 chars omitted),+1 more (map truncated)
  IfcType = 52
  LevelOffset = 0
FEATURE [App::GeometryPython] BuildingPart078  label="Порядовка"  # Arch/BIM 52 (typed FeaturePython)
  Area = 90866160
  Group = -> [BuildingPart077,BuildingPart072,Component151,Component152,Component153,BuildingPart117,BuildingPart116,BuildingPart115,Component154,Component155,Component156,BuildingPart118,BuildingPart119,BuildingPart120,BuildingPart121,BuildingPart122]
  Height = 0
  HeightPropagate = true
  IfcData = attributes={"GlobalId": {"name": "GlobalId", "type": "IfcGloballyUniqueId", "is_enum": false, "enum_values": []}, "Description": {"... (+484 chars omitted),+1 more (map truncated)
  IfcType = 52
  LevelOffset = 0
FEATURE [Part::Part2DObjectPython] Rectangle3404  label="Д90-мансарда-001"  # Draft 2D object (typed FeaturePython)
  Area = 164250
  ChamferSize = 0
  Columns = 1
  FilletRadius = 0
  Height = 900
  Length = 182.5
  MakeFace = true
  Placement = pos=(6550,3642.5,0) rot=(0,0,1;1.5708rad)
  Rows = 1
FEATURE [Part::Part2DObjectPython] Line1738  # Draft 2D object (typed FeaturePython)
  Area = 0
  ChamferSize = 0
  Closed = false
  End = (6500,3805,0)
  FilletRadius = 0
  Length = 800
  MakeFace = false
  Placement = pos=(6500,4605,0) rot=(0,0,-1;0.785398rad)
  Points = (2) [(0,0,0),(565.685,-565.685,0)]
  Start = (6500,4605,0)
  Subdivisions = 0
FEATURE [Part::Part2DObjectPython] Arc128  label="Arc129"  # Draft 2D object (typed FeaturePython)
  Area = 0
  FirstAngle = -225
  LastAngle = -135
  MakeFace = false
  Placement = pos=(6500,3805,0) rot=(0,0,-1;0.785398rad)
  Radius = 800
FEATURE [Part::Part2DObjectPython] Wire921  # Draft 2D object (typed FeaturePython)
  Area = 0
  ChamferSize = 0
  Closed = true
  End = (6737.5,6900,0)
  FilletRadius = 0
  Length = 10465.1
  MakeFace = false
  Placement = pos=(6750.76,3805,0) rot=(0,0,1;0rad)
  Points = (5) [(-13.2612,-4.54747e-13,0),(-1525.1,-4.54747e-13,0),(-2410,884.899,0),(-2410,3095,0),(-13.2612,3095,0)]
  Start = (6737.5,3805,0)
  Subdivisions = 0
FEATURE [Part::Part2DObjectPython] Wire922  # Draft 2D object (typed FeaturePython)
  Area = 0
  ChamferSize = 0
  Closed = true
  End = (3300.05,3780,0)
  FilletRadius = 0
  Length = 14184.8
  MakeFace = false
  Placement = pos=(-29.2388,3780,0) rot=(0,0,1;0rad)
  Points = (7) [(-13.26,0,0),(-13.26,2550,0),(570,2550,0),(570,3120,0),(4220,3120,0),(4220,890.71,0),(3329.29,0,0)]
  Start = (-42.4988,3780,0)
  Subdivisions = 0
FEATURE [Part::Part2DObjectPython] Wire923  # Draft 2D object (typed FeaturePython)
  Area = 0
  ChamferSize = 0
  Closed = true
  End = (-42.4988,1130,0)
  FilletRadius = 0
  Length = 14183.7
  MakeFace = false
  Placement = pos=(-29.2388,3680,0) rot=(0,0,1;0rad)
  Points = (7) [(-13.26,0,0),(3329.29,0,0),(4219.24,-889.949,0),(4219.24,-3120,0),(570,-3120,0),(570,-2550,0),(-13.26,-2550,0)]
  Start = (-42.4988,3680,0)
  Subdivisions = 0
FEATURE [Part::MultiFuse] Fusion072
  Shapes = -> [Extrude092,Roof015]
FEATURE [Part::Part2DObjectPython] Rectangle3249  # Draft 2D object (typed FeaturePython)
  Area = 237147
  ChamferSize = 0
  Columns = 1
  FilletRadius = 0
  Height = 2371.47
  Length = 100
  MakeFace = true
  Placement = pos=(4190,560,0) rot=(0,0,1;0rad)
  Rows = 1
FEATURE [Part::Part2DObjectPython] Wire927  # Draft 2D object (typed FeaturePython)
  Area = 0
  ChamferSize = 0
  Closed = true
  End = (11980,560,0)
  FilletRadius = 0
  Length = 21640
  MakeFace = false
  Placement = pos=(9200,560,0) rot=(0,0,1;0rad)
  Points = (10) [(0,0,0),(0,3245,0),(-1117.5,3245,0),(-1117.5,6340,0),(2780,6340,0),(2780,5770,0),(3362.5,5770,0),(3362.5,570,0),(2780,570,0),(2780,-1.13687e-13,0)]
  Start = (9200,560,0)
  Subdivisions = 0
FEATURE [Part::Part2DObjectPython] Wire928  # Draft 2D object (typed FeaturePython)
  Area = 0
  ChamferSize = 0
  Closed = true
  End = (9100.76,560,0)
  FilletRadius = 0
  Length = 18603.5
  MakeFace = false
  Placement = pos=(4290,560,0) rot=(0,0,1;0rad)
  Points = (13) [(0,0,0),(0,2271.47,0),(-819.239,3090.71,0),(-819.239,3249.29,0),(-100.761,3967.77,0),(0.761184,3967.77,0),(873.528,3095,0),(4810.76,3095,0),+5 more]
  Start = (4290,560,0)
  Subdivisions = 0
FEATURE [Part::Part2DObjectPython] Rectangle3406  label="Д100-мансарда-013"  # Draft 2D object (typed FeaturePython)
  Area = 331500
  ChamferSize = 0
  Columns = 1
  FilletRadius = 0
  Height = 1020
  Length = 325
  MakeFace = true
  Placement = pos=(7920,3492.5,0) rot=(0,0,1;1.5708rad)
  Rows = 1
FEATURE [Part::Part2DObjectPython] Rectangle3407  label="Д90-мансарда-014"  # Draft 2D object (typed FeaturePython)
  Area = 112500
  ChamferSize = 0
  Columns = 1
  FilletRadius = 0
  Height = 900
  Length = 125
  MakeFace = true
  Placement = pos=(4054.38,2907.99,0) rot=(0,0,1;0.785398rad)
  Rows = 1
FEATURE [Part::Part2DObjectPython] Rectangle3408  label="Д90-мансарда-015"  # Draft 2D object (typed FeaturePython)
  Area = 112500
  ChamferSize = 0
  Columns = 1
  FilletRadius = 0
  Height = 900
  Length = 125
  MakeFace = true
  Placement = pos=(4142.77,4463.62,0) rot=(0,0,1;2.35619rad)
  Rows = 1
FEATURE [Part::FeaturePython] Structure461  label="Проём Д90-манс_012"  # Arch/BIM 172 (typed FeaturePython)
  Base = -> Rectangle3408
  FaceMaker = 0
  Height = 2150
  HorizontalArea = 112500
  IfcData = attributes={"GlobalId": {"name": "GlobalId", "type": "IfcGloballyUniqueId", "is_enum": false, "enum_values": []}, "Description": {"... (+484 chars omitted),+1 more (map truncated)
  IfcType = 172
  Length = 0
  MoveBase = false
  MoveWithHost = false
  Nodes = (2) [(-5635.64,-289.376,0),(-5635.64,-289.376,2150)]
  NodesOffset = 0
  Normal = (0,0,0)
  PerimeterLength = 2050
  Placement = pos=(0,0,3130) rot=(0,0,1;0rad)
  PredefinedType = 0
  VerticalArea = 4.4075e+06
  Width = 100
FEATURE [Part::FeaturePython] Structure462  label="Проём Д90-манс_001"  # Arch/BIM 172 (typed FeaturePython)
  Base = -> Rectangle3407
  FaceMaker = 0
  Height = 2150
  HorizontalArea = 112500
  IfcData = attributes={"GlobalId": {"name": "GlobalId", "type": "IfcGloballyUniqueId", "is_enum": false, "enum_values": []}, "Description": {"... (+484 chars omitted),+1 more (map truncated)
  IfcType = 172
  Length = 0
  MoveBase = false
  MoveWithHost = false
  Nodes = (2) [(360.086,4985.1,0),(360.086,4985.1,2170)]
  NodesOffset = 0
  Normal = (0,0,0)
  PerimeterLength = 2050
  Placement = pos=(0,0,3130) rot=(0,0,1;0rad)
  PredefinedType = 0
  VerticalArea = 4.4075e+06
  Width = 100
FEATURE [Part::FeaturePython] Structure463  label="Проём Д90-манс_013"  # Arch/BIM 172 (typed FeaturePython)
  Base = -> Rectangle3404
  FaceMaker = 0
  Height = 2150
  HorizontalArea = 164250
  IfcData = attributes={"GlobalId": {"name": "GlobalId", "type": "IfcGloballyUniqueId", "is_enum": false, "enum_values": []}, "Description": {"... (+484 chars omitted),+1 more (map truncated)
  IfcType = 172
  Length = 0
  MoveBase = false
  MoveWithHost = false
  Nodes = (2) [(-3733.75,6100,0),(-3733.75,6100,2170)]
  NodesOffset = 0
  Normal = (0,0,0)
  PerimeterLength = 2165
  Placement = pos=(0,0,3130) rot=(0,0,1;0rad)
  PredefinedType = 0
  VerticalArea = 4654750
  Width = 100
FEATURE [Part::FeaturePython] Wall392  label="Стена076"  # Arch/BIM 166 (typed FeaturePython)
  Align = 0
  Area = 2.84651e+07
  Base = -> Wire921
  BlockHeight = 0
  BlockLength = 0
  CountBroken = 0
  CountEntire = 0
  Face = 0
  Height = 2720
  HorizontalArea = 207771
  IfcData = attributes={"GlobalId": {"name": "GlobalId", "type": "IfcGloballyUniqueId", "is_enum": false, "enum_values": []}, "Description": {"... (+533 chars omitted),+1 more (map truncated)
  IfcType = 166
  Joint = 0
  Length = 10465.1
  MakeBlocks = false
  MoveBase = false
  MoveWithHost = false
  Normal = (0,0,0)
  OffsetFirst = 0
  OffsetSecond = 0
  PerimeterLength = 10465.1
  Placement = pos=(0,0,3130) rot=(0,0,1;0rad)
  PredefinedType = 0
  Subtractions = -> [Structure463]
  VerticalArea = 5.27297e+07
  Width = 20
FEATURE [Part::FeaturePython] Structure464  label="Проём Д100-манс_011"  # Arch/BIM 172 (typed FeaturePython)
  Base = -> Rectangle3406
  FaceMaker = 0
  Height = 2100
  HorizontalArea = 331500
  IfcData = attributes={"GlobalId": {"name": "GlobalId", "type": "IfcGloballyUniqueId", "is_enum": false, "enum_values": []}, "Description": {"... (+484 chars omitted),+1 more (map truncated)
  IfcType = 172
  Length = 0
  MoveBase = false
  MoveWithHost = false
  Nodes = (2) [(-3723.75,7410,0),(-3723.75,7410,2170)]
  NodesOffset = 0
  Normal = (0,0,0)
  PerimeterLength = 2690
  Placement = pos=(0,0,3130) rot=(0,0,1;0rad)
  PredefinedType = 0
  VerticalArea = 5649000
  Width = 100
FEATURE [Part::FeaturePython] Structure465  label="Проём Д90-манс_010"  # Arch/BIM 172 (typed FeaturePython)
  Base = -> Rectangle3253
  FaceMaker = 0
  Height = 2150
  HorizontalArea = 112500
  IfcData = attributes={"GlobalId": {"name": "GlobalId", "type": "IfcGloballyUniqueId", "is_enum": false, "enum_values": []}, "Description": {"... (+484 chars omitted),+1 more (map truncated)
  IfcType = 172
  Length = 0
  MoveBase = false
  MoveWithHost = false
  Nodes = (2) [(9150,2950,0),(9150,2950,2150)]
  NodesOffset = 0
  Normal = (0,0,0)
  PerimeterLength = 2050
  Placement = pos=(0,0,3130) rot=(0,0,1;0rad)
  PredefinedType = 0
  VerticalArea = 4.4075e+06
  Width = 100
FEATURE [Part::FeaturePython] Wall395  label="Стена079"  # Arch/BIM 166 (typed FeaturePython)
  Align = 0
  Area = 5.06015e+07
  Base = -> Wire928
  BlockHeight = 0
  BlockLength = 0
  CountBroken = 0
  CountEntire = 0
  Face = 0
  Height = 2720
  HorizontalArea = 0
  IfcData = attributes={"GlobalId": {"name": "GlobalId", "type": "IfcGloballyUniqueId", "is_enum": false, "enum_values": []}, "Description": {"... (+533 chars omitted),+1 more (map truncated)
  IfcType = 166
  Joint = 0
  Length = 18603.5
  MakeBlocks = false
  MoveBase = false
  MoveWithHost = false
  Normal = (0,0,0)
  OffsetFirst = 0
  OffsetSecond = 0
  PerimeterLength = 0
  Placement = pos=(0,0,3130) rot=(0,0,1;0rad)
  PredefinedType = 0
  Subtractions = -> [Structure461,Structure464,Structure465,Structure462,Structure463]
  VerticalArea = 0
  Width = 12.5
FEATURE [Part::Part2DObjectPython] Rectangle3409  # Draft 2D object (typed FeaturePython)
  Area = 1.62e+06
  ChamferSize = 0
  Columns = 1
  FilletRadius = 0
  Height = 900
  Length = 1800
  MakeFace = true
  Placement = pos=(6717.5,5080,0) rot=(0,0,1;1.5708rad)
  Rows = 1
FEATURE [Part::Part2DObjectPython] Rectangle3410  # Draft 2D object (typed FeaturePython)
  Area = 270000
  ChamferSize = 0
  Columns = 1
  FilletRadius = 0
  Height = 600
  Length = 450
  MakeFace = true
  Placement = pos=(4360.76,5700,0) rot=(0,0,1;0rad)
  Rows = 1
FEATURE [Part::Part2DObjectPython] Rectangle3412  label="Унитаз Geberit Smyle 54х35 004"  # Draft 2D object (typed FeaturePython)
  ChamferSize = 0
  Columns = 1
  FilletRadius = 0
  Height = 350
  Length = 400
  MakeFace = true
  Placement = pos=(5005.44,4053.5,0) rot=(0,0,1;0.785398rad)
  Rows = 1
FEATURE [Part::Part2DObjectPython] Rectangle3413  # Draft 2D object (typed FeaturePython)
  Area = 270000
  ChamferSize = 0
  Columns = 1
  FilletRadius = 0
  Height = 600
  Length = 450
  MakeFace = true
  Placement = pos=(4360.76,5100,0) rot=(0,0,1;0rad)
  Rows = 1
FEATURE [Part::FeaturePython] Structure466  label="Фронтон каркасн. 003"  # Arch/BIM 52 (typed FeaturePython)
  Base = -> Wire836
  FaceMaker = 0
  GlobalId = 3jxAwhryLARBy7FrCZDeex
  Height = 400
  HorizontalArea = 0
  IfcData = IfcUID=3jxAwhryLARBy7FrCZDeex,+2 more (map truncated)
  IfcType = 52
  Length = 0
  Material = -> Material003
  MoveBase = false
  MoveWithHost = false
  Nodes = (2) [(0,3730,4501.01),(-380,3730,4501.01)]
  NodesOffset = 0
  Normal = (0,0,0)
  PerimeterLength = 14935.2
  Placement = pos=(12950,3.637e-12,10) rot=(0,0,1;0rad)
  VerticalArea = 1.5315e+07
  Width = 100
FEATURE [Part::FeaturePython] Wall396  label="Стена080"  # Arch/BIM 166 (typed FeaturePython)
  Align = 0
  Area = 58860800
  Base = -> Wire927
  BlockHeight = 0
  BlockLength = 0
  CountBroken = 0
  CountEntire = 0
  Face = 0
  Height = 2720
  HorizontalArea = 0
  IfcData = attributes={"GlobalId": {"name": "GlobalId", "type": "IfcGloballyUniqueId", "is_enum": false, "enum_values": []}, "Description": {"... (+533 chars omitted),+1 more (map truncated)
  IfcType = 166
  Joint = 0
  Length = 21640
  MakeBlocks = false
  MoveBase = false
  MoveWithHost = false
  Normal = (0,0,0)
  OffsetFirst = 0
  OffsetSecond = 0
  PerimeterLength = 0
  Placement = pos=(0,0,3130) rot=(0,0,1;0rad)
  PredefinedType = 0
  Subtractions = -> [Structure465,Structure466]
  VerticalArea = 0
  Width = 12.5
FEATURE [Part::FeaturePython] Structure467  label="Фронтон каркасн. 004"  # Arch/BIM 52 (typed FeaturePython)
  Base = -> Wire836
  FaceMaker = 0
  GlobalId = 2MSSJcqfT2sha54GOqmBwm
  Height = 410
  HorizontalArea = 0
  IfcData = IfcUID=2MSSJcqfT2sha54GOqmBwm,+2 more (map truncated)
  IfcType = 52
  Length = 0
  Material = -> Material003
  MoveBase = false
  MoveWithHost = false
  Nodes = (2) [(0,3730,4501.01),(-380,3730,4501.01)]
  NodesOffset = 0
  Normal = (0,0,0)
  PerimeterLength = 0
  Placement = pos=(-20,0,10) rot=(0,0,1;0rad)
  VerticalArea = 1.5315e+07
  Width = 100
FEATURE [Part::FeaturePython] Wall393  label="Стена077"  # Arch/BIM 166 (typed FeaturePython)
  Align = 0
  Area = 3.85825e+07
  Base = -> Wire922
  BlockHeight = 0
  BlockLength = 0
  CountBroken = 0
  CountEntire = 0
  Face = 0
  Height = 2720
  HorizontalArea = 0
  IfcData = attributes={"GlobalId": {"name": "GlobalId", "type": "IfcGloballyUniqueId", "is_enum": false, "enum_values": []}, "Description": {"... (+533 chars omitted),+1 more (map truncated)
  IfcType = 166
  Joint = 0
  Length = 14184.8
  MakeBlocks = false
  MoveBase = false
  MoveWithHost = false
  Normal = (0,0,0)
  OffsetFirst = 0
  OffsetSecond = 0
  PerimeterLength = 0
  Placement = pos=(0,0,3130) rot=(0,0,1;0rad)
  PredefinedType = 0
  Subtractions = -> [Structure461,Structure467]
  VerticalArea = 0
  Width = 12.5
FEATURE [Part::FeaturePython] Wall394  label="Стена078"  # Arch/BIM 166 (typed FeaturePython)
  Align = 0
  Area = 3.85796e+07
  Base = -> Wire923
  BlockHeight = 0
  BlockLength = 0
  CountBroken = 0
  CountEntire = 0
  Face = 0
  Height = 2720
  HorizontalArea = 0
  IfcData = attributes={"GlobalId": {"name": "GlobalId", "type": "IfcGloballyUniqueId", "is_enum": false, "enum_values": []}, "Description": {"... (+533 chars omitted),+1 more (map truncated)
  IfcType = 166
  Joint = 0
  Length = 14183.7
  MakeBlocks = false
  MoveBase = false
  MoveWithHost = false
  Normal = (0,0,0)
  OffsetFirst = 0
  OffsetSecond = 0
  PerimeterLength = 0
  Placement = pos=(0,0,3130) rot=(0,0,1;0rad)
  PredefinedType = 0
  Subtractions = -> [Structure462,Structure467]
  VerticalArea = 0
  Width = 12.5
FEATURE [Part::MultiCommon] Common078  label="отделка (ГКЛ 12.5 мм) 003"
  Shapes = -> [Wall396,Fusion072]
FEATURE [Part::MultiCommon] Common079  label="отделка (ГКЛ 12.5 мм) 004"
  Shapes = -> [Fusion072,Wall394]
FEATURE [Part::MultiCommon] Common080  label="отделка (ГКЛ 12.5 мм) 002"
  Shapes = -> [Fusion072,Wall393]
FEATURE [Part::MultiCommon] Common081  label="отделка (ГКЛ 12.5 мм) 001"
  Shapes = -> [Wall395,Fusion072]
FEATURE [Part::MultiCommon] Common082  label="отделка (ГКЛ+Плитка 20 мм) 003"
  Shapes = -> [Wall392,Fusion072]
FEATURE [Part::Part2DObjectPython] Wire932  # Draft 2D object (typed FeaturePython)
  Area = 0
  ChamferSize = 0
  Closed = false
  End = (7920,7485,0)
  FilletRadius = 0
  Length = 8355
  MakeFace = false
  Placement = pos=(6900,7485,0) rot=(0,0,1;0rad)
  Points = (4) [(0,0,0),(0,-3667.5,0),(1020,-3667.5,0),(1020,0,0)]
  Start = (6900,7485,0)
  Subdivisions = 0
FEATURE [Part::FeaturePython] Wall397  label="Стена081"  # Arch/BIM 166 (typed FeaturePython)
  Align = 0
  Area = 22725600
  Base = -> Wire932
  BlockHeight = 0
  BlockLength = 0
  CountBroken = 0
  CountEntire = 0
  Face = 0
  Height = 2720
  HorizontalArea = 104750
  IfcData = attributes={"GlobalId": {"name": "GlobalId", "type": "IfcGloballyUniqueId", "is_enum": false, "enum_values": []}, "Description": {"... (+533 chars omitted),+1 more (map truncated)
  IfcType = 166
  Joint = 0
  Length = 8355
  MakeBlocks = false
  MoveBase = false
  MoveWithHost = false
  Normal = (0,0,0)
  OffsetFirst = 0
  OffsetSecond = 0
  PerimeterLength = 16785
  Placement = pos=(0,0,3130) rot=(0,0,1;0rad)
  PredefinedType = 0
  Subtractions = -> [Structure464]
  VerticalArea = 41423700
  Width = 12.5
FEATURE [Part::MultiCommon] Common083  label="отделка (ГКЛ 12.5 мм) 005"
  Shapes = -> [Wall397,Fusion072]
FEATURE [Part::FeaturePython] Component157  label="отделка (ГКЛ 12.5 мм) 006"  # Arch/BIM 0 (typed FeaturePython)
  Base = -> Common081
  HorizontalArea = 0
  IfcData = attributes={"GlobalId": {"name": "GlobalId", "type": "IfcGloballyUniqueId", "is_enum": false, "enum_values": []}, "Description": {"... (+538 chars omitted),+1 more (map truncated)
  IfcType = 0
  Material = -> Material008
  MoveBase = false
  MoveWithHost = false
  PerimeterLength = 0
  Placement = pos=(0.76123,0,0) rot=(0,0,1;0rad)
  PredefinedType = 0
  VerticalArea = 0
FEATURE [Part::FeaturePython] Component158  label="отделка (ГКЛ 12.5 мм) 007"  # Arch/BIM 0 (typed FeaturePython)
  Base = -> Common080
  HorizontalArea = 0
  IfcData = attributes={"GlobalId": {"name": "GlobalId", "type": "IfcGloballyUniqueId", "is_enum": false, "enum_values": []}, "Description": {"... (+538 chars omitted),+1 more (map truncated)
  IfcType = 0
  Material = -> Material008
  MoveBase = false
  MoveWithHost = false
  PerimeterLength = 0
  Placement = pos=(0.76123,0,0) rot=(0,0,1;0rad)
  PredefinedType = 0
  VerticalArea = 0
FEATURE [Part::FeaturePython] Component159  label="отделка (ГКЛ 12.5 мм) 008"  # Arch/BIM 0 (typed FeaturePython)
  Base = -> Common078
  HorizontalArea = 0
  IfcData = attributes={"GlobalId": {"name": "GlobalId", "type": "IfcGloballyUniqueId", "is_enum": false, "enum_values": []}, "Description": {"... (+538 chars omitted),+1 more (map truncated)
  IfcType = 0
  Material = -> Material008
  MoveBase = false
  MoveWithHost = false
  PerimeterLength = 0
  PredefinedType = 0
  VerticalArea = 0
FEATURE [Part::FeaturePython] Component160  label="отделка (ГКЛ 12.5 мм) 009"  # Arch/BIM 0 (typed FeaturePython)
  Base = -> Common079
  HorizontalArea = 0
  IfcData = attributes={"GlobalId": {"name": "GlobalId", "type": "IfcGloballyUniqueId", "is_enum": false, "enum_values": []}, "Description": {"... (+538 chars omitted),+1 more (map truncated)
  IfcType = 0
  Material = -> Material008
  MoveBase = false
  MoveWithHost = false
  PerimeterLength = 0
  Placement = pos=(0.76123,0,0) rot=(0,0,1;0rad)
  PredefinedType = 0
  VerticalArea = 0
FEATURE [Part::FeaturePython] Component161  label="отделка (ГКЛ+Плитка 20 мм) 002"  # Arch/BIM 0 (typed FeaturePython)
  Base = -> Common082
  HorizontalArea = 0
  IfcData = attributes={"GlobalId": {"name": "GlobalId", "type": "IfcGloballyUniqueId", "is_enum": false, "enum_values": []}, "Description": {"... (+538 chars omitted),+1 more (map truncated)
  IfcType = 0
  Material = -> Material005
  MoveBase = false
  MoveWithHost = false
  PerimeterLength = 0
  Placement = pos=(0.76123,0,0) rot=(0,0,1;0rad)
  PredefinedType = 0
  VerticalArea = 0
FEATURE [Part::FeaturePython] Component162  label="отделка (ГКЛ 12.5 мм) 010"  # Arch/BIM 0 (typed FeaturePython)
  Base = -> Common083
  HorizontalArea = 0
  IfcData = attributes={"GlobalId": {"name": "GlobalId", "type": "IfcGloballyUniqueId", "is_enum": false, "enum_values": []}, "Description": {"... (+538 chars omitted),+1 more (map truncated)
  IfcType = 0
  Material = -> Material008
  MoveBase = false
  MoveWithHost = false
  PerimeterLength = 0
  PredefinedType = 0
  VerticalArea = 0
FEATURE [Part::Part2DObjectPython] Wire933  label="Детская №1"  # Draft 2D object (typed FeaturePython)
  Area = 1.23019e+07
  ChamferSize = 0
  Closed = true
  End = (3294.87,3792.5,0)
  FilletRadius = 0
  Length = 14089
  MakeFace = true
  Placement = pos=(-29.2388,3792.5,0) rot=(0,0,1;0rad)
  Points = (7) [(-0.76123,0,0),(-0.76123,2525,0),(582.5,2525,0),(582.5,3095,0),(4207.5,3095,0),(4207.5,883.388,0),(3324.11,0,0)]
  Start = (-30,3792.5,0)
  Subdivisions = 0
FEATURE [Part::Part2DObjectPython] Wire934  label="СУ №2"  # Draft 2D object (typed FeaturePython)
  Area = 6.81861e+06
  ChamferSize = 0
  Closed = true
  End = (4360.76,4698.18,0)
  FilletRadius = 0
  Length = 10312
  MakeFace = true
  Placement = pos=(4310.76,6880,0) rot=(0,0,1;0rad)
  Points = (5) [(50,0,0),(2406.74,0,0),(2406.74,-3055,0),(923.183,-3055,0),(50,-2181.82,0)]
  Start = (4360.76,6880,0)
  Subdivisions = 0
FEATURE [Part::Part2DObjectPython] Wire935  label="Лестница"  # Draft 2D object (typed FeaturePython)
  Area = 3740850
  ChamferSize = 0
  Closed = true
  End = (7920,3817.5,0)
  FilletRadius = 0
  Length = 9375
  MakeFace = true
  Placement = pos=(6900,3817.5,0) rot=(0,0,1;0rad)
  Points = (4) [(0,0,0),(0,3667.5,0),(1020,3667.5,0),(1020,0,0)]
  Start = (6900,3817.5,0)
  Subdivisions = 0
FEATURE [Part::Part2DObjectPython] Wire936  label="Спальня №2"  # Draft 2D object (typed FeaturePython)
  Area = 2.3843e+07
  ChamferSize = 0
  Closed = true
  End = (9212.5,3817.5,0)
  FilletRadius = 0
  Length = 21540
  MakeFace = true
  Placement = pos=(8082.5,3817.5,0) rot=(0,0,1;0rad)
  Points = (10) [(12.5,0,0),(12.5,3070,0),(3885,3070,0),(3885,2500,0),(4467.5,2500,0),(4467.5,-2675,0),(3885,-2675,0),(3885,-3245,0),(1130,-3245,0),(1130,0,0)]
  Start = (8095,3817.5,0)
  Subdivisions = 0
FEATURE [Part::Part2DObjectPython] Wire937  label="Детская №002"  # Draft 2D object (typed FeaturePython)
  Area = 1.23002e+07
  ChamferSize = 0
  Closed = true
  End = (-30,1142.5,0)
  FilletRadius = 0
  Length = 14088
  MakeFace = true
  Placement = pos=(-29.2388,3667.5,0) rot=(0,0,1;0rad)
  Points = (7) [(-0.76123,0,0),(3324.11,0,0),(4206.74,-882.627,0),(4206.74,-3095,0),(582.5,-3095,0),(582.5,-2525,0),(-0.76123,-2525,0)]
  Start = (-30,3667.5,0)
  Subdivisions = 0
FEATURE [Part::FeaturePython] Structure468  label="Ванна 180х091"  # Arch/BIM 172 (typed FeaturePython)
  CloneOf = -> Structure343
  FaceMaker = 0
  Height = 600
  HorizontalArea = 1.674e+06
  IfcData = attributes={"GlobalId": {"name": "GlobalId", "type": "IfcGloballyUniqueId", "is_enum": false, "enum_values": []}, "Description": {"... (+484 chars omitted),+1 more (map truncated)
  IfcType = 172
  Length = 0
  Material = -> Material013
  MoveBase = false
  MoveWithHost = false
  Nodes = (2) [(6320,6585,0),(6320,6585,600)]
  NodesOffset = 0
  Normal = (0,0,0)
  PerimeterLength = 4240.95
  Placement = pos=(-112.5,-605,3130) rot=(0,0,1;0rad)
  PredefinedType = 0
  VerticalArea = 5073000
  Width = 100
FEATURE [Part::FeaturePython] Structure469  label="Раковина 81х45 Hatria Area002"  # Arch/BIM 172 (typed FeaturePython)
  CloneOf = -> Structure347
  FaceMaker = 0
  Height = 150
  HorizontalArea = 0
  IfcData = attributes={"GlobalId": {"name": "GlobalId", "type": "IfcGloballyUniqueId", "is_enum": false, "enum_values": []}, "Description": {"... (+484 chars omitted),+1 more (map truncated)
  IfcType = 172
  Length = 0
  Material = -> Material013
  MoveBase = false
  MoveWithHost = false
  Nodes = (2) [(6425,5369.88,0),(6425,5369.88,150)]
  NodesOffset = 0
  Normal = (0,0,0)
  PerimeterLength = 0
  Placement = pos=(9925,-830,3980) rot=(0,0,1;1.5708rad)
  PredefinedType = 0
  VerticalArea = 0
  Width = 100
FEATURE [Part::FeaturePython] Component163  label="унитаз с инсталляцией 004"  # Arch/BIM 0 (typed FeaturePython)
  CloneOf = -> Component030
  HorizontalArea = 0
  IfcData = attributes={"GlobalId": {"name": "GlobalId", "type": "IfcGloballyUniqueId", "is_enum": false, "enum_values": []}, "Description": {"... (+538 chars omitted),+1 more (map truncated)
  IfcType = 0
  Material = -> Material013
  MoveBase = false
  MoveWithHost = false
  PerimeterLength = 0
  Placement = pos=(9247.32,16427.9,3130) rot=(0,0,1;3.92699rad)
  PredefinedType = 0
  VerticalArea = 0
FEATURE [Part::FeaturePython] Wall398  label="Облицовка ванны плиткой 30мм001"  # Arch/BIM 166 (typed FeaturePython)
  Align = 2
  Area = 3112200
  BlockHeight = 0
  BlockLength = 0
  CloneOf = -> Wall240
  CountBroken = 0
  CountEntire = 0
  Face = 0
  Height = 570
  HorizontalArea = 263000
  IfcData = attributes={"GlobalId": {"name": "GlobalId", "type": "IfcGloballyUniqueId", "is_enum": false, "enum_values": []}, "Description": {"... (+533 chars omitted),+1 more (map truncated)
  IfcType = 166
  Joint = 0
  Length = 5460
  MakeBlocks = false
  Material = -> Material005
  MoveBase = false
  MoveWithHost = false
  Normal = (0,0,0)
  OffsetFirst = 0
  OffsetSecond = 0
  PerimeterLength = 5460
  Placement = pos=(-112.5,-605,3130) rot=(0,0,1;0rad)
  PredefinedType = 0
  VerticalArea = 5.9964e+06
  Width = 50
FEATURE [Part::Box] Box3234  label="СМ002"
  AttacherType = Attacher::AttachEngine3D
  Height = 800
  Length = 450
  Placement = pos=(4310,6000,3130) rot=(0,0,1;0rad)
  Width = 600
FEATURE [Part::FeaturePython] Component164  label="СМ003"  # Arch/BIM 52 (typed FeaturePython)
  Base = -> Box3234
  GlobalId = 3p89ErDe9E9Opxcq8_zvGg
  HorizontalArea = 0
  IfcData = IfcUID=3p89ErDe9E9Opxcq8_zvGg,+2 more (map truncated)
  IfcType = 52
  Material = -> Material017
  MoveBase = false
  MoveWithHost = false
  PerimeterLength = 0
  Placement = pos=(4360,6000,3130) rot=(0,0,1;0rad)
  VerticalArea = 0
FEATURE [App::GeometryPython] BuildingPart124  label="Сантехника и мебель в ванной (мансарда)"  # Arch/BIM 172 (typed FeaturePython)
  Area = 3112200
  Group = -> [Structure468,Structure469,Component163,Wall398,Component164]
  Height = 3130
  HeightPropagate = true
  IfcData = attributes={"GlobalId": {"name": "GlobalId", "type": "IfcGloballyUniqueId", "is_enum": false, "enum_values": []}, "Description": {"... (+484 chars omitted),+1 more (map truncated)
  IfcType = 172
  LevelOffset = 0
  Placement = pos=(0,0,3130) rot=(0,0,1;0rad)
  PredefinedType = 0
FEATURE [Part::FeaturePython] Component165  label="кровать 2 спальная 210х170 004"  # Arch/BIM 0 (typed FeaturePython)
  CloneOf = -> Component040
  HorizontalArea = 0
  IfcData = attributes={"GlobalId": {"name": "GlobalId", "type": "IfcGloballyUniqueId", "is_enum": false, "enum_values": []}, "Description": {"... (+538 chars omitted),+1 more (map truncated)
  IfcType = 0
  Material = -> Material015
  MoveBase = false
  MoveWithHost = false
  PerimeterLength = 0
  Placement = pos=(12390.7,1367.73,3130) rot=(0,0,1;3.14159rad)
  PredefinedType = 0
  VerticalArea = 0
FEATURE [Part::FeaturePython] Component166  label="стол письменный002"  # Arch/BIM 0 (typed FeaturePython)
  CloneOf = -> Component042
  HorizontalArea = 0
  IfcData = attributes={"GlobalId": {"name": "GlobalId", "type": "IfcGloballyUniqueId", "is_enum": false, "enum_values": []}, "Description": {"... (+538 chars omitted),+1 more (map truncated)
  IfcType = 0
  Material = -> Material014
  MoveBase = false
  MoveWithHost = false
  PerimeterLength = 0
  Placement = pos=(1140,2147.5,3130) rot=(0,0,1;1.5708rad)
  PredefinedType = 0
  VerticalArea = 0
FEATURE [Part::FeaturePython] Component167  label="стул015"  # Arch/BIM 0 (typed FeaturePython)
  CloneOf = -> Component043
  HorizontalArea = 0
  IfcData = attributes={"GlobalId": {"name": "GlobalId", "type": "IfcGloballyUniqueId", "is_enum": false, "enum_values": []}, "Description": {"... (+538 chars omitted),+1 more (map truncated)
  IfcType = 0
  Material = -> Material014
  MoveBase = false
  MoveWithHost = false
  PerimeterLength = 0
  Placement = pos=(-462.225,3294.69,3130) rot=(0,0,-1;1.5708rad)
  PredefinedType = 0
  VerticalArea = 0
FEATURE [Part::FeaturePython] Component168  label="стол письменный003"  # Arch/BIM 0 (typed FeaturePython)
  CloneOf = -> Component042
  HorizontalArea = 0
  IfcData = attributes={"GlobalId": {"name": "GlobalId", "type": "IfcGloballyUniqueId", "is_enum": false, "enum_values": []}, "Description": {"... (+538 chars omitted),+1 more (map truncated)
  IfcType = 0
  Material = -> Material014
  MoveBase = false
  MoveWithHost = false
  PerimeterLength = 0
  Placement = pos=(1140,3812.5,3130) rot=(0,0,1;1.5708rad)
  PredefinedType = 0
  VerticalArea = 0
FEATURE [Part::FeaturePython] Component169  label="стул016"  # Arch/BIM 0 (typed FeaturePython)
  CloneOf = -> Component043
  HorizontalArea = 0
  IfcData = attributes={"GlobalId": {"name": "GlobalId", "type": "IfcGloballyUniqueId", "is_enum": false, "enum_values": []}, "Description": {"... (+538 chars omitted),+1 more (map truncated)
  IfcType = 0
  Material = -> Material014
  MoveBase = false
  MoveWithHost = false
  PerimeterLength = 0
  Placement = pos=(-462.225,4959.69,3130) rot=(0,0,-1;1.5708rad)
  PredefinedType = 0
  VerticalArea = 0
FEATURE [App::GeometryPython] BuildingPart126  label="Мебель (мансарда)"  # Arch/BIM 172 (typed FeaturePython)
  Area = 0
  Group = -> [Component165,Component166,Component167,Component168,Component169]
  Height = 0
  HeightPropagate = true
  IfcData = attributes={"GlobalId": {"name": "GlobalId", "type": "IfcGloballyUniqueId", "is_enum": false, "enum_values": []}, "Description": {"... (+484 chars omitted),+1 more (map truncated)
  IfcType = 172
  LevelOffset = 0
  PredefinedType = 0
FEATURE [App::GeometryPython] BuildingPart125  label="Обстановка (мансарда)"  # Arch/BIM 172 (typed FeaturePython)
  Area = 3112200
  Group = -> [BuildingPart124,BuildingPart126]
  Height = 0
  HeightPropagate = true
  IfcData = attributes={"GlobalId": {"name": "GlobalId", "type": "IfcGloballyUniqueId", "is_enum": false, "enum_values": []}, "Description": {"... (+484 chars omitted),+1 more (map truncated)
  IfcType = 172
  LevelOffset = 0
  Placement = pos=(0,0,3130) rot=(0,0,1;0rad)
  PredefinedType = 0
FEATURE [App::FeaturePython] Dimension101  # Draft dimension (typed FeaturePython)
  Diameter = false
  Dimline = (5100,5940,0)
  Direction = (0,0,0)
  Distance = 120
  End = (4930,5465,0)
  Normal = (0,0,1)
  Start = (4930,5345,0)
FEATURE [Sketcher::SketchObject] Sketch387
  FullyConstrained = true
  Placement = pos=(3417.99,3544.38,3130) rot=(0.862856,-0.357407,-0.357407;1.71777rad)
  sketch-geometry (8):
    g0: LineSegment StartX=0 StartY=0 StartZ=0 EndX=900 EndY=0 EndZ=0
    g1: LineSegment StartX=900 StartY=0 StartZ=0 EndX=900 EndY=2150 EndZ=0
    g2: LineSegment StartX=900 StartY=2150 StartZ=0 EndX=0 EndY=2150 EndZ=0
    g3: LineSegment StartX=0 StartY=2150 StartZ=0 EndX=0 EndY=0 EndZ=0
    g4: LineSegment StartX=50 StartY=0 StartZ=0 EndX=850 EndY=0 EndZ=0
    g5: LineSegment StartX=850 StartY=0 StartZ=0 EndX=850 EndY=2100 EndZ=0
    g6: LineSegment StartX=850 StartY=2100 StartZ=0 EndX=50 EndY=2100 EndZ=0
    g7: LineSegment StartX=50 StartY=2100 StartZ=0 EndX=50 EndY=0 EndZ=0
  constraints (23):
    c: Coincident(g0,g1)
    c: Coincident(g1,g2)
    c: Coincident(g2,g3)
    c: Coincident(g3,g0)
    c: Horizontal(g0)
    c: Horizontal(g2)
    c: Vertical(g1)
    c: Vertical(g3)
    c: Coincident(g4,g5)
    c: Coincident(g5,g6)
    c: Coincident(g6,g7)
    c: Coincident(g7,g4)
    c: Horizontal(g4)
    c: Horizontal(g6)
    c: Vertical(g5)
    c: Vertical(g7)
    c: DistanceY(g1) = 2150  'Height'
    c: DistanceX(g0) = 900  'Width'
    c: DistanceY(g6,g2) = 50  'Frame1'
    c: DistanceX(g2,g6) = 50  'Frame2'
    c: DistanceX(g4,g0) = 50  'Frame3'
    c: DistanceY(g0,g4) = 0
    c: Coincident(g0,g-1)
FEATURE [Part::FeaturePython] Window083  label="Д90-манс-001"  # Arch/BIM 41 (typed FeaturePython)
  Area = 1935000
  Base = -> Sketch387
  Frame = 50
  Height = 2150
  HoleDepth = 0
  HoleWire = 0
  HorizontalArea = 0
  IfcData = attributes={"GlobalId": {"name": "GlobalId", "type": "IfcGloballyUniqueId", "is_enum": false, "enum_values": []}, "Description": {"... (+1934 chars omitted),+1 more (map truncated)
  IfcType = 41
  LouvreSpacing = 0
  LouvreWidth = 0
  Material = -> Material011
  MoveBase = false
  MoveWithHost = true
  Normal = (0.707107,0.707107,1e-16)
  Opening = 0
  OperationType = 1
  OverallHeight = 2150
  OverallWidth = 900
  PerimeterLength = 0
  PredefinedType = 0
  Preset = 6
  SymbolElevation = false
  SymbolPlan = false
  VerticalArea = 0
  Width = 900
  WindowParts = OuterFrame | Frame | Wire0,Wire1 | 75.0+V | 0.00+V | Door | Solid panel | Wire1,Edge8,Mode2 | 50.0 | 0.0+V
  expr: OverallWidth = .Width.Value
  expr: OverallHeight = .Height.Value
FEATURE [Sketcher::SketchObject] Sketch388
  FullyConstrained = true
  Placement = pos=(4054.38,4552.01,3130) rot=(-0.281085,0.678598,0.678598;3.68962rad)
  sketch-geometry (8):
    g0: LineSegment StartX=0 StartY=0 StartZ=0 EndX=900 EndY=0 EndZ=0
    g1: LineSegment StartX=900 StartY=0 StartZ=0 EndX=900 EndY=2150 EndZ=0
    g2: LineSegment StartX=900 StartY=2150 StartZ=0 EndX=0 EndY=2150 EndZ=0
    g3: LineSegment StartX=0 StartY=2150 StartZ=0 EndX=0 EndY=0 EndZ=0
    g4: LineSegment StartX=50 StartY=0 StartZ=0 EndX=850 EndY=0 EndZ=0
    g5: LineSegment StartX=850 StartY=0 StartZ=0 EndX=850 EndY=2100 EndZ=0
    g6: LineSegment StartX=850 StartY=2100 StartZ=0 EndX=50 EndY=2100 EndZ=0
    g7: LineSegment StartX=50 StartY=2100 StartZ=0 EndX=50 EndY=0 EndZ=0
  constraints (23):
    c: Coincident(g0,g1)
    c: Coincident(g1,g2)
    c: Coincident(g2,g3)
    c: Coincident(g3,g0)
    c: Horizontal(g0)
    c: Horizontal(g2)
    c: Vertical(g1)
    c: Vertical(g3)
    c: Coincident(g4,g5)
    c: Coincident(g5,g6)
    c: Coincident(g6,g7)
    c: Coincident(g7,g4)
    c: Horizontal(g4)
    c: Horizontal(g6)
    c: Vertical(g5)
    c: Vertical(g7)
    c: DistanceY(g1) = 2150  'Height'
    c: DistanceX(g0) = 900  'Width'
    c: DistanceY(g6,g2) = 50  'Frame1'
    c: DistanceX(g2,g6) = 50  'Frame2'
    c: DistanceX(g4,g0) = 50  'Frame3'
    c: DistanceY(g0,g4) = 0
    c: Coincident(g0,g-1)
FEATURE [Part::FeaturePython] Window084  label="Д90-манс-002"  # Arch/BIM 41 (typed FeaturePython)
  Area = 1935000
  Base = -> Sketch388
  Frame = 50
  Height = 2150
  HoleDepth = 0
  HoleWire = 0
  HorizontalArea = 0
  IfcData = attributes={"GlobalId": {"name": "GlobalId", "type": "IfcGloballyUniqueId", "is_enum": false, "enum_values": []}, "Description": {"... (+1933 chars omitted),+1 more (map truncated)
  IfcType = 41
  LouvreSpacing = 0
  LouvreWidth = 0
  Material = -> Material011
  MoveBase = false
  MoveWithHost = true
  Normal = (0.707107,-0.707107,-3e-16)
  Opening = 0
  OperationType = 0
  OverallHeight = 2150
  OverallWidth = 900
  PerimeterLength = 0
  PredefinedType = 0
  Preset = 6
  SymbolElevation = false
  SymbolPlan = false
  VerticalArea = 0
  Width = 900
  WindowParts = OuterFrame | Frame | Wire0,Wire1 | 75.0+V | 0.00+V | Door | Solid panel | Wire1,Edge8,Mode2 | 50.0 | 0.0+V
  expr: OverallWidth = .Width.Value
  expr: OverallHeight = .Height.Value
FEATURE [Sketcher::SketchObject] Sketch389
  FullyConstrained = true
  Placement = pos=(9087.5,3400,3130) rot=(0.57735,-0.57735,-0.57735;2.0944rad)
  sketch-geometry (8):
    g0: LineSegment StartX=0 StartY=0 StartZ=0 EndX=900 EndY=0 EndZ=0
    g1: LineSegment StartX=900 StartY=0 StartZ=0 EndX=900 EndY=2150 EndZ=0
    g2: LineSegment StartX=900 StartY=2150 StartZ=0 EndX=0 EndY=2150 EndZ=0
    g3: LineSegment StartX=0 StartY=2150 StartZ=0 EndX=0 EndY=0 EndZ=0
    g4: LineSegment StartX=50 StartY=0 StartZ=0 EndX=850 EndY=0 EndZ=0
    g5: LineSegment StartX=850 StartY=0 StartZ=0 EndX=850 EndY=2100 EndZ=0
    g6: LineSegment StartX=850 StartY=2100 StartZ=0 EndX=50 EndY=2100 EndZ=0
    g7: LineSegment StartX=50 StartY=2100 StartZ=0 EndX=50 EndY=0 EndZ=0
  constraints (23):
    c: Coincident(g0,g1)
    c: Coincident(g1,g2)
    c: Coincident(g2,g3)
    c: Coincident(g3,g0)
    c: Horizontal(g0)
    c: Horizontal(g2)
    c: Vertical(g1)
    c: Vertical(g3)
    c: Coincident(g4,g5)
    c: Coincident(g5,g6)
    c: Coincident(g6,g7)
    c: Coincident(g7,g4)
    c: Horizontal(g4)
    c: Horizontal(g6)
    c: Vertical(g5)
    c: Vertical(g7)
    c: DistanceY(g1) = 2150  'Height'
    c: DistanceX(g0) = 900  'Width'
    c: DistanceY(g6,g2) = 50  'Frame1'
    c: DistanceX(g2,g6) = 50  'Frame2'
    c: DistanceX(g4,g0) = 50  'Frame3'
    c: DistanceY(g0,g4) = 0
    c: Coincident(g0,g-1)
FEATURE [Part::FeaturePython] Window085  label="Д90-манс-003"  # Arch/BIM 41 (typed FeaturePython)
  Area = 1935000
  Base = -> Sketch389
  Frame = 50
  Height = 2150
  HoleDepth = 0
  HoleWire = 0
  HorizontalArea = 0
  IfcData = attributes={"GlobalId": {"name": "GlobalId", "type": "IfcGloballyUniqueId", "is_enum": false, "enum_values": []}, "Description": {"... (+1933 chars omitted),+1 more (map truncated)
  IfcType = 41
  LouvreSpacing = 0
  LouvreWidth = 0
  Material = -> Material011
  MoveBase = false
  MoveWithHost = true
  Normal = (1,0,0)
  Opening = 0
  OperationType = 0
  OverallHeight = 2150
  OverallWidth = 900
  PerimeterLength = 0
  PredefinedType = 0
  Preset = 6
  SymbolElevation = false
  SymbolPlan = false
  VerticalArea = 0
  Width = 900
  WindowParts = OuterFrame | Frame | Wire0,Wire1 | 75.0+V | 0.00+V | Door | Solid panel | Wire1,Edge8,Mode2 | 50.0 | 0.0+V
  expr: OverallWidth = .Width.Value
  expr: OverallHeight = .Height.Value
FEATURE [Sketcher::SketchObject] Sketch390
  FullyConstrained = true
  Placement = pos=(6550,3825,3130) rot=(0,0.707107,0.707107;3.14159rad)
  sketch-geometry (8):
    g0: LineSegment StartX=0 StartY=0 StartZ=0 EndX=900 EndY=0 EndZ=0
    g1: LineSegment StartX=900 StartY=0 StartZ=0 EndX=900 EndY=2150 EndZ=0
    g2: LineSegment StartX=900 StartY=2150 StartZ=0 EndX=0 EndY=2150 EndZ=0
    g3: LineSegment StartX=0 StartY=2150 StartZ=0 EndX=0 EndY=0 EndZ=0
    g4: LineSegment StartX=50 StartY=0 StartZ=0 EndX=850 EndY=0 EndZ=0
    g5: LineSegment StartX=850 StartY=0 StartZ=0 EndX=850 EndY=2100 EndZ=0
    g6: LineSegment StartX=850 StartY=2100 StartZ=0 EndX=50 EndY=2100 EndZ=0
    g7: LineSegment StartX=50 StartY=2100 StartZ=0 EndX=50 EndY=0 EndZ=0
  constraints (23):
    c: Coincident(g0,g1)
    c: Coincident(g1,g2)
    c: Coincident(g2,g3)
    c: Coincident(g3,g0)
    c: Horizontal(g0)
    c: Horizontal(g2)
    c: Vertical(g1)
    c: Vertical(g3)
    c: Coincident(g4,g5)
    c: Coincident(g5,g6)
    c: Coincident(g6,g7)
    c: Coincident(g7,g4)
    c: Horizontal(g4)
    c: Horizontal(g6)
    c: Vertical(g5)
    c: Vertical(g7)
    c: DistanceY(g1) = 2150  'Height'
    c: DistanceX(g0) = 900  'Width'
    c: DistanceY(g6,g2) = 50  'Frame1'
    c: DistanceX(g2,g6) = 50  'Frame2'
    c: DistanceX(g4,g0) = 50  'Frame3'
    c: DistanceY(g0,g4) = 0
    c: Coincident(g0,g-1)
FEATURE [Part::FeaturePython] Window086  label="Д90-манс-004"  # Arch/BIM 41 (typed FeaturePython)
  Area = 1935000
  Base = -> Sketch390
  Frame = 50
  Height = 2150
  HoleDepth = 0
  HoleWire = 0
  HorizontalArea = 0
  IfcData = attributes={"GlobalId": {"name": "GlobalId", "type": "IfcGloballyUniqueId", "is_enum": false, "enum_values": []}, "Description": {"... (+1933 chars omitted),+1 more (map truncated)
  IfcType = 41
  LouvreSpacing = 0
  LouvreWidth = 0
  Material = -> Material011
  MoveBase = false
  MoveWithHost = true
  Normal = (-9e-16,-1,2e-16)
  Opening = 0
  OperationType = 0
  OverallHeight = 2150
  OverallWidth = 900
  PerimeterLength = 0
  PredefinedType = 0
  Preset = 6
  SymbolElevation = false
  SymbolPlan = false
  VerticalArea = 0
  Width = 900
  WindowParts = OuterFrame | Frame | Wire0,Wire1 | 132.5+V | 0.00+V | Door | Solid panel | Wire1,Edge8,Mode2 | 50.0 | 0.0+V
  expr: OverallWidth = .Width.Value
  expr: OverallHeight = .Height.Value
FEATURE [Sketcher::SketchObject] Sketch392
  FullyConstrained = true
  Placement = pos=(6860,3582.5,3130) rot=(1,0,0;1.5708rad)
  sketch-geometry (8):
    g0: LineSegment StartX=0 StartY=0 StartZ=0 EndX=1100 EndY=0 EndZ=0
    g1: LineSegment StartX=1100 StartY=0 StartZ=0 EndX=1100 EndY=2150 EndZ=0
    g2: LineSegment StartX=1100 StartY=2150 StartZ=0 EndX=0 EndY=2150 EndZ=0
    g3: LineSegment StartX=0 StartY=2150 StartZ=0 EndX=0 EndY=0 EndZ=0
    g4: LineSegment StartX=500 StartY=500 StartZ=0 EndX=600 EndY=500 EndZ=0
    g5: LineSegment StartX=600 StartY=500 StartZ=0 EndX=600 EndY=1650 EndZ=0
    g6: LineSegment StartX=600 StartY=1650 StartZ=0 EndX=500 EndY=1650 EndZ=0
    g7: LineSegment StartX=500 StartY=1650 StartZ=0 EndX=500 EndY=500 EndZ=0
  constraints (23):
    c: Coincident(g0,g1)
    c: Coincident(g1,g2)
    c: Coincident(g2,g3)
    c: Coincident(g3,g0)
    c: Horizontal(g0)
    c: Horizontal(g2)
    c: Vertical(g1)
    c: Vertical(g3)
    c: Coincident(g4,g5)
    c: Coincident(g5,g6)
    c: Coincident(g6,g7)
    c: Coincident(g7,g4)
    c: Horizontal(g4)
    c: Horizontal(g6)
    c: Vertical(g5)
    c: Vertical(g7)
    c: DistanceY(g1) = 2150  'Height'
    c: DistanceX(g0) = 1100  'Width'
    c: DistanceY(g6,g2) = 500  'Frame1'
    c: DistanceX(g2,g6) = 500  'Frame2'
    c: DistanceX(g4,g0) = 500  'Frame3'
    c: DistanceY(g0,g4) = 500  'Frame4'
    c: Coincident(g0,g-1)
FEATURE [Part::FeaturePython] Window087  label="Д110-манс-сдвижная-001"  # Arch/BIM 170 (typed FeaturePython)
  Area = 2365000
  Base = -> Sketch392
  Frame = 0
  Height = 2150
  HoleDepth = 0
  HoleWire = 0
  HorizontalArea = 0
  IfcData = attributes={"GlobalId": {"name": "GlobalId", "type": "IfcGloballyUniqueId", "is_enum": false, "enum_values": []}, "Description": {"... (+1231 chars omitted),+1 more (map truncated)
  IfcType = 170
  LouvreSpacing = 0
  LouvreWidth = 0
  Material = -> Material011
  MoveBase = false
  MoveWithHost = true
  Normal = (3e-16,1,-2e-16)
  Opening = 0
  OverallHeight = 2150
  OverallWidth = 1100
  PartitioningType = 0
  PerimeterLength = 0
  PredefinedType = 0
  Preset = 1
  SymbolElevation = false
  SymbolPlan = false
  VerticalArea = 0
  Width = 1100
  WindowParts = OuterFrame | Frame | Wire0,Wire1 | 50.0+V | 0.00+V | Glass | Glass panel | Wire1 | 5.0 | 25.0+V
  expr: OverallWidth = .Width.Value
  expr: OverallHeight = .Height.Value
FEATURE [App::GeometryPython] BuildingPart  label="Окна и двери (мансарда)"  # Arch/BIM 52 (typed FeaturePython)
  Area = 17722000
  GlobalId = 2ZdcXw_FbERwG8YjxnAt$R
  Group = -> [Window066,Window067,Window063,Window062,Window061,Window059,Window057,Window083,Window084,Window085,Window086,Window087]
  Height = 0
  HeightPropagate = true
  IfcData = IfcUID=2ZdcXw_FbERwG8YjxnAt$R,+2 more (map truncated)
  IfcType = 52
  LevelOffset = 0
FEATURE [Part::Part2DObjectPython] Rectangle3414  # Draft 2D object (typed FeaturePython)
  Area = 0
  ChamferSize = 0
  Columns = 1
  FilletRadius = 0
  Height = 75
  Length = 2370.76
  MakeFace = false
  Placement = pos=(6717.5,3492.5,0) rot=(0,0,1;0rad)
  Rows = 1
FEATURE [Part::Part2DObjectPython] Rectangle3415  # Draft 2D object (typed FeaturePython)
  Area = 0
  ChamferSize = 0
  Columns = 1
  FilletRadius = 0
  Height = 75
  Length = 150
  MakeFace = false
  Placement = pos=(6700,3567.5,0) rot=(0,0,1;0rad)
  Rows = 1
FEATURE [Part::FeaturePython] Wall399  label="отделка (ГКЛ 12.5 мм) 011"  # Arch/BIM 166 (typed FeaturePython)
  Align = 1
  Area = 1.33049e+07
  Base = -> Rectangle3414
  BlockHeight = 0
  BlockLength = 0
  CountBroken = 0
  CountEntire = 0
  Face = 0
  Height = 2720
  HorizontalArea = 60519
  IfcData = attributes={"GlobalId": {"name": "GlobalId", "type": "IfcGloballyUniqueId", "is_enum": false, "enum_values": []}, "Description": {"... (+533 chars omitted),+1 more (map truncated)
  IfcType = 166
  Joint = 0
  Length = 4891.52
  MakeBlocks = false
  Material = -> Material008
  MoveBase = false
  MoveWithHost = false
  Normal = (0,0,0)
  OffsetFirst = 0
  OffsetSecond = 0
  PerimeterLength = 4891.52
  Placement = pos=(0,0,3130) rot=(0,0,1;0rad)
  PredefinedType = 0
  Subtractions = -> [Structure464]
  VerticalArea = 1.78749e+07
  Width = 12.5
FEATURE [Part::FeaturePython] Wall400  label="отделка (ГКЛ 12.5 мм) 012"  # Arch/BIM 166 (typed FeaturePython)
  Align = 1
  Area = 1224000
  Base = -> Rectangle3415
  BlockHeight = 0
  BlockLength = 0
  CountBroken = 0
  CountEntire = 0
  Face = 0
  Height = 2720
  HorizontalArea = 5000
  IfcData = attributes={"GlobalId": {"name": "GlobalId", "type": "IfcGloballyUniqueId", "is_enum": false, "enum_values": []}, "Description": {"... (+533 chars omitted),+1 more (map truncated)
  IfcType = 166
  Joint = 0
  Length = 450
  MakeBlocks = false
  Material = -> Material008
  MoveBase = false
  MoveWithHost = false
  Normal = (0,0,0)
  OffsetFirst = 0
  OffsetSecond = 0
  PerimeterLength = 450
  Placement = pos=(0,0,3130) rot=(0,0,1;0rad)
  PredefinedType = 0
  VerticalArea = 2176000
  Width = 12.5
FEATURE [App::GeometryPython] BuildingPart123  label="Отделка мансарды"  # Arch/BIM 172 (typed FeaturePython)
  Area = 1.45289e+07
  Group = -> [Component157,Component158,Component159,Component160,Component161,Component162,Wall399,Wall400]
  Height = 2720
  HeightPropagate = true
  IfcData = attributes={"GlobalId": {"name": "GlobalId", "type": "IfcGloballyUniqueId", "is_enum": false, "enum_values": []}, "Description": {"... (+484 chars omitted),+1 more (map truncated)
  IfcType = 172
  LevelOffset = 0
  Placement = pos=(0,0,3130) rot=(0,0,1;0rad)
  PredefinedType = 0
FEATURE [App::GeometryPython] BuildingPart104  label="Уровень  мансарды"  # Arch/BIM 14 (typed FeaturePython)
  Area = 3.91817e+08
  CompositionType = 0
  Elevation = 3130
  GlobalId = 2Sd2b8p9H2Ff7iaZY3OzqZ
  Group = -> [BuildingPart016,BuildingPart083,BuildingPart,BuildingPart113,BuildingPart123,BuildingPart125]
  Height = 3130
  HeightPropagate = true
  IfcData = IfcUID=2Sd2b8p9H2Ff7iaZY3OzqZ,+2 more (map truncated)
  IfcType = 14
  LevelOffset = 0
  LongName = Floor
  Placement = pos=(-560,-540,3130) rot=(0,0,1;0rad)
  expr: Elevation = .Placement.Base.z
FEATURE [App::FeaturePython] Section007  label="Section 2nd floor plan"  # WARN: FeaturePython — macro-defined, semantics opaque (R4)
  Clip = false
  Objects = -> [BuildingPart104,BuildingPart093,BuildingPart087,BuildingPart106]
  OnlySolids = true
  Placement = pos=(6260,3730,4300) rot=(0,0,1;0rad)
  UseMaterialColorForFill = true
FEATURE [TechDraw::DrawViewArch] ArchView008
  AllOn = true
  CutLineWidth = 0.1
  FillSpaces = false
  FontSize = 12
  JoinArch = false
  LineWidth = 0.1
  LockPosition = true
  RenderMode = 0
  Rotation = 0
  Scale = 0.02
  ScaleType = 2
  ShowFill = true
  ShowHidden = true
  Source = -> Section007
  Symbol = <blob: 127876 chars omitted>
  X = 210
  Y = 150
FEATURE [TechDraw::DrawPage] Page003  label="План мансарда"
  KeepUpdated = false
  NextBalloonIndex = 1
  ProjectionType = 0
  Template = -> Template003
  Views = -> [ArchView008,Annotation031]
FEATURE [Part::Part2DObjectPython] Wire939  label="Холл"  # Draft 2D object (typed FeaturePython)
  Area = 1.50561e+07
  ChamferSize = 0
  Closed = true
  End = (9088.26,572.5,0)
  FilletRadius = 0
  Length = 18506.3
  MakeFace = true
  Placement = pos=(4302.5,572.5,0) rot=(0,0,1;0rad)
  Points = (15) [(0,0,0),(0,2264.15,0),(-819.239,3083.39,0),(-819.239,3231.61,0),(-108.084,3942.77,0),(-16.9165,3942.77,0),(855.85,3070,0),(2415,3070,0),(2415,2920,0),+6 more]
  Start = (4302.5,572.5,0)
  Subdivisions = 0
FEATURE [Part::Part2DObjectPython] Rectangle3416  # Draft 2D object (typed FeaturePython)
  Area = 0
  ChamferSize = 0
  Columns = 1
  FilletRadius = 0
  Height = 75
  Length = 2362.5
  MakeFace = false
  Placement = pos=(6850,3567.5,0) rot=(0,0,1;0rad)
  Rows = 1
FEATURE [Part::Part2DObjectPython] Line  # Draft 2D object (typed FeaturePython)
  Area = 0
  ChamferSize = 0
  Closed = false
  End = (4930,5325,0)
  FilletRadius = 0
  Length = 2020
  MakeFace = true
  Placement = pos=(6950,5325,0) rot=(0,0,1;0rad)
  Points = (2) [(0,0,0),(-2020,0,0)]
  Start = (6950,5325,0)
  Subdivisions = 0
FEATURE [Part::Part2DObjectPython] Line1739  # Draft 2D object (typed FeaturePython)
  Area = 0
  ChamferSize = 0
  Closed = false
  End = (4930,5435,0)
  FilletRadius = 0
  Length = 2010
  MakeFace = true
  Placement = pos=(6940,5435,0) rot=(0,0,1;0rad)
  Points = (2) [(0,0,0),(-2010,0,0)]
  Start = (6940,5435,0)
  Subdivisions = 0
FEATURE [Part::Part2DObjectPython] Rectangle3417  # Draft 2D object (typed FeaturePython)
  Area = 1520000
  ChamferSize = 0
  Columns = 1
  FilletRadius = 0
  Height = 800
  Length = 1900
  MakeFace = true
  Placement = pos=(4930,5435,0) rot=(0,0,1;0rad)
  Rows = 1
FEATURE [Part::Part2DObjectPython] Rectangle3419  # Draft 2D object (typed FeaturePython)
  Area = 0
  ChamferSize = 0
  Columns = 1
  FilletRadius = 0
  Height = 3660
  Length = 1900
  MakeFace = false
  Placement = pos=(4930,3825,0) rot=(0,0,1;0rad)
  Rows = 1
FEATURE [Part::Part2DObjectPython] Rectangle3420  # Draft 2D object (typed FeaturePython)
  Area = 270000
  ChamferSize = 0
  Columns = 1
  FilletRadius = 0
  Height = 600
  Length = 450
  MakeFace = true
  Placement = pos=(6380,6885,0) rot=(0,0,1;0rad)
  Rows = 1
FEATURE [Part::Part2DObjectPython] Line1740  # Draft 2D object (typed FeaturePython)
  Area = 0
  ChamferSize = 0
  Closed = false
  End = (6380,7485,0)
  FilletRadius = 0
  Length = 1800
  MakeFace = true
  Placement = pos=(6380,5685,0) rot=(0,0,1;0rad)
  Points = (2) [(0,0,0),(0,1800,0)]
  Start = (6380,5685,0)
  Subdivisions = 0
FEATURE [Part::Part2DObjectPython] Rectangle3425  label="проём инсталляции унитаза"  # Draft 2D object (typed FeaturePython)
  Area = 102000
  ChamferSize = 0
  Columns = 1
  FilletRadius = 0
  Height = 340
  Length = 300
  MakeFace = true
  Placement = pos=(5220,5345,0) rot=(0,0,1;0rad)
  Rows = 1
FEATURE [Part::Part2DObjectPython] Rectangle3427  label="Унитаз Geberit Smyle 54х35 006"  # Draft 2D object (typed FeaturePython)
  ChamferSize = 0
  Columns = 1
  FilletRadius = 0
  Height = 350
  Length = 400
  MakeFace = true
  Placement = pos=(5545,5685,0) rot=(0,0,1;1.5708rad)
  Rows = 1
FEATURE [Part::Part2DObjectPython] Rectangle3428  label="Унитаз Geberit Smyle 54х35 007"  # Draft 2D object (typed FeaturePython)
  ChamferSize = 0
  Columns = 1
  FilletRadius = 0
  Height = 350
  Length = 400
  MakeFace = true
  Placement = pos=(5545,4945,0) rot=(0,0,1;1.5708rad)
  Rows = 1
FEATURE [Part::Part2DObjectPython] Circle144  label="Circle145"  # Draft 2D object (typed FeaturePython)
  Area = 0
  FirstAngle = 0
  LastAngle = 0
  MakeFace = false
  Placement = pos=(6136.58,4505.64,0) rot=(0,0,1;0rad)
  Radius = 650
FEATURE [App::DocumentObjectGroup] Draft_Construction  label="Construction"
  Group = -> [Rectangle3159,Line1465,Rectangle3284,Line1478,Line1480,Wire869,Wire871,Wire872,Wire873,Wire874,Wire875,Wire876,Wire877,Wire878,Wire879,Line1626,Wire914,Wire915,Rectangle3261,Rectangle3249,Rectangle3250,Rectangle3262,Rectangle3247,Rectangle3258,Rectangle3259,Rectangle3239,Line1452,Rectangle3255,Rectangle3257,Rectangle3236,Rectangle3233,Rectangle3232,Rectangle3252,Line,Line1739,Rectangle3417,+4 more]
FEATURE [Part::Part2DObjectPython] Wire942  label="Ванная"  # Draft 2D object (typed FeaturePython)
  Area = 3633400
  ChamferSize = 0
  Closed = true
  End = (4930,5465,0)
  FilletRadius = 0
  Length = 7840
  MakeFace = true
  Placement = pos=(4930,7485,0) rot=(0,0,1;0rad)
  Points = (6) [(0,0,0),(1900,0,0),(1900,-1800,0),(970,-1800,0),(970,-2020,0),(0,-2020,0)]
  Start = (4930,7485,0)
  Subdivisions = 0
FEATURE [Part::Part2DObjectPython] Rectangle3429  # Draft 2D object (typed FeaturePython)
  Area = 0
  ChamferSize = 0
  Columns = 1
  FilletRadius = 0
  Height = 600
  Length = 4817.5
  MakeFace = false
  Placement = pos=(12550,1500,0) rot=(0,0,1;1.5708rad)
  Rows = 1
FEATURE [Part::Part2DObjectPython] Line1743  # Draft 2D object (typed FeaturePython)
  Area = 0
  ChamferSize = 0
  Closed = false
  End = (9212.5,1500,0)
  FilletRadius = 0
  Length = 2755
  MakeFace = false
  Placement = pos=(11967.5,1500,0) rot=(0,0,1;0rad)
  Points = (2) [(0,0,0),(-2755,0,0)]
  Start = (11967.5,1500,0)
  Subdivisions = 0
FEATURE [Part::Part2DObjectPython] Rectangle3430  # Draft 2D object (typed FeaturePython)
  Area = 405000
  ChamferSize = 0
  Columns = 1
  FilletRadius = 0
  Height = 450
  Length = 900
  MakeFace = true
  Placement = pos=(2657.9,587.95,0) rot=(0,0,1;0rad)
  Rows = 1
FEATURE [Part::Part2DObjectPython] Rectangle3431  # Draft 2D object (typed FeaturePython)
  Area = 1080000
  ChamferSize = 0
  Columns = 1
  FilletRadius = 0
  Height = 1800
  Length = 600
  MakeFace = true
  Placement = pos=(3578.66,587.95,0) rot=(0,0,1;0rad)
  Rows = 1
FEATURE [Part::Part2DObjectPython] Rectangle3432  # Draft 2D object (typed FeaturePython)
  Area = 1080000
  ChamferSize = 0
  Columns = 1
  FilletRadius = 0
  Height = 1800
  Length = 600
  MakeFace = true
  Placement = pos=(3577.5,5087.5,0) rot=(0,0,1;0rad)
  Rows = 1
FEATURE [Part::Part2DObjectPython] Rectangle3433  # Draft 2D object (typed FeaturePython)
  Area = 405000
  ChamferSize = 0
  Columns = 1
  FilletRadius = 0
  Height = 450
  Length = 900
  MakeFace = true
  Placement = pos=(2657.5,6437.5,0) rot=(0,0,1;0rad)
  Rows = 1
FEATURE [Part::Part2DObjectPython] Rectangle3434  # Draft 2D object (typed FeaturePython)
  Area = 315700
  ChamferSize = 0
  Columns = 1
  FilletRadius = 0
  Height = 770
  Length = 410
  MakeFace = true
  Placement = pos=(8677.5,572.5,0) rot=(0,0,1;0rad)
  Rows = 1
FEATURE [Part::Part2DObjectPython] Rectangle3435  label="TV 43" 001"  # Draft 2D object (typed FeaturePython)
  ChamferSize = 0
  Columns = 1
  FilletRadius = 0
  Height = 950
  Length = 75
  MakeFace = false
  Placement = pos=(8647.5,2345,0) rot=(0,0,1;3.14159rad)
  Rows = 1
FEATURE [Part::Part2DObjectPython] Rectangle3436  # Draft 2D object (typed FeaturePython)
  Area = 2.55526e+06
  ChamferSize = 0
  Columns = 1
  FilletRadius = 0
  Height = 927.5
  Length = 2755
  MakeFace = true
  Placement = pos=(9212.5,572.5,0) rot=(0,0,1;0rad)
  Rows = 1
FEATURE [Part::Part2DObjectPython] Rectangle3437  # Draft 2D object (typed FeaturePython)
  Area = 0
  ChamferSize = 0
  Columns = 1
  FilletRadius = 0
  Height = 450
  Length = 400
  MakeFace = false
  Placement = pos=(11030.9,6414.46,0) rot=(0,0,1;0rad)
  Rows = 1
FEATURE [Part::Part2DObjectPython] Rectangle3438  # Draft 2D object (typed FeaturePython)
  Area = 0
  ChamferSize = 0
  Columns = 1
  FilletRadius = 0
  Height = 450
  Length = 400
  MakeFace = false
  Placement = pos=(8775.2,6416.88,0) rot=(0,0,1;0rad)
  Rows = 1
FEATURE [App::DocumentObjectGroup] Group126  label="План мансарда 94.1 м2"
  Group = -> [Rectangle2788,Wire819,Rectangle2597,Rectangle3220,Line1442,Rectangle3225,Rectangle3223,Rectangle3224,Rectangle3222,Array063,Rectangle3278,Rectangle3228,Rectangle3229,Rectangle3240,Rectangle3265,Rectangle3271,Rectangle3272,Rectangle3277,Rectangle3264,Rectangle3266,Rectangle3267,Line1448,Arc124,Line1447,Arc123,Rectangle3273,Arc119,Line1449,Rectangle3274,Rectangle3275,Rectangle3286,Rectangle3287,+40 more]
FEATURE [Part::Part2DObjectPython] Line1744  # Draft 2D object (typed FeaturePython)
  ChamferSize = 0
  Closed = true
  End = (4910,5405,0)
  FilletRadius = 0
  Length = 1090
  MakeFace = false
  Placement = pos=(7305,8915,0) rot=(0,0,-1;1.5708rad)
  Points = (2) [(3510,-1305,0),(3510,-2395,0)]
  Start = (6000,5405,0)
  Subdivisions = 0
FEATURE [Part::Part2DObjectPython] Line1745  # Draft 2D object (typed FeaturePython)
  ChamferSize = 0
  Closed = true
  End = (5960,5665,0)
  FilletRadius = 0
  Length = 220
  MakeFace = false
  Placement = pos=(7455,8895,0) rot=(0,0,-1;1.5708rad)
  Points = (2) [(3450,-1495,0),(3230,-1495,0)]
  Start = (5960,5445,0)
  Subdivisions = 0
FEATURE [Part::Part2DObjectPython] Rectangle3439  label="Кожух инсталляции унитаза"  # Draft 2D object (typed FeaturePython)
  Area = 0
  ChamferSize = 0
  Columns = 1
  FilletRadius = 0
  Height = 220
  Length = 970
  MakeFace = false
  Placement = pos=(4930,5465,0) rot=(0,0,1;0rad)
  Rows = 1
FEATURE [Part::FeaturePython] Structure459  label="кожух инсталляции"  # Arch/BIM 172 (typed FeaturePython)
  Base = -> Rectangle3439
  FaceMaker = 0
  Height = 1200
  HorizontalArea = 213400
  IfcData = attributes={"GlobalId": {"name": "GlobalId", "type": "IfcGloballyUniqueId", "is_enum": false, "enum_values": []}, "Description": {"... (+484 chars omitted),+1 more (map truncated)
  IfcType = 172
  Length = 0
  MoveBase = false
  MoveWithHost = false
  Nodes = (2) [(5370,5435,0),(5370,5435,1150)]
  NodesOffset = 0
  Normal = (0,0,1)
  PerimeterLength = 2380
  PredefinedType = 0
  VerticalArea = 2856000
  Width = 100
FEATURE [Part::FeaturePython] Component170  label="унитаз с инсталляцией 005"  # Arch/BIM 0 (typed FeaturePython)
  CloneOf = -> Component030
  HorizontalArea = 0
  IfcData = attributes={"GlobalId": {"name": "GlobalId", "type": "IfcGloballyUniqueId", "is_enum": false, "enum_values": []}, "Description": {"... (+538 chars omitted),+1 more (map truncated)
  IfcType = 0
  Material = -> Material013
  MoveBase = false
  MoveWithHost = false
  PerimeterLength = 0
  Placement = pos=(-230,17435,0) rot=(0,0,-1;1.5708rad)
  PredefinedType = 0
  VerticalArea = 0
FEATURE [Part::Part2DObjectPython] Wire946  label="Ванная контур"  # Draft 2D object (typed FeaturePython)
  Area = 0
  ChamferSize = 0
  Closed = true
  End = (4930,5465,0)
  FilletRadius = 0
  Length = 7840
  MakeFace = false
  Placement = pos=(4930,7485,0) rot=(0,0,1;0rad)
  Points = (6) [(0,0,0),(1900,0,0),(1900,-1800,0),(970,-1800,0),(970,-2020,0),(0,-2020,0)]
  Start = (4930,7485,0)
  Subdivisions = 0
FEATURE [Part::FeaturePython] Structure470  label="проём инсталляции унитаза 001"  # Arch/BIM 52 (typed FeaturePython)
  Base = -> Rectangle3425
  FaceMaker = 0
  Height = 1200
  HorizontalArea = 102000
  IfcData = complex_attributes={"OwnerHistory": {}, "IsNestedBy": {}, "IsDecomposedBy": {}, "IsDefinedBy": {}, "ObjectPlacement": {}, "Representation":... (+4 chars omitted)
  IfcType = 52
  Length = 0
  MoveBase = false
  MoveWithHost = false
  Nodes = (2) [(10750,4050,0),(10750,4050,2180)]
  NodesOffset = 0
  Normal = (0,0,0)
  PerimeterLength = 1280
  Placement = pos=(0,0,-20) rot=(0,0,1;0rad)
  VerticalArea = 1536000
  Width = 100
FEATURE [App::GeometryPython] BuildingPart001  label="проёмы"  # Arch/BIM 52 (typed FeaturePython)
  Area = 0
  Group = -> [Structure016,Structure017,Structure019,Structure020,Structure021,Structure023,Structure024,Structure026,Structure141,Structure158,Structure285,Structure148,Structure304,Structure306,Structure308,Structure313,Structure315,Structure317,Structure333,Structure350,Structure360,Structure421,Structure422,Structure432,Structure431,Structure430,Structure426,Structure428,Structure461,Structure464,+4 more]
  Height = 0
  HeightPropagate = true
  IfcData = complex_attributes={"OwnerHistory": {}, "IsNestedBy": {}, "IsDecomposedBy": {}, "IsDefinedBy": {}, "ObjectPlacement": {}, "Representation":... (+4 chars omitted)
  IfcType = 52
  LevelOffset = 0
FEATURE [Part::FeaturePython] Wall401  label="перегородка (сил.блок 500х250х80) 007"  # Arch/BIM 166 (typed FeaturePython)
  Align = 2
  Area = 3052000
  Base = -> Line1744
  BlockHeight = 250
  BlockLength = 0
  CountBroken = 0
  CountEntire = 0
  Face = 0
  Height = 2800
  HorizontalArea = 87200
  IfcType = 166
  Joint = 0
  Length = 1090
  MakeBlocks = false
  Material = -> Material009
  MoveBase = false
  MoveWithHost = false
  Normal = (0,0,0)
  OffsetFirst = 300
  OffsetSecond = 50
  PerimeterLength = 2340
  PredefinedType = 0
  Subtractions = -> [Structure470]
  VerticalArea = 6032800
  Width = 80
FEATURE [Part::FeaturePython] Wall402  label="перегородка (сил.блок 500х250х80) 008"  # Arch/BIM 166 (typed FeaturePython)
  Additions = -> [Wall401]
  Align = 2
  Area = 616000
  Base = -> Line1745
  BlockHeight = 250
  BlockLength = 0
  CountBroken = 0
  CountEntire = 0
  Face = 0
  Height = 2800
  HorizontalArea = 104800
  IfcType = 166
  Joint = 0
  Length = 220
  MakeBlocks = false
  Material = -> Material009
  MoveBase = false
  MoveWithHost = false
  Normal = (0,0,0)
  OffsetFirst = 300
  OffsetSecond = 50
  PerimeterLength = 2780
  PredefinedType = 0
  VerticalArea = 7264800
  Width = 80
FEATURE [Part::FeaturePython] Wall230  label="перегородка (сил.блок 500х250х80) 006"  # Arch/BIM 166 (typed FeaturePython)
  Additions = -> [Wall402]
  Align = 2
  Area = 2380000
  Base = -> Line1390
  BlockHeight = 250
  BlockLength = 0
  CountBroken = 0
  CountEntire = 0
  Face = 0
  Height = 2800
  HorizontalArea = 172800
  IfcType = 166
  Joint = 0
  Length = 850
  MakeBlocks = false
  Material = -> Material009
  MoveBase = false
  MoveWithHost = false
  Normal = (0,0,0)
  OffsetFirst = 300
  OffsetSecond = 50
  PerimeterLength = 4480
  PredefinedType = 0
  VerticalArea = 12024800
  Width = 80
FEATURE [App::GeometryPython] BuildingPart005  label="Перегородки"  # Arch/BIM 52 (typed FeaturePython)
  Area = 48852400
  GlobalId = 2hzWGr02f4ewnrclJv7BWz
  Group = -> [Wall015,Wall186,Wall128,Wall223,Wall231,Wall230]
  Height = 0
  HeightPropagate = true
  IfcData = IfcUID=2hzWGr02f4ewnrclJv7BWz,attributes={"GlobalId": {"value": "2hzWGr02f4ewnrclJv7BWz"}},+1 more (map truncated)
  IfcType = 52
  LevelOffset = 0
FEATURE [App::FeaturePython] Dimension102  # Draft dimension (typed FeaturePython)
  Diameter = false
  Dimline = (6500,7200,0)
  Direction = (0,0,0)
  Distance = 1800
  End = (5900,7485,0)
  Normal = (0,0,1)
  Start = (5900,5685,0)
FEATURE [App::FeaturePython] Dimension103  # Draft dimension (typed FeaturePython)
  Diameter = false
  Dimline = (5700,4500,0)
  Direction = (0,0,0)
  Distance = 1520
  End = (5800,5345,0)
  Normal = (0,0,1)
  Start = (5800,3825,0)
FEATURE [App::FeaturePython] Dimension104  # Draft dimension (typed FeaturePython)
  Diameter = false
  Dimline = (6100.76,4950.83,0)
  Direction = (0,0,0)
  Distance = 810
  End = (6830,5565,0)
  Normal = (0,0,1)
  Start = (6020,5565,0)
FEATURE [App::GeometryPython] BuildingPart090  label="Размеры (1 этаж)"  # Arch/BIM 52 (typed FeaturePython)
  Area = 0
  GlobalId = 3_s$oy9jj54xonqTEdRA8q
  Group = -> [Dimension001,Dimension,Dimension002,Dimension003,Dimension004,Dimension009,Dimension007,Dimension006,ShapeString147,ShapeString138,Circle088,Circle089,ShapeString139,Circle090,ShapeString140,Circle091,ShapeString141,Circle092,ShapeString142,Circle093,ShapeString143,Circle094,ShapeString144,Circle095,ShapeString145,Circle097,Line1326,Line1327,Line1328,Line1329,Line1330,ShapeString189,+103 more]
  Height = 0
  HeightPropagate = true
  IfcData = IfcUID=3_s$oy9jj54xonqTEdRA8q,+2 more (map truncated)
  IfcType = 52
  LevelOffset = 0
FEATURE [Sketcher::SketchObject] Sketch393
  FullyConstrained = true
  Placement = pos=(6005,7895,955) rot=(0,0.707107,0.707107;3.14159rad)
  sketch-geometry (24):
    g0: LineSegment StartX=0 StartY=0 StartZ=0 EndX=920 EndY=0 EndZ=0
    g1: LineSegment StartX=920 StartY=0 StartZ=0 EndX=920 EndY=1610 EndZ=0
    g2: LineSegment StartX=920 StartY=1610 StartZ=0 EndX=0 EndY=1610 EndZ=0
    g3: LineSegment StartX=0 StartY=1610 StartZ=0 EndX=0 EndY=0 EndZ=0
    g4: LineSegment StartX=70 StartY=70 StartZ=0 EndX=850 EndY=70 EndZ=0
    g5: LineSegment StartX=850 StartY=70 StartZ=0 EndX=850 EndY=1540 EndZ=0
    g6: LineSegment StartX=850 StartY=1540 StartZ=0 EndX=70 EndY=1540 EndZ=0
    g7: LineSegment StartX=70 StartY=1540 StartZ=0 EndX=70 EndY=70 EndZ=0
    g8: LineSegment StartX=77 StartY=77 StartZ=0 EndX=843 EndY=77 EndZ=0
    g9: LineSegment StartX=843 StartY=77 StartZ=0 EndX=843 EndY=801.5 EndZ=0
    g10: LineSegment StartX=843 StartY=801.5 StartZ=0 EndX=77 EndY=801.5 EndZ=0
    g11: LineSegment StartX=77 StartY=801.5 StartZ=0 EndX=77 EndY=77 EndZ=0
    g12: LineSegment StartX=117 StartY=117 StartZ=0 EndX=803 EndY=117 EndZ=0
    g13: LineSegment StartX=803 StartY=117 StartZ=0 EndX=803 EndY=761.5 EndZ=0
    g14: LineSegment StartX=803 StartY=761.5 StartZ=0 EndX=117 EndY=761.5 EndZ=0
    g15: LineSegment StartX=117 StartY=761.5 StartZ=0 EndX=117 EndY=117 EndZ=0
    g16: LineSegment StartX=77 StartY=808.5 StartZ=0 EndX=843 EndY=808.5 EndZ=0
    g17: LineSegment StartX=843 StartY=808.5 StartZ=0 EndX=843 EndY=1533 EndZ=0
    g18: LineSegment StartX=843 StartY=1533 StartZ=0 EndX=77 EndY=1533 EndZ=0
    g19: LineSegment StartX=77 StartY=1533 StartZ=0 EndX=77 EndY=808.5 EndZ=0
    g20: LineSegment StartX=117 StartY=848.5 StartZ=0 EndX=803 EndY=848.5 EndZ=0
    g21: LineSegment StartX=803 StartY=848.5 StartZ=0 EndX=803 EndY=1493 EndZ=0
    g22: LineSegment StartX=803 StartY=1493 StartZ=0 EndX=117 EndY=1493 EndZ=0
    g23: LineSegment StartX=117 StartY=1493 StartZ=0 EndX=117 EndY=848.5 EndZ=0
  constraints (71):
    c: Coincident(g0,g1)
    c: Coincident(g1,g2)
    c: Coincident(g2,g3)
    c: Coincident(g3,g0)
    c: Horizontal(g0)
    c: Horizontal(g2)
    c: Vertical(g1)
    c: Vertical(g3)
    c: Coincident(g4,g5)
    c: Coincident(g5,g6)
    c: Coincident(g6,g7)
    c: Coincident(g7,g4)
    c: Horizontal(g4)
    c: Horizontal(g6)
    c: Vertical(g5)
    c: Vertical(g7)
    c: DistanceY(g1) = 1610  'Height'
    c: DistanceX(g0) = 920  'Width'
    c: DistanceY(g6,g2) = 70  'Frame1'
    c: DistanceX(g2,g6) = 70  'Frame2'
    c: DistanceX(g4,g0) = 70  'Frame3'
    c: DistanceY(g0,g4) = 70  'Frame4'
    c: Coincident(g0,g-1)
    c: Coincident(g8,g9)
    c: Coincident(g9,g10)
    c: Coincident(g10,g11)
    c: Coincident(g11,g8)
    c: Horizontal(g8)
    c: Horizontal(g10)
    c: Vertical(g9)
    c: Vertical(g11)
    c: Coincident(g12,g13)
    c: Coincident(g13,g14)
    c: Coincident(g14,g15)
    c: Coincident(g15,g12)
    c: Horizontal(g12)
    c: Horizontal(g14)
    c: Vertical(g13)
    c: Vertical(g15)
    c: Coincident(g16,g17)
    c: Coincident(g17,g18)
    c: Coincident(g18,g19)
    c: Coincident(g19,g16)
    c: Horizontal(g16)
    c: Horizontal(g18)
    c: Vertical(g17)
    c: Vertical(g19)
    c: Coincident(g20,g21)
    c: Coincident(g21,g22)
    c: Coincident(g22,g23)
    c: Coincident(g23,g20)
    c: Horizontal(g20)
    c: Horizontal(g22)
    c: Vertical(g21)
    c: Vertical(g23)
    c: DistanceY(g8,g12) = 40
    c: DistanceX(g8,g12) = 40
    c: DistanceX(g21,g17) = 40
    c: DistanceY(g21,g17) = 40
    c: DistanceY(g16,g20) = 40
    c: DistanceY(g10,g14) = -40
    c: Equal(g23,g15)
    c: DistanceX(g12,g20) = 0
    c: DistanceX(g13,g20) = 0
    c: DistanceX(g4,g8) = 7
    c: DistanceY(g4,g8) = 7
    c: DistanceX(g6,g18) = -7
    c: DistanceY(g6,g18) = -7
    c: DistanceY(g10,g16) = 7
    c: PointOnObject(g9,g17)
    c: PointOnObject(g16,g11)
FEATURE [Part::FeaturePython] Window088  label="ОК-92/161-002"  # Arch/BIM 170 (typed FeaturePython)
  Area = 1481200
  Base = -> Sketch393
  Frame = 70
  Height = 1610
  HoleDepth = 0
  HoleWire = 0
  HorizontalArea = 0
  IfcData = attributes={"GlobalId": {"name": "GlobalId", "type": "IfcGloballyUniqueId", "is_enum": false, "enum_values": []}, "Description": {"... (+1230 chars omitted),+1 more (map truncated)
  IfcType = 170
  LouvreSpacing = 0
  LouvreWidth = 0
  Material = -> Material011
  MoveBase = false
  MoveWithHost = true
  Normal = (0,-1,2e-16)
  Opening = 0
  OverallHeight = 1610
  OverallWidth = 920
  PartitioningType = 0
  PerimeterLength = 0
  PredefinedType = 0
  Preset = 4
  SymbolElevation = false
  SymbolPlan = false
  VerticalArea = 0
  Width = 920
  WindowParts = OuterFrame | Frame | Wire0,Wire1 | 35.0+V | 0.00+V | LowerFrame | Frame | Wire2,Wire3 | 35.0 | 35.0+V | LowerGlass | Glass panel | Wire3 | 3.5 | 52.5+V | UpperFrame | Frame | Wire4,Wire5 | 35.0 | 0.0+V | UpperGlass | Glass panel | Wire5 | 3.5 | 17.5+V
  expr: OverallWidth = .Width.Value
  expr: OverallHeight = .Height.Value
FEATURE [App::GeometryPython] BuildingPart011  label="Окна и двери 1этаж"  # Arch/BIM 52 (typed FeaturePython)
  Area = 31952000
  GlobalId = 2lTKOyIXPBJh5VnrrZDJsa
  Group = -> [Window020,Window021,Window026,Window048,Window052,Window068,Window069,Window070,Window071,Window072,Window073,Window074,Window077,Window078,Window088]
  Height = 0
  HeightPropagate = true
  IfcData = IfcUID=2lTKOyIXPBJh5VnrrZDJsa,attributes={"GlobalId": {"value": "2lTKOyIXPBJh5VnrrZDJsa"}},+1 more (map truncated)
  IfcType = 52
  LevelOffset = 0
FEATURE [Part::FeaturePython] Structure471  label="Раковина 81х45 Hatria Area001"  # Arch/BIM 172 (typed FeaturePython)
  CloneOf = -> Structure347
  FaceMaker = 0
  Height = 150
  HorizontalArea = 0
  IfcData = attributes={"GlobalId": {"name": "GlobalId", "type": "IfcGloballyUniqueId", "is_enum": false, "enum_values": []}, "Description": {"... (+484 chars omitted),+1 more (map truncated)
  IfcType = 172
  Length = 0
  Material = -> Material013
  MoveBase = false
  MoveWithHost = false
  Nodes = (2) [(6425,5369.88,0),(6425,5369.88,150)]
  NodesOffset = 0
  Normal = (0,0,0)
  PerimeterLength = 0
  Placement = pos=(-880,2225,850) rot=(0,0,1;0rad)
  PredefinedType = 0
  VerticalArea = 0
  Width = 100
FEATURE [App::GeometryPython] BuildingPart019  label="Ненужное"  # Arch/BIM 52 (typed FeaturePython)
  Area = 53097200
  Group = -> [Structure044,BuildingPart015,BuildingPart035,BuildingPart010,Window,Structure347,Structure471]
  Height = 0
  HeightPropagate = true
  IfcData = complex_attributes={"OwnerHistory": {}, "IsNestedBy": {}, "IsDecomposedBy": {}, "IsDefinedBy": {}, "ObjectPlacement": {}, "Representation":... (+4 chars omitted)
  IfcType = 52
  LevelOffset = 0
FEATURE [Part::Part2DObjectPython] Wire947  # Draft 2D object (typed FeaturePython)
  Area = 0
  ChamferSize = 0
  Closed = true
  End = (6020,5565,0)
  FilletRadius = 0
  Length = 2372.43
  MakeFace = false
  Placement = pos=(6875,5565,0) rot=(0,0,-1;1.5708rad)
  Points = (10) [(6.36646e-12,-45,0),(360,-45,0),(360,-184.29,0),(393.033,-216.967,0),(410,-275,0),(410,-625,0),(393.033,-683.033,0),(360,-715.711,0),(360,-855,0),+1 more]
  Start = (6830,5565,0)
  Subdivisions = 0
FEATURE [Part::Part2DObjectPython] Rectangle3443  # Draft 2D object (typed FeaturePython)
  Area = 0
  ChamferSize = 0
  Columns = 1
  FilletRadius = 75
  Height = 500
  Length = 240
  MakeFace = false
  Placement = pos=(5295,7670,0) rot=(0,0,-1;1.5708rad)
  Rows = 1
FEATURE [Part::Part2DObjectPython] Wire948  # Draft 2D object (typed FeaturePython)
  Area = 0
  ChamferSize = 0
  Closed = true
  End = (5140,7790,0)
  FilletRadius = 0
  Length = 2372.43
  MakeFace = false
  Placement = pos=(5995,7790,0) rot=(0,0,-1;1.5708rad)
  Points = (10) [(6.36646e-12,-45,0),(360,-45,0),(360,-184.29,0),(393.033,-216.967,0),(410,-275,0),(410,-625,0),(393.033,-683.033,0),(360,-715.711,0),(360,-855,0),+1 more]
  Start = (5950,7790,0)
  Subdivisions = 0
FEATURE [Part::Part2DObjectPython] Wire949  label="Кухня-столовая"  # Draft 2D object (typed FeaturePython)
  Area = 2.94281e+07
  ChamferSize = 0
  Closed = true
  End = (12550,-25,0)
  FilletRadius = 0
  Length = 25500
  MakeFace = true
  Placement = pos=(9550,-25,0) rot=(0,0,1;0rad)
  Points = (14) [(0,0,0),(0,2410,0),(-1130,2410,0),(-1130,3850,0),(-1590,3850,0),(-1590,6610.01,0),(-1190,6610.01,0),(-1190,7510,0),(3000,7510,0),(3000,3850,0),+4 more]
  Start = (9550,-25,0)
  Subdivisions = 0
FEATURE [App::FeaturePython] Dimension105  # Draft dimension (typed FeaturePython)
  Diameter = false
  Dimline = (13900,-300,0)
  Direction = (0,0,0)
  Distance = 7510
  End = (12550,7485,0)
  Normal = (0,0,1)
  Start = (12550,-25,0)
FEATURE [App::FeaturePython] Dimension106  # Draft dimension (typed FeaturePython)
  Diameter = false
  Dimline = (13600,-1100,0)
  Direction = (0,0,0)
  Distance = 12580
  End = (12550,-10,0)
  Normal = (0,0,1)
  Start = (-30,-10,0)
FEATURE [App::FeaturePython] Dimension107  # Draft dimension (typed FeaturePython)
  Diameter = false
  Dimline = (14100,-1000,0)
  Direction = (0,0,0)
  Distance = 8570
  End = (13080,8015,0)
  Normal = (0,0,1)
  Start = (13080,-555,0)
FEATURE [App::FeaturePython] Dimension108  # Draft dimension (typed FeaturePython)
  Diameter = false
  Dimline = (-1600,-1000,0)
  Direction = (0,0,0)
  Distance = 3915
  End = (-1836.7,3680,0)
  Normal = (0,0,1)
  Start = (-1836.7,-235,0)
FEATURE [App::FeaturePython] Dimension109  # Draft dimension (typed FeaturePython)
  Diameter = false
  Dimline = (-1600,3680,0)
  Direction = (0,0,0)
  Distance = 4015
  End = (-1836.7,7695,0)
  Normal = (0,0,1)
  Start = (-1836.7,3680,0)
FEATURE [App::FeaturePython] Dimension110  # Draft dimension (typed FeaturePython)
  Diameter = false
  Dimline = (-600,9000,0)
  Direction = (0,0,0)
  Distance = 5110
  End = (4870,9506.46,0)
  Normal = (0,0,1)
  Start = (-240,9506.46,0)
FEATURE [App::FeaturePython] Dimension111  # Draft dimension (typed FeaturePython)
  Diameter = false
  Dimline = (7910,9000,0)
  Direction = (0,0,0)
  Distance = 1020
  End = (7910,9506.46,0)
  Normal = (0,0,1)
  Start = (6890,9506.46,0)
FEATURE [Part::Part2DObjectPython] ShapeString209  # Draft 2D object (typed FeaturePython)
  FontFile = <path>
  Placement = pos=(6306.65,2599.61,0) rot=(0,0,1;0rad)
  Size = 250
  String = 1
  Tracking = 0
FEATURE [Part::Part2DObjectPython] Circle145  label="Circle146"  # Draft 2D object (typed FeaturePython)
  Area = 0
  FirstAngle = 0
  LastAngle = 0
  MakeFace = false
  Placement = pos=(6400,2700,0) rot=(0,0,1;0rad)
  Radius = 200
FEATURE [Part::Part2DObjectPython] Circle146  label="Circle147"  # Draft 2D object (typed FeaturePython)
  Area = 0
  FirstAngle = 0
  LastAngle = 0
  MakeFace = false
  Placement = pos=(10300,4300,0) rot=(0,0,1;0rad)
  Radius = 200
FEATURE [Part::Part2DObjectPython] ShapeString210  # Draft 2D object (typed FeaturePython)
  FontFile = <path>
  Placement = pos=(10206.7,4199.61,0) rot=(0,0,1;0rad)
  Size = 250
  String = 2
  Tracking = 0
FEATURE [Part::Part2DObjectPython] Circle147  label="Circle148"  # Draft 2D object (typed FeaturePython)
  Area = 0
  FirstAngle = 0
  LastAngle = 0
  MakeFace = false
  Placement = pos=(2000,2700,0) rot=(0,0,1;0rad)
  Radius = 200
FEATURE [Part::Part2DObjectPython] ShapeString211  # Draft 2D object (typed FeaturePython)
  FontFile = <path>
  Placement = pos=(1906.65,2599.61,0) rot=(0,0,1;0rad)
  Size = 250
  String = 3
  Tracking = 0
FEATURE [Part::Part2DObjectPython] Circle149  label="Circle150"  # Draft 2D object (typed FeaturePython)
  Area = 0
  FirstAngle = 0
  LastAngle = 0
  MakeFace = false
  Placement = pos=(2000,4800,0) rot=(0,0,1;0rad)
  Radius = 200
FEATURE [Part::Part2DObjectPython] ShapeString213  # Draft 2D object (typed FeaturePython)
  FontFile = <path>
  Placement = pos=(1906.65,4699.61,0) rot=(0,0,1;0rad)
  Size = 250
  String = 4
  Tracking = 0
FEATURE [Part::Part2DObjectPython] Circle150  label="Circle151"  # Draft 2D object (typed FeaturePython)
  Area = 0
  FirstAngle = 0
  LastAngle = 0
  MakeFace = false
  Placement = pos=(5300,4900,0) rot=(0,0,1;0rad)
  Radius = 200
FEATURE [Part::Part2DObjectPython] ShapeString214  # Draft 2D object (typed FeaturePython)
  FontFile = <path>
  Placement = pos=(5206.65,4799.61,0) rot=(0,0,1;0rad)
  Size = 250
  String = 5
  Tracking = 0
FEATURE [Part::Part2DObjectPython] Circle152  label="Circle153"  # Draft 2D object (typed FeaturePython)
  Area = 0
  FirstAngle = 0
  LastAngle = 0
  MakeFace = false
  Placement = pos=(7410.22,4666.38,0) rot=(0,0,1;0rad)
  Radius = 200
FEATURE [Part::Part2DObjectPython] ShapeString216  # Draft 2D object (typed FeaturePython)
  FontFile = <path>
  Placement = pos=(7316.87,4565.99,0) rot=(0,0,1;0rad)
  Size = 250
  String = 6
  Tracking = 0
FEATURE [Part::Part2DObjectPython] Line1746  # Draft 2D object (typed FeaturePython)
  Area = 0
  ChamferSize = 0
  Closed = true
  End = (14600,5100,0)
  FilletRadius = 0
  Length = 1100
  MakeFace = true
  Placement = pos=(14600,6200,0) rot=(0,0,1;0rad)
  Points = (2) [(0,0,0),(0,-1100,0)]
  Start = (14600,6200,0)
  Subdivisions = 0
FEATURE [Part::Part2DObjectPython] Line1747  # Draft 2D object (typed FeaturePython)
  Area = 0
  ChamferSize = 0
  Closed = false
  End = (14600,6200,0)
  FilletRadius = 0
  Length = 282.843
  MakeFace = true
  Placement = pos=(14400,6400,0) rot=(0,0,1;0rad)
  Points = (2) [(0,0,0),(200,-200,0)]
  Start = (14400,6400,0)
  Subdivisions = 0
FEATURE [Part::Part2DObjectPython] Line1748  # Draft 2D object (typed FeaturePython)
  Area = 0
  ChamferSize = 0
  Closed = false
  End = (14800,6400,0)
  FilletRadius = 0
  Length = 282.843
  MakeFace = true
  Placement = pos=(14600,6200,0) rot=(0,0,1;0rad)
  Points = (2) [(0,0,0),(200,200,0)]
  Start = (14600,6200,0)
  Subdivisions = 0
FEATURE [Part::Part2DObjectPython] Line1749  # Draft 2D object (typed FeaturePython)
  Area = 0
  ChamferSize = 0
  Closed = false
  End = (14400,5500,0)
  FilletRadius = 0
  Length = 447.214
  MakeFace = true
  Placement = pos=(14600,5100,0) rot=(0,0,1;0rad)
  Points = (2) [(0,0,0),(-200,400,0)]
  Start = (14600,5100,0)
  Subdivisions = 0
FEATURE [Part::Part2DObjectPython] Line1750  # Draft 2D object (typed FeaturePython)
  Area = 0
  ChamferSize = 0
  Closed = false
  End = (14800,5500,0)
  FilletRadius = 0
  Length = 447.214
  MakeFace = true
  Placement = pos=(14600,5100,0) rot=(0,0,1;0rad)
  Points = (2) [(0,0,0),(200,400,0)]
  Start = (14600,5100,0)
  Subdivisions = 0
FEATURE [Part::Part2DObjectPython] ShapeString218  # Draft 2D object (typed FeaturePython)
  FontFile = <path>
  Placement = pos=(14506.7,4699.61,0) rot=(0,0,1;0rad)
  Size = 250
  String = С
  Tracking = 0
FEATURE [Part::Part2DObjectPython] ShapeString219  # Draft 2D object (typed FeaturePython)
  FontFile = <path>
  Placement = pos=(14406.7,6499.61,0) rot=(0,0,1;0rad)
  Size = 250
  String = Юг
  Tracking = 0
FEATURE [App::FeaturePython] Dimension112  # Draft dimension (typed FeaturePython)
  Diameter = false
  Dimline = (4870,9000,0)
  Direction = (0,0,0)
  Distance = 2020
  End = (6890,9506.46,0)
  Normal = (0,0,1)
  Start = (4870,9506.46,0)
FEATURE [App::FeaturePython] Dimension113  # Draft dimension (typed FeaturePython)
  Diameter = false
  Dimline = (6500,-1800,0)
  Direction = (0,0,0)
  Distance = 13640
  End = (13080,-555,0)
  Normal = (0,0,1)
  Start = (-560,-555,0)
FEATURE [App::FeaturePython] Dimension114  # Draft dimension (typed FeaturePython)
  Diameter = false
  Dimline = (4150,-1500,0)
  Direction = (0,0,0)
  Distance = 3350
  End = (7400,-2107.94,0)
  Normal = (0,0,1)
  Start = (4050,-2107.94,0)
FEATURE [App::FeaturePython] Dimension115  # Draft dimension (typed FeaturePython)
  Diameter = false
  Dimline = (9500,-1500,0)
  Direction = (0,0,0)
  Distance = 2100
  End = (9500,-2107.94,0)
  Normal = (0,0,1)
  Start = (7400,-2107.94,0)
FEATURE [App::FeaturePython] Dimension116  # Draft dimension (typed FeaturePython)
  Diameter = false
  Dimline = (1700,-1500,0)
  Direction = (0,0,0)
  Distance = 4290
  End = (4050,-2107.94,0)
  Normal = (0,0,1)
  Start = (-240,-2107.94,0)
FEATURE [App::FeaturePython] Dimension117  # Draft dimension (typed FeaturePython)
  Diameter = false
  Dimline = (7910,9000,0)
  Direction = (0,0,0)
  Distance = 4850
  End = (12760,9506.46,0)
  Normal = (0,0,1)
  Start = (7910,9506.46,0)
FEATURE [App::FeaturePython] Dimension118  # Draft dimension (typed FeaturePython)
  Diameter = false
  Dimline = (-1200,2335,0)
  Direction = (0,0,0)
  Distance = 2570
  End = (-1836.7,2335,0)
  Normal = (0,0,1)
  Start = (-1836.7,-235,0)
FEATURE [App::FeaturePython] Dimension119  # Draft dimension (typed FeaturePython)
  Diameter = false
  Dimline = (3550,-1350,0)
  Direction = (0,0,0)
  Distance = 600
  End = (4050,-2107.94,0)
  Normal = (0,0,1)
  Start = (3450,-2107.94,0)
FEATURE [App::FeaturePython] Dimension120  # Draft dimension (typed FeaturePython)
  Diameter = false
  Dimline = (8700,4200,0)
  Direction = (0,0,0)
  Distance = 325
  End = (8200,3817.5,0)
  Normal = (0,0,1)
  Start = (8200,3492.5,0)
FEATURE [Part::Part2DObjectPython] Circle154  label="Circle155"  # Draft 2D object (typed FeaturePython)
  Area = 0
  FirstAngle = 0
  LastAngle = 0
  MakeFace = false
  Placement = pos=(7390,4155,0) rot=(0,0,-1;1.5708rad)
  Radius = 100
FEATURE [Part::Part2DObjectPython] Line1755  # Draft 2D object (typed FeaturePython)
  Area = 0
  ChamferSize = 0
  Closed = false
  End = (7390,3825,0)
  FilletRadius = 0
  Length = 330
  MakeFace = false
  Placement = pos=(7420,4155,0) rot=(0,0,-1;1.5708rad)
  Points = (2) [(0,-30,0),(330,-30,0)]
  Start = (7390,4155,0)
  Subdivisions = 0
FEATURE [App::FeaturePython] Dimension121  # Draft dimension (typed FeaturePython)
  Diameter = false
  Dimline = (9500,-1500,0)
  Direction = (0,0,0)
  Distance = 3260
  End = (12760,-2107.94,0)
  Normal = (0,0,1)
  Start = (9500,-2107.94,0)
FEATURE [App::FeaturePython] Dimension123  # Draft dimension (typed FeaturePython)
  Diameter = false
  Dimline = (9400,3000,0)
  Direction = (0,0,0)
  Distance = 900
  End = (9087.5,3400,0)
  Normal = (0,0,1)
  Start = (9087.5,2500,0)
FEATURE [App::FeaturePython] Dimension124  # Draft dimension (typed FeaturePython)
  Diameter = false
  Dimline = (-1200,2335,0)
  Direction = (0,0,0)
  Distance = 1345
  End = (-1836.7,3680,0)
  Normal = (0,0,1)
  Start = (-1836.7,2335,0)
FEATURE [Part::Part2DObjectPython] Circle155  label="Circle156"  # Draft 2D object (typed FeaturePython)
  Area = 0
  FirstAngle = 0
  LastAngle = 0
  MakeFace = false
  Placement = pos=(-2036.7,7695,0) rot=(0,0,1;0rad)
  Radius = 200
FEATURE [Part::Part2DObjectPython] ShapeString220  # Draft 2D object (typed FeaturePython)
  FontFile = <path>
  Placement = pos=(-2130.05,7594.61,0) rot=(0,0,1;0rad)
  Size = 200
  String = D
  Tracking = 0
FEATURE [Part::Part2DObjectPython] Circle156  label="Circle157"  # Draft 2D object (typed FeaturePython)
  Area = 0
  FirstAngle = 0
  LastAngle = 0
  MakeFace = false
  Placement = pos=(-2036.7,3680,0) rot=(0,0,1;0rad)
  Radius = 200
FEATURE [Part::Part2DObjectPython] ShapeString221  # Draft 2D object (typed FeaturePython)
  FontFile = <path>
  Placement = pos=(-2133.13,3586.85,0) rot=(0,0,1;0rad)
  Size = 200
  String = C
  Tracking = 0
FEATURE [Part::Part2DObjectPython] Circle157  label="Circle158"  # Draft 2D object (typed FeaturePython)
  Area = 0
  FirstAngle = 0
  LastAngle = 0
  MakeFace = false
  Placement = pos=(-2036.7,2335,0) rot=(0,0,1;0rad)
  Radius = 200
FEATURE [Part::Part2DObjectPython] ShapeString222  # Draft 2D object (typed FeaturePython)
  FontFile = <path>
  Placement = pos=(-2116.38,2246.01,0) rot=(0,0,1;0rad)
  Size = 200
  String = B
  Tracking = 0
FEATURE [Part::Part2DObjectPython] Circle158  label="Circle159"  # Draft 2D object (typed FeaturePython)
  Area = 0
  FirstAngle = 0
  LastAngle = 0
  MakeFace = false
  Placement = pos=(-2036.7,-235,0) rot=(0,0,1;0rad)
  Radius = 200
FEATURE [Part::Part2DObjectPython] ShapeString223  # Draft 2D object (typed FeaturePython)
  FontFile = <path>
  Placement = pos=(-2124.02,-327.945,0) rot=(0,0,1;0rad)
  Size = 200
  String = A
  Tracking = 0
FEATURE [Part::Part2DObjectPython] Circle159  label="Circle160"  # Draft 2D object (typed FeaturePython)
  Area = 0
  FirstAngle = 0
  LastAngle = 0
  MakeFace = false
  Placement = pos=(-240,9706.46,0) rot=(0,0,1;0rad)
  Radius = 200
FEATURE [Part::Part2DObjectPython] ShapeString224  # Draft 2D object (typed FeaturePython)
  FontFile = <path>
  Placement = pos=(-319.076,9614.22,0) rot=(0,0,1;0rad)
  Size = 200
  String = 1
  Tracking = 0
FEATURE [Part::Part2DObjectPython] Circle160  label="Circle161"  # Draft 2D object (typed FeaturePython)
  Area = 0
  FirstAngle = 0
  LastAngle = 0
  MakeFace = false
  Placement = pos=(3450,9706.46,0) rot=(0,0,1;0rad)
  Radius = 200
FEATURE [Part::Part2DObjectPython] ShapeString225  # Draft 2D object (typed FeaturePython)
  FontFile = <path>
  Placement = pos=(3367.38,9622.97,0) rot=(0,0,1;0rad)
  Size = 200
  String = 2
  Tracking = 0
FEATURE [Part::Part2DObjectPython] Circle161  label="Circle162"  # Draft 2D object (typed FeaturePython)
  Area = 0
  FirstAngle = 0
  LastAngle = 0
  MakeFace = false
  Placement = pos=(4050,9706.46,0) rot=(0,0,1;0rad)
  Radius = 200
FEATURE [Part::Part2DObjectPython] ShapeString226  # Draft 2D object (typed FeaturePython)
  FontFile = <path>
  Placement = pos=(3978.07,9610.28,0) rot=(0,0,1;0rad)
  Size = 200
  String = 3
  Tracking = 0
FEATURE [Part::Part2DObjectPython] Circle162  label="Circle163"  # Draft 2D object (typed FeaturePython)
  Area = 0
  FirstAngle = 0
  LastAngle = 0
  MakeFace = false
  Placement = pos=(4870,9706.46,0) rot=(0,0,1;0rad)
  Radius = 200
FEATURE [Part::Part2DObjectPython] ShapeString227  # Draft 2D object (typed FeaturePython)
  FontFile = <path>
  Placement = pos=(4784.17,9612.89,0) rot=(0,0,1;0rad)
  Size = 200
  String = 4
  Tracking = 0
FEATURE [Part::Part2DObjectPython] Circle163  label="Circle164"  # Draft 2D object (typed FeaturePython)
  Area = 0
  FirstAngle = 0
  LastAngle = 0
  MakeFace = false
  Placement = pos=(6890,9706.46,0) rot=(0,0,1;0rad)
  Radius = 200
FEATURE [Part::Part2DObjectPython] ShapeString228  # Draft 2D object (typed FeaturePython)
  FontFile = <path>
  Placement = pos=(6820.3,9606.58,0) rot=(0,0,1;0rad)
  Size = 200
  String = 5
  Tracking = 0
FEATURE [Part::Part2DObjectPython] Circle164  label="Circle165"  # Draft 2D object (typed FeaturePython)
  Area = 0
  FirstAngle = 0
  LastAngle = 0
  MakeFace = false
  Placement = pos=(7400,9706.46,0) rot=(0,0,1;0rad)
  Radius = 200
FEATURE [Part::Part2DObjectPython] ShapeString229  # Draft 2D object (typed FeaturePython)
  FontFile = <path>
  Placement = pos=(7325.5,9616.19,0) rot=(0,0,1;0rad)
  Size = 200
  String = 6
  Tracking = 0
FEATURE [Part::Part2DObjectPython] Circle165  label="Circle166"  # Draft 2D object (typed FeaturePython)
  Area = 0
  FirstAngle = 0
  LastAngle = 0
  MakeFace = false
  Placement = pos=(7910,9706.46,0) rot=(0,0,1;0rad)
  Radius = 200
FEATURE [Part::Part2DObjectPython] ShapeString230  # Draft 2D object (typed FeaturePython)
  FontFile = <path>
  Placement = pos=(7839.18,9604.4,0) rot=(0,0,1;0rad)
  Size = 200
  String = 7
  Tracking = 0
FEATURE [Part::Part2DObjectPython] Circle166  label="Circle167"  # Draft 2D object (typed FeaturePython)
  Area = 0
  FirstAngle = 0
  LastAngle = 0
  MakeFace = false
  Placement = pos=(9500,9706.46,0) rot=(0,0,1;0rad)
  Radius = 200
FEATURE [Part::Part2DObjectPython] ShapeString231  # Draft 2D object (typed FeaturePython)
  FontFile = <path>
  Placement = pos=(9427.59,9608.74,0) rot=(0,0,1;0rad)
  Size = 200
  String = 8
  Tracking = 0
FEATURE [Part::Part2DObjectPython] Circle167  label="Circle168"  # Draft 2D object (typed FeaturePython)
  Area = 0
  FirstAngle = 0
  LastAngle = 0
  MakeFace = false
  Placement = pos=(12760,9706.46,0) rot=(0,0,1;0rad)
  Radius = 200
FEATURE [Part::Part2DObjectPython] ShapeString232  # Draft 2D object (typed FeaturePython)
  FontFile = <path>
  Placement = pos=(12685.6,9616.32,0) rot=(0,0,1;0rad)
  Size = 200
  String = 9
  Tracking = 0
FEATURE [App::FeaturePython] Dimension126  # Draft dimension (typed FeaturePython)
  Diameter = false
  Dimline = (4770,3300,0)
  Direction = (0,0,0)
  Distance = 1970
  End = (5365,3730,0)
  Normal = (0,0,1)
  Start = (3395,3730,0)
FEATURE [App::FeaturePython] Dimension127  # Draft dimension (typed FeaturePython)
  Diameter = false
  Dimline = (5650,3300,0)
  Direction = (0,0,0)
  Distance = 900
  End = (6550,3642.5,0)
  Normal = (0,0,1)
  Start = (5650,3642.5,0)
FEATURE [App::FeaturePython] Dimension128  # Draft dimension (typed FeaturePython)
  Diameter = false
  Dimline = (7600,3000,0)
  Direction = (0,0,0)
  Distance = 1690
  End = (8315,3730,0)
  Normal = (0,0,1)
  Start = (6625,3730,0)
FEATURE [App::FeaturePython] Dimension130  # Draft dimension (typed FeaturePython)
  Diameter = false
  Dimline = (4400,2600,0)
  Direction = (0,0,0)
  Distance = 1175
  End = (5132.59,3667.5,0)
  Normal = (0,0,1)
  Start = (4301.74,2836.65,0)
FEATURE [App::FeaturePython] Dimension131  # Draft dimension (typed FeaturePython)
  Diameter = false
  Dimline = (4835,-235,0)
  Direction = (0,0,0)
  Distance = 660
  End = (4835,-25,0)
  Normal = (0,0,1)
  Start = (4175,-25,0)
FEATURE [App::FeaturePython] Dimension132  # Draft dimension (typed FeaturePython)
  Diameter = false
  Dimline = (7555,-235,0)
  Direction = (0,0,0)
  Distance = 660
  End = (8215,-25,0)
  Normal = (0,0,1)
  Start = (7555,-25,0)
FEATURE [App::FeaturePython] Dimension133  # Draft dimension (typed FeaturePython)
  Diameter = false
  Dimline = (-240,1840,0)
  Direction = (0,0,0)
  Distance = 1440
  End = (-30,3280,0)
  Normal = (0,0,1)
  Start = (-30,1840,0)
FEATURE [App::FeaturePython] Dimension134  # Draft dimension (typed FeaturePython)
  Diameter = false
  Dimline = (12760,1320,0)
  Direction = (0,0,0)
  Distance = 1960
  End = (12550,3280,0)
  Normal = (0,0,1)
  Start = (12550,1320,0)
FEATURE [App::FeaturePython] Dimension135  # Draft dimension (typed FeaturePython)
  Diameter = false
  Dimline = (12760,4000,0)
  Direction = (0,0,0)
  Distance = 920
  End = (12550,4970,0)
  Normal = (0,0,1)
  Start = (12550,4050,0)
FEATURE [App::FeaturePython] Dimension136  # Draft dimension (typed FeaturePython)
  Diameter = false
  Dimline = (8595,7695,0)
  Direction = (0,0,0)
  Distance = 1960
  End = (10555,7485,0)
  Normal = (0,0,1)
  Start = (8595,7485,0)
FEATURE [App::FeaturePython] Dimension137  # Draft dimension (typed FeaturePython)
  Diameter = false
  Dimline = (6005,7695,0)
  Direction = (0,0,0)
  Distance = 920
  End = (6005,7485,0)
  Normal = (0,0,1)
  Start = (5085,7485,0)
FEATURE [App::FeaturePython] Dimension138  # Draft dimension (typed FeaturePython)
  Diameter = false
  Dimline = (3925,7695,0)
  Direction = (0,0,0)
  Distance = 1960
  End = (3925,7485,0)
  Normal = (0,0,1)
  Start = (1965,7485,0)
FEATURE [App::FeaturePython] Dimension139  # Draft dimension (typed FeaturePython)
  Diameter = false
  Dimline = (5690,200,0)
  Direction = (0,0,0)
  Distance = 3250
  End = (7350,-25,0)
  Normal = (0,0,1)
  Start = (4100,-25,0)
FEATURE [App::FeaturePython] Dimension140  # Draft dimension (typed FeaturePython)
  Diameter = false
  Dimline = (5200,1052.26,0)
  Direction = (0,0,0)
  Distance = 2310
  End = (7300,2285,0)
  Normal = (0,0,1)
  Start = (7300,-25,0)
FEATURE [App::FeaturePython] Dimension143  # Draft dimension (typed FeaturePython)
  Diameter = false
  Dimline = (11400,2000,0)
  Direction = (0,0,0)
  Distance = 6315
  End = (11967.5,6887.5,0)
  Normal = (0,0,1)
  Start = (11967.5,572.5,0)
FEATURE [App::FeaturePython] Dimension144  # Draft dimension (typed FeaturePython)
  Diameter = false
  Dimline = (3700,8200,0)
  Direction = (0,0,0)
  Distance = 1830
  End = (3860,8015,0)
  Normal = (0,0,1)
  Start = (2030,8015,0)
FEATURE [App::FeaturePython] Dimension145  # Draft dimension (typed FeaturePython)
  Diameter = false
  Dimline = (2300,5100,0)
  Direction = (0,0,0)
  Distance = 4207.5
  End = (4177.5,5200,0)
  Normal = (0,0,1)
  Start = (-30,5200,0)
FEATURE [App::FeaturePython] Dimension146  # Draft dimension (typed FeaturePython)
  Diameter = false
  Dimline = (8800,5100,0)
  Direction = (0,0,0)
  Distance = 4455
  End = (12550,3825,0)
  Normal = (0,0,1)
  Start = (8095,3825,0)
FEATURE [App::FeaturePython] Dimension147  # Draft dimension (typed FeaturePython)
  Diameter = false
  Dimline = (10434.8,1973.04,0)
  Direction = (0,0,0)
  Distance = 3337.5
  End = (12550,3400,0)
  Normal = (0,0,1)
  Start = (9212.5,3400,0)
FEATURE [App::FeaturePython] Dimension148  # Draft dimension (typed FeaturePython)
  Diameter = false
  Dimline = (1231.46,5164.85,0)
  Direction = (0,0,0)
  Distance = 3095
  End = (-30,6887.5,0)
  Normal = (0,0,1)
  Start = (-30,3792.5,0)
FEATURE [App::FeaturePython] Dimension149  # Draft dimension (typed FeaturePython)
  Diameter = false
  Dimline = (10700,200,0)
  Direction = (0,0,0)
  Distance = 2000
  End = (9450,-25,0)
  Normal = (0,0,1)
  Start = (7450,-25,0)
FEATURE [App::FeaturePython] Dimension150  # Draft dimension (typed FeaturePython)
  Diameter = false
  Dimline = (12100,4500,0)
  Direction = (0,0,0)
  Distance = 3660
  End = (12550,7485,0)
  Normal = (0,0,1)
  Start = (12550,3825,0)
FEATURE [App::GeometryPython] BuildingPart128  label="Направление открывания дверей001"  # Arch/BIM 172 (typed FeaturePython)
  Area = 0
  Height = 0
  HeightPropagate = true
  IfcData = attributes={"GlobalId": {"name": "GlobalId", "type": "IfcGloballyUniqueId", "is_enum": false, "enum_values": []}, "Description": {"... (+484 chars omitted),+1 more (map truncated)
  IfcType = 172
  LevelOffset = 0
  PredefinedType = 0
FEATURE [App::FeaturePython] Dimension152  # Draft dimension (typed FeaturePython)
  Diameter = false
  Dimline = (11920,3300,0)
  Direction = (0,0,0)
  Distance = 600
  End = (12550,3730,0)
  Normal = (0,0,1)
  Start = (11950,3730,0)
FEATURE [App::FeaturePython] Dimension153  # Draft dimension (typed FeaturePython)
  Diameter = false
  Dimline = (6720,3300,0)
  Direction = (0,0,0)
  Distance = 1020
  End = (7920,3492.5,0)
  Normal = (0,0,1)
  Start = (6900,3492.5,0)
FEATURE [App::FeaturePython] Dimension154  # Draft dimension (typed FeaturePython)
  Diameter = false
  Dimline = (5800,3000,0)
  Direction = (0,0,0)
  Distance = 1260
  End = (6625,3730,0)
  Normal = (0,0,1)
  Start = (5365,3730,0)
FEATURE [App::FeaturePython] Dimension155  # Draft dimension (typed FeaturePython)
  Diameter = false
  Dimline = (3850,4000,0)
  Direction = (0,0,0)
  Distance = 3900
  End = (3850,3680,0)
  Normal = (0,0,1)
  Start = (-50,3680,0)
FEATURE [App::FeaturePython] Dimension156  # Draft dimension (typed FeaturePython)
  Diameter = false
  Dimline = (4500,1400,0)
  Direction = (0,0,0)
  Distance = 125
  End = (4301.74,572.5,0)
  Normal = (0,0,1)
  Start = (4176.74,572.5,0)
FEATURE [Part::FeaturePython] Component181  label="Компонент027"  # Arch/BIM 0 (typed FeaturePython)
  Base = -> Circle154
  HorizontalArea = 0
  IfcData = attributes={"GlobalId": {"name": "GlobalId", "type": "IfcGloballyUniqueId", "is_enum": false, "enum_values": []}, "Description": {"... (+538 chars omitted),+1 more (map truncated)
  IfcType = 0
  MoveBase = false
  MoveWithHost = false
  PerimeterLength = 0
  Placement = pos=(6267.5,5410,0) rot=(0,0,-1;1.5708rad)
  PredefinedType = 0
  VerticalArea = 0
FEATURE [Part::FeaturePython] Component182  label="Компонент028"  # Arch/BIM 0 (typed FeaturePython)
  Base = -> Line1755
  HorizontalArea = 0
  IfcData = attributes={"GlobalId": {"name": "GlobalId", "type": "IfcGloballyUniqueId", "is_enum": false, "enum_values": []}, "Description": {"... (+538 chars omitted),+1 more (map truncated)
  IfcType = 0
  MoveBase = false
  MoveWithHost = false
  PerimeterLength = 0
  Placement = pos=(6297.5,5410,0) rot=(0,0,-1;1.5708rad)
  PredefinedType = 0
  VerticalArea = 0
FEATURE [App::FeaturePython] Dimension157  # Draft dimension (typed FeaturePython)
  Diameter = false
  Dimline = (2030,8200,0)
  Direction = (0,0,0)
  Distance = 2590
  End = (2030,8015,0)
  Normal = (0,0,1)
  Start = (-560,8015,0)
FEATURE [App::FeaturePython] Dimension158  # Draft dimension (typed FeaturePython)
  Diameter = false
  Dimline = (3860,8200,0)
  Direction = (0,0,0)
  Distance = 1290
  End = (5150,8015,0)
  Normal = (0,0,1)
  Start = (3860,8015,0)
FEATURE [App::FeaturePython] Dimension159  # Draft dimension (typed FeaturePython)
  Diameter = false
  Dimline = (5150,8200,0)
  Direction = (0,0,0)
  Distance = 790
  End = (5940,8015,0)
  Normal = (0,0,1)
  Start = (5150,8015,0)
FEATURE [App::FeaturePython] Dimension160  # Draft dimension (typed FeaturePython)
  Diameter = false
  Dimline = (5940,8200,0)
  Direction = (0,0,0)
  Distance = 2720
  End = (8660,8015,0)
  Normal = (0,0,1)
  Start = (5940,8015,0)
FEATURE [App::FeaturePython] Dimension161  # Draft dimension (typed FeaturePython)
  Diameter = false
  Dimline = (8660,8200,0)
  Direction = (0,0,0)
  Distance = 1830
  End = (10490,8015,0)
  Normal = (0,0,1)
  Start = (8660,8015,0)
FEATURE [App::FeaturePython] Dimension162  # Draft dimension (typed FeaturePython)
  Diameter = false
  Dimline = (10490,8200,0)
  Direction = (0,0,0)
  Distance = 2590
  End = (13080,8015,0)
  Normal = (0,0,1)
  Start = (10490,8015,0)
FEATURE [App::FeaturePython] Dimension163  # Draft dimension (typed FeaturePython)
  Diameter = false
  Dimline = (5000,7200,0)
  Direction = (0,0,0)
  Distance = 1900
  End = (6830,7485,0)
  Normal = (0,0,1)
  Start = (4930,7485,0)
FEATURE [App::FeaturePython] Dimension164  # Draft dimension (typed FeaturePython)
  Diameter = false
  Dimline = (3066.58,4040.26,0)
  Direction = (0,0,0)
  Distance = 900
  End = (4053.62,4552.01,0)
  Normal = (0,0,1)
  Start = (3417.23,3915.62,0)
FEATURE [App::FeaturePython] Dimension165  # Draft dimension (typed FeaturePython)
  Diameter = false
  Dimline = (-800,1905,0)
  Direction = (0,0,0)
  Distance = 2460
  End = (-560,1905,0)
  Normal = (0,0,1)
  Start = (-560,-555,0)
FEATURE [App::FeaturePython] Dimension166  # Draft dimension (typed FeaturePython)
  Diameter = false
  Dimline = (1700,-800,0)
  Direction = (0,0,0)
  Distance = 4800
  End = (4240,-555,0)
  Normal = (0,0,1)
  Start = (-560,-555,0)
FEATURE [App::FeaturePython] Dimension167  # Draft dimension (typed FeaturePython)
  Diameter = false
  Dimline = (4240,-800,0)
  Direction = (0,0,0)
  Distance = 530
  End = (4770,-555,0)
  Normal = (0,0,1)
  Start = (4240,-555,0)
FEATURE [App::FeaturePython] Dimension168  # Draft dimension (typed FeaturePython)
  Diameter = false
  Dimline = (3900,2600,0)
  Direction = (0,0,0)
  Distance = 900
  End = (4053.62,2907.99,0)
  Normal = (0,0,1)
  Start = (3417.23,3544.38,0)
FEATURE [App::FeaturePython] Dimension169  # Draft dimension (typed FeaturePython)
  Diameter = false
  Dimline = (7620,-800,0)
  Direction = (0,0,0)
  Distance = 530
  End = (8150,-555,0)
  Normal = (0,0,1)
  Start = (7620,-555,0)
FEATURE [App::FeaturePython] Dimension170  # Draft dimension (typed FeaturePython)
  Diameter = false
  Dimline = (6720,-800,0)
  Direction = (0,0,0)
  Distance = 900
  End = (7620,-555,0)
  Normal = (0,0,1)
  Start = (6720,-555,0)
FEATURE [App::FeaturePython] Dimension171  # Draft dimension (typed FeaturePython)
  Diameter = false
  Dimline = (8150,-800,0)
  Direction = (0,0,0)
  Distance = 4930
  End = (13080,-555,0)
  Normal = (0,0,1)
  Start = (8150,-555,0)
FEATURE [App::FeaturePython] Dimension172  # Draft dimension (typed FeaturePython)
  Diameter = false
  Dimline = (13600,1200,0)
  Direction = (0,0,0)
  Distance = 1940
  End = (13080,1385,0)
  Normal = (0,0,1)
  Start = (13080,-555,0)
FEATURE [App::FeaturePython] Dimension173  # Draft dimension (typed FeaturePython)
  Diameter = false
  Dimline = (8315,3000,0)
  Direction = (0,0,0)
  Distance = 810
  End = (9125,3730,0)
  Normal = (0,0,1)
  Start = (8315,3730,0)
FEATURE [App::FeaturePython] Dimension174  # Draft dimension (typed FeaturePython)
  Diameter = false
  Dimline = (13600,3215,0)
  Direction = (0,0,0)
  Distance = 900
  End = (13080,4115,0)
  Normal = (0,0,1)
  Start = (13080,3215,0)
FEATURE [App::FeaturePython] Dimension175  # Draft dimension (typed FeaturePython)
  Diameter = false
  Dimline = (13600,4115,0)
  Direction = (0,0,0)
  Distance = 790
  End = (13080,4905,0)
  Normal = (0,0,1)
  Start = (13080,4115,0)
FEATURE [App::FeaturePython] Dimension176  # Draft dimension (typed FeaturePython)
  Diameter = false
  Dimline = (13600,4905,0)
  Direction = (0,0,0)
  Distance = 3110
  End = (13080,8015,0)
  Normal = (0,0,1)
  Start = (13080,4905,0)
FEATURE [App::FeaturePython] Dimension177  # Draft dimension (typed FeaturePython)
  Diameter = false
  Dimline = (-800,3215,0)
  Direction = (0,0,0)
  Distance = 4800
  End = (-560,8015,0)
  Normal = (0,0,1)
  Start = (-560,3215,0)
FEATURE [Part::Part2DObjectPython] Line1758  # Draft 2D object (typed FeaturePython)
  Area = 0
  ChamferSize = 0
  Closed = false
  End = (9950,9900,0)
  FilletRadius = 0
  Length = 200
  MakeFace = true
  Placement = pos=(9950,10100,0) rot=(0,0,1;0rad)
  Points = (2) [(0,0,0),(0,-200,0)]
  Start = (9950,10100,0)
  Subdivisions = 0
FEATURE [Part::Part2DObjectPython] Line1759  # Draft 2D object (typed FeaturePython)
  Area = 0
  ChamferSize = 0
  Closed = false
  End = (7800,9900,0)
  FilletRadius = 0
  Length = 200
  MakeFace = true
  Placement = pos=(7800,10100,0) rot=(0,0,1;0rad)
  Points = (2) [(0,0,0),(0,-200,0)]
  Start = (7800,10100,0)
  Subdivisions = 0
FEATURE [Part::Part2DObjectPython] Line1760  # Draft 2D object (typed FeaturePython)
  Area = 0
  ChamferSize = 0
  Closed = false
  End = (7800,-2300,0)
  FilletRadius = 0
  Length = 200
  MakeFace = true
  Placement = pos=(7800,-2500,0) rot=(0,0,1;0rad)
  Points = (2) [(0,0,0),(0,200,0)]
  Start = (7800,-2500,0)
  Subdivisions = 0
FEATURE [Part::Part2DObjectPython] Line1761  # Draft 2D object (typed FeaturePython)
  Area = 0
  ChamferSize = 0
  Closed = false
  End = (9950,-2300,0)
  FilletRadius = 0
  Length = 200
  MakeFace = true
  Placement = pos=(9950,-2500,0) rot=(0,0,1;0rad)
  Points = (2) [(0,0,0),(0,200,0)]
  Start = (9950,-2500,0)
  Subdivisions = 0
FEATURE [Part::Part2DObjectPython] Line1762  # Draft 2D object (typed FeaturePython)
  Area = 0
  ChamferSize = 0
  Closed = false
  End = (9950,-2500,0)
  FilletRadius = 0
  Length = 250
  MakeFace = true
  Placement = pos=(10200,-2500,0) rot=(0,0,1;0rad)
  Points = (2) [(0,0,0),(-250,0,0)]
  Start = (10200,-2500,0)
  Subdivisions = 0
FEATURE [Part::Part2DObjectPython] ShapeString233  # Draft 2D object (typed FeaturePython)
  FontFile = <path>
  Placement = pos=(10259.2,-2466.26,0) rot=(0,0,1;0rad)
  Size = 150
  String = А
  Tracking = 0
FEATURE [Part::Part2DObjectPython] ShapeString234  # Draft 2D object (typed FeaturePython)
  FontFile = <path>
  Placement = pos=(10259.2,10133.7,0) rot=(0,0,1;0rad)
  Size = 150
  String = А
  Tracking = 0
FEATURE [Part::Part2DObjectPython] Line1763  # Draft 2D object (typed FeaturePython)
  Area = 0
  ChamferSize = 0
  Closed = false
  End = (9950,10100,0)
  FilletRadius = 0
  Length = 250
  MakeFace = true
  Placement = pos=(10200,10100,0) rot=(0,0,1;0rad)
  Points = (2) [(0,0,0),(-250,0,0)]
  Start = (10200,10100,0)
  Subdivisions = 0
FEATURE [Part::Part2DObjectPython] Line1764  # Draft 2D object (typed FeaturePython)
  Area = 0
  ChamferSize = 0
  Closed = false
  End = (7800,-2500,0)
  FilletRadius = 0
  Length = 250
  MakeFace = true
  Placement = pos=(8050,-2500,0) rot=(0,0,1;0rad)
  Points = (2) [(0,0,0),(-250,0,0)]
  Start = (8050,-2500,0)
  Subdivisions = 0
FEATURE [Part::Part2DObjectPython] ShapeString235  # Draft 2D object (typed FeaturePython)
  FontFile = <path>
  Placement = pos=(8109.21,-2466.26,0) rot=(0,0,1;0rad)
  Size = 150
  String = B
  Tracking = 0
FEATURE [Part::Part2DObjectPython] ShapeString236  # Draft 2D object (typed FeaturePython)
  FontFile = <path>
  Placement = pos=(8109.21,10133.7,0) rot=(0,0,1;0rad)
  Size = 150
  String = B
  Tracking = 0
FEATURE [Part::Part2DObjectPython] Line1765  # Draft 2D object (typed FeaturePython)
  Area = 0
  ChamferSize = 0
  Closed = false
  End = (7800,10100,0)
  FilletRadius = 0
  Length = 250
  MakeFace = true
  Placement = pos=(8050,10100,0) rot=(0,0,1;0rad)
  Points = (2) [(0,0,0),(-250,0,0)]
  Start = (8050,10100,0)
  Subdivisions = 0
FEATURE [App::GeometryPython] BuildingPart129  label="разрезы001"  # Arch/BIM 172 (typed FeaturePython)
  Area = 0
  Group = -> [Line1758,Line1759,Line1760,Line1761,Line1762,ShapeString233,ShapeString234,Line1763,Line1764,ShapeString235,ShapeString236,Line1765]
  Height = 0
  HeightPropagate = true
  IfcData = attributes={"GlobalId": {"name": "GlobalId", "type": "IfcGloballyUniqueId", "is_enum": false, "enum_values": []}, "Description": {"... (+484 chars omitted),+1 more (map truncated)
  IfcType = 172
  LevelOffset = 0
  PredefinedType = 0
FEATURE [App::FeaturePython] Dimension179  # Draft dimension (typed FeaturePython)
  Diameter = false
  Dimline = (6500,7200,0)
  Direction = (0,0,0)
  Distance = 1800
  End = (5900,7485,0)
  Normal = (0,0,1)
  Start = (5900,5685,0)
FEATURE [App::FeaturePython] Dimension180  # Draft dimension (typed FeaturePython)
  Diameter = false
  Dimline = (5600,5500,0)
  Direction = (0,0,0)
  Distance = 3055
  End = (6717.5,6880,0)
  Normal = (0,0,1)
  Start = (6717.5,3825,0)
FEATURE [App::FeaturePython] Dimension181  # Draft dimension (typed FeaturePython)
  Diameter = false
  Dimline = (5400,5900,0)
  Direction = (0,0,0)
  Distance = 2357.5
  End = (6717.5,6880,0)
  Normal = (0,0,1)
  Start = (4360,6880,0)
FEATURE [App::GeometryPython] BuildingPart127  label="Размеры (мансарда)"  # Arch/BIM 52 (typed FeaturePython)
  Area = 0
  GlobalId = 3_s$oy9jj54xonqTEdRA8q
  Group = -> [Dimension105,Dimension106,Dimension113,Dimension107,Dimension108,Dimension111,Dimension110,Dimension109,ShapeString209,Circle145,Circle146,ShapeString210,Circle147,ShapeString211,Circle149,ShapeString213,Circle150,ShapeString214,Circle152,ShapeString216,Line1746,Line1747,Line1748,Line1749,Line1750,ShapeString218,ShapeString219,Dimension112,Dimension114,Dimension115,Dimension116,Dimension117,+87 more]
  Height = 0
  HeightPropagate = true
  IfcData = IfcUID=3_s$oy9jj54xonqTEdRA8q,+2 more (map truncated)
  IfcType = 52
  LevelOffset = 0
FEATURE [Part::FeaturePython] Axis001009  label="Вертикальные Оси001"  # WARN: FeaturePython — macro-defined, semantics opaque (R4)
  Angles = [0,0,0,0]
  Distances = [320,4480,4910,3610]
  Length = 11614.4
  Placement = pos=(-560,-2107.94,0) rot=(0,0,1;0rad)
  expr: .Placement.Base.x = Rectangle3343.Placement.Base.x
  expr: .Placement.Base.y = Rectangle3343.Placement.Base.y - Length * 0.135
  expr: Length = Rectangle3343.Height * 1.36
FEATURE [Part::FeaturePython] Axis001010  label="Горизонтальные оси001"  # WARN: FeaturePython — macro-defined, semantics opaque (R4)
  Angles = [0,0,0]
  Distances = [305,3965,3965]
  Length = 15958.8
  Placement = pos=(14122.1,-540,0) rot=(0,0,1;1.5708rad)
  expr: .Placement.Base.y = Rectangle3343.Placement.Base.y
  expr: .Placement.Base.x = Rectangle3343.Placement.Base.x + Length * 0.92
  expr: Length = Rectangle3343.Length * 1.17
FEATURE [Part::Part2DObjectPython] Line1766  # Draft 2D object (typed FeaturePython)
  Area = 0
  ChamferSize = 0
  Closed = false
  End = (12760,-2107.94,0)
  FilletRadius = 0
  Length = 13000
  MakeFace = true
  Placement = pos=(-240,-2107.94,0) rot=(0,0,1;0rad)
  Points = (2) [(0,0,0),(13000,0,0)]
  Start = (-240,-2107.94,0)
  Subdivisions = 0
FEATURE [Part::Part2DObjectPython] Line1767  # Draft 2D object (typed FeaturePython)
  ChamferSize = 0
  Closed = true
  End = (-30,3730,0)
  FilletRadius = 0
  Length = 3350
  MakeFace = false
  Placement = pos=(9650,5690,0) rot=(0,0,1;0rad)
  Points = (2) [(-6330,-1960,0),(-9680,-1960,0)]
  Start = (3320,3730,0)
  Subdivisions = 0
FEATURE [App::MaterialObjectPython] Material020  label="Стекловата"  # material (typed FeaturePython)
  Description = Утепление стекловатой
  Material = AuthorAndLicense=ABS-Generic,CardName=ABS-Generic,Color=(0.9019607843137255, 0.8588235294117647, 0.5843137254901961, 1.0),Density=1060 kg/m^3,+15 more (map truncated)
  Transparency = 0
FEATURE [App::DocumentObjectGroupPython] MaterialContainer  label="Materials"  # scripted group (container) (typed FeaturePython)
  Group = -> [Material004,Material001,Material006,Material011,Material003,Material009,Material010,Material007,Material008,Material005,Material,Material002,Material012,Material013,Material014,Material015,Material016,Material017,Material018,Material019,Material020]
FEATURE [Part::FeaturePython] Wall404  label="утеплитель стекловолоконный 001"  # Arch/BIM 166 (typed FeaturePython)
  Align = 2
  Area = 9112000
  Base = -> Line1767
  BlockHeight = 250
  BlockLength = 0
  CountBroken = 0
  CountEntire = 0
  Face = 0
  GlobalId = 0Pb3kWXLL62hdiT4yMFPnD
  Height = 2720
  HorizontalArea = 335000
  IfcData = IfcUID=0Pb3kWXLL62hdiT4yMFPnD; attributes={"GlobalId": {"value": "0Pb3kWXLL62hdiT4yMFPnD"}}
  IfcType = 166
  Joint = 0
  Length = 3350
  MakeBlocks = false
  Material = -> Material020
  MoveBase = false
  MoveWithHost = false
  Normal = (0,0,0)
  OffsetFirst = 0
  OffsetSecond = 300
  PerimeterLength = 6900
  Placement = pos=(0,0,3130) rot=(0,0,1;0rad)
  PredefinedType = 0
  VerticalArea = 18768000
  Width = 100
FEATURE [Part::Part2DObjectPython] Circle168  label="Circle169"  # Draft 2D object (typed FeaturePython)
  Area = 0
  FirstAngle = 0
  LastAngle = 0
  MakeFace = false
  Placement = pos=(6136.58,4505.64,0) rot=(0,0,1;0rad)
  Radius = 650
FEATURE [Part::Part2DObjectPython] Rectangle3445  label="Шкаф Cersanit Moduo 40_001"  # Draft 2D object (typed FeaturePython)
  Area = 56000
  ChamferSize = 0
  Columns = 1
  FilletRadius = 0
  Height = 400
  Length = 140
  MakeFace = true
  Placement = pos=(4930,4075,0) rot=(0,0,1;0rad)
  Rows = 1
FEATURE [Part::Part2DObjectPython] Rectangle3446  label="Раковина «Cersanit» Moduo 80 Slim_001"  # Draft 2D object (typed FeaturePython)
  Area = 307914
  ChamferSize = 0
  Columns = 1
  FilletRadius = 10
  Height = 385
  Length = 800
  MakeFace = true
  Placement = pos=(6025,5180,0) rot=(0,0,1;0rad)
  Rows = 1
FEATURE [Part::Part2DObjectPython] Rectangle3448  label="полотенцесушитель"  # Draft 2D object (typed FeaturePython)
  Area = 17500
  ChamferSize = 0
  Columns = 1
  FilletRadius = 0
  Height = 35
  Length = 500
  MakeFace = true
  Placement = pos=(5233.97,3855,0) rot=(0,0,1;0rad)
  Rows = 1
FEATURE [Part::Part2DObjectPython] Wire950  label="СУ#1"  # Draft 2D object (typed FeaturePython)
  Area = 3.0312e+06
  ChamferSize = 0
  Closed = true
  End = (5070,4075,0)
  FilletRadius = 0
  Length = 7280
  MakeFace = true
  Placement = pos=(4930,4075,0) rot=(0,0,1;0rad)
  Points = (8) [(0,0,0),(0,1270,0),(1090,1270,0),(1090,1490,0),(1900,1490,0),(1900,-250,0),(140,-250,0),(140,0,0)]
  Start = (4930,4075,0)
  Subdivisions = 0
FEATURE [Part::Part2DObjectPython] Wire951  label="СУ#1_wire"  # Draft 2D object (typed FeaturePython)
  Area = 0
  ChamferSize = 0
  Closed = true
  End = (5070,4075,0)
  FilletRadius = 0
  Length = 7280
  MakeFace = false
  Placement = pos=(4930,4075,0) rot=(0,0,1;0rad)
  Points = (8) [(0,0,0),(0,1270,0),(1090,1270,0),(1090,1490,0),(1900,1490,0),(1900,-250,0),(140,-250,0),(140,0,0)]
  Start = (4930,4075,0)
  Subdivisions = 0
FEATURE [Part::FeaturePython] Wall232  label="Покрытие СУ №1 плиткой 20мм"  # Arch/BIM 166 (typed FeaturePython)
  Align = 1
  Area = 2.0384e+07
  Base = -> Wire951
  BlockHeight = 0
  BlockLength = 0
  CountBroken = 0
  CountEntire = 0
  Face = 0
  GlobalId = 0fSn5rz2v1yx1CM9t4dxRk
  Height = 2800
  HorizontalArea = 0
  IfcData = IfcUID=0fSn5rz2v1yx1CM9t4dxRk,+2 more (map truncated)
  IfcType = 166
  Joint = 0
  Length = 7280
  MakeBlocks = false
  Material = -> Material005
  MoveBase = false
  MoveWithHost = false
  Normal = (0,0,0)
  OffsetFirst = 0
  OffsetSecond = 0
  PerimeterLength = 0
  PredefinedType = 0
  Subtractions = -> [Structure333,Structure020]
  VerticalArea = 0
  Width = 20
FEATURE [App::DocumentObjectGroup] Group125  label="План 1 этаж 94.1 м2"
  Group = -> [Rectangle008,Rectangle2795,Rectangle2807,Rectangle3095,Rectangle2972,Rectangle2798,Rectangle2717,Rectangle2230,Rectangle2169,Rectangle2231,Rectangle005,Wire760,Rectangle011,Rectangle2695,Rectangle006,Rectangle2730,Rectangle016,Rectangle3074,Rectangle3086,Rectangle3084,Rectangle3079,Rectangle2857,Rectangle3166,Rectangle3168,Rectangle544,Rectangle547,Rectangle545,Rectangle546,Rectangle2837,Arc113,+140 more]
FEATURE [App::DocumentObjectGroup] Group131  label="Draft"
  Group = -> [Group125,Group126,ImagePlane001]
FEATURE [Part::FeaturePython] Structure474  label="Структура023"  # Arch/BIM 52 (typed FeaturePython)
  Base = -> Rectangle3193
  FaceMaker = 0
  Height = 100
  HorizontalArea = 164371
  IfcData = attributes={"GlobalId": {"name": "GlobalId", "type": "IfcGloballyUniqueId", "is_enum": false, "enum_values": []}, "Description": {"... (+484 chars omitted),+1 more (map truncated)
  IfcType = 52
  Length = 0
  MoveBase = false
  MoveWithHost = false
  Nodes = (2) [(6380,5325,0),(6380,5325,100)]
  NodesOffset = 0
  Normal = (0,0,1)
  PerimeterLength = 1781.24
  Placement = pos=(0,0,800) rot=(0,0,1;0rad)
  VerticalArea = 178124
  Width = 100
FEATURE [Part::FeaturePython] Structure475  label="Раковина «Cersanit» Moduo 80 Slim 001"  # Arch/BIM 52 (typed FeaturePython)
  Base = -> Rectangle3446
  FaceMaker = 0
  GlobalId = 2d5W_OQQf2Fxkoe6wMEOb9
  Height = 55
  HorizontalArea = 143543
  IfcData = IfcUID=2d5W_OQQf2Fxkoe6wMEOb9,+2 more (map truncated)
  IfcType = 52
  Length = 0
  Material = -> Material013
  MoveBase = false
  MoveWithHost = false
  Nodes = (2) [(-2856.79,7112.64,0),(-2856.79,7112.64,600)]
  NodesOffset = 0
  Normal = (0,0,1)
  PerimeterLength = 2352.83
  Placement = pos=(0,0,845) rot=(0,0,1;0rad)
  Subtractions = -> [Structure474]
  VerticalArea = 227374
  Width = 100
FEATURE [Part::FeaturePython] Structure476  label="Раковина «Cersanit» Moduo 80 Slim (тумба)"  # Arch/BIM 52 (typed FeaturePython)
  Base = -> Rectangle3446
  FaceMaker = 0
  GlobalId = 2d5W_OQQf2Fxkoe6wMEOb9
  Height = 570
  HorizontalArea = 307914
  IfcData = IfcUID=2d5W_OQQf2Fxkoe6wMEOb9,+2 more (map truncated)
  IfcType = 52
  Length = 0
  Material = -> Material013
  MoveBase = false
  MoveWithHost = false
  Nodes = (2) [(-2856.79,7112.64,0),(-2856.79,7112.64,600)]
  NodesOffset = 0
  Normal = (0,0,-1)
  PerimeterLength = 2352.83
  Placement = pos=(0,0,845) rot=(0,0,1;0rad)
  VerticalArea = 1.34111e+06
  Width = 100
FEATURE [Part::FeaturePython] Structure477  label="Шкаф Cersanit Moduo 40_002"  # Arch/BIM 52 (typed FeaturePython)
  Base = -> Rectangle3445
  FaceMaker = 0
  GlobalId = 2d5W_OQQf2Fxkoe6wMEOb9
  Height = 800
  HorizontalArea = 56000
  IfcData = IfcUID=2d5W_OQQf2Fxkoe6wMEOb9,+2 more (map truncated)
  IfcType = 52
  Length = 0
  Material = -> Material013
  MoveBase = false
  MoveWithHost = false
  Nodes = (2) [(-2856.79,7112.64,0),(-2856.79,7112.64,600)]
  NodesOffset = 0
  Normal = (0,0,-1)
  PerimeterLength = 1080
  Placement = pos=(0,0,1075) rot=(0,0,1;0rad)
  VerticalArea = 864000
  Width = 100
FEATURE [Part::FeaturePython] Structure478  label="Шкаф Cersanit Moduo 40_003"  # Arch/BIM 52 (typed FeaturePython)
  Base = -> Rectangle3445
  FaceMaker = 0
  GlobalId = 2d5W_OQQf2Fxkoe6wMEOb9
  Height = 800
  HorizontalArea = 56000
  IfcData = IfcUID=2d5W_OQQf2Fxkoe6wMEOb9,+2 more (map truncated)
  IfcType = 52
  Length = 0
  Material = -> Material013
  MoveBase = false
  MoveWithHost = false
  Nodes = (2) [(-2856.79,7112.64,0),(-2856.79,7112.64,600)]
  NodesOffset = 0
  Normal = (0,0,1)
  PerimeterLength = 1080
  Placement = pos=(0,0,1075) rot=(0,0,1;0rad)
  VerticalArea = 864000
  Width = 100
FEATURE [App::GeometryPython] BuildingPart048  label="Сантехника и мебель в ванной"  # Arch/BIM 52 (typed FeaturePython)
  Area = 3112200
  GlobalId = 2oHchfV$vBmBbFkTdd7Thp
  Group = -> [Structure343,Wall240,Component030,Component031,Structure459,Component170,Structure475,Structure476,Structure477,Structure478]
  Height = 0
  HeightPropagate = true
  IfcData = IfcUID=2oHchfV$vBmBbFkTdd7Thp,attributes={"GlobalId": {"value": "2oHchfV$vBmBbFkTdd7Thp"}},+1 more (map truncated)
  IfcType = 52
  LevelOffset = 0
FEATURE [App::GeometryPython] BuildingPart049  label="Обстановка"  # Arch/BIM 52 (typed FeaturePython)
  Area = 3112200
  GlobalId = 01a0HsyVr7nurh2jl2zfI$
  Group = -> [BuildingPart047,BuildingPart048,BuildingPart045]
  Height = 0
  HeightPropagate = true
  IfcData = IfcUID=01a0HsyVr7nurh2jl2zfI$,attributes={"GlobalId": {"value": "01a0HsyVr7nurh2jl2zfI$"}},+1 more (map truncated)
  IfcType = 52
  LevelOffset = 0
FEATURE [Part::Part2DObjectPython] Rectangle3449  # Draft 2D object (typed FeaturePython)
  Area = 0
  ChamferSize = 0
  Columns = 1
  FilletRadius = 50
  Height = 300
  Length = 425
  MakeFace = false
  Placement = pos=(5335,7440,0) rot=(0,0,-1;0rad)
  Rows = 1
FEATURE [Part::Part2DObjectPython] Rectangle3450  label="Раковина «Cersanit» Moduo 80 Slim_002"  # Draft 2D object (typed FeaturePython)
  Area = 180794
  ChamferSize = 0
  Columns = 1
  FilletRadius = 70
  Height = 370
  Length = 500
  MakeFace = true
  Placement = pos=(5295,7405,0) rot=(0,0,1;0rad)
  Rows = 1
FEATURE [Part::FeaturePython] Structure479  label="Структура024"  # Arch/BIM 52 (typed FeaturePython)
  Base = -> Rectangle3449
  FaceMaker = 0
  Height = 150
  HorizontalArea = 125354
  IfcData = attributes={"GlobalId": {"name": "GlobalId", "type": "IfcGloballyUniqueId", "is_enum": false, "enum_values": []}, "Description": {"... (+484 chars omitted),+1 more (map truncated)
  IfcType = 52
  Length = 0
  MoveBase = false
  MoveWithHost = false
  Nodes = (2) [(6380,5325,0),(6380,5325,100)]
  NodesOffset = 0
  Normal = (0,0,1)
  PerimeterLength = 1364.16
  Placement = pos=(0,0,890) rot=(0,0,1;0rad)
  VerticalArea = 204624
  Width = 100
FEATURE [Part::FeaturePython] Structure480  label="Раковина «Cersanit» Moduo 80 Slim 002"  # Arch/BIM 52 (typed FeaturePython)
  Base = -> Rectangle3450
  FaceMaker = 0
  GlobalId = 2d5W_OQQf2Fxkoe6wMEOb9
  Height = 70
  HorizontalArea = 180794
  IfcData = IfcUID=2d5W_OQQf2Fxkoe6wMEOb9,+2 more (map truncated)
  IfcType = 52
  Length = 0
  Material = -> Material013
  MoveBase = false
  MoveWithHost = false
  Nodes = (2) [(-2856.79,7112.64,0),(-2856.79,7112.64,600)]
  NodesOffset = 0
  Normal = (0,0,-1)
  PerimeterLength = 1619.82
  Placement = pos=(0,0,955) rot=(0,0,1;0rad)
  Subtractions = -> [Structure479]
  VerticalArea = 202058
  Width = 100
FEATURE [Part::FeaturePython] Wall214  label="Внешняя стена ЛСР 380мм"  # Arch/BIM 166 (typed FeaturePython)
  Align = 0
  Area = 121020000
  Base = -> Rectangle016
  BlockHeight = 231
  BlockLength = 0
  CountBroken = 0
  CountEntire = 0
  Face = 0
  GlobalId = 15i3vb4BrBERo7sMNULkP3
  Height = 3000
  HorizontalArea = 0
  IfcData = IfcUID=15i3vb4BrBERo7sMNULkP3,+2 more (map truncated)
  IfcType = 166
  Joint = 0
  Length = 40340
  MakeBlocks = true
  Material = -> Material004
  MoveBase = false
  MoveWithHost = false
  Normal = (0,0,0)
  OffsetFirst = 0
  OffsetSecond = 0
  PerimeterLength = 0
  Placement = pos=(0,0,-200) rot=(0,0,1;0rad)
  PredefinedType = 0
  Subtractions = -> [Structure315,Structure313,Structure308,Structure304,Structure285,Structure019,Structure016,Structure017,Structure306,Wall270,Wall271,Wall280,Wall276,Wall274,Wall275,Wall279,Wall272,Wall273,Wall285,Wall282,Wall284,Wall287,Wall290,Wall289,Wall283,Wall288,Wall286,Structure480,Structure479]
  VerticalArea = 0
  Width = 380
FEATURE [App::GeometryPython] BuildingPart002  label="Стены несущие"  # Arch/BIM 52 (typed FeaturePython)
  Area = 168045630
  GlobalId = 3CS7VrtqL2RQvRhQ1$1d0X
  Group = -> [Wall004,BuildingPart088,BuildingPart089,BuildingPart096,Wall214]
  Height = 0
  HeightPropagate = true
  IfcData = IfcUID=3CS7VrtqL2RQvRhQ1$1d0X,attributes={"GlobalId": {"value": "3CS7VrtqL2RQvRhQ1$1d0X"}},+1 more (map truncated)
  IfcType = 52
  LevelOffset = 0
FEATURE [Part::Part2DObjectPython] Rectangle3451  label="подоконник_с_умывальником001"  # Draft 2D object (typed FeaturePython)
  ChamferSize = 0
  Columns = 1
  FilletRadius = 0
  Height = 410
  Length = 920
  MakeFace = true
  Placement = pos=(5085,7380,0) rot=(0,0,1;0rad)
  Rows = 1
FEATURE [Part::FeaturePython] Structure481  label="подоконник"  # Arch/BIM 52 (typed FeaturePython)
  Base = -> Rectangle3451
  FaceMaker = 0
  Height = 100
  HorizontalArea = 0
  IfcData = complex_attributes={"OwnerHistory": {}, "IsNestedBy": {}, "IsDecomposedBy": {}, "IsDefinedBy": {}, "ObjectPlacement": {}, "Representation":... (+4 chars omitted)
  IfcType = 52
  Length = 0
  MoveBase = false
  MoveWithHost = false
  Nodes = (2) [(1035,250,0),(1035,250,600)]
  NodesOffset = 0
  Normal = (0,0,-1)
  PerimeterLength = 0
  Placement = pos=(0,0,980) rot=(0,0,1;0rad)
  Subtractions = -> [Structure479,Wall214,Structure480]
  VerticalArea = 0
  Width = 100
FEATURE [Part::FeaturePython] Wall403  label="Покрытие ванная плиткой 20мм001"  # Arch/BIM 166 (typed FeaturePython)
  Align = 1
  Area = 21952000
  Base = -> Wire946
  BlockHeight = 0
  BlockLength = 0
  CountBroken = 0
  CountEntire = 0
  Face = 0
  GlobalId = 0fSn5rz2v1yx1CM9t4dxRk
  Height = 2800
  HorizontalArea = 0
  IfcData = IfcUID=0fSn5rz2v1yx1CM9t4dxRk,+2 more (map truncated)
  IfcType = 166
  Joint = 0
  Length = 7840
  MakeBlocks = false
  Material = -> Material005
  MoveBase = false
  MoveWithHost = false
  Normal = (0,0,0)
  OffsetFirst = 0
  OffsetSecond = 0
  PerimeterLength = 0
  PredefinedType = 0
  Subtractions = -> [Structure141,Structure313,Structure480,Structure479,Structure481]
  VerticalArea = 0
  Width = 20
FEATURE [App::GeometryPython] BuildingPart081  label="Отделка"  # Arch/BIM 52 (typed FeaturePython)
  Area = 3.24296e+08
  GlobalId = 3k8znIZGb8Sep8PACCMQ9v
  Group = -> [Wall232,Wall229,Wall233,Wall234,Wall235,Wall236,Wall237,Wall238,Wall,Wall267,Wall268,Wall269,Wall347,Wall346,Component143,Wall349,Wall403,Structure481,Structure480]
  Height = 0
  HeightPropagate = true
  IfcData = IfcUID=3k8znIZGb8Sep8PACCMQ9v,+2 more (map truncated)
  IfcType = 52
  LevelOffset = 0
FEATURE [App::GeometryPython] BuildingPart103  label="Уровень первого этажа"  # Arch/BIM 14 (typed FeaturePython)
  Area = 765428630
  CompositionType = 0
  Elevation = 0
  GlobalId = 377tEiMTb6celHDz_UVksa
  Group = -> [BuildingPart101,BuildingPart102,BuildingPart002,BuildingPart005,BuildingPart081,BuildingPart038,BuildingPart014,BuildingPart093,BuildingPart011,BuildingPart087,BuildingPart049]
  Height = 3130
  HeightPropagate = true
  IfcData = IfcUID=377tEiMTb6celHDz_UVksa,+2 more (map truncated)
  IfcType = 14
  LevelOffset = 0
  LongName = Floor
  Placement = pos=(-560,-540,0) rot=(0,0,1;0rad)
  expr: Elevation = .Placement.Base.z
FEATURE [App::GeometryPython] BuildingPart105  label="Индивидуальный жилой дом"  # Arch/BIM 10 (typed FeaturePython)
  Area = 1.15725e+09
  BuildingType = 36
  CompositionType = 0
  ElevationOfRefHeight = 0
  ElevationOfTerrain = 0
  GlobalId = 1wNqu2gmH0$Q5UGcgb9xOg
  Group = -> [App__DocumentObjectGroup,BuildingPart103,BuildingPart104,WPProxy,WPProxy001,BuildingPart109,BuildingPart106]
  Height = 0
  HeightPropagate = true
  IfcData = IfcUID=1wNqu2gmH0$Q5UGcgb9xOg,+2 more (map truncated)
  IfcType = 10
  LevelOffset = 0
  LongName = Building
  Placement = pos=(-560,-540,0) rot=(0,0,1;0rad)
FEATURE [Part::FeaturePython] Site001  label="Участок ИЖС"  # Arch/BIM 117 (typed FeaturePython)
  AdditionVolume = 0
  CompositionType = 0
  Declination = 0
  Elevation = 0
  ExtrusionVector = (0,0,-100000)
  GlobalId = 0q3YkvPDD0KRQl3VYghQdF
  Group = -> [BuildingPart105]
  IfcData = IfcUID=0q3YkvPDD0KRQl3VYghQdF,+2 more (map truncated)
  IfcType = 117
  Latitude = 0
  LongName = Site
  Longitude = 0
  OriginOffset = (0,0,0)
  Perimeter = 0
  ProjectedArea = 0
  RefElevation = 0
  RemoveSplitter = false
  SubtractionVolume = 0
  TimeZone = 0
  expr: RefElevation = .Elevation.Value
FEATURE [App::FeaturePython] Section006  label="Section 1st floor plan"  # WARN: FeaturePython — macro-defined, semantics opaque (R4)
  Clip = false
  Objects = -> [BuildingPart101,BuildingPart102,BuildingPart002,BuildingPart005,BuildingPart081,BuildingPart093,BuildingPart011,BuildingPart087,BuildingPart049,BuildingPart090]
  OnlySolids = true
  Placement = pos=(6260,3730,1600) rot=(0,0,1;0rad)
  UseMaterialColorForFill = true
FEATURE [TechDraw::DrawViewArch] ArchView007
  AllOn = true
  CutLineWidth = 0.1
  FillSpaces = false
  FontSize = 7
  JoinArch = false
  LineWidth = 0.1
  LockPosition = true
  RenderMode = 0
  Rotation = 0
  Scale = 0.02
  ScaleType = 2
  ShowFill = true
  ShowHidden = false
  Source = -> Section006
  Symbol = <blob: 686580 chars omitted>
  X = 210
  Y = 150
FEATURE [TechDraw::DrawPage] Page002  label="План 1 этаж"
  KeepUpdated = false
  NextBalloonIndex = 1
  ProjectionType = 0
  Template = -> Template002
  Views = -> [Annotation007,ArchView007,DraftView001]
FEATURE [App::FeaturePython] Section  label="Section A-A"  # WARN: FeaturePython — macro-defined, semantics opaque (R4)
  Clip = true
  Objects = -> [BuildingPart103,BuildingPart104,BuildingPart100,BuildingPart106]
  OnlySolids = true
  Placement = pos=(9950,3730,3690.5) rot=(0.57735,0.57735,0.57735;2.0944rad)
  UseMaterialColorForFill = true
FEATURE [TechDraw::DrawViewArch] ArchView
  AllOn = true
  CutLineWidth = 0.1
  FillSpaces = false
  FontSize = 8
  JoinArch = false
  LineWidth = 0.1
  LockPosition = true
  RenderMode = 0
  Rotation = 90
  Scale = 0.02
  ScaleType = 2
  ShowFill = true
  ShowHidden = false
  Source = -> Section
  Symbol = <blob: 758131 chars omitted>
  X = 224.182
  Y = 160.176
FEATURE [TechDraw::DrawPage] Page001  label="Разрез по А-А"
  KeepUpdated = false
  NextBalloonIndex = 1
  ProjectionType = 0
  Scale = 0.02
  Template = -> Template001
  Views = -> [Annotation008,ArchView,Annotation009,Annotation010,Annotation011,Annotation012,LeaderLine,LeaderLine001,LeaderLine002,LeaderLine003,Annotation013,Annotation014,Annotation015,Annotation016,LeaderLine004,Annotation017,Annotation018,Annotation019,Annotation020,Annotation021,Annotation022,Annotation023,Annotation024,Annotation025,Annotation026,LeaderLine005,LeaderLine006,LeaderLine007,LeaderLine008,+12 more]
FEATURE [App::FeaturePython] Section008  label="Section B-B"  # WARN: FeaturePython — macro-defined, semantics opaque (R4)
  Clip = true
  Objects = -> [BuildingPart103,BuildingPart104,BuildingPart106]
  OnlySolids = true
  Placement = pos=(7800,3730,3630.5) rot=(0.57735,0.57735,0.57735;2.0944rad)
  UseMaterialColorForFill = true
FEATURE [App::DocumentObjectGroup] Group129  label="Sections"
  Group = -> [Section006,Section,Section008,Section007]
FEATURE [TechDraw::DrawViewArch] ArchView009
  AllOn = true
  CutLineWidth = 0.1
  FillSpaces = false
  FontSize = 8
  JoinArch = false
  LineWidth = 0.1
  LockPosition = true
  RenderMode = 0
  Rotation = 90
  Scale = 0.02
  ScaleType = 2
  ShowFill = true
  ShowHidden = false
  Source = -> Section008
  Symbol = <blob: 1723092 chars omitted>
  X = 224.18
  Y = 160.18
FEATURE [TechDraw::DrawPage] Page005  label="Разрез по B-B"
  KeepUpdated = false
  NextBalloonIndex = 1
  ProjectionType = 0
  Scale = 0.02
  Template = -> Template005
  Views = -> [ArchView009,Annotation037]
FEATURE [App::DocumentObjectGroup] Group130  label="Листы проекта для печати"
  Group = -> [Group127,Group129,Page004,Page006,Page,Page002,Page003,Page001,Page005]
note: 58 file-system paths scrubbed to <path> (originals preserved in the JSON sidecar)
